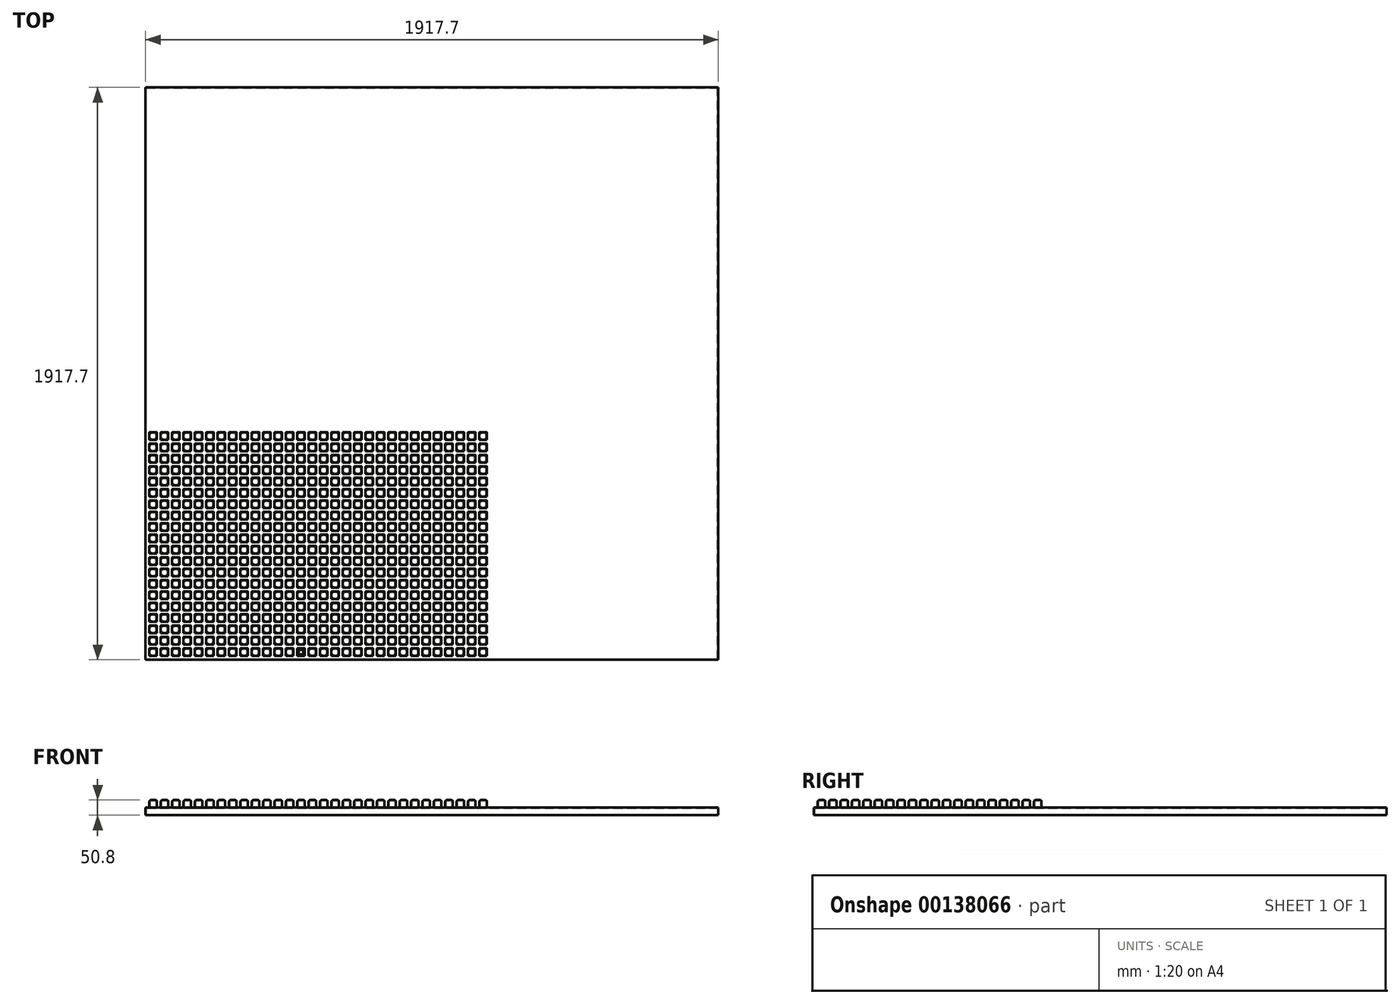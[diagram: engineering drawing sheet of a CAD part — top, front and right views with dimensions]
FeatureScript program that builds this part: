
annotation { "Feature Type Name" : "Feature", "Feature Type Description" : "" }
export const myFeature = defineFeature(function(context is Context, id is Id, definition is map)
    precondition{}
    {
        {
            var Q0;
            Q0=qCreatedBy(makeId("Top.planeOp"),FACE);
            var sketch = newSketch(context, id + "F0", { "sketchPlane" : qUnion([Q0])});
            skLineSegment(sketch, "E0.bottom", {"start": v(0, 0) * mm, "end": v(1917.7, 0) * mm});
            skLineSegment(sketch, "E0.top", {"start": v(0, 1917.7) * mm, "end": v(1917.7, 1917.7) * mm});
            skLineSegment(sketch, "E0.left", {"start": v(0, 0) * mm, "end": v(0, 1917.7) * mm});
            skLineSegment(sketch, "E0.right", {"start": v(1917.7, 0) * mm, "end": v(1917.7, 1917.7) * mm});
            skSolve(sketch);
        }
        {
            var Q0;
            Q0=makeQuery(id+"F0.imprint","IMPRINT",FACE,{"disambiguationData":[TD([[makeQuery(id+"F0.imprint","IMPRINT",EDGE,{"derivedFrom":sQuery(id+"F0.wireOp",EDGE,"E0.bottom")}),1.0]])]});
            extrude(context, id + "F1", {"entities" : qUnion([Q0]), "depth" : 25.4 * mm});
        }
        {
            var Q0;
            Q0=makeQuery(id+"F1.opExtrude","CAP_FACE",FACE,{"disambiguationData":[OSD([sQuery(id+"F0.wireOp",EDGE,"E0.bottom"),sQuery(id+"F0.wireOp",EDGE,"E0.top"),sQuery(id+"F0.wireOp",EDGE,"E0.left"),sQuery(id+"F0.wireOp",EDGE,"E0.right")])],"isStart":false});
            var sketch = newSketch(context, id + "F2", { "sketchPlane" : qUnion([Q0])});
            skLineSegment(sketch, "E1.bottom", {"start": v(12.7, 12.7) * mm, "end": v(38.1, 12.7) * mm});
            skLineSegment(sketch, "E1.top", {"start": v(12.7, 38.1) * mm, "end": v(38.1, 38.1) * mm});
            skLineSegment(sketch, "E1.left", {"start": v(12.7, 12.7) * mm, "end": v(12.7, 38.1) * mm});
            skLineSegment(sketch, "E1.right", {"start": v(38.1, 12.7) * mm, "end": v(38.1, 38.1) * mm});
            skLineSegment(sketch, "E2.0.1.0", {"start": v(38.1, 50.8) * mm, "end": v(38.1, 76.2) * mm});
            skLineSegment(sketch, "E2.0.1.1", {"start": v(12.7, 76.2) * mm, "end": v(38.1, 76.2) * mm});
            skLineSegment(sketch, "E2.0.1.2", {"start": v(12.7, 50.8) * mm, "end": v(38.1, 50.8) * mm});
            skLineSegment(sketch, "E2.0.1.3", {"start": v(12.7, 50.8) * mm, "end": v(12.7, 76.2) * mm});
            skLineSegment(sketch, "E2.0.2.0", {"start": v(38.1, 88.9) * mm, "end": v(38.1, 114.3) * mm});
            skLineSegment(sketch, "E2.0.2.1", {"start": v(12.7, 114.3) * mm, "end": v(38.1, 114.3) * mm});
            skLineSegment(sketch, "E2.0.2.2", {"start": v(12.7, 88.9) * mm, "end": v(38.1, 88.9) * mm});
            skLineSegment(sketch, "E2.0.2.3", {"start": v(12.7, 88.9) * mm, "end": v(12.7, 114.3) * mm});
            skLineSegment(sketch, "E2.0.3.0", {"start": v(38.1, 127) * mm, "end": v(38.1, 152.4) * mm});
            skLineSegment(sketch, "E2.0.3.1", {"start": v(12.7, 152.4) * mm, "end": v(38.1, 152.4) * mm});
            skLineSegment(sketch, "E2.0.3.2", {"start": v(12.7, 127) * mm, "end": v(38.1, 127) * mm});
            skLineSegment(sketch, "E2.0.3.3", {"start": v(12.7, 127) * mm, "end": v(12.7, 152.4) * mm});
            skLineSegment(sketch, "E2.0.4.0", {"start": v(38.1, 165.1) * mm, "end": v(38.1, 190.5) * mm});
            skLineSegment(sketch, "E2.0.4.1", {"start": v(12.7, 190.5) * mm, "end": v(38.1, 190.5) * mm});
            skLineSegment(sketch, "E2.0.4.2", {"start": v(12.7, 165.1) * mm, "end": v(38.1, 165.1) * mm});
            skLineSegment(sketch, "E2.0.4.3", {"start": v(12.7, 165.1) * mm, "end": v(12.7, 190.5) * mm});
            skLineSegment(sketch, "E2.0.5.0", {"start": v(38.1, 203.2) * mm, "end": v(38.1, 228.6) * mm});
            skLineSegment(sketch, "E2.0.5.1", {"start": v(12.7, 228.6) * mm, "end": v(38.1, 228.6) * mm});
            skLineSegment(sketch, "E2.0.5.2", {"start": v(12.7, 203.2) * mm, "end": v(38.1, 203.2) * mm});
            skLineSegment(sketch, "E2.0.5.3", {"start": v(12.7, 203.2) * mm, "end": v(12.7, 228.6) * mm});
            skLineSegment(sketch, "E2.0.6.0", {"start": v(38.1, 241.3) * mm, "end": v(38.1, 266.7) * mm});
            skLineSegment(sketch, "E2.0.6.1", {"start": v(12.7, 266.7) * mm, "end": v(38.1, 266.7) * mm});
            skLineSegment(sketch, "E2.0.6.2", {"start": v(12.7, 241.3) * mm, "end": v(38.1, 241.3) * mm});
            skLineSegment(sketch, "E2.0.6.3", {"start": v(12.7, 241.3) * mm, "end": v(12.7, 266.7) * mm});
            skLineSegment(sketch, "E2.0.7.0", {"start": v(38.1, 279.4) * mm, "end": v(38.1, 304.8) * mm});
            skLineSegment(sketch, "E2.0.7.1", {"start": v(12.7, 304.8) * mm, "end": v(38.1, 304.8) * mm});
            skLineSegment(sketch, "E2.0.7.2", {"start": v(12.7, 279.4) * mm, "end": v(38.1, 279.4) * mm});
            skLineSegment(sketch, "E2.0.7.3", {"start": v(12.7, 279.4) * mm, "end": v(12.7, 304.8) * mm});
            skLineSegment(sketch, "E2.0.8.0", {"start": v(38.1, 317.5) * mm, "end": v(38.1, 342.9) * mm});
            skLineSegment(sketch, "E2.0.8.1", {"start": v(12.7, 342.9) * mm, "end": v(38.1, 342.9) * mm});
            skLineSegment(sketch, "E2.0.8.2", {"start": v(12.7, 317.5) * mm, "end": v(38.1, 317.5) * mm});
            skLineSegment(sketch, "E2.0.8.3", {"start": v(12.7, 317.5) * mm, "end": v(12.7, 342.9) * mm});
            skLineSegment(sketch, "E2.0.9.0", {"start": v(38.1, 355.6) * mm, "end": v(38.1, 381) * mm});
            skLineSegment(sketch, "E2.0.9.1", {"start": v(12.7, 381) * mm, "end": v(38.1, 381) * mm});
            skLineSegment(sketch, "E2.0.9.2", {"start": v(12.7, 355.6) * mm, "end": v(38.1, 355.6) * mm});
            skLineSegment(sketch, "E2.0.9.3", {"start": v(12.7, 355.6) * mm, "end": v(12.7, 381) * mm});
            skLineSegment(sketch, "E2.0.10.0", {"start": v(38.1, 393.7) * mm, "end": v(38.1, 419.1) * mm});
            skLineSegment(sketch, "E2.0.10.1", {"start": v(12.7, 419.1) * mm, "end": v(38.1, 419.1) * mm});
            skLineSegment(sketch, "E2.0.10.2", {"start": v(12.7, 393.7) * mm, "end": v(38.1, 393.7) * mm});
            skLineSegment(sketch, "E2.0.10.3", {"start": v(12.7, 393.7) * mm, "end": v(12.7, 419.1) * mm});
            skLineSegment(sketch, "E2.0.11.0", {"start": v(38.1, 431.8) * mm, "end": v(38.1, 457.2) * mm});
            skLineSegment(sketch, "E2.0.11.1", {"start": v(12.7, 457.2) * mm, "end": v(38.1, 457.2) * mm});
            skLineSegment(sketch, "E2.0.11.2", {"start": v(12.7, 431.8) * mm, "end": v(38.1, 431.8) * mm});
            skLineSegment(sketch, "E2.0.11.3", {"start": v(12.7, 431.8) * mm, "end": v(12.7, 457.2) * mm});
            skLineSegment(sketch, "E2.0.12.0", {"start": v(38.1, 469.9) * mm, "end": v(38.1, 495.3) * mm});
            skLineSegment(sketch, "E2.0.12.1", {"start": v(12.7, 495.3) * mm, "end": v(38.1, 495.3) * mm});
            skLineSegment(sketch, "E2.0.12.2", {"start": v(12.7, 469.9) * mm, "end": v(38.1, 469.9) * mm});
            skLineSegment(sketch, "E2.0.12.3", {"start": v(12.7, 469.9) * mm, "end": v(12.7, 495.3) * mm});
            skLineSegment(sketch, "E2.0.13.0", {"start": v(38.1, 508) * mm, "end": v(38.1, 533.4) * mm});
            skLineSegment(sketch, "E2.0.13.1", {"start": v(12.7, 533.4) * mm, "end": v(38.1, 533.4) * mm});
            skLineSegment(sketch, "E2.0.13.2", {"start": v(12.7, 508) * mm, "end": v(38.1, 508) * mm});
            skLineSegment(sketch, "E2.0.13.3", {"start": v(12.7, 508) * mm, "end": v(12.7, 533.4) * mm});
            skLineSegment(sketch, "E2.0.14.0", {"start": v(38.1, 546.1) * mm, "end": v(38.1, 571.5) * mm});
            skLineSegment(sketch, "E2.0.14.1", {"start": v(12.7, 571.5) * mm, "end": v(38.1, 571.5) * mm});
            skLineSegment(sketch, "E2.0.14.2", {"start": v(12.7, 546.1) * mm, "end": v(38.1, 546.1) * mm});
            skLineSegment(sketch, "E2.0.14.3", {"start": v(12.7, 546.1) * mm, "end": v(12.7, 571.5) * mm});
            skLineSegment(sketch, "E2.0.15.0", {"start": v(38.1, 584.2) * mm, "end": v(38.1, 609.6) * mm});
            skLineSegment(sketch, "E2.0.15.1", {"start": v(12.7, 609.6) * mm, "end": v(38.1, 609.6) * mm});
            skLineSegment(sketch, "E2.0.15.2", {"start": v(12.7, 584.2) * mm, "end": v(38.1, 584.2) * mm});
            skLineSegment(sketch, "E2.0.15.3", {"start": v(12.7, 584.2) * mm, "end": v(12.7, 609.6) * mm});
            skLineSegment(sketch, "E2.0.16.0", {"start": v(38.1, 622.3) * mm, "end": v(38.1, 647.7) * mm});
            skLineSegment(sketch, "E2.0.16.1", {"start": v(12.7, 647.7) * mm, "end": v(38.1, 647.7) * mm});
            skLineSegment(sketch, "E2.0.16.2", {"start": v(12.7, 622.3) * mm, "end": v(38.1, 622.3) * mm});
            skLineSegment(sketch, "E2.0.16.3", {"start": v(12.7, 622.3) * mm, "end": v(12.7, 647.7) * mm});
            skLineSegment(sketch, "E2.0.17.0", {"start": v(38.1, 660.4) * mm, "end": v(38.1, 685.8) * mm});
            skLineSegment(sketch, "E2.0.17.1", {"start": v(12.7, 685.8) * mm, "end": v(38.1, 685.8) * mm});
            skLineSegment(sketch, "E2.0.17.2", {"start": v(12.7, 660.4) * mm, "end": v(38.1, 660.4) * mm});
            skLineSegment(sketch, "E2.0.17.3", {"start": v(12.7, 660.4) * mm, "end": v(12.7, 685.8) * mm});
            skLineSegment(sketch, "E2.0.18.0", {"start": v(38.1, 698.5) * mm, "end": v(38.1, 723.9) * mm});
            skLineSegment(sketch, "E2.0.18.1", {"start": v(12.7, 723.9) * mm, "end": v(38.1, 723.9) * mm});
            skLineSegment(sketch, "E2.0.18.2", {"start": v(12.7, 698.5) * mm, "end": v(38.1, 698.5) * mm});
            skLineSegment(sketch, "E2.0.18.3", {"start": v(12.7, 698.5) * mm, "end": v(12.7, 723.9) * mm});
            skLineSegment(sketch, "E2.0.19.0", {"start": v(38.1, 736.6) * mm, "end": v(38.1, 762) * mm});
            skLineSegment(sketch, "E2.0.19.1", {"start": v(12.7, 762) * mm, "end": v(38.1, 762) * mm});
            skLineSegment(sketch, "E2.0.19.2", {"start": v(12.7, 736.6) * mm, "end": v(38.1, 736.6) * mm});
            skLineSegment(sketch, "E2.0.19.3", {"start": v(12.7, 736.6) * mm, "end": v(12.7, 762) * mm});
            skLineSegment(sketch, "E2.1.0.0", {"start": v(76.2, 12.7) * mm, "end": v(76.2, 38.1) * mm});
            skLineSegment(sketch, "E2.1.0.1", {"start": v(50.8, 38.1) * mm, "end": v(76.2, 38.1) * mm});
            skLineSegment(sketch, "E2.1.0.2", {"start": v(50.8, 12.7) * mm, "end": v(76.2, 12.7) * mm});
            skLineSegment(sketch, "E2.1.0.3", {"start": v(50.8, 12.7) * mm, "end": v(50.8, 38.1) * mm});
            skLineSegment(sketch, "E2.1.1.0", {"start": v(76.2, 50.8) * mm, "end": v(76.2, 76.2) * mm});
            skLineSegment(sketch, "E2.1.1.1", {"start": v(50.8, 76.2) * mm, "end": v(76.2, 76.2) * mm});
            skLineSegment(sketch, "E2.1.1.2", {"start": v(50.8, 50.8) * mm, "end": v(76.2, 50.8) * mm});
            skLineSegment(sketch, "E2.1.1.3", {"start": v(50.8, 50.8) * mm, "end": v(50.8, 76.2) * mm});
            skLineSegment(sketch, "E2.1.2.0", {"start": v(76.2, 88.9) * mm, "end": v(76.2, 114.3) * mm});
            skLineSegment(sketch, "E2.1.2.1", {"start": v(50.8, 114.3) * mm, "end": v(76.2, 114.3) * mm});
            skLineSegment(sketch, "E2.1.2.2", {"start": v(50.8, 88.9) * mm, "end": v(76.2, 88.9) * mm});
            skLineSegment(sketch, "E2.1.2.3", {"start": v(50.8, 88.9) * mm, "end": v(50.8, 114.3) * mm});
            skLineSegment(sketch, "E2.1.3.0", {"start": v(76.2, 127) * mm, "end": v(76.2, 152.4) * mm});
            skLineSegment(sketch, "E2.1.3.1", {"start": v(50.8, 152.4) * mm, "end": v(76.2, 152.4) * mm});
            skLineSegment(sketch, "E2.1.3.2", {"start": v(50.8, 127) * mm, "end": v(76.2, 127) * mm});
            skLineSegment(sketch, "E2.1.3.3", {"start": v(50.8, 127) * mm, "end": v(50.8, 152.4) * mm});
            skLineSegment(sketch, "E2.1.4.0", {"start": v(76.2, 165.1) * mm, "end": v(76.2, 190.5) * mm});
            skLineSegment(sketch, "E2.1.4.1", {"start": v(50.8, 190.5) * mm, "end": v(76.2, 190.5) * mm});
            skLineSegment(sketch, "E2.1.4.2", {"start": v(50.8, 165.1) * mm, "end": v(76.2, 165.1) * mm});
            skLineSegment(sketch, "E2.1.4.3", {"start": v(50.8, 165.1) * mm, "end": v(50.8, 190.5) * mm});
            skLineSegment(sketch, "E2.1.5.0", {"start": v(76.2, 203.2) * mm, "end": v(76.2, 228.6) * mm});
            skLineSegment(sketch, "E2.1.5.1", {"start": v(50.8, 228.6) * mm, "end": v(76.2, 228.6) * mm});
            skLineSegment(sketch, "E2.1.5.2", {"start": v(50.8, 203.2) * mm, "end": v(76.2, 203.2) * mm});
            skLineSegment(sketch, "E2.1.5.3", {"start": v(50.8, 203.2) * mm, "end": v(50.8, 228.6) * mm});
            skLineSegment(sketch, "E2.1.6.0", {"start": v(76.2, 241.3) * mm, "end": v(76.2, 266.7) * mm});
            skLineSegment(sketch, "E2.1.6.1", {"start": v(50.8, 266.7) * mm, "end": v(76.2, 266.7) * mm});
            skLineSegment(sketch, "E2.1.6.2", {"start": v(50.8, 241.3) * mm, "end": v(76.2, 241.3) * mm});
            skLineSegment(sketch, "E2.1.6.3", {"start": v(50.8, 241.3) * mm, "end": v(50.8, 266.7) * mm});
            skLineSegment(sketch, "E2.1.7.0", {"start": v(76.2, 279.4) * mm, "end": v(76.2, 304.8) * mm});
            skLineSegment(sketch, "E2.1.7.1", {"start": v(50.8, 304.8) * mm, "end": v(76.2, 304.8) * mm});
            skLineSegment(sketch, "E2.1.7.2", {"start": v(50.8, 279.4) * mm, "end": v(76.2, 279.4) * mm});
            skLineSegment(sketch, "E2.1.7.3", {"start": v(50.8, 279.4) * mm, "end": v(50.8, 304.8) * mm});
            skLineSegment(sketch, "E2.1.8.0", {"start": v(76.2, 317.5) * mm, "end": v(76.2, 342.9) * mm});
            skLineSegment(sketch, "E2.1.8.1", {"start": v(50.8, 342.9) * mm, "end": v(76.2, 342.9) * mm});
            skLineSegment(sketch, "E2.1.8.2", {"start": v(50.8, 317.5) * mm, "end": v(76.2, 317.5) * mm});
            skLineSegment(sketch, "E2.1.8.3", {"start": v(50.8, 317.5) * mm, "end": v(50.8, 342.9) * mm});
            skLineSegment(sketch, "E2.1.9.0", {"start": v(76.2, 355.6) * mm, "end": v(76.2, 381) * mm});
            skLineSegment(sketch, "E2.1.9.1", {"start": v(50.8, 381) * mm, "end": v(76.2, 381) * mm});
            skLineSegment(sketch, "E2.1.9.2", {"start": v(50.8, 355.6) * mm, "end": v(76.2, 355.6) * mm});
            skLineSegment(sketch, "E2.1.9.3", {"start": v(50.8, 355.6) * mm, "end": v(50.8, 381) * mm});
            skLineSegment(sketch, "E2.1.10.0", {"start": v(76.2, 393.7) * mm, "end": v(76.2, 419.1) * mm});
            skLineSegment(sketch, "E2.1.10.1", {"start": v(50.8, 419.1) * mm, "end": v(76.2, 419.1) * mm});
            skLineSegment(sketch, "E2.1.10.2", {"start": v(50.8, 393.7) * mm, "end": v(76.2, 393.7) * mm});
            skLineSegment(sketch, "E2.1.10.3", {"start": v(50.8, 393.7) * mm, "end": v(50.8, 419.1) * mm});
            skLineSegment(sketch, "E2.1.11.0", {"start": v(76.2, 431.8) * mm, "end": v(76.2, 457.2) * mm});
            skLineSegment(sketch, "E2.1.11.1", {"start": v(50.8, 457.2) * mm, "end": v(76.2, 457.2) * mm});
            skLineSegment(sketch, "E2.1.11.2", {"start": v(50.8, 431.8) * mm, "end": v(76.2, 431.8) * mm});
            skLineSegment(sketch, "E2.1.11.3", {"start": v(50.8, 431.8) * mm, "end": v(50.8, 457.2) * mm});
            skLineSegment(sketch, "E2.1.12.0", {"start": v(76.2, 469.9) * mm, "end": v(76.2, 495.3) * mm});
            skLineSegment(sketch, "E2.1.12.1", {"start": v(50.8, 495.3) * mm, "end": v(76.2, 495.3) * mm});
            skLineSegment(sketch, "E2.1.12.2", {"start": v(50.8, 469.9) * mm, "end": v(76.2, 469.9) * mm});
            skLineSegment(sketch, "E2.1.12.3", {"start": v(50.8, 469.9) * mm, "end": v(50.8, 495.3) * mm});
            skLineSegment(sketch, "E2.1.13.0", {"start": v(76.2, 508) * mm, "end": v(76.2, 533.4) * mm});
            skLineSegment(sketch, "E2.1.13.1", {"start": v(50.8, 533.4) * mm, "end": v(76.2, 533.4) * mm});
            skLineSegment(sketch, "E2.1.13.2", {"start": v(50.8, 508) * mm, "end": v(76.2, 508) * mm});
            skLineSegment(sketch, "E2.1.13.3", {"start": v(50.8, 508) * mm, "end": v(50.8, 533.4) * mm});
            skLineSegment(sketch, "E2.1.14.0", {"start": v(76.2, 546.1) * mm, "end": v(76.2, 571.5) * mm});
            skLineSegment(sketch, "E2.1.14.1", {"start": v(50.8, 571.5) * mm, "end": v(76.2, 571.5) * mm});
            skLineSegment(sketch, "E2.1.14.2", {"start": v(50.8, 546.1) * mm, "end": v(76.2, 546.1) * mm});
            skLineSegment(sketch, "E2.1.14.3", {"start": v(50.8, 546.1) * mm, "end": v(50.8, 571.5) * mm});
            skLineSegment(sketch, "E2.1.15.0", {"start": v(76.2, 584.2) * mm, "end": v(76.2, 609.6) * mm});
            skLineSegment(sketch, "E2.1.15.1", {"start": v(50.8, 609.6) * mm, "end": v(76.2, 609.6) * mm});
            skLineSegment(sketch, "E2.1.15.2", {"start": v(50.8, 584.2) * mm, "end": v(76.2, 584.2) * mm});
            skLineSegment(sketch, "E2.1.15.3", {"start": v(50.8, 584.2) * mm, "end": v(50.8, 609.6) * mm});
            skLineSegment(sketch, "E2.1.16.0", {"start": v(76.2, 622.3) * mm, "end": v(76.2, 647.7) * mm});
            skLineSegment(sketch, "E2.1.16.1", {"start": v(50.8, 647.7) * mm, "end": v(76.2, 647.7) * mm});
            skLineSegment(sketch, "E2.1.16.2", {"start": v(50.8, 622.3) * mm, "end": v(76.2, 622.3) * mm});
            skLineSegment(sketch, "E2.1.16.3", {"start": v(50.8, 622.3) * mm, "end": v(50.8, 647.7) * mm});
            skLineSegment(sketch, "E2.1.17.0", {"start": v(76.2, 660.4) * mm, "end": v(76.2, 685.8) * mm});
            skLineSegment(sketch, "E2.1.17.1", {"start": v(50.8, 685.8) * mm, "end": v(76.2, 685.8) * mm});
            skLineSegment(sketch, "E2.1.17.2", {"start": v(50.8, 660.4) * mm, "end": v(76.2, 660.4) * mm});
            skLineSegment(sketch, "E2.1.17.3", {"start": v(50.8, 660.4) * mm, "end": v(50.8, 685.8) * mm});
            skLineSegment(sketch, "E2.1.18.0", {"start": v(76.2, 698.5) * mm, "end": v(76.2, 723.9) * mm});
            skLineSegment(sketch, "E2.1.18.1", {"start": v(50.8, 723.9) * mm, "end": v(76.2, 723.9) * mm});
            skLineSegment(sketch, "E2.1.18.2", {"start": v(50.8, 698.5) * mm, "end": v(76.2, 698.5) * mm});
            skLineSegment(sketch, "E2.1.18.3", {"start": v(50.8, 698.5) * mm, "end": v(50.8, 723.9) * mm});
            skLineSegment(sketch, "E2.1.19.0", {"start": v(76.2, 736.6) * mm, "end": v(76.2, 762) * mm});
            skLineSegment(sketch, "E2.1.19.1", {"start": v(50.8, 762) * mm, "end": v(76.2, 762) * mm});
            skLineSegment(sketch, "E2.1.19.2", {"start": v(50.8, 736.6) * mm, "end": v(76.2, 736.6) * mm});
            skLineSegment(sketch, "E2.1.19.3", {"start": v(50.8, 736.6) * mm, "end": v(50.8, 762) * mm});
            skLineSegment(sketch, "E2.2.0.0", {"start": v(114.3, 12.7) * mm, "end": v(114.3, 38.1) * mm});
            skLineSegment(sketch, "E2.2.0.1", {"start": v(88.9, 38.1) * mm, "end": v(114.3, 38.1) * mm});
            skLineSegment(sketch, "E2.2.0.2", {"start": v(88.9, 12.7) * mm, "end": v(114.3, 12.7) * mm});
            skLineSegment(sketch, "E2.2.0.3", {"start": v(88.9, 12.7) * mm, "end": v(88.9, 38.1) * mm});
            skLineSegment(sketch, "E2.2.1.0", {"start": v(114.3, 50.8) * mm, "end": v(114.3, 76.2) * mm});
            skLineSegment(sketch, "E2.2.1.1", {"start": v(88.9, 76.2) * mm, "end": v(114.3, 76.2) * mm});
            skLineSegment(sketch, "E2.2.1.2", {"start": v(88.9, 50.8) * mm, "end": v(114.3, 50.8) * mm});
            skLineSegment(sketch, "E2.2.1.3", {"start": v(88.9, 50.8) * mm, "end": v(88.9, 76.2) * mm});
            skLineSegment(sketch, "E2.2.2.0", {"start": v(114.3, 88.9) * mm, "end": v(114.3, 114.3) * mm});
            skLineSegment(sketch, "E2.2.2.1", {"start": v(88.9, 114.3) * mm, "end": v(114.3, 114.3) * mm});
            skLineSegment(sketch, "E2.2.2.2", {"start": v(88.9, 88.9) * mm, "end": v(114.3, 88.9) * mm});
            skLineSegment(sketch, "E2.2.2.3", {"start": v(88.9, 88.9) * mm, "end": v(88.9, 114.3) * mm});
            skLineSegment(sketch, "E2.2.3.0", {"start": v(114.3, 127) * mm, "end": v(114.3, 152.4) * mm});
            skLineSegment(sketch, "E2.2.3.1", {"start": v(88.9, 152.4) * mm, "end": v(114.3, 152.4) * mm});
            skLineSegment(sketch, "E2.2.3.2", {"start": v(88.9, 127) * mm, "end": v(114.3, 127) * mm});
            skLineSegment(sketch, "E2.2.3.3", {"start": v(88.9, 127) * mm, "end": v(88.9, 152.4) * mm});
            skLineSegment(sketch, "E2.2.4.0", {"start": v(114.3, 165.1) * mm, "end": v(114.3, 190.5) * mm});
            skLineSegment(sketch, "E2.2.4.1", {"start": v(88.9, 190.5) * mm, "end": v(114.3, 190.5) * mm});
            skLineSegment(sketch, "E2.2.4.2", {"start": v(88.9, 165.1) * mm, "end": v(114.3, 165.1) * mm});
            skLineSegment(sketch, "E2.2.4.3", {"start": v(88.9, 165.1) * mm, "end": v(88.9, 190.5) * mm});
            skLineSegment(sketch, "E2.2.5.0", {"start": v(114.3, 203.2) * mm, "end": v(114.3, 228.6) * mm});
            skLineSegment(sketch, "E2.2.5.1", {"start": v(88.9, 228.6) * mm, "end": v(114.3, 228.6) * mm});
            skLineSegment(sketch, "E2.2.5.2", {"start": v(88.9, 203.2) * mm, "end": v(114.3, 203.2) * mm});
            skLineSegment(sketch, "E2.2.5.3", {"start": v(88.9, 203.2) * mm, "end": v(88.9, 228.6) * mm});
            skLineSegment(sketch, "E2.2.6.0", {"start": v(114.3, 241.3) * mm, "end": v(114.3, 266.7) * mm});
            skLineSegment(sketch, "E2.2.6.1", {"start": v(88.9, 266.7) * mm, "end": v(114.3, 266.7) * mm});
            skLineSegment(sketch, "E2.2.6.2", {"start": v(88.9, 241.3) * mm, "end": v(114.3, 241.3) * mm});
            skLineSegment(sketch, "E2.2.6.3", {"start": v(88.9, 241.3) * mm, "end": v(88.9, 266.7) * mm});
            skLineSegment(sketch, "E2.2.7.0", {"start": v(114.3, 279.4) * mm, "end": v(114.3, 304.8) * mm});
            skLineSegment(sketch, "E2.2.7.1", {"start": v(88.9, 304.8) * mm, "end": v(114.3, 304.8) * mm});
            skLineSegment(sketch, "E2.2.7.2", {"start": v(88.9, 279.4) * mm, "end": v(114.3, 279.4) * mm});
            skLineSegment(sketch, "E2.2.7.3", {"start": v(88.9, 279.4) * mm, "end": v(88.9, 304.8) * mm});
            skLineSegment(sketch, "E2.2.8.0", {"start": v(114.3, 317.5) * mm, "end": v(114.3, 342.9) * mm});
            skLineSegment(sketch, "E2.2.8.1", {"start": v(88.9, 342.9) * mm, "end": v(114.3, 342.9) * mm});
            skLineSegment(sketch, "E2.2.8.2", {"start": v(88.9, 317.5) * mm, "end": v(114.3, 317.5) * mm});
            skLineSegment(sketch, "E2.2.8.3", {"start": v(88.9, 317.5) * mm, "end": v(88.9, 342.9) * mm});
            skLineSegment(sketch, "E2.2.9.0", {"start": v(114.3, 355.6) * mm, "end": v(114.3, 381) * mm});
            skLineSegment(sketch, "E2.2.9.1", {"start": v(88.9, 381) * mm, "end": v(114.3, 381) * mm});
            skLineSegment(sketch, "E2.2.9.2", {"start": v(88.9, 355.6) * mm, "end": v(114.3, 355.6) * mm});
            skLineSegment(sketch, "E2.2.9.3", {"start": v(88.9, 355.6) * mm, "end": v(88.9, 381) * mm});
            skLineSegment(sketch, "E2.2.10.0", {"start": v(114.3, 393.7) * mm, "end": v(114.3, 419.1) * mm});
            skLineSegment(sketch, "E2.2.10.1", {"start": v(88.9, 419.1) * mm, "end": v(114.3, 419.1) * mm});
            skLineSegment(sketch, "E2.2.10.2", {"start": v(88.9, 393.7) * mm, "end": v(114.3, 393.7) * mm});
            skLineSegment(sketch, "E2.2.10.3", {"start": v(88.9, 393.7) * mm, "end": v(88.9, 419.1) * mm});
            skLineSegment(sketch, "E2.2.11.0", {"start": v(114.3, 431.8) * mm, "end": v(114.3, 457.2) * mm});
            skLineSegment(sketch, "E2.2.11.1", {"start": v(88.9, 457.2) * mm, "end": v(114.3, 457.2) * mm});
            skLineSegment(sketch, "E2.2.11.2", {"start": v(88.9, 431.8) * mm, "end": v(114.3, 431.8) * mm});
            skLineSegment(sketch, "E2.2.11.3", {"start": v(88.9, 431.8) * mm, "end": v(88.9, 457.2) * mm});
            skLineSegment(sketch, "E2.2.12.0", {"start": v(114.3, 469.9) * mm, "end": v(114.3, 495.3) * mm});
            skLineSegment(sketch, "E2.2.12.1", {"start": v(88.9, 495.3) * mm, "end": v(114.3, 495.3) * mm});
            skLineSegment(sketch, "E2.2.12.2", {"start": v(88.9, 469.9) * mm, "end": v(114.3, 469.9) * mm});
            skLineSegment(sketch, "E2.2.12.3", {"start": v(88.9, 469.9) * mm, "end": v(88.9, 495.3) * mm});
            skLineSegment(sketch, "E2.2.13.0", {"start": v(114.3, 508) * mm, "end": v(114.3, 533.4) * mm});
            skLineSegment(sketch, "E2.2.13.1", {"start": v(88.9, 533.4) * mm, "end": v(114.3, 533.4) * mm});
            skLineSegment(sketch, "E2.2.13.2", {"start": v(88.9, 508) * mm, "end": v(114.3, 508) * mm});
            skLineSegment(sketch, "E2.2.13.3", {"start": v(88.9, 508) * mm, "end": v(88.9, 533.4) * mm});
            skLineSegment(sketch, "E2.2.14.0", {"start": v(114.3, 546.1) * mm, "end": v(114.3, 571.5) * mm});
            skLineSegment(sketch, "E2.2.14.1", {"start": v(88.9, 571.5) * mm, "end": v(114.3, 571.5) * mm});
            skLineSegment(sketch, "E2.2.14.2", {"start": v(88.9, 546.1) * mm, "end": v(114.3, 546.1) * mm});
            skLineSegment(sketch, "E2.2.14.3", {"start": v(88.9, 546.1) * mm, "end": v(88.9, 571.5) * mm});
            skLineSegment(sketch, "E2.2.15.0", {"start": v(114.3, 584.2) * mm, "end": v(114.3, 609.6) * mm});
            skLineSegment(sketch, "E2.2.15.1", {"start": v(88.9, 609.6) * mm, "end": v(114.3, 609.6) * mm});
            skLineSegment(sketch, "E2.2.15.2", {"start": v(88.9, 584.2) * mm, "end": v(114.3, 584.2) * mm});
            skLineSegment(sketch, "E2.2.15.3", {"start": v(88.9, 584.2) * mm, "end": v(88.9, 609.6) * mm});
            skLineSegment(sketch, "E2.2.16.0", {"start": v(114.3, 622.3) * mm, "end": v(114.3, 647.7) * mm});
            skLineSegment(sketch, "E2.2.16.1", {"start": v(88.9, 647.7) * mm, "end": v(114.3, 647.7) * mm});
            skLineSegment(sketch, "E2.2.16.2", {"start": v(88.9, 622.3) * mm, "end": v(114.3, 622.3) * mm});
            skLineSegment(sketch, "E2.2.16.3", {"start": v(88.9, 622.3) * mm, "end": v(88.9, 647.7) * mm});
            skLineSegment(sketch, "E2.2.17.0", {"start": v(114.3, 660.4) * mm, "end": v(114.3, 685.8) * mm});
            skLineSegment(sketch, "E2.2.17.1", {"start": v(88.9, 685.8) * mm, "end": v(114.3, 685.8) * mm});
            skLineSegment(sketch, "E2.2.17.2", {"start": v(88.9, 660.4) * mm, "end": v(114.3, 660.4) * mm});
            skLineSegment(sketch, "E2.2.17.3", {"start": v(88.9, 660.4) * mm, "end": v(88.9, 685.8) * mm});
            skLineSegment(sketch, "E2.2.18.0", {"start": v(114.3, 698.5) * mm, "end": v(114.3, 723.9) * mm});
            skLineSegment(sketch, "E2.2.18.1", {"start": v(88.9, 723.9) * mm, "end": v(114.3, 723.9) * mm});
            skLineSegment(sketch, "E2.2.18.2", {"start": v(88.9, 698.5) * mm, "end": v(114.3, 698.5) * mm});
            skLineSegment(sketch, "E2.2.18.3", {"start": v(88.9, 698.5) * mm, "end": v(88.9, 723.9) * mm});
            skLineSegment(sketch, "E2.2.19.0", {"start": v(114.3, 736.6) * mm, "end": v(114.3, 762) * mm});
            skLineSegment(sketch, "E2.2.19.1", {"start": v(88.9, 762) * mm, "end": v(114.3, 762) * mm});
            skLineSegment(sketch, "E2.2.19.2", {"start": v(88.9, 736.6) * mm, "end": v(114.3, 736.6) * mm});
            skLineSegment(sketch, "E2.2.19.3", {"start": v(88.9, 736.6) * mm, "end": v(88.9, 762) * mm});
            skLineSegment(sketch, "E2.3.0.0", {"start": v(152.4, 12.7) * mm, "end": v(152.4, 38.1) * mm});
            skLineSegment(sketch, "E2.3.0.1", {"start": v(127, 38.1) * mm, "end": v(152.4, 38.1) * mm});
            skLineSegment(sketch, "E2.3.0.2", {"start": v(127, 12.7) * mm, "end": v(152.4, 12.7) * mm});
            skLineSegment(sketch, "E2.3.0.3", {"start": v(127, 12.7) * mm, "end": v(127, 38.1) * mm});
            skLineSegment(sketch, "E2.3.1.0", {"start": v(152.4, 50.8) * mm, "end": v(152.4, 76.2) * mm});
            skLineSegment(sketch, "E2.3.1.1", {"start": v(127, 76.2) * mm, "end": v(152.4, 76.2) * mm});
            skLineSegment(sketch, "E2.3.1.2", {"start": v(127, 50.8) * mm, "end": v(152.4, 50.8) * mm});
            skLineSegment(sketch, "E2.3.1.3", {"start": v(127, 50.8) * mm, "end": v(127, 76.2) * mm});
            skLineSegment(sketch, "E2.3.2.0", {"start": v(152.4, 88.9) * mm, "end": v(152.4, 114.3) * mm});
            skLineSegment(sketch, "E2.3.2.1", {"start": v(127, 114.3) * mm, "end": v(152.4, 114.3) * mm});
            skLineSegment(sketch, "E2.3.2.2", {"start": v(127, 88.9) * mm, "end": v(152.4, 88.9) * mm});
            skLineSegment(sketch, "E2.3.2.3", {"start": v(127, 88.9) * mm, "end": v(127, 114.3) * mm});
            skLineSegment(sketch, "E2.3.3.0", {"start": v(152.4, 127) * mm, "end": v(152.4, 152.4) * mm});
            skLineSegment(sketch, "E2.3.3.1", {"start": v(127, 152.4) * mm, "end": v(152.4, 152.4) * mm});
            skLineSegment(sketch, "E2.3.3.2", {"start": v(127, 127) * mm, "end": v(152.4, 127) * mm});
            skLineSegment(sketch, "E2.3.3.3", {"start": v(127, 127) * mm, "end": v(127, 152.4) * mm});
            skLineSegment(sketch, "E2.3.4.0", {"start": v(152.4, 165.1) * mm, "end": v(152.4, 190.5) * mm});
            skLineSegment(sketch, "E2.3.4.1", {"start": v(127, 190.5) * mm, "end": v(152.4, 190.5) * mm});
            skLineSegment(sketch, "E2.3.4.2", {"start": v(127, 165.1) * mm, "end": v(152.4, 165.1) * mm});
            skLineSegment(sketch, "E2.3.4.3", {"start": v(127, 165.1) * mm, "end": v(127, 190.5) * mm});
            skLineSegment(sketch, "E2.3.5.0", {"start": v(152.4, 203.2) * mm, "end": v(152.4, 228.6) * mm});
            skLineSegment(sketch, "E2.3.5.1", {"start": v(127, 228.6) * mm, "end": v(152.4, 228.6) * mm});
            skLineSegment(sketch, "E2.3.5.2", {"start": v(127, 203.2) * mm, "end": v(152.4, 203.2) * mm});
            skLineSegment(sketch, "E2.3.5.3", {"start": v(127, 203.2) * mm, "end": v(127, 228.6) * mm});
            skLineSegment(sketch, "E2.3.6.0", {"start": v(152.4, 241.3) * mm, "end": v(152.4, 266.7) * mm});
            skLineSegment(sketch, "E2.3.6.1", {"start": v(127, 266.7) * mm, "end": v(152.4, 266.7) * mm});
            skLineSegment(sketch, "E2.3.6.2", {"start": v(127, 241.3) * mm, "end": v(152.4, 241.3) * mm});
            skLineSegment(sketch, "E2.3.6.3", {"start": v(127, 241.3) * mm, "end": v(127, 266.7) * mm});
            skLineSegment(sketch, "E2.3.7.0", {"start": v(152.4, 279.4) * mm, "end": v(152.4, 304.8) * mm});
            skLineSegment(sketch, "E2.3.7.1", {"start": v(127, 304.8) * mm, "end": v(152.4, 304.8) * mm});
            skLineSegment(sketch, "E2.3.7.2", {"start": v(127, 279.4) * mm, "end": v(152.4, 279.4) * mm});
            skLineSegment(sketch, "E2.3.7.3", {"start": v(127, 279.4) * mm, "end": v(127, 304.8) * mm});
            skLineSegment(sketch, "E2.3.8.0", {"start": v(152.4, 317.5) * mm, "end": v(152.4, 342.9) * mm});
            skLineSegment(sketch, "E2.3.8.1", {"start": v(127, 342.9) * mm, "end": v(152.4, 342.9) * mm});
            skLineSegment(sketch, "E2.3.8.2", {"start": v(127, 317.5) * mm, "end": v(152.4, 317.5) * mm});
            skLineSegment(sketch, "E2.3.8.3", {"start": v(127, 317.5) * mm, "end": v(127, 342.9) * mm});
            skLineSegment(sketch, "E2.3.9.0", {"start": v(152.4, 355.6) * mm, "end": v(152.4, 381) * mm});
            skLineSegment(sketch, "E2.3.9.1", {"start": v(127, 381) * mm, "end": v(152.4, 381) * mm});
            skLineSegment(sketch, "E2.3.9.2", {"start": v(127, 355.6) * mm, "end": v(152.4, 355.6) * mm});
            skLineSegment(sketch, "E2.3.9.3", {"start": v(127, 355.6) * mm, "end": v(127, 381) * mm});
            skLineSegment(sketch, "E2.3.10.0", {"start": v(152.4, 393.7) * mm, "end": v(152.4, 419.1) * mm});
            skLineSegment(sketch, "E2.3.10.1", {"start": v(127, 419.1) * mm, "end": v(152.4, 419.1) * mm});
            skLineSegment(sketch, "E2.3.10.2", {"start": v(127, 393.7) * mm, "end": v(152.4, 393.7) * mm});
            skLineSegment(sketch, "E2.3.10.3", {"start": v(127, 393.7) * mm, "end": v(127, 419.1) * mm});
            skLineSegment(sketch, "E2.3.11.0", {"start": v(152.4, 431.8) * mm, "end": v(152.4, 457.2) * mm});
            skLineSegment(sketch, "E2.3.11.1", {"start": v(127, 457.2) * mm, "end": v(152.4, 457.2) * mm});
            skLineSegment(sketch, "E2.3.11.2", {"start": v(127, 431.8) * mm, "end": v(152.4, 431.8) * mm});
            skLineSegment(sketch, "E2.3.11.3", {"start": v(127, 431.8) * mm, "end": v(127, 457.2) * mm});
            skLineSegment(sketch, "E2.3.12.0", {"start": v(152.4, 469.9) * mm, "end": v(152.4, 495.3) * mm});
            skLineSegment(sketch, "E2.3.12.1", {"start": v(127, 495.3) * mm, "end": v(152.4, 495.3) * mm});
            skLineSegment(sketch, "E2.3.12.2", {"start": v(127, 469.9) * mm, "end": v(152.4, 469.9) * mm});
            skLineSegment(sketch, "E2.3.12.3", {"start": v(127, 469.9) * mm, "end": v(127, 495.3) * mm});
            skLineSegment(sketch, "E2.3.13.0", {"start": v(152.4, 508) * mm, "end": v(152.4, 533.4) * mm});
            skLineSegment(sketch, "E2.3.13.1", {"start": v(127, 533.4) * mm, "end": v(152.4, 533.4) * mm});
            skLineSegment(sketch, "E2.3.13.2", {"start": v(127, 508) * mm, "end": v(152.4, 508) * mm});
            skLineSegment(sketch, "E2.3.13.3", {"start": v(127, 508) * mm, "end": v(127, 533.4) * mm});
            skLineSegment(sketch, "E2.3.14.0", {"start": v(152.4, 546.1) * mm, "end": v(152.4, 571.5) * mm});
            skLineSegment(sketch, "E2.3.14.1", {"start": v(127, 571.5) * mm, "end": v(152.4, 571.5) * mm});
            skLineSegment(sketch, "E2.3.14.2", {"start": v(127, 546.1) * mm, "end": v(152.4, 546.1) * mm});
            skLineSegment(sketch, "E2.3.14.3", {"start": v(127, 546.1) * mm, "end": v(127, 571.5) * mm});
            skLineSegment(sketch, "E2.3.15.0", {"start": v(152.4, 584.2) * mm, "end": v(152.4, 609.6) * mm});
            skLineSegment(sketch, "E2.3.15.1", {"start": v(127, 609.6) * mm, "end": v(152.4, 609.6) * mm});
            skLineSegment(sketch, "E2.3.15.2", {"start": v(127, 584.2) * mm, "end": v(152.4, 584.2) * mm});
            skLineSegment(sketch, "E2.3.15.3", {"start": v(127, 584.2) * mm, "end": v(127, 609.6) * mm});
            skLineSegment(sketch, "E2.3.16.0", {"start": v(152.4, 622.3) * mm, "end": v(152.4, 647.7) * mm});
            skLineSegment(sketch, "E2.3.16.1", {"start": v(127, 647.7) * mm, "end": v(152.4, 647.7) * mm});
            skLineSegment(sketch, "E2.3.16.2", {"start": v(127, 622.3) * mm, "end": v(152.4, 622.3) * mm});
            skLineSegment(sketch, "E2.3.16.3", {"start": v(127, 622.3) * mm, "end": v(127, 647.7) * mm});
            skLineSegment(sketch, "E2.3.17.0", {"start": v(152.4, 660.4) * mm, "end": v(152.4, 685.8) * mm});
            skLineSegment(sketch, "E2.3.17.1", {"start": v(127, 685.8) * mm, "end": v(152.4, 685.8) * mm});
            skLineSegment(sketch, "E2.3.17.2", {"start": v(127, 660.4) * mm, "end": v(152.4, 660.4) * mm});
            skLineSegment(sketch, "E2.3.17.3", {"start": v(127, 660.4) * mm, "end": v(127, 685.8) * mm});
            skLineSegment(sketch, "E2.3.18.0", {"start": v(152.4, 698.5) * mm, "end": v(152.4, 723.9) * mm});
            skLineSegment(sketch, "E2.3.18.1", {"start": v(127, 723.9) * mm, "end": v(152.4, 723.9) * mm});
            skLineSegment(sketch, "E2.3.18.2", {"start": v(127, 698.5) * mm, "end": v(152.4, 698.5) * mm});
            skLineSegment(sketch, "E2.3.18.3", {"start": v(127, 698.5) * mm, "end": v(127, 723.9) * mm});
            skLineSegment(sketch, "E2.3.19.0", {"start": v(152.4, 736.6) * mm, "end": v(152.4, 762) * mm});
            skLineSegment(sketch, "E2.3.19.1", {"start": v(127, 762) * mm, "end": v(152.4, 762) * mm});
            skLineSegment(sketch, "E2.3.19.2", {"start": v(127, 736.6) * mm, "end": v(152.4, 736.6) * mm});
            skLineSegment(sketch, "E2.3.19.3", {"start": v(127, 736.6) * mm, "end": v(127, 762) * mm});
            skLineSegment(sketch, "E2.4.0.0", {"start": v(190.5, 12.7) * mm, "end": v(190.5, 38.1) * mm});
            skLineSegment(sketch, "E2.4.0.1", {"start": v(165.1, 38.1) * mm, "end": v(190.5, 38.1) * mm});
            skLineSegment(sketch, "E2.4.0.2", {"start": v(165.1, 12.7) * mm, "end": v(190.5, 12.7) * mm});
            skLineSegment(sketch, "E2.4.0.3", {"start": v(165.1, 12.7) * mm, "end": v(165.1, 38.1) * mm});
            skLineSegment(sketch, "E2.4.1.0", {"start": v(190.5, 50.8) * mm, "end": v(190.5, 76.2) * mm});
            skLineSegment(sketch, "E2.4.1.1", {"start": v(165.1, 76.2) * mm, "end": v(190.5, 76.2) * mm});
            skLineSegment(sketch, "E2.4.1.2", {"start": v(165.1, 50.8) * mm, "end": v(190.5, 50.8) * mm});
            skLineSegment(sketch, "E2.4.1.3", {"start": v(165.1, 50.8) * mm, "end": v(165.1, 76.2) * mm});
            skLineSegment(sketch, "E2.4.2.0", {"start": v(190.5, 88.9) * mm, "end": v(190.5, 114.3) * mm});
            skLineSegment(sketch, "E2.4.2.1", {"start": v(165.1, 114.3) * mm, "end": v(190.5, 114.3) * mm});
            skLineSegment(sketch, "E2.4.2.2", {"start": v(165.1, 88.9) * mm, "end": v(190.5, 88.9) * mm});
            skLineSegment(sketch, "E2.4.2.3", {"start": v(165.1, 88.9) * mm, "end": v(165.1, 114.3) * mm});
            skLineSegment(sketch, "E2.4.3.0", {"start": v(190.5, 127) * mm, "end": v(190.5, 152.4) * mm});
            skLineSegment(sketch, "E2.4.3.1", {"start": v(165.1, 152.4) * mm, "end": v(190.5, 152.4) * mm});
            skLineSegment(sketch, "E2.4.3.2", {"start": v(165.1, 127) * mm, "end": v(190.5, 127) * mm});
            skLineSegment(sketch, "E2.4.3.3", {"start": v(165.1, 127) * mm, "end": v(165.1, 152.4) * mm});
            skLineSegment(sketch, "E2.4.4.0", {"start": v(190.5, 165.1) * mm, "end": v(190.5, 190.5) * mm});
            skLineSegment(sketch, "E2.4.4.1", {"start": v(165.1, 190.5) * mm, "end": v(190.5, 190.5) * mm});
            skLineSegment(sketch, "E2.4.4.2", {"start": v(165.1, 165.1) * mm, "end": v(190.5, 165.1) * mm});
            skLineSegment(sketch, "E2.4.4.3", {"start": v(165.1, 165.1) * mm, "end": v(165.1, 190.5) * mm});
            skLineSegment(sketch, "E2.4.5.0", {"start": v(190.5, 203.2) * mm, "end": v(190.5, 228.6) * mm});
            skLineSegment(sketch, "E2.4.5.1", {"start": v(165.1, 228.6) * mm, "end": v(190.5, 228.6) * mm});
            skLineSegment(sketch, "E2.4.5.2", {"start": v(165.1, 203.2) * mm, "end": v(190.5, 203.2) * mm});
            skLineSegment(sketch, "E2.4.5.3", {"start": v(165.1, 203.2) * mm, "end": v(165.1, 228.6) * mm});
            skLineSegment(sketch, "E2.4.6.0", {"start": v(190.5, 241.3) * mm, "end": v(190.5, 266.7) * mm});
            skLineSegment(sketch, "E2.4.6.1", {"start": v(165.1, 266.7) * mm, "end": v(190.5, 266.7) * mm});
            skLineSegment(sketch, "E2.4.6.2", {"start": v(165.1, 241.3) * mm, "end": v(190.5, 241.3) * mm});
            skLineSegment(sketch, "E2.4.6.3", {"start": v(165.1, 241.3) * mm, "end": v(165.1, 266.7) * mm});
            skLineSegment(sketch, "E2.4.7.0", {"start": v(190.5, 279.4) * mm, "end": v(190.5, 304.8) * mm});
            skLineSegment(sketch, "E2.4.7.1", {"start": v(165.1, 304.8) * mm, "end": v(190.5, 304.8) * mm});
            skLineSegment(sketch, "E2.4.7.2", {"start": v(165.1, 279.4) * mm, "end": v(190.5, 279.4) * mm});
            skLineSegment(sketch, "E2.4.7.3", {"start": v(165.1, 279.4) * mm, "end": v(165.1, 304.8) * mm});
            skLineSegment(sketch, "E2.4.8.0", {"start": v(190.5, 317.5) * mm, "end": v(190.5, 342.9) * mm});
            skLineSegment(sketch, "E2.4.8.1", {"start": v(165.1, 342.9) * mm, "end": v(190.5, 342.9) * mm});
            skLineSegment(sketch, "E2.4.8.2", {"start": v(165.1, 317.5) * mm, "end": v(190.5, 317.5) * mm});
            skLineSegment(sketch, "E2.4.8.3", {"start": v(165.1, 317.5) * mm, "end": v(165.1, 342.9) * mm});
            skLineSegment(sketch, "E2.4.9.0", {"start": v(190.5, 355.6) * mm, "end": v(190.5, 381) * mm});
            skLineSegment(sketch, "E2.4.9.1", {"start": v(165.1, 381) * mm, "end": v(190.5, 381) * mm});
            skLineSegment(sketch, "E2.4.9.2", {"start": v(165.1, 355.6) * mm, "end": v(190.5, 355.6) * mm});
            skLineSegment(sketch, "E2.4.9.3", {"start": v(165.1, 355.6) * mm, "end": v(165.1, 381) * mm});
            skLineSegment(sketch, "E2.4.10.0", {"start": v(190.5, 393.7) * mm, "end": v(190.5, 419.1) * mm});
            skLineSegment(sketch, "E2.4.10.1", {"start": v(165.1, 419.1) * mm, "end": v(190.5, 419.1) * mm});
            skLineSegment(sketch, "E2.4.10.2", {"start": v(165.1, 393.7) * mm, "end": v(190.5, 393.7) * mm});
            skLineSegment(sketch, "E2.4.10.3", {"start": v(165.1, 393.7) * mm, "end": v(165.1, 419.1) * mm});
            skLineSegment(sketch, "E2.4.11.0", {"start": v(190.5, 431.8) * mm, "end": v(190.5, 457.2) * mm});
            skLineSegment(sketch, "E2.4.11.1", {"start": v(165.1, 457.2) * mm, "end": v(190.5, 457.2) * mm});
            skLineSegment(sketch, "E2.4.11.2", {"start": v(165.1, 431.8) * mm, "end": v(190.5, 431.8) * mm});
            skLineSegment(sketch, "E2.4.11.3", {"start": v(165.1, 431.8) * mm, "end": v(165.1, 457.2) * mm});
            skLineSegment(sketch, "E2.4.12.0", {"start": v(190.5, 469.9) * mm, "end": v(190.5, 495.3) * mm});
            skLineSegment(sketch, "E2.4.12.1", {"start": v(165.1, 495.3) * mm, "end": v(190.5, 495.3) * mm});
            skLineSegment(sketch, "E2.4.12.2", {"start": v(165.1, 469.9) * mm, "end": v(190.5, 469.9) * mm});
            skLineSegment(sketch, "E2.4.12.3", {"start": v(165.1, 469.9) * mm, "end": v(165.1, 495.3) * mm});
            skLineSegment(sketch, "E2.4.13.0", {"start": v(190.5, 508) * mm, "end": v(190.5, 533.4) * mm});
            skLineSegment(sketch, "E2.4.13.1", {"start": v(165.1, 533.4) * mm, "end": v(190.5, 533.4) * mm});
            skLineSegment(sketch, "E2.4.13.2", {"start": v(165.1, 508) * mm, "end": v(190.5, 508) * mm});
            skLineSegment(sketch, "E2.4.13.3", {"start": v(165.1, 508) * mm, "end": v(165.1, 533.4) * mm});
            skLineSegment(sketch, "E2.4.14.0", {"start": v(190.5, 546.1) * mm, "end": v(190.5, 571.5) * mm});
            skLineSegment(sketch, "E2.4.14.1", {"start": v(165.1, 571.5) * mm, "end": v(190.5, 571.5) * mm});
            skLineSegment(sketch, "E2.4.14.2", {"start": v(165.1, 546.1) * mm, "end": v(190.5, 546.1) * mm});
            skLineSegment(sketch, "E2.4.14.3", {"start": v(165.1, 546.1) * mm, "end": v(165.1, 571.5) * mm});
            skLineSegment(sketch, "E2.4.15.0", {"start": v(190.5, 584.2) * mm, "end": v(190.5, 609.6) * mm});
            skLineSegment(sketch, "E2.4.15.1", {"start": v(165.1, 609.6) * mm, "end": v(190.5, 609.6) * mm});
            skLineSegment(sketch, "E2.4.15.2", {"start": v(165.1, 584.2) * mm, "end": v(190.5, 584.2) * mm});
            skLineSegment(sketch, "E2.4.15.3", {"start": v(165.1, 584.2) * mm, "end": v(165.1, 609.6) * mm});
            skLineSegment(sketch, "E2.4.16.0", {"start": v(190.5, 622.3) * mm, "end": v(190.5, 647.7) * mm});
            skLineSegment(sketch, "E2.4.16.1", {"start": v(165.1, 647.7) * mm, "end": v(190.5, 647.7) * mm});
            skLineSegment(sketch, "E2.4.16.2", {"start": v(165.1, 622.3) * mm, "end": v(190.5, 622.3) * mm});
            skLineSegment(sketch, "E2.4.16.3", {"start": v(165.1, 622.3) * mm, "end": v(165.1, 647.7) * mm});
            skLineSegment(sketch, "E2.4.17.0", {"start": v(190.5, 660.4) * mm, "end": v(190.5, 685.8) * mm});
            skLineSegment(sketch, "E2.4.17.1", {"start": v(165.1, 685.8) * mm, "end": v(190.5, 685.8) * mm});
            skLineSegment(sketch, "E2.4.17.2", {"start": v(165.1, 660.4) * mm, "end": v(190.5, 660.4) * mm});
            skLineSegment(sketch, "E2.4.17.3", {"start": v(165.1, 660.4) * mm, "end": v(165.1, 685.8) * mm});
            skLineSegment(sketch, "E2.4.18.0", {"start": v(190.5, 698.5) * mm, "end": v(190.5, 723.9) * mm});
            skLineSegment(sketch, "E2.4.18.1", {"start": v(165.1, 723.9) * mm, "end": v(190.5, 723.9) * mm});
            skLineSegment(sketch, "E2.4.18.2", {"start": v(165.1, 698.5) * mm, "end": v(190.5, 698.5) * mm});
            skLineSegment(sketch, "E2.4.18.3", {"start": v(165.1, 698.5) * mm, "end": v(165.1, 723.9) * mm});
            skLineSegment(sketch, "E2.4.19.0", {"start": v(190.5, 736.6) * mm, "end": v(190.5, 762) * mm});
            skLineSegment(sketch, "E2.4.19.1", {"start": v(165.1, 762) * mm, "end": v(190.5, 762) * mm});
            skLineSegment(sketch, "E2.4.19.2", {"start": v(165.1, 736.6) * mm, "end": v(190.5, 736.6) * mm});
            skLineSegment(sketch, "E2.4.19.3", {"start": v(165.1, 736.6) * mm, "end": v(165.1, 762) * mm});
            skLineSegment(sketch, "E2.5.0.0", {"start": v(228.6, 12.7) * mm, "end": v(228.6, 38.1) * mm});
            skLineSegment(sketch, "E2.5.0.1", {"start": v(203.2, 38.1) * mm, "end": v(228.6, 38.1) * mm});
            skLineSegment(sketch, "E2.5.0.2", {"start": v(203.2, 12.7) * mm, "end": v(228.6, 12.7) * mm});
            skLineSegment(sketch, "E2.5.0.3", {"start": v(203.2, 12.7) * mm, "end": v(203.2, 38.1) * mm});
            skLineSegment(sketch, "E2.5.1.0", {"start": v(228.6, 50.8) * mm, "end": v(228.6, 76.2) * mm});
            skLineSegment(sketch, "E2.5.1.1", {"start": v(203.2, 76.2) * mm, "end": v(228.6, 76.2) * mm});
            skLineSegment(sketch, "E2.5.1.2", {"start": v(203.2, 50.8) * mm, "end": v(228.6, 50.8) * mm});
            skLineSegment(sketch, "E2.5.1.3", {"start": v(203.2, 50.8) * mm, "end": v(203.2, 76.2) * mm});
            skLineSegment(sketch, "E2.5.2.0", {"start": v(228.6, 88.9) * mm, "end": v(228.6, 114.3) * mm});
            skLineSegment(sketch, "E2.5.2.1", {"start": v(203.2, 114.3) * mm, "end": v(228.6, 114.3) * mm});
            skLineSegment(sketch, "E2.5.2.2", {"start": v(203.2, 88.9) * mm, "end": v(228.6, 88.9) * mm});
            skLineSegment(sketch, "E2.5.2.3", {"start": v(203.2, 88.9) * mm, "end": v(203.2, 114.3) * mm});
            skLineSegment(sketch, "E2.5.3.0", {"start": v(228.6, 127) * mm, "end": v(228.6, 152.4) * mm});
            skLineSegment(sketch, "E2.5.3.1", {"start": v(203.2, 152.4) * mm, "end": v(228.6, 152.4) * mm});
            skLineSegment(sketch, "E2.5.3.2", {"start": v(203.2, 127) * mm, "end": v(228.6, 127) * mm});
            skLineSegment(sketch, "E2.5.3.3", {"start": v(203.2, 127) * mm, "end": v(203.2, 152.4) * mm});
            skLineSegment(sketch, "E2.5.4.0", {"start": v(228.6, 165.1) * mm, "end": v(228.6, 190.5) * mm});
            skLineSegment(sketch, "E2.5.4.1", {"start": v(203.2, 190.5) * mm, "end": v(228.6, 190.5) * mm});
            skLineSegment(sketch, "E2.5.4.2", {"start": v(203.2, 165.1) * mm, "end": v(228.6, 165.1) * mm});
            skLineSegment(sketch, "E2.5.4.3", {"start": v(203.2, 165.1) * mm, "end": v(203.2, 190.5) * mm});
            skLineSegment(sketch, "E2.5.5.0", {"start": v(228.6, 203.2) * mm, "end": v(228.6, 228.6) * mm});
            skLineSegment(sketch, "E2.5.5.1", {"start": v(203.2, 228.6) * mm, "end": v(228.6, 228.6) * mm});
            skLineSegment(sketch, "E2.5.5.2", {"start": v(203.2, 203.2) * mm, "end": v(228.6, 203.2) * mm});
            skLineSegment(sketch, "E2.5.5.3", {"start": v(203.2, 203.2) * mm, "end": v(203.2, 228.6) * mm});
            skLineSegment(sketch, "E2.5.6.0", {"start": v(228.6, 241.3) * mm, "end": v(228.6, 266.7) * mm});
            skLineSegment(sketch, "E2.5.6.1", {"start": v(203.2, 266.7) * mm, "end": v(228.6, 266.7) * mm});
            skLineSegment(sketch, "E2.5.6.2", {"start": v(203.2, 241.3) * mm, "end": v(228.6, 241.3) * mm});
            skLineSegment(sketch, "E2.5.6.3", {"start": v(203.2, 241.3) * mm, "end": v(203.2, 266.7) * mm});
            skLineSegment(sketch, "E2.5.7.0", {"start": v(228.6, 279.4) * mm, "end": v(228.6, 304.8) * mm});
            skLineSegment(sketch, "E2.5.7.1", {"start": v(203.2, 304.8) * mm, "end": v(228.6, 304.8) * mm});
            skLineSegment(sketch, "E2.5.7.2", {"start": v(203.2, 279.4) * mm, "end": v(228.6, 279.4) * mm});
            skLineSegment(sketch, "E2.5.7.3", {"start": v(203.2, 279.4) * mm, "end": v(203.2, 304.8) * mm});
            skLineSegment(sketch, "E2.5.8.0", {"start": v(228.6, 317.5) * mm, "end": v(228.6, 342.9) * mm});
            skLineSegment(sketch, "E2.5.8.1", {"start": v(203.2, 342.9) * mm, "end": v(228.6, 342.9) * mm});
            skLineSegment(sketch, "E2.5.8.2", {"start": v(203.2, 317.5) * mm, "end": v(228.6, 317.5) * mm});
            skLineSegment(sketch, "E2.5.8.3", {"start": v(203.2, 317.5) * mm, "end": v(203.2, 342.9) * mm});
            skLineSegment(sketch, "E2.5.9.0", {"start": v(228.6, 355.6) * mm, "end": v(228.6, 381) * mm});
            skLineSegment(sketch, "E2.5.9.1", {"start": v(203.2, 381) * mm, "end": v(228.6, 381) * mm});
            skLineSegment(sketch, "E2.5.9.2", {"start": v(203.2, 355.6) * mm, "end": v(228.6, 355.6) * mm});
            skLineSegment(sketch, "E2.5.9.3", {"start": v(203.2, 355.6) * mm, "end": v(203.2, 381) * mm});
            skLineSegment(sketch, "E2.5.10.0", {"start": v(228.6, 393.7) * mm, "end": v(228.6, 419.1) * mm});
            skLineSegment(sketch, "E2.5.10.1", {"start": v(203.2, 419.1) * mm, "end": v(228.6, 419.1) * mm});
            skLineSegment(sketch, "E2.5.10.2", {"start": v(203.2, 393.7) * mm, "end": v(228.6, 393.7) * mm});
            skLineSegment(sketch, "E2.5.10.3", {"start": v(203.2, 393.7) * mm, "end": v(203.2, 419.1) * mm});
            skLineSegment(sketch, "E2.5.11.0", {"start": v(228.6, 431.8) * mm, "end": v(228.6, 457.2) * mm});
            skLineSegment(sketch, "E2.5.11.1", {"start": v(203.2, 457.2) * mm, "end": v(228.6, 457.2) * mm});
            skLineSegment(sketch, "E2.5.11.2", {"start": v(203.2, 431.8) * mm, "end": v(228.6, 431.8) * mm});
            skLineSegment(sketch, "E2.5.11.3", {"start": v(203.2, 431.8) * mm, "end": v(203.2, 457.2) * mm});
            skLineSegment(sketch, "E2.5.12.0", {"start": v(228.6, 469.9) * mm, "end": v(228.6, 495.3) * mm});
            skLineSegment(sketch, "E2.5.12.1", {"start": v(203.2, 495.3) * mm, "end": v(228.6, 495.3) * mm});
            skLineSegment(sketch, "E2.5.12.2", {"start": v(203.2, 469.9) * mm, "end": v(228.6, 469.9) * mm});
            skLineSegment(sketch, "E2.5.12.3", {"start": v(203.2, 469.9) * mm, "end": v(203.2, 495.3) * mm});
            skLineSegment(sketch, "E2.5.13.0", {"start": v(228.6, 508) * mm, "end": v(228.6, 533.4) * mm});
            skLineSegment(sketch, "E2.5.13.1", {"start": v(203.2, 533.4) * mm, "end": v(228.6, 533.4) * mm});
            skLineSegment(sketch, "E2.5.13.2", {"start": v(203.2, 508) * mm, "end": v(228.6, 508) * mm});
            skLineSegment(sketch, "E2.5.13.3", {"start": v(203.2, 508) * mm, "end": v(203.2, 533.4) * mm});
            skLineSegment(sketch, "E2.5.14.0", {"start": v(228.6, 546.1) * mm, "end": v(228.6, 571.5) * mm});
            skLineSegment(sketch, "E2.5.14.1", {"start": v(203.2, 571.5) * mm, "end": v(228.6, 571.5) * mm});
            skLineSegment(sketch, "E2.5.14.2", {"start": v(203.2, 546.1) * mm, "end": v(228.6, 546.1) * mm});
            skLineSegment(sketch, "E2.5.14.3", {"start": v(203.2, 546.1) * mm, "end": v(203.2, 571.5) * mm});
            skLineSegment(sketch, "E2.5.15.0", {"start": v(228.6, 584.2) * mm, "end": v(228.6, 609.6) * mm});
            skLineSegment(sketch, "E2.5.15.1", {"start": v(203.2, 609.6) * mm, "end": v(228.6, 609.6) * mm});
            skLineSegment(sketch, "E2.5.15.2", {"start": v(203.2, 584.2) * mm, "end": v(228.6, 584.2) * mm});
            skLineSegment(sketch, "E2.5.15.3", {"start": v(203.2, 584.2) * mm, "end": v(203.2, 609.6) * mm});
            skLineSegment(sketch, "E2.5.16.0", {"start": v(228.6, 622.3) * mm, "end": v(228.6, 647.7) * mm});
            skLineSegment(sketch, "E2.5.16.1", {"start": v(203.2, 647.7) * mm, "end": v(228.6, 647.7) * mm});
            skLineSegment(sketch, "E2.5.16.2", {"start": v(203.2, 622.3) * mm, "end": v(228.6, 622.3) * mm});
            skLineSegment(sketch, "E2.5.16.3", {"start": v(203.2, 622.3) * mm, "end": v(203.2, 647.7) * mm});
            skLineSegment(sketch, "E2.5.17.0", {"start": v(228.6, 660.4) * mm, "end": v(228.6, 685.8) * mm});
            skLineSegment(sketch, "E2.5.17.1", {"start": v(203.2, 685.8) * mm, "end": v(228.6, 685.8) * mm});
            skLineSegment(sketch, "E2.5.17.2", {"start": v(203.2, 660.4) * mm, "end": v(228.6, 660.4) * mm});
            skLineSegment(sketch, "E2.5.17.3", {"start": v(203.2, 660.4) * mm, "end": v(203.2, 685.8) * mm});
            skLineSegment(sketch, "E2.5.18.0", {"start": v(228.6, 698.5) * mm, "end": v(228.6, 723.9) * mm});
            skLineSegment(sketch, "E2.5.18.1", {"start": v(203.2, 723.9) * mm, "end": v(228.6, 723.9) * mm});
            skLineSegment(sketch, "E2.5.18.2", {"start": v(203.2, 698.5) * mm, "end": v(228.6, 698.5) * mm});
            skLineSegment(sketch, "E2.5.18.3", {"start": v(203.2, 698.5) * mm, "end": v(203.2, 723.9) * mm});
            skLineSegment(sketch, "E2.5.19.0", {"start": v(228.6, 736.6) * mm, "end": v(228.6, 762) * mm});
            skLineSegment(sketch, "E2.5.19.1", {"start": v(203.2, 762) * mm, "end": v(228.6, 762) * mm});
            skLineSegment(sketch, "E2.5.19.2", {"start": v(203.2, 736.6) * mm, "end": v(228.6, 736.6) * mm});
            skLineSegment(sketch, "E2.5.19.3", {"start": v(203.2, 736.6) * mm, "end": v(203.2, 762) * mm});
            skLineSegment(sketch, "E2.6.0.0", {"start": v(266.7, 12.7) * mm, "end": v(266.7, 38.1) * mm});
            skLineSegment(sketch, "E2.6.0.1", {"start": v(241.3, 38.1) * mm, "end": v(266.7, 38.1) * mm});
            skLineSegment(sketch, "E2.6.0.2", {"start": v(241.3, 12.7) * mm, "end": v(266.7, 12.7) * mm});
            skLineSegment(sketch, "E2.6.0.3", {"start": v(241.3, 12.7) * mm, "end": v(241.3, 38.1) * mm});
            skLineSegment(sketch, "E2.6.1.0", {"start": v(266.7, 50.8) * mm, "end": v(266.7, 76.2) * mm});
            skLineSegment(sketch, "E2.6.1.1", {"start": v(241.3, 76.2) * mm, "end": v(266.7, 76.2) * mm});
            skLineSegment(sketch, "E2.6.1.2", {"start": v(241.3, 50.8) * mm, "end": v(266.7, 50.8) * mm});
            skLineSegment(sketch, "E2.6.1.3", {"start": v(241.3, 50.8) * mm, "end": v(241.3, 76.2) * mm});
            skLineSegment(sketch, "E2.6.2.0", {"start": v(266.7, 88.9) * mm, "end": v(266.7, 114.3) * mm});
            skLineSegment(sketch, "E2.6.2.1", {"start": v(241.3, 114.3) * mm, "end": v(266.7, 114.3) * mm});
            skLineSegment(sketch, "E2.6.2.2", {"start": v(241.3, 88.9) * mm, "end": v(266.7, 88.9) * mm});
            skLineSegment(sketch, "E2.6.2.3", {"start": v(241.3, 88.9) * mm, "end": v(241.3, 114.3) * mm});
            skLineSegment(sketch, "E2.6.3.0", {"start": v(266.7, 127) * mm, "end": v(266.7, 152.4) * mm});
            skLineSegment(sketch, "E2.6.3.1", {"start": v(241.3, 152.4) * mm, "end": v(266.7, 152.4) * mm});
            skLineSegment(sketch, "E2.6.3.2", {"start": v(241.3, 127) * mm, "end": v(266.7, 127) * mm});
            skLineSegment(sketch, "E2.6.3.3", {"start": v(241.3, 127) * mm, "end": v(241.3, 152.4) * mm});
            skLineSegment(sketch, "E2.6.4.0", {"start": v(266.7, 165.1) * mm, "end": v(266.7, 190.5) * mm});
            skLineSegment(sketch, "E2.6.4.1", {"start": v(241.3, 190.5) * mm, "end": v(266.7, 190.5) * mm});
            skLineSegment(sketch, "E2.6.4.2", {"start": v(241.3, 165.1) * mm, "end": v(266.7, 165.1) * mm});
            skLineSegment(sketch, "E2.6.4.3", {"start": v(241.3, 165.1) * mm, "end": v(241.3, 190.5) * mm});
            skLineSegment(sketch, "E2.6.5.0", {"start": v(266.7, 203.2) * mm, "end": v(266.7, 228.6) * mm});
            skLineSegment(sketch, "E2.6.5.1", {"start": v(241.3, 228.6) * mm, "end": v(266.7, 228.6) * mm});
            skLineSegment(sketch, "E2.6.5.2", {"start": v(241.3, 203.2) * mm, "end": v(266.7, 203.2) * mm});
            skLineSegment(sketch, "E2.6.5.3", {"start": v(241.3, 203.2) * mm, "end": v(241.3, 228.6) * mm});
            skLineSegment(sketch, "E2.6.6.0", {"start": v(266.7, 241.3) * mm, "end": v(266.7, 266.7) * mm});
            skLineSegment(sketch, "E2.6.6.1", {"start": v(241.3, 266.7) * mm, "end": v(266.7, 266.7) * mm});
            skLineSegment(sketch, "E2.6.6.2", {"start": v(241.3, 241.3) * mm, "end": v(266.7, 241.3) * mm});
            skLineSegment(sketch, "E2.6.6.3", {"start": v(241.3, 241.3) * mm, "end": v(241.3, 266.7) * mm});
            skLineSegment(sketch, "E2.6.7.0", {"start": v(266.7, 279.4) * mm, "end": v(266.7, 304.8) * mm});
            skLineSegment(sketch, "E2.6.7.1", {"start": v(241.3, 304.8) * mm, "end": v(266.7, 304.8) * mm});
            skLineSegment(sketch, "E2.6.7.2", {"start": v(241.3, 279.4) * mm, "end": v(266.7, 279.4) * mm});
            skLineSegment(sketch, "E2.6.7.3", {"start": v(241.3, 279.4) * mm, "end": v(241.3, 304.8) * mm});
            skLineSegment(sketch, "E2.6.8.0", {"start": v(266.7, 317.5) * mm, "end": v(266.7, 342.9) * mm});
            skLineSegment(sketch, "E2.6.8.1", {"start": v(241.3, 342.9) * mm, "end": v(266.7, 342.9) * mm});
            skLineSegment(sketch, "E2.6.8.2", {"start": v(241.3, 317.5) * mm, "end": v(266.7, 317.5) * mm});
            skLineSegment(sketch, "E2.6.8.3", {"start": v(241.3, 317.5) * mm, "end": v(241.3, 342.9) * mm});
            skLineSegment(sketch, "E2.6.9.0", {"start": v(266.7, 355.6) * mm, "end": v(266.7, 381) * mm});
            skLineSegment(sketch, "E2.6.9.1", {"start": v(241.3, 381) * mm, "end": v(266.7, 381) * mm});
            skLineSegment(sketch, "E2.6.9.2", {"start": v(241.3, 355.6) * mm, "end": v(266.7, 355.6) * mm});
            skLineSegment(sketch, "E2.6.9.3", {"start": v(241.3, 355.6) * mm, "end": v(241.3, 381) * mm});
            skLineSegment(sketch, "E2.6.10.0", {"start": v(266.7, 393.7) * mm, "end": v(266.7, 419.1) * mm});
            skLineSegment(sketch, "E2.6.10.1", {"start": v(241.3, 419.1) * mm, "end": v(266.7, 419.1) * mm});
            skLineSegment(sketch, "E2.6.10.2", {"start": v(241.3, 393.7) * mm, "end": v(266.7, 393.7) * mm});
            skLineSegment(sketch, "E2.6.10.3", {"start": v(241.3, 393.7) * mm, "end": v(241.3, 419.1) * mm});
            skLineSegment(sketch, "E2.6.11.0", {"start": v(266.7, 431.8) * mm, "end": v(266.7, 457.2) * mm});
            skLineSegment(sketch, "E2.6.11.1", {"start": v(241.3, 457.2) * mm, "end": v(266.7, 457.2) * mm});
            skLineSegment(sketch, "E2.6.11.2", {"start": v(241.3, 431.8) * mm, "end": v(266.7, 431.8) * mm});
            skLineSegment(sketch, "E2.6.11.3", {"start": v(241.3, 431.8) * mm, "end": v(241.3, 457.2) * mm});
            skLineSegment(sketch, "E2.6.12.0", {"start": v(266.7, 469.9) * mm, "end": v(266.7, 495.3) * mm});
            skLineSegment(sketch, "E2.6.12.1", {"start": v(241.3, 495.3) * mm, "end": v(266.7, 495.3) * mm});
            skLineSegment(sketch, "E2.6.12.2", {"start": v(241.3, 469.9) * mm, "end": v(266.7, 469.9) * mm});
            skLineSegment(sketch, "E2.6.12.3", {"start": v(241.3, 469.9) * mm, "end": v(241.3, 495.3) * mm});
            skLineSegment(sketch, "E2.6.13.0", {"start": v(266.7, 508) * mm, "end": v(266.7, 533.4) * mm});
            skLineSegment(sketch, "E2.6.13.1", {"start": v(241.3, 533.4) * mm, "end": v(266.7, 533.4) * mm});
            skLineSegment(sketch, "E2.6.13.2", {"start": v(241.3, 508) * mm, "end": v(266.7, 508) * mm});
            skLineSegment(sketch, "E2.6.13.3", {"start": v(241.3, 508) * mm, "end": v(241.3, 533.4) * mm});
            skLineSegment(sketch, "E2.6.14.0", {"start": v(266.7, 546.1) * mm, "end": v(266.7, 571.5) * mm});
            skLineSegment(sketch, "E2.6.14.1", {"start": v(241.3, 571.5) * mm, "end": v(266.7, 571.5) * mm});
            skLineSegment(sketch, "E2.6.14.2", {"start": v(241.3, 546.1) * mm, "end": v(266.7, 546.1) * mm});
            skLineSegment(sketch, "E2.6.14.3", {"start": v(241.3, 546.1) * mm, "end": v(241.3, 571.5) * mm});
            skLineSegment(sketch, "E2.6.15.0", {"start": v(266.7, 584.2) * mm, "end": v(266.7, 609.6) * mm});
            skLineSegment(sketch, "E2.6.15.1", {"start": v(241.3, 609.6) * mm, "end": v(266.7, 609.6) * mm});
            skLineSegment(sketch, "E2.6.15.2", {"start": v(241.3, 584.2) * mm, "end": v(266.7, 584.2) * mm});
            skLineSegment(sketch, "E2.6.15.3", {"start": v(241.3, 584.2) * mm, "end": v(241.3, 609.6) * mm});
            skLineSegment(sketch, "E2.6.16.0", {"start": v(266.7, 622.3) * mm, "end": v(266.7, 647.7) * mm});
            skLineSegment(sketch, "E2.6.16.1", {"start": v(241.3, 647.7) * mm, "end": v(266.7, 647.7) * mm});
            skLineSegment(sketch, "E2.6.16.2", {"start": v(241.3, 622.3) * mm, "end": v(266.7, 622.3) * mm});
            skLineSegment(sketch, "E2.6.16.3", {"start": v(241.3, 622.3) * mm, "end": v(241.3, 647.7) * mm});
            skLineSegment(sketch, "E2.6.17.0", {"start": v(266.7, 660.4) * mm, "end": v(266.7, 685.8) * mm});
            skLineSegment(sketch, "E2.6.17.1", {"start": v(241.3, 685.8) * mm, "end": v(266.7, 685.8) * mm});
            skLineSegment(sketch, "E2.6.17.2", {"start": v(241.3, 660.4) * mm, "end": v(266.7, 660.4) * mm});
            skLineSegment(sketch, "E2.6.17.3", {"start": v(241.3, 660.4) * mm, "end": v(241.3, 685.8) * mm});
            skLineSegment(sketch, "E2.6.18.0", {"start": v(266.7, 698.5) * mm, "end": v(266.7, 723.9) * mm});
            skLineSegment(sketch, "E2.6.18.1", {"start": v(241.3, 723.9) * mm, "end": v(266.7, 723.9) * mm});
            skLineSegment(sketch, "E2.6.18.2", {"start": v(241.3, 698.5) * mm, "end": v(266.7, 698.5) * mm});
            skLineSegment(sketch, "E2.6.18.3", {"start": v(241.3, 698.5) * mm, "end": v(241.3, 723.9) * mm});
            skLineSegment(sketch, "E2.6.19.0", {"start": v(266.7, 736.6) * mm, "end": v(266.7, 762) * mm});
            skLineSegment(sketch, "E2.6.19.1", {"start": v(241.3, 762) * mm, "end": v(266.7, 762) * mm});
            skLineSegment(sketch, "E2.6.19.2", {"start": v(241.3, 736.6) * mm, "end": v(266.7, 736.6) * mm});
            skLineSegment(sketch, "E2.6.19.3", {"start": v(241.3, 736.6) * mm, "end": v(241.3, 762) * mm});
            skLineSegment(sketch, "E2.7.0.0", {"start": v(304.8, 12.7) * mm, "end": v(304.8, 38.1) * mm});
            skLineSegment(sketch, "E2.7.0.1", {"start": v(279.4, 38.1) * mm, "end": v(304.8, 38.1) * mm});
            skLineSegment(sketch, "E2.7.0.2", {"start": v(279.4, 12.7) * mm, "end": v(304.8, 12.7) * mm});
            skLineSegment(sketch, "E2.7.0.3", {"start": v(279.4, 12.7) * mm, "end": v(279.4, 38.1) * mm});
            skLineSegment(sketch, "E2.7.1.0", {"start": v(304.8, 50.8) * mm, "end": v(304.8, 76.2) * mm});
            skLineSegment(sketch, "E2.7.1.1", {"start": v(279.4, 76.2) * mm, "end": v(304.8, 76.2) * mm});
            skLineSegment(sketch, "E2.7.1.2", {"start": v(279.4, 50.8) * mm, "end": v(304.8, 50.8) * mm});
            skLineSegment(sketch, "E2.7.1.3", {"start": v(279.4, 50.8) * mm, "end": v(279.4, 76.2) * mm});
            skLineSegment(sketch, "E2.7.2.0", {"start": v(304.8, 88.9) * mm, "end": v(304.8, 114.3) * mm});
            skLineSegment(sketch, "E2.7.2.1", {"start": v(279.4, 114.3) * mm, "end": v(304.8, 114.3) * mm});
            skLineSegment(sketch, "E2.7.2.2", {"start": v(279.4, 88.9) * mm, "end": v(304.8, 88.9) * mm});
            skLineSegment(sketch, "E2.7.2.3", {"start": v(279.4, 88.9) * mm, "end": v(279.4, 114.3) * mm});
            skLineSegment(sketch, "E2.7.3.0", {"start": v(304.8, 127) * mm, "end": v(304.8, 152.4) * mm});
            skLineSegment(sketch, "E2.7.3.1", {"start": v(279.4, 152.4) * mm, "end": v(304.8, 152.4) * mm});
            skLineSegment(sketch, "E2.7.3.2", {"start": v(279.4, 127) * mm, "end": v(304.8, 127) * mm});
            skLineSegment(sketch, "E2.7.3.3", {"start": v(279.4, 127) * mm, "end": v(279.4, 152.4) * mm});
            skLineSegment(sketch, "E2.7.4.0", {"start": v(304.8, 165.1) * mm, "end": v(304.8, 190.5) * mm});
            skLineSegment(sketch, "E2.7.4.1", {"start": v(279.4, 190.5) * mm, "end": v(304.8, 190.5) * mm});
            skLineSegment(sketch, "E2.7.4.2", {"start": v(279.4, 165.1) * mm, "end": v(304.8, 165.1) * mm});
            skLineSegment(sketch, "E2.7.4.3", {"start": v(279.4, 165.1) * mm, "end": v(279.4, 190.5) * mm});
            skLineSegment(sketch, "E2.7.5.0", {"start": v(304.8, 203.2) * mm, "end": v(304.8, 228.6) * mm});
            skLineSegment(sketch, "E2.7.5.1", {"start": v(279.4, 228.6) * mm, "end": v(304.8, 228.6) * mm});
            skLineSegment(sketch, "E2.7.5.2", {"start": v(279.4, 203.2) * mm, "end": v(304.8, 203.2) * mm});
            skLineSegment(sketch, "E2.7.5.3", {"start": v(279.4, 203.2) * mm, "end": v(279.4, 228.6) * mm});
            skLineSegment(sketch, "E2.7.6.0", {"start": v(304.8, 241.3) * mm, "end": v(304.8, 266.7) * mm});
            skLineSegment(sketch, "E2.7.6.1", {"start": v(279.4, 266.7) * mm, "end": v(304.8, 266.7) * mm});
            skLineSegment(sketch, "E2.7.6.2", {"start": v(279.4, 241.3) * mm, "end": v(304.8, 241.3) * mm});
            skLineSegment(sketch, "E2.7.6.3", {"start": v(279.4, 241.3) * mm, "end": v(279.4, 266.7) * mm});
            skLineSegment(sketch, "E2.7.7.0", {"start": v(304.8, 279.4) * mm, "end": v(304.8, 304.8) * mm});
            skLineSegment(sketch, "E2.7.7.1", {"start": v(279.4, 304.8) * mm, "end": v(304.8, 304.8) * mm});
            skLineSegment(sketch, "E2.7.7.2", {"start": v(279.4, 279.4) * mm, "end": v(304.8, 279.4) * mm});
            skLineSegment(sketch, "E2.7.7.3", {"start": v(279.4, 279.4) * mm, "end": v(279.4, 304.8) * mm});
            skLineSegment(sketch, "E2.7.8.0", {"start": v(304.8, 317.5) * mm, "end": v(304.8, 342.9) * mm});
            skLineSegment(sketch, "E2.7.8.1", {"start": v(279.4, 342.9) * mm, "end": v(304.8, 342.9) * mm});
            skLineSegment(sketch, "E2.7.8.2", {"start": v(279.4, 317.5) * mm, "end": v(304.8, 317.5) * mm});
            skLineSegment(sketch, "E2.7.8.3", {"start": v(279.4, 317.5) * mm, "end": v(279.4, 342.9) * mm});
            skLineSegment(sketch, "E2.7.9.0", {"start": v(304.8, 355.6) * mm, "end": v(304.8, 381) * mm});
            skLineSegment(sketch, "E2.7.9.1", {"start": v(279.4, 381) * mm, "end": v(304.8, 381) * mm});
            skLineSegment(sketch, "E2.7.9.2", {"start": v(279.4, 355.6) * mm, "end": v(304.8, 355.6) * mm});
            skLineSegment(sketch, "E2.7.9.3", {"start": v(279.4, 355.6) * mm, "end": v(279.4, 381) * mm});
            skLineSegment(sketch, "E2.7.10.0", {"start": v(304.8, 393.7) * mm, "end": v(304.8, 419.1) * mm});
            skLineSegment(sketch, "E2.7.10.1", {"start": v(279.4, 419.1) * mm, "end": v(304.8, 419.1) * mm});
            skLineSegment(sketch, "E2.7.10.2", {"start": v(279.4, 393.7) * mm, "end": v(304.8, 393.7) * mm});
            skLineSegment(sketch, "E2.7.10.3", {"start": v(279.4, 393.7) * mm, "end": v(279.4, 419.1) * mm});
            skLineSegment(sketch, "E2.7.11.0", {"start": v(304.8, 431.8) * mm, "end": v(304.8, 457.2) * mm});
            skLineSegment(sketch, "E2.7.11.1", {"start": v(279.4, 457.2) * mm, "end": v(304.8, 457.2) * mm});
            skLineSegment(sketch, "E2.7.11.2", {"start": v(279.4, 431.8) * mm, "end": v(304.8, 431.8) * mm});
            skLineSegment(sketch, "E2.7.11.3", {"start": v(279.4, 431.8) * mm, "end": v(279.4, 457.2) * mm});
            skLineSegment(sketch, "E2.7.12.0", {"start": v(304.8, 469.9) * mm, "end": v(304.8, 495.3) * mm});
            skLineSegment(sketch, "E2.7.12.1", {"start": v(279.4, 495.3) * mm, "end": v(304.8, 495.3) * mm});
            skLineSegment(sketch, "E2.7.12.2", {"start": v(279.4, 469.9) * mm, "end": v(304.8, 469.9) * mm});
            skLineSegment(sketch, "E2.7.12.3", {"start": v(279.4, 469.9) * mm, "end": v(279.4, 495.3) * mm});
            skLineSegment(sketch, "E2.7.13.0", {"start": v(304.8, 508) * mm, "end": v(304.8, 533.4) * mm});
            skLineSegment(sketch, "E2.7.13.1", {"start": v(279.4, 533.4) * mm, "end": v(304.8, 533.4) * mm});
            skLineSegment(sketch, "E2.7.13.2", {"start": v(279.4, 508) * mm, "end": v(304.8, 508) * mm});
            skLineSegment(sketch, "E2.7.13.3", {"start": v(279.4, 508) * mm, "end": v(279.4, 533.4) * mm});
            skLineSegment(sketch, "E2.7.14.0", {"start": v(304.8, 546.1) * mm, "end": v(304.8, 571.5) * mm});
            skLineSegment(sketch, "E2.7.14.1", {"start": v(279.4, 571.5) * mm, "end": v(304.8, 571.5) * mm});
            skLineSegment(sketch, "E2.7.14.2", {"start": v(279.4, 546.1) * mm, "end": v(304.8, 546.1) * mm});
            skLineSegment(sketch, "E2.7.14.3", {"start": v(279.4, 546.1) * mm, "end": v(279.4, 571.5) * mm});
            skLineSegment(sketch, "E2.7.15.0", {"start": v(304.8, 584.2) * mm, "end": v(304.8, 609.6) * mm});
            skLineSegment(sketch, "E2.7.15.1", {"start": v(279.4, 609.6) * mm, "end": v(304.8, 609.6) * mm});
            skLineSegment(sketch, "E2.7.15.2", {"start": v(279.4, 584.2) * mm, "end": v(304.8, 584.2) * mm});
            skLineSegment(sketch, "E2.7.15.3", {"start": v(279.4, 584.2) * mm, "end": v(279.4, 609.6) * mm});
            skLineSegment(sketch, "E2.7.16.0", {"start": v(304.8, 622.3) * mm, "end": v(304.8, 647.7) * mm});
            skLineSegment(sketch, "E2.7.16.1", {"start": v(279.4, 647.7) * mm, "end": v(304.8, 647.7) * mm});
            skLineSegment(sketch, "E2.7.16.2", {"start": v(279.4, 622.3) * mm, "end": v(304.8, 622.3) * mm});
            skLineSegment(sketch, "E2.7.16.3", {"start": v(279.4, 622.3) * mm, "end": v(279.4, 647.7) * mm});
            skLineSegment(sketch, "E2.7.17.0", {"start": v(304.8, 660.4) * mm, "end": v(304.8, 685.8) * mm});
            skLineSegment(sketch, "E2.7.17.1", {"start": v(279.4, 685.8) * mm, "end": v(304.8, 685.8) * mm});
            skLineSegment(sketch, "E2.7.17.2", {"start": v(279.4, 660.4) * mm, "end": v(304.8, 660.4) * mm});
            skLineSegment(sketch, "E2.7.17.3", {"start": v(279.4, 660.4) * mm, "end": v(279.4, 685.8) * mm});
            skLineSegment(sketch, "E2.7.18.0", {"start": v(304.8, 698.5) * mm, "end": v(304.8, 723.9) * mm});
            skLineSegment(sketch, "E2.7.18.1", {"start": v(279.4, 723.9) * mm, "end": v(304.8, 723.9) * mm});
            skLineSegment(sketch, "E2.7.18.2", {"start": v(279.4, 698.5) * mm, "end": v(304.8, 698.5) * mm});
            skLineSegment(sketch, "E2.7.18.3", {"start": v(279.4, 698.5) * mm, "end": v(279.4, 723.9) * mm});
            skLineSegment(sketch, "E2.7.19.0", {"start": v(304.8, 736.6) * mm, "end": v(304.8, 762) * mm});
            skLineSegment(sketch, "E2.7.19.1", {"start": v(279.4, 762) * mm, "end": v(304.8, 762) * mm});
            skLineSegment(sketch, "E2.7.19.2", {"start": v(279.4, 736.6) * mm, "end": v(304.8, 736.6) * mm});
            skLineSegment(sketch, "E2.7.19.3", {"start": v(279.4, 736.6) * mm, "end": v(279.4, 762) * mm});
            skLineSegment(sketch, "E2.8.0.0", {"start": v(342.9, 12.7) * mm, "end": v(342.9, 38.1) * mm});
            skLineSegment(sketch, "E2.8.0.1", {"start": v(317.5, 38.1) * mm, "end": v(342.9, 38.1) * mm});
            skLineSegment(sketch, "E2.8.0.2", {"start": v(317.5, 12.7) * mm, "end": v(342.9, 12.7) * mm});
            skLineSegment(sketch, "E2.8.0.3", {"start": v(317.5, 12.7) * mm, "end": v(317.5, 38.1) * mm});
            skLineSegment(sketch, "E2.8.1.0", {"start": v(342.9, 50.8) * mm, "end": v(342.9, 76.2) * mm});
            skLineSegment(sketch, "E2.8.1.1", {"start": v(317.5, 76.2) * mm, "end": v(342.9, 76.2) * mm});
            skLineSegment(sketch, "E2.8.1.2", {"start": v(317.5, 50.8) * mm, "end": v(342.9, 50.8) * mm});
            skLineSegment(sketch, "E2.8.1.3", {"start": v(317.5, 50.8) * mm, "end": v(317.5, 76.2) * mm});
            skLineSegment(sketch, "E2.8.2.0", {"start": v(342.9, 88.9) * mm, "end": v(342.9, 114.3) * mm});
            skLineSegment(sketch, "E2.8.2.1", {"start": v(317.5, 114.3) * mm, "end": v(342.9, 114.3) * mm});
            skLineSegment(sketch, "E2.8.2.2", {"start": v(317.5, 88.9) * mm, "end": v(342.9, 88.9) * mm});
            skLineSegment(sketch, "E2.8.2.3", {"start": v(317.5, 88.9) * mm, "end": v(317.5, 114.3) * mm});
            skLineSegment(sketch, "E2.8.3.0", {"start": v(342.9, 127) * mm, "end": v(342.9, 152.4) * mm});
            skLineSegment(sketch, "E2.8.3.1", {"start": v(317.5, 152.4) * mm, "end": v(342.9, 152.4) * mm});
            skLineSegment(sketch, "E2.8.3.2", {"start": v(317.5, 127) * mm, "end": v(342.9, 127) * mm});
            skLineSegment(sketch, "E2.8.3.3", {"start": v(317.5, 127) * mm, "end": v(317.5, 152.4) * mm});
            skLineSegment(sketch, "E2.8.4.0", {"start": v(342.9, 165.1) * mm, "end": v(342.9, 190.5) * mm});
            skLineSegment(sketch, "E2.8.4.1", {"start": v(317.5, 190.5) * mm, "end": v(342.9, 190.5) * mm});
            skLineSegment(sketch, "E2.8.4.2", {"start": v(317.5, 165.1) * mm, "end": v(342.9, 165.1) * mm});
            skLineSegment(sketch, "E2.8.4.3", {"start": v(317.5, 165.1) * mm, "end": v(317.5, 190.5) * mm});
            skLineSegment(sketch, "E2.8.5.0", {"start": v(342.9, 203.2) * mm, "end": v(342.9, 228.6) * mm});
            skLineSegment(sketch, "E2.8.5.1", {"start": v(317.5, 228.6) * mm, "end": v(342.9, 228.6) * mm});
            skLineSegment(sketch, "E2.8.5.2", {"start": v(317.5, 203.2) * mm, "end": v(342.9, 203.2) * mm});
            skLineSegment(sketch, "E2.8.5.3", {"start": v(317.5, 203.2) * mm, "end": v(317.5, 228.6) * mm});
            skLineSegment(sketch, "E2.8.6.0", {"start": v(342.9, 241.3) * mm, "end": v(342.9, 266.7) * mm});
            skLineSegment(sketch, "E2.8.6.1", {"start": v(317.5, 266.7) * mm, "end": v(342.9, 266.7) * mm});
            skLineSegment(sketch, "E2.8.6.2", {"start": v(317.5, 241.3) * mm, "end": v(342.9, 241.3) * mm});
            skLineSegment(sketch, "E2.8.6.3", {"start": v(317.5, 241.3) * mm, "end": v(317.5, 266.7) * mm});
            skLineSegment(sketch, "E2.8.7.0", {"start": v(342.9, 279.4) * mm, "end": v(342.9, 304.8) * mm});
            skLineSegment(sketch, "E2.8.7.1", {"start": v(317.5, 304.8) * mm, "end": v(342.9, 304.8) * mm});
            skLineSegment(sketch, "E2.8.7.2", {"start": v(317.5, 279.4) * mm, "end": v(342.9, 279.4) * mm});
            skLineSegment(sketch, "E2.8.7.3", {"start": v(317.5, 279.4) * mm, "end": v(317.5, 304.8) * mm});
            skLineSegment(sketch, "E2.8.8.0", {"start": v(342.9, 317.5) * mm, "end": v(342.9, 342.9) * mm});
            skLineSegment(sketch, "E2.8.8.1", {"start": v(317.5, 342.9) * mm, "end": v(342.9, 342.9) * mm});
            skLineSegment(sketch, "E2.8.8.2", {"start": v(317.5, 317.5) * mm, "end": v(342.9, 317.5) * mm});
            skLineSegment(sketch, "E2.8.8.3", {"start": v(317.5, 317.5) * mm, "end": v(317.5, 342.9) * mm});
            skLineSegment(sketch, "E2.8.9.0", {"start": v(342.9, 355.6) * mm, "end": v(342.9, 381) * mm});
            skLineSegment(sketch, "E2.8.9.1", {"start": v(317.5, 381) * mm, "end": v(342.9, 381) * mm});
            skLineSegment(sketch, "E2.8.9.2", {"start": v(317.5, 355.6) * mm, "end": v(342.9, 355.6) * mm});
            skLineSegment(sketch, "E2.8.9.3", {"start": v(317.5, 355.6) * mm, "end": v(317.5, 381) * mm});
            skLineSegment(sketch, "E2.8.10.0", {"start": v(342.9, 393.7) * mm, "end": v(342.9, 419.1) * mm});
            skLineSegment(sketch, "E2.8.10.1", {"start": v(317.5, 419.1) * mm, "end": v(342.9, 419.1) * mm});
            skLineSegment(sketch, "E2.8.10.2", {"start": v(317.5, 393.7) * mm, "end": v(342.9, 393.7) * mm});
            skLineSegment(sketch, "E2.8.10.3", {"start": v(317.5, 393.7) * mm, "end": v(317.5, 419.1) * mm});
            skLineSegment(sketch, "E2.8.11.0", {"start": v(342.9, 431.8) * mm, "end": v(342.9, 457.2) * mm});
            skLineSegment(sketch, "E2.8.11.1", {"start": v(317.5, 457.2) * mm, "end": v(342.9, 457.2) * mm});
            skLineSegment(sketch, "E2.8.11.2", {"start": v(317.5, 431.8) * mm, "end": v(342.9, 431.8) * mm});
            skLineSegment(sketch, "E2.8.11.3", {"start": v(317.5, 431.8) * mm, "end": v(317.5, 457.2) * mm});
            skLineSegment(sketch, "E2.8.12.0", {"start": v(342.9, 469.9) * mm, "end": v(342.9, 495.3) * mm});
            skLineSegment(sketch, "E2.8.12.1", {"start": v(317.5, 495.3) * mm, "end": v(342.9, 495.3) * mm});
            skLineSegment(sketch, "E2.8.12.2", {"start": v(317.5, 469.9) * mm, "end": v(342.9, 469.9) * mm});
            skLineSegment(sketch, "E2.8.12.3", {"start": v(317.5, 469.9) * mm, "end": v(317.5, 495.3) * mm});
            skLineSegment(sketch, "E2.8.13.0", {"start": v(342.9, 508) * mm, "end": v(342.9, 533.4) * mm});
            skLineSegment(sketch, "E2.8.13.1", {"start": v(317.5, 533.4) * mm, "end": v(342.9, 533.4) * mm});
            skLineSegment(sketch, "E2.8.13.2", {"start": v(317.5, 508) * mm, "end": v(342.9, 508) * mm});
            skLineSegment(sketch, "E2.8.13.3", {"start": v(317.5, 508) * mm, "end": v(317.5, 533.4) * mm});
            skLineSegment(sketch, "E2.8.14.0", {"start": v(342.9, 546.1) * mm, "end": v(342.9, 571.5) * mm});
            skLineSegment(sketch, "E2.8.14.1", {"start": v(317.5, 571.5) * mm, "end": v(342.9, 571.5) * mm});
            skLineSegment(sketch, "E2.8.14.2", {"start": v(317.5, 546.1) * mm, "end": v(342.9, 546.1) * mm});
            skLineSegment(sketch, "E2.8.14.3", {"start": v(317.5, 546.1) * mm, "end": v(317.5, 571.5) * mm});
            skLineSegment(sketch, "E2.8.15.0", {"start": v(342.9, 584.2) * mm, "end": v(342.9, 609.6) * mm});
            skLineSegment(sketch, "E2.8.15.1", {"start": v(317.5, 609.6) * mm, "end": v(342.9, 609.6) * mm});
            skLineSegment(sketch, "E2.8.15.2", {"start": v(317.5, 584.2) * mm, "end": v(342.9, 584.2) * mm});
            skLineSegment(sketch, "E2.8.15.3", {"start": v(317.5, 584.2) * mm, "end": v(317.5, 609.6) * mm});
            skLineSegment(sketch, "E2.8.16.0", {"start": v(342.9, 622.3) * mm, "end": v(342.9, 647.7) * mm});
            skLineSegment(sketch, "E2.8.16.1", {"start": v(317.5, 647.7) * mm, "end": v(342.9, 647.7) * mm});
            skLineSegment(sketch, "E2.8.16.2", {"start": v(317.5, 622.3) * mm, "end": v(342.9, 622.3) * mm});
            skLineSegment(sketch, "E2.8.16.3", {"start": v(317.5, 622.3) * mm, "end": v(317.5, 647.7) * mm});
            skLineSegment(sketch, "E2.8.17.0", {"start": v(342.9, 660.4) * mm, "end": v(342.9, 685.8) * mm});
            skLineSegment(sketch, "E2.8.17.1", {"start": v(317.5, 685.8) * mm, "end": v(342.9, 685.8) * mm});
            skLineSegment(sketch, "E2.8.17.2", {"start": v(317.5, 660.4) * mm, "end": v(342.9, 660.4) * mm});
            skLineSegment(sketch, "E2.8.17.3", {"start": v(317.5, 660.4) * mm, "end": v(317.5, 685.8) * mm});
            skLineSegment(sketch, "E2.8.18.0", {"start": v(342.9, 698.5) * mm, "end": v(342.9, 723.9) * mm});
            skLineSegment(sketch, "E2.8.18.1", {"start": v(317.5, 723.9) * mm, "end": v(342.9, 723.9) * mm});
            skLineSegment(sketch, "E2.8.18.2", {"start": v(317.5, 698.5) * mm, "end": v(342.9, 698.5) * mm});
            skLineSegment(sketch, "E2.8.18.3", {"start": v(317.5, 698.5) * mm, "end": v(317.5, 723.9) * mm});
            skLineSegment(sketch, "E2.8.19.0", {"start": v(342.9, 736.6) * mm, "end": v(342.9, 762) * mm});
            skLineSegment(sketch, "E2.8.19.1", {"start": v(317.5, 762) * mm, "end": v(342.9, 762) * mm});
            skLineSegment(sketch, "E2.8.19.2", {"start": v(317.5, 736.6) * mm, "end": v(342.9, 736.6) * mm});
            skLineSegment(sketch, "E2.8.19.3", {"start": v(317.5, 736.6) * mm, "end": v(317.5, 762) * mm});
            skLineSegment(sketch, "E2.9.0.0", {"start": v(381, 12.7) * mm, "end": v(381, 38.1) * mm});
            skLineSegment(sketch, "E2.9.0.1", {"start": v(355.6, 38.1) * mm, "end": v(381, 38.1) * mm});
            skLineSegment(sketch, "E2.9.0.2", {"start": v(355.6, 12.7) * mm, "end": v(381, 12.7) * mm});
            skLineSegment(sketch, "E2.9.0.3", {"start": v(355.6, 12.7) * mm, "end": v(355.6, 38.1) * mm});
            skLineSegment(sketch, "E2.9.1.0", {"start": v(381, 50.8) * mm, "end": v(381, 76.2) * mm});
            skLineSegment(sketch, "E2.9.1.1", {"start": v(355.6, 76.2) * mm, "end": v(381, 76.2) * mm});
            skLineSegment(sketch, "E2.9.1.2", {"start": v(355.6, 50.8) * mm, "end": v(381, 50.8) * mm});
            skLineSegment(sketch, "E2.9.1.3", {"start": v(355.6, 50.8) * mm, "end": v(355.6, 76.2) * mm});
            skLineSegment(sketch, "E2.9.2.0", {"start": v(381, 88.9) * mm, "end": v(381, 114.3) * mm});
            skLineSegment(sketch, "E2.9.2.1", {"start": v(355.6, 114.3) * mm, "end": v(381, 114.3) * mm});
            skLineSegment(sketch, "E2.9.2.2", {"start": v(355.6, 88.9) * mm, "end": v(381, 88.9) * mm});
            skLineSegment(sketch, "E2.9.2.3", {"start": v(355.6, 88.9) * mm, "end": v(355.6, 114.3) * mm});
            skLineSegment(sketch, "E2.9.3.0", {"start": v(381, 127) * mm, "end": v(381, 152.4) * mm});
            skLineSegment(sketch, "E2.9.3.1", {"start": v(355.6, 152.4) * mm, "end": v(381, 152.4) * mm});
            skLineSegment(sketch, "E2.9.3.2", {"start": v(355.6, 127) * mm, "end": v(381, 127) * mm});
            skLineSegment(sketch, "E2.9.3.3", {"start": v(355.6, 127) * mm, "end": v(355.6, 152.4) * mm});
            skLineSegment(sketch, "E2.9.4.0", {"start": v(381, 165.1) * mm, "end": v(381, 190.5) * mm});
            skLineSegment(sketch, "E2.9.4.1", {"start": v(355.6, 190.5) * mm, "end": v(381, 190.5) * mm});
            skLineSegment(sketch, "E2.9.4.2", {"start": v(355.6, 165.1) * mm, "end": v(381, 165.1) * mm});
            skLineSegment(sketch, "E2.9.4.3", {"start": v(355.6, 165.1) * mm, "end": v(355.6, 190.5) * mm});
            skLineSegment(sketch, "E2.9.5.0", {"start": v(381, 203.2) * mm, "end": v(381, 228.6) * mm});
            skLineSegment(sketch, "E2.9.5.1", {"start": v(355.6, 228.6) * mm, "end": v(381, 228.6) * mm});
            skLineSegment(sketch, "E2.9.5.2", {"start": v(355.6, 203.2) * mm, "end": v(381, 203.2) * mm});
            skLineSegment(sketch, "E2.9.5.3", {"start": v(355.6, 203.2) * mm, "end": v(355.6, 228.6) * mm});
            skLineSegment(sketch, "E2.9.6.0", {"start": v(381, 241.3) * mm, "end": v(381, 266.7) * mm});
            skLineSegment(sketch, "E2.9.6.1", {"start": v(355.6, 266.7) * mm, "end": v(381, 266.7) * mm});
            skLineSegment(sketch, "E2.9.6.2", {"start": v(355.6, 241.3) * mm, "end": v(381, 241.3) * mm});
            skLineSegment(sketch, "E2.9.6.3", {"start": v(355.6, 241.3) * mm, "end": v(355.6, 266.7) * mm});
            skLineSegment(sketch, "E2.9.7.0", {"start": v(381, 279.4) * mm, "end": v(381, 304.8) * mm});
            skLineSegment(sketch, "E2.9.7.1", {"start": v(355.6, 304.8) * mm, "end": v(381, 304.8) * mm});
            skLineSegment(sketch, "E2.9.7.2", {"start": v(355.6, 279.4) * mm, "end": v(381, 279.4) * mm});
            skLineSegment(sketch, "E2.9.7.3", {"start": v(355.6, 279.4) * mm, "end": v(355.6, 304.8) * mm});
            skLineSegment(sketch, "E2.9.8.0", {"start": v(381, 317.5) * mm, "end": v(381, 342.9) * mm});
            skLineSegment(sketch, "E2.9.8.1", {"start": v(355.6, 342.9) * mm, "end": v(381, 342.9) * mm});
            skLineSegment(sketch, "E2.9.8.2", {"start": v(355.6, 317.5) * mm, "end": v(381, 317.5) * mm});
            skLineSegment(sketch, "E2.9.8.3", {"start": v(355.6, 317.5) * mm, "end": v(355.6, 342.9) * mm});
            skLineSegment(sketch, "E2.9.9.0", {"start": v(381, 355.6) * mm, "end": v(381, 381) * mm});
            skLineSegment(sketch, "E2.9.9.1", {"start": v(355.6, 381) * mm, "end": v(381, 381) * mm});
            skLineSegment(sketch, "E2.9.9.2", {"start": v(355.6, 355.6) * mm, "end": v(381, 355.6) * mm});
            skLineSegment(sketch, "E2.9.9.3", {"start": v(355.6, 355.6) * mm, "end": v(355.6, 381) * mm});
            skLineSegment(sketch, "E2.9.10.0", {"start": v(381, 393.7) * mm, "end": v(381, 419.1) * mm});
            skLineSegment(sketch, "E2.9.10.1", {"start": v(355.6, 419.1) * mm, "end": v(381, 419.1) * mm});
            skLineSegment(sketch, "E2.9.10.2", {"start": v(355.6, 393.7) * mm, "end": v(381, 393.7) * mm});
            skLineSegment(sketch, "E2.9.10.3", {"start": v(355.6, 393.7) * mm, "end": v(355.6, 419.1) * mm});
            skLineSegment(sketch, "E2.9.11.0", {"start": v(381, 431.8) * mm, "end": v(381, 457.2) * mm});
            skLineSegment(sketch, "E2.9.11.1", {"start": v(355.6, 457.2) * mm, "end": v(381, 457.2) * mm});
            skLineSegment(sketch, "E2.9.11.2", {"start": v(355.6, 431.8) * mm, "end": v(381, 431.8) * mm});
            skLineSegment(sketch, "E2.9.11.3", {"start": v(355.6, 431.8) * mm, "end": v(355.6, 457.2) * mm});
            skLineSegment(sketch, "E2.9.12.0", {"start": v(381, 469.9) * mm, "end": v(381, 495.3) * mm});
            skLineSegment(sketch, "E2.9.12.1", {"start": v(355.6, 495.3) * mm, "end": v(381, 495.3) * mm});
            skLineSegment(sketch, "E2.9.12.2", {"start": v(355.6, 469.9) * mm, "end": v(381, 469.9) * mm});
            skLineSegment(sketch, "E2.9.12.3", {"start": v(355.6, 469.9) * mm, "end": v(355.6, 495.3) * mm});
            skLineSegment(sketch, "E2.9.13.0", {"start": v(381, 508) * mm, "end": v(381, 533.4) * mm});
            skLineSegment(sketch, "E2.9.13.1", {"start": v(355.6, 533.4) * mm, "end": v(381, 533.4) * mm});
            skLineSegment(sketch, "E2.9.13.2", {"start": v(355.6, 508) * mm, "end": v(381, 508) * mm});
            skLineSegment(sketch, "E2.9.13.3", {"start": v(355.6, 508) * mm, "end": v(355.6, 533.4) * mm});
            skLineSegment(sketch, "E2.9.14.0", {"start": v(381, 546.1) * mm, "end": v(381, 571.5) * mm});
            skLineSegment(sketch, "E2.9.14.1", {"start": v(355.6, 571.5) * mm, "end": v(381, 571.5) * mm});
            skLineSegment(sketch, "E2.9.14.2", {"start": v(355.6, 546.1) * mm, "end": v(381, 546.1) * mm});
            skLineSegment(sketch, "E2.9.14.3", {"start": v(355.6, 546.1) * mm, "end": v(355.6, 571.5) * mm});
            skLineSegment(sketch, "E2.9.15.0", {"start": v(381, 584.2) * mm, "end": v(381, 609.6) * mm});
            skLineSegment(sketch, "E2.9.15.1", {"start": v(355.6, 609.6) * mm, "end": v(381, 609.6) * mm});
            skLineSegment(sketch, "E2.9.15.2", {"start": v(355.6, 584.2) * mm, "end": v(381, 584.2) * mm});
            skLineSegment(sketch, "E2.9.15.3", {"start": v(355.6, 584.2) * mm, "end": v(355.6, 609.6) * mm});
            skLineSegment(sketch, "E2.9.16.0", {"start": v(381, 622.3) * mm, "end": v(381, 647.7) * mm});
            skLineSegment(sketch, "E2.9.16.1", {"start": v(355.6, 647.7) * mm, "end": v(381, 647.7) * mm});
            skLineSegment(sketch, "E2.9.16.2", {"start": v(355.6, 622.3) * mm, "end": v(381, 622.3) * mm});
            skLineSegment(sketch, "E2.9.16.3", {"start": v(355.6, 622.3) * mm, "end": v(355.6, 647.7) * mm});
            skLineSegment(sketch, "E2.9.17.0", {"start": v(381, 660.4) * mm, "end": v(381, 685.8) * mm});
            skLineSegment(sketch, "E2.9.17.1", {"start": v(355.6, 685.8) * mm, "end": v(381, 685.8) * mm});
            skLineSegment(sketch, "E2.9.17.2", {"start": v(355.6, 660.4) * mm, "end": v(381, 660.4) * mm});
            skLineSegment(sketch, "E2.9.17.3", {"start": v(355.6, 660.4) * mm, "end": v(355.6, 685.8) * mm});
            skLineSegment(sketch, "E2.9.18.0", {"start": v(381, 698.5) * mm, "end": v(381, 723.9) * mm});
            skLineSegment(sketch, "E2.9.18.1", {"start": v(355.6, 723.9) * mm, "end": v(381, 723.9) * mm});
            skLineSegment(sketch, "E2.9.18.2", {"start": v(355.6, 698.5) * mm, "end": v(381, 698.5) * mm});
            skLineSegment(sketch, "E2.9.18.3", {"start": v(355.6, 698.5) * mm, "end": v(355.6, 723.9) * mm});
            skLineSegment(sketch, "E2.9.19.0", {"start": v(381, 736.6) * mm, "end": v(381, 762) * mm});
            skLineSegment(sketch, "E2.9.19.1", {"start": v(355.6, 762) * mm, "end": v(381, 762) * mm});
            skLineSegment(sketch, "E2.9.19.2", {"start": v(355.6, 736.6) * mm, "end": v(381, 736.6) * mm});
            skLineSegment(sketch, "E2.9.19.3", {"start": v(355.6, 736.6) * mm, "end": v(355.6, 762) * mm});
            skLineSegment(sketch, "E2.10.0.0", {"start": v(419.1, 12.7) * mm, "end": v(419.1, 38.1) * mm});
            skLineSegment(sketch, "E2.10.0.1", {"start": v(393.7, 38.1) * mm, "end": v(419.1, 38.1) * mm});
            skLineSegment(sketch, "E2.10.0.2", {"start": v(393.7, 12.7) * mm, "end": v(419.1, 12.7) * mm});
            skLineSegment(sketch, "E2.10.0.3", {"start": v(393.7, 12.7) * mm, "end": v(393.7, 38.1) * mm});
            skLineSegment(sketch, "E2.10.1.0", {"start": v(419.1, 50.8) * mm, "end": v(419.1, 76.2) * mm});
            skLineSegment(sketch, "E2.10.1.1", {"start": v(393.7, 76.2) * mm, "end": v(419.1, 76.2) * mm});
            skLineSegment(sketch, "E2.10.1.2", {"start": v(393.7, 50.8) * mm, "end": v(419.1, 50.8) * mm});
            skLineSegment(sketch, "E2.10.1.3", {"start": v(393.7, 50.8) * mm, "end": v(393.7, 76.2) * mm});
            skLineSegment(sketch, "E2.10.2.0", {"start": v(419.1, 88.9) * mm, "end": v(419.1, 114.3) * mm});
            skLineSegment(sketch, "E2.10.2.1", {"start": v(393.7, 114.3) * mm, "end": v(419.1, 114.3) * mm});
            skLineSegment(sketch, "E2.10.2.2", {"start": v(393.7, 88.9) * mm, "end": v(419.1, 88.9) * mm});
            skLineSegment(sketch, "E2.10.2.3", {"start": v(393.7, 88.9) * mm, "end": v(393.7, 114.3) * mm});
            skLineSegment(sketch, "E2.10.3.0", {"start": v(419.1, 127) * mm, "end": v(419.1, 152.4) * mm});
            skLineSegment(sketch, "E2.10.3.1", {"start": v(393.7, 152.4) * mm, "end": v(419.1, 152.4) * mm});
            skLineSegment(sketch, "E2.10.3.2", {"start": v(393.7, 127) * mm, "end": v(419.1, 127) * mm});
            skLineSegment(sketch, "E2.10.3.3", {"start": v(393.7, 127) * mm, "end": v(393.7, 152.4) * mm});
            skLineSegment(sketch, "E2.10.4.0", {"start": v(419.1, 165.1) * mm, "end": v(419.1, 190.5) * mm});
            skLineSegment(sketch, "E2.10.4.1", {"start": v(393.7, 190.5) * mm, "end": v(419.1, 190.5) * mm});
            skLineSegment(sketch, "E2.10.4.2", {"start": v(393.7, 165.1) * mm, "end": v(419.1, 165.1) * mm});
            skLineSegment(sketch, "E2.10.4.3", {"start": v(393.7, 165.1) * mm, "end": v(393.7, 190.5) * mm});
            skLineSegment(sketch, "E2.10.5.0", {"start": v(419.1, 203.2) * mm, "end": v(419.1, 228.6) * mm});
            skLineSegment(sketch, "E2.10.5.1", {"start": v(393.7, 228.6) * mm, "end": v(419.1, 228.6) * mm});
            skLineSegment(sketch, "E2.10.5.2", {"start": v(393.7, 203.2) * mm, "end": v(419.1, 203.2) * mm});
            skLineSegment(sketch, "E2.10.5.3", {"start": v(393.7, 203.2) * mm, "end": v(393.7, 228.6) * mm});
            skLineSegment(sketch, "E2.10.6.0", {"start": v(419.1, 241.3) * mm, "end": v(419.1, 266.7) * mm});
            skLineSegment(sketch, "E2.10.6.1", {"start": v(393.7, 266.7) * mm, "end": v(419.1, 266.7) * mm});
            skLineSegment(sketch, "E2.10.6.2", {"start": v(393.7, 241.3) * mm, "end": v(419.1, 241.3) * mm});
            skLineSegment(sketch, "E2.10.6.3", {"start": v(393.7, 241.3) * mm, "end": v(393.7, 266.7) * mm});
            skLineSegment(sketch, "E2.10.7.0", {"start": v(419.1, 279.4) * mm, "end": v(419.1, 304.8) * mm});
            skLineSegment(sketch, "E2.10.7.1", {"start": v(393.7, 304.8) * mm, "end": v(419.1, 304.8) * mm});
            skLineSegment(sketch, "E2.10.7.2", {"start": v(393.7, 279.4) * mm, "end": v(419.1, 279.4) * mm});
            skLineSegment(sketch, "E2.10.7.3", {"start": v(393.7, 279.4) * mm, "end": v(393.7, 304.8) * mm});
            skLineSegment(sketch, "E2.10.8.0", {"start": v(419.1, 317.5) * mm, "end": v(419.1, 342.9) * mm});
            skLineSegment(sketch, "E2.10.8.1", {"start": v(393.7, 342.9) * mm, "end": v(419.1, 342.9) * mm});
            skLineSegment(sketch, "E2.10.8.2", {"start": v(393.7, 317.5) * mm, "end": v(419.1, 317.5) * mm});
            skLineSegment(sketch, "E2.10.8.3", {"start": v(393.7, 317.5) * mm, "end": v(393.7, 342.9) * mm});
            skLineSegment(sketch, "E2.10.9.0", {"start": v(419.1, 355.6) * mm, "end": v(419.1, 381) * mm});
            skLineSegment(sketch, "E2.10.9.1", {"start": v(393.7, 381) * mm, "end": v(419.1, 381) * mm});
            skLineSegment(sketch, "E2.10.9.2", {"start": v(393.7, 355.6) * mm, "end": v(419.1, 355.6) * mm});
            skLineSegment(sketch, "E2.10.9.3", {"start": v(393.7, 355.6) * mm, "end": v(393.7, 381) * mm});
            skLineSegment(sketch, "E2.10.10.0", {"start": v(419.1, 393.7) * mm, "end": v(419.1, 419.1) * mm});
            skLineSegment(sketch, "E2.10.10.1", {"start": v(393.7, 419.1) * mm, "end": v(419.1, 419.1) * mm});
            skLineSegment(sketch, "E2.10.10.2", {"start": v(393.7, 393.7) * mm, "end": v(419.1, 393.7) * mm});
            skLineSegment(sketch, "E2.10.10.3", {"start": v(393.7, 393.7) * mm, "end": v(393.7, 419.1) * mm});
            skLineSegment(sketch, "E2.10.11.0", {"start": v(419.1, 431.8) * mm, "end": v(419.1, 457.2) * mm});
            skLineSegment(sketch, "E2.10.11.1", {"start": v(393.7, 457.2) * mm, "end": v(419.1, 457.2) * mm});
            skLineSegment(sketch, "E2.10.11.2", {"start": v(393.7, 431.8) * mm, "end": v(419.1, 431.8) * mm});
            skLineSegment(sketch, "E2.10.11.3", {"start": v(393.7, 431.8) * mm, "end": v(393.7, 457.2) * mm});
            skLineSegment(sketch, "E2.10.12.0", {"start": v(419.1, 469.9) * mm, "end": v(419.1, 495.3) * mm});
            skLineSegment(sketch, "E2.10.12.1", {"start": v(393.7, 495.3) * mm, "end": v(419.1, 495.3) * mm});
            skLineSegment(sketch, "E2.10.12.2", {"start": v(393.7, 469.9) * mm, "end": v(419.1, 469.9) * mm});
            skLineSegment(sketch, "E2.10.12.3", {"start": v(393.7, 469.9) * mm, "end": v(393.7, 495.3) * mm});
            skLineSegment(sketch, "E2.10.13.0", {"start": v(419.1, 508) * mm, "end": v(419.1, 533.4) * mm});
            skLineSegment(sketch, "E2.10.13.1", {"start": v(393.7, 533.4) * mm, "end": v(419.1, 533.4) * mm});
            skLineSegment(sketch, "E2.10.13.2", {"start": v(393.7, 508) * mm, "end": v(419.1, 508) * mm});
            skLineSegment(sketch, "E2.10.13.3", {"start": v(393.7, 508) * mm, "end": v(393.7, 533.4) * mm});
            skLineSegment(sketch, "E2.10.14.0", {"start": v(419.1, 546.1) * mm, "end": v(419.1, 571.5) * mm});
            skLineSegment(sketch, "E2.10.14.1", {"start": v(393.7, 571.5) * mm, "end": v(419.1, 571.5) * mm});
            skLineSegment(sketch, "E2.10.14.2", {"start": v(393.7, 546.1) * mm, "end": v(419.1, 546.1) * mm});
            skLineSegment(sketch, "E2.10.14.3", {"start": v(393.7, 546.1) * mm, "end": v(393.7, 571.5) * mm});
            skLineSegment(sketch, "E2.10.15.0", {"start": v(419.1, 584.2) * mm, "end": v(419.1, 609.6) * mm});
            skLineSegment(sketch, "E2.10.15.1", {"start": v(393.7, 609.6) * mm, "end": v(419.1, 609.6) * mm});
            skLineSegment(sketch, "E2.10.15.2", {"start": v(393.7, 584.2) * mm, "end": v(419.1, 584.2) * mm});
            skLineSegment(sketch, "E2.10.15.3", {"start": v(393.7, 584.2) * mm, "end": v(393.7, 609.6) * mm});
            skLineSegment(sketch, "E2.10.16.0", {"start": v(419.1, 622.3) * mm, "end": v(419.1, 647.7) * mm});
            skLineSegment(sketch, "E2.10.16.1", {"start": v(393.7, 647.7) * mm, "end": v(419.1, 647.7) * mm});
            skLineSegment(sketch, "E2.10.16.2", {"start": v(393.7, 622.3) * mm, "end": v(419.1, 622.3) * mm});
            skLineSegment(sketch, "E2.10.16.3", {"start": v(393.7, 622.3) * mm, "end": v(393.7, 647.7) * mm});
            skLineSegment(sketch, "E2.10.17.0", {"start": v(419.1, 660.4) * mm, "end": v(419.1, 685.8) * mm});
            skLineSegment(sketch, "E2.10.17.1", {"start": v(393.7, 685.8) * mm, "end": v(419.1, 685.8) * mm});
            skLineSegment(sketch, "E2.10.17.2", {"start": v(393.7, 660.4) * mm, "end": v(419.1, 660.4) * mm});
            skLineSegment(sketch, "E2.10.17.3", {"start": v(393.7, 660.4) * mm, "end": v(393.7, 685.8) * mm});
            skLineSegment(sketch, "E2.10.18.0", {"start": v(419.1, 698.5) * mm, "end": v(419.1, 723.9) * mm});
            skLineSegment(sketch, "E2.10.18.1", {"start": v(393.7, 723.9) * mm, "end": v(419.1, 723.9) * mm});
            skLineSegment(sketch, "E2.10.18.2", {"start": v(393.7, 698.5) * mm, "end": v(419.1, 698.5) * mm});
            skLineSegment(sketch, "E2.10.18.3", {"start": v(393.7, 698.5) * mm, "end": v(393.7, 723.9) * mm});
            skLineSegment(sketch, "E2.10.19.0", {"start": v(419.1, 736.6) * mm, "end": v(419.1, 762) * mm});
            skLineSegment(sketch, "E2.10.19.1", {"start": v(393.7, 762) * mm, "end": v(419.1, 762) * mm});
            skLineSegment(sketch, "E2.10.19.2", {"start": v(393.7, 736.6) * mm, "end": v(419.1, 736.6) * mm});
            skLineSegment(sketch, "E2.10.19.3", {"start": v(393.7, 736.6) * mm, "end": v(393.7, 762) * mm});
            skLineSegment(sketch, "E2.11.0.0", {"start": v(457.2, 12.7) * mm, "end": v(457.2, 38.1) * mm});
            skLineSegment(sketch, "E2.11.0.1", {"start": v(431.8, 38.1) * mm, "end": v(457.2, 38.1) * mm});
            skLineSegment(sketch, "E2.11.0.2", {"start": v(431.8, 12.7) * mm, "end": v(457.2, 12.7) * mm});
            skLineSegment(sketch, "E2.11.0.3", {"start": v(431.8, 12.7) * mm, "end": v(431.8, 38.1) * mm});
            skLineSegment(sketch, "E2.11.1.0", {"start": v(457.2, 50.8) * mm, "end": v(457.2, 76.2) * mm});
            skLineSegment(sketch, "E2.11.1.1", {"start": v(431.8, 76.2) * mm, "end": v(457.2, 76.2) * mm});
            skLineSegment(sketch, "E2.11.1.2", {"start": v(431.8, 50.8) * mm, "end": v(457.2, 50.8) * mm});
            skLineSegment(sketch, "E2.11.1.3", {"start": v(431.8, 50.8) * mm, "end": v(431.8, 76.2) * mm});
            skLineSegment(sketch, "E2.11.2.0", {"start": v(457.2, 88.9) * mm, "end": v(457.2, 114.3) * mm});
            skLineSegment(sketch, "E2.11.2.1", {"start": v(431.8, 114.3) * mm, "end": v(457.2, 114.3) * mm});
            skLineSegment(sketch, "E2.11.2.2", {"start": v(431.8, 88.9) * mm, "end": v(457.2, 88.9) * mm});
            skLineSegment(sketch, "E2.11.2.3", {"start": v(431.8, 88.9) * mm, "end": v(431.8, 114.3) * mm});
            skLineSegment(sketch, "E2.11.3.0", {"start": v(457.2, 127) * mm, "end": v(457.2, 152.4) * mm});
            skLineSegment(sketch, "E2.11.3.1", {"start": v(431.8, 152.4) * mm, "end": v(457.2, 152.4) * mm});
            skLineSegment(sketch, "E2.11.3.2", {"start": v(431.8, 127) * mm, "end": v(457.2, 127) * mm});
            skLineSegment(sketch, "E2.11.3.3", {"start": v(431.8, 127) * mm, "end": v(431.8, 152.4) * mm});
            skLineSegment(sketch, "E2.11.4.0", {"start": v(457.2, 165.1) * mm, "end": v(457.2, 190.5) * mm});
            skLineSegment(sketch, "E2.11.4.1", {"start": v(431.8, 190.5) * mm, "end": v(457.2, 190.5) * mm});
            skLineSegment(sketch, "E2.11.4.2", {"start": v(431.8, 165.1) * mm, "end": v(457.2, 165.1) * mm});
            skLineSegment(sketch, "E2.11.4.3", {"start": v(431.8, 165.1) * mm, "end": v(431.8, 190.5) * mm});
            skLineSegment(sketch, "E2.11.5.0", {"start": v(457.2, 203.2) * mm, "end": v(457.2, 228.6) * mm});
            skLineSegment(sketch, "E2.11.5.1", {"start": v(431.8, 228.6) * mm, "end": v(457.2, 228.6) * mm});
            skLineSegment(sketch, "E2.11.5.2", {"start": v(431.8, 203.2) * mm, "end": v(457.2, 203.2) * mm});
            skLineSegment(sketch, "E2.11.5.3", {"start": v(431.8, 203.2) * mm, "end": v(431.8, 228.6) * mm});
            skLineSegment(sketch, "E2.11.6.0", {"start": v(457.2, 241.3) * mm, "end": v(457.2, 266.7) * mm});
            skLineSegment(sketch, "E2.11.6.1", {"start": v(431.8, 266.7) * mm, "end": v(457.2, 266.7) * mm});
            skLineSegment(sketch, "E2.11.6.2", {"start": v(431.8, 241.3) * mm, "end": v(457.2, 241.3) * mm});
            skLineSegment(sketch, "E2.11.6.3", {"start": v(431.8, 241.3) * mm, "end": v(431.8, 266.7) * mm});
            skLineSegment(sketch, "E2.11.7.0", {"start": v(457.2, 279.4) * mm, "end": v(457.2, 304.8) * mm});
            skLineSegment(sketch, "E2.11.7.1", {"start": v(431.8, 304.8) * mm, "end": v(457.2, 304.8) * mm});
            skLineSegment(sketch, "E2.11.7.2", {"start": v(431.8, 279.4) * mm, "end": v(457.2, 279.4) * mm});
            skLineSegment(sketch, "E2.11.7.3", {"start": v(431.8, 279.4) * mm, "end": v(431.8, 304.8) * mm});
            skLineSegment(sketch, "E2.11.8.0", {"start": v(457.2, 317.5) * mm, "end": v(457.2, 342.9) * mm});
            skLineSegment(sketch, "E2.11.8.1", {"start": v(431.8, 342.9) * mm, "end": v(457.2, 342.9) * mm});
            skLineSegment(sketch, "E2.11.8.2", {"start": v(431.8, 317.5) * mm, "end": v(457.2, 317.5) * mm});
            skLineSegment(sketch, "E2.11.8.3", {"start": v(431.8, 317.5) * mm, "end": v(431.8, 342.9) * mm});
            skLineSegment(sketch, "E2.11.9.0", {"start": v(457.2, 355.6) * mm, "end": v(457.2, 381) * mm});
            skLineSegment(sketch, "E2.11.9.1", {"start": v(431.8, 381) * mm, "end": v(457.2, 381) * mm});
            skLineSegment(sketch, "E2.11.9.2", {"start": v(431.8, 355.6) * mm, "end": v(457.2, 355.6) * mm});
            skLineSegment(sketch, "E2.11.9.3", {"start": v(431.8, 355.6) * mm, "end": v(431.8, 381) * mm});
            skLineSegment(sketch, "E2.11.10.0", {"start": v(457.2, 393.7) * mm, "end": v(457.2, 419.1) * mm});
            skLineSegment(sketch, "E2.11.10.1", {"start": v(431.8, 419.1) * mm, "end": v(457.2, 419.1) * mm});
            skLineSegment(sketch, "E2.11.10.2", {"start": v(431.8, 393.7) * mm, "end": v(457.2, 393.7) * mm});
            skLineSegment(sketch, "E2.11.10.3", {"start": v(431.8, 393.7) * mm, "end": v(431.8, 419.1) * mm});
            skLineSegment(sketch, "E2.11.11.0", {"start": v(457.2, 431.8) * mm, "end": v(457.2, 457.2) * mm});
            skLineSegment(sketch, "E2.11.11.1", {"start": v(431.8, 457.2) * mm, "end": v(457.2, 457.2) * mm});
            skLineSegment(sketch, "E2.11.11.2", {"start": v(431.8, 431.8) * mm, "end": v(457.2, 431.8) * mm});
            skLineSegment(sketch, "E2.11.11.3", {"start": v(431.8, 431.8) * mm, "end": v(431.8, 457.2) * mm});
            skLineSegment(sketch, "E2.11.12.0", {"start": v(457.2, 469.9) * mm, "end": v(457.2, 495.3) * mm});
            skLineSegment(sketch, "E2.11.12.1", {"start": v(431.8, 495.3) * mm, "end": v(457.2, 495.3) * mm});
            skLineSegment(sketch, "E2.11.12.2", {"start": v(431.8, 469.9) * mm, "end": v(457.2, 469.9) * mm});
            skLineSegment(sketch, "E2.11.12.3", {"start": v(431.8, 469.9) * mm, "end": v(431.8, 495.3) * mm});
            skLineSegment(sketch, "E2.11.13.0", {"start": v(457.2, 508) * mm, "end": v(457.2, 533.4) * mm});
            skLineSegment(sketch, "E2.11.13.1", {"start": v(431.8, 533.4) * mm, "end": v(457.2, 533.4) * mm});
            skLineSegment(sketch, "E2.11.13.2", {"start": v(431.8, 508) * mm, "end": v(457.2, 508) * mm});
            skLineSegment(sketch, "E2.11.13.3", {"start": v(431.8, 508) * mm, "end": v(431.8, 533.4) * mm});
            skLineSegment(sketch, "E2.11.14.0", {"start": v(457.2, 546.1) * mm, "end": v(457.2, 571.5) * mm});
            skLineSegment(sketch, "E2.11.14.1", {"start": v(431.8, 571.5) * mm, "end": v(457.2, 571.5) * mm});
            skLineSegment(sketch, "E2.11.14.2", {"start": v(431.8, 546.1) * mm, "end": v(457.2, 546.1) * mm});
            skLineSegment(sketch, "E2.11.14.3", {"start": v(431.8, 546.1) * mm, "end": v(431.8, 571.5) * mm});
            skLineSegment(sketch, "E2.11.15.0", {"start": v(457.2, 584.2) * mm, "end": v(457.2, 609.6) * mm});
            skLineSegment(sketch, "E2.11.15.1", {"start": v(431.8, 609.6) * mm, "end": v(457.2, 609.6) * mm});
            skLineSegment(sketch, "E2.11.15.2", {"start": v(431.8, 584.2) * mm, "end": v(457.2, 584.2) * mm});
            skLineSegment(sketch, "E2.11.15.3", {"start": v(431.8, 584.2) * mm, "end": v(431.8, 609.6) * mm});
            skLineSegment(sketch, "E2.11.16.0", {"start": v(457.2, 622.3) * mm, "end": v(457.2, 647.7) * mm});
            skLineSegment(sketch, "E2.11.16.1", {"start": v(431.8, 647.7) * mm, "end": v(457.2, 647.7) * mm});
            skLineSegment(sketch, "E2.11.16.2", {"start": v(431.8, 622.3) * mm, "end": v(457.2, 622.3) * mm});
            skLineSegment(sketch, "E2.11.16.3", {"start": v(431.8, 622.3) * mm, "end": v(431.8, 647.7) * mm});
            skLineSegment(sketch, "E2.11.17.0", {"start": v(457.2, 660.4) * mm, "end": v(457.2, 685.8) * mm});
            skLineSegment(sketch, "E2.11.17.1", {"start": v(431.8, 685.8) * mm, "end": v(457.2, 685.8) * mm});
            skLineSegment(sketch, "E2.11.17.2", {"start": v(431.8, 660.4) * mm, "end": v(457.2, 660.4) * mm});
            skLineSegment(sketch, "E2.11.17.3", {"start": v(431.8, 660.4) * mm, "end": v(431.8, 685.8) * mm});
            skLineSegment(sketch, "E2.11.18.0", {"start": v(457.2, 698.5) * mm, "end": v(457.2, 723.9) * mm});
            skLineSegment(sketch, "E2.11.18.1", {"start": v(431.8, 723.9) * mm, "end": v(457.2, 723.9) * mm});
            skLineSegment(sketch, "E2.11.18.2", {"start": v(431.8, 698.5) * mm, "end": v(457.2, 698.5) * mm});
            skLineSegment(sketch, "E2.11.18.3", {"start": v(431.8, 698.5) * mm, "end": v(431.8, 723.9) * mm});
            skLineSegment(sketch, "E2.11.19.0", {"start": v(457.2, 736.6) * mm, "end": v(457.2, 762) * mm});
            skLineSegment(sketch, "E2.11.19.1", {"start": v(431.8, 762) * mm, "end": v(457.2, 762) * mm});
            skLineSegment(sketch, "E2.11.19.2", {"start": v(431.8, 736.6) * mm, "end": v(457.2, 736.6) * mm});
            skLineSegment(sketch, "E2.11.19.3", {"start": v(431.8, 736.6) * mm, "end": v(431.8, 762) * mm});
            skLineSegment(sketch, "E2.12.0.0", {"start": v(495.3, 12.7) * mm, "end": v(495.3, 38.1) * mm});
            skLineSegment(sketch, "E2.12.0.1", {"start": v(469.9, 38.1) * mm, "end": v(495.3, 38.1) * mm});
            skLineSegment(sketch, "E2.12.0.2", {"start": v(469.9, 12.7) * mm, "end": v(495.3, 12.7) * mm});
            skLineSegment(sketch, "E2.12.0.3", {"start": v(469.9, 12.7) * mm, "end": v(469.9, 38.1) * mm});
            skLineSegment(sketch, "E2.12.1.0", {"start": v(495.3, 50.8) * mm, "end": v(495.3, 76.2) * mm});
            skLineSegment(sketch, "E2.12.1.1", {"start": v(469.9, 76.2) * mm, "end": v(495.3, 76.2) * mm});
            skLineSegment(sketch, "E2.12.1.2", {"start": v(469.9, 50.8) * mm, "end": v(495.3, 50.8) * mm});
            skLineSegment(sketch, "E2.12.1.3", {"start": v(469.9, 50.8) * mm, "end": v(469.9, 76.2) * mm});
            skLineSegment(sketch, "E2.12.2.0", {"start": v(495.3, 88.9) * mm, "end": v(495.3, 114.3) * mm});
            skLineSegment(sketch, "E2.12.2.1", {"start": v(469.9, 114.3) * mm, "end": v(495.3, 114.3) * mm});
            skLineSegment(sketch, "E2.12.2.2", {"start": v(469.9, 88.9) * mm, "end": v(495.3, 88.9) * mm});
            skLineSegment(sketch, "E2.12.2.3", {"start": v(469.9, 88.9) * mm, "end": v(469.9, 114.3) * mm});
            skLineSegment(sketch, "E2.12.3.0", {"start": v(495.3, 127) * mm, "end": v(495.3, 152.4) * mm});
            skLineSegment(sketch, "E2.12.3.1", {"start": v(469.9, 152.4) * mm, "end": v(495.3, 152.4) * mm});
            skLineSegment(sketch, "E2.12.3.2", {"start": v(469.9, 127) * mm, "end": v(495.3, 127) * mm});
            skLineSegment(sketch, "E2.12.3.3", {"start": v(469.9, 127) * mm, "end": v(469.9, 152.4) * mm});
            skLineSegment(sketch, "E2.12.4.0", {"start": v(495.3, 165.1) * mm, "end": v(495.3, 190.5) * mm});
            skLineSegment(sketch, "E2.12.4.1", {"start": v(469.9, 190.5) * mm, "end": v(495.3, 190.5) * mm});
            skLineSegment(sketch, "E2.12.4.2", {"start": v(469.9, 165.1) * mm, "end": v(495.3, 165.1) * mm});
            skLineSegment(sketch, "E2.12.4.3", {"start": v(469.9, 165.1) * mm, "end": v(469.9, 190.5) * mm});
            skLineSegment(sketch, "E2.12.5.0", {"start": v(495.3, 203.2) * mm, "end": v(495.3, 228.6) * mm});
            skLineSegment(sketch, "E2.12.5.1", {"start": v(469.9, 228.6) * mm, "end": v(495.3, 228.6) * mm});
            skLineSegment(sketch, "E2.12.5.2", {"start": v(469.9, 203.2) * mm, "end": v(495.3, 203.2) * mm});
            skLineSegment(sketch, "E2.12.5.3", {"start": v(469.9, 203.2) * mm, "end": v(469.9, 228.6) * mm});
            skLineSegment(sketch, "E2.12.6.0", {"start": v(495.3, 241.3) * mm, "end": v(495.3, 266.7) * mm});
            skLineSegment(sketch, "E2.12.6.1", {"start": v(469.9, 266.7) * mm, "end": v(495.3, 266.7) * mm});
            skLineSegment(sketch, "E2.12.6.2", {"start": v(469.9, 241.3) * mm, "end": v(495.3, 241.3) * mm});
            skLineSegment(sketch, "E2.12.6.3", {"start": v(469.9, 241.3) * mm, "end": v(469.9, 266.7) * mm});
            skLineSegment(sketch, "E2.12.7.0", {"start": v(495.3, 279.4) * mm, "end": v(495.3, 304.8) * mm});
            skLineSegment(sketch, "E2.12.7.1", {"start": v(469.9, 304.8) * mm, "end": v(495.3, 304.8) * mm});
            skLineSegment(sketch, "E2.12.7.2", {"start": v(469.9, 279.4) * mm, "end": v(495.3, 279.4) * mm});
            skLineSegment(sketch, "E2.12.7.3", {"start": v(469.9, 279.4) * mm, "end": v(469.9, 304.8) * mm});
            skLineSegment(sketch, "E2.12.8.0", {"start": v(495.3, 317.5) * mm, "end": v(495.3, 342.9) * mm});
            skLineSegment(sketch, "E2.12.8.1", {"start": v(469.9, 342.9) * mm, "end": v(495.3, 342.9) * mm});
            skLineSegment(sketch, "E2.12.8.2", {"start": v(469.9, 317.5) * mm, "end": v(495.3, 317.5) * mm});
            skLineSegment(sketch, "E2.12.8.3", {"start": v(469.9, 317.5) * mm, "end": v(469.9, 342.9) * mm});
            skLineSegment(sketch, "E2.12.9.0", {"start": v(495.3, 355.6) * mm, "end": v(495.3, 381) * mm});
            skLineSegment(sketch, "E2.12.9.1", {"start": v(469.9, 381) * mm, "end": v(495.3, 381) * mm});
            skLineSegment(sketch, "E2.12.9.2", {"start": v(469.9, 355.6) * mm, "end": v(495.3, 355.6) * mm});
            skLineSegment(sketch, "E2.12.9.3", {"start": v(469.9, 355.6) * mm, "end": v(469.9, 381) * mm});
            skLineSegment(sketch, "E2.12.10.0", {"start": v(495.3, 393.7) * mm, "end": v(495.3, 419.1) * mm});
            skLineSegment(sketch, "E2.12.10.1", {"start": v(469.9, 419.1) * mm, "end": v(495.3, 419.1) * mm});
            skLineSegment(sketch, "E2.12.10.2", {"start": v(469.9, 393.7) * mm, "end": v(495.3, 393.7) * mm});
            skLineSegment(sketch, "E2.12.10.3", {"start": v(469.9, 393.7) * mm, "end": v(469.9, 419.1) * mm});
            skLineSegment(sketch, "E2.12.11.0", {"start": v(495.3, 431.8) * mm, "end": v(495.3, 457.2) * mm});
            skLineSegment(sketch, "E2.12.11.1", {"start": v(469.9, 457.2) * mm, "end": v(495.3, 457.2) * mm});
            skLineSegment(sketch, "E2.12.11.2", {"start": v(469.9, 431.8) * mm, "end": v(495.3, 431.8) * mm});
            skLineSegment(sketch, "E2.12.11.3", {"start": v(469.9, 431.8) * mm, "end": v(469.9, 457.2) * mm});
            skLineSegment(sketch, "E2.12.12.0", {"start": v(495.3, 469.9) * mm, "end": v(495.3, 495.3) * mm});
            skLineSegment(sketch, "E2.12.12.1", {"start": v(469.9, 495.3) * mm, "end": v(495.3, 495.3) * mm});
            skLineSegment(sketch, "E2.12.12.2", {"start": v(469.9, 469.9) * mm, "end": v(495.3, 469.9) * mm});
            skLineSegment(sketch, "E2.12.12.3", {"start": v(469.9, 469.9) * mm, "end": v(469.9, 495.3) * mm});
            skLineSegment(sketch, "E2.12.13.0", {"start": v(495.3, 508) * mm, "end": v(495.3, 533.4) * mm});
            skLineSegment(sketch, "E2.12.13.1", {"start": v(469.9, 533.4) * mm, "end": v(495.3, 533.4) * mm});
            skLineSegment(sketch, "E2.12.13.2", {"start": v(469.9, 508) * mm, "end": v(495.3, 508) * mm});
            skLineSegment(sketch, "E2.12.13.3", {"start": v(469.9, 508) * mm, "end": v(469.9, 533.4) * mm});
            skLineSegment(sketch, "E2.12.14.0", {"start": v(495.3, 546.1) * mm, "end": v(495.3, 571.5) * mm});
            skLineSegment(sketch, "E2.12.14.1", {"start": v(469.9, 571.5) * mm, "end": v(495.3, 571.5) * mm});
            skLineSegment(sketch, "E2.12.14.2", {"start": v(469.9, 546.1) * mm, "end": v(495.3, 546.1) * mm});
            skLineSegment(sketch, "E2.12.14.3", {"start": v(469.9, 546.1) * mm, "end": v(469.9, 571.5) * mm});
            skLineSegment(sketch, "E2.12.15.0", {"start": v(495.3, 584.2) * mm, "end": v(495.3, 609.6) * mm});
            skLineSegment(sketch, "E2.12.15.1", {"start": v(469.9, 609.6) * mm, "end": v(495.3, 609.6) * mm});
            skLineSegment(sketch, "E2.12.15.2", {"start": v(469.9, 584.2) * mm, "end": v(495.3, 584.2) * mm});
            skLineSegment(sketch, "E2.12.15.3", {"start": v(469.9, 584.2) * mm, "end": v(469.9, 609.6) * mm});
            skLineSegment(sketch, "E2.12.16.0", {"start": v(495.3, 622.3) * mm, "end": v(495.3, 647.7) * mm});
            skLineSegment(sketch, "E2.12.16.1", {"start": v(469.9, 647.7) * mm, "end": v(495.3, 647.7) * mm});
            skLineSegment(sketch, "E2.12.16.2", {"start": v(469.9, 622.3) * mm, "end": v(495.3, 622.3) * mm});
            skLineSegment(sketch, "E2.12.16.3", {"start": v(469.9, 622.3) * mm, "end": v(469.9, 647.7) * mm});
            skLineSegment(sketch, "E2.12.17.0", {"start": v(495.3, 660.4) * mm, "end": v(495.3, 685.8) * mm});
            skLineSegment(sketch, "E2.12.17.1", {"start": v(469.9, 685.8) * mm, "end": v(495.3, 685.8) * mm});
            skLineSegment(sketch, "E2.12.17.2", {"start": v(469.9, 660.4) * mm, "end": v(495.3, 660.4) * mm});
            skLineSegment(sketch, "E2.12.17.3", {"start": v(469.9, 660.4) * mm, "end": v(469.9, 685.8) * mm});
            skLineSegment(sketch, "E2.12.18.0", {"start": v(495.3, 698.5) * mm, "end": v(495.3, 723.9) * mm});
            skLineSegment(sketch, "E2.12.18.1", {"start": v(469.9, 723.9) * mm, "end": v(495.3, 723.9) * mm});
            skLineSegment(sketch, "E2.12.18.2", {"start": v(469.9, 698.5) * mm, "end": v(495.3, 698.5) * mm});
            skLineSegment(sketch, "E2.12.18.3", {"start": v(469.9, 698.5) * mm, "end": v(469.9, 723.9) * mm});
            skLineSegment(sketch, "E2.12.19.0", {"start": v(495.3, 736.6) * mm, "end": v(495.3, 762) * mm});
            skLineSegment(sketch, "E2.12.19.1", {"start": v(469.9, 762) * mm, "end": v(495.3, 762) * mm});
            skLineSegment(sketch, "E2.12.19.2", {"start": v(469.9, 736.6) * mm, "end": v(495.3, 736.6) * mm});
            skLineSegment(sketch, "E2.12.19.3", {"start": v(469.9, 736.6) * mm, "end": v(469.9, 762) * mm});
            skLineSegment(sketch, "E2.13.0.0", {"start": v(533.4, 12.7) * mm, "end": v(533.4, 38.1) * mm});
            skLineSegment(sketch, "E2.13.0.1", {"start": v(508, 38.1) * mm, "end": v(533.4, 38.1) * mm});
            skLineSegment(sketch, "E2.13.0.2", {"start": v(508, 12.7) * mm, "end": v(533.4, 12.7) * mm});
            skLineSegment(sketch, "E2.13.0.3", {"start": v(508, 12.7) * mm, "end": v(508, 38.1) * mm});
            skLineSegment(sketch, "E2.13.1.0", {"start": v(533.4, 50.8) * mm, "end": v(533.4, 76.2) * mm});
            skLineSegment(sketch, "E2.13.1.1", {"start": v(508, 76.2) * mm, "end": v(533.4, 76.2) * mm});
            skLineSegment(sketch, "E2.13.1.2", {"start": v(508, 50.8) * mm, "end": v(533.4, 50.8) * mm});
            skLineSegment(sketch, "E2.13.1.3", {"start": v(508, 50.8) * mm, "end": v(508, 76.2) * mm});
            skLineSegment(sketch, "E2.13.2.0", {"start": v(533.4, 88.9) * mm, "end": v(533.4, 114.3) * mm});
            skLineSegment(sketch, "E2.13.2.1", {"start": v(508, 114.3) * mm, "end": v(533.4, 114.3) * mm});
            skLineSegment(sketch, "E2.13.2.2", {"start": v(508, 88.9) * mm, "end": v(533.4, 88.9) * mm});
            skLineSegment(sketch, "E2.13.2.3", {"start": v(508, 88.9) * mm, "end": v(508, 114.3) * mm});
            skLineSegment(sketch, "E2.13.3.0", {"start": v(533.4, 127) * mm, "end": v(533.4, 152.4) * mm});
            skLineSegment(sketch, "E2.13.3.1", {"start": v(508, 152.4) * mm, "end": v(533.4, 152.4) * mm});
            skLineSegment(sketch, "E2.13.3.2", {"start": v(508, 127) * mm, "end": v(533.4, 127) * mm});
            skLineSegment(sketch, "E2.13.3.3", {"start": v(508, 127) * mm, "end": v(508, 152.4) * mm});
            skLineSegment(sketch, "E2.13.4.0", {"start": v(533.4, 165.1) * mm, "end": v(533.4, 190.5) * mm});
            skLineSegment(sketch, "E2.13.4.1", {"start": v(508, 190.5) * mm, "end": v(533.4, 190.5) * mm});
            skLineSegment(sketch, "E2.13.4.2", {"start": v(508, 165.1) * mm, "end": v(533.4, 165.1) * mm});
            skLineSegment(sketch, "E2.13.4.3", {"start": v(508, 165.1) * mm, "end": v(508, 190.5) * mm});
            skLineSegment(sketch, "E2.13.5.0", {"start": v(533.4, 203.2) * mm, "end": v(533.4, 228.6) * mm});
            skLineSegment(sketch, "E2.13.5.1", {"start": v(508, 228.6) * mm, "end": v(533.4, 228.6) * mm});
            skLineSegment(sketch, "E2.13.5.2", {"start": v(508, 203.2) * mm, "end": v(533.4, 203.2) * mm});
            skLineSegment(sketch, "E2.13.5.3", {"start": v(508, 203.2) * mm, "end": v(508, 228.6) * mm});
            skLineSegment(sketch, "E2.13.6.0", {"start": v(533.4, 241.3) * mm, "end": v(533.4, 266.7) * mm});
            skLineSegment(sketch, "E2.13.6.1", {"start": v(508, 266.7) * mm, "end": v(533.4, 266.7) * mm});
            skLineSegment(sketch, "E2.13.6.2", {"start": v(508, 241.3) * mm, "end": v(533.4, 241.3) * mm});
            skLineSegment(sketch, "E2.13.6.3", {"start": v(508, 241.3) * mm, "end": v(508, 266.7) * mm});
            skLineSegment(sketch, "E2.13.7.0", {"start": v(533.4, 279.4) * mm, "end": v(533.4, 304.8) * mm});
            skLineSegment(sketch, "E2.13.7.1", {"start": v(508, 304.8) * mm, "end": v(533.4, 304.8) * mm});
            skLineSegment(sketch, "E2.13.7.2", {"start": v(508, 279.4) * mm, "end": v(533.4, 279.4) * mm});
            skLineSegment(sketch, "E2.13.7.3", {"start": v(508, 279.4) * mm, "end": v(508, 304.8) * mm});
            skLineSegment(sketch, "E2.13.8.0", {"start": v(533.4, 317.5) * mm, "end": v(533.4, 342.9) * mm});
            skLineSegment(sketch, "E2.13.8.1", {"start": v(508, 342.9) * mm, "end": v(533.4, 342.9) * mm});
            skLineSegment(sketch, "E2.13.8.2", {"start": v(508, 317.5) * mm, "end": v(533.4, 317.5) * mm});
            skLineSegment(sketch, "E2.13.8.3", {"start": v(508, 317.5) * mm, "end": v(508, 342.9) * mm});
            skLineSegment(sketch, "E2.13.9.0", {"start": v(533.4, 355.6) * mm, "end": v(533.4, 381) * mm});
            skLineSegment(sketch, "E2.13.9.1", {"start": v(508, 381) * mm, "end": v(533.4, 381) * mm});
            skLineSegment(sketch, "E2.13.9.2", {"start": v(508, 355.6) * mm, "end": v(533.4, 355.6) * mm});
            skLineSegment(sketch, "E2.13.9.3", {"start": v(508, 355.6) * mm, "end": v(508, 381) * mm});
            skLineSegment(sketch, "E2.13.10.0", {"start": v(533.4, 393.7) * mm, "end": v(533.4, 419.1) * mm});
            skLineSegment(sketch, "E2.13.10.1", {"start": v(508, 419.1) * mm, "end": v(533.4, 419.1) * mm});
            skLineSegment(sketch, "E2.13.10.2", {"start": v(508, 393.7) * mm, "end": v(533.4, 393.7) * mm});
            skLineSegment(sketch, "E2.13.10.3", {"start": v(508, 393.7) * mm, "end": v(508, 419.1) * mm});
            skLineSegment(sketch, "E2.13.11.0", {"start": v(533.4, 431.8) * mm, "end": v(533.4, 457.2) * mm});
            skLineSegment(sketch, "E2.13.11.1", {"start": v(508, 457.2) * mm, "end": v(533.4, 457.2) * mm});
            skLineSegment(sketch, "E2.13.11.2", {"start": v(508, 431.8) * mm, "end": v(533.4, 431.8) * mm});
            skLineSegment(sketch, "E2.13.11.3", {"start": v(508, 431.8) * mm, "end": v(508, 457.2) * mm});
            skLineSegment(sketch, "E2.13.12.0", {"start": v(533.4, 469.9) * mm, "end": v(533.4, 495.3) * mm});
            skLineSegment(sketch, "E2.13.12.1", {"start": v(508, 495.3) * mm, "end": v(533.4, 495.3) * mm});
            skLineSegment(sketch, "E2.13.12.2", {"start": v(508, 469.9) * mm, "end": v(533.4, 469.9) * mm});
            skLineSegment(sketch, "E2.13.12.3", {"start": v(508, 469.9) * mm, "end": v(508, 495.3) * mm});
            skLineSegment(sketch, "E2.13.13.0", {"start": v(533.4, 508) * mm, "end": v(533.4, 533.4) * mm});
            skLineSegment(sketch, "E2.13.13.1", {"start": v(508, 533.4) * mm, "end": v(533.4, 533.4) * mm});
            skLineSegment(sketch, "E2.13.13.2", {"start": v(508, 508) * mm, "end": v(533.4, 508) * mm});
            skLineSegment(sketch, "E2.13.13.3", {"start": v(508, 508) * mm, "end": v(508, 533.4) * mm});
            skLineSegment(sketch, "E2.13.14.0", {"start": v(533.4, 546.1) * mm, "end": v(533.4, 571.5) * mm});
            skLineSegment(sketch, "E2.13.14.1", {"start": v(508, 571.5) * mm, "end": v(533.4, 571.5) * mm});
            skLineSegment(sketch, "E2.13.14.2", {"start": v(508, 546.1) * mm, "end": v(533.4, 546.1) * mm});
            skLineSegment(sketch, "E2.13.14.3", {"start": v(508, 546.1) * mm, "end": v(508, 571.5) * mm});
            skLineSegment(sketch, "E2.13.15.0", {"start": v(533.4, 584.2) * mm, "end": v(533.4, 609.6) * mm});
            skLineSegment(sketch, "E2.13.15.1", {"start": v(508, 609.6) * mm, "end": v(533.4, 609.6) * mm});
            skLineSegment(sketch, "E2.13.15.2", {"start": v(508, 584.2) * mm, "end": v(533.4, 584.2) * mm});
            skLineSegment(sketch, "E2.13.15.3", {"start": v(508, 584.2) * mm, "end": v(508, 609.6) * mm});
            skLineSegment(sketch, "E2.13.16.0", {"start": v(533.4, 622.3) * mm, "end": v(533.4, 647.7) * mm});
            skLineSegment(sketch, "E2.13.16.1", {"start": v(508, 647.7) * mm, "end": v(533.4, 647.7) * mm});
            skLineSegment(sketch, "E2.13.16.2", {"start": v(508, 622.3) * mm, "end": v(533.4, 622.3) * mm});
            skLineSegment(sketch, "E2.13.16.3", {"start": v(508, 622.3) * mm, "end": v(508, 647.7) * mm});
            skLineSegment(sketch, "E2.13.17.0", {"start": v(533.4, 660.4) * mm, "end": v(533.4, 685.8) * mm});
            skLineSegment(sketch, "E2.13.17.1", {"start": v(508, 685.8) * mm, "end": v(533.4, 685.8) * mm});
            skLineSegment(sketch, "E2.13.17.2", {"start": v(508, 660.4) * mm, "end": v(533.4, 660.4) * mm});
            skLineSegment(sketch, "E2.13.17.3", {"start": v(508, 660.4) * mm, "end": v(508, 685.8) * mm});
            skLineSegment(sketch, "E2.13.18.0", {"start": v(533.4, 698.5) * mm, "end": v(533.4, 723.9) * mm});
            skLineSegment(sketch, "E2.13.18.1", {"start": v(508, 723.9) * mm, "end": v(533.4, 723.9) * mm});
            skLineSegment(sketch, "E2.13.18.2", {"start": v(508, 698.5) * mm, "end": v(533.4, 698.5) * mm});
            skLineSegment(sketch, "E2.13.18.3", {"start": v(508, 698.5) * mm, "end": v(508, 723.9) * mm});
            skLineSegment(sketch, "E2.13.19.0", {"start": v(533.4, 736.6) * mm, "end": v(533.4, 762) * mm});
            skLineSegment(sketch, "E2.13.19.1", {"start": v(508, 762) * mm, "end": v(533.4, 762) * mm});
            skLineSegment(sketch, "E2.13.19.2", {"start": v(508, 736.6) * mm, "end": v(533.4, 736.6) * mm});
            skLineSegment(sketch, "E2.13.19.3", {"start": v(508, 736.6) * mm, "end": v(508, 762) * mm});
            skLineSegment(sketch, "E2.14.0.0", {"start": v(571.5, 12.7) * mm, "end": v(571.5, 38.1) * mm});
            skLineSegment(sketch, "E2.14.0.1", {"start": v(546.1, 38.1) * mm, "end": v(571.5, 38.1) * mm});
            skLineSegment(sketch, "E2.14.0.2", {"start": v(546.1, 12.7) * mm, "end": v(571.5, 12.7) * mm});
            skLineSegment(sketch, "E2.14.0.3", {"start": v(546.1, 12.7) * mm, "end": v(546.1, 38.1) * mm});
            skLineSegment(sketch, "E2.14.1.0", {"start": v(571.5, 50.8) * mm, "end": v(571.5, 76.2) * mm});
            skLineSegment(sketch, "E2.14.1.1", {"start": v(546.1, 76.2) * mm, "end": v(571.5, 76.2) * mm});
            skLineSegment(sketch, "E2.14.1.2", {"start": v(546.1, 50.8) * mm, "end": v(571.5, 50.8) * mm});
            skLineSegment(sketch, "E2.14.1.3", {"start": v(546.1, 50.8) * mm, "end": v(546.1, 76.2) * mm});
            skLineSegment(sketch, "E2.14.2.0", {"start": v(571.5, 88.9) * mm, "end": v(571.5, 114.3) * mm});
            skLineSegment(sketch, "E2.14.2.1", {"start": v(546.1, 114.3) * mm, "end": v(571.5, 114.3) * mm});
            skLineSegment(sketch, "E2.14.2.2", {"start": v(546.1, 88.9) * mm, "end": v(571.5, 88.9) * mm});
            skLineSegment(sketch, "E2.14.2.3", {"start": v(546.1, 88.9) * mm, "end": v(546.1, 114.3) * mm});
            skLineSegment(sketch, "E2.14.3.0", {"start": v(571.5, 127) * mm, "end": v(571.5, 152.4) * mm});
            skLineSegment(sketch, "E2.14.3.1", {"start": v(546.1, 152.4) * mm, "end": v(571.5, 152.4) * mm});
            skLineSegment(sketch, "E2.14.3.2", {"start": v(546.1, 127) * mm, "end": v(571.5, 127) * mm});
            skLineSegment(sketch, "E2.14.3.3", {"start": v(546.1, 127) * mm, "end": v(546.1, 152.4) * mm});
            skLineSegment(sketch, "E2.14.4.0", {"start": v(571.5, 165.1) * mm, "end": v(571.5, 190.5) * mm});
            skLineSegment(sketch, "E2.14.4.1", {"start": v(546.1, 190.5) * mm, "end": v(571.5, 190.5) * mm});
            skLineSegment(sketch, "E2.14.4.2", {"start": v(546.1, 165.1) * mm, "end": v(571.5, 165.1) * mm});
            skLineSegment(sketch, "E2.14.4.3", {"start": v(546.1, 165.1) * mm, "end": v(546.1, 190.5) * mm});
            skLineSegment(sketch, "E2.14.5.0", {"start": v(571.5, 203.2) * mm, "end": v(571.5, 228.6) * mm});
            skLineSegment(sketch, "E2.14.5.1", {"start": v(546.1, 228.6) * mm, "end": v(571.5, 228.6) * mm});
            skLineSegment(sketch, "E2.14.5.2", {"start": v(546.1, 203.2) * mm, "end": v(571.5, 203.2) * mm});
            skLineSegment(sketch, "E2.14.5.3", {"start": v(546.1, 203.2) * mm, "end": v(546.1, 228.6) * mm});
            skLineSegment(sketch, "E2.14.6.0", {"start": v(571.5, 241.3) * mm, "end": v(571.5, 266.7) * mm});
            skLineSegment(sketch, "E2.14.6.1", {"start": v(546.1, 266.7) * mm, "end": v(571.5, 266.7) * mm});
            skLineSegment(sketch, "E2.14.6.2", {"start": v(546.1, 241.3) * mm, "end": v(571.5, 241.3) * mm});
            skLineSegment(sketch, "E2.14.6.3", {"start": v(546.1, 241.3) * mm, "end": v(546.1, 266.7) * mm});
            skLineSegment(sketch, "E2.14.7.0", {"start": v(571.5, 279.4) * mm, "end": v(571.5, 304.8) * mm});
            skLineSegment(sketch, "E2.14.7.1", {"start": v(546.1, 304.8) * mm, "end": v(571.5, 304.8) * mm});
            skLineSegment(sketch, "E2.14.7.2", {"start": v(546.1, 279.4) * mm, "end": v(571.5, 279.4) * mm});
            skLineSegment(sketch, "E2.14.7.3", {"start": v(546.1, 279.4) * mm, "end": v(546.1, 304.8) * mm});
            skLineSegment(sketch, "E2.14.8.0", {"start": v(571.5, 317.5) * mm, "end": v(571.5, 342.9) * mm});
            skLineSegment(sketch, "E2.14.8.1", {"start": v(546.1, 342.9) * mm, "end": v(571.5, 342.9) * mm});
            skLineSegment(sketch, "E2.14.8.2", {"start": v(546.1, 317.5) * mm, "end": v(571.5, 317.5) * mm});
            skLineSegment(sketch, "E2.14.8.3", {"start": v(546.1, 317.5) * mm, "end": v(546.1, 342.9) * mm});
            skLineSegment(sketch, "E2.14.9.0", {"start": v(571.5, 355.6) * mm, "end": v(571.5, 381) * mm});
            skLineSegment(sketch, "E2.14.9.1", {"start": v(546.1, 381) * mm, "end": v(571.5, 381) * mm});
            skLineSegment(sketch, "E2.14.9.2", {"start": v(546.1, 355.6) * mm, "end": v(571.5, 355.6) * mm});
            skLineSegment(sketch, "E2.14.9.3", {"start": v(546.1, 355.6) * mm, "end": v(546.1, 381) * mm});
            skLineSegment(sketch, "E2.14.10.0", {"start": v(571.5, 393.7) * mm, "end": v(571.5, 419.1) * mm});
            skLineSegment(sketch, "E2.14.10.1", {"start": v(546.1, 419.1) * mm, "end": v(571.5, 419.1) * mm});
            skLineSegment(sketch, "E2.14.10.2", {"start": v(546.1, 393.7) * mm, "end": v(571.5, 393.7) * mm});
            skLineSegment(sketch, "E2.14.10.3", {"start": v(546.1, 393.7) * mm, "end": v(546.1, 419.1) * mm});
            skLineSegment(sketch, "E2.14.11.0", {"start": v(571.5, 431.8) * mm, "end": v(571.5, 457.2) * mm});
            skLineSegment(sketch, "E2.14.11.1", {"start": v(546.1, 457.2) * mm, "end": v(571.5, 457.2) * mm});
            skLineSegment(sketch, "E2.14.11.2", {"start": v(546.1, 431.8) * mm, "end": v(571.5, 431.8) * mm});
            skLineSegment(sketch, "E2.14.11.3", {"start": v(546.1, 431.8) * mm, "end": v(546.1, 457.2) * mm});
            skLineSegment(sketch, "E2.14.12.0", {"start": v(571.5, 469.9) * mm, "end": v(571.5, 495.3) * mm});
            skLineSegment(sketch, "E2.14.12.1", {"start": v(546.1, 495.3) * mm, "end": v(571.5, 495.3) * mm});
            skLineSegment(sketch, "E2.14.12.2", {"start": v(546.1, 469.9) * mm, "end": v(571.5, 469.9) * mm});
            skLineSegment(sketch, "E2.14.12.3", {"start": v(546.1, 469.9) * mm, "end": v(546.1, 495.3) * mm});
            skLineSegment(sketch, "E2.14.13.0", {"start": v(571.5, 508) * mm, "end": v(571.5, 533.4) * mm});
            skLineSegment(sketch, "E2.14.13.1", {"start": v(546.1, 533.4) * mm, "end": v(571.5, 533.4) * mm});
            skLineSegment(sketch, "E2.14.13.2", {"start": v(546.1, 508) * mm, "end": v(571.5, 508) * mm});
            skLineSegment(sketch, "E2.14.13.3", {"start": v(546.1, 508) * mm, "end": v(546.1, 533.4) * mm});
            skLineSegment(sketch, "E2.14.14.0", {"start": v(571.5, 546.1) * mm, "end": v(571.5, 571.5) * mm});
            skLineSegment(sketch, "E2.14.14.1", {"start": v(546.1, 571.5) * mm, "end": v(571.5, 571.5) * mm});
            skLineSegment(sketch, "E2.14.14.2", {"start": v(546.1, 546.1) * mm, "end": v(571.5, 546.1) * mm});
            skLineSegment(sketch, "E2.14.14.3", {"start": v(546.1, 546.1) * mm, "end": v(546.1, 571.5) * mm});
            skLineSegment(sketch, "E2.14.15.0", {"start": v(571.5, 584.2) * mm, "end": v(571.5, 609.6) * mm});
            skLineSegment(sketch, "E2.14.15.1", {"start": v(546.1, 609.6) * mm, "end": v(571.5, 609.6) * mm});
            skLineSegment(sketch, "E2.14.15.2", {"start": v(546.1, 584.2) * mm, "end": v(571.5, 584.2) * mm});
            skLineSegment(sketch, "E2.14.15.3", {"start": v(546.1, 584.2) * mm, "end": v(546.1, 609.6) * mm});
            skLineSegment(sketch, "E2.14.16.0", {"start": v(571.5, 622.3) * mm, "end": v(571.5, 647.7) * mm});
            skLineSegment(sketch, "E2.14.16.1", {"start": v(546.1, 647.7) * mm, "end": v(571.5, 647.7) * mm});
            skLineSegment(sketch, "E2.14.16.2", {"start": v(546.1, 622.3) * mm, "end": v(571.5, 622.3) * mm});
            skLineSegment(sketch, "E2.14.16.3", {"start": v(546.1, 622.3) * mm, "end": v(546.1, 647.7) * mm});
            skLineSegment(sketch, "E2.14.17.0", {"start": v(571.5, 660.4) * mm, "end": v(571.5, 685.8) * mm});
            skLineSegment(sketch, "E2.14.17.1", {"start": v(546.1, 685.8) * mm, "end": v(571.5, 685.8) * mm});
            skLineSegment(sketch, "E2.14.17.2", {"start": v(546.1, 660.4) * mm, "end": v(571.5, 660.4) * mm});
            skLineSegment(sketch, "E2.14.17.3", {"start": v(546.1, 660.4) * mm, "end": v(546.1, 685.8) * mm});
            skLineSegment(sketch, "E2.14.18.0", {"start": v(571.5, 698.5) * mm, "end": v(571.5, 723.9) * mm});
            skLineSegment(sketch, "E2.14.18.1", {"start": v(546.1, 723.9) * mm, "end": v(571.5, 723.9) * mm});
            skLineSegment(sketch, "E2.14.18.2", {"start": v(546.1, 698.5) * mm, "end": v(571.5, 698.5) * mm});
            skLineSegment(sketch, "E2.14.18.3", {"start": v(546.1, 698.5) * mm, "end": v(546.1, 723.9) * mm});
            skLineSegment(sketch, "E2.14.19.0", {"start": v(571.5, 736.6) * mm, "end": v(571.5, 762) * mm});
            skLineSegment(sketch, "E2.14.19.1", {"start": v(546.1, 762) * mm, "end": v(571.5, 762) * mm});
            skLineSegment(sketch, "E2.14.19.2", {"start": v(546.1, 736.6) * mm, "end": v(571.5, 736.6) * mm});
            skLineSegment(sketch, "E2.14.19.3", {"start": v(546.1, 736.6) * mm, "end": v(546.1, 762) * mm});
            skLineSegment(sketch, "E2.15.0.0", {"start": v(609.6, 12.7) * mm, "end": v(609.6, 38.1) * mm});
            skLineSegment(sketch, "E2.15.0.1", {"start": v(584.2, 38.1) * mm, "end": v(609.6, 38.1) * mm});
            skLineSegment(sketch, "E2.15.0.2", {"start": v(584.2, 12.7) * mm, "end": v(609.6, 12.7) * mm});
            skLineSegment(sketch, "E2.15.0.3", {"start": v(584.2, 12.7) * mm, "end": v(584.2, 38.1) * mm});
            skLineSegment(sketch, "E2.15.1.0", {"start": v(609.6, 50.8) * mm, "end": v(609.6, 76.2) * mm});
            skLineSegment(sketch, "E2.15.1.1", {"start": v(584.2, 76.2) * mm, "end": v(609.6, 76.2) * mm});
            skLineSegment(sketch, "E2.15.1.2", {"start": v(584.2, 50.8) * mm, "end": v(609.6, 50.8) * mm});
            skLineSegment(sketch, "E2.15.1.3", {"start": v(584.2, 50.8) * mm, "end": v(584.2, 76.2) * mm});
            skLineSegment(sketch, "E2.15.2.0", {"start": v(609.6, 88.9) * mm, "end": v(609.6, 114.3) * mm});
            skLineSegment(sketch, "E2.15.2.1", {"start": v(584.2, 114.3) * mm, "end": v(609.6, 114.3) * mm});
            skLineSegment(sketch, "E2.15.2.2", {"start": v(584.2, 88.9) * mm, "end": v(609.6, 88.9) * mm});
            skLineSegment(sketch, "E2.15.2.3", {"start": v(584.2, 88.9) * mm, "end": v(584.2, 114.3) * mm});
            skLineSegment(sketch, "E2.15.3.0", {"start": v(609.6, 127) * mm, "end": v(609.6, 152.4) * mm});
            skLineSegment(sketch, "E2.15.3.1", {"start": v(584.2, 152.4) * mm, "end": v(609.6, 152.4) * mm});
            skLineSegment(sketch, "E2.15.3.2", {"start": v(584.2, 127) * mm, "end": v(609.6, 127) * mm});
            skLineSegment(sketch, "E2.15.3.3", {"start": v(584.2, 127) * mm, "end": v(584.2, 152.4) * mm});
            skLineSegment(sketch, "E2.15.4.0", {"start": v(609.6, 165.1) * mm, "end": v(609.6, 190.5) * mm});
            skLineSegment(sketch, "E2.15.4.1", {"start": v(584.2, 190.5) * mm, "end": v(609.6, 190.5) * mm});
            skLineSegment(sketch, "E2.15.4.2", {"start": v(584.2, 165.1) * mm, "end": v(609.6, 165.1) * mm});
            skLineSegment(sketch, "E2.15.4.3", {"start": v(584.2, 165.1) * mm, "end": v(584.2, 190.5) * mm});
            skLineSegment(sketch, "E2.15.5.0", {"start": v(609.6, 203.2) * mm, "end": v(609.6, 228.6) * mm});
            skLineSegment(sketch, "E2.15.5.1", {"start": v(584.2, 228.6) * mm, "end": v(609.6, 228.6) * mm});
            skLineSegment(sketch, "E2.15.5.2", {"start": v(584.2, 203.2) * mm, "end": v(609.6, 203.2) * mm});
            skLineSegment(sketch, "E2.15.5.3", {"start": v(584.2, 203.2) * mm, "end": v(584.2, 228.6) * mm});
            skLineSegment(sketch, "E2.15.6.0", {"start": v(609.6, 241.3) * mm, "end": v(609.6, 266.7) * mm});
            skLineSegment(sketch, "E2.15.6.1", {"start": v(584.2, 266.7) * mm, "end": v(609.6, 266.7) * mm});
            skLineSegment(sketch, "E2.15.6.2", {"start": v(584.2, 241.3) * mm, "end": v(609.6, 241.3) * mm});
            skLineSegment(sketch, "E2.15.6.3", {"start": v(584.2, 241.3) * mm, "end": v(584.2, 266.7) * mm});
            skLineSegment(sketch, "E2.15.7.0", {"start": v(609.6, 279.4) * mm, "end": v(609.6, 304.8) * mm});
            skLineSegment(sketch, "E2.15.7.1", {"start": v(584.2, 304.8) * mm, "end": v(609.6, 304.8) * mm});
            skLineSegment(sketch, "E2.15.7.2", {"start": v(584.2, 279.4) * mm, "end": v(609.6, 279.4) * mm});
            skLineSegment(sketch, "E2.15.7.3", {"start": v(584.2, 279.4) * mm, "end": v(584.2, 304.8) * mm});
            skLineSegment(sketch, "E2.15.8.0", {"start": v(609.6, 317.5) * mm, "end": v(609.6, 342.9) * mm});
            skLineSegment(sketch, "E2.15.8.1", {"start": v(584.2, 342.9) * mm, "end": v(609.6, 342.9) * mm});
            skLineSegment(sketch, "E2.15.8.2", {"start": v(584.2, 317.5) * mm, "end": v(609.6, 317.5) * mm});
            skLineSegment(sketch, "E2.15.8.3", {"start": v(584.2, 317.5) * mm, "end": v(584.2, 342.9) * mm});
            skLineSegment(sketch, "E2.15.9.0", {"start": v(609.6, 355.6) * mm, "end": v(609.6, 381) * mm});
            skLineSegment(sketch, "E2.15.9.1", {"start": v(584.2, 381) * mm, "end": v(609.6, 381) * mm});
            skLineSegment(sketch, "E2.15.9.2", {"start": v(584.2, 355.6) * mm, "end": v(609.6, 355.6) * mm});
            skLineSegment(sketch, "E2.15.9.3", {"start": v(584.2, 355.6) * mm, "end": v(584.2, 381) * mm});
            skLineSegment(sketch, "E2.15.10.0", {"start": v(609.6, 393.7) * mm, "end": v(609.6, 419.1) * mm});
            skLineSegment(sketch, "E2.15.10.1", {"start": v(584.2, 419.1) * mm, "end": v(609.6, 419.1) * mm});
            skLineSegment(sketch, "E2.15.10.2", {"start": v(584.2, 393.7) * mm, "end": v(609.6, 393.7) * mm});
            skLineSegment(sketch, "E2.15.10.3", {"start": v(584.2, 393.7) * mm, "end": v(584.2, 419.1) * mm});
            skLineSegment(sketch, "E2.15.11.0", {"start": v(609.6, 431.8) * mm, "end": v(609.6, 457.2) * mm});
            skLineSegment(sketch, "E2.15.11.1", {"start": v(584.2, 457.2) * mm, "end": v(609.6, 457.2) * mm});
            skLineSegment(sketch, "E2.15.11.2", {"start": v(584.2, 431.8) * mm, "end": v(609.6, 431.8) * mm});
            skLineSegment(sketch, "E2.15.11.3", {"start": v(584.2, 431.8) * mm, "end": v(584.2, 457.2) * mm});
            skLineSegment(sketch, "E2.15.12.0", {"start": v(609.6, 469.9) * mm, "end": v(609.6, 495.3) * mm});
            skLineSegment(sketch, "E2.15.12.1", {"start": v(584.2, 495.3) * mm, "end": v(609.6, 495.3) * mm});
            skLineSegment(sketch, "E2.15.12.2", {"start": v(584.2, 469.9) * mm, "end": v(609.6, 469.9) * mm});
            skLineSegment(sketch, "E2.15.12.3", {"start": v(584.2, 469.9) * mm, "end": v(584.2, 495.3) * mm});
            skLineSegment(sketch, "E2.15.13.0", {"start": v(609.6, 508) * mm, "end": v(609.6, 533.4) * mm});
            skLineSegment(sketch, "E2.15.13.1", {"start": v(584.2, 533.4) * mm, "end": v(609.6, 533.4) * mm});
            skLineSegment(sketch, "E2.15.13.2", {"start": v(584.2, 508) * mm, "end": v(609.6, 508) * mm});
            skLineSegment(sketch, "E2.15.13.3", {"start": v(584.2, 508) * mm, "end": v(584.2, 533.4) * mm});
            skLineSegment(sketch, "E2.15.14.0", {"start": v(609.6, 546.1) * mm, "end": v(609.6, 571.5) * mm});
            skLineSegment(sketch, "E2.15.14.1", {"start": v(584.2, 571.5) * mm, "end": v(609.6, 571.5) * mm});
            skLineSegment(sketch, "E2.15.14.2", {"start": v(584.2, 546.1) * mm, "end": v(609.6, 546.1) * mm});
            skLineSegment(sketch, "E2.15.14.3", {"start": v(584.2, 546.1) * mm, "end": v(584.2, 571.5) * mm});
            skLineSegment(sketch, "E2.15.15.0", {"start": v(609.6, 584.2) * mm, "end": v(609.6, 609.6) * mm});
            skLineSegment(sketch, "E2.15.15.1", {"start": v(584.2, 609.6) * mm, "end": v(609.6, 609.6) * mm});
            skLineSegment(sketch, "E2.15.15.2", {"start": v(584.2, 584.2) * mm, "end": v(609.6, 584.2) * mm});
            skLineSegment(sketch, "E2.15.15.3", {"start": v(584.2, 584.2) * mm, "end": v(584.2, 609.6) * mm});
            skLineSegment(sketch, "E2.15.16.0", {"start": v(609.6, 622.3) * mm, "end": v(609.6, 647.7) * mm});
            skLineSegment(sketch, "E2.15.16.1", {"start": v(584.2, 647.7) * mm, "end": v(609.6, 647.7) * mm});
            skLineSegment(sketch, "E2.15.16.2", {"start": v(584.2, 622.3) * mm, "end": v(609.6, 622.3) * mm});
            skLineSegment(sketch, "E2.15.16.3", {"start": v(584.2, 622.3) * mm, "end": v(584.2, 647.7) * mm});
            skLineSegment(sketch, "E2.15.17.0", {"start": v(609.6, 660.4) * mm, "end": v(609.6, 685.8) * mm});
            skLineSegment(sketch, "E2.15.17.1", {"start": v(584.2, 685.8) * mm, "end": v(609.6, 685.8) * mm});
            skLineSegment(sketch, "E2.15.17.2", {"start": v(584.2, 660.4) * mm, "end": v(609.6, 660.4) * mm});
            skLineSegment(sketch, "E2.15.17.3", {"start": v(584.2, 660.4) * mm, "end": v(584.2, 685.8) * mm});
            skLineSegment(sketch, "E2.15.18.0", {"start": v(609.6, 698.5) * mm, "end": v(609.6, 723.9) * mm});
            skLineSegment(sketch, "E2.15.18.1", {"start": v(584.2, 723.9) * mm, "end": v(609.6, 723.9) * mm});
            skLineSegment(sketch, "E2.15.18.2", {"start": v(584.2, 698.5) * mm, "end": v(609.6, 698.5) * mm});
            skLineSegment(sketch, "E2.15.18.3", {"start": v(584.2, 698.5) * mm, "end": v(584.2, 723.9) * mm});
            skLineSegment(sketch, "E2.15.19.0", {"start": v(609.6, 736.6) * mm, "end": v(609.6, 762) * mm});
            skLineSegment(sketch, "E2.15.19.1", {"start": v(584.2, 762) * mm, "end": v(609.6, 762) * mm});
            skLineSegment(sketch, "E2.15.19.2", {"start": v(584.2, 736.6) * mm, "end": v(609.6, 736.6) * mm});
            skLineSegment(sketch, "E2.15.19.3", {"start": v(584.2, 736.6) * mm, "end": v(584.2, 762) * mm});
            skLineSegment(sketch, "E2.16.0.0", {"start": v(647.7, 12.7) * mm, "end": v(647.7, 38.1) * mm});
            skLineSegment(sketch, "E2.16.0.1", {"start": v(622.3, 38.1) * mm, "end": v(647.7, 38.1) * mm});
            skLineSegment(sketch, "E2.16.0.2", {"start": v(622.3, 12.7) * mm, "end": v(647.7, 12.7) * mm});
            skLineSegment(sketch, "E2.16.0.3", {"start": v(622.3, 12.7) * mm, "end": v(622.3, 38.1) * mm});
            skLineSegment(sketch, "E2.16.1.0", {"start": v(647.7, 50.8) * mm, "end": v(647.7, 76.2) * mm});
            skLineSegment(sketch, "E2.16.1.1", {"start": v(622.3, 76.2) * mm, "end": v(647.7, 76.2) * mm});
            skLineSegment(sketch, "E2.16.1.2", {"start": v(622.3, 50.8) * mm, "end": v(647.7, 50.8) * mm});
            skLineSegment(sketch, "E2.16.1.3", {"start": v(622.3, 50.8) * mm, "end": v(622.3, 76.2) * mm});
            skLineSegment(sketch, "E2.16.2.0", {"start": v(647.7, 88.9) * mm, "end": v(647.7, 114.3) * mm});
            skLineSegment(sketch, "E2.16.2.1", {"start": v(622.3, 114.3) * mm, "end": v(647.7, 114.3) * mm});
            skLineSegment(sketch, "E2.16.2.2", {"start": v(622.3, 88.9) * mm, "end": v(647.7, 88.9) * mm});
            skLineSegment(sketch, "E2.16.2.3", {"start": v(622.3, 88.9) * mm, "end": v(622.3, 114.3) * mm});
            skLineSegment(sketch, "E2.16.3.0", {"start": v(647.7, 127) * mm, "end": v(647.7, 152.4) * mm});
            skLineSegment(sketch, "E2.16.3.1", {"start": v(622.3, 152.4) * mm, "end": v(647.7, 152.4) * mm});
            skLineSegment(sketch, "E2.16.3.2", {"start": v(622.3, 127) * mm, "end": v(647.7, 127) * mm});
            skLineSegment(sketch, "E2.16.3.3", {"start": v(622.3, 127) * mm, "end": v(622.3, 152.4) * mm});
            skLineSegment(sketch, "E2.16.4.0", {"start": v(647.7, 165.1) * mm, "end": v(647.7, 190.5) * mm});
            skLineSegment(sketch, "E2.16.4.1", {"start": v(622.3, 190.5) * mm, "end": v(647.7, 190.5) * mm});
            skLineSegment(sketch, "E2.16.4.2", {"start": v(622.3, 165.1) * mm, "end": v(647.7, 165.1) * mm});
            skLineSegment(sketch, "E2.16.4.3", {"start": v(622.3, 165.1) * mm, "end": v(622.3, 190.5) * mm});
            skLineSegment(sketch, "E2.16.5.0", {"start": v(647.7, 203.2) * mm, "end": v(647.7, 228.6) * mm});
            skLineSegment(sketch, "E2.16.5.1", {"start": v(622.3, 228.6) * mm, "end": v(647.7, 228.6) * mm});
            skLineSegment(sketch, "E2.16.5.2", {"start": v(622.3, 203.2) * mm, "end": v(647.7, 203.2) * mm});
            skLineSegment(sketch, "E2.16.5.3", {"start": v(622.3, 203.2) * mm, "end": v(622.3, 228.6) * mm});
            skLineSegment(sketch, "E2.16.6.0", {"start": v(647.7, 241.3) * mm, "end": v(647.7, 266.7) * mm});
            skLineSegment(sketch, "E2.16.6.1", {"start": v(622.3, 266.7) * mm, "end": v(647.7, 266.7) * mm});
            skLineSegment(sketch, "E2.16.6.2", {"start": v(622.3, 241.3) * mm, "end": v(647.7, 241.3) * mm});
            skLineSegment(sketch, "E2.16.6.3", {"start": v(622.3, 241.3) * mm, "end": v(622.3, 266.7) * mm});
            skLineSegment(sketch, "E2.16.7.0", {"start": v(647.7, 279.4) * mm, "end": v(647.7, 304.8) * mm});
            skLineSegment(sketch, "E2.16.7.1", {"start": v(622.3, 304.8) * mm, "end": v(647.7, 304.8) * mm});
            skLineSegment(sketch, "E2.16.7.2", {"start": v(622.3, 279.4) * mm, "end": v(647.7, 279.4) * mm});
            skLineSegment(sketch, "E2.16.7.3", {"start": v(622.3, 279.4) * mm, "end": v(622.3, 304.8) * mm});
            skLineSegment(sketch, "E2.16.8.0", {"start": v(647.7, 317.5) * mm, "end": v(647.7, 342.9) * mm});
            skLineSegment(sketch, "E2.16.8.1", {"start": v(622.3, 342.9) * mm, "end": v(647.7, 342.9) * mm});
            skLineSegment(sketch, "E2.16.8.2", {"start": v(622.3, 317.5) * mm, "end": v(647.7, 317.5) * mm});
            skLineSegment(sketch, "E2.16.8.3", {"start": v(622.3, 317.5) * mm, "end": v(622.3, 342.9) * mm});
            skLineSegment(sketch, "E2.16.9.0", {"start": v(647.7, 355.6) * mm, "end": v(647.7, 381) * mm});
            skLineSegment(sketch, "E2.16.9.1", {"start": v(622.3, 381) * mm, "end": v(647.7, 381) * mm});
            skLineSegment(sketch, "E2.16.9.2", {"start": v(622.3, 355.6) * mm, "end": v(647.7, 355.6) * mm});
            skLineSegment(sketch, "E2.16.9.3", {"start": v(622.3, 355.6) * mm, "end": v(622.3, 381) * mm});
            skLineSegment(sketch, "E2.16.10.0", {"start": v(647.7, 393.7) * mm, "end": v(647.7, 419.1) * mm});
            skLineSegment(sketch, "E2.16.10.1", {"start": v(622.3, 419.1) * mm, "end": v(647.7, 419.1) * mm});
            skLineSegment(sketch, "E2.16.10.2", {"start": v(622.3, 393.7) * mm, "end": v(647.7, 393.7) * mm});
            skLineSegment(sketch, "E2.16.10.3", {"start": v(622.3, 393.7) * mm, "end": v(622.3, 419.1) * mm});
            skLineSegment(sketch, "E2.16.11.0", {"start": v(647.7, 431.8) * mm, "end": v(647.7, 457.2) * mm});
            skLineSegment(sketch, "E2.16.11.1", {"start": v(622.3, 457.2) * mm, "end": v(647.7, 457.2) * mm});
            skLineSegment(sketch, "E2.16.11.2", {"start": v(622.3, 431.8) * mm, "end": v(647.7, 431.8) * mm});
            skLineSegment(sketch, "E2.16.11.3", {"start": v(622.3, 431.8) * mm, "end": v(622.3, 457.2) * mm});
            skLineSegment(sketch, "E2.16.12.0", {"start": v(647.7, 469.9) * mm, "end": v(647.7, 495.3) * mm});
            skLineSegment(sketch, "E2.16.12.1", {"start": v(622.3, 495.3) * mm, "end": v(647.7, 495.3) * mm});
            skLineSegment(sketch, "E2.16.12.2", {"start": v(622.3, 469.9) * mm, "end": v(647.7, 469.9) * mm});
            skLineSegment(sketch, "E2.16.12.3", {"start": v(622.3, 469.9) * mm, "end": v(622.3, 495.3) * mm});
            skLineSegment(sketch, "E2.16.13.0", {"start": v(647.7, 508) * mm, "end": v(647.7, 533.4) * mm});
            skLineSegment(sketch, "E2.16.13.1", {"start": v(622.3, 533.4) * mm, "end": v(647.7, 533.4) * mm});
            skLineSegment(sketch, "E2.16.13.2", {"start": v(622.3, 508) * mm, "end": v(647.7, 508) * mm});
            skLineSegment(sketch, "E2.16.13.3", {"start": v(622.3, 508) * mm, "end": v(622.3, 533.4) * mm});
            skLineSegment(sketch, "E2.16.14.0", {"start": v(647.7, 546.1) * mm, "end": v(647.7, 571.5) * mm});
            skLineSegment(sketch, "E2.16.14.1", {"start": v(622.3, 571.5) * mm, "end": v(647.7, 571.5) * mm});
            skLineSegment(sketch, "E2.16.14.2", {"start": v(622.3, 546.1) * mm, "end": v(647.7, 546.1) * mm});
            skLineSegment(sketch, "E2.16.14.3", {"start": v(622.3, 546.1) * mm, "end": v(622.3, 571.5) * mm});
            skLineSegment(sketch, "E2.16.15.0", {"start": v(647.7, 584.2) * mm, "end": v(647.7, 609.6) * mm});
            skLineSegment(sketch, "E2.16.15.1", {"start": v(622.3, 609.6) * mm, "end": v(647.7, 609.6) * mm});
            skLineSegment(sketch, "E2.16.15.2", {"start": v(622.3, 584.2) * mm, "end": v(647.7, 584.2) * mm});
            skLineSegment(sketch, "E2.16.15.3", {"start": v(622.3, 584.2) * mm, "end": v(622.3, 609.6) * mm});
            skLineSegment(sketch, "E2.16.16.0", {"start": v(647.7, 622.3) * mm, "end": v(647.7, 647.7) * mm});
            skLineSegment(sketch, "E2.16.16.1", {"start": v(622.3, 647.7) * mm, "end": v(647.7, 647.7) * mm});
            skLineSegment(sketch, "E2.16.16.2", {"start": v(622.3, 622.3) * mm, "end": v(647.7, 622.3) * mm});
            skLineSegment(sketch, "E2.16.16.3", {"start": v(622.3, 622.3) * mm, "end": v(622.3, 647.7) * mm});
            skLineSegment(sketch, "E2.16.17.0", {"start": v(647.7, 660.4) * mm, "end": v(647.7, 685.8) * mm});
            skLineSegment(sketch, "E2.16.17.1", {"start": v(622.3, 685.8) * mm, "end": v(647.7, 685.8) * mm});
            skLineSegment(sketch, "E2.16.17.2", {"start": v(622.3, 660.4) * mm, "end": v(647.7, 660.4) * mm});
            skLineSegment(sketch, "E2.16.17.3", {"start": v(622.3, 660.4) * mm, "end": v(622.3, 685.8) * mm});
            skLineSegment(sketch, "E2.16.18.0", {"start": v(647.7, 698.5) * mm, "end": v(647.7, 723.9) * mm});
            skLineSegment(sketch, "E2.16.18.1", {"start": v(622.3, 723.9) * mm, "end": v(647.7, 723.9) * mm});
            skLineSegment(sketch, "E2.16.18.2", {"start": v(622.3, 698.5) * mm, "end": v(647.7, 698.5) * mm});
            skLineSegment(sketch, "E2.16.18.3", {"start": v(622.3, 698.5) * mm, "end": v(622.3, 723.9) * mm});
            skLineSegment(sketch, "E2.16.19.0", {"start": v(647.7, 736.6) * mm, "end": v(647.7, 762) * mm});
            skLineSegment(sketch, "E2.16.19.1", {"start": v(622.3, 762) * mm, "end": v(647.7, 762) * mm});
            skLineSegment(sketch, "E2.16.19.2", {"start": v(622.3, 736.6) * mm, "end": v(647.7, 736.6) * mm});
            skLineSegment(sketch, "E2.16.19.3", {"start": v(622.3, 736.6) * mm, "end": v(622.3, 762) * mm});
            skLineSegment(sketch, "E2.17.0.0", {"start": v(685.8, 12.7) * mm, "end": v(685.8, 38.1) * mm});
            skLineSegment(sketch, "E2.17.0.1", {"start": v(660.4, 38.1) * mm, "end": v(685.8, 38.1) * mm});
            skLineSegment(sketch, "E2.17.0.2", {"start": v(660.4, 12.7) * mm, "end": v(685.8, 12.7) * mm});
            skLineSegment(sketch, "E2.17.0.3", {"start": v(660.4, 12.7) * mm, "end": v(660.4, 38.1) * mm});
            skLineSegment(sketch, "E2.17.1.0", {"start": v(685.8, 50.8) * mm, "end": v(685.8, 76.2) * mm});
            skLineSegment(sketch, "E2.17.1.1", {"start": v(660.4, 76.2) * mm, "end": v(685.8, 76.2) * mm});
            skLineSegment(sketch, "E2.17.1.2", {"start": v(660.4, 50.8) * mm, "end": v(685.8, 50.8) * mm});
            skLineSegment(sketch, "E2.17.1.3", {"start": v(660.4, 50.8) * mm, "end": v(660.4, 76.2) * mm});
            skLineSegment(sketch, "E2.17.2.0", {"start": v(685.8, 88.9) * mm, "end": v(685.8, 114.3) * mm});
            skLineSegment(sketch, "E2.17.2.1", {"start": v(660.4, 114.3) * mm, "end": v(685.8, 114.3) * mm});
            skLineSegment(sketch, "E2.17.2.2", {"start": v(660.4, 88.9) * mm, "end": v(685.8, 88.9) * mm});
            skLineSegment(sketch, "E2.17.2.3", {"start": v(660.4, 88.9) * mm, "end": v(660.4, 114.3) * mm});
            skLineSegment(sketch, "E2.17.3.0", {"start": v(685.8, 127) * mm, "end": v(685.8, 152.4) * mm});
            skLineSegment(sketch, "E2.17.3.1", {"start": v(660.4, 152.4) * mm, "end": v(685.8, 152.4) * mm});
            skLineSegment(sketch, "E2.17.3.2", {"start": v(660.4, 127) * mm, "end": v(685.8, 127) * mm});
            skLineSegment(sketch, "E2.17.3.3", {"start": v(660.4, 127) * mm, "end": v(660.4, 152.4) * mm});
            skLineSegment(sketch, "E2.17.4.0", {"start": v(685.8, 165.1) * mm, "end": v(685.8, 190.5) * mm});
            skLineSegment(sketch, "E2.17.4.1", {"start": v(660.4, 190.5) * mm, "end": v(685.8, 190.5) * mm});
            skLineSegment(sketch, "E2.17.4.2", {"start": v(660.4, 165.1) * mm, "end": v(685.8, 165.1) * mm});
            skLineSegment(sketch, "E2.17.4.3", {"start": v(660.4, 165.1) * mm, "end": v(660.4, 190.5) * mm});
            skLineSegment(sketch, "E2.17.5.0", {"start": v(685.8, 203.2) * mm, "end": v(685.8, 228.6) * mm});
            skLineSegment(sketch, "E2.17.5.1", {"start": v(660.4, 228.6) * mm, "end": v(685.8, 228.6) * mm});
            skLineSegment(sketch, "E2.17.5.2", {"start": v(660.4, 203.2) * mm, "end": v(685.8, 203.2) * mm});
            skLineSegment(sketch, "E2.17.5.3", {"start": v(660.4, 203.2) * mm, "end": v(660.4, 228.6) * mm});
            skLineSegment(sketch, "E2.17.6.0", {"start": v(685.8, 241.3) * mm, "end": v(685.8, 266.7) * mm});
            skLineSegment(sketch, "E2.17.6.1", {"start": v(660.4, 266.7) * mm, "end": v(685.8, 266.7) * mm});
            skLineSegment(sketch, "E2.17.6.2", {"start": v(660.4, 241.3) * mm, "end": v(685.8, 241.3) * mm});
            skLineSegment(sketch, "E2.17.6.3", {"start": v(660.4, 241.3) * mm, "end": v(660.4, 266.7) * mm});
            skLineSegment(sketch, "E2.17.7.0", {"start": v(685.8, 279.4) * mm, "end": v(685.8, 304.8) * mm});
            skLineSegment(sketch, "E2.17.7.1", {"start": v(660.4, 304.8) * mm, "end": v(685.8, 304.8) * mm});
            skLineSegment(sketch, "E2.17.7.2", {"start": v(660.4, 279.4) * mm, "end": v(685.8, 279.4) * mm});
            skLineSegment(sketch, "E2.17.7.3", {"start": v(660.4, 279.4) * mm, "end": v(660.4, 304.8) * mm});
            skLineSegment(sketch, "E2.17.8.0", {"start": v(685.8, 317.5) * mm, "end": v(685.8, 342.9) * mm});
            skLineSegment(sketch, "E2.17.8.1", {"start": v(660.4, 342.9) * mm, "end": v(685.8, 342.9) * mm});
            skLineSegment(sketch, "E2.17.8.2", {"start": v(660.4, 317.5) * mm, "end": v(685.8, 317.5) * mm});
            skLineSegment(sketch, "E2.17.8.3", {"start": v(660.4, 317.5) * mm, "end": v(660.4, 342.9) * mm});
            skLineSegment(sketch, "E2.17.9.0", {"start": v(685.8, 355.6) * mm, "end": v(685.8, 381) * mm});
            skLineSegment(sketch, "E2.17.9.1", {"start": v(660.4, 381) * mm, "end": v(685.8, 381) * mm});
            skLineSegment(sketch, "E2.17.9.2", {"start": v(660.4, 355.6) * mm, "end": v(685.8, 355.6) * mm});
            skLineSegment(sketch, "E2.17.9.3", {"start": v(660.4, 355.6) * mm, "end": v(660.4, 381) * mm});
            skLineSegment(sketch, "E2.17.10.0", {"start": v(685.8, 393.7) * mm, "end": v(685.8, 419.1) * mm});
            skLineSegment(sketch, "E2.17.10.1", {"start": v(660.4, 419.1) * mm, "end": v(685.8, 419.1) * mm});
            skLineSegment(sketch, "E2.17.10.2", {"start": v(660.4, 393.7) * mm, "end": v(685.8, 393.7) * mm});
            skLineSegment(sketch, "E2.17.10.3", {"start": v(660.4, 393.7) * mm, "end": v(660.4, 419.1) * mm});
            skLineSegment(sketch, "E2.17.11.0", {"start": v(685.8, 431.8) * mm, "end": v(685.8, 457.2) * mm});
            skLineSegment(sketch, "E2.17.11.1", {"start": v(660.4, 457.2) * mm, "end": v(685.8, 457.2) * mm});
            skLineSegment(sketch, "E2.17.11.2", {"start": v(660.4, 431.8) * mm, "end": v(685.8, 431.8) * mm});
            skLineSegment(sketch, "E2.17.11.3", {"start": v(660.4, 431.8) * mm, "end": v(660.4, 457.2) * mm});
            skLineSegment(sketch, "E2.17.12.0", {"start": v(685.8, 469.9) * mm, "end": v(685.8, 495.3) * mm});
            skLineSegment(sketch, "E2.17.12.1", {"start": v(660.4, 495.3) * mm, "end": v(685.8, 495.3) * mm});
            skLineSegment(sketch, "E2.17.12.2", {"start": v(660.4, 469.9) * mm, "end": v(685.8, 469.9) * mm});
            skLineSegment(sketch, "E2.17.12.3", {"start": v(660.4, 469.9) * mm, "end": v(660.4, 495.3) * mm});
            skLineSegment(sketch, "E2.17.13.0", {"start": v(685.8, 508) * mm, "end": v(685.8, 533.4) * mm});
            skLineSegment(sketch, "E2.17.13.1", {"start": v(660.4, 533.4) * mm, "end": v(685.8, 533.4) * mm});
            skLineSegment(sketch, "E2.17.13.2", {"start": v(660.4, 508) * mm, "end": v(685.8, 508) * mm});
            skLineSegment(sketch, "E2.17.13.3", {"start": v(660.4, 508) * mm, "end": v(660.4, 533.4) * mm});
            skLineSegment(sketch, "E2.17.14.0", {"start": v(685.8, 546.1) * mm, "end": v(685.8, 571.5) * mm});
            skLineSegment(sketch, "E2.17.14.1", {"start": v(660.4, 571.5) * mm, "end": v(685.8, 571.5) * mm});
            skLineSegment(sketch, "E2.17.14.2", {"start": v(660.4, 546.1) * mm, "end": v(685.8, 546.1) * mm});
            skLineSegment(sketch, "E2.17.14.3", {"start": v(660.4, 546.1) * mm, "end": v(660.4, 571.5) * mm});
            skLineSegment(sketch, "E2.17.15.0", {"start": v(685.8, 584.2) * mm, "end": v(685.8, 609.6) * mm});
            skLineSegment(sketch, "E2.17.15.1", {"start": v(660.4, 609.6) * mm, "end": v(685.8, 609.6) * mm});
            skLineSegment(sketch, "E2.17.15.2", {"start": v(660.4, 584.2) * mm, "end": v(685.8, 584.2) * mm});
            skLineSegment(sketch, "E2.17.15.3", {"start": v(660.4, 584.2) * mm, "end": v(660.4, 609.6) * mm});
            skLineSegment(sketch, "E2.17.16.0", {"start": v(685.8, 622.3) * mm, "end": v(685.8, 647.7) * mm});
            skLineSegment(sketch, "E2.17.16.1", {"start": v(660.4, 647.7) * mm, "end": v(685.8, 647.7) * mm});
            skLineSegment(sketch, "E2.17.16.2", {"start": v(660.4, 622.3) * mm, "end": v(685.8, 622.3) * mm});
            skLineSegment(sketch, "E2.17.16.3", {"start": v(660.4, 622.3) * mm, "end": v(660.4, 647.7) * mm});
            skLineSegment(sketch, "E2.17.17.0", {"start": v(685.8, 660.4) * mm, "end": v(685.8, 685.8) * mm});
            skLineSegment(sketch, "E2.17.17.1", {"start": v(660.4, 685.8) * mm, "end": v(685.8, 685.8) * mm});
            skLineSegment(sketch, "E2.17.17.2", {"start": v(660.4, 660.4) * mm, "end": v(685.8, 660.4) * mm});
            skLineSegment(sketch, "E2.17.17.3", {"start": v(660.4, 660.4) * mm, "end": v(660.4, 685.8) * mm});
            skLineSegment(sketch, "E2.17.18.0", {"start": v(685.8, 698.5) * mm, "end": v(685.8, 723.9) * mm});
            skLineSegment(sketch, "E2.17.18.1", {"start": v(660.4, 723.9) * mm, "end": v(685.8, 723.9) * mm});
            skLineSegment(sketch, "E2.17.18.2", {"start": v(660.4, 698.5) * mm, "end": v(685.8, 698.5) * mm});
            skLineSegment(sketch, "E2.17.18.3", {"start": v(660.4, 698.5) * mm, "end": v(660.4, 723.9) * mm});
            skLineSegment(sketch, "E2.17.19.0", {"start": v(685.8, 736.6) * mm, "end": v(685.8, 762) * mm});
            skLineSegment(sketch, "E2.17.19.1", {"start": v(660.4, 762) * mm, "end": v(685.8, 762) * mm});
            skLineSegment(sketch, "E2.17.19.2", {"start": v(660.4, 736.6) * mm, "end": v(685.8, 736.6) * mm});
            skLineSegment(sketch, "E2.17.19.3", {"start": v(660.4, 736.6) * mm, "end": v(660.4, 762) * mm});
            skLineSegment(sketch, "E2.18.0.0", {"start": v(723.9, 12.7) * mm, "end": v(723.9, 38.1) * mm});
            skLineSegment(sketch, "E2.18.0.1", {"start": v(698.5, 38.1) * mm, "end": v(723.9, 38.1) * mm});
            skLineSegment(sketch, "E2.18.0.2", {"start": v(698.5, 12.7) * mm, "end": v(723.9, 12.7) * mm});
            skLineSegment(sketch, "E2.18.0.3", {"start": v(698.5, 12.7) * mm, "end": v(698.5, 38.1) * mm});
            skLineSegment(sketch, "E2.18.1.0", {"start": v(723.9, 50.8) * mm, "end": v(723.9, 76.2) * mm});
            skLineSegment(sketch, "E2.18.1.1", {"start": v(698.5, 76.2) * mm, "end": v(723.9, 76.2) * mm});
            skLineSegment(sketch, "E2.18.1.2", {"start": v(698.5, 50.8) * mm, "end": v(723.9, 50.8) * mm});
            skLineSegment(sketch, "E2.18.1.3", {"start": v(698.5, 50.8) * mm, "end": v(698.5, 76.2) * mm});
            skLineSegment(sketch, "E2.18.2.0", {"start": v(723.9, 88.9) * mm, "end": v(723.9, 114.3) * mm});
            skLineSegment(sketch, "E2.18.2.1", {"start": v(698.5, 114.3) * mm, "end": v(723.9, 114.3) * mm});
            skLineSegment(sketch, "E2.18.2.2", {"start": v(698.5, 88.9) * mm, "end": v(723.9, 88.9) * mm});
            skLineSegment(sketch, "E2.18.2.3", {"start": v(698.5, 88.9) * mm, "end": v(698.5, 114.3) * mm});
            skLineSegment(sketch, "E2.18.3.0", {"start": v(723.9, 127) * mm, "end": v(723.9, 152.4) * mm});
            skLineSegment(sketch, "E2.18.3.1", {"start": v(698.5, 152.4) * mm, "end": v(723.9, 152.4) * mm});
            skLineSegment(sketch, "E2.18.3.2", {"start": v(698.5, 127) * mm, "end": v(723.9, 127) * mm});
            skLineSegment(sketch, "E2.18.3.3", {"start": v(698.5, 127) * mm, "end": v(698.5, 152.4) * mm});
            skLineSegment(sketch, "E2.18.4.0", {"start": v(723.9, 165.1) * mm, "end": v(723.9, 190.5) * mm});
            skLineSegment(sketch, "E2.18.4.1", {"start": v(698.5, 190.5) * mm, "end": v(723.9, 190.5) * mm});
            skLineSegment(sketch, "E2.18.4.2", {"start": v(698.5, 165.1) * mm, "end": v(723.9, 165.1) * mm});
            skLineSegment(sketch, "E2.18.4.3", {"start": v(698.5, 165.1) * mm, "end": v(698.5, 190.5) * mm});
            skLineSegment(sketch, "E2.18.5.0", {"start": v(723.9, 203.2) * mm, "end": v(723.9, 228.6) * mm});
            skLineSegment(sketch, "E2.18.5.1", {"start": v(698.5, 228.6) * mm, "end": v(723.9, 228.6) * mm});
            skLineSegment(sketch, "E2.18.5.2", {"start": v(698.5, 203.2) * mm, "end": v(723.9, 203.2) * mm});
            skLineSegment(sketch, "E2.18.5.3", {"start": v(698.5, 203.2) * mm, "end": v(698.5, 228.6) * mm});
            skLineSegment(sketch, "E2.18.6.0", {"start": v(723.9, 241.3) * mm, "end": v(723.9, 266.7) * mm});
            skLineSegment(sketch, "E2.18.6.1", {"start": v(698.5, 266.7) * mm, "end": v(723.9, 266.7) * mm});
            skLineSegment(sketch, "E2.18.6.2", {"start": v(698.5, 241.3) * mm, "end": v(723.9, 241.3) * mm});
            skLineSegment(sketch, "E2.18.6.3", {"start": v(698.5, 241.3) * mm, "end": v(698.5, 266.7) * mm});
            skLineSegment(sketch, "E2.18.7.0", {"start": v(723.9, 279.4) * mm, "end": v(723.9, 304.8) * mm});
            skLineSegment(sketch, "E2.18.7.1", {"start": v(698.5, 304.8) * mm, "end": v(723.9, 304.8) * mm});
            skLineSegment(sketch, "E2.18.7.2", {"start": v(698.5, 279.4) * mm, "end": v(723.9, 279.4) * mm});
            skLineSegment(sketch, "E2.18.7.3", {"start": v(698.5, 279.4) * mm, "end": v(698.5, 304.8) * mm});
            skLineSegment(sketch, "E2.18.8.0", {"start": v(723.9, 317.5) * mm, "end": v(723.9, 342.9) * mm});
            skLineSegment(sketch, "E2.18.8.1", {"start": v(698.5, 342.9) * mm, "end": v(723.9, 342.9) * mm});
            skLineSegment(sketch, "E2.18.8.2", {"start": v(698.5, 317.5) * mm, "end": v(723.9, 317.5) * mm});
            skLineSegment(sketch, "E2.18.8.3", {"start": v(698.5, 317.5) * mm, "end": v(698.5, 342.9) * mm});
            skLineSegment(sketch, "E2.18.9.0", {"start": v(723.9, 355.6) * mm, "end": v(723.9, 381) * mm});
            skLineSegment(sketch, "E2.18.9.1", {"start": v(698.5, 381) * mm, "end": v(723.9, 381) * mm});
            skLineSegment(sketch, "E2.18.9.2", {"start": v(698.5, 355.6) * mm, "end": v(723.9, 355.6) * mm});
            skLineSegment(sketch, "E2.18.9.3", {"start": v(698.5, 355.6) * mm, "end": v(698.5, 381) * mm});
            skLineSegment(sketch, "E2.18.10.0", {"start": v(723.9, 393.7) * mm, "end": v(723.9, 419.1) * mm});
            skLineSegment(sketch, "E2.18.10.1", {"start": v(698.5, 419.1) * mm, "end": v(723.9, 419.1) * mm});
            skLineSegment(sketch, "E2.18.10.2", {"start": v(698.5, 393.7) * mm, "end": v(723.9, 393.7) * mm});
            skLineSegment(sketch, "E2.18.10.3", {"start": v(698.5, 393.7) * mm, "end": v(698.5, 419.1) * mm});
            skLineSegment(sketch, "E2.18.11.0", {"start": v(723.9, 431.8) * mm, "end": v(723.9, 457.2) * mm});
            skLineSegment(sketch, "E2.18.11.1", {"start": v(698.5, 457.2) * mm, "end": v(723.9, 457.2) * mm});
            skLineSegment(sketch, "E2.18.11.2", {"start": v(698.5, 431.8) * mm, "end": v(723.9, 431.8) * mm});
            skLineSegment(sketch, "E2.18.11.3", {"start": v(698.5, 431.8) * mm, "end": v(698.5, 457.2) * mm});
            skLineSegment(sketch, "E2.18.12.0", {"start": v(723.9, 469.9) * mm, "end": v(723.9, 495.3) * mm});
            skLineSegment(sketch, "E2.18.12.1", {"start": v(698.5, 495.3) * mm, "end": v(723.9, 495.3) * mm});
            skLineSegment(sketch, "E2.18.12.2", {"start": v(698.5, 469.9) * mm, "end": v(723.9, 469.9) * mm});
            skLineSegment(sketch, "E2.18.12.3", {"start": v(698.5, 469.9) * mm, "end": v(698.5, 495.3) * mm});
            skLineSegment(sketch, "E2.18.13.0", {"start": v(723.9, 508) * mm, "end": v(723.9, 533.4) * mm});
            skLineSegment(sketch, "E2.18.13.1", {"start": v(698.5, 533.4) * mm, "end": v(723.9, 533.4) * mm});
            skLineSegment(sketch, "E2.18.13.2", {"start": v(698.5, 508) * mm, "end": v(723.9, 508) * mm});
            skLineSegment(sketch, "E2.18.13.3", {"start": v(698.5, 508) * mm, "end": v(698.5, 533.4) * mm});
            skLineSegment(sketch, "E2.18.14.0", {"start": v(723.9, 546.1) * mm, "end": v(723.9, 571.5) * mm});
            skLineSegment(sketch, "E2.18.14.1", {"start": v(698.5, 571.5) * mm, "end": v(723.9, 571.5) * mm});
            skLineSegment(sketch, "E2.18.14.2", {"start": v(698.5, 546.1) * mm, "end": v(723.9, 546.1) * mm});
            skLineSegment(sketch, "E2.18.14.3", {"start": v(698.5, 546.1) * mm, "end": v(698.5, 571.5) * mm});
            skLineSegment(sketch, "E2.18.15.0", {"start": v(723.9, 584.2) * mm, "end": v(723.9, 609.6) * mm});
            skLineSegment(sketch, "E2.18.15.1", {"start": v(698.5, 609.6) * mm, "end": v(723.9, 609.6) * mm});
            skLineSegment(sketch, "E2.18.15.2", {"start": v(698.5, 584.2) * mm, "end": v(723.9, 584.2) * mm});
            skLineSegment(sketch, "E2.18.15.3", {"start": v(698.5, 584.2) * mm, "end": v(698.5, 609.6) * mm});
            skLineSegment(sketch, "E2.18.16.0", {"start": v(723.9, 622.3) * mm, "end": v(723.9, 647.7) * mm});
            skLineSegment(sketch, "E2.18.16.1", {"start": v(698.5, 647.7) * mm, "end": v(723.9, 647.7) * mm});
            skLineSegment(sketch, "E2.18.16.2", {"start": v(698.5, 622.3) * mm, "end": v(723.9, 622.3) * mm});
            skLineSegment(sketch, "E2.18.16.3", {"start": v(698.5, 622.3) * mm, "end": v(698.5, 647.7) * mm});
            skLineSegment(sketch, "E2.18.17.0", {"start": v(723.9, 660.4) * mm, "end": v(723.9, 685.8) * mm});
            skLineSegment(sketch, "E2.18.17.1", {"start": v(698.5, 685.8) * mm, "end": v(723.9, 685.8) * mm});
            skLineSegment(sketch, "E2.18.17.2", {"start": v(698.5, 660.4) * mm, "end": v(723.9, 660.4) * mm});
            skLineSegment(sketch, "E2.18.17.3", {"start": v(698.5, 660.4) * mm, "end": v(698.5, 685.8) * mm});
            skLineSegment(sketch, "E2.18.18.0", {"start": v(723.9, 698.5) * mm, "end": v(723.9, 723.9) * mm});
            skLineSegment(sketch, "E2.18.18.1", {"start": v(698.5, 723.9) * mm, "end": v(723.9, 723.9) * mm});
            skLineSegment(sketch, "E2.18.18.2", {"start": v(698.5, 698.5) * mm, "end": v(723.9, 698.5) * mm});
            skLineSegment(sketch, "E2.18.18.3", {"start": v(698.5, 698.5) * mm, "end": v(698.5, 723.9) * mm});
            skLineSegment(sketch, "E2.18.19.0", {"start": v(723.9, 736.6) * mm, "end": v(723.9, 762) * mm});
            skLineSegment(sketch, "E2.18.19.1", {"start": v(698.5, 762) * mm, "end": v(723.9, 762) * mm});
            skLineSegment(sketch, "E2.18.19.2", {"start": v(698.5, 736.6) * mm, "end": v(723.9, 736.6) * mm});
            skLineSegment(sketch, "E2.18.19.3", {"start": v(698.5, 736.6) * mm, "end": v(698.5, 762) * mm});
            skLineSegment(sketch, "E2.19.0.0", {"start": v(762, 12.7) * mm, "end": v(762, 38.1) * mm});
            skLineSegment(sketch, "E2.19.0.1", {"start": v(736.6, 38.1) * mm, "end": v(762, 38.1) * mm});
            skLineSegment(sketch, "E2.19.0.2", {"start": v(736.6, 12.7) * mm, "end": v(762, 12.7) * mm});
            skLineSegment(sketch, "E2.19.0.3", {"start": v(736.6, 12.7) * mm, "end": v(736.6, 38.1) * mm});
            skLineSegment(sketch, "E2.19.1.0", {"start": v(762, 50.8) * mm, "end": v(762, 76.2) * mm});
            skLineSegment(sketch, "E2.19.1.1", {"start": v(736.6, 76.2) * mm, "end": v(762, 76.2) * mm});
            skLineSegment(sketch, "E2.19.1.2", {"start": v(736.6, 50.8) * mm, "end": v(762, 50.8) * mm});
            skLineSegment(sketch, "E2.19.1.3", {"start": v(736.6, 50.8) * mm, "end": v(736.6, 76.2) * mm});
            skLineSegment(sketch, "E2.19.2.0", {"start": v(762, 88.9) * mm, "end": v(762, 114.3) * mm});
            skLineSegment(sketch, "E2.19.2.1", {"start": v(736.6, 114.3) * mm, "end": v(762, 114.3) * mm});
            skLineSegment(sketch, "E2.19.2.2", {"start": v(736.6, 88.9) * mm, "end": v(762, 88.9) * mm});
            skLineSegment(sketch, "E2.19.2.3", {"start": v(736.6, 88.9) * mm, "end": v(736.6, 114.3) * mm});
            skLineSegment(sketch, "E2.19.3.0", {"start": v(762, 127) * mm, "end": v(762, 152.4) * mm});
            skLineSegment(sketch, "E2.19.3.1", {"start": v(736.6, 152.4) * mm, "end": v(762, 152.4) * mm});
            skLineSegment(sketch, "E2.19.3.2", {"start": v(736.6, 127) * mm, "end": v(762, 127) * mm});
            skLineSegment(sketch, "E2.19.3.3", {"start": v(736.6, 127) * mm, "end": v(736.6, 152.4) * mm});
            skLineSegment(sketch, "E2.19.4.0", {"start": v(762, 165.1) * mm, "end": v(762, 190.5) * mm});
            skLineSegment(sketch, "E2.19.4.1", {"start": v(736.6, 190.5) * mm, "end": v(762, 190.5) * mm});
            skLineSegment(sketch, "E2.19.4.2", {"start": v(736.6, 165.1) * mm, "end": v(762, 165.1) * mm});
            skLineSegment(sketch, "E2.19.4.3", {"start": v(736.6, 165.1) * mm, "end": v(736.6, 190.5) * mm});
            skLineSegment(sketch, "E2.19.5.0", {"start": v(762, 203.2) * mm, "end": v(762, 228.6) * mm});
            skLineSegment(sketch, "E2.19.5.1", {"start": v(736.6, 228.6) * mm, "end": v(762, 228.6) * mm});
            skLineSegment(sketch, "E2.19.5.2", {"start": v(736.6, 203.2) * mm, "end": v(762, 203.2) * mm});
            skLineSegment(sketch, "E2.19.5.3", {"start": v(736.6, 203.2) * mm, "end": v(736.6, 228.6) * mm});
            skLineSegment(sketch, "E2.19.6.0", {"start": v(762, 241.3) * mm, "end": v(762, 266.7) * mm});
            skLineSegment(sketch, "E2.19.6.1", {"start": v(736.6, 266.7) * mm, "end": v(762, 266.7) * mm});
            skLineSegment(sketch, "E2.19.6.2", {"start": v(736.6, 241.3) * mm, "end": v(762, 241.3) * mm});
            skLineSegment(sketch, "E2.19.6.3", {"start": v(736.6, 241.3) * mm, "end": v(736.6, 266.7) * mm});
            skLineSegment(sketch, "E2.19.7.0", {"start": v(762, 279.4) * mm, "end": v(762, 304.8) * mm});
            skLineSegment(sketch, "E2.19.7.1", {"start": v(736.6, 304.8) * mm, "end": v(762, 304.8) * mm});
            skLineSegment(sketch, "E2.19.7.2", {"start": v(736.6, 279.4) * mm, "end": v(762, 279.4) * mm});
            skLineSegment(sketch, "E2.19.7.3", {"start": v(736.6, 279.4) * mm, "end": v(736.6, 304.8) * mm});
            skLineSegment(sketch, "E2.19.8.0", {"start": v(762, 317.5) * mm, "end": v(762, 342.9) * mm});
            skLineSegment(sketch, "E2.19.8.1", {"start": v(736.6, 342.9) * mm, "end": v(762, 342.9) * mm});
            skLineSegment(sketch, "E2.19.8.2", {"start": v(736.6, 317.5) * mm, "end": v(762, 317.5) * mm});
            skLineSegment(sketch, "E2.19.8.3", {"start": v(736.6, 317.5) * mm, "end": v(736.6, 342.9) * mm});
            skLineSegment(sketch, "E2.19.9.0", {"start": v(762, 355.6) * mm, "end": v(762, 381) * mm});
            skLineSegment(sketch, "E2.19.9.1", {"start": v(736.6, 381) * mm, "end": v(762, 381) * mm});
            skLineSegment(sketch, "E2.19.9.2", {"start": v(736.6, 355.6) * mm, "end": v(762, 355.6) * mm});
            skLineSegment(sketch, "E2.19.9.3", {"start": v(736.6, 355.6) * mm, "end": v(736.6, 381) * mm});
            skLineSegment(sketch, "E2.19.10.0", {"start": v(762, 393.7) * mm, "end": v(762, 419.1) * mm});
            skLineSegment(sketch, "E2.19.10.1", {"start": v(736.6, 419.1) * mm, "end": v(762, 419.1) * mm});
            skLineSegment(sketch, "E2.19.10.2", {"start": v(736.6, 393.7) * mm, "end": v(762, 393.7) * mm});
            skLineSegment(sketch, "E2.19.10.3", {"start": v(736.6, 393.7) * mm, "end": v(736.6, 419.1) * mm});
            skLineSegment(sketch, "E2.19.11.0", {"start": v(762, 431.8) * mm, "end": v(762, 457.2) * mm});
            skLineSegment(sketch, "E2.19.11.1", {"start": v(736.6, 457.2) * mm, "end": v(762, 457.2) * mm});
            skLineSegment(sketch, "E2.19.11.2", {"start": v(736.6, 431.8) * mm, "end": v(762, 431.8) * mm});
            skLineSegment(sketch, "E2.19.11.3", {"start": v(736.6, 431.8) * mm, "end": v(736.6, 457.2) * mm});
            skLineSegment(sketch, "E2.19.12.0", {"start": v(762, 469.9) * mm, "end": v(762, 495.3) * mm});
            skLineSegment(sketch, "E2.19.12.1", {"start": v(736.6, 495.3) * mm, "end": v(762, 495.3) * mm});
            skLineSegment(sketch, "E2.19.12.2", {"start": v(736.6, 469.9) * mm, "end": v(762, 469.9) * mm});
            skLineSegment(sketch, "E2.19.12.3", {"start": v(736.6, 469.9) * mm, "end": v(736.6, 495.3) * mm});
            skLineSegment(sketch, "E2.19.13.0", {"start": v(762, 508) * mm, "end": v(762, 533.4) * mm});
            skLineSegment(sketch, "E2.19.13.1", {"start": v(736.6, 533.4) * mm, "end": v(762, 533.4) * mm});
            skLineSegment(sketch, "E2.19.13.2", {"start": v(736.6, 508) * mm, "end": v(762, 508) * mm});
            skLineSegment(sketch, "E2.19.13.3", {"start": v(736.6, 508) * mm, "end": v(736.6, 533.4) * mm});
            skLineSegment(sketch, "E2.19.14.0", {"start": v(762, 546.1) * mm, "end": v(762, 571.5) * mm});
            skLineSegment(sketch, "E2.19.14.1", {"start": v(736.6, 571.5) * mm, "end": v(762, 571.5) * mm});
            skLineSegment(sketch, "E2.19.14.2", {"start": v(736.6, 546.1) * mm, "end": v(762, 546.1) * mm});
            skLineSegment(sketch, "E2.19.14.3", {"start": v(736.6, 546.1) * mm, "end": v(736.6, 571.5) * mm});
            skLineSegment(sketch, "E2.19.15.0", {"start": v(762, 584.2) * mm, "end": v(762, 609.6) * mm});
            skLineSegment(sketch, "E2.19.15.1", {"start": v(736.6, 609.6) * mm, "end": v(762, 609.6) * mm});
            skLineSegment(sketch, "E2.19.15.2", {"start": v(736.6, 584.2) * mm, "end": v(762, 584.2) * mm});
            skLineSegment(sketch, "E2.19.15.3", {"start": v(736.6, 584.2) * mm, "end": v(736.6, 609.6) * mm});
            skLineSegment(sketch, "E2.19.16.0", {"start": v(762, 622.3) * mm, "end": v(762, 647.7) * mm});
            skLineSegment(sketch, "E2.19.16.1", {"start": v(736.6, 647.7) * mm, "end": v(762, 647.7) * mm});
            skLineSegment(sketch, "E2.19.16.2", {"start": v(736.6, 622.3) * mm, "end": v(762, 622.3) * mm});
            skLineSegment(sketch, "E2.19.16.3", {"start": v(736.6, 622.3) * mm, "end": v(736.6, 647.7) * mm});
            skLineSegment(sketch, "E2.19.17.0", {"start": v(762, 660.4) * mm, "end": v(762, 685.8) * mm});
            skLineSegment(sketch, "E2.19.17.1", {"start": v(736.6, 685.8) * mm, "end": v(762, 685.8) * mm});
            skLineSegment(sketch, "E2.19.17.2", {"start": v(736.6, 660.4) * mm, "end": v(762, 660.4) * mm});
            skLineSegment(sketch, "E2.19.17.3", {"start": v(736.6, 660.4) * mm, "end": v(736.6, 685.8) * mm});
            skLineSegment(sketch, "E2.19.18.0", {"start": v(762, 698.5) * mm, "end": v(762, 723.9) * mm});
            skLineSegment(sketch, "E2.19.18.1", {"start": v(736.6, 723.9) * mm, "end": v(762, 723.9) * mm});
            skLineSegment(sketch, "E2.19.18.2", {"start": v(736.6, 698.5) * mm, "end": v(762, 698.5) * mm});
            skLineSegment(sketch, "E2.19.18.3", {"start": v(736.6, 698.5) * mm, "end": v(736.6, 723.9) * mm});
            skLineSegment(sketch, "E2.19.19.0", {"start": v(762, 736.6) * mm, "end": v(762, 762) * mm});
            skLineSegment(sketch, "E2.19.19.1", {"start": v(736.6, 762) * mm, "end": v(762, 762) * mm});
            skLineSegment(sketch, "E2.19.19.2", {"start": v(736.6, 736.6) * mm, "end": v(762, 736.6) * mm});
            skLineSegment(sketch, "E2.19.19.3", {"start": v(736.6, 736.6) * mm, "end": v(736.6, 762) * mm});
            skLineSegment(sketch, "E2.direction1", {"start": v(12.7, 12.7) * mm, "end": v(50.8, 12.7) * mm, "construction": true});
            skLineSegment(sketch, "E2.direction2", {"start": v(12.7, 12.7) * mm, "end": v(12.7, 50.8) * mm, "construction": true});
            skLineSegment(sketch, "E3.0.20.0", {"start": v(800.1, 12.7) * mm, "end": v(800.1, 38.1) * mm});
            skLineSegment(sketch, "E3.3.20.0", {"start": v(774.7, 38.1) * mm, "end": v(800.1, 38.1) * mm});
            skLineSegment(sketch, "E3.6.20.0", {"start": v(774.7, 12.7) * mm, "end": v(800.1, 12.7) * mm});
            skLineSegment(sketch, "E3.9.20.0", {"start": v(774.7, 12.7) * mm, "end": v(774.7, 38.1) * mm});
            skLineSegment(sketch, "E3.0.20.1", {"start": v(800.1, 50.8) * mm, "end": v(800.1, 76.2) * mm});
            skLineSegment(sketch, "E3.3.20.1", {"start": v(774.7, 76.2) * mm, "end": v(800.1, 76.2) * mm});
            skLineSegment(sketch, "E3.6.20.1", {"start": v(774.7, 50.8) * mm, "end": v(800.1, 50.8) * mm});
            skLineSegment(sketch, "E3.9.20.1", {"start": v(774.7, 50.8) * mm, "end": v(774.7, 76.2) * mm});
            skLineSegment(sketch, "E3.0.20.2", {"start": v(800.1, 88.9) * mm, "end": v(800.1, 114.3) * mm});
            skLineSegment(sketch, "E3.3.20.2", {"start": v(774.7, 114.3) * mm, "end": v(800.1, 114.3) * mm});
            skLineSegment(sketch, "E3.6.20.2", {"start": v(774.7, 88.9) * mm, "end": v(800.1, 88.9) * mm});
            skLineSegment(sketch, "E3.9.20.2", {"start": v(774.7, 88.9) * mm, "end": v(774.7, 114.3) * mm});
            skLineSegment(sketch, "E3.0.20.3", {"start": v(800.1, 127) * mm, "end": v(800.1, 152.4) * mm});
            skLineSegment(sketch, "E3.3.20.3", {"start": v(774.7, 152.4) * mm, "end": v(800.1, 152.4) * mm});
            skLineSegment(sketch, "E3.6.20.3", {"start": v(774.7, 127) * mm, "end": v(800.1, 127) * mm});
            skLineSegment(sketch, "E3.9.20.3", {"start": v(774.7, 127) * mm, "end": v(774.7, 152.4) * mm});
            skLineSegment(sketch, "E3.0.20.4", {"start": v(800.1, 165.1) * mm, "end": v(800.1, 190.5) * mm});
            skLineSegment(sketch, "E3.3.20.4", {"start": v(774.7, 190.5) * mm, "end": v(800.1, 190.5) * mm});
            skLineSegment(sketch, "E3.6.20.4", {"start": v(774.7, 165.1) * mm, "end": v(800.1, 165.1) * mm});
            skLineSegment(sketch, "E3.9.20.4", {"start": v(774.7, 165.1) * mm, "end": v(774.7, 190.5) * mm});
            skLineSegment(sketch, "E3.0.20.5", {"start": v(800.1, 203.2) * mm, "end": v(800.1, 228.6) * mm});
            skLineSegment(sketch, "E3.3.20.5", {"start": v(774.7, 228.6) * mm, "end": v(800.1, 228.6) * mm});
            skLineSegment(sketch, "E3.6.20.5", {"start": v(774.7, 203.2) * mm, "end": v(800.1, 203.2) * mm});
            skLineSegment(sketch, "E3.9.20.5", {"start": v(774.7, 203.2) * mm, "end": v(774.7, 228.6) * mm});
            skLineSegment(sketch, "E3.0.20.6", {"start": v(800.1, 241.3) * mm, "end": v(800.1, 266.7) * mm});
            skLineSegment(sketch, "E3.3.20.6", {"start": v(774.7, 266.7) * mm, "end": v(800.1, 266.7) * mm});
            skLineSegment(sketch, "E3.6.20.6", {"start": v(774.7, 241.3) * mm, "end": v(800.1, 241.3) * mm});
            skLineSegment(sketch, "E3.9.20.6", {"start": v(774.7, 241.3) * mm, "end": v(774.7, 266.7) * mm});
            skLineSegment(sketch, "E3.0.20.7", {"start": v(800.1, 279.4) * mm, "end": v(800.1, 304.8) * mm});
            skLineSegment(sketch, "E3.3.20.7", {"start": v(774.7, 304.8) * mm, "end": v(800.1, 304.8) * mm});
            skLineSegment(sketch, "E3.6.20.7", {"start": v(774.7, 279.4) * mm, "end": v(800.1, 279.4) * mm});
            skLineSegment(sketch, "E3.9.20.7", {"start": v(774.7, 279.4) * mm, "end": v(774.7, 304.8) * mm});
            skLineSegment(sketch, "E3.0.20.8", {"start": v(800.1, 317.5) * mm, "end": v(800.1, 342.9) * mm});
            skLineSegment(sketch, "E3.3.20.8", {"start": v(774.7, 342.9) * mm, "end": v(800.1, 342.9) * mm});
            skLineSegment(sketch, "E3.6.20.8", {"start": v(774.7, 317.5) * mm, "end": v(800.1, 317.5) * mm});
            skLineSegment(sketch, "E3.9.20.8", {"start": v(774.7, 317.5) * mm, "end": v(774.7, 342.9) * mm});
            skLineSegment(sketch, "E3.0.20.9", {"start": v(800.1, 355.6) * mm, "end": v(800.1, 381) * mm});
            skLineSegment(sketch, "E3.3.20.9", {"start": v(774.7, 381) * mm, "end": v(800.1, 381) * mm});
            skLineSegment(sketch, "E3.6.20.9", {"start": v(774.7, 355.6) * mm, "end": v(800.1, 355.6) * mm});
            skLineSegment(sketch, "E3.9.20.9", {"start": v(774.7, 355.6) * mm, "end": v(774.7, 381) * mm});
            skLineSegment(sketch, "E3.0.20.10", {"start": v(800.1, 393.7) * mm, "end": v(800.1, 419.1) * mm});
            skLineSegment(sketch, "E3.3.20.10", {"start": v(774.7, 419.1) * mm, "end": v(800.1, 419.1) * mm});
            skLineSegment(sketch, "E3.6.20.10", {"start": v(774.7, 393.7) * mm, "end": v(800.1, 393.7) * mm});
            skLineSegment(sketch, "E3.9.20.10", {"start": v(774.7, 393.7) * mm, "end": v(774.7, 419.1) * mm});
            skLineSegment(sketch, "E3.0.20.11", {"start": v(800.1, 431.8) * mm, "end": v(800.1, 457.2) * mm});
            skLineSegment(sketch, "E3.3.20.11", {"start": v(774.7, 457.2) * mm, "end": v(800.1, 457.2) * mm});
            skLineSegment(sketch, "E3.6.20.11", {"start": v(774.7, 431.8) * mm, "end": v(800.1, 431.8) * mm});
            skLineSegment(sketch, "E3.9.20.11", {"start": v(774.7, 431.8) * mm, "end": v(774.7, 457.2) * mm});
            skLineSegment(sketch, "E3.0.20.12", {"start": v(800.1, 469.9) * mm, "end": v(800.1, 495.3) * mm});
            skLineSegment(sketch, "E3.3.20.12", {"start": v(774.7, 495.3) * mm, "end": v(800.1, 495.3) * mm});
            skLineSegment(sketch, "E3.6.20.12", {"start": v(774.7, 469.9) * mm, "end": v(800.1, 469.9) * mm});
            skLineSegment(sketch, "E3.9.20.12", {"start": v(774.7, 469.9) * mm, "end": v(774.7, 495.3) * mm});
            skLineSegment(sketch, "E3.0.20.13", {"start": v(800.1, 508) * mm, "end": v(800.1, 533.4) * mm});
            skLineSegment(sketch, "E3.3.20.13", {"start": v(774.7, 533.4) * mm, "end": v(800.1, 533.4) * mm});
            skLineSegment(sketch, "E3.6.20.13", {"start": v(774.7, 508) * mm, "end": v(800.1, 508) * mm});
            skLineSegment(sketch, "E3.9.20.13", {"start": v(774.7, 508) * mm, "end": v(774.7, 533.4) * mm});
            skLineSegment(sketch, "E3.0.20.14", {"start": v(800.1, 546.1) * mm, "end": v(800.1, 571.5) * mm});
            skLineSegment(sketch, "E3.3.20.14", {"start": v(774.7, 571.5) * mm, "end": v(800.1, 571.5) * mm});
            skLineSegment(sketch, "E3.6.20.14", {"start": v(774.7, 546.1) * mm, "end": v(800.1, 546.1) * mm});
            skLineSegment(sketch, "E3.9.20.14", {"start": v(774.7, 546.1) * mm, "end": v(774.7, 571.5) * mm});
            skLineSegment(sketch, "E3.0.20.15", {"start": v(800.1, 584.2) * mm, "end": v(800.1, 609.6) * mm});
            skLineSegment(sketch, "E3.3.20.15", {"start": v(774.7, 609.6) * mm, "end": v(800.1, 609.6) * mm});
            skLineSegment(sketch, "E3.6.20.15", {"start": v(774.7, 584.2) * mm, "end": v(800.1, 584.2) * mm});
            skLineSegment(sketch, "E3.9.20.15", {"start": v(774.7, 584.2) * mm, "end": v(774.7, 609.6) * mm});
            skLineSegment(sketch, "E3.0.20.16", {"start": v(800.1, 622.3) * mm, "end": v(800.1, 647.7) * mm});
            skLineSegment(sketch, "E3.3.20.16", {"start": v(774.7, 647.7) * mm, "end": v(800.1, 647.7) * mm});
            skLineSegment(sketch, "E3.6.20.16", {"start": v(774.7, 622.3) * mm, "end": v(800.1, 622.3) * mm});
            skLineSegment(sketch, "E3.9.20.16", {"start": v(774.7, 622.3) * mm, "end": v(774.7, 647.7) * mm});
            skLineSegment(sketch, "E3.0.20.17", {"start": v(800.1, 660.4) * mm, "end": v(800.1, 685.8) * mm});
            skLineSegment(sketch, "E3.3.20.17", {"start": v(774.7, 685.8) * mm, "end": v(800.1, 685.8) * mm});
            skLineSegment(sketch, "E3.6.20.17", {"start": v(774.7, 660.4) * mm, "end": v(800.1, 660.4) * mm});
            skLineSegment(sketch, "E3.9.20.17", {"start": v(774.7, 660.4) * mm, "end": v(774.7, 685.8) * mm});
            skLineSegment(sketch, "E3.0.20.18", {"start": v(800.1, 698.5) * mm, "end": v(800.1, 723.9) * mm});
            skLineSegment(sketch, "E3.3.20.18", {"start": v(774.7, 723.9) * mm, "end": v(800.1, 723.9) * mm});
            skLineSegment(sketch, "E3.6.20.18", {"start": v(774.7, 698.5) * mm, "end": v(800.1, 698.5) * mm});
            skLineSegment(sketch, "E3.9.20.18", {"start": v(774.7, 698.5) * mm, "end": v(774.7, 723.9) * mm});
            skLineSegment(sketch, "E3.0.20.19", {"start": v(800.1, 736.6) * mm, "end": v(800.1, 762) * mm});
            skLineSegment(sketch, "E3.3.20.19", {"start": v(774.7, 762) * mm, "end": v(800.1, 762) * mm});
            skLineSegment(sketch, "E3.6.20.19", {"start": v(774.7, 736.6) * mm, "end": v(800.1, 736.6) * mm});
            skLineSegment(sketch, "E3.9.20.19", {"start": v(774.7, 736.6) * mm, "end": v(774.7, 762) * mm});
            skLineSegment(sketch, "E3.0.21.0", {"start": v(838.2, 12.7) * mm, "end": v(838.2, 38.1) * mm});
            skLineSegment(sketch, "E3.3.21.0", {"start": v(812.8, 38.1) * mm, "end": v(838.2, 38.1) * mm});
            skLineSegment(sketch, "E3.6.21.0", {"start": v(812.8, 12.7) * mm, "end": v(838.2, 12.7) * mm});
            skLineSegment(sketch, "E3.9.21.0", {"start": v(812.8, 12.7) * mm, "end": v(812.8, 38.1) * mm});
            skLineSegment(sketch, "E3.0.21.1", {"start": v(838.2, 50.8) * mm, "end": v(838.2, 76.2) * mm});
            skLineSegment(sketch, "E3.3.21.1", {"start": v(812.8, 76.2) * mm, "end": v(838.2, 76.2) * mm});
            skLineSegment(sketch, "E3.6.21.1", {"start": v(812.8, 50.8) * mm, "end": v(838.2, 50.8) * mm});
            skLineSegment(sketch, "E3.9.21.1", {"start": v(812.8, 50.8) * mm, "end": v(812.8, 76.2) * mm});
            skLineSegment(sketch, "E3.0.21.2", {"start": v(838.2, 88.9) * mm, "end": v(838.2, 114.3) * mm});
            skLineSegment(sketch, "E3.3.21.2", {"start": v(812.8, 114.3) * mm, "end": v(838.2, 114.3) * mm});
            skLineSegment(sketch, "E3.6.21.2", {"start": v(812.8, 88.9) * mm, "end": v(838.2, 88.9) * mm});
            skLineSegment(sketch, "E3.9.21.2", {"start": v(812.8, 88.9) * mm, "end": v(812.8, 114.3) * mm});
            skLineSegment(sketch, "E3.0.21.3", {"start": v(838.2, 127) * mm, "end": v(838.2, 152.4) * mm});
            skLineSegment(sketch, "E3.3.21.3", {"start": v(812.8, 152.4) * mm, "end": v(838.2, 152.4) * mm});
            skLineSegment(sketch, "E3.6.21.3", {"start": v(812.8, 127) * mm, "end": v(838.2, 127) * mm});
            skLineSegment(sketch, "E3.9.21.3", {"start": v(812.8, 127) * mm, "end": v(812.8, 152.4) * mm});
            skLineSegment(sketch, "E3.0.21.4", {"start": v(838.2, 165.1) * mm, "end": v(838.2, 190.5) * mm});
            skLineSegment(sketch, "E3.3.21.4", {"start": v(812.8, 190.5) * mm, "end": v(838.2, 190.5) * mm});
            skLineSegment(sketch, "E3.6.21.4", {"start": v(812.8, 165.1) * mm, "end": v(838.2, 165.1) * mm});
            skLineSegment(sketch, "E3.9.21.4", {"start": v(812.8, 165.1) * mm, "end": v(812.8, 190.5) * mm});
            skLineSegment(sketch, "E3.0.21.5", {"start": v(838.2, 203.2) * mm, "end": v(838.2, 228.6) * mm});
            skLineSegment(sketch, "E3.3.21.5", {"start": v(812.8, 228.6) * mm, "end": v(838.2, 228.6) * mm});
            skLineSegment(sketch, "E3.6.21.5", {"start": v(812.8, 203.2) * mm, "end": v(838.2, 203.2) * mm});
            skLineSegment(sketch, "E3.9.21.5", {"start": v(812.8, 203.2) * mm, "end": v(812.8, 228.6) * mm});
            skLineSegment(sketch, "E3.0.21.6", {"start": v(838.2, 241.3) * mm, "end": v(838.2, 266.7) * mm});
            skLineSegment(sketch, "E3.3.21.6", {"start": v(812.8, 266.7) * mm, "end": v(838.2, 266.7) * mm});
            skLineSegment(sketch, "E3.6.21.6", {"start": v(812.8, 241.3) * mm, "end": v(838.2, 241.3) * mm});
            skLineSegment(sketch, "E3.9.21.6", {"start": v(812.8, 241.3) * mm, "end": v(812.8, 266.7) * mm});
            skLineSegment(sketch, "E3.0.21.7", {"start": v(838.2, 279.4) * mm, "end": v(838.2, 304.8) * mm});
            skLineSegment(sketch, "E3.3.21.7", {"start": v(812.8, 304.8) * mm, "end": v(838.2, 304.8) * mm});
            skLineSegment(sketch, "E3.6.21.7", {"start": v(812.8, 279.4) * mm, "end": v(838.2, 279.4) * mm});
            skLineSegment(sketch, "E3.9.21.7", {"start": v(812.8, 279.4) * mm, "end": v(812.8, 304.8) * mm});
            skLineSegment(sketch, "E3.0.21.8", {"start": v(838.2, 317.5) * mm, "end": v(838.2, 342.9) * mm});
            skLineSegment(sketch, "E3.3.21.8", {"start": v(812.8, 342.9) * mm, "end": v(838.2, 342.9) * mm});
            skLineSegment(sketch, "E3.6.21.8", {"start": v(812.8, 317.5) * mm, "end": v(838.2, 317.5) * mm});
            skLineSegment(sketch, "E3.9.21.8", {"start": v(812.8, 317.5) * mm, "end": v(812.8, 342.9) * mm});
            skLineSegment(sketch, "E3.0.21.9", {"start": v(838.2, 355.6) * mm, "end": v(838.2, 381) * mm});
            skLineSegment(sketch, "E3.3.21.9", {"start": v(812.8, 381) * mm, "end": v(838.2, 381) * mm});
            skLineSegment(sketch, "E3.6.21.9", {"start": v(812.8, 355.6) * mm, "end": v(838.2, 355.6) * mm});
            skLineSegment(sketch, "E3.9.21.9", {"start": v(812.8, 355.6) * mm, "end": v(812.8, 381) * mm});
            skLineSegment(sketch, "E3.0.21.10", {"start": v(838.2, 393.7) * mm, "end": v(838.2, 419.1) * mm});
            skLineSegment(sketch, "E3.3.21.10", {"start": v(812.8, 419.1) * mm, "end": v(838.2, 419.1) * mm});
            skLineSegment(sketch, "E3.6.21.10", {"start": v(812.8, 393.7) * mm, "end": v(838.2, 393.7) * mm});
            skLineSegment(sketch, "E3.9.21.10", {"start": v(812.8, 393.7) * mm, "end": v(812.8, 419.1) * mm});
            skLineSegment(sketch, "E3.0.21.11", {"start": v(838.2, 431.8) * mm, "end": v(838.2, 457.2) * mm});
            skLineSegment(sketch, "E3.3.21.11", {"start": v(812.8, 457.2) * mm, "end": v(838.2, 457.2) * mm});
            skLineSegment(sketch, "E3.6.21.11", {"start": v(812.8, 431.8) * mm, "end": v(838.2, 431.8) * mm});
            skLineSegment(sketch, "E3.9.21.11", {"start": v(812.8, 431.8) * mm, "end": v(812.8, 457.2) * mm});
            skLineSegment(sketch, "E3.0.21.12", {"start": v(838.2, 469.9) * mm, "end": v(838.2, 495.3) * mm});
            skLineSegment(sketch, "E3.3.21.12", {"start": v(812.8, 495.3) * mm, "end": v(838.2, 495.3) * mm});
            skLineSegment(sketch, "E3.6.21.12", {"start": v(812.8, 469.9) * mm, "end": v(838.2, 469.9) * mm});
            skLineSegment(sketch, "E3.9.21.12", {"start": v(812.8, 469.9) * mm, "end": v(812.8, 495.3) * mm});
            skLineSegment(sketch, "E3.0.21.13", {"start": v(838.2, 508) * mm, "end": v(838.2, 533.4) * mm});
            skLineSegment(sketch, "E3.3.21.13", {"start": v(812.8, 533.4) * mm, "end": v(838.2, 533.4) * mm});
            skLineSegment(sketch, "E3.6.21.13", {"start": v(812.8, 508) * mm, "end": v(838.2, 508) * mm});
            skLineSegment(sketch, "E3.9.21.13", {"start": v(812.8, 508) * mm, "end": v(812.8, 533.4) * mm});
            skLineSegment(sketch, "E3.0.21.14", {"start": v(838.2, 546.1) * mm, "end": v(838.2, 571.5) * mm});
            skLineSegment(sketch, "E3.3.21.14", {"start": v(812.8, 571.5) * mm, "end": v(838.2, 571.5) * mm});
            skLineSegment(sketch, "E3.6.21.14", {"start": v(812.8, 546.1) * mm, "end": v(838.2, 546.1) * mm});
            skLineSegment(sketch, "E3.9.21.14", {"start": v(812.8, 546.1) * mm, "end": v(812.8, 571.5) * mm});
            skLineSegment(sketch, "E3.0.21.15", {"start": v(838.2, 584.2) * mm, "end": v(838.2, 609.6) * mm});
            skLineSegment(sketch, "E3.3.21.15", {"start": v(812.8, 609.6) * mm, "end": v(838.2, 609.6) * mm});
            skLineSegment(sketch, "E3.6.21.15", {"start": v(812.8, 584.2) * mm, "end": v(838.2, 584.2) * mm});
            skLineSegment(sketch, "E3.9.21.15", {"start": v(812.8, 584.2) * mm, "end": v(812.8, 609.6) * mm});
            skLineSegment(sketch, "E3.0.21.16", {"start": v(838.2, 622.3) * mm, "end": v(838.2, 647.7) * mm});
            skLineSegment(sketch, "E3.3.21.16", {"start": v(812.8, 647.7) * mm, "end": v(838.2, 647.7) * mm});
            skLineSegment(sketch, "E3.6.21.16", {"start": v(812.8, 622.3) * mm, "end": v(838.2, 622.3) * mm});
            skLineSegment(sketch, "E3.9.21.16", {"start": v(812.8, 622.3) * mm, "end": v(812.8, 647.7) * mm});
            skLineSegment(sketch, "E3.0.21.17", {"start": v(838.2, 660.4) * mm, "end": v(838.2, 685.8) * mm});
            skLineSegment(sketch, "E3.3.21.17", {"start": v(812.8, 685.8) * mm, "end": v(838.2, 685.8) * mm});
            skLineSegment(sketch, "E3.6.21.17", {"start": v(812.8, 660.4) * mm, "end": v(838.2, 660.4) * mm});
            skLineSegment(sketch, "E3.9.21.17", {"start": v(812.8, 660.4) * mm, "end": v(812.8, 685.8) * mm});
            skLineSegment(sketch, "E3.0.21.18", {"start": v(838.2, 698.5) * mm, "end": v(838.2, 723.9) * mm});
            skLineSegment(sketch, "E3.3.21.18", {"start": v(812.8, 723.9) * mm, "end": v(838.2, 723.9) * mm});
            skLineSegment(sketch, "E3.6.21.18", {"start": v(812.8, 698.5) * mm, "end": v(838.2, 698.5) * mm});
            skLineSegment(sketch, "E3.9.21.18", {"start": v(812.8, 698.5) * mm, "end": v(812.8, 723.9) * mm});
            skLineSegment(sketch, "E3.0.21.19", {"start": v(838.2, 736.6) * mm, "end": v(838.2, 762) * mm});
            skLineSegment(sketch, "E3.3.21.19", {"start": v(812.8, 762) * mm, "end": v(838.2, 762) * mm});
            skLineSegment(sketch, "E3.6.21.19", {"start": v(812.8, 736.6) * mm, "end": v(838.2, 736.6) * mm});
            skLineSegment(sketch, "E3.9.21.19", {"start": v(812.8, 736.6) * mm, "end": v(812.8, 762) * mm});
            skLineSegment(sketch, "E3.0.22.0", {"start": v(876.3, 12.7) * mm, "end": v(876.3, 38.1) * mm});
            skLineSegment(sketch, "E3.3.22.0", {"start": v(850.9, 38.1) * mm, "end": v(876.3, 38.1) * mm});
            skLineSegment(sketch, "E3.6.22.0", {"start": v(850.9, 12.7) * mm, "end": v(876.3, 12.7) * mm});
            skLineSegment(sketch, "E3.9.22.0", {"start": v(850.9, 12.7) * mm, "end": v(850.9, 38.1) * mm});
            skLineSegment(sketch, "E3.0.22.1", {"start": v(876.3, 50.8) * mm, "end": v(876.3, 76.2) * mm});
            skLineSegment(sketch, "E3.3.22.1", {"start": v(850.9, 76.2) * mm, "end": v(876.3, 76.2) * mm});
            skLineSegment(sketch, "E3.6.22.1", {"start": v(850.9, 50.8) * mm, "end": v(876.3, 50.8) * mm});
            skLineSegment(sketch, "E3.9.22.1", {"start": v(850.9, 50.8) * mm, "end": v(850.9, 76.2) * mm});
            skLineSegment(sketch, "E3.0.22.2", {"start": v(876.3, 88.9) * mm, "end": v(876.3, 114.3) * mm});
            skLineSegment(sketch, "E3.3.22.2", {"start": v(850.9, 114.3) * mm, "end": v(876.3, 114.3) * mm});
            skLineSegment(sketch, "E3.6.22.2", {"start": v(850.9, 88.9) * mm, "end": v(876.3, 88.9) * mm});
            skLineSegment(sketch, "E3.9.22.2", {"start": v(850.9, 88.9) * mm, "end": v(850.9, 114.3) * mm});
            skLineSegment(sketch, "E3.0.22.3", {"start": v(876.3, 127) * mm, "end": v(876.3, 152.4) * mm});
            skLineSegment(sketch, "E3.3.22.3", {"start": v(850.9, 152.4) * mm, "end": v(876.3, 152.4) * mm});
            skLineSegment(sketch, "E3.6.22.3", {"start": v(850.9, 127) * mm, "end": v(876.3, 127) * mm});
            skLineSegment(sketch, "E3.9.22.3", {"start": v(850.9, 127) * mm, "end": v(850.9, 152.4) * mm});
            skLineSegment(sketch, "E3.0.22.4", {"start": v(876.3, 165.1) * mm, "end": v(876.3, 190.5) * mm});
            skLineSegment(sketch, "E3.3.22.4", {"start": v(850.9, 190.5) * mm, "end": v(876.3, 190.5) * mm});
            skLineSegment(sketch, "E3.6.22.4", {"start": v(850.9, 165.1) * mm, "end": v(876.3, 165.1) * mm});
            skLineSegment(sketch, "E3.9.22.4", {"start": v(850.9, 165.1) * mm, "end": v(850.9, 190.5) * mm});
            skLineSegment(sketch, "E3.0.22.5", {"start": v(876.3, 203.2) * mm, "end": v(876.3, 228.6) * mm});
            skLineSegment(sketch, "E3.3.22.5", {"start": v(850.9, 228.6) * mm, "end": v(876.3, 228.6) * mm});
            skLineSegment(sketch, "E3.6.22.5", {"start": v(850.9, 203.2) * mm, "end": v(876.3, 203.2) * mm});
            skLineSegment(sketch, "E3.9.22.5", {"start": v(850.9, 203.2) * mm, "end": v(850.9, 228.6) * mm});
            skLineSegment(sketch, "E3.0.22.6", {"start": v(876.3, 241.3) * mm, "end": v(876.3, 266.7) * mm});
            skLineSegment(sketch, "E3.3.22.6", {"start": v(850.9, 266.7) * mm, "end": v(876.3, 266.7) * mm});
            skLineSegment(sketch, "E3.6.22.6", {"start": v(850.9, 241.3) * mm, "end": v(876.3, 241.3) * mm});
            skLineSegment(sketch, "E3.9.22.6", {"start": v(850.9, 241.3) * mm, "end": v(850.9, 266.7) * mm});
            skLineSegment(sketch, "E3.0.22.7", {"start": v(876.3, 279.4) * mm, "end": v(876.3, 304.8) * mm});
            skLineSegment(sketch, "E3.3.22.7", {"start": v(850.9, 304.8) * mm, "end": v(876.3, 304.8) * mm});
            skLineSegment(sketch, "E3.6.22.7", {"start": v(850.9, 279.4) * mm, "end": v(876.3, 279.4) * mm});
            skLineSegment(sketch, "E3.9.22.7", {"start": v(850.9, 279.4) * mm, "end": v(850.9, 304.8) * mm});
            skLineSegment(sketch, "E3.0.22.8", {"start": v(876.3, 317.5) * mm, "end": v(876.3, 342.9) * mm});
            skLineSegment(sketch, "E3.3.22.8", {"start": v(850.9, 342.9) * mm, "end": v(876.3, 342.9) * mm});
            skLineSegment(sketch, "E3.6.22.8", {"start": v(850.9, 317.5) * mm, "end": v(876.3, 317.5) * mm});
            skLineSegment(sketch, "E3.9.22.8", {"start": v(850.9, 317.5) * mm, "end": v(850.9, 342.9) * mm});
            skLineSegment(sketch, "E3.0.22.9", {"start": v(876.3, 355.6) * mm, "end": v(876.3, 381) * mm});
            skLineSegment(sketch, "E3.3.22.9", {"start": v(850.9, 381) * mm, "end": v(876.3, 381) * mm});
            skLineSegment(sketch, "E3.6.22.9", {"start": v(850.9, 355.6) * mm, "end": v(876.3, 355.6) * mm});
            skLineSegment(sketch, "E3.9.22.9", {"start": v(850.9, 355.6) * mm, "end": v(850.9, 381) * mm});
            skLineSegment(sketch, "E3.0.22.10", {"start": v(876.3, 393.7) * mm, "end": v(876.3, 419.1) * mm});
            skLineSegment(sketch, "E3.3.22.10", {"start": v(850.9, 419.1) * mm, "end": v(876.3, 419.1) * mm});
            skLineSegment(sketch, "E3.6.22.10", {"start": v(850.9, 393.7) * mm, "end": v(876.3, 393.7) * mm});
            skLineSegment(sketch, "E3.9.22.10", {"start": v(850.9, 393.7) * mm, "end": v(850.9, 419.1) * mm});
            skLineSegment(sketch, "E3.0.22.11", {"start": v(876.3, 431.8) * mm, "end": v(876.3, 457.2) * mm});
            skLineSegment(sketch, "E3.3.22.11", {"start": v(850.9, 457.2) * mm, "end": v(876.3, 457.2) * mm});
            skLineSegment(sketch, "E3.6.22.11", {"start": v(850.9, 431.8) * mm, "end": v(876.3, 431.8) * mm});
            skLineSegment(sketch, "E3.9.22.11", {"start": v(850.9, 431.8) * mm, "end": v(850.9, 457.2) * mm});
            skLineSegment(sketch, "E3.0.22.12", {"start": v(876.3, 469.9) * mm, "end": v(876.3, 495.3) * mm});
            skLineSegment(sketch, "E3.3.22.12", {"start": v(850.9, 495.3) * mm, "end": v(876.3, 495.3) * mm});
            skLineSegment(sketch, "E3.6.22.12", {"start": v(850.9, 469.9) * mm, "end": v(876.3, 469.9) * mm});
            skLineSegment(sketch, "E3.9.22.12", {"start": v(850.9, 469.9) * mm, "end": v(850.9, 495.3) * mm});
            skLineSegment(sketch, "E3.0.22.13", {"start": v(876.3, 508) * mm, "end": v(876.3, 533.4) * mm});
            skLineSegment(sketch, "E3.3.22.13", {"start": v(850.9, 533.4) * mm, "end": v(876.3, 533.4) * mm});
            skLineSegment(sketch, "E3.6.22.13", {"start": v(850.9, 508) * mm, "end": v(876.3, 508) * mm});
            skLineSegment(sketch, "E3.9.22.13", {"start": v(850.9, 508) * mm, "end": v(850.9, 533.4) * mm});
            skLineSegment(sketch, "E3.0.22.14", {"start": v(876.3, 546.1) * mm, "end": v(876.3, 571.5) * mm});
            skLineSegment(sketch, "E3.3.22.14", {"start": v(850.9, 571.5) * mm, "end": v(876.3, 571.5) * mm});
            skLineSegment(sketch, "E3.6.22.14", {"start": v(850.9, 546.1) * mm, "end": v(876.3, 546.1) * mm});
            skLineSegment(sketch, "E3.9.22.14", {"start": v(850.9, 546.1) * mm, "end": v(850.9, 571.5) * mm});
            skLineSegment(sketch, "E3.0.22.15", {"start": v(876.3, 584.2) * mm, "end": v(876.3, 609.6) * mm});
            skLineSegment(sketch, "E3.3.22.15", {"start": v(850.9, 609.6) * mm, "end": v(876.3, 609.6) * mm});
            skLineSegment(sketch, "E3.6.22.15", {"start": v(850.9, 584.2) * mm, "end": v(876.3, 584.2) * mm});
            skLineSegment(sketch, "E3.9.22.15", {"start": v(850.9, 584.2) * mm, "end": v(850.9, 609.6) * mm});
            skLineSegment(sketch, "E3.0.22.16", {"start": v(876.3, 622.3) * mm, "end": v(876.3, 647.7) * mm});
            skLineSegment(sketch, "E3.3.22.16", {"start": v(850.9, 647.7) * mm, "end": v(876.3, 647.7) * mm});
            skLineSegment(sketch, "E3.6.22.16", {"start": v(850.9, 622.3) * mm, "end": v(876.3, 622.3) * mm});
            skLineSegment(sketch, "E3.9.22.16", {"start": v(850.9, 622.3) * mm, "end": v(850.9, 647.7) * mm});
            skLineSegment(sketch, "E3.0.22.17", {"start": v(876.3, 660.4) * mm, "end": v(876.3, 685.8) * mm});
            skLineSegment(sketch, "E3.3.22.17", {"start": v(850.9, 685.8) * mm, "end": v(876.3, 685.8) * mm});
            skLineSegment(sketch, "E3.6.22.17", {"start": v(850.9, 660.4) * mm, "end": v(876.3, 660.4) * mm});
            skLineSegment(sketch, "E3.9.22.17", {"start": v(850.9, 660.4) * mm, "end": v(850.9, 685.8) * mm});
            skLineSegment(sketch, "E3.0.22.18", {"start": v(876.3, 698.5) * mm, "end": v(876.3, 723.9) * mm});
            skLineSegment(sketch, "E3.3.22.18", {"start": v(850.9, 723.9) * mm, "end": v(876.3, 723.9) * mm});
            skLineSegment(sketch, "E3.6.22.18", {"start": v(850.9, 698.5) * mm, "end": v(876.3, 698.5) * mm});
            skLineSegment(sketch, "E3.9.22.18", {"start": v(850.9, 698.5) * mm, "end": v(850.9, 723.9) * mm});
            skLineSegment(sketch, "E3.0.22.19", {"start": v(876.3, 736.6) * mm, "end": v(876.3, 762) * mm});
            skLineSegment(sketch, "E3.3.22.19", {"start": v(850.9, 762) * mm, "end": v(876.3, 762) * mm});
            skLineSegment(sketch, "E3.6.22.19", {"start": v(850.9, 736.6) * mm, "end": v(876.3, 736.6) * mm});
            skLineSegment(sketch, "E3.9.22.19", {"start": v(850.9, 736.6) * mm, "end": v(850.9, 762) * mm});
            skLineSegment(sketch, "E3.0.23.0", {"start": v(914.4, 12.7) * mm, "end": v(914.4, 38.1) * mm});
            skLineSegment(sketch, "E3.3.23.0", {"start": v(889, 38.1) * mm, "end": v(914.4, 38.1) * mm});
            skLineSegment(sketch, "E3.6.23.0", {"start": v(889, 12.7) * mm, "end": v(914.4, 12.7) * mm});
            skLineSegment(sketch, "E3.9.23.0", {"start": v(889, 12.7) * mm, "end": v(889, 38.1) * mm});
            skLineSegment(sketch, "E3.0.23.1", {"start": v(914.4, 50.8) * mm, "end": v(914.4, 76.2) * mm});
            skLineSegment(sketch, "E3.3.23.1", {"start": v(889, 76.2) * mm, "end": v(914.4, 76.2) * mm});
            skLineSegment(sketch, "E3.6.23.1", {"start": v(889, 50.8) * mm, "end": v(914.4, 50.8) * mm});
            skLineSegment(sketch, "E3.9.23.1", {"start": v(889, 50.8) * mm, "end": v(889, 76.2) * mm});
            skLineSegment(sketch, "E3.0.23.2", {"start": v(914.4, 88.9) * mm, "end": v(914.4, 114.3) * mm});
            skLineSegment(sketch, "E3.3.23.2", {"start": v(889, 114.3) * mm, "end": v(914.4, 114.3) * mm});
            skLineSegment(sketch, "E3.6.23.2", {"start": v(889, 88.9) * mm, "end": v(914.4, 88.9) * mm});
            skLineSegment(sketch, "E3.9.23.2", {"start": v(889, 88.9) * mm, "end": v(889, 114.3) * mm});
            skLineSegment(sketch, "E3.0.23.3", {"start": v(914.4, 127) * mm, "end": v(914.4, 152.4) * mm});
            skLineSegment(sketch, "E3.3.23.3", {"start": v(889, 152.4) * mm, "end": v(914.4, 152.4) * mm});
            skLineSegment(sketch, "E3.6.23.3", {"start": v(889, 127) * mm, "end": v(914.4, 127) * mm});
            skLineSegment(sketch, "E3.9.23.3", {"start": v(889, 127) * mm, "end": v(889, 152.4) * mm});
            skLineSegment(sketch, "E3.0.23.4", {"start": v(914.4, 165.1) * mm, "end": v(914.4, 190.5) * mm});
            skLineSegment(sketch, "E3.3.23.4", {"start": v(889, 190.5) * mm, "end": v(914.4, 190.5) * mm});
            skLineSegment(sketch, "E3.6.23.4", {"start": v(889, 165.1) * mm, "end": v(914.4, 165.1) * mm});
            skLineSegment(sketch, "E3.9.23.4", {"start": v(889, 165.1) * mm, "end": v(889, 190.5) * mm});
            skLineSegment(sketch, "E3.0.23.5", {"start": v(914.4, 203.2) * mm, "end": v(914.4, 228.6) * mm});
            skLineSegment(sketch, "E3.3.23.5", {"start": v(889, 228.6) * mm, "end": v(914.4, 228.6) * mm});
            skLineSegment(sketch, "E3.6.23.5", {"start": v(889, 203.2) * mm, "end": v(914.4, 203.2) * mm});
            skLineSegment(sketch, "E3.9.23.5", {"start": v(889, 203.2) * mm, "end": v(889, 228.6) * mm});
            skLineSegment(sketch, "E3.0.23.6", {"start": v(914.4, 241.3) * mm, "end": v(914.4, 266.7) * mm});
            skLineSegment(sketch, "E3.3.23.6", {"start": v(889, 266.7) * mm, "end": v(914.4, 266.7) * mm});
            skLineSegment(sketch, "E3.6.23.6", {"start": v(889, 241.3) * mm, "end": v(914.4, 241.3) * mm});
            skLineSegment(sketch, "E3.9.23.6", {"start": v(889, 241.3) * mm, "end": v(889, 266.7) * mm});
            skLineSegment(sketch, "E3.0.23.7", {"start": v(914.4, 279.4) * mm, "end": v(914.4, 304.8) * mm});
            skLineSegment(sketch, "E3.3.23.7", {"start": v(889, 304.8) * mm, "end": v(914.4, 304.8) * mm});
            skLineSegment(sketch, "E3.6.23.7", {"start": v(889, 279.4) * mm, "end": v(914.4, 279.4) * mm});
            skLineSegment(sketch, "E3.9.23.7", {"start": v(889, 279.4) * mm, "end": v(889, 304.8) * mm});
            skLineSegment(sketch, "E3.0.23.8", {"start": v(914.4, 317.5) * mm, "end": v(914.4, 342.9) * mm});
            skLineSegment(sketch, "E3.3.23.8", {"start": v(889, 342.9) * mm, "end": v(914.4, 342.9) * mm});
            skLineSegment(sketch, "E3.6.23.8", {"start": v(889, 317.5) * mm, "end": v(914.4, 317.5) * mm});
            skLineSegment(sketch, "E3.9.23.8", {"start": v(889, 317.5) * mm, "end": v(889, 342.9) * mm});
            skLineSegment(sketch, "E3.0.23.9", {"start": v(914.4, 355.6) * mm, "end": v(914.4, 381) * mm});
            skLineSegment(sketch, "E3.3.23.9", {"start": v(889, 381) * mm, "end": v(914.4, 381) * mm});
            skLineSegment(sketch, "E3.6.23.9", {"start": v(889, 355.6) * mm, "end": v(914.4, 355.6) * mm});
            skLineSegment(sketch, "E3.9.23.9", {"start": v(889, 355.6) * mm, "end": v(889, 381) * mm});
            skLineSegment(sketch, "E3.0.23.10", {"start": v(914.4, 393.7) * mm, "end": v(914.4, 419.1) * mm});
            skLineSegment(sketch, "E3.3.23.10", {"start": v(889, 419.1) * mm, "end": v(914.4, 419.1) * mm});
            skLineSegment(sketch, "E3.6.23.10", {"start": v(889, 393.7) * mm, "end": v(914.4, 393.7) * mm});
            skLineSegment(sketch, "E3.9.23.10", {"start": v(889, 393.7) * mm, "end": v(889, 419.1) * mm});
            skLineSegment(sketch, "E3.0.23.11", {"start": v(914.4, 431.8) * mm, "end": v(914.4, 457.2) * mm});
            skLineSegment(sketch, "E3.3.23.11", {"start": v(889, 457.2) * mm, "end": v(914.4, 457.2) * mm});
            skLineSegment(sketch, "E3.6.23.11", {"start": v(889, 431.8) * mm, "end": v(914.4, 431.8) * mm});
            skLineSegment(sketch, "E3.9.23.11", {"start": v(889, 431.8) * mm, "end": v(889, 457.2) * mm});
            skLineSegment(sketch, "E3.0.23.12", {"start": v(914.4, 469.9) * mm, "end": v(914.4, 495.3) * mm});
            skLineSegment(sketch, "E3.3.23.12", {"start": v(889, 495.3) * mm, "end": v(914.4, 495.3) * mm});
            skLineSegment(sketch, "E3.6.23.12", {"start": v(889, 469.9) * mm, "end": v(914.4, 469.9) * mm});
            skLineSegment(sketch, "E3.9.23.12", {"start": v(889, 469.9) * mm, "end": v(889, 495.3) * mm});
            skLineSegment(sketch, "E3.0.23.13", {"start": v(914.4, 508) * mm, "end": v(914.4, 533.4) * mm});
            skLineSegment(sketch, "E3.3.23.13", {"start": v(889, 533.4) * mm, "end": v(914.4, 533.4) * mm});
            skLineSegment(sketch, "E3.6.23.13", {"start": v(889, 508) * mm, "end": v(914.4, 508) * mm});
            skLineSegment(sketch, "E3.9.23.13", {"start": v(889, 508) * mm, "end": v(889, 533.4) * mm});
            skLineSegment(sketch, "E3.0.23.14", {"start": v(914.4, 546.1) * mm, "end": v(914.4, 571.5) * mm});
            skLineSegment(sketch, "E3.3.23.14", {"start": v(889, 571.5) * mm, "end": v(914.4, 571.5) * mm});
            skLineSegment(sketch, "E3.6.23.14", {"start": v(889, 546.1) * mm, "end": v(914.4, 546.1) * mm});
            skLineSegment(sketch, "E3.9.23.14", {"start": v(889, 546.1) * mm, "end": v(889, 571.5) * mm});
            skLineSegment(sketch, "E3.0.23.15", {"start": v(914.4, 584.2) * mm, "end": v(914.4, 609.6) * mm});
            skLineSegment(sketch, "E3.3.23.15", {"start": v(889, 609.6) * mm, "end": v(914.4, 609.6) * mm});
            skLineSegment(sketch, "E3.6.23.15", {"start": v(889, 584.2) * mm, "end": v(914.4, 584.2) * mm});
            skLineSegment(sketch, "E3.9.23.15", {"start": v(889, 584.2) * mm, "end": v(889, 609.6) * mm});
            skLineSegment(sketch, "E3.0.23.16", {"start": v(914.4, 622.3) * mm, "end": v(914.4, 647.7) * mm});
            skLineSegment(sketch, "E3.3.23.16", {"start": v(889, 647.7) * mm, "end": v(914.4, 647.7) * mm});
            skLineSegment(sketch, "E3.6.23.16", {"start": v(889, 622.3) * mm, "end": v(914.4, 622.3) * mm});
            skLineSegment(sketch, "E3.9.23.16", {"start": v(889, 622.3) * mm, "end": v(889, 647.7) * mm});
            skLineSegment(sketch, "E3.0.23.17", {"start": v(914.4, 660.4) * mm, "end": v(914.4, 685.8) * mm});
            skLineSegment(sketch, "E3.3.23.17", {"start": v(889, 685.8) * mm, "end": v(914.4, 685.8) * mm});
            skLineSegment(sketch, "E3.6.23.17", {"start": v(889, 660.4) * mm, "end": v(914.4, 660.4) * mm});
            skLineSegment(sketch, "E3.9.23.17", {"start": v(889, 660.4) * mm, "end": v(889, 685.8) * mm});
            skLineSegment(sketch, "E3.0.23.18", {"start": v(914.4, 698.5) * mm, "end": v(914.4, 723.9) * mm});
            skLineSegment(sketch, "E3.3.23.18", {"start": v(889, 723.9) * mm, "end": v(914.4, 723.9) * mm});
            skLineSegment(sketch, "E3.6.23.18", {"start": v(889, 698.5) * mm, "end": v(914.4, 698.5) * mm});
            skLineSegment(sketch, "E3.9.23.18", {"start": v(889, 698.5) * mm, "end": v(889, 723.9) * mm});
            skLineSegment(sketch, "E3.0.23.19", {"start": v(914.4, 736.6) * mm, "end": v(914.4, 762) * mm});
            skLineSegment(sketch, "E3.3.23.19", {"start": v(889, 762) * mm, "end": v(914.4, 762) * mm});
            skLineSegment(sketch, "E3.6.23.19", {"start": v(889, 736.6) * mm, "end": v(914.4, 736.6) * mm});
            skLineSegment(sketch, "E3.9.23.19", {"start": v(889, 736.6) * mm, "end": v(889, 762) * mm});
            skLineSegment(sketch, "E3.0.24.0", {"start": v(952.5, 12.7) * mm, "end": v(952.5, 38.1) * mm});
            skLineSegment(sketch, "E3.3.24.0", {"start": v(927.1, 38.1) * mm, "end": v(952.5, 38.1) * mm});
            skLineSegment(sketch, "E3.6.24.0", {"start": v(927.1, 12.7) * mm, "end": v(952.5, 12.7) * mm});
            skLineSegment(sketch, "E3.9.24.0", {"start": v(927.1, 12.7) * mm, "end": v(927.1, 38.1) * mm});
            skLineSegment(sketch, "E3.0.24.1", {"start": v(952.5, 50.8) * mm, "end": v(952.5, 76.2) * mm});
            skLineSegment(sketch, "E3.3.24.1", {"start": v(927.1, 76.2) * mm, "end": v(952.5, 76.2) * mm});
            skLineSegment(sketch, "E3.6.24.1", {"start": v(927.1, 50.8) * mm, "end": v(952.5, 50.8) * mm});
            skLineSegment(sketch, "E3.9.24.1", {"start": v(927.1, 50.8) * mm, "end": v(927.1, 76.2) * mm});
            skLineSegment(sketch, "E3.0.24.2", {"start": v(952.5, 88.9) * mm, "end": v(952.5, 114.3) * mm});
            skLineSegment(sketch, "E3.3.24.2", {"start": v(927.1, 114.3) * mm, "end": v(952.5, 114.3) * mm});
            skLineSegment(sketch, "E3.6.24.2", {"start": v(927.1, 88.9) * mm, "end": v(952.5, 88.9) * mm});
            skLineSegment(sketch, "E3.9.24.2", {"start": v(927.1, 88.9) * mm, "end": v(927.1, 114.3) * mm});
            skLineSegment(sketch, "E3.0.24.3", {"start": v(952.5, 127) * mm, "end": v(952.5, 152.4) * mm});
            skLineSegment(sketch, "E3.3.24.3", {"start": v(927.1, 152.4) * mm, "end": v(952.5, 152.4) * mm});
            skLineSegment(sketch, "E3.6.24.3", {"start": v(927.1, 127) * mm, "end": v(952.5, 127) * mm});
            skLineSegment(sketch, "E3.9.24.3", {"start": v(927.1, 127) * mm, "end": v(927.1, 152.4) * mm});
            skLineSegment(sketch, "E3.0.24.4", {"start": v(952.5, 165.1) * mm, "end": v(952.5, 190.5) * mm});
            skLineSegment(sketch, "E3.3.24.4", {"start": v(927.1, 190.5) * mm, "end": v(952.5, 190.5) * mm});
            skLineSegment(sketch, "E3.6.24.4", {"start": v(927.1, 165.1) * mm, "end": v(952.5, 165.1) * mm});
            skLineSegment(sketch, "E3.9.24.4", {"start": v(927.1, 165.1) * mm, "end": v(927.1, 190.5) * mm});
            skLineSegment(sketch, "E3.0.24.5", {"start": v(952.5, 203.2) * mm, "end": v(952.5, 228.6) * mm});
            skLineSegment(sketch, "E3.3.24.5", {"start": v(927.1, 228.6) * mm, "end": v(952.5, 228.6) * mm});
            skLineSegment(sketch, "E3.6.24.5", {"start": v(927.1, 203.2) * mm, "end": v(952.5, 203.2) * mm});
            skLineSegment(sketch, "E3.9.24.5", {"start": v(927.1, 203.2) * mm, "end": v(927.1, 228.6) * mm});
            skLineSegment(sketch, "E3.0.24.6", {"start": v(952.5, 241.3) * mm, "end": v(952.5, 266.7) * mm});
            skLineSegment(sketch, "E3.3.24.6", {"start": v(927.1, 266.7) * mm, "end": v(952.5, 266.7) * mm});
            skLineSegment(sketch, "E3.6.24.6", {"start": v(927.1, 241.3) * mm, "end": v(952.5, 241.3) * mm});
            skLineSegment(sketch, "E3.9.24.6", {"start": v(927.1, 241.3) * mm, "end": v(927.1, 266.7) * mm});
            skLineSegment(sketch, "E3.0.24.7", {"start": v(952.5, 279.4) * mm, "end": v(952.5, 304.8) * mm});
            skLineSegment(sketch, "E3.3.24.7", {"start": v(927.1, 304.8) * mm, "end": v(952.5, 304.8) * mm});
            skLineSegment(sketch, "E3.6.24.7", {"start": v(927.1, 279.4) * mm, "end": v(952.5, 279.4) * mm});
            skLineSegment(sketch, "E3.9.24.7", {"start": v(927.1, 279.4) * mm, "end": v(927.1, 304.8) * mm});
            skLineSegment(sketch, "E3.0.24.8", {"start": v(952.5, 317.5) * mm, "end": v(952.5, 342.9) * mm});
            skLineSegment(sketch, "E3.3.24.8", {"start": v(927.1, 342.9) * mm, "end": v(952.5, 342.9) * mm});
            skLineSegment(sketch, "E3.6.24.8", {"start": v(927.1, 317.5) * mm, "end": v(952.5, 317.5) * mm});
            skLineSegment(sketch, "E3.9.24.8", {"start": v(927.1, 317.5) * mm, "end": v(927.1, 342.9) * mm});
            skLineSegment(sketch, "E3.0.24.9", {"start": v(952.5, 355.6) * mm, "end": v(952.5, 381) * mm});
            skLineSegment(sketch, "E3.3.24.9", {"start": v(927.1, 381) * mm, "end": v(952.5, 381) * mm});
            skLineSegment(sketch, "E3.6.24.9", {"start": v(927.1, 355.6) * mm, "end": v(952.5, 355.6) * mm});
            skLineSegment(sketch, "E3.9.24.9", {"start": v(927.1, 355.6) * mm, "end": v(927.1, 381) * mm});
            skLineSegment(sketch, "E3.0.24.10", {"start": v(952.5, 393.7) * mm, "end": v(952.5, 419.1) * mm});
            skLineSegment(sketch, "E3.3.24.10", {"start": v(927.1, 419.1) * mm, "end": v(952.5, 419.1) * mm});
            skLineSegment(sketch, "E3.6.24.10", {"start": v(927.1, 393.7) * mm, "end": v(952.5, 393.7) * mm});
            skLineSegment(sketch, "E3.9.24.10", {"start": v(927.1, 393.7) * mm, "end": v(927.1, 419.1) * mm});
            skLineSegment(sketch, "E3.0.24.11", {"start": v(952.5, 431.8) * mm, "end": v(952.5, 457.2) * mm});
            skLineSegment(sketch, "E3.3.24.11", {"start": v(927.1, 457.2) * mm, "end": v(952.5, 457.2) * mm});
            skLineSegment(sketch, "E3.6.24.11", {"start": v(927.1, 431.8) * mm, "end": v(952.5, 431.8) * mm});
            skLineSegment(sketch, "E3.9.24.11", {"start": v(927.1, 431.8) * mm, "end": v(927.1, 457.2) * mm});
            skLineSegment(sketch, "E3.0.24.12", {"start": v(952.5, 469.9) * mm, "end": v(952.5, 495.3) * mm});
            skLineSegment(sketch, "E3.3.24.12", {"start": v(927.1, 495.3) * mm, "end": v(952.5, 495.3) * mm});
            skLineSegment(sketch, "E3.6.24.12", {"start": v(927.1, 469.9) * mm, "end": v(952.5, 469.9) * mm});
            skLineSegment(sketch, "E3.9.24.12", {"start": v(927.1, 469.9) * mm, "end": v(927.1, 495.3) * mm});
            skLineSegment(sketch, "E3.0.24.13", {"start": v(952.5, 508) * mm, "end": v(952.5, 533.4) * mm});
            skLineSegment(sketch, "E3.3.24.13", {"start": v(927.1, 533.4) * mm, "end": v(952.5, 533.4) * mm});
            skLineSegment(sketch, "E3.6.24.13", {"start": v(927.1, 508) * mm, "end": v(952.5, 508) * mm});
            skLineSegment(sketch, "E3.9.24.13", {"start": v(927.1, 508) * mm, "end": v(927.1, 533.4) * mm});
            skLineSegment(sketch, "E3.0.24.14", {"start": v(952.5, 546.1) * mm, "end": v(952.5, 571.5) * mm});
            skLineSegment(sketch, "E3.3.24.14", {"start": v(927.1, 571.5) * mm, "end": v(952.5, 571.5) * mm});
            skLineSegment(sketch, "E3.6.24.14", {"start": v(927.1, 546.1) * mm, "end": v(952.5, 546.1) * mm});
            skLineSegment(sketch, "E3.9.24.14", {"start": v(927.1, 546.1) * mm, "end": v(927.1, 571.5) * mm});
            skLineSegment(sketch, "E3.0.24.15", {"start": v(952.5, 584.2) * mm, "end": v(952.5, 609.6) * mm});
            skLineSegment(sketch, "E3.3.24.15", {"start": v(927.1, 609.6) * mm, "end": v(952.5, 609.6) * mm});
            skLineSegment(sketch, "E3.6.24.15", {"start": v(927.1, 584.2) * mm, "end": v(952.5, 584.2) * mm});
            skLineSegment(sketch, "E3.9.24.15", {"start": v(927.1, 584.2) * mm, "end": v(927.1, 609.6) * mm});
            skLineSegment(sketch, "E3.0.24.16", {"start": v(952.5, 622.3) * mm, "end": v(952.5, 647.7) * mm});
            skLineSegment(sketch, "E3.3.24.16", {"start": v(927.1, 647.7) * mm, "end": v(952.5, 647.7) * mm});
            skLineSegment(sketch, "E3.6.24.16", {"start": v(927.1, 622.3) * mm, "end": v(952.5, 622.3) * mm});
            skLineSegment(sketch, "E3.9.24.16", {"start": v(927.1, 622.3) * mm, "end": v(927.1, 647.7) * mm});
            skLineSegment(sketch, "E3.0.24.17", {"start": v(952.5, 660.4) * mm, "end": v(952.5, 685.8) * mm});
            skLineSegment(sketch, "E3.3.24.17", {"start": v(927.1, 685.8) * mm, "end": v(952.5, 685.8) * mm});
            skLineSegment(sketch, "E3.6.24.17", {"start": v(927.1, 660.4) * mm, "end": v(952.5, 660.4) * mm});
            skLineSegment(sketch, "E3.9.24.17", {"start": v(927.1, 660.4) * mm, "end": v(927.1, 685.8) * mm});
            skLineSegment(sketch, "E3.0.24.18", {"start": v(952.5, 698.5) * mm, "end": v(952.5, 723.9) * mm});
            skLineSegment(sketch, "E3.3.24.18", {"start": v(927.1, 723.9) * mm, "end": v(952.5, 723.9) * mm});
            skLineSegment(sketch, "E3.6.24.18", {"start": v(927.1, 698.5) * mm, "end": v(952.5, 698.5) * mm});
            skLineSegment(sketch, "E3.9.24.18", {"start": v(927.1, 698.5) * mm, "end": v(927.1, 723.9) * mm});
            skLineSegment(sketch, "E3.0.24.19", {"start": v(952.5, 736.6) * mm, "end": v(952.5, 762) * mm});
            skLineSegment(sketch, "E3.3.24.19", {"start": v(927.1, 762) * mm, "end": v(952.5, 762) * mm});
            skLineSegment(sketch, "E3.6.24.19", {"start": v(927.1, 736.6) * mm, "end": v(952.5, 736.6) * mm});
            skLineSegment(sketch, "E3.9.24.19", {"start": v(927.1, 736.6) * mm, "end": v(927.1, 762) * mm});
            skLineSegment(sketch, "E3.0.25.0", {"start": v(990.6, 12.7) * mm, "end": v(990.6, 38.1) * mm});
            skLineSegment(sketch, "E3.3.25.0", {"start": v(965.2, 38.1) * mm, "end": v(990.6, 38.1) * mm});
            skLineSegment(sketch, "E3.6.25.0", {"start": v(965.2, 12.7) * mm, "end": v(990.6, 12.7) * mm});
            skLineSegment(sketch, "E3.9.25.0", {"start": v(965.2, 12.7) * mm, "end": v(965.2, 38.1) * mm});
            skLineSegment(sketch, "E3.0.25.1", {"start": v(990.6, 50.8) * mm, "end": v(990.6, 76.2) * mm});
            skLineSegment(sketch, "E3.3.25.1", {"start": v(965.2, 76.2) * mm, "end": v(990.6, 76.2) * mm});
            skLineSegment(sketch, "E3.6.25.1", {"start": v(965.2, 50.8) * mm, "end": v(990.6, 50.8) * mm});
            skLineSegment(sketch, "E3.9.25.1", {"start": v(965.2, 50.8) * mm, "end": v(965.2, 76.2) * mm});
            skLineSegment(sketch, "E3.0.25.2", {"start": v(990.6, 88.9) * mm, "end": v(990.6, 114.3) * mm});
            skLineSegment(sketch, "E3.3.25.2", {"start": v(965.2, 114.3) * mm, "end": v(990.6, 114.3) * mm});
            skLineSegment(sketch, "E3.6.25.2", {"start": v(965.2, 88.9) * mm, "end": v(990.6, 88.9) * mm});
            skLineSegment(sketch, "E3.9.25.2", {"start": v(965.2, 88.9) * mm, "end": v(965.2, 114.3) * mm});
            skLineSegment(sketch, "E3.0.25.3", {"start": v(990.6, 127) * mm, "end": v(990.6, 152.4) * mm});
            skLineSegment(sketch, "E3.3.25.3", {"start": v(965.2, 152.4) * mm, "end": v(990.6, 152.4) * mm});
            skLineSegment(sketch, "E3.6.25.3", {"start": v(965.2, 127) * mm, "end": v(990.6, 127) * mm});
            skLineSegment(sketch, "E3.9.25.3", {"start": v(965.2, 127) * mm, "end": v(965.2, 152.4) * mm});
            skLineSegment(sketch, "E3.0.25.4", {"start": v(990.6, 165.1) * mm, "end": v(990.6, 190.5) * mm});
            skLineSegment(sketch, "E3.3.25.4", {"start": v(965.2, 190.5) * mm, "end": v(990.6, 190.5) * mm});
            skLineSegment(sketch, "E3.6.25.4", {"start": v(965.2, 165.1) * mm, "end": v(990.6, 165.1) * mm});
            skLineSegment(sketch, "E3.9.25.4", {"start": v(965.2, 165.1) * mm, "end": v(965.2, 190.5) * mm});
            skLineSegment(sketch, "E3.0.25.5", {"start": v(990.6, 203.2) * mm, "end": v(990.6, 228.6) * mm});
            skLineSegment(sketch, "E3.3.25.5", {"start": v(965.2, 228.6) * mm, "end": v(990.6, 228.6) * mm});
            skLineSegment(sketch, "E3.6.25.5", {"start": v(965.2, 203.2) * mm, "end": v(990.6, 203.2) * mm});
            skLineSegment(sketch, "E3.9.25.5", {"start": v(965.2, 203.2) * mm, "end": v(965.2, 228.6) * mm});
            skLineSegment(sketch, "E3.0.25.6", {"start": v(990.6, 241.3) * mm, "end": v(990.6, 266.7) * mm});
            skLineSegment(sketch, "E3.3.25.6", {"start": v(965.2, 266.7) * mm, "end": v(990.6, 266.7) * mm});
            skLineSegment(sketch, "E3.6.25.6", {"start": v(965.2, 241.3) * mm, "end": v(990.6, 241.3) * mm});
            skLineSegment(sketch, "E3.9.25.6", {"start": v(965.2, 241.3) * mm, "end": v(965.2, 266.7) * mm});
            skLineSegment(sketch, "E3.0.25.7", {"start": v(990.6, 279.4) * mm, "end": v(990.6, 304.8) * mm});
            skLineSegment(sketch, "E3.3.25.7", {"start": v(965.2, 304.8) * mm, "end": v(990.6, 304.8) * mm});
            skLineSegment(sketch, "E3.6.25.7", {"start": v(965.2, 279.4) * mm, "end": v(990.6, 279.4) * mm});
            skLineSegment(sketch, "E3.9.25.7", {"start": v(965.2, 279.4) * mm, "end": v(965.2, 304.8) * mm});
            skLineSegment(sketch, "E3.0.25.8", {"start": v(990.6, 317.5) * mm, "end": v(990.6, 342.9) * mm});
            skLineSegment(sketch, "E3.3.25.8", {"start": v(965.2, 342.9) * mm, "end": v(990.6, 342.9) * mm});
            skLineSegment(sketch, "E3.6.25.8", {"start": v(965.2, 317.5) * mm, "end": v(990.6, 317.5) * mm});
            skLineSegment(sketch, "E3.9.25.8", {"start": v(965.2, 317.5) * mm, "end": v(965.2, 342.9) * mm});
            skLineSegment(sketch, "E3.0.25.9", {"start": v(990.6, 355.6) * mm, "end": v(990.6, 381) * mm});
            skLineSegment(sketch, "E3.3.25.9", {"start": v(965.2, 381) * mm, "end": v(990.6, 381) * mm});
            skLineSegment(sketch, "E3.6.25.9", {"start": v(965.2, 355.6) * mm, "end": v(990.6, 355.6) * mm});
            skLineSegment(sketch, "E3.9.25.9", {"start": v(965.2, 355.6) * mm, "end": v(965.2, 381) * mm});
            skLineSegment(sketch, "E3.0.25.10", {"start": v(990.6, 393.7) * mm, "end": v(990.6, 419.1) * mm});
            skLineSegment(sketch, "E3.3.25.10", {"start": v(965.2, 419.1) * mm, "end": v(990.6, 419.1) * mm});
            skLineSegment(sketch, "E3.6.25.10", {"start": v(965.2, 393.7) * mm, "end": v(990.6, 393.7) * mm});
            skLineSegment(sketch, "E3.9.25.10", {"start": v(965.2, 393.7) * mm, "end": v(965.2, 419.1) * mm});
            skLineSegment(sketch, "E3.0.25.11", {"start": v(990.6, 431.8) * mm, "end": v(990.6, 457.2) * mm});
            skLineSegment(sketch, "E3.3.25.11", {"start": v(965.2, 457.2) * mm, "end": v(990.6, 457.2) * mm});
            skLineSegment(sketch, "E3.6.25.11", {"start": v(965.2, 431.8) * mm, "end": v(990.6, 431.8) * mm});
            skLineSegment(sketch, "E3.9.25.11", {"start": v(965.2, 431.8) * mm, "end": v(965.2, 457.2) * mm});
            skLineSegment(sketch, "E3.0.25.12", {"start": v(990.6, 469.9) * mm, "end": v(990.6, 495.3) * mm});
            skLineSegment(sketch, "E3.3.25.12", {"start": v(965.2, 495.3) * mm, "end": v(990.6, 495.3) * mm});
            skLineSegment(sketch, "E3.6.25.12", {"start": v(965.2, 469.9) * mm, "end": v(990.6, 469.9) * mm});
            skLineSegment(sketch, "E3.9.25.12", {"start": v(965.2, 469.9) * mm, "end": v(965.2, 495.3) * mm});
            skLineSegment(sketch, "E3.0.25.13", {"start": v(990.6, 508) * mm, "end": v(990.6, 533.4) * mm});
            skLineSegment(sketch, "E3.3.25.13", {"start": v(965.2, 533.4) * mm, "end": v(990.6, 533.4) * mm});
            skLineSegment(sketch, "E3.6.25.13", {"start": v(965.2, 508) * mm, "end": v(990.6, 508) * mm});
            skLineSegment(sketch, "E3.9.25.13", {"start": v(965.2, 508) * mm, "end": v(965.2, 533.4) * mm});
            skLineSegment(sketch, "E3.0.25.14", {"start": v(990.6, 546.1) * mm, "end": v(990.6, 571.5) * mm});
            skLineSegment(sketch, "E3.3.25.14", {"start": v(965.2, 571.5) * mm, "end": v(990.6, 571.5) * mm});
            skLineSegment(sketch, "E3.6.25.14", {"start": v(965.2, 546.1) * mm, "end": v(990.6, 546.1) * mm});
            skLineSegment(sketch, "E3.9.25.14", {"start": v(965.2, 546.1) * mm, "end": v(965.2, 571.5) * mm});
            skLineSegment(sketch, "E3.0.25.15", {"start": v(990.6, 584.2) * mm, "end": v(990.6, 609.6) * mm});
            skLineSegment(sketch, "E3.3.25.15", {"start": v(965.2, 609.6) * mm, "end": v(990.6, 609.6) * mm});
            skLineSegment(sketch, "E3.6.25.15", {"start": v(965.2, 584.2) * mm, "end": v(990.6, 584.2) * mm});
            skLineSegment(sketch, "E3.9.25.15", {"start": v(965.2, 584.2) * mm, "end": v(965.2, 609.6) * mm});
            skLineSegment(sketch, "E3.0.25.16", {"start": v(990.6, 622.3) * mm, "end": v(990.6, 647.7) * mm});
            skLineSegment(sketch, "E3.3.25.16", {"start": v(965.2, 647.7) * mm, "end": v(990.6, 647.7) * mm});
            skLineSegment(sketch, "E3.6.25.16", {"start": v(965.2, 622.3) * mm, "end": v(990.6, 622.3) * mm});
            skLineSegment(sketch, "E3.9.25.16", {"start": v(965.2, 622.3) * mm, "end": v(965.2, 647.7) * mm});
            skLineSegment(sketch, "E3.0.25.17", {"start": v(990.6, 660.4) * mm, "end": v(990.6, 685.8) * mm});
            skLineSegment(sketch, "E3.3.25.17", {"start": v(965.2, 685.8) * mm, "end": v(990.6, 685.8) * mm});
            skLineSegment(sketch, "E3.6.25.17", {"start": v(965.2, 660.4) * mm, "end": v(990.6, 660.4) * mm});
            skLineSegment(sketch, "E3.9.25.17", {"start": v(965.2, 660.4) * mm, "end": v(965.2, 685.8) * mm});
            skLineSegment(sketch, "E3.0.25.18", {"start": v(990.6, 698.5) * mm, "end": v(990.6, 723.9) * mm});
            skLineSegment(sketch, "E3.3.25.18", {"start": v(965.2, 723.9) * mm, "end": v(990.6, 723.9) * mm});
            skLineSegment(sketch, "E3.6.25.18", {"start": v(965.2, 698.5) * mm, "end": v(990.6, 698.5) * mm});
            skLineSegment(sketch, "E3.9.25.18", {"start": v(965.2, 698.5) * mm, "end": v(965.2, 723.9) * mm});
            skLineSegment(sketch, "E3.0.25.19", {"start": v(990.6, 736.6) * mm, "end": v(990.6, 762) * mm});
            skLineSegment(sketch, "E3.3.25.19", {"start": v(965.2, 762) * mm, "end": v(990.6, 762) * mm});
            skLineSegment(sketch, "E3.6.25.19", {"start": v(965.2, 736.6) * mm, "end": v(990.6, 736.6) * mm});
            skLineSegment(sketch, "E3.9.25.19", {"start": v(965.2, 736.6) * mm, "end": v(965.2, 762) * mm});
            skLineSegment(sketch, "E3.0.26.0", {"start": v(1028.7, 12.7) * mm, "end": v(1028.7, 38.1) * mm});
            skLineSegment(sketch, "E3.3.26.0", {"start": v(1003.3, 38.1) * mm, "end": v(1028.7, 38.1) * mm});
            skLineSegment(sketch, "E3.6.26.0", {"start": v(1003.3, 12.7) * mm, "end": v(1028.7, 12.7) * mm});
            skLineSegment(sketch, "E3.9.26.0", {"start": v(1003.3, 12.7) * mm, "end": v(1003.3, 38.1) * mm});
            skLineSegment(sketch, "E3.0.26.1", {"start": v(1028.7, 50.8) * mm, "end": v(1028.7, 76.2) * mm});
            skLineSegment(sketch, "E3.3.26.1", {"start": v(1003.3, 76.2) * mm, "end": v(1028.7, 76.2) * mm});
            skLineSegment(sketch, "E3.6.26.1", {"start": v(1003.3, 50.8) * mm, "end": v(1028.7, 50.8) * mm});
            skLineSegment(sketch, "E3.9.26.1", {"start": v(1003.3, 50.8) * mm, "end": v(1003.3, 76.2) * mm});
            skLineSegment(sketch, "E3.0.26.2", {"start": v(1028.7, 88.9) * mm, "end": v(1028.7, 114.3) * mm});
            skLineSegment(sketch, "E3.3.26.2", {"start": v(1003.3, 114.3) * mm, "end": v(1028.7, 114.3) * mm});
            skLineSegment(sketch, "E3.6.26.2", {"start": v(1003.3, 88.9) * mm, "end": v(1028.7, 88.9) * mm});
            skLineSegment(sketch, "E3.9.26.2", {"start": v(1003.3, 88.9) * mm, "end": v(1003.3, 114.3) * mm});
            skLineSegment(sketch, "E3.0.26.3", {"start": v(1028.7, 127) * mm, "end": v(1028.7, 152.4) * mm});
            skLineSegment(sketch, "E3.3.26.3", {"start": v(1003.3, 152.4) * mm, "end": v(1028.7, 152.4) * mm});
            skLineSegment(sketch, "E3.6.26.3", {"start": v(1003.3, 127) * mm, "end": v(1028.7, 127) * mm});
            skLineSegment(sketch, "E3.9.26.3", {"start": v(1003.3, 127) * mm, "end": v(1003.3, 152.4) * mm});
            skLineSegment(sketch, "E3.0.26.4", {"start": v(1028.7, 165.1) * mm, "end": v(1028.7, 190.5) * mm});
            skLineSegment(sketch, "E3.3.26.4", {"start": v(1003.3, 190.5) * mm, "end": v(1028.7, 190.5) * mm});
            skLineSegment(sketch, "E3.6.26.4", {"start": v(1003.3, 165.1) * mm, "end": v(1028.7, 165.1) * mm});
            skLineSegment(sketch, "E3.9.26.4", {"start": v(1003.3, 165.1) * mm, "end": v(1003.3, 190.5) * mm});
            skLineSegment(sketch, "E3.0.26.5", {"start": v(1028.7, 203.2) * mm, "end": v(1028.7, 228.6) * mm});
            skLineSegment(sketch, "E3.3.26.5", {"start": v(1003.3, 228.6) * mm, "end": v(1028.7, 228.6) * mm});
            skLineSegment(sketch, "E3.6.26.5", {"start": v(1003.3, 203.2) * mm, "end": v(1028.7, 203.2) * mm});
            skLineSegment(sketch, "E3.9.26.5", {"start": v(1003.3, 203.2) * mm, "end": v(1003.3, 228.6) * mm});
            skLineSegment(sketch, "E3.0.26.6", {"start": v(1028.7, 241.3) * mm, "end": v(1028.7, 266.7) * mm});
            skLineSegment(sketch, "E3.3.26.6", {"start": v(1003.3, 266.7) * mm, "end": v(1028.7, 266.7) * mm});
            skLineSegment(sketch, "E3.6.26.6", {"start": v(1003.3, 241.3) * mm, "end": v(1028.7, 241.3) * mm});
            skLineSegment(sketch, "E3.9.26.6", {"start": v(1003.3, 241.3) * mm, "end": v(1003.3, 266.7) * mm});
            skLineSegment(sketch, "E3.0.26.7", {"start": v(1028.7, 279.4) * mm, "end": v(1028.7, 304.8) * mm});
            skLineSegment(sketch, "E3.3.26.7", {"start": v(1003.3, 304.8) * mm, "end": v(1028.7, 304.8) * mm});
            skLineSegment(sketch, "E3.6.26.7", {"start": v(1003.3, 279.4) * mm, "end": v(1028.7, 279.4) * mm});
            skLineSegment(sketch, "E3.9.26.7", {"start": v(1003.3, 279.4) * mm, "end": v(1003.3, 304.8) * mm});
            skLineSegment(sketch, "E3.0.26.8", {"start": v(1028.7, 317.5) * mm, "end": v(1028.7, 342.9) * mm});
            skLineSegment(sketch, "E3.3.26.8", {"start": v(1003.3, 342.9) * mm, "end": v(1028.7, 342.9) * mm});
            skLineSegment(sketch, "E3.6.26.8", {"start": v(1003.3, 317.5) * mm, "end": v(1028.7, 317.5) * mm});
            skLineSegment(sketch, "E3.9.26.8", {"start": v(1003.3, 317.5) * mm, "end": v(1003.3, 342.9) * mm});
            skLineSegment(sketch, "E3.0.26.9", {"start": v(1028.7, 355.6) * mm, "end": v(1028.7, 381) * mm});
            skLineSegment(sketch, "E3.3.26.9", {"start": v(1003.3, 381) * mm, "end": v(1028.7, 381) * mm});
            skLineSegment(sketch, "E3.6.26.9", {"start": v(1003.3, 355.6) * mm, "end": v(1028.7, 355.6) * mm});
            skLineSegment(sketch, "E3.9.26.9", {"start": v(1003.3, 355.6) * mm, "end": v(1003.3, 381) * mm});
            skLineSegment(sketch, "E3.0.26.10", {"start": v(1028.7, 393.7) * mm, "end": v(1028.7, 419.1) * mm});
            skLineSegment(sketch, "E3.3.26.10", {"start": v(1003.3, 419.1) * mm, "end": v(1028.7, 419.1) * mm});
            skLineSegment(sketch, "E3.6.26.10", {"start": v(1003.3, 393.7) * mm, "end": v(1028.7, 393.7) * mm});
            skLineSegment(sketch, "E3.9.26.10", {"start": v(1003.3, 393.7) * mm, "end": v(1003.3, 419.1) * mm});
            skLineSegment(sketch, "E3.0.26.11", {"start": v(1028.7, 431.8) * mm, "end": v(1028.7, 457.2) * mm});
            skLineSegment(sketch, "E3.3.26.11", {"start": v(1003.3, 457.2) * mm, "end": v(1028.7, 457.2) * mm});
            skLineSegment(sketch, "E3.6.26.11", {"start": v(1003.3, 431.8) * mm, "end": v(1028.7, 431.8) * mm});
            skLineSegment(sketch, "E3.9.26.11", {"start": v(1003.3, 431.8) * mm, "end": v(1003.3, 457.2) * mm});
            skLineSegment(sketch, "E3.0.26.12", {"start": v(1028.7, 469.9) * mm, "end": v(1028.7, 495.3) * mm});
            skLineSegment(sketch, "E3.3.26.12", {"start": v(1003.3, 495.3) * mm, "end": v(1028.7, 495.3) * mm});
            skLineSegment(sketch, "E3.6.26.12", {"start": v(1003.3, 469.9) * mm, "end": v(1028.7, 469.9) * mm});
            skLineSegment(sketch, "E3.9.26.12", {"start": v(1003.3, 469.9) * mm, "end": v(1003.3, 495.3) * mm});
            skLineSegment(sketch, "E3.0.26.13", {"start": v(1028.7, 508) * mm, "end": v(1028.7, 533.4) * mm});
            skLineSegment(sketch, "E3.3.26.13", {"start": v(1003.3, 533.4) * mm, "end": v(1028.7, 533.4) * mm});
            skLineSegment(sketch, "E3.6.26.13", {"start": v(1003.3, 508) * mm, "end": v(1028.7, 508) * mm});
            skLineSegment(sketch, "E3.9.26.13", {"start": v(1003.3, 508) * mm, "end": v(1003.3, 533.4) * mm});
            skLineSegment(sketch, "E3.0.26.14", {"start": v(1028.7, 546.1) * mm, "end": v(1028.7, 571.5) * mm});
            skLineSegment(sketch, "E3.3.26.14", {"start": v(1003.3, 571.5) * mm, "end": v(1028.7, 571.5) * mm});
            skLineSegment(sketch, "E3.6.26.14", {"start": v(1003.3, 546.1) * mm, "end": v(1028.7, 546.1) * mm});
            skLineSegment(sketch, "E3.9.26.14", {"start": v(1003.3, 546.1) * mm, "end": v(1003.3, 571.5) * mm});
            skLineSegment(sketch, "E3.0.26.15", {"start": v(1028.7, 584.2) * mm, "end": v(1028.7, 609.6) * mm});
            skLineSegment(sketch, "E3.3.26.15", {"start": v(1003.3, 609.6) * mm, "end": v(1028.7, 609.6) * mm});
            skLineSegment(sketch, "E3.6.26.15", {"start": v(1003.3, 584.2) * mm, "end": v(1028.7, 584.2) * mm});
            skLineSegment(sketch, "E3.9.26.15", {"start": v(1003.3, 584.2) * mm, "end": v(1003.3, 609.6) * mm});
            skLineSegment(sketch, "E3.0.26.16", {"start": v(1028.7, 622.3) * mm, "end": v(1028.7, 647.7) * mm});
            skLineSegment(sketch, "E3.3.26.16", {"start": v(1003.3, 647.7) * mm, "end": v(1028.7, 647.7) * mm});
            skLineSegment(sketch, "E3.6.26.16", {"start": v(1003.3, 622.3) * mm, "end": v(1028.7, 622.3) * mm});
            skLineSegment(sketch, "E3.9.26.16", {"start": v(1003.3, 622.3) * mm, "end": v(1003.3, 647.7) * mm});
            skLineSegment(sketch, "E3.0.26.17", {"start": v(1028.7, 660.4) * mm, "end": v(1028.7, 685.8) * mm});
            skLineSegment(sketch, "E3.3.26.17", {"start": v(1003.3, 685.8) * mm, "end": v(1028.7, 685.8) * mm});
            skLineSegment(sketch, "E3.6.26.17", {"start": v(1003.3, 660.4) * mm, "end": v(1028.7, 660.4) * mm});
            skLineSegment(sketch, "E3.9.26.17", {"start": v(1003.3, 660.4) * mm, "end": v(1003.3, 685.8) * mm});
            skLineSegment(sketch, "E3.0.26.18", {"start": v(1028.7, 698.5) * mm, "end": v(1028.7, 723.9) * mm});
            skLineSegment(sketch, "E3.3.26.18", {"start": v(1003.3, 723.9) * mm, "end": v(1028.7, 723.9) * mm});
            skLineSegment(sketch, "E3.6.26.18", {"start": v(1003.3, 698.5) * mm, "end": v(1028.7, 698.5) * mm});
            skLineSegment(sketch, "E3.9.26.18", {"start": v(1003.3, 698.5) * mm, "end": v(1003.3, 723.9) * mm});
            skLineSegment(sketch, "E3.0.26.19", {"start": v(1028.7, 736.6) * mm, "end": v(1028.7, 762) * mm});
            skLineSegment(sketch, "E3.3.26.19", {"start": v(1003.3, 762) * mm, "end": v(1028.7, 762) * mm});
            skLineSegment(sketch, "E3.6.26.19", {"start": v(1003.3, 736.6) * mm, "end": v(1028.7, 736.6) * mm});
            skLineSegment(sketch, "E3.9.26.19", {"start": v(1003.3, 736.6) * mm, "end": v(1003.3, 762) * mm});
            skLineSegment(sketch, "E3.0.27.0", {"start": v(1066.8, 12.7) * mm, "end": v(1066.8, 38.1) * mm});
            skLineSegment(sketch, "E3.3.27.0", {"start": v(1041.4, 38.1) * mm, "end": v(1066.8, 38.1) * mm});
            skLineSegment(sketch, "E3.6.27.0", {"start": v(1041.4, 12.7) * mm, "end": v(1066.8, 12.7) * mm});
            skLineSegment(sketch, "E3.9.27.0", {"start": v(1041.4, 12.7) * mm, "end": v(1041.4, 38.1) * mm});
            skLineSegment(sketch, "E3.0.27.1", {"start": v(1066.8, 50.8) * mm, "end": v(1066.8, 76.2) * mm});
            skLineSegment(sketch, "E3.3.27.1", {"start": v(1041.4, 76.2) * mm, "end": v(1066.8, 76.2) * mm});
            skLineSegment(sketch, "E3.6.27.1", {"start": v(1041.4, 50.8) * mm, "end": v(1066.8, 50.8) * mm});
            skLineSegment(sketch, "E3.9.27.1", {"start": v(1041.4, 50.8) * mm, "end": v(1041.4, 76.2) * mm});
            skLineSegment(sketch, "E3.0.27.2", {"start": v(1066.8, 88.9) * mm, "end": v(1066.8, 114.3) * mm});
            skLineSegment(sketch, "E3.3.27.2", {"start": v(1041.4, 114.3) * mm, "end": v(1066.8, 114.3) * mm});
            skLineSegment(sketch, "E3.6.27.2", {"start": v(1041.4, 88.9) * mm, "end": v(1066.8, 88.9) * mm});
            skLineSegment(sketch, "E3.9.27.2", {"start": v(1041.4, 88.9) * mm, "end": v(1041.4, 114.3) * mm});
            skLineSegment(sketch, "E3.0.27.3", {"start": v(1066.8, 127) * mm, "end": v(1066.8, 152.4) * mm});
            skLineSegment(sketch, "E3.3.27.3", {"start": v(1041.4, 152.4) * mm, "end": v(1066.8, 152.4) * mm});
            skLineSegment(sketch, "E3.6.27.3", {"start": v(1041.4, 127) * mm, "end": v(1066.8, 127) * mm});
            skLineSegment(sketch, "E3.9.27.3", {"start": v(1041.4, 127) * mm, "end": v(1041.4, 152.4) * mm});
            skLineSegment(sketch, "E3.0.27.4", {"start": v(1066.8, 165.1) * mm, "end": v(1066.8, 190.5) * mm});
            skLineSegment(sketch, "E3.3.27.4", {"start": v(1041.4, 190.5) * mm, "end": v(1066.8, 190.5) * mm});
            skLineSegment(sketch, "E3.6.27.4", {"start": v(1041.4, 165.1) * mm, "end": v(1066.8, 165.1) * mm});
            skLineSegment(sketch, "E3.9.27.4", {"start": v(1041.4, 165.1) * mm, "end": v(1041.4, 190.5) * mm});
            skLineSegment(sketch, "E3.0.27.5", {"start": v(1066.8, 203.2) * mm, "end": v(1066.8, 228.6) * mm});
            skLineSegment(sketch, "E3.3.27.5", {"start": v(1041.4, 228.6) * mm, "end": v(1066.8, 228.6) * mm});
            skLineSegment(sketch, "E3.6.27.5", {"start": v(1041.4, 203.2) * mm, "end": v(1066.8, 203.2) * mm});
            skLineSegment(sketch, "E3.9.27.5", {"start": v(1041.4, 203.2) * mm, "end": v(1041.4, 228.6) * mm});
            skLineSegment(sketch, "E3.0.27.6", {"start": v(1066.8, 241.3) * mm, "end": v(1066.8, 266.7) * mm});
            skLineSegment(sketch, "E3.3.27.6", {"start": v(1041.4, 266.7) * mm, "end": v(1066.8, 266.7) * mm});
            skLineSegment(sketch, "E3.6.27.6", {"start": v(1041.4, 241.3) * mm, "end": v(1066.8, 241.3) * mm});
            skLineSegment(sketch, "E3.9.27.6", {"start": v(1041.4, 241.3) * mm, "end": v(1041.4, 266.7) * mm});
            skLineSegment(sketch, "E3.0.27.7", {"start": v(1066.8, 279.4) * mm, "end": v(1066.8, 304.8) * mm});
            skLineSegment(sketch, "E3.3.27.7", {"start": v(1041.4, 304.8) * mm, "end": v(1066.8, 304.8) * mm});
            skLineSegment(sketch, "E3.6.27.7", {"start": v(1041.4, 279.4) * mm, "end": v(1066.8, 279.4) * mm});
            skLineSegment(sketch, "E3.9.27.7", {"start": v(1041.4, 279.4) * mm, "end": v(1041.4, 304.8) * mm});
            skLineSegment(sketch, "E3.0.27.8", {"start": v(1066.8, 317.5) * mm, "end": v(1066.8, 342.9) * mm});
            skLineSegment(sketch, "E3.3.27.8", {"start": v(1041.4, 342.9) * mm, "end": v(1066.8, 342.9) * mm});
            skLineSegment(sketch, "E3.6.27.8", {"start": v(1041.4, 317.5) * mm, "end": v(1066.8, 317.5) * mm});
            skLineSegment(sketch, "E3.9.27.8", {"start": v(1041.4, 317.5) * mm, "end": v(1041.4, 342.9) * mm});
            skLineSegment(sketch, "E3.0.27.9", {"start": v(1066.8, 355.6) * mm, "end": v(1066.8, 381) * mm});
            skLineSegment(sketch, "E3.3.27.9", {"start": v(1041.4, 381) * mm, "end": v(1066.8, 381) * mm});
            skLineSegment(sketch, "E3.6.27.9", {"start": v(1041.4, 355.6) * mm, "end": v(1066.8, 355.6) * mm});
            skLineSegment(sketch, "E3.9.27.9", {"start": v(1041.4, 355.6) * mm, "end": v(1041.4, 381) * mm});
            skLineSegment(sketch, "E3.0.27.10", {"start": v(1066.8, 393.7) * mm, "end": v(1066.8, 419.1) * mm});
            skLineSegment(sketch, "E3.3.27.10", {"start": v(1041.4, 419.1) * mm, "end": v(1066.8, 419.1) * mm});
            skLineSegment(sketch, "E3.6.27.10", {"start": v(1041.4, 393.7) * mm, "end": v(1066.8, 393.7) * mm});
            skLineSegment(sketch, "E3.9.27.10", {"start": v(1041.4, 393.7) * mm, "end": v(1041.4, 419.1) * mm});
            skLineSegment(sketch, "E3.0.27.11", {"start": v(1066.8, 431.8) * mm, "end": v(1066.8, 457.2) * mm});
            skLineSegment(sketch, "E3.3.27.11", {"start": v(1041.4, 457.2) * mm, "end": v(1066.8, 457.2) * mm});
            skLineSegment(sketch, "E3.6.27.11", {"start": v(1041.4, 431.8) * mm, "end": v(1066.8, 431.8) * mm});
            skLineSegment(sketch, "E3.9.27.11", {"start": v(1041.4, 431.8) * mm, "end": v(1041.4, 457.2) * mm});
            skLineSegment(sketch, "E3.0.27.12", {"start": v(1066.8, 469.9) * mm, "end": v(1066.8, 495.3) * mm});
            skLineSegment(sketch, "E3.3.27.12", {"start": v(1041.4, 495.3) * mm, "end": v(1066.8, 495.3) * mm});
            skLineSegment(sketch, "E3.6.27.12", {"start": v(1041.4, 469.9) * mm, "end": v(1066.8, 469.9) * mm});
            skLineSegment(sketch, "E3.9.27.12", {"start": v(1041.4, 469.9) * mm, "end": v(1041.4, 495.3) * mm});
            skLineSegment(sketch, "E3.0.27.13", {"start": v(1066.8, 508) * mm, "end": v(1066.8, 533.4) * mm});
            skLineSegment(sketch, "E3.3.27.13", {"start": v(1041.4, 533.4) * mm, "end": v(1066.8, 533.4) * mm});
            skLineSegment(sketch, "E3.6.27.13", {"start": v(1041.4, 508) * mm, "end": v(1066.8, 508) * mm});
            skLineSegment(sketch, "E3.9.27.13", {"start": v(1041.4, 508) * mm, "end": v(1041.4, 533.4) * mm});
            skLineSegment(sketch, "E3.0.27.14", {"start": v(1066.8, 546.1) * mm, "end": v(1066.8, 571.5) * mm});
            skLineSegment(sketch, "E3.3.27.14", {"start": v(1041.4, 571.5) * mm, "end": v(1066.8, 571.5) * mm});
            skLineSegment(sketch, "E3.6.27.14", {"start": v(1041.4, 546.1) * mm, "end": v(1066.8, 546.1) * mm});
            skLineSegment(sketch, "E3.9.27.14", {"start": v(1041.4, 546.1) * mm, "end": v(1041.4, 571.5) * mm});
            skLineSegment(sketch, "E3.0.27.15", {"start": v(1066.8, 584.2) * mm, "end": v(1066.8, 609.6) * mm});
            skLineSegment(sketch, "E3.3.27.15", {"start": v(1041.4, 609.6) * mm, "end": v(1066.8, 609.6) * mm});
            skLineSegment(sketch, "E3.6.27.15", {"start": v(1041.4, 584.2) * mm, "end": v(1066.8, 584.2) * mm});
            skLineSegment(sketch, "E3.9.27.15", {"start": v(1041.4, 584.2) * mm, "end": v(1041.4, 609.6) * mm});
            skLineSegment(sketch, "E3.0.27.16", {"start": v(1066.8, 622.3) * mm, "end": v(1066.8, 647.7) * mm});
            skLineSegment(sketch, "E3.3.27.16", {"start": v(1041.4, 647.7) * mm, "end": v(1066.8, 647.7) * mm});
            skLineSegment(sketch, "E3.6.27.16", {"start": v(1041.4, 622.3) * mm, "end": v(1066.8, 622.3) * mm});
            skLineSegment(sketch, "E3.9.27.16", {"start": v(1041.4, 622.3) * mm, "end": v(1041.4, 647.7) * mm});
            skLineSegment(sketch, "E3.0.27.17", {"start": v(1066.8, 660.4) * mm, "end": v(1066.8, 685.8) * mm});
            skLineSegment(sketch, "E3.3.27.17", {"start": v(1041.4, 685.8) * mm, "end": v(1066.8, 685.8) * mm});
            skLineSegment(sketch, "E3.6.27.17", {"start": v(1041.4, 660.4) * mm, "end": v(1066.8, 660.4) * mm});
            skLineSegment(sketch, "E3.9.27.17", {"start": v(1041.4, 660.4) * mm, "end": v(1041.4, 685.8) * mm});
            skLineSegment(sketch, "E3.0.27.18", {"start": v(1066.8, 698.5) * mm, "end": v(1066.8, 723.9) * mm});
            skLineSegment(sketch, "E3.3.27.18", {"start": v(1041.4, 723.9) * mm, "end": v(1066.8, 723.9) * mm});
            skLineSegment(sketch, "E3.6.27.18", {"start": v(1041.4, 698.5) * mm, "end": v(1066.8, 698.5) * mm});
            skLineSegment(sketch, "E3.9.27.18", {"start": v(1041.4, 698.5) * mm, "end": v(1041.4, 723.9) * mm});
            skLineSegment(sketch, "E3.0.27.19", {"start": v(1066.8, 736.6) * mm, "end": v(1066.8, 762) * mm});
            skLineSegment(sketch, "E3.3.27.19", {"start": v(1041.4, 762) * mm, "end": v(1066.8, 762) * mm});
            skLineSegment(sketch, "E3.6.27.19", {"start": v(1041.4, 736.6) * mm, "end": v(1066.8, 736.6) * mm});
            skLineSegment(sketch, "E3.9.27.19", {"start": v(1041.4, 736.6) * mm, "end": v(1041.4, 762) * mm});
            skLineSegment(sketch, "E3.0.28.0", {"start": v(1104.9, 12.7) * mm, "end": v(1104.9, 38.1) * mm});
            skLineSegment(sketch, "E3.3.28.0", {"start": v(1079.5, 38.1) * mm, "end": v(1104.9, 38.1) * mm});
            skLineSegment(sketch, "E3.6.28.0", {"start": v(1079.5, 12.7) * mm, "end": v(1104.9, 12.7) * mm});
            skLineSegment(sketch, "E3.9.28.0", {"start": v(1079.5, 12.7) * mm, "end": v(1079.5, 38.1) * mm});
            skLineSegment(sketch, "E3.0.28.1", {"start": v(1104.9, 50.8) * mm, "end": v(1104.9, 76.2) * mm});
            skLineSegment(sketch, "E3.3.28.1", {"start": v(1079.5, 76.2) * mm, "end": v(1104.9, 76.2) * mm});
            skLineSegment(sketch, "E3.6.28.1", {"start": v(1079.5, 50.8) * mm, "end": v(1104.9, 50.8) * mm});
            skLineSegment(sketch, "E3.9.28.1", {"start": v(1079.5, 50.8) * mm, "end": v(1079.5, 76.2) * mm});
            skLineSegment(sketch, "E3.0.28.2", {"start": v(1104.9, 88.9) * mm, "end": v(1104.9, 114.3) * mm});
            skLineSegment(sketch, "E3.3.28.2", {"start": v(1079.5, 114.3) * mm, "end": v(1104.9, 114.3) * mm});
            skLineSegment(sketch, "E3.6.28.2", {"start": v(1079.5, 88.9) * mm, "end": v(1104.9, 88.9) * mm});
            skLineSegment(sketch, "E3.9.28.2", {"start": v(1079.5, 88.9) * mm, "end": v(1079.5, 114.3) * mm});
            skLineSegment(sketch, "E3.0.28.3", {"start": v(1104.9, 127) * mm, "end": v(1104.9, 152.4) * mm});
            skLineSegment(sketch, "E3.3.28.3", {"start": v(1079.5, 152.4) * mm, "end": v(1104.9, 152.4) * mm});
            skLineSegment(sketch, "E3.6.28.3", {"start": v(1079.5, 127) * mm, "end": v(1104.9, 127) * mm});
            skLineSegment(sketch, "E3.9.28.3", {"start": v(1079.5, 127) * mm, "end": v(1079.5, 152.4) * mm});
            skLineSegment(sketch, "E3.0.28.4", {"start": v(1104.9, 165.1) * mm, "end": v(1104.9, 190.5) * mm});
            skLineSegment(sketch, "E3.3.28.4", {"start": v(1079.5, 190.5) * mm, "end": v(1104.9, 190.5) * mm});
            skLineSegment(sketch, "E3.6.28.4", {"start": v(1079.5, 165.1) * mm, "end": v(1104.9, 165.1) * mm});
            skLineSegment(sketch, "E3.9.28.4", {"start": v(1079.5, 165.1) * mm, "end": v(1079.5, 190.5) * mm});
            skLineSegment(sketch, "E3.0.28.5", {"start": v(1104.9, 203.2) * mm, "end": v(1104.9, 228.6) * mm});
            skLineSegment(sketch, "E3.3.28.5", {"start": v(1079.5, 228.6) * mm, "end": v(1104.9, 228.6) * mm});
            skLineSegment(sketch, "E3.6.28.5", {"start": v(1079.5, 203.2) * mm, "end": v(1104.9, 203.2) * mm});
            skLineSegment(sketch, "E3.9.28.5", {"start": v(1079.5, 203.2) * mm, "end": v(1079.5, 228.6) * mm});
            skLineSegment(sketch, "E3.0.28.6", {"start": v(1104.9, 241.3) * mm, "end": v(1104.9, 266.7) * mm});
            skLineSegment(sketch, "E3.3.28.6", {"start": v(1079.5, 266.7) * mm, "end": v(1104.9, 266.7) * mm});
            skLineSegment(sketch, "E3.6.28.6", {"start": v(1079.5, 241.3) * mm, "end": v(1104.9, 241.3) * mm});
            skLineSegment(sketch, "E3.9.28.6", {"start": v(1079.5, 241.3) * mm, "end": v(1079.5, 266.7) * mm});
            skLineSegment(sketch, "E3.0.28.7", {"start": v(1104.9, 279.4) * mm, "end": v(1104.9, 304.8) * mm});
            skLineSegment(sketch, "E3.3.28.7", {"start": v(1079.5, 304.8) * mm, "end": v(1104.9, 304.8) * mm});
            skLineSegment(sketch, "E3.6.28.7", {"start": v(1079.5, 279.4) * mm, "end": v(1104.9, 279.4) * mm});
            skLineSegment(sketch, "E3.9.28.7", {"start": v(1079.5, 279.4) * mm, "end": v(1079.5, 304.8) * mm});
            skLineSegment(sketch, "E3.0.28.8", {"start": v(1104.9, 317.5) * mm, "end": v(1104.9, 342.9) * mm});
            skLineSegment(sketch, "E3.3.28.8", {"start": v(1079.5, 342.9) * mm, "end": v(1104.9, 342.9) * mm});
            skLineSegment(sketch, "E3.6.28.8", {"start": v(1079.5, 317.5) * mm, "end": v(1104.9, 317.5) * mm});
            skLineSegment(sketch, "E3.9.28.8", {"start": v(1079.5, 317.5) * mm, "end": v(1079.5, 342.9) * mm});
            skLineSegment(sketch, "E3.0.28.9", {"start": v(1104.9, 355.6) * mm, "end": v(1104.9, 381) * mm});
            skLineSegment(sketch, "E3.3.28.9", {"start": v(1079.5, 381) * mm, "end": v(1104.9, 381) * mm});
            skLineSegment(sketch, "E3.6.28.9", {"start": v(1079.5, 355.6) * mm, "end": v(1104.9, 355.6) * mm});
            skLineSegment(sketch, "E3.9.28.9", {"start": v(1079.5, 355.6) * mm, "end": v(1079.5, 381) * mm});
            skLineSegment(sketch, "E3.0.28.10", {"start": v(1104.9, 393.7) * mm, "end": v(1104.9, 419.1) * mm});
            skLineSegment(sketch, "E3.3.28.10", {"start": v(1079.5, 419.1) * mm, "end": v(1104.9, 419.1) * mm});
            skLineSegment(sketch, "E3.6.28.10", {"start": v(1079.5, 393.7) * mm, "end": v(1104.9, 393.7) * mm});
            skLineSegment(sketch, "E3.9.28.10", {"start": v(1079.5, 393.7) * mm, "end": v(1079.5, 419.1) * mm});
            skLineSegment(sketch, "E3.0.28.11", {"start": v(1104.9, 431.8) * mm, "end": v(1104.9, 457.2) * mm});
            skLineSegment(sketch, "E3.3.28.11", {"start": v(1079.5, 457.2) * mm, "end": v(1104.9, 457.2) * mm});
            skLineSegment(sketch, "E3.6.28.11", {"start": v(1079.5, 431.8) * mm, "end": v(1104.9, 431.8) * mm});
            skLineSegment(sketch, "E3.9.28.11", {"start": v(1079.5, 431.8) * mm, "end": v(1079.5, 457.2) * mm});
            skLineSegment(sketch, "E3.0.28.12", {"start": v(1104.9, 469.9) * mm, "end": v(1104.9, 495.3) * mm});
            skLineSegment(sketch, "E3.3.28.12", {"start": v(1079.5, 495.3) * mm, "end": v(1104.9, 495.3) * mm});
            skLineSegment(sketch, "E3.6.28.12", {"start": v(1079.5, 469.9) * mm, "end": v(1104.9, 469.9) * mm});
            skLineSegment(sketch, "E3.9.28.12", {"start": v(1079.5, 469.9) * mm, "end": v(1079.5, 495.3) * mm});
            skLineSegment(sketch, "E3.0.28.13", {"start": v(1104.9, 508) * mm, "end": v(1104.9, 533.4) * mm});
            skLineSegment(sketch, "E3.3.28.13", {"start": v(1079.5, 533.4) * mm, "end": v(1104.9, 533.4) * mm});
            skLineSegment(sketch, "E3.6.28.13", {"start": v(1079.5, 508) * mm, "end": v(1104.9, 508) * mm});
            skLineSegment(sketch, "E3.9.28.13", {"start": v(1079.5, 508) * mm, "end": v(1079.5, 533.4) * mm});
            skLineSegment(sketch, "E3.0.28.14", {"start": v(1104.9, 546.1) * mm, "end": v(1104.9, 571.5) * mm});
            skLineSegment(sketch, "E3.3.28.14", {"start": v(1079.5, 571.5) * mm, "end": v(1104.9, 571.5) * mm});
            skLineSegment(sketch, "E3.6.28.14", {"start": v(1079.5, 546.1) * mm, "end": v(1104.9, 546.1) * mm});
            skLineSegment(sketch, "E3.9.28.14", {"start": v(1079.5, 546.1) * mm, "end": v(1079.5, 571.5) * mm});
            skLineSegment(sketch, "E3.0.28.15", {"start": v(1104.9, 584.2) * mm, "end": v(1104.9, 609.6) * mm});
            skLineSegment(sketch, "E3.3.28.15", {"start": v(1079.5, 609.6) * mm, "end": v(1104.9, 609.6) * mm});
            skLineSegment(sketch, "E3.6.28.15", {"start": v(1079.5, 584.2) * mm, "end": v(1104.9, 584.2) * mm});
            skLineSegment(sketch, "E3.9.28.15", {"start": v(1079.5, 584.2) * mm, "end": v(1079.5, 609.6) * mm});
            skLineSegment(sketch, "E3.0.28.16", {"start": v(1104.9, 622.3) * mm, "end": v(1104.9, 647.7) * mm});
            skLineSegment(sketch, "E3.3.28.16", {"start": v(1079.5, 647.7) * mm, "end": v(1104.9, 647.7) * mm});
            skLineSegment(sketch, "E3.6.28.16", {"start": v(1079.5, 622.3) * mm, "end": v(1104.9, 622.3) * mm});
            skLineSegment(sketch, "E3.9.28.16", {"start": v(1079.5, 622.3) * mm, "end": v(1079.5, 647.7) * mm});
            skLineSegment(sketch, "E3.0.28.17", {"start": v(1104.9, 660.4) * mm, "end": v(1104.9, 685.8) * mm});
            skLineSegment(sketch, "E3.3.28.17", {"start": v(1079.5, 685.8) * mm, "end": v(1104.9, 685.8) * mm});
            skLineSegment(sketch, "E3.6.28.17", {"start": v(1079.5, 660.4) * mm, "end": v(1104.9, 660.4) * mm});
            skLineSegment(sketch, "E3.9.28.17", {"start": v(1079.5, 660.4) * mm, "end": v(1079.5, 685.8) * mm});
            skLineSegment(sketch, "E3.0.28.18", {"start": v(1104.9, 698.5) * mm, "end": v(1104.9, 723.9) * mm});
            skLineSegment(sketch, "E3.3.28.18", {"start": v(1079.5, 723.9) * mm, "end": v(1104.9, 723.9) * mm});
            skLineSegment(sketch, "E3.6.28.18", {"start": v(1079.5, 698.5) * mm, "end": v(1104.9, 698.5) * mm});
            skLineSegment(sketch, "E3.9.28.18", {"start": v(1079.5, 698.5) * mm, "end": v(1079.5, 723.9) * mm});
            skLineSegment(sketch, "E3.0.28.19", {"start": v(1104.9, 736.6) * mm, "end": v(1104.9, 762) * mm});
            skLineSegment(sketch, "E3.3.28.19", {"start": v(1079.5, 762) * mm, "end": v(1104.9, 762) * mm});
            skLineSegment(sketch, "E3.6.28.19", {"start": v(1079.5, 736.6) * mm, "end": v(1104.9, 736.6) * mm});
            skLineSegment(sketch, "E3.9.28.19", {"start": v(1079.5, 736.6) * mm, "end": v(1079.5, 762) * mm});
            skLineSegment(sketch, "E3.0.29.0", {"start": v(1143, 12.7) * mm, "end": v(1143, 38.1) * mm});
            skLineSegment(sketch, "E3.3.29.0", {"start": v(1117.6, 38.1) * mm, "end": v(1143, 38.1) * mm});
            skLineSegment(sketch, "E3.6.29.0", {"start": v(1117.6, 12.7) * mm, "end": v(1143, 12.7) * mm});
            skLineSegment(sketch, "E3.9.29.0", {"start": v(1117.6, 12.7) * mm, "end": v(1117.6, 38.1) * mm});
            skLineSegment(sketch, "E3.0.29.1", {"start": v(1143, 50.8) * mm, "end": v(1143, 76.2) * mm});
            skLineSegment(sketch, "E3.3.29.1", {"start": v(1117.6, 76.2) * mm, "end": v(1143, 76.2) * mm});
            skLineSegment(sketch, "E3.6.29.1", {"start": v(1117.6, 50.8) * mm, "end": v(1143, 50.8) * mm});
            skLineSegment(sketch, "E3.9.29.1", {"start": v(1117.6, 50.8) * mm, "end": v(1117.6, 76.2) * mm});
            skLineSegment(sketch, "E3.0.29.2", {"start": v(1143, 88.9) * mm, "end": v(1143, 114.3) * mm});
            skLineSegment(sketch, "E3.3.29.2", {"start": v(1117.6, 114.3) * mm, "end": v(1143, 114.3) * mm});
            skLineSegment(sketch, "E3.6.29.2", {"start": v(1117.6, 88.9) * mm, "end": v(1143, 88.9) * mm});
            skLineSegment(sketch, "E3.9.29.2", {"start": v(1117.6, 88.9) * mm, "end": v(1117.6, 114.3) * mm});
            skLineSegment(sketch, "E3.0.29.3", {"start": v(1143, 127) * mm, "end": v(1143, 152.4) * mm});
            skLineSegment(sketch, "E3.3.29.3", {"start": v(1117.6, 152.4) * mm, "end": v(1143, 152.4) * mm});
            skLineSegment(sketch, "E3.6.29.3", {"start": v(1117.6, 127) * mm, "end": v(1143, 127) * mm});
            skLineSegment(sketch, "E3.9.29.3", {"start": v(1117.6, 127) * mm, "end": v(1117.6, 152.4) * mm});
            skLineSegment(sketch, "E3.0.29.4", {"start": v(1143, 165.1) * mm, "end": v(1143, 190.5) * mm});
            skLineSegment(sketch, "E3.3.29.4", {"start": v(1117.6, 190.5) * mm, "end": v(1143, 190.5) * mm});
            skLineSegment(sketch, "E3.6.29.4", {"start": v(1117.6, 165.1) * mm, "end": v(1143, 165.1) * mm});
            skLineSegment(sketch, "E3.9.29.4", {"start": v(1117.6, 165.1) * mm, "end": v(1117.6, 190.5) * mm});
            skLineSegment(sketch, "E3.0.29.5", {"start": v(1143, 203.2) * mm, "end": v(1143, 228.6) * mm});
            skLineSegment(sketch, "E3.3.29.5", {"start": v(1117.6, 228.6) * mm, "end": v(1143, 228.6) * mm});
            skLineSegment(sketch, "E3.6.29.5", {"start": v(1117.6, 203.2) * mm, "end": v(1143, 203.2) * mm});
            skLineSegment(sketch, "E3.9.29.5", {"start": v(1117.6, 203.2) * mm, "end": v(1117.6, 228.6) * mm});
            skLineSegment(sketch, "E3.0.29.6", {"start": v(1143, 241.3) * mm, "end": v(1143, 266.7) * mm});
            skLineSegment(sketch, "E3.3.29.6", {"start": v(1117.6, 266.7) * mm, "end": v(1143, 266.7) * mm});
            skLineSegment(sketch, "E3.6.29.6", {"start": v(1117.6, 241.3) * mm, "end": v(1143, 241.3) * mm});
            skLineSegment(sketch, "E3.9.29.6", {"start": v(1117.6, 241.3) * mm, "end": v(1117.6, 266.7) * mm});
            skLineSegment(sketch, "E3.0.29.7", {"start": v(1143, 279.4) * mm, "end": v(1143, 304.8) * mm});
            skLineSegment(sketch, "E3.3.29.7", {"start": v(1117.6, 304.8) * mm, "end": v(1143, 304.8) * mm});
            skLineSegment(sketch, "E3.6.29.7", {"start": v(1117.6, 279.4) * mm, "end": v(1143, 279.4) * mm});
            skLineSegment(sketch, "E3.9.29.7", {"start": v(1117.6, 279.4) * mm, "end": v(1117.6, 304.8) * mm});
            skLineSegment(sketch, "E3.0.29.8", {"start": v(1143, 317.5) * mm, "end": v(1143, 342.9) * mm});
            skLineSegment(sketch, "E3.3.29.8", {"start": v(1117.6, 342.9) * mm, "end": v(1143, 342.9) * mm});
            skLineSegment(sketch, "E3.6.29.8", {"start": v(1117.6, 317.5) * mm, "end": v(1143, 317.5) * mm});
            skLineSegment(sketch, "E3.9.29.8", {"start": v(1117.6, 317.5) * mm, "end": v(1117.6, 342.9) * mm});
            skLineSegment(sketch, "E3.0.29.9", {"start": v(1143, 355.6) * mm, "end": v(1143, 381) * mm});
            skLineSegment(sketch, "E3.3.29.9", {"start": v(1117.6, 381) * mm, "end": v(1143, 381) * mm});
            skLineSegment(sketch, "E3.6.29.9", {"start": v(1117.6, 355.6) * mm, "end": v(1143, 355.6) * mm});
            skLineSegment(sketch, "E3.9.29.9", {"start": v(1117.6, 355.6) * mm, "end": v(1117.6, 381) * mm});
            skLineSegment(sketch, "E3.0.29.10", {"start": v(1143, 393.7) * mm, "end": v(1143, 419.1) * mm});
            skLineSegment(sketch, "E3.3.29.10", {"start": v(1117.6, 419.1) * mm, "end": v(1143, 419.1) * mm});
            skLineSegment(sketch, "E3.6.29.10", {"start": v(1117.6, 393.7) * mm, "end": v(1143, 393.7) * mm});
            skLineSegment(sketch, "E3.9.29.10", {"start": v(1117.6, 393.7) * mm, "end": v(1117.6, 419.1) * mm});
            skLineSegment(sketch, "E3.0.29.11", {"start": v(1143, 431.8) * mm, "end": v(1143, 457.2) * mm});
            skLineSegment(sketch, "E3.3.29.11", {"start": v(1117.6, 457.2) * mm, "end": v(1143, 457.2) * mm});
            skLineSegment(sketch, "E3.6.29.11", {"start": v(1117.6, 431.8) * mm, "end": v(1143, 431.8) * mm});
            skLineSegment(sketch, "E3.9.29.11", {"start": v(1117.6, 431.8) * mm, "end": v(1117.6, 457.2) * mm});
            skLineSegment(sketch, "E3.0.29.12", {"start": v(1143, 469.9) * mm, "end": v(1143, 495.3) * mm});
            skLineSegment(sketch, "E3.3.29.12", {"start": v(1117.6, 495.3) * mm, "end": v(1143, 495.3) * mm});
            skLineSegment(sketch, "E3.6.29.12", {"start": v(1117.6, 469.9) * mm, "end": v(1143, 469.9) * mm});
            skLineSegment(sketch, "E3.9.29.12", {"start": v(1117.6, 469.9) * mm, "end": v(1117.6, 495.3) * mm});
            skLineSegment(sketch, "E3.0.29.13", {"start": v(1143, 508) * mm, "end": v(1143, 533.4) * mm});
            skLineSegment(sketch, "E3.3.29.13", {"start": v(1117.6, 533.4) * mm, "end": v(1143, 533.4) * mm});
            skLineSegment(sketch, "E3.6.29.13", {"start": v(1117.6, 508) * mm, "end": v(1143, 508) * mm});
            skLineSegment(sketch, "E3.9.29.13", {"start": v(1117.6, 508) * mm, "end": v(1117.6, 533.4) * mm});
            skLineSegment(sketch, "E3.0.29.14", {"start": v(1143, 546.1) * mm, "end": v(1143, 571.5) * mm});
            skLineSegment(sketch, "E3.3.29.14", {"start": v(1117.6, 571.5) * mm, "end": v(1143, 571.5) * mm});
            skLineSegment(sketch, "E3.6.29.14", {"start": v(1117.6, 546.1) * mm, "end": v(1143, 546.1) * mm});
            skLineSegment(sketch, "E3.9.29.14", {"start": v(1117.6, 546.1) * mm, "end": v(1117.6, 571.5) * mm});
            skLineSegment(sketch, "E3.0.29.15", {"start": v(1143, 584.2) * mm, "end": v(1143, 609.6) * mm});
            skLineSegment(sketch, "E3.3.29.15", {"start": v(1117.6, 609.6) * mm, "end": v(1143, 609.6) * mm});
            skLineSegment(sketch, "E3.6.29.15", {"start": v(1117.6, 584.2) * mm, "end": v(1143, 584.2) * mm});
            skLineSegment(sketch, "E3.9.29.15", {"start": v(1117.6, 584.2) * mm, "end": v(1117.6, 609.6) * mm});
            skLineSegment(sketch, "E3.0.29.16", {"start": v(1143, 622.3) * mm, "end": v(1143, 647.7) * mm});
            skLineSegment(sketch, "E3.3.29.16", {"start": v(1117.6, 647.7) * mm, "end": v(1143, 647.7) * mm});
            skLineSegment(sketch, "E3.6.29.16", {"start": v(1117.6, 622.3) * mm, "end": v(1143, 622.3) * mm});
            skLineSegment(sketch, "E3.9.29.16", {"start": v(1117.6, 622.3) * mm, "end": v(1117.6, 647.7) * mm});
            skLineSegment(sketch, "E3.0.29.17", {"start": v(1143, 660.4) * mm, "end": v(1143, 685.8) * mm});
            skLineSegment(sketch, "E3.3.29.17", {"start": v(1117.6, 685.8) * mm, "end": v(1143, 685.8) * mm});
            skLineSegment(sketch, "E3.6.29.17", {"start": v(1117.6, 660.4) * mm, "end": v(1143, 660.4) * mm});
            skLineSegment(sketch, "E3.9.29.17", {"start": v(1117.6, 660.4) * mm, "end": v(1117.6, 685.8) * mm});
            skLineSegment(sketch, "E3.0.29.18", {"start": v(1143, 698.5) * mm, "end": v(1143, 723.9) * mm});
            skLineSegment(sketch, "E3.3.29.18", {"start": v(1117.6, 723.9) * mm, "end": v(1143, 723.9) * mm});
            skLineSegment(sketch, "E3.6.29.18", {"start": v(1117.6, 698.5) * mm, "end": v(1143, 698.5) * mm});
            skLineSegment(sketch, "E3.9.29.18", {"start": v(1117.6, 698.5) * mm, "end": v(1117.6, 723.9) * mm});
            skLineSegment(sketch, "E3.0.29.19", {"start": v(1143, 736.6) * mm, "end": v(1143, 762) * mm});
            skLineSegment(sketch, "E3.3.29.19", {"start": v(1117.6, 762) * mm, "end": v(1143, 762) * mm});
            skLineSegment(sketch, "E3.6.29.19", {"start": v(1117.6, 736.6) * mm, "end": v(1143, 736.6) * mm});
            skLineSegment(sketch, "E3.9.29.19", {"start": v(1117.6, 736.6) * mm, "end": v(1117.6, 762) * mm});
            skSolve(sketch);
        }
        {
            var Q0;
            Q0 = qSketchRegion(id + "F2", true);
            extrude(context, id + "F3", {"entities" : qUnion([Q0]), "operationType" : NewBodyOperationType.ADD, "depth" : 25.4 * mm});
        }
        {
            var Q0;
            Q0=makeQuery(id+"F3.opExtrude","CAP_EDGE",EDGE,{"disambiguationData":[OSD([sQuery(id+"F2.wireOp",EDGE,"E1.bottom")])],"isStart":false});
            var Q1;
            Q1=makeQuery(id+"F3.opExtrude","CAP_EDGE",EDGE,{"disambiguationData":[OSD([sQuery(id+"F2.wireOp",EDGE,"E2.4.0.3")])],"isStart":false});
            var Q2;
            Q2=makeQuery(id+"F3.opExtrude","CAP_EDGE",EDGE,{"disambiguationData":[OSD([sQuery(id+"F2.wireOp",EDGE,"E2.16.0.3")])],"isStart":false});
            var Q3;
            Q3=makeQuery(id+"F3.opExtrude","CAP_EDGE",EDGE,{"disambiguationData":[OSD([sQuery(id+"F2.wireOp",EDGE,"E2.3.0.3")])],"isStart":false});
            var Q4;
            Q4=makeQuery(id+"F3.opExtrude","CAP_EDGE",EDGE,{"disambiguationData":[OSD([sQuery(id+"F2.wireOp",EDGE,"E1.right")])],"isStart":false});
            var Q5;
            Q5=makeQuery(id+"F3.opExtrude","CAP_EDGE",EDGE,{"disambiguationData":[OSD([sQuery(id+"F2.wireOp",EDGE,"E2.19.0.3")])],"isStart":false});
            var Q6;
            Q6=makeQuery(id+"F3.opExtrude","CAP_EDGE",EDGE,{"disambiguationData":[OSD([sQuery(id+"F2.wireOp",EDGE,"E2.13.0.3")])],"isStart":false});
            var Q7;
            Q7=makeQuery(id+"F3.opExtrude","CAP_EDGE",EDGE,{"disambiguationData":[OSD([sQuery(id+"F2.wireOp",EDGE,"E2.7.0.3")])],"isStart":false});
            var Q8;
            Q8=makeQuery(id+"F3.opExtrude","CAP_EDGE",EDGE,{"disambiguationData":[OSD([sQuery(id+"F2.wireOp",EDGE,"E3.9.26.0")])],"isStart":false});
            var Q9;
            Q9=makeQuery(id+"F3.opExtrude","CAP_EDGE",EDGE,{"disambiguationData":[OSD([sQuery(id+"F2.wireOp",EDGE,"E2.1.0.3")])],"isStart":false});
            var Q10;
            Q10=makeQuery(id+"F3.opExtrude","CAP_EDGE",EDGE,{"disambiguationData":[OSD([sQuery(id+"F2.wireOp",EDGE,"E3.9.20.0")])],"isStart":false});
            var Q11;
            Q11=makeQuery(id+"F3.opExtrude","CAP_EDGE",EDGE,{"disambiguationData":[OSD([sQuery(id+"F2.wireOp",EDGE,"E3.9.27.0")])],"isStart":false});
            var Q12;
            Q12=makeQuery(id+"F3.opExtrude","CAP_EDGE",EDGE,{"disambiguationData":[OSD([sQuery(id+"F2.wireOp",EDGE,"E2.8.0.3")])],"isStart":false});
            var Q13;
            Q13=makeQuery(id+"F3.opExtrude","CAP_EDGE",EDGE,{"disambiguationData":[OSD([sQuery(id+"F2.wireOp",EDGE,"E2.14.0.3")])],"isStart":false});
            var Q14;
            Q14=makeQuery(id+"F3.opExtrude","CAP_EDGE",EDGE,{"disambiguationData":[OSD([sQuery(id+"F2.wireOp",EDGE,"E2.2.0.3")])],"isStart":false});
            var Q15;
            Q15=makeQuery(id+"F3.opExtrude","CAP_EDGE",EDGE,{"disambiguationData":[OSD([sQuery(id+"F2.wireOp",EDGE,"E3.9.21.0")])],"isStart":false});
            var Q16;
            Q16=makeQuery(id+"F3.opExtrude","CAP_EDGE",EDGE,{"disambiguationData":[OSD([sQuery(id+"F2.wireOp",EDGE,"E3.9.28.0")])],"isStart":false});
            var Q17;
            Q17=makeQuery(id+"F3.opExtrude","CAP_EDGE",EDGE,{"disambiguationData":[OSD([sQuery(id+"F2.wireOp",EDGE,"E2.15.0.3")])],"isStart":false});
            var Q18;
            Q18=makeQuery(id+"F3.opExtrude","CAP_EDGE",EDGE,{"disambiguationData":[OSD([sQuery(id+"F2.wireOp",EDGE,"E2.10.0.3")])],"isStart":false});
            var Q19;
            Q19=makeQuery(id+"F3.opExtrude","CAP_EDGE",EDGE,{"disambiguationData":[OSD([sQuery(id+"F2.wireOp",EDGE,"E3.9.29.0")])],"isStart":false});
            var Q20;
            Q20=makeQuery(id+"F3.opExtrude","CAP_EDGE",EDGE,{"disambiguationData":[OSD([sQuery(id+"F2.wireOp",EDGE,"E3.9.23.0")])],"isStart":false});
            var Q21;
            Q21=makeQuery(id+"F3.opExtrude","CAP_EDGE",EDGE,{"disambiguationData":[OSD([sQuery(id+"F2.wireOp",EDGE,"E2.17.0.3")])],"isStart":false});
            var Q22;
            Q22=makeQuery(id+"F3.opExtrude","CAP_EDGE",EDGE,{"disambiguationData":[OSD([sQuery(id+"F2.wireOp",EDGE,"E3.9.24.0")])],"isStart":false});
            var Q23;
            Q23=makeQuery(id+"F3.opExtrude","CAP_EDGE",EDGE,{"disambiguationData":[OSD([sQuery(id+"F2.wireOp",EDGE,"E2.11.0.3")])],"isStart":false});
            var Q24;
            Q24=makeQuery(id+"F3.opExtrude","CAP_EDGE",EDGE,{"disambiguationData":[OSD([sQuery(id+"F2.wireOp",EDGE,"E2.18.0.3")])],"isStart":false});
            var Q25;
            Q25=makeQuery(id+"F3.opExtrude","CAP_EDGE",EDGE,{"disambiguationData":[OSD([sQuery(id+"F2.wireOp",EDGE,"E2.5.0.3")])],"isStart":false});
            var Q26;
            Q26=makeQuery(id+"F3.opExtrude","CAP_EDGE",EDGE,{"disambiguationData":[OSD([sQuery(id+"F2.wireOp",EDGE,"E2.12.0.3")])],"isStart":false});
            var Q27;
            Q27=makeQuery(id+"F3.opExtrude","CAP_EDGE",EDGE,{"disambiguationData":[OSD([sQuery(id+"F2.wireOp",EDGE,"E2.6.0.3")])],"isStart":false});
            var Q28;
            Q28=makeQuery(id+"F3.opExtrude","CAP_EDGE",EDGE,{"disambiguationData":[OSD([sQuery(id+"F2.wireOp",EDGE,"E3.9.25.0")])],"isStart":false});
            var Q29;
            Q29=makeQuery(id+"F3.opExtrude","CAP_EDGE",EDGE,{"disambiguationData":[OSD([sQuery(id+"F2.wireOp",EDGE,"E2.4.0.0")])],"isStart":false});
            var Q30;
            Q30=makeQuery(id+"F3.opExtrude","CAP_EDGE",EDGE,{"disambiguationData":[OSD([sQuery(id+"F2.wireOp",EDGE,"E2.3.0.0")])],"isStart":false});
            var Q31;
            Q31=makeQuery(id+"F3.opExtrude","CAP_EDGE",EDGE,{"disambiguationData":[OSD([sQuery(id+"F2.wireOp",EDGE,"E3.0.29.0")])],"isStart":false});
            var Q32;
            Q32=makeQuery(id+"F3.opExtrude","CAP_EDGE",EDGE,{"disambiguationData":[OSD([sQuery(id+"F2.wireOp",EDGE,"E2.16.0.0")])],"isStart":false});
            var Q33;
            Q33=makeQuery(id+"F3.opExtrude","CAP_EDGE",EDGE,{"disambiguationData":[OSD([sQuery(id+"F2.wireOp",EDGE,"E3.0.23.0")])],"isStart":false});
            var Q34;
            Q34=makeQuery(id+"F3.opExtrude","CAP_EDGE",EDGE,{"disambiguationData":[OSD([sQuery(id+"F2.wireOp",EDGE,"E2.10.0.0")])],"isStart":false});
            var Q35;
            Q35=makeQuery(id+"F3.opExtrude","CAP_EDGE",EDGE,{"disambiguationData":[OSD([sQuery(id+"F2.wireOp",EDGE,"E3.9.22.0")])],"isStart":false});
            var Q36;
            Q36=makeQuery(id+"F3.opExtrude","CAP_EDGE",EDGE,{"disambiguationData":[OSD([sQuery(id+"F2.wireOp",EDGE,"E2.9.0.3")])],"isStart":false});
            var Q37;
            Q37=makeQuery(id+"F3.opExtrude","CAP_EDGE",EDGE,{"disambiguationData":[OSD([sQuery(id+"F2.wireOp",EDGE,"E3.0.26.0")])],"isStart":false});
            var Q38;
            Q38=makeQuery(id+"F3.opExtrude","CAP_EDGE",EDGE,{"disambiguationData":[OSD([sQuery(id+"F2.wireOp",EDGE,"E3.0.20.0")])],"isStart":false});
            var Q39;
            Q39=makeQuery(id+"F3.opExtrude","CAP_EDGE",EDGE,{"disambiguationData":[OSD([sQuery(id+"F2.wireOp",EDGE,"E2.7.0.0")])],"isStart":false});
            var Q40;
            Q40=makeQuery(id+"F3.opExtrude","CAP_EDGE",EDGE,{"disambiguationData":[OSD([sQuery(id+"F2.wireOp",EDGE,"E2.14.0.0")])],"isStart":false});
            var Q41;
            Q41=makeQuery(id+"F3.opExtrude","CAP_EDGE",EDGE,{"disambiguationData":[OSD([sQuery(id+"F2.wireOp",EDGE,"E2.1.0.0")])],"isStart":false});
            var Q42;
            Q42=makeQuery(id+"F3.opExtrude","CAP_EDGE",EDGE,{"disambiguationData":[OSD([sQuery(id+"F2.wireOp",EDGE,"E2.8.0.0")])],"isStart":false});
            var Q43;
            Q43=makeQuery(id+"F3.opExtrude","CAP_EDGE",EDGE,{"disambiguationData":[OSD([sQuery(id+"F2.wireOp",EDGE,"E3.0.27.0")])],"isStart":false});
            var Q44;
            Q44=makeQuery(id+"F3.opExtrude","CAP_EDGE",EDGE,{"disambiguationData":[OSD([sQuery(id+"F2.wireOp",EDGE,"E2.2.0.0")])],"isStart":false});
            var Q45;
            Q45=makeQuery(id+"F3.opExtrude","CAP_EDGE",EDGE,{"disambiguationData":[OSD([sQuery(id+"F2.wireOp",EDGE,"E3.0.21.0")])],"isStart":false});
            var Q46;
            Q46=makeQuery(id+"F3.opExtrude","CAP_EDGE",EDGE,{"disambiguationData":[OSD([sQuery(id+"F2.wireOp",EDGE,"E3.0.28.0")])],"isStart":false});
            var Q47;
            Q47=makeQuery(id+"F3.opExtrude","CAP_EDGE",EDGE,{"disambiguationData":[OSD([sQuery(id+"F2.wireOp",EDGE,"E2.15.0.0")])],"isStart":false});
            var Q48;
            Q48=makeQuery(id+"F3.opExtrude","CAP_EDGE",EDGE,{"disambiguationData":[OSD([sQuery(id+"F2.wireOp",EDGE,"E3.0.22.0")])],"isStart":false});
            var Q49;
            Q49=makeQuery(id+"F3.opExtrude","CAP_EDGE",EDGE,{"disambiguationData":[OSD([sQuery(id+"F2.wireOp",EDGE,"E2.9.0.0")])],"isStart":false});
            var Q50;
            Q50=makeQuery(id+"F3.opExtrude","CAP_EDGE",EDGE,{"disambiguationData":[OSD([sQuery(id+"F2.wireOp",EDGE,"E2.17.0.0")])],"isStart":false});
            var Q51;
            Q51=makeQuery(id+"F3.opExtrude","CAP_EDGE",EDGE,{"disambiguationData":[OSD([sQuery(id+"F2.wireOp",EDGE,"E3.0.24.0")])],"isStart":false});
            var Q52;
            Q52=makeQuery(id+"F3.opExtrude","CAP_EDGE",EDGE,{"disambiguationData":[OSD([sQuery(id+"F2.wireOp",EDGE,"E2.11.0.0")])],"isStart":false});
            var Q53;
            Q53=makeQuery(id+"F3.opExtrude","CAP_EDGE",EDGE,{"disambiguationData":[OSD([sQuery(id+"F2.wireOp",EDGE,"E2.18.0.0")])],"isStart":false});
            var Q54;
            Q54=makeQuery(id+"F3.opExtrude","CAP_EDGE",EDGE,{"disambiguationData":[OSD([sQuery(id+"F2.wireOp",EDGE,"E2.5.0.0")])],"isStart":false});
            var Q55;
            Q55=makeQuery(id+"F3.opExtrude","CAP_EDGE",EDGE,{"disambiguationData":[OSD([sQuery(id+"F2.wireOp",EDGE,"E3.0.25.0")])],"isStart":false});
            var Q56;
            Q56=makeQuery(id+"F3.opExtrude","CAP_EDGE",EDGE,{"disambiguationData":[OSD([sQuery(id+"F2.wireOp",EDGE,"E2.12.0.0")])],"isStart":false});
            var Q57;
            Q57=makeQuery(id+"F3.opExtrude","CAP_EDGE",EDGE,{"disambiguationData":[OSD([sQuery(id+"F2.wireOp",EDGE,"E2.19.0.0")])],"isStart":false});
            var Q58;
            Q58=makeQuery(id+"F3.opExtrude","CAP_EDGE",EDGE,{"disambiguationData":[OSD([sQuery(id+"F2.wireOp",EDGE,"E2.6.0.0")])],"isStart":false});
            var Q59;
            Q59=makeQuery(id+"F3.opExtrude","CAP_EDGE",EDGE,{"disambiguationData":[OSD([sQuery(id+"F2.wireOp",EDGE,"E2.13.0.0")])],"isStart":false});
            var Q60;
            Q60=makeQuery(id+"F3.opExtrude","CAP_EDGE",EDGE,{"disambiguationData":[OSD([sQuery(id+"F2.wireOp",EDGE,"E1.top")])],"isStart":false});
            var Q61;
            Q61=makeQuery(id+"F3.opExtrude","CAP_EDGE",EDGE,{"disambiguationData":[OSD([sQuery(id+"F2.wireOp",EDGE,"E3.6.23.0")])],"isStart":false});
            var Q62;
            Q62=makeQuery(id+"F3.opExtrude","CAP_EDGE",EDGE,{"disambiguationData":[OSD([sQuery(id+"F2.wireOp",EDGE,"E2.17.0.2")])],"isStart":false});
            var Q63;
            Q63=makeQuery(id+"F3.opExtrude","CAP_EDGE",EDGE,{"disambiguationData":[OSD([sQuery(id+"F2.wireOp",EDGE,"E3.6.24.0")])],"isStart":false});
            var Q64;
            Q64=makeQuery(id+"F3.opExtrude","CAP_EDGE",EDGE,{"disambiguationData":[OSD([sQuery(id+"F2.wireOp",EDGE,"E2.11.0.2")])],"isStart":false});
            var Q65;
            Q65=makeQuery(id+"F3.opExtrude","CAP_EDGE",EDGE,{"disambiguationData":[OSD([sQuery(id+"F2.wireOp",EDGE,"E2.18.0.2")])],"isStart":false});
            var Q66;
            Q66=makeQuery(id+"F3.opExtrude","CAP_EDGE",EDGE,{"disambiguationData":[OSD([sQuery(id+"F2.wireOp",EDGE,"E2.5.0.2")])],"isStart":false});
            var Q67;
            Q67=makeQuery(id+"F3.opExtrude","CAP_EDGE",EDGE,{"disambiguationData":[OSD([sQuery(id+"F2.wireOp",EDGE,"E2.12.0.2")])],"isStart":false});
            var Q68;
            Q68=makeQuery(id+"F3.opExtrude","CAP_EDGE",EDGE,{"disambiguationData":[OSD([sQuery(id+"F2.wireOp",EDGE,"E2.6.0.2")])],"isStart":false});
            var Q69;
            Q69=makeQuery(id+"F3.opExtrude","CAP_EDGE",EDGE,{"disambiguationData":[OSD([sQuery(id+"F2.wireOp",EDGE,"E3.6.25.0")])],"isStart":false});
            var Q70;
            Q70=makeQuery(id+"F3.opExtrude","CAP_EDGE",EDGE,{"disambiguationData":[OSD([sQuery(id+"F2.wireOp",EDGE,"E1.left")])],"isStart":false});
            var Q71;
            Q71=makeQuery(id+"F3.opExtrude","CAP_EDGE",EDGE,{"disambiguationData":[OSD([sQuery(id+"F2.wireOp",EDGE,"E2.19.0.2")])],"isStart":false});
            var Q72;
            Q72=makeQuery(id+"F3.opExtrude","CAP_EDGE",EDGE,{"disambiguationData":[OSD([sQuery(id+"F2.wireOp",EDGE,"E2.4.0.2")])],"isStart":false});
            var Q73;
            Q73=makeQuery(id+"F3.opExtrude","CAP_EDGE",EDGE,{"disambiguationData":[OSD([sQuery(id+"F2.wireOp",EDGE,"E2.16.0.2")])],"isStart":false});
            var Q74;
            Q74=makeQuery(id+"F3.opExtrude","CAP_EDGE",EDGE,{"disambiguationData":[OSD([sQuery(id+"F2.wireOp",EDGE,"E2.3.0.2")])],"isStart":false});
            var Q75;
            Q75=makeQuery(id+"F3.opExtrude","CAP_EDGE",EDGE,{"disambiguationData":[OSD([sQuery(id+"F2.wireOp",EDGE,"E2.10.0.2")])],"isStart":false});
            var Q76;
            Q76=makeQuery(id+"F3.opExtrude","CAP_EDGE",EDGE,{"disambiguationData":[OSD([sQuery(id+"F2.wireOp",EDGE,"E3.6.29.0")])],"isStart":false});
            var Q77;
            Q77=makeQuery(id+"F3.opExtrude","CAP_EDGE",EDGE,{"disambiguationData":[OSD([sQuery(id+"F2.wireOp",EDGE,"E2.13.0.2")])],"isStart":false});
            var Q78;
            Q78=makeQuery(id+"F3.opExtrude","CAP_EDGE",EDGE,{"disambiguationData":[OSD([sQuery(id+"F2.wireOp",EDGE,"E3.6.26.0")])],"isStart":false});
            var Q79;
            Q79=makeQuery(id+"F3.opExtrude","CAP_EDGE",EDGE,{"disambiguationData":[OSD([sQuery(id+"F2.wireOp",EDGE,"E3.6.20.0")])],"isStart":false});
            var Q80;
            Q80=makeQuery(id+"F3.opExtrude","CAP_EDGE",EDGE,{"disambiguationData":[OSD([sQuery(id+"F2.wireOp",EDGE,"E2.7.0.2")])],"isStart":false});
            var Q81;
            Q81=makeQuery(id+"F3.opExtrude","CAP_EDGE",EDGE,{"disambiguationData":[OSD([sQuery(id+"F2.wireOp",EDGE,"E2.14.0.2")])],"isStart":false});
            var Q82;
            Q82=makeQuery(id+"F3.opExtrude","CAP_EDGE",EDGE,{"disambiguationData":[OSD([sQuery(id+"F2.wireOp",EDGE,"E2.1.0.2")])],"isStart":false});
            var Q83;
            Q83=makeQuery(id+"F3.opExtrude","CAP_EDGE",EDGE,{"disambiguationData":[OSD([sQuery(id+"F2.wireOp",EDGE,"E2.8.0.2")])],"isStart":false});
            var Q84;
            Q84=makeQuery(id+"F3.opExtrude","CAP_EDGE",EDGE,{"disambiguationData":[OSD([sQuery(id+"F2.wireOp",EDGE,"E3.6.27.0")])],"isStart":false});
            var Q85;
            Q85=makeQuery(id+"F3.opExtrude","CAP_EDGE",EDGE,{"disambiguationData":[OSD([sQuery(id+"F2.wireOp",EDGE,"E2.2.0.2")])],"isStart":false});
            var Q86;
            Q86=makeQuery(id+"F3.opExtrude","CAP_EDGE",EDGE,{"disambiguationData":[OSD([sQuery(id+"F2.wireOp",EDGE,"E3.6.21.0")])],"isStart":false});
            var Q87;
            Q87=makeQuery(id+"F3.opExtrude","CAP_EDGE",EDGE,{"disambiguationData":[OSD([sQuery(id+"F2.wireOp",EDGE,"E3.6.28.0")])],"isStart":false});
            var Q88;
            Q88=makeQuery(id+"F3.opExtrude","CAP_EDGE",EDGE,{"disambiguationData":[OSD([sQuery(id+"F2.wireOp",EDGE,"E2.15.0.2")])],"isStart":false});
            var Q89;
            Q89=makeQuery(id+"F3.opExtrude","CAP_EDGE",EDGE,{"disambiguationData":[OSD([sQuery(id+"F2.wireOp",EDGE,"E3.6.22.0")])],"isStart":false});
            var Q90;
            Q90=makeQuery(id+"F3.opExtrude","CAP_EDGE",EDGE,{"disambiguationData":[OSD([sQuery(id+"F2.wireOp",EDGE,"E2.9.0.2")])],"isStart":false});
            var Q91;
            Q91=makeQuery(id+"F3.opExtrude","CAP_EDGE",EDGE,{"disambiguationData":[OSD([sQuery(id+"F2.wireOp",EDGE,"E2.4.0.1")])],"isStart":false});
            var Q92;
            Q92=makeQuery(id+"F3.opExtrude","CAP_EDGE",EDGE,{"disambiguationData":[OSD([sQuery(id+"F2.wireOp",EDGE,"E2.16.0.1")])],"isStart":false});
            var Q93;
            Q93=makeQuery(id+"F3.opExtrude","CAP_EDGE",EDGE,{"disambiguationData":[OSD([sQuery(id+"F2.wireOp",EDGE,"E2.3.0.1")])],"isStart":false});
            var Q94;
            Q94=makeQuery(id+"F3.opExtrude","CAP_EDGE",EDGE,{"disambiguationData":[OSD([sQuery(id+"F2.wireOp",EDGE,"E3.3.23.0")])],"isStart":false});
            var Q95;
            Q95=makeQuery(id+"F3.opExtrude","CAP_EDGE",EDGE,{"disambiguationData":[OSD([sQuery(id+"F2.wireOp",EDGE,"E3.3.29.0")])],"isStart":false});
            var Q96;
            Q96=makeQuery(id+"F3.opExtrude","CAP_EDGE",EDGE,{"disambiguationData":[OSD([sQuery(id+"F2.wireOp",EDGE,"E2.10.0.1")])],"isStart":false});
            var Q97;
            Q97=makeQuery(id+"F3.opExtrude","CAP_EDGE",EDGE,{"disambiguationData":[OSD([sQuery(id+"F2.wireOp",EDGE,"E2.17.0.1")])],"isStart":false});
            var Q98;
            Q98=makeQuery(id+"F3.opExtrude","CAP_EDGE",EDGE,{"disambiguationData":[OSD([sQuery(id+"F2.wireOp",EDGE,"E3.3.24.0")])],"isStart":false});
            var Q99;
            Q99=makeQuery(id+"F3.opExtrude","CAP_EDGE",EDGE,{"disambiguationData":[OSD([sQuery(id+"F2.wireOp",EDGE,"E2.11.0.1")])],"isStart":false});
            var Q100;
            Q100=makeQuery(id+"F3.opExtrude","CAP_EDGE",EDGE,{"disambiguationData":[OSD([sQuery(id+"F2.wireOp",EDGE,"E2.8.0.1")])],"isStart":false});
            var Q101;
            Q101=makeQuery(id+"F3.opExtrude","CAP_EDGE",EDGE,{"disambiguationData":[OSD([sQuery(id+"F2.wireOp",EDGE,"E3.3.27.0")])],"isStart":false});
            var Q102;
            Q102=makeQuery(id+"F3.opExtrude","CAP_EDGE",EDGE,{"disambiguationData":[OSD([sQuery(id+"F2.wireOp",EDGE,"E2.2.0.1")])],"isStart":false});
            var Q103;
            Q103=makeQuery(id+"F3.opExtrude","CAP_EDGE",EDGE,{"disambiguationData":[OSD([sQuery(id+"F2.wireOp",EDGE,"E3.3.21.0")])],"isStart":false});
            var Q104;
            Q104=makeQuery(id+"F3.opExtrude","CAP_EDGE",EDGE,{"disambiguationData":[OSD([sQuery(id+"F2.wireOp",EDGE,"E3.3.28.0")])],"isStart":false});
            var Q105;
            Q105=makeQuery(id+"F3.opExtrude","CAP_EDGE",EDGE,{"disambiguationData":[OSD([sQuery(id+"F2.wireOp",EDGE,"E2.15.0.1")])],"isStart":false});
            var Q106;
            Q106=makeQuery(id+"F3.opExtrude","CAP_EDGE",EDGE,{"disambiguationData":[OSD([sQuery(id+"F2.wireOp",EDGE,"E3.3.22.0")])],"isStart":false});
            var Q107;
            Q107=makeQuery(id+"F3.opExtrude","CAP_EDGE",EDGE,{"disambiguationData":[OSD([sQuery(id+"F2.wireOp",EDGE,"E2.9.0.1")])],"isStart":false});
            var Q108;
            Q108=makeQuery(id+"F3.opExtrude","CAP_EDGE",EDGE,{"disambiguationData":[OSD([sQuery(id+"F2.wireOp",EDGE,"E2.18.0.1")])],"isStart":false});
            var Q109;
            Q109=makeQuery(id+"F3.opExtrude","CAP_EDGE",EDGE,{"disambiguationData":[OSD([sQuery(id+"F2.wireOp",EDGE,"E2.5.0.1")])],"isStart":false});
            var Q110;
            Q110=makeQuery(id+"F3.opExtrude","CAP_EDGE",EDGE,{"disambiguationData":[OSD([sQuery(id+"F2.wireOp",EDGE,"E2.12.0.1")])],"isStart":false});
            var Q111;
            Q111=makeQuery(id+"F3.opExtrude","CAP_EDGE",EDGE,{"disambiguationData":[OSD([sQuery(id+"F2.wireOp",EDGE,"E2.6.0.1")])],"isStart":false});
            var Q112;
            Q112=makeQuery(id+"F3.opExtrude","CAP_EDGE",EDGE,{"disambiguationData":[OSD([sQuery(id+"F2.wireOp",EDGE,"E3.3.25.0")])],"isStart":false});
            var Q113;
            Q113=makeQuery(id+"F3.opExtrude","CAP_EDGE",EDGE,{"disambiguationData":[OSD([sQuery(id+"F2.wireOp",EDGE,"E2.13.0.1")])],"isStart":false});
            var Q114;
            Q114=makeQuery(id+"F3.opExtrude","CAP_EDGE",EDGE,{"disambiguationData":[OSD([sQuery(id+"F2.wireOp",EDGE,"E2.19.0.1")])],"isStart":false});
            var Q115;
            Q115=makeQuery(id+"F3.opExtrude","CAP_EDGE",EDGE,{"disambiguationData":[OSD([sQuery(id+"F2.wireOp",EDGE,"E3.3.26.0")])],"isStart":false});
            var Q116;
            Q116=makeQuery(id+"F3.opExtrude","CAP_EDGE",EDGE,{"disambiguationData":[OSD([sQuery(id+"F2.wireOp",EDGE,"E3.3.20.0")])],"isStart":false});
            var Q117;
            Q117=makeQuery(id+"F3.opExtrude","CAP_EDGE",EDGE,{"disambiguationData":[OSD([sQuery(id+"F2.wireOp",EDGE,"E2.7.0.1")])],"isStart":false});
            var Q118;
            Q118=makeQuery(id+"F3.opExtrude","CAP_EDGE",EDGE,{"disambiguationData":[OSD([sQuery(id+"F2.wireOp",EDGE,"E2.14.0.1")])],"isStart":false});
            var Q119;
            Q119=makeQuery(id+"F3.opExtrude","CAP_EDGE",EDGE,{"disambiguationData":[OSD([sQuery(id+"F2.wireOp",EDGE,"E2.1.0.1")])],"isStart":false});
            var Q120;
            Q120=makeQuery(id+"F3.opExtrude","CAP_EDGE",EDGE,{"disambiguationData":[OSD([sQuery(id+"F2.wireOp",EDGE,"E2.0.1.0")])],"isStart":false});
            var Q121;
            Q121=makeQuery(id+"F3.opExtrude","CAP_EDGE",EDGE,{"disambiguationData":[OSD([sQuery(id+"F2.wireOp",EDGE,"E2.0.1.2")])],"isStart":false});
            var Q122;
            Q122=makeQuery(id+"F3.opExtrude","CAP_EDGE",EDGE,{"disambiguationData":[OSD([sQuery(id+"F2.wireOp",EDGE,"E2.4.1.0")])],"isStart":false});
            var Q123;
            Q123=makeQuery(id+"F3.opExtrude","CAP_EDGE",EDGE,{"disambiguationData":[OSD([sQuery(id+"F2.wireOp",EDGE,"E2.16.1.0")])],"isStart":false});
            var Q124;
            Q124=makeQuery(id+"F3.opExtrude","CAP_EDGE",EDGE,{"disambiguationData":[OSD([sQuery(id+"F2.wireOp",EDGE,"E2.3.1.0")])],"isStart":false});
            var Q125;
            Q125=makeQuery(id+"F3.opExtrude","CAP_EDGE",EDGE,{"disambiguationData":[OSD([sQuery(id+"F2.wireOp",EDGE,"E2.10.1.0")])],"isStart":false});
            var Q126;
            Q126=makeQuery(id+"F3.opExtrude","CAP_EDGE",EDGE,{"disambiguationData":[OSD([sQuery(id+"F2.wireOp",EDGE,"E3.0.29.1")])],"isStart":false});
            var Q127;
            Q127=makeQuery(id+"F3.opExtrude","CAP_EDGE",EDGE,{"disambiguationData":[OSD([sQuery(id+"F2.wireOp",EDGE,"E3.0.23.1")])],"isStart":false});
            var Q128;
            Q128=makeQuery(id+"F3.opExtrude","CAP_EDGE",EDGE,{"disambiguationData":[OSD([sQuery(id+"F2.wireOp",EDGE,"E2.17.1.0")])],"isStart":false});
            var Q129;
            Q129=makeQuery(id+"F3.opExtrude","CAP_EDGE",EDGE,{"disambiguationData":[OSD([sQuery(id+"F2.wireOp",EDGE,"E2.1.1.0")])],"isStart":false});
            var Q130;
            Q130=makeQuery(id+"F3.opExtrude","CAP_EDGE",EDGE,{"disambiguationData":[OSD([sQuery(id+"F2.wireOp",EDGE,"E3.0.20.1")])],"isStart":false});
            var Q131;
            Q131=makeQuery(id+"F3.opExtrude","CAP_EDGE",EDGE,{"disambiguationData":[OSD([sQuery(id+"F2.wireOp",EDGE,"E3.0.27.1")])],"isStart":false});
            var Q132;
            Q132=makeQuery(id+"F3.opExtrude","CAP_EDGE",EDGE,{"disambiguationData":[OSD([sQuery(id+"F2.wireOp",EDGE,"E2.14.1.0")])],"isStart":false});
            var Q133;
            Q133=makeQuery(id+"F3.opExtrude","CAP_EDGE",EDGE,{"disambiguationData":[OSD([sQuery(id+"F2.wireOp",EDGE,"E3.0.21.1")])],"isStart":false});
            var Q134;
            Q134=makeQuery(id+"F3.opExtrude","CAP_EDGE",EDGE,{"disambiguationData":[OSD([sQuery(id+"F2.wireOp",EDGE,"E2.2.1.0")])],"isStart":false});
            var Q135;
            Q135=makeQuery(id+"F3.opExtrude","CAP_EDGE",EDGE,{"disambiguationData":[OSD([sQuery(id+"F2.wireOp",EDGE,"E2.8.1.0")])],"isStart":false});
            var Q136;
            Q136=makeQuery(id+"F3.opExtrude","CAP_EDGE",EDGE,{"disambiguationData":[OSD([sQuery(id+"F2.wireOp",EDGE,"E3.0.28.1")])],"isStart":false});
            var Q137;
            Q137=makeQuery(id+"F3.opExtrude","CAP_EDGE",EDGE,{"disambiguationData":[OSD([sQuery(id+"F2.wireOp",EDGE,"E2.15.1.0")])],"isStart":false});
            var Q138;
            Q138=makeQuery(id+"F3.opExtrude","CAP_EDGE",EDGE,{"disambiguationData":[OSD([sQuery(id+"F2.wireOp",EDGE,"E3.0.22.1")])],"isStart":false});
            var Q139;
            Q139=makeQuery(id+"F3.opExtrude","CAP_EDGE",EDGE,{"disambiguationData":[OSD([sQuery(id+"F2.wireOp",EDGE,"E2.9.1.0")])],"isStart":false});
            var Q140;
            Q140=makeQuery(id+"F3.opExtrude","CAP_EDGE",EDGE,{"disambiguationData":[OSD([sQuery(id+"F2.wireOp",EDGE,"E3.0.24.1")])],"isStart":false});
            var Q141;
            Q141=makeQuery(id+"F3.opExtrude","CAP_EDGE",EDGE,{"disambiguationData":[OSD([sQuery(id+"F2.wireOp",EDGE,"E2.11.1.0")])],"isStart":false});
            var Q142;
            Q142=makeQuery(id+"F3.opExtrude","CAP_EDGE",EDGE,{"disambiguationData":[OSD([sQuery(id+"F2.wireOp",EDGE,"E2.18.1.0")])],"isStart":false});
            var Q143;
            Q143=makeQuery(id+"F3.opExtrude","CAP_EDGE",EDGE,{"disambiguationData":[OSD([sQuery(id+"F2.wireOp",EDGE,"E2.5.1.0")])],"isStart":false});
            var Q144;
            Q144=makeQuery(id+"F3.opExtrude","CAP_EDGE",EDGE,{"disambiguationData":[OSD([sQuery(id+"F2.wireOp",EDGE,"E2.12.1.0")])],"isStart":false});
            var Q145;
            Q145=makeQuery(id+"F3.opExtrude","CAP_EDGE",EDGE,{"disambiguationData":[OSD([sQuery(id+"F2.wireOp",EDGE,"E2.6.1.0")])],"isStart":false});
            var Q146;
            Q146=makeQuery(id+"F3.opExtrude","CAP_EDGE",EDGE,{"disambiguationData":[OSD([sQuery(id+"F2.wireOp",EDGE,"E3.0.25.1")])],"isStart":false});
            var Q147;
            Q147=makeQuery(id+"F3.opExtrude","CAP_EDGE",EDGE,{"disambiguationData":[OSD([sQuery(id+"F2.wireOp",EDGE,"E2.19.1.0")])],"isStart":false});
            var Q148;
            Q148=makeQuery(id+"F3.opExtrude","CAP_EDGE",EDGE,{"disambiguationData":[OSD([sQuery(id+"F2.wireOp",EDGE,"E2.13.1.0")])],"isStart":false});
            var Q149;
            Q149=makeQuery(id+"F3.opExtrude","CAP_EDGE",EDGE,{"disambiguationData":[OSD([sQuery(id+"F2.wireOp",EDGE,"E2.7.1.0")])],"isStart":false});
            var Q150;
            Q150=makeQuery(id+"F3.opExtrude","CAP_EDGE",EDGE,{"disambiguationData":[OSD([sQuery(id+"F2.wireOp",EDGE,"E3.0.26.1")])],"isStart":false});
            var Q151;
            Q151=makeQuery(id+"F3.opExtrude","CAP_EDGE",EDGE,{"disambiguationData":[OSD([sQuery(id+"F2.wireOp",EDGE,"E2.4.1.2")])],"isStart":false});
            var Q152;
            Q152=makeQuery(id+"F3.opExtrude","CAP_EDGE",EDGE,{"disambiguationData":[OSD([sQuery(id+"F2.wireOp",EDGE,"E2.6.1.2")])],"isStart":false});
            var Q153;
            Q153=makeQuery(id+"F3.opExtrude","CAP_EDGE",EDGE,{"disambiguationData":[OSD([sQuery(id+"F2.wireOp",EDGE,"E3.6.25.1")])],"isStart":false});
            var Q154;
            Q154=makeQuery(id+"F3.opExtrude","CAP_EDGE",EDGE,{"disambiguationData":[OSD([sQuery(id+"F2.wireOp",EDGE,"E2.19.1.2")])],"isStart":false});
            var Q155;
            Q155=makeQuery(id+"F3.opExtrude","CAP_EDGE",EDGE,{"disambiguationData":[OSD([sQuery(id+"F2.wireOp",EDGE,"E2.13.1.2")])],"isStart":false});
            var Q156;
            Q156=makeQuery(id+"F3.opExtrude","CAP_EDGE",EDGE,{"disambiguationData":[OSD([sQuery(id+"F2.wireOp",EDGE,"E2.7.1.2")])],"isStart":false});
            var Q157;
            Q157=makeQuery(id+"F3.opExtrude","CAP_EDGE",EDGE,{"disambiguationData":[OSD([sQuery(id+"F2.wireOp",EDGE,"E3.6.26.1")])],"isStart":false});
            var Q158;
            Q158=makeQuery(id+"F3.opExtrude","CAP_EDGE",EDGE,{"disambiguationData":[OSD([sQuery(id+"F2.wireOp",EDGE,"E2.1.1.2")])],"isStart":false});
            var Q159;
            Q159=makeQuery(id+"F3.opExtrude","CAP_EDGE",EDGE,{"disambiguationData":[OSD([sQuery(id+"F2.wireOp",EDGE,"E3.6.20.1")])],"isStart":false});
            var Q160;
            Q160=makeQuery(id+"F3.opExtrude","CAP_EDGE",EDGE,{"disambiguationData":[OSD([sQuery(id+"F2.wireOp",EDGE,"E3.6.27.1")])],"isStart":false});
            var Q161;
            Q161=makeQuery(id+"F3.opExtrude","CAP_EDGE",EDGE,{"disambiguationData":[OSD([sQuery(id+"F2.wireOp",EDGE,"E2.14.1.2")])],"isStart":false});
            var Q162;
            Q162=makeQuery(id+"F3.opExtrude","CAP_EDGE",EDGE,{"disambiguationData":[OSD([sQuery(id+"F2.wireOp",EDGE,"E3.6.21.1")])],"isStart":false});
            var Q163;
            Q163=makeQuery(id+"F3.opExtrude","CAP_EDGE",EDGE,{"disambiguationData":[OSD([sQuery(id+"F2.wireOp",EDGE,"E2.8.1.2")])],"isStart":false});
            var Q164;
            Q164=makeQuery(id+"F3.opExtrude","CAP_EDGE",EDGE,{"disambiguationData":[OSD([sQuery(id+"F2.wireOp",EDGE,"E2.0.1.1")])],"isStart":false});
            var Q165;
            Q165=makeQuery(id+"F3.opExtrude","CAP_EDGE",EDGE,{"disambiguationData":[OSD([sQuery(id+"F2.wireOp",EDGE,"E2.16.1.2")])],"isStart":false});
            var Q166;
            Q166=makeQuery(id+"F3.opExtrude","CAP_EDGE",EDGE,{"disambiguationData":[OSD([sQuery(id+"F2.wireOp",EDGE,"E2.3.1.2")])],"isStart":false});
            var Q167;
            Q167=makeQuery(id+"F3.opExtrude","CAP_EDGE",EDGE,{"disambiguationData":[OSD([sQuery(id+"F2.wireOp",EDGE,"E2.10.1.2")])],"isStart":false});
            var Q168;
            Q168=makeQuery(id+"F3.opExtrude","CAP_EDGE",EDGE,{"disambiguationData":[OSD([sQuery(id+"F2.wireOp",EDGE,"E3.6.29.1")])],"isStart":false});
            var Q169;
            Q169=makeQuery(id+"F3.opExtrude","CAP_EDGE",EDGE,{"disambiguationData":[OSD([sQuery(id+"F2.wireOp",EDGE,"E3.6.23.1")])],"isStart":false});
            var Q170;
            Q170=makeQuery(id+"F3.opExtrude","CAP_EDGE",EDGE,{"disambiguationData":[OSD([sQuery(id+"F2.wireOp",EDGE,"E2.17.1.2")])],"isStart":false});
            var Q171;
            Q171=makeQuery(id+"F3.opExtrude","CAP_EDGE",EDGE,{"disambiguationData":[OSD([sQuery(id+"F2.wireOp",EDGE,"E3.6.24.1")])],"isStart":false});
            var Q172;
            Q172=makeQuery(id+"F3.opExtrude","CAP_EDGE",EDGE,{"disambiguationData":[OSD([sQuery(id+"F2.wireOp",EDGE,"E2.11.1.2")])],"isStart":false});
            var Q173;
            Q173=makeQuery(id+"F3.opExtrude","CAP_EDGE",EDGE,{"disambiguationData":[OSD([sQuery(id+"F2.wireOp",EDGE,"E2.18.1.2")])],"isStart":false});
            var Q174;
            Q174=makeQuery(id+"F3.opExtrude","CAP_EDGE",EDGE,{"disambiguationData":[OSD([sQuery(id+"F2.wireOp",EDGE,"E2.5.1.2")])],"isStart":false});
            var Q175;
            Q175=makeQuery(id+"F3.opExtrude","CAP_EDGE",EDGE,{"disambiguationData":[OSD([sQuery(id+"F2.wireOp",EDGE,"E2.12.1.2")])],"isStart":false});
            var Q176;
            Q176=makeQuery(id+"F3.opExtrude","CAP_EDGE",EDGE,{"disambiguationData":[OSD([sQuery(id+"F2.wireOp",EDGE,"E2.15.1.2")])],"isStart":false});
            var Q177;
            Q177=makeQuery(id+"F3.opExtrude","CAP_EDGE",EDGE,{"disambiguationData":[OSD([sQuery(id+"F2.wireOp",EDGE,"E2.2.1.2")])],"isStart":false});
            var Q178;
            Q178=makeQuery(id+"F3.opExtrude","CAP_EDGE",EDGE,{"disambiguationData":[OSD([sQuery(id+"F2.wireOp",EDGE,"E3.6.22.1")])],"isStart":false});
            var Q179;
            Q179=makeQuery(id+"F3.opExtrude","CAP_EDGE",EDGE,{"disambiguationData":[OSD([sQuery(id+"F2.wireOp",EDGE,"E3.6.28.1")])],"isStart":false});
            var Q180;
            Q180=makeQuery(id+"F3.opExtrude","CAP_EDGE",EDGE,{"disambiguationData":[OSD([sQuery(id+"F2.wireOp",EDGE,"E2.9.1.2")])],"isStart":false});
            var Q181;
            Q181=makeQuery(id+"F3.opExtrude","CAP_EDGE",EDGE,{"disambiguationData":[OSD([sQuery(id+"F2.wireOp",EDGE,"E2.0.1.3")])],"isStart":false});
            var Q182;
            Q182=makeQuery(id+"F3.opExtrude","CAP_EDGE",EDGE,{"disambiguationData":[OSD([sQuery(id+"F2.wireOp",EDGE,"E2.10.1.1")])],"isStart":false});
            var Q183;
            Q183=makeQuery(id+"F3.opExtrude","CAP_EDGE",EDGE,{"disambiguationData":[OSD([sQuery(id+"F2.wireOp",EDGE,"E3.3.29.1")])],"isStart":false});
            var Q184;
            Q184=makeQuery(id+"F3.opExtrude","CAP_EDGE",EDGE,{"disambiguationData":[OSD([sQuery(id+"F2.wireOp",EDGE,"E3.3.23.1")])],"isStart":false});
            var Q185;
            Q185=makeQuery(id+"F3.opExtrude","CAP_EDGE",EDGE,{"disambiguationData":[OSD([sQuery(id+"F2.wireOp",EDGE,"E2.17.1.1")])],"isStart":false});
            var Q186;
            Q186=makeQuery(id+"F3.opExtrude","CAP_EDGE",EDGE,{"disambiguationData":[OSD([sQuery(id+"F2.wireOp",EDGE,"E3.3.24.1")])],"isStart":false});
            var Q187;
            Q187=makeQuery(id+"F3.opExtrude","CAP_EDGE",EDGE,{"disambiguationData":[OSD([sQuery(id+"F2.wireOp",EDGE,"E2.11.1.1")])],"isStart":false});
            var Q188;
            Q188=makeQuery(id+"F3.opExtrude","CAP_EDGE",EDGE,{"disambiguationData":[OSD([sQuery(id+"F2.wireOp",EDGE,"E2.18.1.1")])],"isStart":false});
            var Q189;
            Q189=makeQuery(id+"F3.opExtrude","CAP_EDGE",EDGE,{"disambiguationData":[OSD([sQuery(id+"F2.wireOp",EDGE,"E2.5.1.1")])],"isStart":false});
            var Q190;
            Q190=makeQuery(id+"F3.opExtrude","CAP_EDGE",EDGE,{"disambiguationData":[OSD([sQuery(id+"F2.wireOp",EDGE,"E2.12.1.1")])],"isStart":false});
            var Q191;
            Q191=makeQuery(id+"F3.opExtrude","CAP_EDGE",EDGE,{"disambiguationData":[OSD([sQuery(id+"F2.wireOp",EDGE,"E2.6.1.1")])],"isStart":false});
            var Q192;
            Q192=makeQuery(id+"F3.opExtrude","CAP_EDGE",EDGE,{"disambiguationData":[OSD([sQuery(id+"F2.wireOp",EDGE,"E3.3.25.1")])],"isStart":false});
            var Q193;
            Q193=makeQuery(id+"F3.opExtrude","CAP_EDGE",EDGE,{"disambiguationData":[OSD([sQuery(id+"F2.wireOp",EDGE,"E2.4.1.1")])],"isStart":false});
            var Q194;
            Q194=makeQuery(id+"F3.opExtrude","CAP_EDGE",EDGE,{"disambiguationData":[OSD([sQuery(id+"F2.wireOp",EDGE,"E2.16.1.1")])],"isStart":false});
            var Q195;
            Q195=makeQuery(id+"F3.opExtrude","CAP_EDGE",EDGE,{"disambiguationData":[OSD([sQuery(id+"F2.wireOp",EDGE,"E2.3.1.1")])],"isStart":false});
            var Q196;
            Q196=makeQuery(id+"F3.opExtrude","CAP_EDGE",EDGE,{"disambiguationData":[OSD([sQuery(id+"F2.wireOp",EDGE,"E2.9.1.1")])],"isStart":false});
            var Q197;
            Q197=makeQuery(id+"F3.opExtrude","CAP_EDGE",EDGE,{"disambiguationData":[OSD([sQuery(id+"F2.wireOp",EDGE,"E3.3.28.1")])],"isStart":false});
            var Q198;
            Q198=makeQuery(id+"F3.opExtrude","CAP_EDGE",EDGE,{"disambiguationData":[OSD([sQuery(id+"F2.wireOp",EDGE,"E3.3.22.1")])],"isStart":false});
            var Q199;
            Q199=makeQuery(id+"F3.opExtrude","CAP_EDGE",EDGE,{"disambiguationData":[OSD([sQuery(id+"F2.wireOp",EDGE,"E2.19.1.1")])],"isStart":false});
            var Q200;
            Q200=makeQuery(id+"F3.opExtrude","CAP_EDGE",EDGE,{"disambiguationData":[OSD([sQuery(id+"F2.wireOp",EDGE,"E2.13.1.1")])],"isStart":false});
            var Q201;
            Q201=makeQuery(id+"F3.opExtrude","CAP_EDGE",EDGE,{"disambiguationData":[OSD([sQuery(id+"F2.wireOp",EDGE,"E2.7.1.1")])],"isStart":false});
            var Q202;
            Q202=makeQuery(id+"F3.opExtrude","CAP_EDGE",EDGE,{"disambiguationData":[OSD([sQuery(id+"F2.wireOp",EDGE,"E3.3.26.1")])],"isStart":false});
            var Q203;
            Q203=makeQuery(id+"F3.opExtrude","CAP_EDGE",EDGE,{"disambiguationData":[OSD([sQuery(id+"F2.wireOp",EDGE,"E2.1.1.1")])],"isStart":false});
            var Q204;
            Q204=makeQuery(id+"F3.opExtrude","CAP_EDGE",EDGE,{"disambiguationData":[OSD([sQuery(id+"F2.wireOp",EDGE,"E3.3.20.1")])],"isStart":false});
            var Q205;
            Q205=makeQuery(id+"F3.opExtrude","CAP_EDGE",EDGE,{"disambiguationData":[OSD([sQuery(id+"F2.wireOp",EDGE,"E3.3.27.1")])],"isStart":false});
            var Q206;
            Q206=makeQuery(id+"F3.opExtrude","CAP_EDGE",EDGE,{"disambiguationData":[OSD([sQuery(id+"F2.wireOp",EDGE,"E2.14.1.1")])],"isStart":false});
            var Q207;
            Q207=makeQuery(id+"F3.opExtrude","CAP_EDGE",EDGE,{"disambiguationData":[OSD([sQuery(id+"F2.wireOp",EDGE,"E3.3.21.1")])],"isStart":false});
            var Q208;
            Q208=makeQuery(id+"F3.opExtrude","CAP_EDGE",EDGE,{"disambiguationData":[OSD([sQuery(id+"F2.wireOp",EDGE,"E2.8.1.1")])],"isStart":false});
            var Q209;
            Q209=makeQuery(id+"F3.opExtrude","CAP_EDGE",EDGE,{"disambiguationData":[OSD([sQuery(id+"F2.wireOp",EDGE,"E2.15.1.1")])],"isStart":false});
            var Q210;
            Q210=makeQuery(id+"F3.opExtrude","CAP_EDGE",EDGE,{"disambiguationData":[OSD([sQuery(id+"F2.wireOp",EDGE,"E2.2.1.1")])],"isStart":false});
            var Q211;
            Q211=makeQuery(id+"F3.opExtrude","CAP_EDGE",EDGE,{"disambiguationData":[OSD([sQuery(id+"F2.wireOp",EDGE,"E2.4.1.3")])],"isStart":false});
            var Q212;
            Q212=makeQuery(id+"F3.opExtrude","CAP_EDGE",EDGE,{"disambiguationData":[OSD([sQuery(id+"F2.wireOp",EDGE,"E2.16.1.3")])],"isStart":false});
            var Q213;
            Q213=makeQuery(id+"F3.opExtrude","CAP_EDGE",EDGE,{"disambiguationData":[OSD([sQuery(id+"F2.wireOp",EDGE,"E2.3.1.3")])],"isStart":false});
            var Q214;
            Q214=makeQuery(id+"F3.opExtrude","CAP_EDGE",EDGE,{"disambiguationData":[OSD([sQuery(id+"F2.wireOp",EDGE,"E2.10.1.3")])],"isStart":false});
            var Q215;
            Q215=makeQuery(id+"F3.opExtrude","CAP_EDGE",EDGE,{"disambiguationData":[OSD([sQuery(id+"F2.wireOp",EDGE,"E3.9.29.1")])],"isStart":false});
            var Q216;
            Q216=makeQuery(id+"F3.opExtrude","CAP_EDGE",EDGE,{"disambiguationData":[OSD([sQuery(id+"F2.wireOp",EDGE,"E3.9.23.1")])],"isStart":false});
            var Q217;
            Q217=makeQuery(id+"F3.opExtrude","CAP_EDGE",EDGE,{"disambiguationData":[OSD([sQuery(id+"F2.wireOp",EDGE,"E2.7.1.3")])],"isStart":false});
            var Q218;
            Q218=makeQuery(id+"F3.opExtrude","CAP_EDGE",EDGE,{"disambiguationData":[OSD([sQuery(id+"F2.wireOp",EDGE,"E3.9.26.1")])],"isStart":false});
            var Q219;
            Q219=makeQuery(id+"F3.opExtrude","CAP_EDGE",EDGE,{"disambiguationData":[OSD([sQuery(id+"F2.wireOp",EDGE,"E2.1.1.3")])],"isStart":false});
            var Q220;
            Q220=makeQuery(id+"F3.opExtrude","CAP_EDGE",EDGE,{"disambiguationData":[OSD([sQuery(id+"F2.wireOp",EDGE,"E3.9.20.1")])],"isStart":false});
            var Q221;
            Q221=makeQuery(id+"F3.opExtrude","CAP_EDGE",EDGE,{"disambiguationData":[OSD([sQuery(id+"F2.wireOp",EDGE,"E3.9.27.1")])],"isStart":false});
            var Q222;
            Q222=makeQuery(id+"F3.opExtrude","CAP_EDGE",EDGE,{"disambiguationData":[OSD([sQuery(id+"F2.wireOp",EDGE,"E2.14.1.3")])],"isStart":false});
            var Q223;
            Q223=makeQuery(id+"F3.opExtrude","CAP_EDGE",EDGE,{"disambiguationData":[OSD([sQuery(id+"F2.wireOp",EDGE,"E3.9.21.1")])],"isStart":false});
            var Q224;
            Q224=makeQuery(id+"F3.opExtrude","CAP_EDGE",EDGE,{"disambiguationData":[OSD([sQuery(id+"F2.wireOp",EDGE,"E2.8.1.3")])],"isStart":false});
            var Q225;
            Q225=makeQuery(id+"F3.opExtrude","CAP_EDGE",EDGE,{"disambiguationData":[OSD([sQuery(id+"F2.wireOp",EDGE,"E2.15.1.3")])],"isStart":false});
            var Q226;
            Q226=makeQuery(id+"F3.opExtrude","CAP_EDGE",EDGE,{"disambiguationData":[OSD([sQuery(id+"F2.wireOp",EDGE,"E2.2.1.3")])],"isStart":false});
            var Q227;
            Q227=makeQuery(id+"F3.opExtrude","CAP_EDGE",EDGE,{"disambiguationData":[OSD([sQuery(id+"F2.wireOp",EDGE,"E2.9.1.3")])],"isStart":false});
            var Q228;
            Q228=makeQuery(id+"F3.opExtrude","CAP_EDGE",EDGE,{"disambiguationData":[OSD([sQuery(id+"F2.wireOp",EDGE,"E3.9.28.1")])],"isStart":false});
            var Q229;
            Q229=makeQuery(id+"F3.opExtrude","CAP_EDGE",EDGE,{"disambiguationData":[OSD([sQuery(id+"F2.wireOp",EDGE,"E3.9.22.1")])],"isStart":false});
            var Q230;
            Q230=makeQuery(id+"F3.opExtrude","CAP_EDGE",EDGE,{"disambiguationData":[OSD([sQuery(id+"F2.wireOp",EDGE,"E2.17.1.3")])],"isStart":false});
            var Q231;
            Q231=makeQuery(id+"F3.opExtrude","CAP_EDGE",EDGE,{"disambiguationData":[OSD([sQuery(id+"F2.wireOp",EDGE,"E3.9.24.1")])],"isStart":false});
            var Q232;
            Q232=makeQuery(id+"F3.opExtrude","CAP_EDGE",EDGE,{"disambiguationData":[OSD([sQuery(id+"F2.wireOp",EDGE,"E2.11.1.3")])],"isStart":false});
            var Q233;
            Q233=makeQuery(id+"F3.opExtrude","CAP_EDGE",EDGE,{"disambiguationData":[OSD([sQuery(id+"F2.wireOp",EDGE,"E2.18.1.3")])],"isStart":false});
            var Q234;
            Q234=makeQuery(id+"F3.opExtrude","CAP_EDGE",EDGE,{"disambiguationData":[OSD([sQuery(id+"F2.wireOp",EDGE,"E2.5.1.3")])],"isStart":false});
            var Q235;
            Q235=makeQuery(id+"F3.opExtrude","CAP_EDGE",EDGE,{"disambiguationData":[OSD([sQuery(id+"F2.wireOp",EDGE,"E2.12.1.3")])],"isStart":false});
            var Q236;
            Q236=makeQuery(id+"F3.opExtrude","CAP_EDGE",EDGE,{"disambiguationData":[OSD([sQuery(id+"F2.wireOp",EDGE,"E2.6.1.3")])],"isStart":false});
            var Q237;
            Q237=makeQuery(id+"F3.opExtrude","CAP_EDGE",EDGE,{"disambiguationData":[OSD([sQuery(id+"F2.wireOp",EDGE,"E3.9.25.1")])],"isStart":false});
            var Q238;
            Q238=makeQuery(id+"F3.opExtrude","CAP_EDGE",EDGE,{"disambiguationData":[OSD([sQuery(id+"F2.wireOp",EDGE,"E2.19.1.3")])],"isStart":false});
            var Q239;
            Q239=makeQuery(id+"F3.opExtrude","CAP_EDGE",EDGE,{"disambiguationData":[OSD([sQuery(id+"F2.wireOp",EDGE,"E2.13.1.3")])],"isStart":false});
            var Q240;
            Q240=makeQuery(id+"F3.opExtrude","CAP_EDGE",EDGE,{"disambiguationData":[OSD([sQuery(id+"F2.wireOp",EDGE,"E2.0.2.3")])],"isStart":false});
            var Q241;
            Q241=makeQuery(id+"F3.opExtrude","CAP_EDGE",EDGE,{"disambiguationData":[OSD([sQuery(id+"F2.wireOp",EDGE,"E2.0.2.0")])],"isStart":false});
            var Q242;
            Q242=makeQuery(id+"F3.opExtrude","CAP_EDGE",EDGE,{"disambiguationData":[OSD([sQuery(id+"F2.wireOp",EDGE,"E2.0.2.2")])],"isStart":false});
            var Q243;
            Q243=makeQuery(id+"F3.opExtrude","CAP_EDGE",EDGE,{"disambiguationData":[OSD([sQuery(id+"F2.wireOp",EDGE,"E2.4.2.3")])],"isStart":false});
            var Q244;
            Q244=makeQuery(id+"F3.opExtrude","CAP_EDGE",EDGE,{"disambiguationData":[OSD([sQuery(id+"F2.wireOp",EDGE,"E2.16.2.3")])],"isStart":false});
            var Q245;
            Q245=makeQuery(id+"F3.opExtrude","CAP_EDGE",EDGE,{"disambiguationData":[OSD([sQuery(id+"F2.wireOp",EDGE,"E2.3.2.3")])],"isStart":false});
            var Q246;
            Q246=makeQuery(id+"F3.opExtrude","CAP_EDGE",EDGE,{"disambiguationData":[OSD([sQuery(id+"F2.wireOp",EDGE,"E2.19.2.3")])],"isStart":false});
            var Q247;
            Q247=makeQuery(id+"F3.opExtrude","CAP_EDGE",EDGE,{"disambiguationData":[OSD([sQuery(id+"F2.wireOp",EDGE,"E2.13.2.3")])],"isStart":false});
            var Q248;
            Q248=makeQuery(id+"F3.opExtrude","CAP_EDGE",EDGE,{"disambiguationData":[OSD([sQuery(id+"F2.wireOp",EDGE,"E2.7.2.3")])],"isStart":false});
            var Q249;
            Q249=makeQuery(id+"F3.opExtrude","CAP_EDGE",EDGE,{"disambiguationData":[OSD([sQuery(id+"F2.wireOp",EDGE,"E3.9.26.2")])],"isStart":false});
            var Q250;
            Q250=makeQuery(id+"F3.opExtrude","CAP_EDGE",EDGE,{"disambiguationData":[OSD([sQuery(id+"F2.wireOp",EDGE,"E2.1.2.3")])],"isStart":false});
            var Q251;
            Q251=makeQuery(id+"F3.opExtrude","CAP_EDGE",EDGE,{"disambiguationData":[OSD([sQuery(id+"F2.wireOp",EDGE,"E3.9.20.2")])],"isStart":false});
            var Q252;
            Q252=makeQuery(id+"F3.opExtrude","CAP_EDGE",EDGE,{"disambiguationData":[OSD([sQuery(id+"F2.wireOp",EDGE,"E3.9.27.2")])],"isStart":false});
            var Q253;
            Q253=makeQuery(id+"F3.opExtrude","CAP_EDGE",EDGE,{"disambiguationData":[OSD([sQuery(id+"F2.wireOp",EDGE,"E2.14.2.3")])],"isStart":false});
            var Q254;
            Q254=makeQuery(id+"F3.opExtrude","CAP_EDGE",EDGE,{"disambiguationData":[OSD([sQuery(id+"F2.wireOp",EDGE,"E3.9.21.2")])],"isStart":false});
            var Q255;
            Q255=makeQuery(id+"F3.opExtrude","CAP_EDGE",EDGE,{"disambiguationData":[OSD([sQuery(id+"F2.wireOp",EDGE,"E2.8.2.3")])],"isStart":false});
            var Q256;
            Q256=makeQuery(id+"F3.opExtrude","CAP_EDGE",EDGE,{"disambiguationData":[OSD([sQuery(id+"F2.wireOp",EDGE,"E2.15.2.3")])],"isStart":false});
            var Q257;
            Q257=makeQuery(id+"F3.opExtrude","CAP_EDGE",EDGE,{"disambiguationData":[OSD([sQuery(id+"F2.wireOp",EDGE,"E2.2.2.3")])],"isStart":false});
            var Q258;
            Q258=makeQuery(id+"F3.opExtrude","CAP_EDGE",EDGE,{"disambiguationData":[OSD([sQuery(id+"F2.wireOp",EDGE,"E2.10.2.3")])],"isStart":false});
            var Q259;
            Q259=makeQuery(id+"F3.opExtrude","CAP_EDGE",EDGE,{"disambiguationData":[OSD([sQuery(id+"F2.wireOp",EDGE,"E3.9.29.2")])],"isStart":false});
            var Q260;
            Q260=makeQuery(id+"F3.opExtrude","CAP_EDGE",EDGE,{"disambiguationData":[OSD([sQuery(id+"F2.wireOp",EDGE,"E3.9.23.2")])],"isStart":false});
            var Q261;
            Q261=makeQuery(id+"F3.opExtrude","CAP_EDGE",EDGE,{"disambiguationData":[OSD([sQuery(id+"F2.wireOp",EDGE,"E2.17.2.3")])],"isStart":false});
            var Q262;
            Q262=makeQuery(id+"F3.opExtrude","CAP_EDGE",EDGE,{"disambiguationData":[OSD([sQuery(id+"F2.wireOp",EDGE,"E2.11.2.3")])],"isStart":false});
            var Q263;
            Q263=makeQuery(id+"F3.opExtrude","CAP_EDGE",EDGE,{"disambiguationData":[OSD([sQuery(id+"F2.wireOp",EDGE,"E2.18.2.3")])],"isStart":false});
            var Q264;
            Q264=makeQuery(id+"F3.opExtrude","CAP_EDGE",EDGE,{"disambiguationData":[OSD([sQuery(id+"F2.wireOp",EDGE,"E3.9.24.2")])],"isStart":false});
            var Q265;
            Q265=makeQuery(id+"F3.opExtrude","CAP_EDGE",EDGE,{"disambiguationData":[OSD([sQuery(id+"F2.wireOp",EDGE,"E2.5.2.3")])],"isStart":false});
            var Q266;
            Q266=makeQuery(id+"F3.opExtrude","CAP_EDGE",EDGE,{"disambiguationData":[OSD([sQuery(id+"F2.wireOp",EDGE,"E2.12.2.3")])],"isStart":false});
            var Q267;
            Q267=makeQuery(id+"F3.opExtrude","CAP_EDGE",EDGE,{"disambiguationData":[OSD([sQuery(id+"F2.wireOp",EDGE,"E2.6.2.3")])],"isStart":false});
            var Q268;
            Q268=makeQuery(id+"F3.opExtrude","CAP_EDGE",EDGE,{"disambiguationData":[OSD([sQuery(id+"F2.wireOp",EDGE,"E3.9.25.2")])],"isStart":false});
            var Q269;
            Q269=makeQuery(id+"F3.opExtrude","CAP_EDGE",EDGE,{"disambiguationData":[OSD([sQuery(id+"F2.wireOp",EDGE,"E2.4.2.0")])],"isStart":false});
            var Q270;
            Q270=makeQuery(id+"F3.opExtrude","CAP_EDGE",EDGE,{"disambiguationData":[OSD([sQuery(id+"F2.wireOp",EDGE,"E2.16.2.0")])],"isStart":false});
            var Q271;
            Q271=makeQuery(id+"F3.opExtrude","CAP_EDGE",EDGE,{"disambiguationData":[OSD([sQuery(id+"F2.wireOp",EDGE,"E2.3.2.0")])],"isStart":false});
            var Q272;
            Q272=makeQuery(id+"F3.opExtrude","CAP_EDGE",EDGE,{"disambiguationData":[OSD([sQuery(id+"F2.wireOp",EDGE,"E2.10.2.0")])],"isStart":false});
            var Q273;
            Q273=makeQuery(id+"F3.opExtrude","CAP_EDGE",EDGE,{"disambiguationData":[OSD([sQuery(id+"F2.wireOp",EDGE,"E3.0.29.2")])],"isStart":false});
            var Q274;
            Q274=makeQuery(id+"F3.opExtrude","CAP_EDGE",EDGE,{"disambiguationData":[OSD([sQuery(id+"F2.wireOp",EDGE,"E2.9.2.3")])],"isStart":false});
            var Q275;
            Q275=makeQuery(id+"F3.opExtrude","CAP_EDGE",EDGE,{"disambiguationData":[OSD([sQuery(id+"F2.wireOp",EDGE,"E3.9.28.2")])],"isStart":false});
            var Q276;
            Q276=makeQuery(id+"F3.opExtrude","CAP_EDGE",EDGE,{"disambiguationData":[OSD([sQuery(id+"F2.wireOp",EDGE,"E3.9.22.2")])],"isStart":false});
            var Q277;
            Q277=makeQuery(id+"F3.opExtrude","CAP_EDGE",EDGE,{"disambiguationData":[OSD([sQuery(id+"F2.wireOp",EDGE,"E2.13.2.0")])],"isStart":false});
            var Q278;
            Q278=makeQuery(id+"F3.opExtrude","CAP_EDGE",EDGE,{"disambiguationData":[OSD([sQuery(id+"F2.wireOp",EDGE,"E2.7.2.0")])],"isStart":false});
            var Q279;
            Q279=makeQuery(id+"F3.opExtrude","CAP_EDGE",EDGE,{"disambiguationData":[OSD([sQuery(id+"F2.wireOp",EDGE,"E3.0.26.2")])],"isStart":false});
            var Q280;
            Q280=makeQuery(id+"F3.opExtrude","CAP_EDGE",EDGE,{"disambiguationData":[OSD([sQuery(id+"F2.wireOp",EDGE,"E2.1.2.0")])],"isStart":false});
            var Q281;
            Q281=makeQuery(id+"F3.opExtrude","CAP_EDGE",EDGE,{"disambiguationData":[OSD([sQuery(id+"F2.wireOp",EDGE,"E3.0.20.2")])],"isStart":false});
            var Q282;
            Q282=makeQuery(id+"F3.opExtrude","CAP_EDGE",EDGE,{"disambiguationData":[OSD([sQuery(id+"F2.wireOp",EDGE,"E3.0.27.2")])],"isStart":false});
            var Q283;
            Q283=makeQuery(id+"F3.opExtrude","CAP_EDGE",EDGE,{"disambiguationData":[OSD([sQuery(id+"F2.wireOp",EDGE,"E2.8.2.0")])],"isStart":false});
            var Q284;
            Q284=makeQuery(id+"F3.opExtrude","CAP_EDGE",EDGE,{"disambiguationData":[OSD([sQuery(id+"F2.wireOp",EDGE,"E2.14.2.0")])],"isStart":false});
            var Q285;
            Q285=makeQuery(id+"F3.opExtrude","CAP_EDGE",EDGE,{"disambiguationData":[OSD([sQuery(id+"F2.wireOp",EDGE,"E2.2.2.0")])],"isStart":false});
            var Q286;
            Q286=makeQuery(id+"F3.opExtrude","CAP_EDGE",EDGE,{"disambiguationData":[OSD([sQuery(id+"F2.wireOp",EDGE,"E3.0.21.2")])],"isStart":false});
            var Q287;
            Q287=makeQuery(id+"F3.opExtrude","CAP_EDGE",EDGE,{"disambiguationData":[OSD([sQuery(id+"F2.wireOp",EDGE,"E3.0.28.2")])],"isStart":false});
            var Q288;
            Q288=makeQuery(id+"F3.opExtrude","CAP_EDGE",EDGE,{"disambiguationData":[OSD([sQuery(id+"F2.wireOp",EDGE,"E2.15.2.0")])],"isStart":false});
            var Q289;
            Q289=makeQuery(id+"F3.opExtrude","CAP_EDGE",EDGE,{"disambiguationData":[OSD([sQuery(id+"F2.wireOp",EDGE,"E3.0.22.2")])],"isStart":false});
            var Q290;
            Q290=makeQuery(id+"F3.opExtrude","CAP_EDGE",EDGE,{"disambiguationData":[OSD([sQuery(id+"F2.wireOp",EDGE,"E2.9.2.0")])],"isStart":false});
            var Q291;
            Q291=makeQuery(id+"F3.opExtrude","CAP_EDGE",EDGE,{"disambiguationData":[OSD([sQuery(id+"F2.wireOp",EDGE,"E3.0.23.2")])],"isStart":false});
            var Q292;
            Q292=makeQuery(id+"F3.opExtrude","CAP_EDGE",EDGE,{"disambiguationData":[OSD([sQuery(id+"F2.wireOp",EDGE,"E2.17.2.0")])],"isStart":false});
            var Q293;
            Q293=makeQuery(id+"F3.opExtrude","CAP_EDGE",EDGE,{"disambiguationData":[OSD([sQuery(id+"F2.wireOp",EDGE,"E3.0.24.2")])],"isStart":false});
            var Q294;
            Q294=makeQuery(id+"F3.opExtrude","CAP_EDGE",EDGE,{"disambiguationData":[OSD([sQuery(id+"F2.wireOp",EDGE,"E2.11.2.0")])],"isStart":false});
            var Q295;
            Q295=makeQuery(id+"F3.opExtrude","CAP_EDGE",EDGE,{"disambiguationData":[OSD([sQuery(id+"F2.wireOp",EDGE,"E2.18.2.0")])],"isStart":false});
            var Q296;
            Q296=makeQuery(id+"F3.opExtrude","CAP_EDGE",EDGE,{"disambiguationData":[OSD([sQuery(id+"F2.wireOp",EDGE,"E2.5.2.0")])],"isStart":false});
            var Q297;
            Q297=makeQuery(id+"F3.opExtrude","CAP_EDGE",EDGE,{"disambiguationData":[OSD([sQuery(id+"F2.wireOp",EDGE,"E2.12.2.0")])],"isStart":false});
            var Q298;
            Q298=makeQuery(id+"F3.opExtrude","CAP_EDGE",EDGE,{"disambiguationData":[OSD([sQuery(id+"F2.wireOp",EDGE,"E2.6.2.0")])],"isStart":false});
            var Q299;
            Q299=makeQuery(id+"F3.opExtrude","CAP_EDGE",EDGE,{"disambiguationData":[OSD([sQuery(id+"F2.wireOp",EDGE,"E3.0.25.2")])],"isStart":false});
            var Q300;
            Q300=makeQuery(id+"F3.opExtrude","CAP_EDGE",EDGE,{"disambiguationData":[OSD([sQuery(id+"F2.wireOp",EDGE,"E2.19.2.0")])],"isStart":false});
            var Q301;
            Q301=makeQuery(id+"F3.opExtrude","CAP_EDGE",EDGE,{"disambiguationData":[OSD([sQuery(id+"F2.wireOp",EDGE,"E2.0.2.1")])],"isStart":false});
            var Q302;
            Q302=makeQuery(id+"F3.opExtrude","CAP_EDGE",EDGE,{"disambiguationData":[OSD([sQuery(id+"F2.wireOp",EDGE,"E3.6.23.2")])],"isStart":false});
            var Q303;
            Q303=makeQuery(id+"F3.opExtrude","CAP_EDGE",EDGE,{"disambiguationData":[OSD([sQuery(id+"F2.wireOp",EDGE,"E2.17.2.2")])],"isStart":false});
            var Q304;
            Q304=makeQuery(id+"F3.opExtrude","CAP_EDGE",EDGE,{"disambiguationData":[OSD([sQuery(id+"F2.wireOp",EDGE,"E3.6.24.2")])],"isStart":false});
            var Q305;
            Q305=makeQuery(id+"F3.opExtrude","CAP_EDGE",EDGE,{"disambiguationData":[OSD([sQuery(id+"F2.wireOp",EDGE,"E2.11.2.2")])],"isStart":false});
            var Q306;
            Q306=makeQuery(id+"F3.opExtrude","CAP_EDGE",EDGE,{"disambiguationData":[OSD([sQuery(id+"F2.wireOp",EDGE,"E2.18.2.2")])],"isStart":false});
            var Q307;
            Q307=makeQuery(id+"F3.opExtrude","CAP_EDGE",EDGE,{"disambiguationData":[OSD([sQuery(id+"F2.wireOp",EDGE,"E2.5.2.2")])],"isStart":false});
            var Q308;
            Q308=makeQuery(id+"F3.opExtrude","CAP_EDGE",EDGE,{"disambiguationData":[OSD([sQuery(id+"F2.wireOp",EDGE,"E2.12.2.2")])],"isStart":false});
            var Q309;
            Q309=makeQuery(id+"F3.opExtrude","CAP_EDGE",EDGE,{"disambiguationData":[OSD([sQuery(id+"F2.wireOp",EDGE,"E2.6.2.2")])],"isStart":false});
            var Q310;
            Q310=makeQuery(id+"F3.opExtrude","CAP_EDGE",EDGE,{"disambiguationData":[OSD([sQuery(id+"F2.wireOp",EDGE,"E3.6.25.2")])],"isStart":false});
            var Q311;
            Q311=makeQuery(id+"F3.opExtrude","CAP_EDGE",EDGE,{"disambiguationData":[OSD([sQuery(id+"F2.wireOp",EDGE,"E2.19.2.2")])],"isStart":false});
            var Q312;
            Q312=makeQuery(id+"F3.opExtrude","CAP_EDGE",EDGE,{"disambiguationData":[OSD([sQuery(id+"F2.wireOp",EDGE,"E2.4.2.2")])],"isStart":false});
            var Q313;
            Q313=makeQuery(id+"F3.opExtrude","CAP_EDGE",EDGE,{"disambiguationData":[OSD([sQuery(id+"F2.wireOp",EDGE,"E2.16.2.2")])],"isStart":false});
            var Q314;
            Q314=makeQuery(id+"F3.opExtrude","CAP_EDGE",EDGE,{"disambiguationData":[OSD([sQuery(id+"F2.wireOp",EDGE,"E2.3.2.2")])],"isStart":false});
            var Q315;
            Q315=makeQuery(id+"F3.opExtrude","CAP_EDGE",EDGE,{"disambiguationData":[OSD([sQuery(id+"F2.wireOp",EDGE,"E2.10.2.2")])],"isStart":false});
            var Q316;
            Q316=makeQuery(id+"F3.opExtrude","CAP_EDGE",EDGE,{"disambiguationData":[OSD([sQuery(id+"F2.wireOp",EDGE,"E3.6.29.2")])],"isStart":false});
            var Q317;
            Q317=makeQuery(id+"F3.opExtrude","CAP_EDGE",EDGE,{"disambiguationData":[OSD([sQuery(id+"F2.wireOp",EDGE,"E3.6.22.2")])],"isStart":false});
            var Q318;
            Q318=makeQuery(id+"F3.opExtrude","CAP_EDGE",EDGE,{"disambiguationData":[OSD([sQuery(id+"F2.wireOp",EDGE,"E2.13.2.2")])],"isStart":false});
            var Q319;
            Q319=makeQuery(id+"F3.opExtrude","CAP_EDGE",EDGE,{"disambiguationData":[OSD([sQuery(id+"F2.wireOp",EDGE,"E2.7.2.2")])],"isStart":false});
            var Q320;
            Q320=makeQuery(id+"F3.opExtrude","CAP_EDGE",EDGE,{"disambiguationData":[OSD([sQuery(id+"F2.wireOp",EDGE,"E3.6.26.2")])],"isStart":false});
            var Q321;
            Q321=makeQuery(id+"F3.opExtrude","CAP_EDGE",EDGE,{"disambiguationData":[OSD([sQuery(id+"F2.wireOp",EDGE,"E2.1.2.2")])],"isStart":false});
            var Q322;
            Q322=makeQuery(id+"F3.opExtrude","CAP_EDGE",EDGE,{"disambiguationData":[OSD([sQuery(id+"F2.wireOp",EDGE,"E3.6.20.2")])],"isStart":false});
            var Q323;
            Q323=makeQuery(id+"F3.opExtrude","CAP_EDGE",EDGE,{"disambiguationData":[OSD([sQuery(id+"F2.wireOp",EDGE,"E3.6.27.2")])],"isStart":false});
            var Q324;
            Q324=makeQuery(id+"F3.opExtrude","CAP_EDGE",EDGE,{"disambiguationData":[OSD([sQuery(id+"F2.wireOp",EDGE,"E2.14.2.2")])],"isStart":false});
            var Q325;
            Q325=makeQuery(id+"F3.opExtrude","CAP_EDGE",EDGE,{"disambiguationData":[OSD([sQuery(id+"F2.wireOp",EDGE,"E3.6.21.2")])],"isStart":false});
            var Q326;
            Q326=makeQuery(id+"F3.opExtrude","CAP_EDGE",EDGE,{"disambiguationData":[OSD([sQuery(id+"F2.wireOp",EDGE,"E2.8.2.2")])],"isStart":false});
            var Q327;
            Q327=makeQuery(id+"F3.opExtrude","CAP_EDGE",EDGE,{"disambiguationData":[OSD([sQuery(id+"F2.wireOp",EDGE,"E2.15.2.2")])],"isStart":false});
            var Q328;
            Q328=makeQuery(id+"F3.opExtrude","CAP_EDGE",EDGE,{"disambiguationData":[OSD([sQuery(id+"F2.wireOp",EDGE,"E2.2.2.2")])],"isStart":false});
            var Q329;
            Q329=makeQuery(id+"F3.opExtrude","CAP_EDGE",EDGE,{"disambiguationData":[OSD([sQuery(id+"F2.wireOp",EDGE,"E2.9.2.2")])],"isStart":false});
            var Q330;
            Q330=makeQuery(id+"F3.opExtrude","CAP_EDGE",EDGE,{"disambiguationData":[OSD([sQuery(id+"F2.wireOp",EDGE,"E3.6.28.2")])],"isStart":false});
            var Q331;
            Q331=makeQuery(id+"F3.opExtrude","CAP_EDGE",EDGE,{"disambiguationData":[OSD([sQuery(id+"F2.wireOp",EDGE,"E2.4.2.1")])],"isStart":false});
            var Q332;
            Q332=makeQuery(id+"F3.opExtrude","CAP_EDGE",EDGE,{"disambiguationData":[OSD([sQuery(id+"F2.wireOp",EDGE,"E2.16.2.1")])],"isStart":false});
            var Q333;
            Q333=makeQuery(id+"F3.opExtrude","CAP_EDGE",EDGE,{"disambiguationData":[OSD([sQuery(id+"F2.wireOp",EDGE,"E2.3.2.1")])],"isStart":false});
            var Q334;
            Q334=makeQuery(id+"F3.opExtrude","CAP_EDGE",EDGE,{"disambiguationData":[OSD([sQuery(id+"F2.wireOp",EDGE,"E2.10.2.1")])],"isStart":false});
            var Q335;
            Q335=makeQuery(id+"F3.opExtrude","CAP_EDGE",EDGE,{"disambiguationData":[OSD([sQuery(id+"F2.wireOp",EDGE,"E3.3.29.2")])],"isStart":false});
            var Q336;
            Q336=makeQuery(id+"F3.opExtrude","CAP_EDGE",EDGE,{"disambiguationData":[OSD([sQuery(id+"F2.wireOp",EDGE,"E3.3.23.2")])],"isStart":false});
            var Q337;
            Q337=makeQuery(id+"F3.opExtrude","CAP_EDGE",EDGE,{"disambiguationData":[OSD([sQuery(id+"F2.wireOp",EDGE,"E2.17.2.1")])],"isStart":false});
            var Q338;
            Q338=makeQuery(id+"F3.opExtrude","CAP_EDGE",EDGE,{"disambiguationData":[OSD([sQuery(id+"F2.wireOp",EDGE,"E3.3.24.2")])],"isStart":false});
            var Q339;
            Q339=makeQuery(id+"F3.opExtrude","CAP_EDGE",EDGE,{"disambiguationData":[OSD([sQuery(id+"F2.wireOp",EDGE,"E2.11.2.1")])],"isStart":false});
            var Q340;
            Q340=makeQuery(id+"F3.opExtrude","CAP_EDGE",EDGE,{"disambiguationData":[OSD([sQuery(id+"F2.wireOp",EDGE,"E3.3.27.2")])],"isStart":false});
            var Q341;
            Q341=makeQuery(id+"F3.opExtrude","CAP_EDGE",EDGE,{"disambiguationData":[OSD([sQuery(id+"F2.wireOp",EDGE,"E2.14.2.1")])],"isStart":false});
            var Q342;
            Q342=makeQuery(id+"F3.opExtrude","CAP_EDGE",EDGE,{"disambiguationData":[OSD([sQuery(id+"F2.wireOp",EDGE,"E3.3.21.2")])],"isStart":false});
            var Q343;
            Q343=makeQuery(id+"F3.opExtrude","CAP_EDGE",EDGE,{"disambiguationData":[OSD([sQuery(id+"F2.wireOp",EDGE,"E2.8.2.1")])],"isStart":false});
            var Q344;
            Q344=makeQuery(id+"F3.opExtrude","CAP_EDGE",EDGE,{"disambiguationData":[OSD([sQuery(id+"F2.wireOp",EDGE,"E2.15.2.1")])],"isStart":false});
            var Q345;
            Q345=makeQuery(id+"F3.opExtrude","CAP_EDGE",EDGE,{"disambiguationData":[OSD([sQuery(id+"F2.wireOp",EDGE,"E2.2.2.1")])],"isStart":false});
            var Q346;
            Q346=makeQuery(id+"F3.opExtrude","CAP_EDGE",EDGE,{"disambiguationData":[OSD([sQuery(id+"F2.wireOp",EDGE,"E3.3.22.2")])],"isStart":false});
            var Q347;
            Q347=makeQuery(id+"F3.opExtrude","CAP_EDGE",EDGE,{"disambiguationData":[OSD([sQuery(id+"F2.wireOp",EDGE,"E3.3.28.2")])],"isStart":false});
            var Q348;
            Q348=makeQuery(id+"F3.opExtrude","CAP_EDGE",EDGE,{"disambiguationData":[OSD([sQuery(id+"F2.wireOp",EDGE,"E2.9.2.1")])],"isStart":false});
            var Q349;
            Q349=makeQuery(id+"F3.opExtrude","CAP_EDGE",EDGE,{"disambiguationData":[OSD([sQuery(id+"F2.wireOp",EDGE,"E2.18.2.1")])],"isStart":false});
            var Q350;
            Q350=makeQuery(id+"F3.opExtrude","CAP_EDGE",EDGE,{"disambiguationData":[OSD([sQuery(id+"F2.wireOp",EDGE,"E2.5.2.1")])],"isStart":false});
            var Q351;
            Q351=makeQuery(id+"F3.opExtrude","CAP_EDGE",EDGE,{"disambiguationData":[OSD([sQuery(id+"F2.wireOp",EDGE,"E2.12.2.1")])],"isStart":false});
            var Q352;
            Q352=makeQuery(id+"F3.opExtrude","CAP_EDGE",EDGE,{"disambiguationData":[OSD([sQuery(id+"F2.wireOp",EDGE,"E2.6.2.1")])],"isStart":false});
            var Q353;
            Q353=makeQuery(id+"F3.opExtrude","CAP_EDGE",EDGE,{"disambiguationData":[OSD([sQuery(id+"F2.wireOp",EDGE,"E3.3.25.2")])],"isStart":false});
            var Q354;
            Q354=makeQuery(id+"F3.opExtrude","CAP_EDGE",EDGE,{"disambiguationData":[OSD([sQuery(id+"F2.wireOp",EDGE,"E2.19.2.1")])],"isStart":false});
            var Q355;
            Q355=makeQuery(id+"F3.opExtrude","CAP_EDGE",EDGE,{"disambiguationData":[OSD([sQuery(id+"F2.wireOp",EDGE,"E2.13.2.1")])],"isStart":false});
            var Q356;
            Q356=makeQuery(id+"F3.opExtrude","CAP_EDGE",EDGE,{"disambiguationData":[OSD([sQuery(id+"F2.wireOp",EDGE,"E2.7.2.1")])],"isStart":false});
            var Q357;
            Q357=makeQuery(id+"F3.opExtrude","CAP_EDGE",EDGE,{"disambiguationData":[OSD([sQuery(id+"F2.wireOp",EDGE,"E3.3.26.2")])],"isStart":false});
            var Q358;
            Q358=makeQuery(id+"F3.opExtrude","CAP_EDGE",EDGE,{"disambiguationData":[OSD([sQuery(id+"F2.wireOp",EDGE,"E2.1.2.1")])],"isStart":false});
            var Q359;
            Q359=makeQuery(id+"F3.opExtrude","CAP_EDGE",EDGE,{"disambiguationData":[OSD([sQuery(id+"F2.wireOp",EDGE,"E3.3.20.2")])],"isStart":false});
            var Q360;
            Q360=makeQuery(id+"F3.opExtrude","CAP_EDGE",EDGE,{"disambiguationData":[OSD([sQuery(id+"F2.wireOp",EDGE,"E2.0.3.0")])],"isStart":false});
            var Q361;
            Q361=makeQuery(id+"F3.opExtrude","CAP_EDGE",EDGE,{"disambiguationData":[OSD([sQuery(id+"F2.wireOp",EDGE,"E2.0.3.2")])],"isStart":false});
            var Q362;
            Q362=makeQuery(id+"F3.opExtrude","CAP_EDGE",EDGE,{"disambiguationData":[OSD([sQuery(id+"F2.wireOp",EDGE,"E2.16.3.0")])],"isStart":false});
            var Q363;
            Q363=makeQuery(id+"F3.opExtrude","CAP_EDGE",EDGE,{"disambiguationData":[OSD([sQuery(id+"F2.wireOp",EDGE,"E2.4.3.0")])],"isStart":false});
            var Q364;
            Q364=makeQuery(id+"F3.opExtrude","CAP_EDGE",EDGE,{"disambiguationData":[OSD([sQuery(id+"F2.wireOp",EDGE,"E2.3.3.0")])],"isStart":false});
            var Q365;
            Q365=makeQuery(id+"F3.opExtrude","CAP_EDGE",EDGE,{"disambiguationData":[OSD([sQuery(id+"F2.wireOp",EDGE,"E2.10.3.0")])],"isStart":false});
            var Q366;
            Q366=makeQuery(id+"F3.opExtrude","CAP_EDGE",EDGE,{"disambiguationData":[OSD([sQuery(id+"F2.wireOp",EDGE,"E3.0.29.3")])],"isStart":false});
            var Q367;
            Q367=makeQuery(id+"F3.opExtrude","CAP_EDGE",EDGE,{"disambiguationData":[OSD([sQuery(id+"F2.wireOp",EDGE,"E3.0.23.3")])],"isStart":false});
            var Q368;
            Q368=makeQuery(id+"F3.opExtrude","CAP_EDGE",EDGE,{"disambiguationData":[OSD([sQuery(id+"F2.wireOp",EDGE,"E2.17.3.0")])],"isStart":false});
            var Q369;
            Q369=makeQuery(id+"F3.opExtrude","CAP_EDGE",EDGE,{"disambiguationData":[OSD([sQuery(id+"F2.wireOp",EDGE,"E2.1.3.0")])],"isStart":false});
            var Q370;
            Q370=makeQuery(id+"F3.opExtrude","CAP_EDGE",EDGE,{"disambiguationData":[OSD([sQuery(id+"F2.wireOp",EDGE,"E3.0.20.3")])],"isStart":false});
            var Q371;
            Q371=makeQuery(id+"F3.opExtrude","CAP_EDGE",EDGE,{"disambiguationData":[OSD([sQuery(id+"F2.wireOp",EDGE,"E3.0.27.3")])],"isStart":false});
            var Q372;
            Q372=makeQuery(id+"F3.opExtrude","CAP_EDGE",EDGE,{"disambiguationData":[OSD([sQuery(id+"F2.wireOp",EDGE,"E2.14.3.0")])],"isStart":false});
            var Q373;
            Q373=makeQuery(id+"F3.opExtrude","CAP_EDGE",EDGE,{"disambiguationData":[OSD([sQuery(id+"F2.wireOp",EDGE,"E3.0.21.3")])],"isStart":false});
            var Q374;
            Q374=makeQuery(id+"F3.opExtrude","CAP_EDGE",EDGE,{"disambiguationData":[OSD([sQuery(id+"F2.wireOp",EDGE,"E2.8.3.0")])],"isStart":false});
            var Q375;
            Q375=makeQuery(id+"F3.opExtrude","CAP_EDGE",EDGE,{"disambiguationData":[OSD([sQuery(id+"F2.wireOp",EDGE,"E2.15.3.0")])],"isStart":false});
            var Q376;
            Q376=makeQuery(id+"F3.opExtrude","CAP_EDGE",EDGE,{"disambiguationData":[OSD([sQuery(id+"F2.wireOp",EDGE,"E2.2.3.0")])],"isStart":false});
            var Q377;
            Q377=makeQuery(id+"F3.opExtrude","CAP_EDGE",EDGE,{"disambiguationData":[OSD([sQuery(id+"F2.wireOp",EDGE,"E2.9.3.0")])],"isStart":false});
            var Q378;
            Q378=makeQuery(id+"F3.opExtrude","CAP_EDGE",EDGE,{"disambiguationData":[OSD([sQuery(id+"F2.wireOp",EDGE,"E3.0.28.3")])],"isStart":false});
            var Q379;
            Q379=makeQuery(id+"F3.opExtrude","CAP_EDGE",EDGE,{"disambiguationData":[OSD([sQuery(id+"F2.wireOp",EDGE,"E3.0.22.3")])],"isStart":false});
            var Q380;
            Q380=makeQuery(id+"F3.opExtrude","CAP_EDGE",EDGE,{"disambiguationData":[OSD([sQuery(id+"F2.wireOp",EDGE,"E2.11.3.0")])],"isStart":false});
            var Q381;
            Q381=makeQuery(id+"F3.opExtrude","CAP_EDGE",EDGE,{"disambiguationData":[OSD([sQuery(id+"F2.wireOp",EDGE,"E2.5.3.0")])],"isStart":false});
            var Q382;
            Q382=makeQuery(id+"F3.opExtrude","CAP_EDGE",EDGE,{"disambiguationData":[OSD([sQuery(id+"F2.wireOp",EDGE,"E3.0.24.3")])],"isStart":false});
            var Q383;
            Q383=makeQuery(id+"F3.opExtrude","CAP_EDGE",EDGE,{"disambiguationData":[OSD([sQuery(id+"F2.wireOp",EDGE,"E2.18.3.0")])],"isStart":false});
            var Q384;
            Q384=makeQuery(id+"F3.opExtrude","CAP_EDGE",EDGE,{"disambiguationData":[OSD([sQuery(id+"F2.wireOp",EDGE,"E3.0.25.3")])],"isStart":false});
            var Q385;
            Q385=makeQuery(id+"F3.opExtrude","CAP_EDGE",EDGE,{"disambiguationData":[OSD([sQuery(id+"F2.wireOp",EDGE,"E2.6.3.0")])],"isStart":false});
            var Q386;
            Q386=makeQuery(id+"F3.opExtrude","CAP_EDGE",EDGE,{"disambiguationData":[OSD([sQuery(id+"F2.wireOp",EDGE,"E2.12.3.0")])],"isStart":false});
            var Q387;
            Q387=makeQuery(id+"F3.opExtrude","CAP_EDGE",EDGE,{"disambiguationData":[OSD([sQuery(id+"F2.wireOp",EDGE,"E2.19.3.0")])],"isStart":false});
            var Q388;
            Q388=makeQuery(id+"F3.opExtrude","CAP_EDGE",EDGE,{"disambiguationData":[OSD([sQuery(id+"F2.wireOp",EDGE,"E2.13.3.0")])],"isStart":false});
            var Q389;
            Q389=makeQuery(id+"F3.opExtrude","CAP_EDGE",EDGE,{"disambiguationData":[OSD([sQuery(id+"F2.wireOp",EDGE,"E2.7.3.0")])],"isStart":false});
            var Q390;
            Q390=makeQuery(id+"F3.opExtrude","CAP_EDGE",EDGE,{"disambiguationData":[OSD([sQuery(id+"F2.wireOp",EDGE,"E3.0.26.3")])],"isStart":false});
            var Q391;
            Q391=makeQuery(id+"F3.opExtrude","CAP_EDGE",EDGE,{"disambiguationData":[OSD([sQuery(id+"F2.wireOp",EDGE,"E3.6.25.3")])],"isStart":false});
            var Q392;
            Q392=makeQuery(id+"F3.opExtrude","CAP_EDGE",EDGE,{"disambiguationData":[OSD([sQuery(id+"F2.wireOp",EDGE,"E2.12.3.2")])],"isStart":false});
            var Q393;
            Q393=makeQuery(id+"F3.opExtrude","CAP_EDGE",EDGE,{"disambiguationData":[OSD([sQuery(id+"F2.wireOp",EDGE,"E2.19.3.2")])],"isStart":false});
            var Q394;
            Q394=makeQuery(id+"F3.opExtrude","CAP_EDGE",EDGE,{"disambiguationData":[OSD([sQuery(id+"F2.wireOp",EDGE,"E2.6.3.2")])],"isStart":false});
            var Q395;
            Q395=makeQuery(id+"F3.opExtrude","CAP_EDGE",EDGE,{"disambiguationData":[OSD([sQuery(id+"F2.wireOp",EDGE,"E2.13.3.2")])],"isStart":false});
            var Q396;
            Q396=makeQuery(id+"F3.opExtrude","CAP_EDGE",EDGE,{"disambiguationData":[OSD([sQuery(id+"F2.wireOp",EDGE,"E2.7.3.2")])],"isStart":false});
            var Q397;
            Q397=makeQuery(id+"F3.opExtrude","CAP_EDGE",EDGE,{"disambiguationData":[OSD([sQuery(id+"F2.wireOp",EDGE,"E3.6.26.3")])],"isStart":false});
            var Q398;
            Q398=makeQuery(id+"F3.opExtrude","CAP_EDGE",EDGE,{"disambiguationData":[OSD([sQuery(id+"F2.wireOp",EDGE,"E2.1.3.2")])],"isStart":false});
            var Q399;
            Q399=makeQuery(id+"F3.opExtrude","CAP_EDGE",EDGE,{"disambiguationData":[OSD([sQuery(id+"F2.wireOp",EDGE,"E3.6.20.3")])],"isStart":false});
            var Q400;
            Q400=makeQuery(id+"F3.opExtrude","CAP_EDGE",EDGE,{"disambiguationData":[OSD([sQuery(id+"F2.wireOp",EDGE,"E3.6.27.3")])],"isStart":false});
            var Q401;
            Q401=makeQuery(id+"F3.opExtrude","CAP_EDGE",EDGE,{"disambiguationData":[OSD([sQuery(id+"F2.wireOp",EDGE,"E2.14.3.2")])],"isStart":false});
            var Q402;
            Q402=makeQuery(id+"F3.opExtrude","CAP_EDGE",EDGE,{"disambiguationData":[OSD([sQuery(id+"F2.wireOp",EDGE,"E3.6.21.3")])],"isStart":false});
            var Q403;
            Q403=makeQuery(id+"F3.opExtrude","CAP_EDGE",EDGE,{"disambiguationData":[OSD([sQuery(id+"F2.wireOp",EDGE,"E2.8.3.2")])],"isStart":false});
            var Q404;
            Q404=makeQuery(id+"F3.opExtrude","CAP_EDGE",EDGE,{"disambiguationData":[OSD([sQuery(id+"F2.wireOp",EDGE,"E2.3.3.2")])],"isStart":false});
            var Q405;
            Q405=makeQuery(id+"F3.opExtrude","CAP_EDGE",EDGE,{"disambiguationData":[OSD([sQuery(id+"F2.wireOp",EDGE,"E2.4.3.2")])],"isStart":false});
            var Q406;
            Q406=makeQuery(id+"F3.opExtrude","CAP_EDGE",EDGE,{"disambiguationData":[OSD([sQuery(id+"F2.wireOp",EDGE,"E3.6.29.3")])],"isStart":false});
            var Q407;
            Q407=makeQuery(id+"F3.opExtrude","CAP_EDGE",EDGE,{"disambiguationData":[OSD([sQuery(id+"F2.wireOp",EDGE,"E2.10.3.2")])],"isStart":false});
            var Q408;
            Q408=makeQuery(id+"F3.opExtrude","CAP_EDGE",EDGE,{"disambiguationData":[OSD([sQuery(id+"F2.wireOp",EDGE,"E2.0.3.1")])],"isStart":false});
            var Q409;
            Q409=makeQuery(id+"F3.opExtrude","CAP_EDGE",EDGE,{"disambiguationData":[OSD([sQuery(id+"F2.wireOp",EDGE,"E2.16.3.2")])],"isStart":false});
            var Q410;
            Q410=makeQuery(id+"F3.opExtrude","CAP_EDGE",EDGE,{"disambiguationData":[OSD([sQuery(id+"F2.wireOp",EDGE,"E3.6.23.3")])],"isStart":false});
            var Q411;
            Q411=makeQuery(id+"F3.opExtrude","CAP_EDGE",EDGE,{"disambiguationData":[OSD([sQuery(id+"F2.wireOp",EDGE,"E2.17.3.2")])],"isStart":false});
            var Q412;
            Q412=makeQuery(id+"F3.opExtrude","CAP_EDGE",EDGE,{"disambiguationData":[OSD([sQuery(id+"F2.wireOp",EDGE,"E2.11.3.2")])],"isStart":false});
            var Q413;
            Q413=makeQuery(id+"F3.opExtrude","CAP_EDGE",EDGE,{"disambiguationData":[OSD([sQuery(id+"F2.wireOp",EDGE,"E2.5.3.2")])],"isStart":false});
            var Q414;
            Q414=makeQuery(id+"F3.opExtrude","CAP_EDGE",EDGE,{"disambiguationData":[OSD([sQuery(id+"F2.wireOp",EDGE,"E3.6.24.3")])],"isStart":false});
            var Q415;
            Q415=makeQuery(id+"F3.opExtrude","CAP_EDGE",EDGE,{"disambiguationData":[OSD([sQuery(id+"F2.wireOp",EDGE,"E2.18.3.2")])],"isStart":false});
            var Q416;
            Q416=makeQuery(id+"F3.opExtrude","CAP_EDGE",EDGE,{"disambiguationData":[OSD([sQuery(id+"F2.wireOp",EDGE,"E2.15.3.2")])],"isStart":false});
            var Q417;
            Q417=makeQuery(id+"F3.opExtrude","CAP_EDGE",EDGE,{"disambiguationData":[OSD([sQuery(id+"F2.wireOp",EDGE,"E2.2.3.2")])],"isStart":false});
            var Q418;
            Q418=makeQuery(id+"F3.opExtrude","CAP_EDGE",EDGE,{"disambiguationData":[OSD([sQuery(id+"F2.wireOp",EDGE,"E2.9.3.2")])],"isStart":false});
            var Q419;
            Q419=makeQuery(id+"F3.opExtrude","CAP_EDGE",EDGE,{"disambiguationData":[OSD([sQuery(id+"F2.wireOp",EDGE,"E3.6.28.3")])],"isStart":false});
            var Q420;
            Q420=makeQuery(id+"F3.opExtrude","CAP_EDGE",EDGE,{"disambiguationData":[OSD([sQuery(id+"F2.wireOp",EDGE,"E3.6.22.3")])],"isStart":false});
            var Q421;
            Q421=makeQuery(id+"F3.opExtrude","CAP_EDGE",EDGE,{"disambiguationData":[OSD([sQuery(id+"F2.wireOp",EDGE,"E2.0.3.3")])],"isStart":false});
            var Q422;
            Q422=makeQuery(id+"F3.opExtrude","CAP_EDGE",EDGE,{"disambiguationData":[OSD([sQuery(id+"F2.wireOp",EDGE,"E3.3.29.3")])],"isStart":false});
            var Q423;
            Q423=makeQuery(id+"F3.opExtrude","CAP_EDGE",EDGE,{"disambiguationData":[OSD([sQuery(id+"F2.wireOp",EDGE,"E2.16.3.1")])],"isStart":false});
            var Q424;
            Q424=makeQuery(id+"F3.opExtrude","CAP_EDGE",EDGE,{"disambiguationData":[OSD([sQuery(id+"F2.wireOp",EDGE,"E3.3.23.3")])],"isStart":false});
            var Q425;
            Q425=makeQuery(id+"F3.opExtrude","CAP_EDGE",EDGE,{"disambiguationData":[OSD([sQuery(id+"F2.wireOp",EDGE,"E2.10.3.1")])],"isStart":false});
            var Q426;
            Q426=makeQuery(id+"F3.opExtrude","CAP_EDGE",EDGE,{"disambiguationData":[OSD([sQuery(id+"F2.wireOp",EDGE,"E2.17.3.1")])],"isStart":false});
            var Q427;
            Q427=makeQuery(id+"F3.opExtrude","CAP_EDGE",EDGE,{"disambiguationData":[OSD([sQuery(id+"F2.wireOp",EDGE,"E2.11.3.1")])],"isStart":false});
            var Q428;
            Q428=makeQuery(id+"F3.opExtrude","CAP_EDGE",EDGE,{"disambiguationData":[OSD([sQuery(id+"F2.wireOp",EDGE,"E2.5.3.1")])],"isStart":false});
            var Q429;
            Q429=makeQuery(id+"F3.opExtrude","CAP_EDGE",EDGE,{"disambiguationData":[OSD([sQuery(id+"F2.wireOp",EDGE,"E3.3.24.3")])],"isStart":false});
            var Q430;
            Q430=makeQuery(id+"F3.opExtrude","CAP_EDGE",EDGE,{"disambiguationData":[OSD([sQuery(id+"F2.wireOp",EDGE,"E2.18.3.1")])],"isStart":false});
            var Q431;
            Q431=makeQuery(id+"F3.opExtrude","CAP_EDGE",EDGE,{"disambiguationData":[OSD([sQuery(id+"F2.wireOp",EDGE,"E3.3.25.3")])],"isStart":false});
            var Q432;
            Q432=makeQuery(id+"F3.opExtrude","CAP_EDGE",EDGE,{"disambiguationData":[OSD([sQuery(id+"F2.wireOp",EDGE,"E2.12.3.1")])],"isStart":false});
            var Q433;
            Q433=makeQuery(id+"F3.opExtrude","CAP_EDGE",EDGE,{"disambiguationData":[OSD([sQuery(id+"F2.wireOp",EDGE,"E2.3.3.1")])],"isStart":false});
            var Q434;
            Q434=makeQuery(id+"F3.opExtrude","CAP_EDGE",EDGE,{"disambiguationData":[OSD([sQuery(id+"F2.wireOp",EDGE,"E2.4.3.1")])],"isStart":false});
            var Q435;
            Q435=makeQuery(id+"F3.opExtrude","CAP_EDGE",EDGE,{"disambiguationData":[OSD([sQuery(id+"F2.wireOp",EDGE,"E2.9.3.1")])],"isStart":false});
            var Q436;
            Q436=makeQuery(id+"F3.opExtrude","CAP_EDGE",EDGE,{"disambiguationData":[OSD([sQuery(id+"F2.wireOp",EDGE,"E3.3.28.3")])],"isStart":false});
            var Q437;
            Q437=makeQuery(id+"F3.opExtrude","CAP_EDGE",EDGE,{"disambiguationData":[OSD([sQuery(id+"F2.wireOp",EDGE,"E3.3.22.3")])],"isStart":false});
            var Q438;
            Q438=makeQuery(id+"F3.opExtrude","CAP_EDGE",EDGE,{"disambiguationData":[OSD([sQuery(id+"F2.wireOp",EDGE,"E2.19.3.1")])],"isStart":false});
            var Q439;
            Q439=makeQuery(id+"F3.opExtrude","CAP_EDGE",EDGE,{"disambiguationData":[OSD([sQuery(id+"F2.wireOp",EDGE,"E2.6.3.1")])],"isStart":false});
            var Q440;
            Q440=makeQuery(id+"F3.opExtrude","CAP_EDGE",EDGE,{"disambiguationData":[OSD([sQuery(id+"F2.wireOp",EDGE,"E2.13.3.1")])],"isStart":false});
            var Q441;
            Q441=makeQuery(id+"F3.opExtrude","CAP_EDGE",EDGE,{"disambiguationData":[OSD([sQuery(id+"F2.wireOp",EDGE,"E2.7.3.1")])],"isStart":false});
            var Q442;
            Q442=makeQuery(id+"F3.opExtrude","CAP_EDGE",EDGE,{"disambiguationData":[OSD([sQuery(id+"F2.wireOp",EDGE,"E3.3.26.3")])],"isStart":false});
            var Q443;
            Q443=makeQuery(id+"F3.opExtrude","CAP_EDGE",EDGE,{"disambiguationData":[OSD([sQuery(id+"F2.wireOp",EDGE,"E2.1.3.1")])],"isStart":false});
            var Q444;
            Q444=makeQuery(id+"F3.opExtrude","CAP_EDGE",EDGE,{"disambiguationData":[OSD([sQuery(id+"F2.wireOp",EDGE,"E3.3.20.3")])],"isStart":false});
            var Q445;
            Q445=makeQuery(id+"F3.opExtrude","CAP_EDGE",EDGE,{"disambiguationData":[OSD([sQuery(id+"F2.wireOp",EDGE,"E3.3.27.3")])],"isStart":false});
            var Q446;
            Q446=makeQuery(id+"F3.opExtrude","CAP_EDGE",EDGE,{"disambiguationData":[OSD([sQuery(id+"F2.wireOp",EDGE,"E2.14.3.1")])],"isStart":false});
            var Q447;
            Q447=makeQuery(id+"F3.opExtrude","CAP_EDGE",EDGE,{"disambiguationData":[OSD([sQuery(id+"F2.wireOp",EDGE,"E3.3.21.3")])],"isStart":false});
            var Q448;
            Q448=makeQuery(id+"F3.opExtrude","CAP_EDGE",EDGE,{"disambiguationData":[OSD([sQuery(id+"F2.wireOp",EDGE,"E2.8.3.1")])],"isStart":false});
            var Q449;
            Q449=makeQuery(id+"F3.opExtrude","CAP_EDGE",EDGE,{"disambiguationData":[OSD([sQuery(id+"F2.wireOp",EDGE,"E2.15.3.1")])],"isStart":false});
            var Q450;
            Q450=makeQuery(id+"F3.opExtrude","CAP_EDGE",EDGE,{"disambiguationData":[OSD([sQuery(id+"F2.wireOp",EDGE,"E2.2.3.1")])],"isStart":false});
            var Q451;
            Q451=makeQuery(id+"F3.opExtrude","CAP_EDGE",EDGE,{"disambiguationData":[OSD([sQuery(id+"F2.wireOp",EDGE,"E2.3.3.3")])],"isStart":false});
            var Q452;
            Q452=makeQuery(id+"F3.opExtrude","CAP_EDGE",EDGE,{"disambiguationData":[OSD([sQuery(id+"F2.wireOp",EDGE,"E2.4.3.3")])],"isStart":false});
            var Q453;
            Q453=makeQuery(id+"F3.opExtrude","CAP_EDGE",EDGE,{"disambiguationData":[OSD([sQuery(id+"F2.wireOp",EDGE,"E3.9.29.3")])],"isStart":false});
            var Q454;
            Q454=makeQuery(id+"F3.opExtrude","CAP_EDGE",EDGE,{"disambiguationData":[OSD([sQuery(id+"F2.wireOp",EDGE,"E2.16.3.3")])],"isStart":false});
            var Q455;
            Q455=makeQuery(id+"F3.opExtrude","CAP_EDGE",EDGE,{"disambiguationData":[OSD([sQuery(id+"F2.wireOp",EDGE,"E3.9.23.3")])],"isStart":false});
            var Q456;
            Q456=makeQuery(id+"F3.opExtrude","CAP_EDGE",EDGE,{"disambiguationData":[OSD([sQuery(id+"F2.wireOp",EDGE,"E2.10.3.3")])],"isStart":false});
            var Q457;
            Q457=makeQuery(id+"F3.opExtrude","CAP_EDGE",EDGE,{"disambiguationData":[OSD([sQuery(id+"F2.wireOp",EDGE,"E2.7.3.3")])],"isStart":false});
            var Q458;
            Q458=makeQuery(id+"F3.opExtrude","CAP_EDGE",EDGE,{"disambiguationData":[OSD([sQuery(id+"F2.wireOp",EDGE,"E3.9.26.3")])],"isStart":false});
            var Q459;
            Q459=makeQuery(id+"F3.opExtrude","CAP_EDGE",EDGE,{"disambiguationData":[OSD([sQuery(id+"F2.wireOp",EDGE,"E2.1.3.3")])],"isStart":false});
            var Q460;
            Q460=makeQuery(id+"F3.opExtrude","CAP_EDGE",EDGE,{"disambiguationData":[OSD([sQuery(id+"F2.wireOp",EDGE,"E3.9.20.3")])],"isStart":false});
            var Q461;
            Q461=makeQuery(id+"F3.opExtrude","CAP_EDGE",EDGE,{"disambiguationData":[OSD([sQuery(id+"F2.wireOp",EDGE,"E3.9.27.3")])],"isStart":false});
            var Q462;
            Q462=makeQuery(id+"F3.opExtrude","CAP_EDGE",EDGE,{"disambiguationData":[OSD([sQuery(id+"F2.wireOp",EDGE,"E2.14.3.3")])],"isStart":false});
            var Q463;
            Q463=makeQuery(id+"F3.opExtrude","CAP_EDGE",EDGE,{"disambiguationData":[OSD([sQuery(id+"F2.wireOp",EDGE,"E3.9.21.3")])],"isStart":false});
            var Q464;
            Q464=makeQuery(id+"F3.opExtrude","CAP_EDGE",EDGE,{"disambiguationData":[OSD([sQuery(id+"F2.wireOp",EDGE,"E2.8.3.3")])],"isStart":false});
            var Q465;
            Q465=makeQuery(id+"F3.opExtrude","CAP_EDGE",EDGE,{"disambiguationData":[OSD([sQuery(id+"F2.wireOp",EDGE,"E2.15.3.3")])],"isStart":false});
            var Q466;
            Q466=makeQuery(id+"F3.opExtrude","CAP_EDGE",EDGE,{"disambiguationData":[OSD([sQuery(id+"F2.wireOp",EDGE,"E2.2.3.3")])],"isStart":false});
            var Q467;
            Q467=makeQuery(id+"F3.opExtrude","CAP_EDGE",EDGE,{"disambiguationData":[OSD([sQuery(id+"F2.wireOp",EDGE,"E2.9.3.3")])],"isStart":false});
            var Q468;
            Q468=makeQuery(id+"F3.opExtrude","CAP_EDGE",EDGE,{"disambiguationData":[OSD([sQuery(id+"F2.wireOp",EDGE,"E3.9.28.3")])],"isStart":false});
            var Q469;
            Q469=makeQuery(id+"F3.opExtrude","CAP_EDGE",EDGE,{"disambiguationData":[OSD([sQuery(id+"F2.wireOp",EDGE,"E3.9.22.3")])],"isStart":false});
            var Q470;
            Q470=makeQuery(id+"F3.opExtrude","CAP_EDGE",EDGE,{"disambiguationData":[OSD([sQuery(id+"F2.wireOp",EDGE,"E2.17.3.3")])],"isStart":false});
            var Q471;
            Q471=makeQuery(id+"F3.opExtrude","CAP_EDGE",EDGE,{"disambiguationData":[OSD([sQuery(id+"F2.wireOp",EDGE,"E2.11.3.3")])],"isStart":false});
            var Q472;
            Q472=makeQuery(id+"F3.opExtrude","CAP_EDGE",EDGE,{"disambiguationData":[OSD([sQuery(id+"F2.wireOp",EDGE,"E2.5.3.3")])],"isStart":false});
            var Q473;
            Q473=makeQuery(id+"F3.opExtrude","CAP_EDGE",EDGE,{"disambiguationData":[OSD([sQuery(id+"F2.wireOp",EDGE,"E3.9.24.3")])],"isStart":false});
            var Q474;
            Q474=makeQuery(id+"F3.opExtrude","CAP_EDGE",EDGE,{"disambiguationData":[OSD([sQuery(id+"F2.wireOp",EDGE,"E2.18.3.3")])],"isStart":false});
            var Q475;
            Q475=makeQuery(id+"F3.opExtrude","CAP_EDGE",EDGE,{"disambiguationData":[OSD([sQuery(id+"F2.wireOp",EDGE,"E3.9.25.3")])],"isStart":false});
            var Q476;
            Q476=makeQuery(id+"F3.opExtrude","CAP_EDGE",EDGE,{"disambiguationData":[OSD([sQuery(id+"F2.wireOp",EDGE,"E2.12.3.3")])],"isStart":false});
            var Q477;
            Q477=makeQuery(id+"F3.opExtrude","CAP_EDGE",EDGE,{"disambiguationData":[OSD([sQuery(id+"F2.wireOp",EDGE,"E2.19.3.3")])],"isStart":false});
            var Q478;
            Q478=makeQuery(id+"F3.opExtrude","CAP_EDGE",EDGE,{"disambiguationData":[OSD([sQuery(id+"F2.wireOp",EDGE,"E2.6.3.3")])],"isStart":false});
            var Q479;
            Q479=makeQuery(id+"F3.opExtrude","CAP_EDGE",EDGE,{"disambiguationData":[OSD([sQuery(id+"F2.wireOp",EDGE,"E2.13.3.3")])],"isStart":false});
            var Q480;
            Q480=makeQuery(id+"F3.opExtrude","CAP_EDGE",EDGE,{"disambiguationData":[OSD([sQuery(id+"F2.wireOp",EDGE,"E2.0.4.3")])],"isStart":false});
            var Q481;
            Q481=makeQuery(id+"F3.opExtrude","CAP_EDGE",EDGE,{"disambiguationData":[OSD([sQuery(id+"F2.wireOp",EDGE,"E2.0.4.0")])],"isStart":false});
            var Q482;
            Q482=makeQuery(id+"F3.opExtrude","CAP_EDGE",EDGE,{"disambiguationData":[OSD([sQuery(id+"F2.wireOp",EDGE,"E2.0.4.2")])],"isStart":false});
            var Q483;
            Q483=makeQuery(id+"F3.opExtrude","CAP_EDGE",EDGE,{"disambiguationData":[OSD([sQuery(id+"F2.wireOp",EDGE,"E3.9.23.4")])],"isStart":false});
            var Q484;
            Q484=makeQuery(id+"F3.opExtrude","CAP_EDGE",EDGE,{"disambiguationData":[OSD([sQuery(id+"F2.wireOp",EDGE,"E2.3.4.3")])],"isStart":false});
            var Q485;
            Q485=makeQuery(id+"F3.opExtrude","CAP_EDGE",EDGE,{"disambiguationData":[OSD([sQuery(id+"F2.wireOp",EDGE,"E3.9.22.4")])],"isStart":false});
            var Q486;
            Q486=makeQuery(id+"F3.opExtrude","CAP_EDGE",EDGE,{"disambiguationData":[OSD([sQuery(id+"F2.wireOp",EDGE,"E2.19.4.3")])],"isStart":false});
            var Q487;
            Q487=makeQuery(id+"F3.opExtrude","CAP_EDGE",EDGE,{"disambiguationData":[OSD([sQuery(id+"F2.wireOp",EDGE,"E2.6.4.3")])],"isStart":false});
            var Q488;
            Q488=makeQuery(id+"F3.opExtrude","CAP_EDGE",EDGE,{"disambiguationData":[OSD([sQuery(id+"F2.wireOp",EDGE,"E3.9.26.4")])],"isStart":false});
            var Q489;
            Q489=makeQuery(id+"F3.opExtrude","CAP_EDGE",EDGE,{"disambiguationData":[OSD([sQuery(id+"F2.wireOp",EDGE,"E2.13.4.3")])],"isStart":false});
            var Q490;
            Q490=makeQuery(id+"F3.opExtrude","CAP_EDGE",EDGE,{"disambiguationData":[OSD([sQuery(id+"F2.wireOp",EDGE,"E3.9.20.4")])],"isStart":false});
            var Q491;
            Q491=makeQuery(id+"F3.opExtrude","CAP_EDGE",EDGE,{"disambiguationData":[OSD([sQuery(id+"F2.wireOp",EDGE,"E2.1.4.3")])],"isStart":false});
            var Q492;
            Q492=makeQuery(id+"F3.opExtrude","CAP_EDGE",EDGE,{"disambiguationData":[OSD([sQuery(id+"F2.wireOp",EDGE,"E2.7.4.3")])],"isStart":false});
            var Q493;
            Q493=makeQuery(id+"F3.opExtrude","CAP_EDGE",EDGE,{"disambiguationData":[OSD([sQuery(id+"F2.wireOp",EDGE,"E3.9.27.4")])],"isStart":false});
            var Q494;
            Q494=makeQuery(id+"F3.opExtrude","CAP_EDGE",EDGE,{"disambiguationData":[OSD([sQuery(id+"F2.wireOp",EDGE,"E2.14.4.3")])],"isStart":false});
            var Q495;
            Q495=makeQuery(id+"F3.opExtrude","CAP_EDGE",EDGE,{"disambiguationData":[OSD([sQuery(id+"F2.wireOp",EDGE,"E3.9.21.4")])],"isStart":false});
            var Q496;
            Q496=makeQuery(id+"F3.opExtrude","CAP_EDGE",EDGE,{"disambiguationData":[OSD([sQuery(id+"F2.wireOp",EDGE,"E2.8.4.3")])],"isStart":false});
            var Q497;
            Q497=makeQuery(id+"F3.opExtrude","CAP_EDGE",EDGE,{"disambiguationData":[OSD([sQuery(id+"F2.wireOp",EDGE,"E2.15.4.3")])],"isStart":false});
            var Q498;
            Q498=makeQuery(id+"F3.opExtrude","CAP_EDGE",EDGE,{"disambiguationData":[OSD([sQuery(id+"F2.wireOp",EDGE,"E2.2.4.3")])],"isStart":false});
            var Q499;
            Q499=makeQuery(id+"F3.opExtrude","CAP_EDGE",EDGE,{"disambiguationData":[OSD([sQuery(id+"F2.wireOp",EDGE,"E3.9.29.4")])],"isStart":false});
            var Q500;
            Q500=makeQuery(id+"F3.opExtrude","CAP_EDGE",EDGE,{"disambiguationData":[OSD([sQuery(id+"F2.wireOp",EDGE,"E2.16.4.3")])],"isStart":false});
            var Q501;
            Q501=makeQuery(id+"F3.opExtrude","CAP_EDGE",EDGE,{"disambiguationData":[OSD([sQuery(id+"F2.wireOp",EDGE,"E2.10.4.3")])],"isStart":false});
            var Q502;
            Q502=makeQuery(id+"F3.opExtrude","CAP_EDGE",EDGE,{"disambiguationData":[OSD([sQuery(id+"F2.wireOp",EDGE,"E2.17.4.3")])],"isStart":false});
            var Q503;
            Q503=makeQuery(id+"F3.opExtrude","CAP_EDGE",EDGE,{"disambiguationData":[OSD([sQuery(id+"F2.wireOp",EDGE,"E2.4.4.3")])],"isStart":false});
            var Q504;
            Q504=makeQuery(id+"F3.opExtrude","CAP_EDGE",EDGE,{"disambiguationData":[OSD([sQuery(id+"F2.wireOp",EDGE,"E2.11.4.3")])],"isStart":false});
            var Q505;
            Q505=makeQuery(id+"F3.opExtrude","CAP_EDGE",EDGE,{"disambiguationData":[OSD([sQuery(id+"F2.wireOp",EDGE,"E2.5.4.3")])],"isStart":false});
            var Q506;
            Q506=makeQuery(id+"F3.opExtrude","CAP_EDGE",EDGE,{"disambiguationData":[OSD([sQuery(id+"F2.wireOp",EDGE,"E3.9.24.4")])],"isStart":false});
            var Q507;
            Q507=makeQuery(id+"F3.opExtrude","CAP_EDGE",EDGE,{"disambiguationData":[OSD([sQuery(id+"F2.wireOp",EDGE,"E2.18.4.3")])],"isStart":false});
            var Q508;
            Q508=makeQuery(id+"F3.opExtrude","CAP_EDGE",EDGE,{"disambiguationData":[OSD([sQuery(id+"F2.wireOp",EDGE,"E3.9.25.4")])],"isStart":false});
            var Q509;
            Q509=makeQuery(id+"F3.opExtrude","CAP_EDGE",EDGE,{"disambiguationData":[OSD([sQuery(id+"F2.wireOp",EDGE,"E2.12.4.3")])],"isStart":false});
            var Q510;
            Q510=makeQuery(id+"F3.opExtrude","CAP_EDGE",EDGE,{"disambiguationData":[OSD([sQuery(id+"F2.wireOp",EDGE,"E3.0.23.4")])],"isStart":false});
            var Q511;
            Q511=makeQuery(id+"F3.opExtrude","CAP_EDGE",EDGE,{"disambiguationData":[OSD([sQuery(id+"F2.wireOp",EDGE,"E3.0.22.4")])],"isStart":false});
            var Q512;
            Q512=makeQuery(id+"F3.opExtrude","CAP_EDGE",EDGE,{"disambiguationData":[OSD([sQuery(id+"F2.wireOp",EDGE,"E2.16.4.0")])],"isStart":false});
            var Q513;
            Q513=makeQuery(id+"F3.opExtrude","CAP_EDGE",EDGE,{"disambiguationData":[OSD([sQuery(id+"F2.wireOp",EDGE,"E2.3.4.0")])],"isStart":false});
            var Q514;
            Q514=makeQuery(id+"F3.opExtrude","CAP_EDGE",EDGE,{"disambiguationData":[OSD([sQuery(id+"F2.wireOp",EDGE,"E2.10.4.0")])],"isStart":false});
            var Q515;
            Q515=makeQuery(id+"F3.opExtrude","CAP_EDGE",EDGE,{"disambiguationData":[OSD([sQuery(id+"F2.wireOp",EDGE,"E3.0.29.4")])],"isStart":false});
            var Q516;
            Q516=makeQuery(id+"F3.opExtrude","CAP_EDGE",EDGE,{"disambiguationData":[OSD([sQuery(id+"F2.wireOp",EDGE,"E2.9.4.3")])],"isStart":false});
            var Q517;
            Q517=makeQuery(id+"F3.opExtrude","CAP_EDGE",EDGE,{"disambiguationData":[OSD([sQuery(id+"F2.wireOp",EDGE,"E3.9.28.4")])],"isStart":false});
            var Q518;
            Q518=makeQuery(id+"F3.opExtrude","CAP_EDGE",EDGE,{"disambiguationData":[OSD([sQuery(id+"F2.wireOp",EDGE,"E2.13.4.0")])],"isStart":false});
            var Q519;
            Q519=makeQuery(id+"F3.opExtrude","CAP_EDGE",EDGE,{"disambiguationData":[OSD([sQuery(id+"F2.wireOp",EDGE,"E2.7.4.0")])],"isStart":false});
            var Q520;
            Q520=makeQuery(id+"F3.opExtrude","CAP_EDGE",EDGE,{"disambiguationData":[OSD([sQuery(id+"F2.wireOp",EDGE,"E3.0.26.4")])],"isStart":false});
            var Q521;
            Q521=makeQuery(id+"F3.opExtrude","CAP_EDGE",EDGE,{"disambiguationData":[OSD([sQuery(id+"F2.wireOp",EDGE,"E2.1.4.0")])],"isStart":false});
            var Q522;
            Q522=makeQuery(id+"F3.opExtrude","CAP_EDGE",EDGE,{"disambiguationData":[OSD([sQuery(id+"F2.wireOp",EDGE,"E3.0.20.4")])],"isStart":false});
            var Q523;
            Q523=makeQuery(id+"F3.opExtrude","CAP_EDGE",EDGE,{"disambiguationData":[OSD([sQuery(id+"F2.wireOp",EDGE,"E3.0.27.4")])],"isStart":false});
            var Q524;
            Q524=makeQuery(id+"F3.opExtrude","CAP_EDGE",EDGE,{"disambiguationData":[OSD([sQuery(id+"F2.wireOp",EDGE,"E2.14.4.0")])],"isStart":false});
            var Q525;
            Q525=makeQuery(id+"F3.opExtrude","CAP_EDGE",EDGE,{"disambiguationData":[OSD([sQuery(id+"F2.wireOp",EDGE,"E3.0.21.4")])],"isStart":false});
            var Q526;
            Q526=makeQuery(id+"F3.opExtrude","CAP_EDGE",EDGE,{"disambiguationData":[OSD([sQuery(id+"F2.wireOp",EDGE,"E2.8.4.0")])],"isStart":false});
            var Q527;
            Q527=makeQuery(id+"F3.opExtrude","CAP_EDGE",EDGE,{"disambiguationData":[OSD([sQuery(id+"F2.wireOp",EDGE,"E2.15.4.0")])],"isStart":false});
            var Q528;
            Q528=makeQuery(id+"F3.opExtrude","CAP_EDGE",EDGE,{"disambiguationData":[OSD([sQuery(id+"F2.wireOp",EDGE,"E2.2.4.0")])],"isStart":false});
            var Q529;
            Q529=makeQuery(id+"F3.opExtrude","CAP_EDGE",EDGE,{"disambiguationData":[OSD([sQuery(id+"F2.wireOp",EDGE,"E2.9.4.0")])],"isStart":false});
            var Q530;
            Q530=makeQuery(id+"F3.opExtrude","CAP_EDGE",EDGE,{"disambiguationData":[OSD([sQuery(id+"F2.wireOp",EDGE,"E3.0.28.4")])],"isStart":false});
            var Q531;
            Q531=makeQuery(id+"F3.opExtrude","CAP_EDGE",EDGE,{"disambiguationData":[OSD([sQuery(id+"F2.wireOp",EDGE,"E2.17.4.0")])],"isStart":false});
            var Q532;
            Q532=makeQuery(id+"F3.opExtrude","CAP_EDGE",EDGE,{"disambiguationData":[OSD([sQuery(id+"F2.wireOp",EDGE,"E2.4.4.0")])],"isStart":false});
            var Q533;
            Q533=makeQuery(id+"F3.opExtrude","CAP_EDGE",EDGE,{"disambiguationData":[OSD([sQuery(id+"F2.wireOp",EDGE,"E2.11.4.0")])],"isStart":false});
            var Q534;
            Q534=makeQuery(id+"F3.opExtrude","CAP_EDGE",EDGE,{"disambiguationData":[OSD([sQuery(id+"F2.wireOp",EDGE,"E2.5.4.0")])],"isStart":false});
            var Q535;
            Q535=makeQuery(id+"F3.opExtrude","CAP_EDGE",EDGE,{"disambiguationData":[OSD([sQuery(id+"F2.wireOp",EDGE,"E3.0.24.4")])],"isStart":false});
            var Q536;
            Q536=makeQuery(id+"F3.opExtrude","CAP_EDGE",EDGE,{"disambiguationData":[OSD([sQuery(id+"F2.wireOp",EDGE,"E2.12.4.0")])],"isStart":false});
            var Q537;
            Q537=makeQuery(id+"F3.opExtrude","CAP_EDGE",EDGE,{"disambiguationData":[OSD([sQuery(id+"F2.wireOp",EDGE,"E2.18.4.0")])],"isStart":false});
            var Q538;
            Q538=makeQuery(id+"F3.opExtrude","CAP_EDGE",EDGE,{"disambiguationData":[OSD([sQuery(id+"F2.wireOp",EDGE,"E2.6.4.0")])],"isStart":false});
            var Q539;
            Q539=makeQuery(id+"F3.opExtrude","CAP_EDGE",EDGE,{"disambiguationData":[OSD([sQuery(id+"F2.wireOp",EDGE,"E3.0.25.4")])],"isStart":false});
            var Q540;
            Q540=makeQuery(id+"F3.opExtrude","CAP_EDGE",EDGE,{"disambiguationData":[OSD([sQuery(id+"F2.wireOp",EDGE,"E2.19.4.0")])],"isStart":false});
            var Q541;
            Q541=makeQuery(id+"F3.opExtrude","CAP_EDGE",EDGE,{"disambiguationData":[OSD([sQuery(id+"F2.wireOp",EDGE,"E2.0.4.1")])],"isStart":false});
            var Q542;
            Q542=makeQuery(id+"F3.opExtrude","CAP_EDGE",EDGE,{"disambiguationData":[OSD([sQuery(id+"F2.wireOp",EDGE,"E2.10.4.2")])],"isStart":false});
            var Q543;
            Q543=makeQuery(id+"F3.opExtrude","CAP_EDGE",EDGE,{"disambiguationData":[OSD([sQuery(id+"F2.wireOp",EDGE,"E2.17.4.2")])],"isStart":false});
            var Q544;
            Q544=makeQuery(id+"F3.opExtrude","CAP_EDGE",EDGE,{"disambiguationData":[OSD([sQuery(id+"F2.wireOp",EDGE,"E2.4.4.2")])],"isStart":false});
            var Q545;
            Q545=makeQuery(id+"F3.opExtrude","CAP_EDGE",EDGE,{"disambiguationData":[OSD([sQuery(id+"F2.wireOp",EDGE,"E2.11.4.2")])],"isStart":false});
            var Q546;
            Q546=makeQuery(id+"F3.opExtrude","CAP_EDGE",EDGE,{"disambiguationData":[OSD([sQuery(id+"F2.wireOp",EDGE,"E2.5.4.2")])],"isStart":false});
            var Q547;
            Q547=makeQuery(id+"F3.opExtrude","CAP_EDGE",EDGE,{"disambiguationData":[OSD([sQuery(id+"F2.wireOp",EDGE,"E3.6.24.4")])],"isStart":false});
            var Q548;
            Q548=makeQuery(id+"F3.opExtrude","CAP_EDGE",EDGE,{"disambiguationData":[OSD([sQuery(id+"F2.wireOp",EDGE,"E2.18.4.2")])],"isStart":false});
            var Q549;
            Q549=makeQuery(id+"F3.opExtrude","CAP_EDGE",EDGE,{"disambiguationData":[OSD([sQuery(id+"F2.wireOp",EDGE,"E3.6.25.4")])],"isStart":false});
            var Q550;
            Q550=makeQuery(id+"F3.opExtrude","CAP_EDGE",EDGE,{"disambiguationData":[OSD([sQuery(id+"F2.wireOp",EDGE,"E2.12.4.2")])],"isStart":false});
            var Q551;
            Q551=makeQuery(id+"F3.opExtrude","CAP_EDGE",EDGE,{"disambiguationData":[OSD([sQuery(id+"F2.wireOp",EDGE,"E2.19.4.2")])],"isStart":false});
            var Q552;
            Q552=makeQuery(id+"F3.opExtrude","CAP_EDGE",EDGE,{"disambiguationData":[OSD([sQuery(id+"F2.wireOp",EDGE,"E2.6.4.2")])],"isStart":false});
            var Q553;
            Q553=makeQuery(id+"F3.opExtrude","CAP_EDGE",EDGE,{"disambiguationData":[OSD([sQuery(id+"F2.wireOp",EDGE,"E3.6.23.4")])],"isStart":false});
            var Q554;
            Q554=makeQuery(id+"F3.opExtrude","CAP_EDGE",EDGE,{"disambiguationData":[OSD([sQuery(id+"F2.wireOp",EDGE,"E2.3.4.2")])],"isStart":false});
            var Q555;
            Q555=makeQuery(id+"F3.opExtrude","CAP_EDGE",EDGE,{"disambiguationData":[OSD([sQuery(id+"F2.wireOp",EDGE,"E3.6.22.4")])],"isStart":false});
            var Q556;
            Q556=makeQuery(id+"F3.opExtrude","CAP_EDGE",EDGE,{"disambiguationData":[OSD([sQuery(id+"F2.wireOp",EDGE,"E3.6.29.4")])],"isStart":false});
            var Q557;
            Q557=makeQuery(id+"F3.opExtrude","CAP_EDGE",EDGE,{"disambiguationData":[OSD([sQuery(id+"F2.wireOp",EDGE,"E2.16.4.2")])],"isStart":false});
            var Q558;
            Q558=makeQuery(id+"F3.opExtrude","CAP_EDGE",EDGE,{"disambiguationData":[OSD([sQuery(id+"F2.wireOp",EDGE,"E2.13.4.2")])],"isStart":false});
            var Q559;
            Q559=makeQuery(id+"F3.opExtrude","CAP_EDGE",EDGE,{"disambiguationData":[OSD([sQuery(id+"F2.wireOp",EDGE,"E2.7.4.2")])],"isStart":false});
            var Q560;
            Q560=makeQuery(id+"F3.opExtrude","CAP_EDGE",EDGE,{"disambiguationData":[OSD([sQuery(id+"F2.wireOp",EDGE,"E3.6.26.4")])],"isStart":false});
            var Q561;
            Q561=makeQuery(id+"F3.opExtrude","CAP_EDGE",EDGE,{"disambiguationData":[OSD([sQuery(id+"F2.wireOp",EDGE,"E2.1.4.2")])],"isStart":false});
            var Q562;
            Q562=makeQuery(id+"F3.opExtrude","CAP_EDGE",EDGE,{"disambiguationData":[OSD([sQuery(id+"F2.wireOp",EDGE,"E3.6.20.4")])],"isStart":false});
            var Q563;
            Q563=makeQuery(id+"F3.opExtrude","CAP_EDGE",EDGE,{"disambiguationData":[OSD([sQuery(id+"F2.wireOp",EDGE,"E3.6.27.4")])],"isStart":false});
            var Q564;
            Q564=makeQuery(id+"F3.opExtrude","CAP_EDGE",EDGE,{"disambiguationData":[OSD([sQuery(id+"F2.wireOp",EDGE,"E2.14.4.2")])],"isStart":false});
            var Q565;
            Q565=makeQuery(id+"F3.opExtrude","CAP_EDGE",EDGE,{"disambiguationData":[OSD([sQuery(id+"F2.wireOp",EDGE,"E3.6.21.4")])],"isStart":false});
            var Q566;
            Q566=makeQuery(id+"F3.opExtrude","CAP_EDGE",EDGE,{"disambiguationData":[OSD([sQuery(id+"F2.wireOp",EDGE,"E2.8.4.2")])],"isStart":false});
            var Q567;
            Q567=makeQuery(id+"F3.opExtrude","CAP_EDGE",EDGE,{"disambiguationData":[OSD([sQuery(id+"F2.wireOp",EDGE,"E2.15.4.2")])],"isStart":false});
            var Q568;
            Q568=makeQuery(id+"F3.opExtrude","CAP_EDGE",EDGE,{"disambiguationData":[OSD([sQuery(id+"F2.wireOp",EDGE,"E2.2.4.2")])],"isStart":false});
            var Q569;
            Q569=makeQuery(id+"F3.opExtrude","CAP_EDGE",EDGE,{"disambiguationData":[OSD([sQuery(id+"F2.wireOp",EDGE,"E2.9.4.2")])],"isStart":false});
            var Q570;
            Q570=makeQuery(id+"F3.opExtrude","CAP_EDGE",EDGE,{"disambiguationData":[OSD([sQuery(id+"F2.wireOp",EDGE,"E3.6.28.4")])],"isStart":false});
            var Q571;
            Q571=makeQuery(id+"F3.opExtrude","CAP_EDGE",EDGE,{"disambiguationData":[OSD([sQuery(id+"F2.wireOp",EDGE,"E3.3.23.4")])],"isStart":false});
            var Q572;
            Q572=makeQuery(id+"F3.opExtrude","CAP_EDGE",EDGE,{"disambiguationData":[OSD([sQuery(id+"F2.wireOp",EDGE,"E2.3.4.1")])],"isStart":false});
            var Q573;
            Q573=makeQuery(id+"F3.opExtrude","CAP_EDGE",EDGE,{"disambiguationData":[OSD([sQuery(id+"F2.wireOp",EDGE,"E3.3.22.4")])],"isStart":false});
            var Q574;
            Q574=makeQuery(id+"F3.opExtrude","CAP_EDGE",EDGE,{"disambiguationData":[OSD([sQuery(id+"F2.wireOp",EDGE,"E3.3.29.4")])],"isStart":false});
            var Q575;
            Q575=makeQuery(id+"F3.opExtrude","CAP_EDGE",EDGE,{"disambiguationData":[OSD([sQuery(id+"F2.wireOp",EDGE,"E2.10.4.1")])],"isStart":false});
            var Q576;
            Q576=makeQuery(id+"F3.opExtrude","CAP_EDGE",EDGE,{"disambiguationData":[OSD([sQuery(id+"F2.wireOp",EDGE,"E2.16.4.1")])],"isStart":false});
            var Q577;
            Q577=makeQuery(id+"F3.opExtrude","CAP_EDGE",EDGE,{"disambiguationData":[OSD([sQuery(id+"F2.wireOp",EDGE,"E2.17.4.1")])],"isStart":false});
            var Q578;
            Q578=makeQuery(id+"F3.opExtrude","CAP_EDGE",EDGE,{"disambiguationData":[OSD([sQuery(id+"F2.wireOp",EDGE,"E2.4.4.1")])],"isStart":false});
            var Q579;
            Q579=makeQuery(id+"F3.opExtrude","CAP_EDGE",EDGE,{"disambiguationData":[OSD([sQuery(id+"F2.wireOp",EDGE,"E2.11.4.1")])],"isStart":false});
            var Q580;
            Q580=makeQuery(id+"F3.opExtrude","CAP_EDGE",EDGE,{"disambiguationData":[OSD([sQuery(id+"F2.wireOp",EDGE,"E3.3.27.4")])],"isStart":false});
            var Q581;
            Q581=makeQuery(id+"F3.opExtrude","CAP_EDGE",EDGE,{"disambiguationData":[OSD([sQuery(id+"F2.wireOp",EDGE,"E2.14.4.1")])],"isStart":false});
            var Q582;
            Q582=makeQuery(id+"F3.opExtrude","CAP_EDGE",EDGE,{"disambiguationData":[OSD([sQuery(id+"F2.wireOp",EDGE,"E3.3.21.4")])],"isStart":false});
            var Q583;
            Q583=makeQuery(id+"F3.opExtrude","CAP_EDGE",EDGE,{"disambiguationData":[OSD([sQuery(id+"F2.wireOp",EDGE,"E2.8.4.1")])],"isStart":false});
            var Q584;
            Q584=makeQuery(id+"F3.opExtrude","CAP_EDGE",EDGE,{"disambiguationData":[OSD([sQuery(id+"F2.wireOp",EDGE,"E2.15.4.1")])],"isStart":false});
            var Q585;
            Q585=makeQuery(id+"F3.opExtrude","CAP_EDGE",EDGE,{"disambiguationData":[OSD([sQuery(id+"F2.wireOp",EDGE,"E2.2.4.1")])],"isStart":false});
            var Q586;
            Q586=makeQuery(id+"F3.opExtrude","CAP_EDGE",EDGE,{"disambiguationData":[OSD([sQuery(id+"F2.wireOp",EDGE,"E2.9.4.1")])],"isStart":false});
            var Q587;
            Q587=makeQuery(id+"F3.opExtrude","CAP_EDGE",EDGE,{"disambiguationData":[OSD([sQuery(id+"F2.wireOp",EDGE,"E3.3.28.4")])],"isStart":false});
            var Q588;
            Q588=makeQuery(id+"F3.opExtrude","CAP_EDGE",EDGE,{"disambiguationData":[OSD([sQuery(id+"F2.wireOp",EDGE,"E2.5.4.1")])],"isStart":false});
            var Q589;
            Q589=makeQuery(id+"F3.opExtrude","CAP_EDGE",EDGE,{"disambiguationData":[OSD([sQuery(id+"F2.wireOp",EDGE,"E3.3.24.4")])],"isStart":false});
            var Q590;
            Q590=makeQuery(id+"F3.opExtrude","CAP_EDGE",EDGE,{"disambiguationData":[OSD([sQuery(id+"F2.wireOp",EDGE,"E2.18.4.1")])],"isStart":false});
            var Q591;
            Q591=makeQuery(id+"F3.opExtrude","CAP_EDGE",EDGE,{"disambiguationData":[OSD([sQuery(id+"F2.wireOp",EDGE,"E3.3.25.4")])],"isStart":false});
            var Q592;
            Q592=makeQuery(id+"F3.opExtrude","CAP_EDGE",EDGE,{"disambiguationData":[OSD([sQuery(id+"F2.wireOp",EDGE,"E2.6.4.1")])],"isStart":false});
            var Q593;
            Q593=makeQuery(id+"F3.opExtrude","CAP_EDGE",EDGE,{"disambiguationData":[OSD([sQuery(id+"F2.wireOp",EDGE,"E2.12.4.1")])],"isStart":false});
            var Q594;
            Q594=makeQuery(id+"F3.opExtrude","CAP_EDGE",EDGE,{"disambiguationData":[OSD([sQuery(id+"F2.wireOp",EDGE,"E2.19.4.1")])],"isStart":false});
            var Q595;
            Q595=makeQuery(id+"F3.opExtrude","CAP_EDGE",EDGE,{"disambiguationData":[OSD([sQuery(id+"F2.wireOp",EDGE,"E2.13.4.1")])],"isStart":false});
            var Q596;
            Q596=makeQuery(id+"F3.opExtrude","CAP_EDGE",EDGE,{"disambiguationData":[OSD([sQuery(id+"F2.wireOp",EDGE,"E2.7.4.1")])],"isStart":false});
            var Q597;
            Q597=makeQuery(id+"F3.opExtrude","CAP_EDGE",EDGE,{"disambiguationData":[OSD([sQuery(id+"F2.wireOp",EDGE,"E3.3.26.4")])],"isStart":false});
            var Q598;
            Q598=makeQuery(id+"F3.opExtrude","CAP_EDGE",EDGE,{"disambiguationData":[OSD([sQuery(id+"F2.wireOp",EDGE,"E2.1.4.1")])],"isStart":false});
            var Q599;
            Q599=makeQuery(id+"F3.opExtrude","CAP_EDGE",EDGE,{"disambiguationData":[OSD([sQuery(id+"F2.wireOp",EDGE,"E3.3.20.4")])],"isStart":false});
            var Q600;
            Q600=makeQuery(id+"F3.opExtrude","CAP_EDGE",EDGE,{"disambiguationData":[OSD([sQuery(id+"F2.wireOp",EDGE,"E2.0.5.0")])],"isStart":false});
            var Q601;
            Q601=makeQuery(id+"F3.opExtrude","CAP_EDGE",EDGE,{"disambiguationData":[OSD([sQuery(id+"F2.wireOp",EDGE,"E2.0.5.2")])],"isStart":false});
            var Q602;
            Q602=makeQuery(id+"F3.opExtrude","CAP_EDGE",EDGE,{"disambiguationData":[OSD([sQuery(id+"F2.wireOp",EDGE,"E3.0.23.5")])],"isStart":false});
            var Q603;
            Q603=makeQuery(id+"F3.opExtrude","CAP_EDGE",EDGE,{"disambiguationData":[OSD([sQuery(id+"F2.wireOp",EDGE,"E2.3.5.0")])],"isStart":false});
            var Q604;
            Q604=makeQuery(id+"F3.opExtrude","CAP_EDGE",EDGE,{"disambiguationData":[OSD([sQuery(id+"F2.wireOp",EDGE,"E3.0.22.5")])],"isStart":false});
            var Q605;
            Q605=makeQuery(id+"F3.opExtrude","CAP_EDGE",EDGE,{"disambiguationData":[OSD([sQuery(id+"F2.wireOp",EDGE,"E3.0.29.5")])],"isStart":false});
            var Q606;
            Q606=makeQuery(id+"F3.opExtrude","CAP_EDGE",EDGE,{"disambiguationData":[OSD([sQuery(id+"F2.wireOp",EDGE,"E2.16.5.0")])],"isStart":false});
            var Q607;
            Q607=makeQuery(id+"F3.opExtrude","CAP_EDGE",EDGE,{"disambiguationData":[OSD([sQuery(id+"F2.wireOp",EDGE,"E2.10.5.0")])],"isStart":false});
            var Q608;
            Q608=makeQuery(id+"F3.opExtrude","CAP_EDGE",EDGE,{"disambiguationData":[OSD([sQuery(id+"F2.wireOp",EDGE,"E2.17.5.0")])],"isStart":false});
            var Q609;
            Q609=makeQuery(id+"F3.opExtrude","CAP_EDGE",EDGE,{"disambiguationData":[OSD([sQuery(id+"F2.wireOp",EDGE,"E2.4.5.0")])],"isStart":false});
            var Q610;
            Q610=makeQuery(id+"F3.opExtrude","CAP_EDGE",EDGE,{"disambiguationData":[OSD([sQuery(id+"F2.wireOp",EDGE,"E3.0.20.5")])],"isStart":false});
            var Q611;
            Q611=makeQuery(id+"F3.opExtrude","CAP_EDGE",EDGE,{"disambiguationData":[OSD([sQuery(id+"F2.wireOp",EDGE,"E2.7.5.0")])],"isStart":false});
            var Q612;
            Q612=makeQuery(id+"F3.opExtrude","CAP_EDGE",EDGE,{"disambiguationData":[OSD([sQuery(id+"F2.wireOp",EDGE,"E2.14.5.0")])],"isStart":false});
            var Q613;
            Q613=makeQuery(id+"F3.opExtrude","CAP_EDGE",EDGE,{"disambiguationData":[OSD([sQuery(id+"F2.wireOp",EDGE,"E2.1.5.0")])],"isStart":false});
            var Q614;
            Q614=makeQuery(id+"F3.opExtrude","CAP_EDGE",EDGE,{"disambiguationData":[OSD([sQuery(id+"F2.wireOp",EDGE,"E2.8.5.0")])],"isStart":false});
            var Q615;
            Q615=makeQuery(id+"F3.opExtrude","CAP_EDGE",EDGE,{"disambiguationData":[OSD([sQuery(id+"F2.wireOp",EDGE,"E3.0.27.5")])],"isStart":false});
            var Q616;
            Q616=makeQuery(id+"F3.opExtrude","CAP_EDGE",EDGE,{"disambiguationData":[OSD([sQuery(id+"F2.wireOp",EDGE,"E2.15.5.0")])],"isStart":false});
            var Q617;
            Q617=makeQuery(id+"F3.opExtrude","CAP_EDGE",EDGE,{"disambiguationData":[OSD([sQuery(id+"F2.wireOp",EDGE,"E3.0.21.5")])],"isStart":false});
            var Q618;
            Q618=makeQuery(id+"F3.opExtrude","CAP_EDGE",EDGE,{"disambiguationData":[OSD([sQuery(id+"F2.wireOp",EDGE,"E2.2.5.0")])],"isStart":false});
            var Q619;
            Q619=makeQuery(id+"F3.opExtrude","CAP_EDGE",EDGE,{"disambiguationData":[OSD([sQuery(id+"F2.wireOp",EDGE,"E2.9.5.0")])],"isStart":false});
            var Q620;
            Q620=makeQuery(id+"F3.opExtrude","CAP_EDGE",EDGE,{"disambiguationData":[OSD([sQuery(id+"F2.wireOp",EDGE,"E3.0.28.5")])],"isStart":false});
            var Q621;
            Q621=makeQuery(id+"F3.opExtrude","CAP_EDGE",EDGE,{"disambiguationData":[OSD([sQuery(id+"F2.wireOp",EDGE,"E2.11.5.0")])],"isStart":false});
            var Q622;
            Q622=makeQuery(id+"F3.opExtrude","CAP_EDGE",EDGE,{"disambiguationData":[OSD([sQuery(id+"F2.wireOp",EDGE,"E2.5.5.0")])],"isStart":false});
            var Q623;
            Q623=makeQuery(id+"F3.opExtrude","CAP_EDGE",EDGE,{"disambiguationData":[OSD([sQuery(id+"F2.wireOp",EDGE,"E3.0.24.5")])],"isStart":false});
            var Q624;
            Q624=makeQuery(id+"F3.opExtrude","CAP_EDGE",EDGE,{"disambiguationData":[OSD([sQuery(id+"F2.wireOp",EDGE,"E2.18.5.0")])],"isStart":false});
            var Q625;
            Q625=makeQuery(id+"F3.opExtrude","CAP_EDGE",EDGE,{"disambiguationData":[OSD([sQuery(id+"F2.wireOp",EDGE,"E3.0.25.5")])],"isStart":false});
            var Q626;
            Q626=makeQuery(id+"F3.opExtrude","CAP_EDGE",EDGE,{"disambiguationData":[OSD([sQuery(id+"F2.wireOp",EDGE,"E2.12.5.0")])],"isStart":false});
            var Q627;
            Q627=makeQuery(id+"F3.opExtrude","CAP_EDGE",EDGE,{"disambiguationData":[OSD([sQuery(id+"F2.wireOp",EDGE,"E2.19.5.0")])],"isStart":false});
            var Q628;
            Q628=makeQuery(id+"F3.opExtrude","CAP_EDGE",EDGE,{"disambiguationData":[OSD([sQuery(id+"F2.wireOp",EDGE,"E2.6.5.0")])],"isStart":false});
            var Q629;
            Q629=makeQuery(id+"F3.opExtrude","CAP_EDGE",EDGE,{"disambiguationData":[OSD([sQuery(id+"F2.wireOp",EDGE,"E3.0.26.5")])],"isStart":false});
            var Q630;
            Q630=makeQuery(id+"F3.opExtrude","CAP_EDGE",EDGE,{"disambiguationData":[OSD([sQuery(id+"F2.wireOp",EDGE,"E2.13.5.0")])],"isStart":false});
            var Q631;
            Q631=makeQuery(id+"F3.opExtrude","CAP_EDGE",EDGE,{"disambiguationData":[OSD([sQuery(id+"F2.wireOp",EDGE,"E3.6.23.5")])],"isStart":false});
            var Q632;
            Q632=makeQuery(id+"F3.opExtrude","CAP_EDGE",EDGE,{"disambiguationData":[OSD([sQuery(id+"F2.wireOp",EDGE,"E3.6.25.5")])],"isStart":false});
            var Q633;
            Q633=makeQuery(id+"F3.opExtrude","CAP_EDGE",EDGE,{"disambiguationData":[OSD([sQuery(id+"F2.wireOp",EDGE,"E2.12.5.2")])],"isStart":false});
            var Q634;
            Q634=makeQuery(id+"F3.opExtrude","CAP_EDGE",EDGE,{"disambiguationData":[OSD([sQuery(id+"F2.wireOp",EDGE,"E2.19.5.2")])],"isStart":false});
            var Q635;
            Q635=makeQuery(id+"F3.opExtrude","CAP_EDGE",EDGE,{"disambiguationData":[OSD([sQuery(id+"F2.wireOp",EDGE,"E2.6.5.2")])],"isStart":false});
            var Q636;
            Q636=makeQuery(id+"F3.opExtrude","CAP_EDGE",EDGE,{"disambiguationData":[OSD([sQuery(id+"F2.wireOp",EDGE,"E3.6.26.5")])],"isStart":false});
            var Q637;
            Q637=makeQuery(id+"F3.opExtrude","CAP_EDGE",EDGE,{"disambiguationData":[OSD([sQuery(id+"F2.wireOp",EDGE,"E2.13.5.2")])],"isStart":false});
            var Q638;
            Q638=makeQuery(id+"F3.opExtrude","CAP_EDGE",EDGE,{"disambiguationData":[OSD([sQuery(id+"F2.wireOp",EDGE,"E3.6.20.5")])],"isStart":false});
            var Q639;
            Q639=makeQuery(id+"F3.opExtrude","CAP_EDGE",EDGE,{"disambiguationData":[OSD([sQuery(id+"F2.wireOp",EDGE,"E2.7.5.2")])],"isStart":false});
            var Q640;
            Q640=makeQuery(id+"F3.opExtrude","CAP_EDGE",EDGE,{"disambiguationData":[OSD([sQuery(id+"F2.wireOp",EDGE,"E2.14.5.2")])],"isStart":false});
            var Q641;
            Q641=makeQuery(id+"F3.opExtrude","CAP_EDGE",EDGE,{"disambiguationData":[OSD([sQuery(id+"F2.wireOp",EDGE,"E2.1.5.2")])],"isStart":false});
            var Q642;
            Q642=makeQuery(id+"F3.opExtrude","CAP_EDGE",EDGE,{"disambiguationData":[OSD([sQuery(id+"F2.wireOp",EDGE,"E2.8.5.2")])],"isStart":false});
            var Q643;
            Q643=makeQuery(id+"F3.opExtrude","CAP_EDGE",EDGE,{"disambiguationData":[OSD([sQuery(id+"F2.wireOp",EDGE,"E3.6.27.5")])],"isStart":false});
            var Q644;
            Q644=makeQuery(id+"F3.opExtrude","CAP_EDGE",EDGE,{"disambiguationData":[OSD([sQuery(id+"F2.wireOp",EDGE,"E2.3.5.2")])],"isStart":false});
            var Q645;
            Q645=makeQuery(id+"F3.opExtrude","CAP_EDGE",EDGE,{"disambiguationData":[OSD([sQuery(id+"F2.wireOp",EDGE,"E3.6.22.5")])],"isStart":false});
            var Q646;
            Q646=makeQuery(id+"F3.opExtrude","CAP_EDGE",EDGE,{"disambiguationData":[OSD([sQuery(id+"F2.wireOp",EDGE,"E3.6.29.5")])],"isStart":false});
            var Q647;
            Q647=makeQuery(id+"F3.opExtrude","CAP_EDGE",EDGE,{"disambiguationData":[OSD([sQuery(id+"F2.wireOp",EDGE,"E2.0.5.1")])],"isStart":false});
            var Q648;
            Q648=makeQuery(id+"F3.opExtrude","CAP_EDGE",EDGE,{"disambiguationData":[OSD([sQuery(id+"F2.wireOp",EDGE,"E2.16.5.2")])],"isStart":false});
            var Q649;
            Q649=makeQuery(id+"F3.opExtrude","CAP_EDGE",EDGE,{"disambiguationData":[OSD([sQuery(id+"F2.wireOp",EDGE,"E2.10.5.2")])],"isStart":false});
            var Q650;
            Q650=makeQuery(id+"F3.opExtrude","CAP_EDGE",EDGE,{"disambiguationData":[OSD([sQuery(id+"F2.wireOp",EDGE,"E2.17.5.2")])],"isStart":false});
            var Q651;
            Q651=makeQuery(id+"F3.opExtrude","CAP_EDGE",EDGE,{"disambiguationData":[OSD([sQuery(id+"F2.wireOp",EDGE,"E2.4.5.2")])],"isStart":false});
            var Q652;
            Q652=makeQuery(id+"F3.opExtrude","CAP_EDGE",EDGE,{"disambiguationData":[OSD([sQuery(id+"F2.wireOp",EDGE,"E2.11.5.2")])],"isStart":false});
            var Q653;
            Q653=makeQuery(id+"F3.opExtrude","CAP_EDGE",EDGE,{"disambiguationData":[OSD([sQuery(id+"F2.wireOp",EDGE,"E2.5.5.2")])],"isStart":false});
            var Q654;
            Q654=makeQuery(id+"F3.opExtrude","CAP_EDGE",EDGE,{"disambiguationData":[OSD([sQuery(id+"F2.wireOp",EDGE,"E3.6.24.5")])],"isStart":false});
            var Q655;
            Q655=makeQuery(id+"F3.opExtrude","CAP_EDGE",EDGE,{"disambiguationData":[OSD([sQuery(id+"F2.wireOp",EDGE,"E2.18.5.2")])],"isStart":false});
            var Q656;
            Q656=makeQuery(id+"F3.opExtrude","CAP_EDGE",EDGE,{"disambiguationData":[OSD([sQuery(id+"F2.wireOp",EDGE,"E2.2.5.2")])],"isStart":false});
            var Q657;
            Q657=makeQuery(id+"F3.opExtrude","CAP_EDGE",EDGE,{"disambiguationData":[OSD([sQuery(id+"F2.wireOp",EDGE,"E3.6.21.5")])],"isStart":false});
            var Q658;
            Q658=makeQuery(id+"F3.opExtrude","CAP_EDGE",EDGE,{"disambiguationData":[OSD([sQuery(id+"F2.wireOp",EDGE,"E3.6.28.5")])],"isStart":false});
            var Q659;
            Q659=makeQuery(id+"F3.opExtrude","CAP_EDGE",EDGE,{"disambiguationData":[OSD([sQuery(id+"F2.wireOp",EDGE,"E2.9.5.2")])],"isStart":false});
            var Q660;
            Q660=makeQuery(id+"F3.opExtrude","CAP_EDGE",EDGE,{"disambiguationData":[OSD([sQuery(id+"F2.wireOp",EDGE,"E2.15.5.2")])],"isStart":false});
            var Q661;
            Q661=makeQuery(id+"F3.opExtrude","CAP_EDGE",EDGE,{"disambiguationData":[OSD([sQuery(id+"F2.wireOp",EDGE,"E2.0.5.3")])],"isStart":false});
            var Q662;
            Q662=makeQuery(id+"F3.opExtrude","CAP_EDGE",EDGE,{"disambiguationData":[OSD([sQuery(id+"F2.wireOp",EDGE,"E3.3.29.5")])],"isStart":false});
            var Q663;
            Q663=makeQuery(id+"F3.opExtrude","CAP_EDGE",EDGE,{"disambiguationData":[OSD([sQuery(id+"F2.wireOp",EDGE,"E2.16.5.1")])],"isStart":false});
            var Q664;
            Q664=makeQuery(id+"F3.opExtrude","CAP_EDGE",EDGE,{"disambiguationData":[OSD([sQuery(id+"F2.wireOp",EDGE,"E2.10.5.1")])],"isStart":false});
            var Q665;
            Q665=makeQuery(id+"F3.opExtrude","CAP_EDGE",EDGE,{"disambiguationData":[OSD([sQuery(id+"F2.wireOp",EDGE,"E2.17.5.1")])],"isStart":false});
            var Q666;
            Q666=makeQuery(id+"F3.opExtrude","CAP_EDGE",EDGE,{"disambiguationData":[OSD([sQuery(id+"F2.wireOp",EDGE,"E2.4.5.1")])],"isStart":false});
            var Q667;
            Q667=makeQuery(id+"F3.opExtrude","CAP_EDGE",EDGE,{"disambiguationData":[OSD([sQuery(id+"F2.wireOp",EDGE,"E2.11.5.1")])],"isStart":false});
            var Q668;
            Q668=makeQuery(id+"F3.opExtrude","CAP_EDGE",EDGE,{"disambiguationData":[OSD([sQuery(id+"F2.wireOp",EDGE,"E2.5.5.1")])],"isStart":false});
            var Q669;
            Q669=makeQuery(id+"F3.opExtrude","CAP_EDGE",EDGE,{"disambiguationData":[OSD([sQuery(id+"F2.wireOp",EDGE,"E3.3.24.5")])],"isStart":false});
            var Q670;
            Q670=makeQuery(id+"F3.opExtrude","CAP_EDGE",EDGE,{"disambiguationData":[OSD([sQuery(id+"F2.wireOp",EDGE,"E2.18.5.1")])],"isStart":false});
            var Q671;
            Q671=makeQuery(id+"F3.opExtrude","CAP_EDGE",EDGE,{"disambiguationData":[OSD([sQuery(id+"F2.wireOp",EDGE,"E3.3.25.5")])],"isStart":false});
            var Q672;
            Q672=makeQuery(id+"F3.opExtrude","CAP_EDGE",EDGE,{"disambiguationData":[OSD([sQuery(id+"F2.wireOp",EDGE,"E2.12.5.1")])],"isStart":false});
            var Q673;
            Q673=makeQuery(id+"F3.opExtrude","CAP_EDGE",EDGE,{"disambiguationData":[OSD([sQuery(id+"F2.wireOp",EDGE,"E3.3.23.5")])],"isStart":false});
            var Q674;
            Q674=makeQuery(id+"F3.opExtrude","CAP_EDGE",EDGE,{"disambiguationData":[OSD([sQuery(id+"F2.wireOp",EDGE,"E2.3.5.1")])],"isStart":false});
            var Q675;
            Q675=makeQuery(id+"F3.opExtrude","CAP_EDGE",EDGE,{"disambiguationData":[OSD([sQuery(id+"F2.wireOp",EDGE,"E3.3.22.5")])],"isStart":false});
            var Q676;
            Q676=makeQuery(id+"F3.opExtrude","CAP_EDGE",EDGE,{"disambiguationData":[OSD([sQuery(id+"F2.wireOp",EDGE,"E3.3.28.5")])],"isStart":false});
            var Q677;
            Q677=makeQuery(id+"F3.opExtrude","CAP_EDGE",EDGE,{"disambiguationData":[OSD([sQuery(id+"F2.wireOp",EDGE,"E2.15.5.1")])],"isStart":false});
            var Q678;
            Q678=makeQuery(id+"F3.opExtrude","CAP_EDGE",EDGE,{"disambiguationData":[OSD([sQuery(id+"F2.wireOp",EDGE,"E2.9.5.1")])],"isStart":false});
            var Q679;
            Q679=makeQuery(id+"F3.opExtrude","CAP_EDGE",EDGE,{"disambiguationData":[OSD([sQuery(id+"F2.wireOp",EDGE,"E2.19.5.1")])],"isStart":false});
            var Q680;
            Q680=makeQuery(id+"F3.opExtrude","CAP_EDGE",EDGE,{"disambiguationData":[OSD([sQuery(id+"F2.wireOp",EDGE,"E2.6.5.1")])],"isStart":false});
            var Q681;
            Q681=makeQuery(id+"F3.opExtrude","CAP_EDGE",EDGE,{"disambiguationData":[OSD([sQuery(id+"F2.wireOp",EDGE,"E3.3.26.5")])],"isStart":false});
            var Q682;
            Q682=makeQuery(id+"F3.opExtrude","CAP_EDGE",EDGE,{"disambiguationData":[OSD([sQuery(id+"F2.wireOp",EDGE,"E2.13.5.1")])],"isStart":false});
            var Q683;
            Q683=makeQuery(id+"F3.opExtrude","CAP_EDGE",EDGE,{"disambiguationData":[OSD([sQuery(id+"F2.wireOp",EDGE,"E3.3.20.5")])],"isStart":false});
            var Q684;
            Q684=makeQuery(id+"F3.opExtrude","CAP_EDGE",EDGE,{"disambiguationData":[OSD([sQuery(id+"F2.wireOp",EDGE,"E2.7.5.1")])],"isStart":false});
            var Q685;
            Q685=makeQuery(id+"F3.opExtrude","CAP_EDGE",EDGE,{"disambiguationData":[OSD([sQuery(id+"F2.wireOp",EDGE,"E2.14.5.1")])],"isStart":false});
            var Q686;
            Q686=makeQuery(id+"F3.opExtrude","CAP_EDGE",EDGE,{"disambiguationData":[OSD([sQuery(id+"F2.wireOp",EDGE,"E2.1.5.1")])],"isStart":false});
            var Q687;
            Q687=makeQuery(id+"F3.opExtrude","CAP_EDGE",EDGE,{"disambiguationData":[OSD([sQuery(id+"F2.wireOp",EDGE,"E2.8.5.1")])],"isStart":false});
            var Q688;
            Q688=makeQuery(id+"F3.opExtrude","CAP_EDGE",EDGE,{"disambiguationData":[OSD([sQuery(id+"F2.wireOp",EDGE,"E3.3.27.5")])],"isStart":false});
            var Q689;
            Q689=makeQuery(id+"F3.opExtrude","CAP_EDGE",EDGE,{"disambiguationData":[OSD([sQuery(id+"F2.wireOp",EDGE,"E2.2.5.1")])],"isStart":false});
            var Q690;
            Q690=makeQuery(id+"F3.opExtrude","CAP_EDGE",EDGE,{"disambiguationData":[OSD([sQuery(id+"F2.wireOp",EDGE,"E3.3.21.5")])],"isStart":false});
            var Q691;
            Q691=makeQuery(id+"F3.opExtrude","CAP_EDGE",EDGE,{"disambiguationData":[OSD([sQuery(id+"F2.wireOp",EDGE,"E3.9.23.5")])],"isStart":false});
            var Q692;
            Q692=makeQuery(id+"F3.opExtrude","CAP_EDGE",EDGE,{"disambiguationData":[OSD([sQuery(id+"F2.wireOp",EDGE,"E2.3.5.3")])],"isStart":false});
            var Q693;
            Q693=makeQuery(id+"F3.opExtrude","CAP_EDGE",EDGE,{"disambiguationData":[OSD([sQuery(id+"F2.wireOp",EDGE,"E3.9.22.5")])],"isStart":false});
            var Q694;
            Q694=makeQuery(id+"F3.opExtrude","CAP_EDGE",EDGE,{"disambiguationData":[OSD([sQuery(id+"F2.wireOp",EDGE,"E3.9.29.5")])],"isStart":false});
            var Q695;
            Q695=makeQuery(id+"F3.opExtrude","CAP_EDGE",EDGE,{"disambiguationData":[OSD([sQuery(id+"F2.wireOp",EDGE,"E2.16.5.3")])],"isStart":false});
            var Q696;
            Q696=makeQuery(id+"F3.opExtrude","CAP_EDGE",EDGE,{"disambiguationData":[OSD([sQuery(id+"F2.wireOp",EDGE,"E2.10.5.3")])],"isStart":false});
            var Q697;
            Q697=makeQuery(id+"F3.opExtrude","CAP_EDGE",EDGE,{"disambiguationData":[OSD([sQuery(id+"F2.wireOp",EDGE,"E3.9.26.5")])],"isStart":false});
            var Q698;
            Q698=makeQuery(id+"F3.opExtrude","CAP_EDGE",EDGE,{"disambiguationData":[OSD([sQuery(id+"F2.wireOp",EDGE,"E2.13.5.3")])],"isStart":false});
            var Q699;
            Q699=makeQuery(id+"F3.opExtrude","CAP_EDGE",EDGE,{"disambiguationData":[OSD([sQuery(id+"F2.wireOp",EDGE,"E3.9.20.5")])],"isStart":false});
            var Q700;
            Q700=makeQuery(id+"F3.opExtrude","CAP_EDGE",EDGE,{"disambiguationData":[OSD([sQuery(id+"F2.wireOp",EDGE,"E2.7.5.3")])],"isStart":false});
            var Q701;
            Q701=makeQuery(id+"F3.opExtrude","CAP_EDGE",EDGE,{"disambiguationData":[OSD([sQuery(id+"F2.wireOp",EDGE,"E2.14.5.3")])],"isStart":false});
            var Q702;
            Q702=makeQuery(id+"F3.opExtrude","CAP_EDGE",EDGE,{"disambiguationData":[OSD([sQuery(id+"F2.wireOp",EDGE,"E2.1.5.3")])],"isStart":false});
            var Q703;
            Q703=makeQuery(id+"F3.opExtrude","CAP_EDGE",EDGE,{"disambiguationData":[OSD([sQuery(id+"F2.wireOp",EDGE,"E2.8.5.3")])],"isStart":false});
            var Q704;
            Q704=makeQuery(id+"F3.opExtrude","CAP_EDGE",EDGE,{"disambiguationData":[OSD([sQuery(id+"F2.wireOp",EDGE,"E3.9.27.5")])],"isStart":false});
            var Q705;
            Q705=makeQuery(id+"F3.opExtrude","CAP_EDGE",EDGE,{"disambiguationData":[OSD([sQuery(id+"F2.wireOp",EDGE,"E2.2.5.3")])],"isStart":false});
            var Q706;
            Q706=makeQuery(id+"F3.opExtrude","CAP_EDGE",EDGE,{"disambiguationData":[OSD([sQuery(id+"F2.wireOp",EDGE,"E3.9.21.5")])],"isStart":false});
            var Q707;
            Q707=makeQuery(id+"F3.opExtrude","CAP_EDGE",EDGE,{"disambiguationData":[OSD([sQuery(id+"F2.wireOp",EDGE,"E3.9.28.5")])],"isStart":false});
            var Q708;
            Q708=makeQuery(id+"F3.opExtrude","CAP_EDGE",EDGE,{"disambiguationData":[OSD([sQuery(id+"F2.wireOp",EDGE,"E2.15.5.3")])],"isStart":false});
            var Q709;
            Q709=makeQuery(id+"F3.opExtrude","CAP_EDGE",EDGE,{"disambiguationData":[OSD([sQuery(id+"F2.wireOp",EDGE,"E2.9.5.3")])],"isStart":false});
            var Q710;
            Q710=makeQuery(id+"F3.opExtrude","CAP_EDGE",EDGE,{"disambiguationData":[OSD([sQuery(id+"F2.wireOp",EDGE,"E2.17.5.3")])],"isStart":false});
            var Q711;
            Q711=makeQuery(id+"F3.opExtrude","CAP_EDGE",EDGE,{"disambiguationData":[OSD([sQuery(id+"F2.wireOp",EDGE,"E2.4.5.3")])],"isStart":false});
            var Q712;
            Q712=makeQuery(id+"F3.opExtrude","CAP_EDGE",EDGE,{"disambiguationData":[OSD([sQuery(id+"F2.wireOp",EDGE,"E2.11.5.3")])],"isStart":false});
            var Q713;
            Q713=makeQuery(id+"F3.opExtrude","CAP_EDGE",EDGE,{"disambiguationData":[OSD([sQuery(id+"F2.wireOp",EDGE,"E2.5.5.3")])],"isStart":false});
            var Q714;
            Q714=makeQuery(id+"F3.opExtrude","CAP_EDGE",EDGE,{"disambiguationData":[OSD([sQuery(id+"F2.wireOp",EDGE,"E3.9.24.5")])],"isStart":false});
            var Q715;
            Q715=makeQuery(id+"F3.opExtrude","CAP_EDGE",EDGE,{"disambiguationData":[OSD([sQuery(id+"F2.wireOp",EDGE,"E2.18.5.3")])],"isStart":false});
            var Q716;
            Q716=makeQuery(id+"F3.opExtrude","CAP_EDGE",EDGE,{"disambiguationData":[OSD([sQuery(id+"F2.wireOp",EDGE,"E3.9.25.5")])],"isStart":false});
            var Q717;
            Q717=makeQuery(id+"F3.opExtrude","CAP_EDGE",EDGE,{"disambiguationData":[OSD([sQuery(id+"F2.wireOp",EDGE,"E2.12.5.3")])],"isStart":false});
            var Q718;
            Q718=makeQuery(id+"F3.opExtrude","CAP_EDGE",EDGE,{"disambiguationData":[OSD([sQuery(id+"F2.wireOp",EDGE,"E2.19.5.3")])],"isStart":false});
            var Q719;
            Q719=makeQuery(id+"F3.opExtrude","CAP_EDGE",EDGE,{"disambiguationData":[OSD([sQuery(id+"F2.wireOp",EDGE,"E2.6.5.3")])],"isStart":false});
            var Q720;
            Q720=makeQuery(id+"F3.opExtrude","CAP_EDGE",EDGE,{"disambiguationData":[OSD([sQuery(id+"F2.wireOp",EDGE,"E2.0.6.3")])],"isStart":false});
            var Q721;
            Q721=makeQuery(id+"F3.opExtrude","CAP_EDGE",EDGE,{"disambiguationData":[OSD([sQuery(id+"F2.wireOp",EDGE,"E2.0.6.0")])],"isStart":false});
            var Q722;
            Q722=makeQuery(id+"F3.opExtrude","CAP_EDGE",EDGE,{"disambiguationData":[OSD([sQuery(id+"F2.wireOp",EDGE,"E2.0.6.2")])],"isStart":false});
            var Q723;
            Q723=makeQuery(id+"F3.opExtrude","CAP_EDGE",EDGE,{"disambiguationData":[OSD([sQuery(id+"F2.wireOp",EDGE,"E3.9.23.6")])],"isStart":false});
            var Q724;
            Q724=makeQuery(id+"F3.opExtrude","CAP_EDGE",EDGE,{"disambiguationData":[OSD([sQuery(id+"F2.wireOp",EDGE,"E2.3.6.3")])],"isStart":false});
            var Q725;
            Q725=makeQuery(id+"F3.opExtrude","CAP_EDGE",EDGE,{"disambiguationData":[OSD([sQuery(id+"F2.wireOp",EDGE,"E3.9.22.6")])],"isStart":false});
            var Q726;
            Q726=makeQuery(id+"F3.opExtrude","CAP_EDGE",EDGE,{"disambiguationData":[OSD([sQuery(id+"F2.wireOp",EDGE,"E2.19.6.3")])],"isStart":false});
            var Q727;
            Q727=makeQuery(id+"F3.opExtrude","CAP_EDGE",EDGE,{"disambiguationData":[OSD([sQuery(id+"F2.wireOp",EDGE,"E2.6.6.3")])],"isStart":false});
            var Q728;
            Q728=makeQuery(id+"F3.opExtrude","CAP_EDGE",EDGE,{"disambiguationData":[OSD([sQuery(id+"F2.wireOp",EDGE,"E3.9.26.6")])],"isStart":false});
            var Q729;
            Q729=makeQuery(id+"F3.opExtrude","CAP_EDGE",EDGE,{"disambiguationData":[OSD([sQuery(id+"F2.wireOp",EDGE,"E2.13.6.3")])],"isStart":false});
            var Q730;
            Q730=makeQuery(id+"F3.opExtrude","CAP_EDGE",EDGE,{"disambiguationData":[OSD([sQuery(id+"F2.wireOp",EDGE,"E3.9.20.6")])],"isStart":false});
            var Q731;
            Q731=makeQuery(id+"F3.opExtrude","CAP_EDGE",EDGE,{"disambiguationData":[OSD([sQuery(id+"F2.wireOp",EDGE,"E2.7.6.3")])],"isStart":false});
            var Q732;
            Q732=makeQuery(id+"F3.opExtrude","CAP_EDGE",EDGE,{"disambiguationData":[OSD([sQuery(id+"F2.wireOp",EDGE,"E2.14.6.3")])],"isStart":false});
            var Q733;
            Q733=makeQuery(id+"F3.opExtrude","CAP_EDGE",EDGE,{"disambiguationData":[OSD([sQuery(id+"F2.wireOp",EDGE,"E2.1.6.3")])],"isStart":false});
            var Q734;
            Q734=makeQuery(id+"F3.opExtrude","CAP_EDGE",EDGE,{"disambiguationData":[OSD([sQuery(id+"F2.wireOp",EDGE,"E2.8.6.3")])],"isStart":false});
            var Q735;
            Q735=makeQuery(id+"F3.opExtrude","CAP_EDGE",EDGE,{"disambiguationData":[OSD([sQuery(id+"F2.wireOp",EDGE,"E3.9.27.6")])],"isStart":false});
            var Q736;
            Q736=makeQuery(id+"F3.opExtrude","CAP_EDGE",EDGE,{"disambiguationData":[OSD([sQuery(id+"F2.wireOp",EDGE,"E2.2.6.3")])],"isStart":false});
            var Q737;
            Q737=makeQuery(id+"F3.opExtrude","CAP_EDGE",EDGE,{"disambiguationData":[OSD([sQuery(id+"F2.wireOp",EDGE,"E3.9.21.6")])],"isStart":false});
            var Q738;
            Q738=makeQuery(id+"F3.opExtrude","CAP_EDGE",EDGE,{"disambiguationData":[OSD([sQuery(id+"F2.wireOp",EDGE,"E3.9.29.6")])],"isStart":false});
            var Q739;
            Q739=makeQuery(id+"F3.opExtrude","CAP_EDGE",EDGE,{"disambiguationData":[OSD([sQuery(id+"F2.wireOp",EDGE,"E2.16.6.3")])],"isStart":false});
            var Q740;
            Q740=makeQuery(id+"F3.opExtrude","CAP_EDGE",EDGE,{"disambiguationData":[OSD([sQuery(id+"F2.wireOp",EDGE,"E2.10.6.3")])],"isStart":false});
            var Q741;
            Q741=makeQuery(id+"F3.opExtrude","CAP_EDGE",EDGE,{"disambiguationData":[OSD([sQuery(id+"F2.wireOp",EDGE,"E2.4.6.3")])],"isStart":false});
            var Q742;
            Q742=makeQuery(id+"F3.opExtrude","CAP_EDGE",EDGE,{"disambiguationData":[OSD([sQuery(id+"F2.wireOp",EDGE,"E2.17.6.3")])],"isStart":false});
            var Q743;
            Q743=makeQuery(id+"F3.opExtrude","CAP_EDGE",EDGE,{"disambiguationData":[OSD([sQuery(id+"F2.wireOp",EDGE,"E3.9.24.6")])],"isStart":false});
            var Q744;
            Q744=makeQuery(id+"F3.opExtrude","CAP_EDGE",EDGE,{"disambiguationData":[OSD([sQuery(id+"F2.wireOp",EDGE,"E2.5.6.3")])],"isStart":false});
            var Q745;
            Q745=makeQuery(id+"F3.opExtrude","CAP_EDGE",EDGE,{"disambiguationData":[OSD([sQuery(id+"F2.wireOp",EDGE,"E2.11.6.3")])],"isStart":false});
            var Q746;
            Q746=makeQuery(id+"F3.opExtrude","CAP_EDGE",EDGE,{"disambiguationData":[OSD([sQuery(id+"F2.wireOp",EDGE,"E2.18.6.3")])],"isStart":false});
            var Q747;
            Q747=makeQuery(id+"F3.opExtrude","CAP_EDGE",EDGE,{"disambiguationData":[OSD([sQuery(id+"F2.wireOp",EDGE,"E3.9.25.6")])],"isStart":false});
            var Q748;
            Q748=makeQuery(id+"F3.opExtrude","CAP_EDGE",EDGE,{"disambiguationData":[OSD([sQuery(id+"F2.wireOp",EDGE,"E2.12.6.3")])],"isStart":false});
            var Q749;
            Q749=makeQuery(id+"F3.opExtrude","CAP_EDGE",EDGE,{"disambiguationData":[OSD([sQuery(id+"F2.wireOp",EDGE,"E3.0.23.6")])],"isStart":false});
            var Q750;
            Q750=makeQuery(id+"F3.opExtrude","CAP_EDGE",EDGE,{"disambiguationData":[OSD([sQuery(id+"F2.wireOp",EDGE,"E2.3.6.0")])],"isStart":false});
            var Q751;
            Q751=makeQuery(id+"F3.opExtrude","CAP_EDGE",EDGE,{"disambiguationData":[OSD([sQuery(id+"F2.wireOp",EDGE,"E3.0.22.6")])],"isStart":false});
            var Q752;
            Q752=makeQuery(id+"F3.opExtrude","CAP_EDGE",EDGE,{"disambiguationData":[OSD([sQuery(id+"F2.wireOp",EDGE,"E3.0.29.6")])],"isStart":false});
            var Q753;
            Q753=makeQuery(id+"F3.opExtrude","CAP_EDGE",EDGE,{"disambiguationData":[OSD([sQuery(id+"F2.wireOp",EDGE,"E2.16.6.0")])],"isStart":false});
            var Q754;
            Q754=makeQuery(id+"F3.opExtrude","CAP_EDGE",EDGE,{"disambiguationData":[OSD([sQuery(id+"F2.wireOp",EDGE,"E3.9.28.6")])],"isStart":false});
            var Q755;
            Q755=makeQuery(id+"F3.opExtrude","CAP_EDGE",EDGE,{"disambiguationData":[OSD([sQuery(id+"F2.wireOp",EDGE,"E2.15.6.3")])],"isStart":false});
            var Q756;
            Q756=makeQuery(id+"F3.opExtrude","CAP_EDGE",EDGE,{"disambiguationData":[OSD([sQuery(id+"F2.wireOp",EDGE,"E2.9.6.3")])],"isStart":false});
            var Q757;
            Q757=makeQuery(id+"F3.opExtrude","CAP_EDGE",EDGE,{"disambiguationData":[OSD([sQuery(id+"F2.wireOp",EDGE,"E3.0.26.6")])],"isStart":false});
            var Q758;
            Q758=makeQuery(id+"F3.opExtrude","CAP_EDGE",EDGE,{"disambiguationData":[OSD([sQuery(id+"F2.wireOp",EDGE,"E2.13.6.0")])],"isStart":false});
            var Q759;
            Q759=makeQuery(id+"F3.opExtrude","CAP_EDGE",EDGE,{"disambiguationData":[OSD([sQuery(id+"F2.wireOp",EDGE,"E3.0.20.6")])],"isStart":false});
            var Q760;
            Q760=makeQuery(id+"F3.opExtrude","CAP_EDGE",EDGE,{"disambiguationData":[OSD([sQuery(id+"F2.wireOp",EDGE,"E2.7.6.0")])],"isStart":false});
            var Q761;
            Q761=makeQuery(id+"F3.opExtrude","CAP_EDGE",EDGE,{"disambiguationData":[OSD([sQuery(id+"F2.wireOp",EDGE,"E2.14.6.0")])],"isStart":false});
            var Q762;
            Q762=makeQuery(id+"F3.opExtrude","CAP_EDGE",EDGE,{"disambiguationData":[OSD([sQuery(id+"F2.wireOp",EDGE,"E2.1.6.0")])],"isStart":false});
            var Q763;
            Q763=makeQuery(id+"F3.opExtrude","CAP_EDGE",EDGE,{"disambiguationData":[OSD([sQuery(id+"F2.wireOp",EDGE,"E3.0.21.6")])],"isStart":false});
            var Q764;
            Q764=makeQuery(id+"F3.opExtrude","CAP_EDGE",EDGE,{"disambiguationData":[OSD([sQuery(id+"F2.wireOp",EDGE,"E3.0.27.6")])],"isStart":false});
            var Q765;
            Q765=makeQuery(id+"F3.opExtrude","CAP_EDGE",EDGE,{"disambiguationData":[OSD([sQuery(id+"F2.wireOp",EDGE,"E2.8.6.0")])],"isStart":false});
            var Q766;
            Q766=makeQuery(id+"F3.opExtrude","CAP_EDGE",EDGE,{"disambiguationData":[OSD([sQuery(id+"F2.wireOp",EDGE,"E2.15.6.0")])],"isStart":false});
            var Q767;
            Q767=makeQuery(id+"F3.opExtrude","CAP_EDGE",EDGE,{"disambiguationData":[OSD([sQuery(id+"F2.wireOp",EDGE,"E2.2.6.0")])],"isStart":false});
            var Q768;
            Q768=makeQuery(id+"F3.opExtrude","CAP_EDGE",EDGE,{"disambiguationData":[OSD([sQuery(id+"F2.wireOp",EDGE,"E2.9.6.0")])],"isStart":false});
            var Q769;
            Q769=makeQuery(id+"F3.opExtrude","CAP_EDGE",EDGE,{"disambiguationData":[OSD([sQuery(id+"F2.wireOp",EDGE,"E3.0.28.6")])],"isStart":false});
            var Q770;
            Q770=makeQuery(id+"F3.opExtrude","CAP_EDGE",EDGE,{"disambiguationData":[OSD([sQuery(id+"F2.wireOp",EDGE,"E2.10.6.0")])],"isStart":false});
            var Q771;
            Q771=makeQuery(id+"F3.opExtrude","CAP_EDGE",EDGE,{"disambiguationData":[OSD([sQuery(id+"F2.wireOp",EDGE,"E2.17.6.0")])],"isStart":false});
            var Q772;
            Q772=makeQuery(id+"F3.opExtrude","CAP_EDGE",EDGE,{"disambiguationData":[OSD([sQuery(id+"F2.wireOp",EDGE,"E2.4.6.0")])],"isStart":false});
            var Q773;
            Q773=makeQuery(id+"F3.opExtrude","CAP_EDGE",EDGE,{"disambiguationData":[OSD([sQuery(id+"F2.wireOp",EDGE,"E2.11.6.0")])],"isStart":false});
            var Q774;
            Q774=makeQuery(id+"F3.opExtrude","CAP_EDGE",EDGE,{"disambiguationData":[OSD([sQuery(id+"F2.wireOp",EDGE,"E2.5.6.0")])],"isStart":false});
            var Q775;
            Q775=makeQuery(id+"F3.opExtrude","CAP_EDGE",EDGE,{"disambiguationData":[OSD([sQuery(id+"F2.wireOp",EDGE,"E3.0.24.6")])],"isStart":false});
            var Q776;
            Q776=makeQuery(id+"F3.opExtrude","CAP_EDGE",EDGE,{"disambiguationData":[OSD([sQuery(id+"F2.wireOp",EDGE,"E2.18.6.0")])],"isStart":false});
            var Q777;
            Q777=makeQuery(id+"F3.opExtrude","CAP_EDGE",EDGE,{"disambiguationData":[OSD([sQuery(id+"F2.wireOp",EDGE,"E3.0.25.6")])],"isStart":false});
            var Q778;
            Q778=makeQuery(id+"F3.opExtrude","CAP_EDGE",EDGE,{"disambiguationData":[OSD([sQuery(id+"F2.wireOp",EDGE,"E2.12.6.0")])],"isStart":false});
            var Q779;
            Q779=makeQuery(id+"F3.opExtrude","CAP_EDGE",EDGE,{"disambiguationData":[OSD([sQuery(id+"F2.wireOp",EDGE,"E2.19.6.0")])],"isStart":false});
            var Q780;
            Q780=makeQuery(id+"F3.opExtrude","CAP_EDGE",EDGE,{"disambiguationData":[OSD([sQuery(id+"F2.wireOp",EDGE,"E2.6.6.0")])],"isStart":false});
            var Q781;
            Q781=makeQuery(id+"F3.opExtrude","CAP_EDGE",EDGE,{"disambiguationData":[OSD([sQuery(id+"F2.wireOp",EDGE,"E2.0.6.1")])],"isStart":false});
            var Q782;
            Q782=makeQuery(id+"F3.opExtrude","CAP_EDGE",EDGE,{"disambiguationData":[OSD([sQuery(id+"F2.wireOp",EDGE,"E2.10.6.2")])],"isStart":false});
            var Q783;
            Q783=makeQuery(id+"F3.opExtrude","CAP_EDGE",EDGE,{"disambiguationData":[OSD([sQuery(id+"F2.wireOp",EDGE,"E2.17.6.2")])],"isStart":false});
            var Q784;
            Q784=makeQuery(id+"F3.opExtrude","CAP_EDGE",EDGE,{"disambiguationData":[OSD([sQuery(id+"F2.wireOp",EDGE,"E2.4.6.2")])],"isStart":false});
            var Q785;
            Q785=makeQuery(id+"F3.opExtrude","CAP_EDGE",EDGE,{"disambiguationData":[OSD([sQuery(id+"F2.wireOp",EDGE,"E2.11.6.2")])],"isStart":false});
            var Q786;
            Q786=makeQuery(id+"F3.opExtrude","CAP_EDGE",EDGE,{"disambiguationData":[OSD([sQuery(id+"F2.wireOp",EDGE,"E2.5.6.2")])],"isStart":false});
            var Q787;
            Q787=makeQuery(id+"F3.opExtrude","CAP_EDGE",EDGE,{"disambiguationData":[OSD([sQuery(id+"F2.wireOp",EDGE,"E3.6.24.6")])],"isStart":false});
            var Q788;
            Q788=makeQuery(id+"F3.opExtrude","CAP_EDGE",EDGE,{"disambiguationData":[OSD([sQuery(id+"F2.wireOp",EDGE,"E2.18.6.2")])],"isStart":false});
            var Q789;
            Q789=makeQuery(id+"F3.opExtrude","CAP_EDGE",EDGE,{"disambiguationData":[OSD([sQuery(id+"F2.wireOp",EDGE,"E3.6.25.6")])],"isStart":false});
            var Q790;
            Q790=makeQuery(id+"F3.opExtrude","CAP_EDGE",EDGE,{"disambiguationData":[OSD([sQuery(id+"F2.wireOp",EDGE,"E2.12.6.2")])],"isStart":false});
            var Q791;
            Q791=makeQuery(id+"F3.opExtrude","CAP_EDGE",EDGE,{"disambiguationData":[OSD([sQuery(id+"F2.wireOp",EDGE,"E2.19.6.2")])],"isStart":false});
            var Q792;
            Q792=makeQuery(id+"F3.opExtrude","CAP_EDGE",EDGE,{"disambiguationData":[OSD([sQuery(id+"F2.wireOp",EDGE,"E2.6.6.2")])],"isStart":false});
            var Q793;
            Q793=makeQuery(id+"F3.opExtrude","CAP_EDGE",EDGE,{"disambiguationData":[OSD([sQuery(id+"F2.wireOp",EDGE,"E3.6.23.6")])],"isStart":false});
            var Q794;
            Q794=makeQuery(id+"F3.opExtrude","CAP_EDGE",EDGE,{"disambiguationData":[OSD([sQuery(id+"F2.wireOp",EDGE,"E2.3.6.2")])],"isStart":false});
            var Q795;
            Q795=makeQuery(id+"F3.opExtrude","CAP_EDGE",EDGE,{"disambiguationData":[OSD([sQuery(id+"F2.wireOp",EDGE,"E3.6.22.6")])],"isStart":false});
            var Q796;
            Q796=makeQuery(id+"F3.opExtrude","CAP_EDGE",EDGE,{"disambiguationData":[OSD([sQuery(id+"F2.wireOp",EDGE,"E3.6.29.6")])],"isStart":false});
            var Q797;
            Q797=makeQuery(id+"F3.opExtrude","CAP_EDGE",EDGE,{"disambiguationData":[OSD([sQuery(id+"F2.wireOp",EDGE,"E2.16.6.2")])],"isStart":false});
            var Q798;
            Q798=makeQuery(id+"F3.opExtrude","CAP_EDGE",EDGE,{"disambiguationData":[OSD([sQuery(id+"F2.wireOp",EDGE,"E2.9.6.2")])],"isStart":false});
            var Q799;
            Q799=makeQuery(id+"F3.opExtrude","CAP_EDGE",EDGE,{"disambiguationData":[OSD([sQuery(id+"F2.wireOp",EDGE,"E3.6.26.6")])],"isStart":false});
            var Q800;
            Q800=makeQuery(id+"F3.opExtrude","CAP_EDGE",EDGE,{"disambiguationData":[OSD([sQuery(id+"F2.wireOp",EDGE,"E2.13.6.2")])],"isStart":false});
            var Q801;
            Q801=makeQuery(id+"F3.opExtrude","CAP_EDGE",EDGE,{"disambiguationData":[OSD([sQuery(id+"F2.wireOp",EDGE,"E3.6.20.6")])],"isStart":false});
            var Q802;
            Q802=makeQuery(id+"F3.opExtrude","CAP_EDGE",EDGE,{"disambiguationData":[OSD([sQuery(id+"F2.wireOp",EDGE,"E2.7.6.2")])],"isStart":false});
            var Q803;
            Q803=makeQuery(id+"F3.opExtrude","CAP_EDGE",EDGE,{"disambiguationData":[OSD([sQuery(id+"F2.wireOp",EDGE,"E2.14.6.2")])],"isStart":false});
            var Q804;
            Q804=makeQuery(id+"F3.opExtrude","CAP_EDGE",EDGE,{"disambiguationData":[OSD([sQuery(id+"F2.wireOp",EDGE,"E2.1.6.2")])],"isStart":false});
            var Q805;
            Q805=makeQuery(id+"F3.opExtrude","CAP_EDGE",EDGE,{"disambiguationData":[OSD([sQuery(id+"F2.wireOp",EDGE,"E2.8.6.2")])],"isStart":false});
            var Q806;
            Q806=makeQuery(id+"F3.opExtrude","CAP_EDGE",EDGE,{"disambiguationData":[OSD([sQuery(id+"F2.wireOp",EDGE,"E3.6.27.6")])],"isStart":false});
            var Q807;
            Q807=makeQuery(id+"F3.opExtrude","CAP_EDGE",EDGE,{"disambiguationData":[OSD([sQuery(id+"F2.wireOp",EDGE,"E2.2.6.2")])],"isStart":false});
            var Q808;
            Q808=makeQuery(id+"F3.opExtrude","CAP_EDGE",EDGE,{"disambiguationData":[OSD([sQuery(id+"F2.wireOp",EDGE,"E3.6.21.6")])],"isStart":false});
            var Q809;
            Q809=makeQuery(id+"F3.opExtrude","CAP_EDGE",EDGE,{"disambiguationData":[OSD([sQuery(id+"F2.wireOp",EDGE,"E3.6.28.6")])],"isStart":false});
            var Q810;
            Q810=makeQuery(id+"F3.opExtrude","CAP_EDGE",EDGE,{"disambiguationData":[OSD([sQuery(id+"F2.wireOp",EDGE,"E2.15.6.2")])],"isStart":false});
            var Q811;
            Q811=makeQuery(id+"F3.opExtrude","CAP_EDGE",EDGE,{"disambiguationData":[OSD([sQuery(id+"F2.wireOp",EDGE,"E3.3.23.6")])],"isStart":false});
            var Q812;
            Q812=makeQuery(id+"F3.opExtrude","CAP_EDGE",EDGE,{"disambiguationData":[OSD([sQuery(id+"F2.wireOp",EDGE,"E2.3.6.1")])],"isStart":false});
            var Q813;
            Q813=makeQuery(id+"F3.opExtrude","CAP_EDGE",EDGE,{"disambiguationData":[OSD([sQuery(id+"F2.wireOp",EDGE,"E3.3.22.6")])],"isStart":false});
            var Q814;
            Q814=makeQuery(id+"F3.opExtrude","CAP_EDGE",EDGE,{"disambiguationData":[OSD([sQuery(id+"F2.wireOp",EDGE,"E3.3.29.6")])],"isStart":false});
            var Q815;
            Q815=makeQuery(id+"F3.opExtrude","CAP_EDGE",EDGE,{"disambiguationData":[OSD([sQuery(id+"F2.wireOp",EDGE,"E2.16.6.1")])],"isStart":false});
            var Q816;
            Q816=makeQuery(id+"F3.opExtrude","CAP_EDGE",EDGE,{"disambiguationData":[OSD([sQuery(id+"F2.wireOp",EDGE,"E2.10.6.1")])],"isStart":false});
            var Q817;
            Q817=makeQuery(id+"F3.opExtrude","CAP_EDGE",EDGE,{"disambiguationData":[OSD([sQuery(id+"F2.wireOp",EDGE,"E2.17.6.1")])],"isStart":false});
            var Q818;
            Q818=makeQuery(id+"F3.opExtrude","CAP_EDGE",EDGE,{"disambiguationData":[OSD([sQuery(id+"F2.wireOp",EDGE,"E2.4.6.1")])],"isStart":false});
            var Q819;
            Q819=makeQuery(id+"F3.opExtrude","CAP_EDGE",EDGE,{"disambiguationData":[OSD([sQuery(id+"F2.wireOp",EDGE,"E2.11.6.1")])],"isStart":false});
            var Q820;
            Q820=makeQuery(id+"F3.opExtrude","CAP_EDGE",EDGE,{"disambiguationData":[OSD([sQuery(id+"F2.wireOp",EDGE,"E2.14.6.1")])],"isStart":false});
            var Q821;
            Q821=makeQuery(id+"F3.opExtrude","CAP_EDGE",EDGE,{"disambiguationData":[OSD([sQuery(id+"F2.wireOp",EDGE,"E2.1.6.1")])],"isStart":false});
            var Q822;
            Q822=makeQuery(id+"F3.opExtrude","CAP_EDGE",EDGE,{"disambiguationData":[OSD([sQuery(id+"F2.wireOp",EDGE,"E2.8.6.1")])],"isStart":false});
            var Q823;
            Q823=makeQuery(id+"F3.opExtrude","CAP_EDGE",EDGE,{"disambiguationData":[OSD([sQuery(id+"F2.wireOp",EDGE,"E3.3.27.6")])],"isStart":false});
            var Q824;
            Q824=makeQuery(id+"F3.opExtrude","CAP_EDGE",EDGE,{"disambiguationData":[OSD([sQuery(id+"F2.wireOp",EDGE,"E2.15.6.1")])],"isStart":false});
            var Q825;
            Q825=makeQuery(id+"F3.opExtrude","CAP_EDGE",EDGE,{"disambiguationData":[OSD([sQuery(id+"F2.wireOp",EDGE,"E3.3.21.6")])],"isStart":false});
            var Q826;
            Q826=makeQuery(id+"F3.opExtrude","CAP_EDGE",EDGE,{"disambiguationData":[OSD([sQuery(id+"F2.wireOp",EDGE,"E2.2.6.1")])],"isStart":false});
            var Q827;
            Q827=makeQuery(id+"F3.opExtrude","CAP_EDGE",EDGE,{"disambiguationData":[OSD([sQuery(id+"F2.wireOp",EDGE,"E2.9.6.1")])],"isStart":false});
            var Q828;
            Q828=makeQuery(id+"F3.opExtrude","CAP_EDGE",EDGE,{"disambiguationData":[OSD([sQuery(id+"F2.wireOp",EDGE,"E3.3.28.6")])],"isStart":false});
            var Q829;
            Q829=makeQuery(id+"F3.opExtrude","CAP_EDGE",EDGE,{"disambiguationData":[OSD([sQuery(id+"F2.wireOp",EDGE,"E2.5.6.1")])],"isStart":false});
            var Q830;
            Q830=makeQuery(id+"F3.opExtrude","CAP_EDGE",EDGE,{"disambiguationData":[OSD([sQuery(id+"F2.wireOp",EDGE,"E3.3.24.6")])],"isStart":false});
            var Q831;
            Q831=makeQuery(id+"F3.opExtrude","CAP_EDGE",EDGE,{"disambiguationData":[OSD([sQuery(id+"F2.wireOp",EDGE,"E2.18.6.1")])],"isStart":false});
            var Q832;
            Q832=makeQuery(id+"F3.opExtrude","CAP_EDGE",EDGE,{"disambiguationData":[OSD([sQuery(id+"F2.wireOp",EDGE,"E3.3.25.6")])],"isStart":false});
            var Q833;
            Q833=makeQuery(id+"F3.opExtrude","CAP_EDGE",EDGE,{"disambiguationData":[OSD([sQuery(id+"F2.wireOp",EDGE,"E2.12.6.1")])],"isStart":false});
            var Q834;
            Q834=makeQuery(id+"F3.opExtrude","CAP_EDGE",EDGE,{"disambiguationData":[OSD([sQuery(id+"F2.wireOp",EDGE,"E2.19.6.1")])],"isStart":false});
            var Q835;
            Q835=makeQuery(id+"F3.opExtrude","CAP_EDGE",EDGE,{"disambiguationData":[OSD([sQuery(id+"F2.wireOp",EDGE,"E2.6.6.1")])],"isStart":false});
            var Q836;
            Q836=makeQuery(id+"F3.opExtrude","CAP_EDGE",EDGE,{"disambiguationData":[OSD([sQuery(id+"F2.wireOp",EDGE,"E3.3.26.6")])],"isStart":false});
            var Q837;
            Q837=makeQuery(id+"F3.opExtrude","CAP_EDGE",EDGE,{"disambiguationData":[OSD([sQuery(id+"F2.wireOp",EDGE,"E2.13.6.1")])],"isStart":false});
            var Q838;
            Q838=makeQuery(id+"F3.opExtrude","CAP_EDGE",EDGE,{"disambiguationData":[OSD([sQuery(id+"F2.wireOp",EDGE,"E3.3.20.6")])],"isStart":false});
            var Q839;
            Q839=makeQuery(id+"F3.opExtrude","CAP_EDGE",EDGE,{"disambiguationData":[OSD([sQuery(id+"F2.wireOp",EDGE,"E2.7.6.1")])],"isStart":false});
            var Q840;
            Q840=makeQuery(id+"F3.opExtrude","CAP_EDGE",EDGE,{"disambiguationData":[OSD([sQuery(id+"F2.wireOp",EDGE,"E2.0.7.0")])],"isStart":false});
            var Q841;
            Q841=makeQuery(id+"F3.opExtrude","CAP_EDGE",EDGE,{"disambiguationData":[OSD([sQuery(id+"F2.wireOp",EDGE,"E2.0.7.2")])],"isStart":false});
            var Q842;
            Q842=makeQuery(id+"F3.opExtrude","CAP_EDGE",EDGE,{"disambiguationData":[OSD([sQuery(id+"F2.wireOp",EDGE,"E3.0.22.7")])],"isStart":false});
            var Q843;
            Q843=makeQuery(id+"F3.opExtrude","CAP_EDGE",EDGE,{"disambiguationData":[OSD([sQuery(id+"F2.wireOp",EDGE,"E2.3.7.0")])],"isStart":false});
            var Q844;
            Q844=makeQuery(id+"F3.opExtrude","CAP_EDGE",EDGE,{"disambiguationData":[OSD([sQuery(id+"F2.wireOp",EDGE,"E3.0.23.7")])],"isStart":false});
            var Q845;
            Q845=makeQuery(id+"F3.opExtrude","CAP_EDGE",EDGE,{"disambiguationData":[OSD([sQuery(id+"F2.wireOp",EDGE,"E3.0.29.7")])],"isStart":false});
            var Q846;
            Q846=makeQuery(id+"F3.opExtrude","CAP_EDGE",EDGE,{"disambiguationData":[OSD([sQuery(id+"F2.wireOp",EDGE,"E2.16.7.0")])],"isStart":false});
            var Q847;
            Q847=makeQuery(id+"F3.opExtrude","CAP_EDGE",EDGE,{"disambiguationData":[OSD([sQuery(id+"F2.wireOp",EDGE,"E2.10.7.0")])],"isStart":false});
            var Q848;
            Q848=makeQuery(id+"F3.opExtrude","CAP_EDGE",EDGE,{"disambiguationData":[OSD([sQuery(id+"F2.wireOp",EDGE,"E2.4.7.0")])],"isStart":false});
            var Q849;
            Q849=makeQuery(id+"F3.opExtrude","CAP_EDGE",EDGE,{"disambiguationData":[OSD([sQuery(id+"F2.wireOp",EDGE,"E3.0.20.7")])],"isStart":false});
            var Q850;
            Q850=makeQuery(id+"F3.opExtrude","CAP_EDGE",EDGE,{"disambiguationData":[OSD([sQuery(id+"F2.wireOp",EDGE,"E2.7.7.0")])],"isStart":false});
            var Q851;
            Q851=makeQuery(id+"F3.opExtrude","CAP_EDGE",EDGE,{"disambiguationData":[OSD([sQuery(id+"F2.wireOp",EDGE,"E2.14.7.0")])],"isStart":false});
            var Q852;
            Q852=makeQuery(id+"F3.opExtrude","CAP_EDGE",EDGE,{"disambiguationData":[OSD([sQuery(id+"F2.wireOp",EDGE,"E2.1.7.0")])],"isStart":false});
            var Q853;
            Q853=makeQuery(id+"F3.opExtrude","CAP_EDGE",EDGE,{"disambiguationData":[OSD([sQuery(id+"F2.wireOp",EDGE,"E2.8.7.0")])],"isStart":false});
            var Q854;
            Q854=makeQuery(id+"F3.opExtrude","CAP_EDGE",EDGE,{"disambiguationData":[OSD([sQuery(id+"F2.wireOp",EDGE,"E3.0.27.7")])],"isStart":false});
            var Q855;
            Q855=makeQuery(id+"F3.opExtrude","CAP_EDGE",EDGE,{"disambiguationData":[OSD([sQuery(id+"F2.wireOp",EDGE,"E2.2.7.0")])],"isStart":false});
            var Q856;
            Q856=makeQuery(id+"F3.opExtrude","CAP_EDGE",EDGE,{"disambiguationData":[OSD([sQuery(id+"F2.wireOp",EDGE,"E3.0.21.7")])],"isStart":false});
            var Q857;
            Q857=makeQuery(id+"F3.opExtrude","CAP_EDGE",EDGE,{"disambiguationData":[OSD([sQuery(id+"F2.wireOp",EDGE,"E3.0.28.7")])],"isStart":false});
            var Q858;
            Q858=makeQuery(id+"F3.opExtrude","CAP_EDGE",EDGE,{"disambiguationData":[OSD([sQuery(id+"F2.wireOp",EDGE,"E2.15.7.0")])],"isStart":false});
            var Q859;
            Q859=makeQuery(id+"F3.opExtrude","CAP_EDGE",EDGE,{"disambiguationData":[OSD([sQuery(id+"F2.wireOp",EDGE,"E2.9.7.0")])],"isStart":false});
            var Q860;
            Q860=makeQuery(id+"F3.opExtrude","CAP_EDGE",EDGE,{"disambiguationData":[OSD([sQuery(id+"F2.wireOp",EDGE,"E2.17.7.0")])],"isStart":false});
            var Q861;
            Q861=makeQuery(id+"F3.opExtrude","CAP_EDGE",EDGE,{"disambiguationData":[OSD([sQuery(id+"F2.wireOp",EDGE,"E3.0.24.7")])],"isStart":false});
            var Q862;
            Q862=makeQuery(id+"F3.opExtrude","CAP_EDGE",EDGE,{"disambiguationData":[OSD([sQuery(id+"F2.wireOp",EDGE,"E2.11.7.0")])],"isStart":false});
            var Q863;
            Q863=makeQuery(id+"F3.opExtrude","CAP_EDGE",EDGE,{"disambiguationData":[OSD([sQuery(id+"F2.wireOp",EDGE,"E2.18.7.0")])],"isStart":false});
            var Q864;
            Q864=makeQuery(id+"F3.opExtrude","CAP_EDGE",EDGE,{"disambiguationData":[OSD([sQuery(id+"F2.wireOp",EDGE,"E2.5.7.0")])],"isStart":false});
            var Q865;
            Q865=makeQuery(id+"F3.opExtrude","CAP_EDGE",EDGE,{"disambiguationData":[OSD([sQuery(id+"F2.wireOp",EDGE,"E2.12.7.0")])],"isStart":false});
            var Q866;
            Q866=makeQuery(id+"F3.opExtrude","CAP_EDGE",EDGE,{"disambiguationData":[OSD([sQuery(id+"F2.wireOp",EDGE,"E2.19.7.0")])],"isStart":false});
            var Q867;
            Q867=makeQuery(id+"F3.opExtrude","CAP_EDGE",EDGE,{"disambiguationData":[OSD([sQuery(id+"F2.wireOp",EDGE,"E3.0.25.7")])],"isStart":false});
            var Q868;
            Q868=makeQuery(id+"F3.opExtrude","CAP_EDGE",EDGE,{"disambiguationData":[OSD([sQuery(id+"F2.wireOp",EDGE,"E2.6.7.0")])],"isStart":false});
            var Q869;
            Q869=makeQuery(id+"F3.opExtrude","CAP_EDGE",EDGE,{"disambiguationData":[OSD([sQuery(id+"F2.wireOp",EDGE,"E3.0.26.7")])],"isStart":false});
            var Q870;
            Q870=makeQuery(id+"F3.opExtrude","CAP_EDGE",EDGE,{"disambiguationData":[OSD([sQuery(id+"F2.wireOp",EDGE,"E2.13.7.0")])],"isStart":false});
            var Q871;
            Q871=makeQuery(id+"F3.opExtrude","CAP_EDGE",EDGE,{"disambiguationData":[OSD([sQuery(id+"F2.wireOp",EDGE,"E2.12.7.2")])],"isStart":false});
            var Q872;
            Q872=makeQuery(id+"F3.opExtrude","CAP_EDGE",EDGE,{"disambiguationData":[OSD([sQuery(id+"F2.wireOp",EDGE,"E2.6.7.2")])],"isStart":false});
            var Q873;
            Q873=makeQuery(id+"F3.opExtrude","CAP_EDGE",EDGE,{"disambiguationData":[OSD([sQuery(id+"F2.wireOp",EDGE,"E3.6.25.7")])],"isStart":false});
            var Q874;
            Q874=makeQuery(id+"F3.opExtrude","CAP_EDGE",EDGE,{"disambiguationData":[OSD([sQuery(id+"F2.wireOp",EDGE,"E2.19.7.2")])],"isStart":false});
            var Q875;
            Q875=makeQuery(id+"F3.opExtrude","CAP_EDGE",EDGE,{"disambiguationData":[OSD([sQuery(id+"F2.wireOp",EDGE,"E3.6.26.7")])],"isStart":false});
            var Q876;
            Q876=makeQuery(id+"F3.opExtrude","CAP_EDGE",EDGE,{"disambiguationData":[OSD([sQuery(id+"F2.wireOp",EDGE,"E2.13.7.2")])],"isStart":false});
            var Q877;
            Q877=makeQuery(id+"F3.opExtrude","CAP_EDGE",EDGE,{"disambiguationData":[OSD([sQuery(id+"F2.wireOp",EDGE,"E3.6.20.7")])],"isStart":false});
            var Q878;
            Q878=makeQuery(id+"F3.opExtrude","CAP_EDGE",EDGE,{"disambiguationData":[OSD([sQuery(id+"F2.wireOp",EDGE,"E2.7.7.2")])],"isStart":false});
            var Q879;
            Q879=makeQuery(id+"F3.opExtrude","CAP_EDGE",EDGE,{"disambiguationData":[OSD([sQuery(id+"F2.wireOp",EDGE,"E2.14.7.2")])],"isStart":false});
            var Q880;
            Q880=makeQuery(id+"F3.opExtrude","CAP_EDGE",EDGE,{"disambiguationData":[OSD([sQuery(id+"F2.wireOp",EDGE,"E2.1.7.2")])],"isStart":false});
            var Q881;
            Q881=makeQuery(id+"F3.opExtrude","CAP_EDGE",EDGE,{"disambiguationData":[OSD([sQuery(id+"F2.wireOp",EDGE,"E2.8.7.2")])],"isStart":false});
            var Q882;
            Q882=makeQuery(id+"F3.opExtrude","CAP_EDGE",EDGE,{"disambiguationData":[OSD([sQuery(id+"F2.wireOp",EDGE,"E3.6.27.7")])],"isStart":false});
            var Q883;
            Q883=makeQuery(id+"F3.opExtrude","CAP_EDGE",EDGE,{"disambiguationData":[OSD([sQuery(id+"F2.wireOp",EDGE,"E3.6.22.7")])],"isStart":false});
            var Q884;
            Q884=makeQuery(id+"F3.opExtrude","CAP_EDGE",EDGE,{"disambiguationData":[OSD([sQuery(id+"F2.wireOp",EDGE,"E3.6.23.7")])],"isStart":false});
            var Q885;
            Q885=makeQuery(id+"F3.opExtrude","CAP_EDGE",EDGE,{"disambiguationData":[OSD([sQuery(id+"F2.wireOp",EDGE,"E2.16.7.2")])],"isStart":false});
            var Q886;
            Q886=makeQuery(id+"F3.opExtrude","CAP_EDGE",EDGE,{"disambiguationData":[OSD([sQuery(id+"F2.wireOp",EDGE,"E2.3.7.2")])],"isStart":false});
            var Q887;
            Q887=makeQuery(id+"F3.opExtrude","CAP_EDGE",EDGE,{"disambiguationData":[OSD([sQuery(id+"F2.wireOp",EDGE,"E2.0.7.1")])],"isStart":false});
            var Q888;
            Q888=makeQuery(id+"F3.opExtrude","CAP_EDGE",EDGE,{"disambiguationData":[OSD([sQuery(id+"F2.wireOp",EDGE,"E3.6.29.7")])],"isStart":false});
            var Q889;
            Q889=makeQuery(id+"F3.opExtrude","CAP_EDGE",EDGE,{"disambiguationData":[OSD([sQuery(id+"F2.wireOp",EDGE,"E2.10.7.2")])],"isStart":false});
            var Q890;
            Q890=makeQuery(id+"F3.opExtrude","CAP_EDGE",EDGE,{"disambiguationData":[OSD([sQuery(id+"F2.wireOp",EDGE,"E2.4.7.2")])],"isStart":false});
            var Q891;
            Q891=makeQuery(id+"F3.opExtrude","CAP_EDGE",EDGE,{"disambiguationData":[OSD([sQuery(id+"F2.wireOp",EDGE,"E2.17.7.2")])],"isStart":false});
            var Q892;
            Q892=makeQuery(id+"F3.opExtrude","CAP_EDGE",EDGE,{"disambiguationData":[OSD([sQuery(id+"F2.wireOp",EDGE,"E3.6.24.7")])],"isStart":false});
            var Q893;
            Q893=makeQuery(id+"F3.opExtrude","CAP_EDGE",EDGE,{"disambiguationData":[OSD([sQuery(id+"F2.wireOp",EDGE,"E2.11.7.2")])],"isStart":false});
            var Q894;
            Q894=makeQuery(id+"F3.opExtrude","CAP_EDGE",EDGE,{"disambiguationData":[OSD([sQuery(id+"F2.wireOp",EDGE,"E2.18.7.2")])],"isStart":false});
            var Q895;
            Q895=makeQuery(id+"F3.opExtrude","CAP_EDGE",EDGE,{"disambiguationData":[OSD([sQuery(id+"F2.wireOp",EDGE,"E2.5.7.2")])],"isStart":false});
            var Q896;
            Q896=makeQuery(id+"F3.opExtrude","CAP_EDGE",EDGE,{"disambiguationData":[OSD([sQuery(id+"F2.wireOp",EDGE,"E2.2.7.2")])],"isStart":false});
            var Q897;
            Q897=makeQuery(id+"F3.opExtrude","CAP_EDGE",EDGE,{"disambiguationData":[OSD([sQuery(id+"F2.wireOp",EDGE,"E3.6.21.7")])],"isStart":false});
            var Q898;
            Q898=makeQuery(id+"F3.opExtrude","CAP_EDGE",EDGE,{"disambiguationData":[OSD([sQuery(id+"F2.wireOp",EDGE,"E3.6.28.7")])],"isStart":false});
            var Q899;
            Q899=makeQuery(id+"F3.opExtrude","CAP_EDGE",EDGE,{"disambiguationData":[OSD([sQuery(id+"F2.wireOp",EDGE,"E2.15.7.2")])],"isStart":false});
            var Q900;
            Q900=makeQuery(id+"F3.opExtrude","CAP_EDGE",EDGE,{"disambiguationData":[OSD([sQuery(id+"F2.wireOp",EDGE,"E2.9.7.2")])],"isStart":false});
            var Q901;
            Q901=makeQuery(id+"F3.opExtrude","CAP_EDGE",EDGE,{"disambiguationData":[OSD([sQuery(id+"F2.wireOp",EDGE,"E2.0.7.3")])],"isStart":false});
            var Q902;
            Q902=makeQuery(id+"F3.opExtrude","CAP_EDGE",EDGE,{"disambiguationData":[OSD([sQuery(id+"F2.wireOp",EDGE,"E2.16.7.1")])],"isStart":false});
            var Q903;
            Q903=makeQuery(id+"F3.opExtrude","CAP_EDGE",EDGE,{"disambiguationData":[OSD([sQuery(id+"F2.wireOp",EDGE,"E2.3.7.1")])],"isStart":false});
            var Q904;
            Q904=makeQuery(id+"F3.opExtrude","CAP_EDGE",EDGE,{"disambiguationData":[OSD([sQuery(id+"F2.wireOp",EDGE,"E2.10.7.1")])],"isStart":false});
            var Q905;
            Q905=makeQuery(id+"F3.opExtrude","CAP_EDGE",EDGE,{"disambiguationData":[OSD([sQuery(id+"F2.wireOp",EDGE,"E3.3.29.7")])],"isStart":false});
            var Q906;
            Q906=makeQuery(id+"F3.opExtrude","CAP_EDGE",EDGE,{"disambiguationData":[OSD([sQuery(id+"F2.wireOp",EDGE,"E2.4.7.1")])],"isStart":false});
            var Q907;
            Q907=makeQuery(id+"F3.opExtrude","CAP_EDGE",EDGE,{"disambiguationData":[OSD([sQuery(id+"F2.wireOp",EDGE,"E2.17.7.1")])],"isStart":false});
            var Q908;
            Q908=makeQuery(id+"F3.opExtrude","CAP_EDGE",EDGE,{"disambiguationData":[OSD([sQuery(id+"F2.wireOp",EDGE,"E3.3.24.7")])],"isStart":false});
            var Q909;
            Q909=makeQuery(id+"F3.opExtrude","CAP_EDGE",EDGE,{"disambiguationData":[OSD([sQuery(id+"F2.wireOp",EDGE,"E2.11.7.1")])],"isStart":false});
            var Q910;
            Q910=makeQuery(id+"F3.opExtrude","CAP_EDGE",EDGE,{"disambiguationData":[OSD([sQuery(id+"F2.wireOp",EDGE,"E2.18.7.1")])],"isStart":false});
            var Q911;
            Q911=makeQuery(id+"F3.opExtrude","CAP_EDGE",EDGE,{"disambiguationData":[OSD([sQuery(id+"F2.wireOp",EDGE,"E2.5.7.1")])],"isStart":false});
            var Q912;
            Q912=makeQuery(id+"F3.opExtrude","CAP_EDGE",EDGE,{"disambiguationData":[OSD([sQuery(id+"F2.wireOp",EDGE,"E2.12.7.1")])],"isStart":false});
            var Q913;
            Q913=makeQuery(id+"F3.opExtrude","CAP_EDGE",EDGE,{"disambiguationData":[OSD([sQuery(id+"F2.wireOp",EDGE,"E3.3.22.7")])],"isStart":false});
            var Q914;
            Q914=makeQuery(id+"F3.opExtrude","CAP_EDGE",EDGE,{"disambiguationData":[OSD([sQuery(id+"F2.wireOp",EDGE,"E3.3.23.7")])],"isStart":false});
            var Q915;
            Q915=makeQuery(id+"F3.opExtrude","CAP_EDGE",EDGE,{"disambiguationData":[OSD([sQuery(id+"F2.wireOp",EDGE,"E3.3.28.7")])],"isStart":false});
            var Q916;
            Q916=makeQuery(id+"F3.opExtrude","CAP_EDGE",EDGE,{"disambiguationData":[OSD([sQuery(id+"F2.wireOp",EDGE,"E2.15.7.1")])],"isStart":false});
            var Q917;
            Q917=makeQuery(id+"F3.opExtrude","CAP_EDGE",EDGE,{"disambiguationData":[OSD([sQuery(id+"F2.wireOp",EDGE,"E2.9.7.1")])],"isStart":false});
            var Q918;
            Q918=makeQuery(id+"F3.opExtrude","CAP_EDGE",EDGE,{"disambiguationData":[OSD([sQuery(id+"F2.wireOp",EDGE,"E2.6.7.1")])],"isStart":false});
            var Q919;
            Q919=makeQuery(id+"F3.opExtrude","CAP_EDGE",EDGE,{"disambiguationData":[OSD([sQuery(id+"F2.wireOp",EDGE,"E3.3.25.7")])],"isStart":false});
            var Q920;
            Q920=makeQuery(id+"F3.opExtrude","CAP_EDGE",EDGE,{"disambiguationData":[OSD([sQuery(id+"F2.wireOp",EDGE,"E2.19.7.1")])],"isStart":false});
            var Q921;
            Q921=makeQuery(id+"F3.opExtrude","CAP_EDGE",EDGE,{"disambiguationData":[OSD([sQuery(id+"F2.wireOp",EDGE,"E3.3.26.7")])],"isStart":false});
            var Q922;
            Q922=makeQuery(id+"F3.opExtrude","CAP_EDGE",EDGE,{"disambiguationData":[OSD([sQuery(id+"F2.wireOp",EDGE,"E2.13.7.1")])],"isStart":false});
            var Q923;
            Q923=makeQuery(id+"F3.opExtrude","CAP_EDGE",EDGE,{"disambiguationData":[OSD([sQuery(id+"F2.wireOp",EDGE,"E3.3.20.7")])],"isStart":false});
            var Q924;
            Q924=makeQuery(id+"F3.opExtrude","CAP_EDGE",EDGE,{"disambiguationData":[OSD([sQuery(id+"F2.wireOp",EDGE,"E2.7.7.1")])],"isStart":false});
            var Q925;
            Q925=makeQuery(id+"F3.opExtrude","CAP_EDGE",EDGE,{"disambiguationData":[OSD([sQuery(id+"F2.wireOp",EDGE,"E2.14.7.1")])],"isStart":false});
            var Q926;
            Q926=makeQuery(id+"F3.opExtrude","CAP_EDGE",EDGE,{"disambiguationData":[OSD([sQuery(id+"F2.wireOp",EDGE,"E2.1.7.1")])],"isStart":false});
            var Q927;
            Q927=makeQuery(id+"F3.opExtrude","CAP_EDGE",EDGE,{"disambiguationData":[OSD([sQuery(id+"F2.wireOp",EDGE,"E2.8.7.1")])],"isStart":false});
            var Q928;
            Q928=makeQuery(id+"F3.opExtrude","CAP_EDGE",EDGE,{"disambiguationData":[OSD([sQuery(id+"F2.wireOp",EDGE,"E3.3.27.7")])],"isStart":false});
            var Q929;
            Q929=makeQuery(id+"F3.opExtrude","CAP_EDGE",EDGE,{"disambiguationData":[OSD([sQuery(id+"F2.wireOp",EDGE,"E2.2.7.1")])],"isStart":false});
            var Q930;
            Q930=makeQuery(id+"F3.opExtrude","CAP_EDGE",EDGE,{"disambiguationData":[OSD([sQuery(id+"F2.wireOp",EDGE,"E3.3.21.7")])],"isStart":false});
            var Q931;
            Q931=makeQuery(id+"F3.opExtrude","CAP_EDGE",EDGE,{"disambiguationData":[OSD([sQuery(id+"F2.wireOp",EDGE,"E3.9.22.7")])],"isStart":false});
            var Q932;
            Q932=makeQuery(id+"F3.opExtrude","CAP_EDGE",EDGE,{"disambiguationData":[OSD([sQuery(id+"F2.wireOp",EDGE,"E3.9.23.7")])],"isStart":false});
            var Q933;
            Q933=makeQuery(id+"F3.opExtrude","CAP_EDGE",EDGE,{"disambiguationData":[OSD([sQuery(id+"F2.wireOp",EDGE,"E2.16.7.3")])],"isStart":false});
            var Q934;
            Q934=makeQuery(id+"F3.opExtrude","CAP_EDGE",EDGE,{"disambiguationData":[OSD([sQuery(id+"F2.wireOp",EDGE,"E2.3.7.3")])],"isStart":false});
            var Q935;
            Q935=makeQuery(id+"F3.opExtrude","CAP_EDGE",EDGE,{"disambiguationData":[OSD([sQuery(id+"F2.wireOp",EDGE,"E2.10.7.3")])],"isStart":false});
            var Q936;
            Q936=makeQuery(id+"F3.opExtrude","CAP_EDGE",EDGE,{"disambiguationData":[OSD([sQuery(id+"F2.wireOp",EDGE,"E3.9.29.7")])],"isStart":false});
            var Q937;
            Q937=makeQuery(id+"F3.opExtrude","CAP_EDGE",EDGE,{"disambiguationData":[OSD([sQuery(id+"F2.wireOp",EDGE,"E3.9.26.7")])],"isStart":false});
            var Q938;
            Q938=makeQuery(id+"F3.opExtrude","CAP_EDGE",EDGE,{"disambiguationData":[OSD([sQuery(id+"F2.wireOp",EDGE,"E2.13.7.3")])],"isStart":false});
            var Q939;
            Q939=makeQuery(id+"F3.opExtrude","CAP_EDGE",EDGE,{"disambiguationData":[OSD([sQuery(id+"F2.wireOp",EDGE,"E3.9.20.7")])],"isStart":false});
            var Q940;
            Q940=makeQuery(id+"F3.opExtrude","CAP_EDGE",EDGE,{"disambiguationData":[OSD([sQuery(id+"F2.wireOp",EDGE,"E2.7.7.3")])],"isStart":false});
            var Q941;
            Q941=makeQuery(id+"F3.opExtrude","CAP_EDGE",EDGE,{"disambiguationData":[OSD([sQuery(id+"F2.wireOp",EDGE,"E2.14.7.3")])],"isStart":false});
            var Q942;
            Q942=makeQuery(id+"F3.opExtrude","CAP_EDGE",EDGE,{"disambiguationData":[OSD([sQuery(id+"F2.wireOp",EDGE,"E2.1.7.3")])],"isStart":false});
            var Q943;
            Q943=makeQuery(id+"F3.opExtrude","CAP_EDGE",EDGE,{"disambiguationData":[OSD([sQuery(id+"F2.wireOp",EDGE,"E2.8.7.3")])],"isStart":false});
            var Q944;
            Q944=makeQuery(id+"F3.opExtrude","CAP_EDGE",EDGE,{"disambiguationData":[OSD([sQuery(id+"F2.wireOp",EDGE,"E3.9.27.7")])],"isStart":false});
            var Q945;
            Q945=makeQuery(id+"F3.opExtrude","CAP_EDGE",EDGE,{"disambiguationData":[OSD([sQuery(id+"F2.wireOp",EDGE,"E2.2.7.3")])],"isStart":false});
            var Q946;
            Q946=makeQuery(id+"F3.opExtrude","CAP_EDGE",EDGE,{"disambiguationData":[OSD([sQuery(id+"F2.wireOp",EDGE,"E3.9.21.7")])],"isStart":false});
            var Q947;
            Q947=makeQuery(id+"F3.opExtrude","CAP_EDGE",EDGE,{"disambiguationData":[OSD([sQuery(id+"F2.wireOp",EDGE,"E3.9.28.7")])],"isStart":false});
            var Q948;
            Q948=makeQuery(id+"F3.opExtrude","CAP_EDGE",EDGE,{"disambiguationData":[OSD([sQuery(id+"F2.wireOp",EDGE,"E2.15.7.3")])],"isStart":false});
            var Q949;
            Q949=makeQuery(id+"F3.opExtrude","CAP_EDGE",EDGE,{"disambiguationData":[OSD([sQuery(id+"F2.wireOp",EDGE,"E2.9.7.3")])],"isStart":false});
            var Q950;
            Q950=makeQuery(id+"F3.opExtrude","CAP_EDGE",EDGE,{"disambiguationData":[OSD([sQuery(id+"F2.wireOp",EDGE,"E2.4.7.3")])],"isStart":false});
            var Q951;
            Q951=makeQuery(id+"F3.opExtrude","CAP_EDGE",EDGE,{"disambiguationData":[OSD([sQuery(id+"F2.wireOp",EDGE,"E2.17.7.3")])],"isStart":false});
            var Q952;
            Q952=makeQuery(id+"F3.opExtrude","CAP_EDGE",EDGE,{"disambiguationData":[OSD([sQuery(id+"F2.wireOp",EDGE,"E3.9.24.7")])],"isStart":false});
            var Q953;
            Q953=makeQuery(id+"F3.opExtrude","CAP_EDGE",EDGE,{"disambiguationData":[OSD([sQuery(id+"F2.wireOp",EDGE,"E2.11.7.3")])],"isStart":false});
            var Q954;
            Q954=makeQuery(id+"F3.opExtrude","CAP_EDGE",EDGE,{"disambiguationData":[OSD([sQuery(id+"F2.wireOp",EDGE,"E2.18.7.3")])],"isStart":false});
            var Q955;
            Q955=makeQuery(id+"F3.opExtrude","CAP_EDGE",EDGE,{"disambiguationData":[OSD([sQuery(id+"F2.wireOp",EDGE,"E2.5.7.3")])],"isStart":false});
            var Q956;
            Q956=makeQuery(id+"F3.opExtrude","CAP_EDGE",EDGE,{"disambiguationData":[OSD([sQuery(id+"F2.wireOp",EDGE,"E2.12.7.3")])],"isStart":false});
            var Q957;
            Q957=makeQuery(id+"F3.opExtrude","CAP_EDGE",EDGE,{"disambiguationData":[OSD([sQuery(id+"F2.wireOp",EDGE,"E2.6.7.3")])],"isStart":false});
            var Q958;
            Q958=makeQuery(id+"F3.opExtrude","CAP_EDGE",EDGE,{"disambiguationData":[OSD([sQuery(id+"F2.wireOp",EDGE,"E3.9.25.7")])],"isStart":false});
            var Q959;
            Q959=makeQuery(id+"F3.opExtrude","CAP_EDGE",EDGE,{"disambiguationData":[OSD([sQuery(id+"F2.wireOp",EDGE,"E2.19.7.3")])],"isStart":false});
            var Q960;
            Q960=makeQuery(id+"F3.opExtrude","CAP_EDGE",EDGE,{"disambiguationData":[OSD([sQuery(id+"F2.wireOp",EDGE,"E2.0.8.3")])],"isStart":false});
            var Q961;
            Q961=makeQuery(id+"F3.opExtrude","CAP_EDGE",EDGE,{"disambiguationData":[OSD([sQuery(id+"F2.wireOp",EDGE,"E2.0.8.0")])],"isStart":false});
            var Q962;
            Q962=makeQuery(id+"F3.opExtrude","CAP_EDGE",EDGE,{"disambiguationData":[OSD([sQuery(id+"F2.wireOp",EDGE,"E2.0.8.2")])],"isStart":false});
            var Q963;
            Q963=makeQuery(id+"F3.opExtrude","CAP_EDGE",EDGE,{"disambiguationData":[OSD([sQuery(id+"F2.wireOp",EDGE,"E2.10.8.3")])],"isStart":false});
            var Q964;
            Q964=makeQuery(id+"F3.opExtrude","CAP_EDGE",EDGE,{"disambiguationData":[OSD([sQuery(id+"F2.wireOp",EDGE,"E3.9.22.8")])],"isStart":false});
            var Q965;
            Q965=makeQuery(id+"F3.opExtrude","CAP_EDGE",EDGE,{"disambiguationData":[OSD([sQuery(id+"F2.wireOp",EDGE,"E2.9.8.3")])],"isStart":false});
            var Q966;
            Q966=makeQuery(id+"F3.opExtrude","CAP_EDGE",EDGE,{"disambiguationData":[OSD([sQuery(id+"F2.wireOp",EDGE,"E2.6.8.3")])],"isStart":false});
            var Q967;
            Q967=makeQuery(id+"F3.opExtrude","CAP_EDGE",EDGE,{"disambiguationData":[OSD([sQuery(id+"F2.wireOp",EDGE,"E3.9.25.8")])],"isStart":false});
            var Q968;
            Q968=makeQuery(id+"F3.opExtrude","CAP_EDGE",EDGE,{"disambiguationData":[OSD([sQuery(id+"F2.wireOp",EDGE,"E2.19.8.3")])],"isStart":false});
            var Q969;
            Q969=makeQuery(id+"F3.opExtrude","CAP_EDGE",EDGE,{"disambiguationData":[OSD([sQuery(id+"F2.wireOp",EDGE,"E2.13.8.3")])],"isStart":false});
            var Q970;
            Q970=makeQuery(id+"F3.opExtrude","CAP_EDGE",EDGE,{"disambiguationData":[OSD([sQuery(id+"F2.wireOp",EDGE,"E2.7.8.3")])],"isStart":false});
            var Q971;
            Q971=makeQuery(id+"F3.opExtrude","CAP_EDGE",EDGE,{"disambiguationData":[OSD([sQuery(id+"F2.wireOp",EDGE,"E3.9.26.8")])],"isStart":false});
            var Q972;
            Q972=makeQuery(id+"F3.opExtrude","CAP_EDGE",EDGE,{"disambiguationData":[OSD([sQuery(id+"F2.wireOp",EDGE,"E2.14.8.3")])],"isStart":false});
            var Q973;
            Q973=makeQuery(id+"F3.opExtrude","CAP_EDGE",EDGE,{"disambiguationData":[OSD([sQuery(id+"F2.wireOp",EDGE,"E3.9.20.8")])],"isStart":false});
            var Q974;
            Q974=makeQuery(id+"F3.opExtrude","CAP_EDGE",EDGE,{"disambiguationData":[OSD([sQuery(id+"F2.wireOp",EDGE,"E2.1.8.3")])],"isStart":false});
            var Q975;
            Q975=makeQuery(id+"F3.opExtrude","CAP_EDGE",EDGE,{"disambiguationData":[OSD([sQuery(id+"F2.wireOp",EDGE,"E2.8.8.3")])],"isStart":false});
            var Q976;
            Q976=makeQuery(id+"F3.opExtrude","CAP_EDGE",EDGE,{"disambiguationData":[OSD([sQuery(id+"F2.wireOp",EDGE,"E3.9.27.8")])],"isStart":false});
            var Q977;
            Q977=makeQuery(id+"F3.opExtrude","CAP_EDGE",EDGE,{"disambiguationData":[OSD([sQuery(id+"F2.wireOp",EDGE,"E2.2.8.3")])],"isStart":false});
            var Q978;
            Q978=makeQuery(id+"F3.opExtrude","CAP_EDGE",EDGE,{"disambiguationData":[OSD([sQuery(id+"F2.wireOp",EDGE,"E3.9.21.8")])],"isStart":false});
            var Q979;
            Q979=makeQuery(id+"F3.opExtrude","CAP_EDGE",EDGE,{"disambiguationData":[OSD([sQuery(id+"F2.wireOp",EDGE,"E2.16.8.3")])],"isStart":false});
            var Q980;
            Q980=makeQuery(id+"F3.opExtrude","CAP_EDGE",EDGE,{"disambiguationData":[OSD([sQuery(id+"F2.wireOp",EDGE,"E2.3.8.3")])],"isStart":false});
            var Q981;
            Q981=makeQuery(id+"F3.opExtrude","CAP_EDGE",EDGE,{"disambiguationData":[OSD([sQuery(id+"F2.wireOp",EDGE,"E3.9.29.8")])],"isStart":false});
            var Q982;
            Q982=makeQuery(id+"F3.opExtrude","CAP_EDGE",EDGE,{"disambiguationData":[OSD([sQuery(id+"F2.wireOp",EDGE,"E2.4.8.3")])],"isStart":false});
            var Q983;
            Q983=makeQuery(id+"F3.opExtrude","CAP_EDGE",EDGE,{"disambiguationData":[OSD([sQuery(id+"F2.wireOp",EDGE,"E3.9.23.8")])],"isStart":false});
            var Q984;
            Q984=makeQuery(id+"F3.opExtrude","CAP_EDGE",EDGE,{"disambiguationData":[OSD([sQuery(id+"F2.wireOp",EDGE,"E2.17.8.3")])],"isStart":false});
            var Q985;
            Q985=makeQuery(id+"F3.opExtrude","CAP_EDGE",EDGE,{"disambiguationData":[OSD([sQuery(id+"F2.wireOp",EDGE,"E3.9.24.8")])],"isStart":false});
            var Q986;
            Q986=makeQuery(id+"F3.opExtrude","CAP_EDGE",EDGE,{"disambiguationData":[OSD([sQuery(id+"F2.wireOp",EDGE,"E2.11.8.3")])],"isStart":false});
            var Q987;
            Q987=makeQuery(id+"F3.opExtrude","CAP_EDGE",EDGE,{"disambiguationData":[OSD([sQuery(id+"F2.wireOp",EDGE,"E2.18.8.3")])],"isStart":false});
            var Q988;
            Q988=makeQuery(id+"F3.opExtrude","CAP_EDGE",EDGE,{"disambiguationData":[OSD([sQuery(id+"F2.wireOp",EDGE,"E2.5.8.3")])],"isStart":false});
            var Q989;
            Q989=makeQuery(id+"F3.opExtrude","CAP_EDGE",EDGE,{"disambiguationData":[OSD([sQuery(id+"F2.wireOp",EDGE,"E2.12.8.3")])],"isStart":false});
            var Q990;
            Q990=makeQuery(id+"F3.opExtrude","CAP_EDGE",EDGE,{"disambiguationData":[OSD([sQuery(id+"F2.wireOp",EDGE,"E2.10.8.0")])],"isStart":false});
            var Q991;
            Q991=makeQuery(id+"F3.opExtrude","CAP_EDGE",EDGE,{"disambiguationData":[OSD([sQuery(id+"F2.wireOp",EDGE,"E2.9.8.0")])],"isStart":false});
            var Q992;
            Q992=makeQuery(id+"F3.opExtrude","CAP_EDGE",EDGE,{"disambiguationData":[OSD([sQuery(id+"F2.wireOp",EDGE,"E2.3.8.0")])],"isStart":false});
            var Q993;
            Q993=makeQuery(id+"F3.opExtrude","CAP_EDGE",EDGE,{"disambiguationData":[OSD([sQuery(id+"F2.wireOp",EDGE,"E3.0.22.8")])],"isStart":false});
            var Q994;
            Q994=makeQuery(id+"F3.opExtrude","CAP_EDGE",EDGE,{"disambiguationData":[OSD([sQuery(id+"F2.wireOp",EDGE,"E3.0.29.8")])],"isStart":false});
            var Q995;
            Q995=makeQuery(id+"F3.opExtrude","CAP_EDGE",EDGE,{"disambiguationData":[OSD([sQuery(id+"F2.wireOp",EDGE,"E2.16.8.0")])],"isStart":false});
            var Q996;
            Q996=makeQuery(id+"F3.opExtrude","CAP_EDGE",EDGE,{"disambiguationData":[OSD([sQuery(id+"F2.wireOp",EDGE,"E3.9.28.8")])],"isStart":false});
            var Q997;
            Q997=makeQuery(id+"F3.opExtrude","CAP_EDGE",EDGE,{"disambiguationData":[OSD([sQuery(id+"F2.wireOp",EDGE,"E2.15.8.3")])],"isStart":false});
            var Q998;
            Q998=makeQuery(id+"F3.opExtrude","CAP_EDGE",EDGE,{"disambiguationData":[OSD([sQuery(id+"F2.wireOp",EDGE,"E3.0.26.8")])],"isStart":false});
            var Q999;
            Q999=makeQuery(id+"F3.opExtrude","CAP_EDGE",EDGE,{"disambiguationData":[OSD([sQuery(id+"F2.wireOp",EDGE,"E2.13.8.0")])],"isStart":false});
            var Q1000;
            Q1000=makeQuery(id+"F3.opExtrude","CAP_EDGE",EDGE,{"disambiguationData":[OSD([sQuery(id+"F2.wireOp",EDGE,"E3.0.20.8")])],"isStart":false});
            var Q1001;
            Q1001=makeQuery(id+"F3.opExtrude","CAP_EDGE",EDGE,{"disambiguationData":[OSD([sQuery(id+"F2.wireOp",EDGE,"E2.7.8.0")])],"isStart":false});
            var Q1002;
            Q1002=makeQuery(id+"F3.opExtrude","CAP_EDGE",EDGE,{"disambiguationData":[OSD([sQuery(id+"F2.wireOp",EDGE,"E2.14.8.0")])],"isStart":false});
            var Q1003;
            Q1003=makeQuery(id+"F3.opExtrude","CAP_EDGE",EDGE,{"disambiguationData":[OSD([sQuery(id+"F2.wireOp",EDGE,"E2.1.8.0")])],"isStart":false});
            var Q1004;
            Q1004=makeQuery(id+"F3.opExtrude","CAP_EDGE",EDGE,{"disambiguationData":[OSD([sQuery(id+"F2.wireOp",EDGE,"E2.8.8.0")])],"isStart":false});
            var Q1005;
            Q1005=makeQuery(id+"F3.opExtrude","CAP_EDGE",EDGE,{"disambiguationData":[OSD([sQuery(id+"F2.wireOp",EDGE,"E3.0.27.8")])],"isStart":false});
            var Q1006;
            Q1006=makeQuery(id+"F3.opExtrude","CAP_EDGE",EDGE,{"disambiguationData":[OSD([sQuery(id+"F2.wireOp",EDGE,"E2.2.8.0")])],"isStart":false});
            var Q1007;
            Q1007=makeQuery(id+"F3.opExtrude","CAP_EDGE",EDGE,{"disambiguationData":[OSD([sQuery(id+"F2.wireOp",EDGE,"E3.0.21.8")])],"isStart":false});
            var Q1008;
            Q1008=makeQuery(id+"F3.opExtrude","CAP_EDGE",EDGE,{"disambiguationData":[OSD([sQuery(id+"F2.wireOp",EDGE,"E3.0.28.8")])],"isStart":false});
            var Q1009;
            Q1009=makeQuery(id+"F3.opExtrude","CAP_EDGE",EDGE,{"disambiguationData":[OSD([sQuery(id+"F2.wireOp",EDGE,"E2.15.8.0")])],"isStart":false});
            var Q1010;
            Q1010=makeQuery(id+"F3.opExtrude","CAP_EDGE",EDGE,{"disambiguationData":[OSD([sQuery(id+"F2.wireOp",EDGE,"E2.4.8.0")])],"isStart":false});
            var Q1011;
            Q1011=makeQuery(id+"F3.opExtrude","CAP_EDGE",EDGE,{"disambiguationData":[OSD([sQuery(id+"F2.wireOp",EDGE,"E3.0.23.8")])],"isStart":false});
            var Q1012;
            Q1012=makeQuery(id+"F3.opExtrude","CAP_EDGE",EDGE,{"disambiguationData":[OSD([sQuery(id+"F2.wireOp",EDGE,"E2.17.8.0")])],"isStart":false});
            var Q1013;
            Q1013=makeQuery(id+"F3.opExtrude","CAP_EDGE",EDGE,{"disambiguationData":[OSD([sQuery(id+"F2.wireOp",EDGE,"E3.0.24.8")])],"isStart":false});
            var Q1014;
            Q1014=makeQuery(id+"F3.opExtrude","CAP_EDGE",EDGE,{"disambiguationData":[OSD([sQuery(id+"F2.wireOp",EDGE,"E2.5.8.0")])],"isStart":false});
            var Q1015;
            Q1015=makeQuery(id+"F3.opExtrude","CAP_EDGE",EDGE,{"disambiguationData":[OSD([sQuery(id+"F2.wireOp",EDGE,"E2.11.8.0")])],"isStart":false});
            var Q1016;
            Q1016=makeQuery(id+"F3.opExtrude","CAP_EDGE",EDGE,{"disambiguationData":[OSD([sQuery(id+"F2.wireOp",EDGE,"E2.18.8.0")])],"isStart":false});
            var Q1017;
            Q1017=makeQuery(id+"F3.opExtrude","CAP_EDGE",EDGE,{"disambiguationData":[OSD([sQuery(id+"F2.wireOp",EDGE,"E3.0.25.8")])],"isStart":false});
            var Q1018;
            Q1018=makeQuery(id+"F3.opExtrude","CAP_EDGE",EDGE,{"disambiguationData":[OSD([sQuery(id+"F2.wireOp",EDGE,"E2.12.8.0")])],"isStart":false});
            var Q1019;
            Q1019=makeQuery(id+"F3.opExtrude","CAP_EDGE",EDGE,{"disambiguationData":[OSD([sQuery(id+"F2.wireOp",EDGE,"E2.19.8.0")])],"isStart":false});
            var Q1020;
            Q1020=makeQuery(id+"F3.opExtrude","CAP_EDGE",EDGE,{"disambiguationData":[OSD([sQuery(id+"F2.wireOp",EDGE,"E2.6.8.0")])],"isStart":false});
            var Q1021;
            Q1021=makeQuery(id+"F3.opExtrude","CAP_EDGE",EDGE,{"disambiguationData":[OSD([sQuery(id+"F2.wireOp",EDGE,"E2.0.8.1")])],"isStart":false});
            var Q1022;
            Q1022=makeQuery(id+"F3.opExtrude","CAP_EDGE",EDGE,{"disambiguationData":[OSD([sQuery(id+"F2.wireOp",EDGE,"E3.6.29.8")])],"isStart":false});
            var Q1023;
            Q1023=makeQuery(id+"F3.opExtrude","CAP_EDGE",EDGE,{"disambiguationData":[OSD([sQuery(id+"F2.wireOp",EDGE,"E2.4.8.2")])],"isStart":false});
            var Q1024;
            Q1024=makeQuery(id+"F3.opExtrude","CAP_EDGE",EDGE,{"disambiguationData":[OSD([sQuery(id+"F2.wireOp",EDGE,"E3.6.23.8")])],"isStart":false});
            var Q1025;
            Q1025=makeQuery(id+"F3.opExtrude","CAP_EDGE",EDGE,{"disambiguationData":[OSD([sQuery(id+"F2.wireOp",EDGE,"E2.17.8.2")])],"isStart":false});
            var Q1026;
            Q1026=makeQuery(id+"F3.opExtrude","CAP_EDGE",EDGE,{"disambiguationData":[OSD([sQuery(id+"F2.wireOp",EDGE,"E3.6.24.8")])],"isStart":false});
            var Q1027;
            Q1027=makeQuery(id+"F3.opExtrude","CAP_EDGE",EDGE,{"disambiguationData":[OSD([sQuery(id+"F2.wireOp",EDGE,"E2.11.8.2")])],"isStart":false});
            var Q1028;
            Q1028=makeQuery(id+"F3.opExtrude","CAP_EDGE",EDGE,{"disambiguationData":[OSD([sQuery(id+"F2.wireOp",EDGE,"E2.18.8.2")])],"isStart":false});
            var Q1029;
            Q1029=makeQuery(id+"F3.opExtrude","CAP_EDGE",EDGE,{"disambiguationData":[OSD([sQuery(id+"F2.wireOp",EDGE,"E2.5.8.2")])],"isStart":false});
            var Q1030;
            Q1030=makeQuery(id+"F3.opExtrude","CAP_EDGE",EDGE,{"disambiguationData":[OSD([sQuery(id+"F2.wireOp",EDGE,"E2.12.8.2")])],"isStart":false});
            var Q1031;
            Q1031=makeQuery(id+"F3.opExtrude","CAP_EDGE",EDGE,{"disambiguationData":[OSD([sQuery(id+"F2.wireOp",EDGE,"E2.6.8.2")])],"isStart":false});
            var Q1032;
            Q1032=makeQuery(id+"F3.opExtrude","CAP_EDGE",EDGE,{"disambiguationData":[OSD([sQuery(id+"F2.wireOp",EDGE,"E3.6.25.8")])],"isStart":false});
            var Q1033;
            Q1033=makeQuery(id+"F3.opExtrude","CAP_EDGE",EDGE,{"disambiguationData":[OSD([sQuery(id+"F2.wireOp",EDGE,"E2.10.8.2")])],"isStart":false});
            var Q1034;
            Q1034=makeQuery(id+"F3.opExtrude","CAP_EDGE",EDGE,{"disambiguationData":[OSD([sQuery(id+"F2.wireOp",EDGE,"E3.6.22.8")])],"isStart":false});
            var Q1035;
            Q1035=makeQuery(id+"F3.opExtrude","CAP_EDGE",EDGE,{"disambiguationData":[OSD([sQuery(id+"F2.wireOp",EDGE,"E2.9.8.2")])],"isStart":false});
            var Q1036;
            Q1036=makeQuery(id+"F3.opExtrude","CAP_EDGE",EDGE,{"disambiguationData":[OSD([sQuery(id+"F2.wireOp",EDGE,"E2.16.8.2")])],"isStart":false});
            var Q1037;
            Q1037=makeQuery(id+"F3.opExtrude","CAP_EDGE",EDGE,{"disambiguationData":[OSD([sQuery(id+"F2.wireOp",EDGE,"E2.3.8.2")])],"isStart":false});
            var Q1038;
            Q1038=makeQuery(id+"F3.opExtrude","CAP_EDGE",EDGE,{"disambiguationData":[OSD([sQuery(id+"F2.wireOp",EDGE,"E2.19.8.2")])],"isStart":false});
            var Q1039;
            Q1039=makeQuery(id+"F3.opExtrude","CAP_EDGE",EDGE,{"disambiguationData":[OSD([sQuery(id+"F2.wireOp",EDGE,"E3.6.26.8")])],"isStart":false});
            var Q1040;
            Q1040=makeQuery(id+"F3.opExtrude","CAP_EDGE",EDGE,{"disambiguationData":[OSD([sQuery(id+"F2.wireOp",EDGE,"E2.13.8.2")])],"isStart":false});
            var Q1041;
            Q1041=makeQuery(id+"F3.opExtrude","CAP_EDGE",EDGE,{"disambiguationData":[OSD([sQuery(id+"F2.wireOp",EDGE,"E3.6.20.8")])],"isStart":false});
            var Q1042;
            Q1042=makeQuery(id+"F3.opExtrude","CAP_EDGE",EDGE,{"disambiguationData":[OSD([sQuery(id+"F2.wireOp",EDGE,"E2.7.8.2")])],"isStart":false});
            var Q1043;
            Q1043=makeQuery(id+"F3.opExtrude","CAP_EDGE",EDGE,{"disambiguationData":[OSD([sQuery(id+"F2.wireOp",EDGE,"E2.14.8.2")])],"isStart":false});
            var Q1044;
            Q1044=makeQuery(id+"F3.opExtrude","CAP_EDGE",EDGE,{"disambiguationData":[OSD([sQuery(id+"F2.wireOp",EDGE,"E2.1.8.2")])],"isStart":false});
            var Q1045;
            Q1045=makeQuery(id+"F3.opExtrude","CAP_EDGE",EDGE,{"disambiguationData":[OSD([sQuery(id+"F2.wireOp",EDGE,"E2.8.8.2")])],"isStart":false});
            var Q1046;
            Q1046=makeQuery(id+"F3.opExtrude","CAP_EDGE",EDGE,{"disambiguationData":[OSD([sQuery(id+"F2.wireOp",EDGE,"E3.6.27.8")])],"isStart":false});
            var Q1047;
            Q1047=makeQuery(id+"F3.opExtrude","CAP_EDGE",EDGE,{"disambiguationData":[OSD([sQuery(id+"F2.wireOp",EDGE,"E2.2.8.2")])],"isStart":false});
            var Q1048;
            Q1048=makeQuery(id+"F3.opExtrude","CAP_EDGE",EDGE,{"disambiguationData":[OSD([sQuery(id+"F2.wireOp",EDGE,"E3.6.21.8")])],"isStart":false});
            var Q1049;
            Q1049=makeQuery(id+"F3.opExtrude","CAP_EDGE",EDGE,{"disambiguationData":[OSD([sQuery(id+"F2.wireOp",EDGE,"E3.6.28.8")])],"isStart":false});
            var Q1050;
            Q1050=makeQuery(id+"F3.opExtrude","CAP_EDGE",EDGE,{"disambiguationData":[OSD([sQuery(id+"F2.wireOp",EDGE,"E2.15.8.2")])],"isStart":false});
            var Q1051;
            Q1051=makeQuery(id+"F3.opExtrude","CAP_EDGE",EDGE,{"disambiguationData":[OSD([sQuery(id+"F2.wireOp",EDGE,"E2.10.8.1")])],"isStart":false});
            var Q1052;
            Q1052=makeQuery(id+"F3.opExtrude","CAP_EDGE",EDGE,{"disambiguationData":[OSD([sQuery(id+"F2.wireOp",EDGE,"E3.3.22.8")])],"isStart":false});
            var Q1053;
            Q1053=makeQuery(id+"F3.opExtrude","CAP_EDGE",EDGE,{"disambiguationData":[OSD([sQuery(id+"F2.wireOp",EDGE,"E2.3.8.1")])],"isStart":false});
            var Q1054;
            Q1054=makeQuery(id+"F3.opExtrude","CAP_EDGE",EDGE,{"disambiguationData":[OSD([sQuery(id+"F2.wireOp",EDGE,"E2.9.8.1")])],"isStart":false});
            var Q1055;
            Q1055=makeQuery(id+"F3.opExtrude","CAP_EDGE",EDGE,{"disambiguationData":[OSD([sQuery(id+"F2.wireOp",EDGE,"E3.3.29.8")])],"isStart":false});
            var Q1056;
            Q1056=makeQuery(id+"F3.opExtrude","CAP_EDGE",EDGE,{"disambiguationData":[OSD([sQuery(id+"F2.wireOp",EDGE,"E2.16.8.1")])],"isStart":false});
            var Q1057;
            Q1057=makeQuery(id+"F3.opExtrude","CAP_EDGE",EDGE,{"disambiguationData":[OSD([sQuery(id+"F2.wireOp",EDGE,"E2.4.8.1")])],"isStart":false});
            var Q1058;
            Q1058=makeQuery(id+"F3.opExtrude","CAP_EDGE",EDGE,{"disambiguationData":[OSD([sQuery(id+"F2.wireOp",EDGE,"E3.3.23.8")])],"isStart":false});
            var Q1059;
            Q1059=makeQuery(id+"F3.opExtrude","CAP_EDGE",EDGE,{"disambiguationData":[OSD([sQuery(id+"F2.wireOp",EDGE,"E2.17.8.1")])],"isStart":false});
            var Q1060;
            Q1060=makeQuery(id+"F3.opExtrude","CAP_EDGE",EDGE,{"disambiguationData":[OSD([sQuery(id+"F2.wireOp",EDGE,"E2.14.8.1")])],"isStart":false});
            var Q1061;
            Q1061=makeQuery(id+"F3.opExtrude","CAP_EDGE",EDGE,{"disambiguationData":[OSD([sQuery(id+"F2.wireOp",EDGE,"E2.1.8.1")])],"isStart":false});
            var Q1062;
            Q1062=makeQuery(id+"F3.opExtrude","CAP_EDGE",EDGE,{"disambiguationData":[OSD([sQuery(id+"F2.wireOp",EDGE,"E2.8.8.1")])],"isStart":false});
            var Q1063;
            Q1063=makeQuery(id+"F3.opExtrude","CAP_EDGE",EDGE,{"disambiguationData":[OSD([sQuery(id+"F2.wireOp",EDGE,"E3.3.27.8")])],"isStart":false});
            var Q1064;
            Q1064=makeQuery(id+"F3.opExtrude","CAP_EDGE",EDGE,{"disambiguationData":[OSD([sQuery(id+"F2.wireOp",EDGE,"E2.2.8.1")])],"isStart":false});
            var Q1065;
            Q1065=makeQuery(id+"F3.opExtrude","CAP_EDGE",EDGE,{"disambiguationData":[OSD([sQuery(id+"F2.wireOp",EDGE,"E3.3.21.8")])],"isStart":false});
            var Q1066;
            Q1066=makeQuery(id+"F3.opExtrude","CAP_EDGE",EDGE,{"disambiguationData":[OSD([sQuery(id+"F2.wireOp",EDGE,"E3.3.28.8")])],"isStart":false});
            var Q1067;
            Q1067=makeQuery(id+"F3.opExtrude","CAP_EDGE",EDGE,{"disambiguationData":[OSD([sQuery(id+"F2.wireOp",EDGE,"E2.15.8.1")])],"isStart":false});
            var Q1068;
            Q1068=makeQuery(id+"F3.opExtrude","CAP_EDGE",EDGE,{"disambiguationData":[OSD([sQuery(id+"F2.wireOp",EDGE,"E3.3.24.8")])],"isStart":false});
            var Q1069;
            Q1069=makeQuery(id+"F3.opExtrude","CAP_EDGE",EDGE,{"disambiguationData":[OSD([sQuery(id+"F2.wireOp",EDGE,"E2.11.8.1")])],"isStart":false});
            var Q1070;
            Q1070=makeQuery(id+"F3.opExtrude","CAP_EDGE",EDGE,{"disambiguationData":[OSD([sQuery(id+"F2.wireOp",EDGE,"E2.18.8.1")])],"isStart":false});
            var Q1071;
            Q1071=makeQuery(id+"F3.opExtrude","CAP_EDGE",EDGE,{"disambiguationData":[OSD([sQuery(id+"F2.wireOp",EDGE,"E2.5.8.1")])],"isStart":false});
            var Q1072;
            Q1072=makeQuery(id+"F3.opExtrude","CAP_EDGE",EDGE,{"disambiguationData":[OSD([sQuery(id+"F2.wireOp",EDGE,"E2.12.8.1")])],"isStart":false});
            var Q1073;
            Q1073=makeQuery(id+"F3.opExtrude","CAP_EDGE",EDGE,{"disambiguationData":[OSD([sQuery(id+"F2.wireOp",EDGE,"E2.19.8.1")])],"isStart":false});
            var Q1074;
            Q1074=makeQuery(id+"F3.opExtrude","CAP_EDGE",EDGE,{"disambiguationData":[OSD([sQuery(id+"F2.wireOp",EDGE,"E3.3.25.8")])],"isStart":false});
            var Q1075;
            Q1075=makeQuery(id+"F3.opExtrude","CAP_EDGE",EDGE,{"disambiguationData":[OSD([sQuery(id+"F2.wireOp",EDGE,"E2.6.8.1")])],"isStart":false});
            var Q1076;
            Q1076=makeQuery(id+"F3.opExtrude","CAP_EDGE",EDGE,{"disambiguationData":[OSD([sQuery(id+"F2.wireOp",EDGE,"E3.3.26.8")])],"isStart":false});
            var Q1077;
            Q1077=makeQuery(id+"F3.opExtrude","CAP_EDGE",EDGE,{"disambiguationData":[OSD([sQuery(id+"F2.wireOp",EDGE,"E2.13.8.1")])],"isStart":false});
            var Q1078;
            Q1078=makeQuery(id+"F3.opExtrude","CAP_EDGE",EDGE,{"disambiguationData":[OSD([sQuery(id+"F2.wireOp",EDGE,"E3.3.20.8")])],"isStart":false});
            var Q1079;
            Q1079=makeQuery(id+"F3.opExtrude","CAP_EDGE",EDGE,{"disambiguationData":[OSD([sQuery(id+"F2.wireOp",EDGE,"E2.7.8.1")])],"isStart":false});
            var Q1080;
            Q1080=makeQuery(id+"F3.opExtrude","CAP_EDGE",EDGE,{"disambiguationData":[OSD([sQuery(id+"F2.wireOp",EDGE,"E2.0.9.0")])],"isStart":false});
            var Q1081;
            Q1081=makeQuery(id+"F3.opExtrude","CAP_EDGE",EDGE,{"disambiguationData":[OSD([sQuery(id+"F2.wireOp",EDGE,"E2.0.9.2")])],"isStart":false});
            var Q1082;
            Q1082=makeQuery(id+"F3.opExtrude","CAP_EDGE",EDGE,{"disambiguationData":[OSD([sQuery(id+"F2.wireOp",EDGE,"E2.10.9.0")])],"isStart":false});
            var Q1083;
            Q1083=makeQuery(id+"F3.opExtrude","CAP_EDGE",EDGE,{"disambiguationData":[OSD([sQuery(id+"F2.wireOp",EDGE,"E3.0.22.9")])],"isStart":false});
            var Q1084;
            Q1084=makeQuery(id+"F3.opExtrude","CAP_EDGE",EDGE,{"disambiguationData":[OSD([sQuery(id+"F2.wireOp",EDGE,"E2.9.9.0")])],"isStart":false});
            var Q1085;
            Q1085=makeQuery(id+"F3.opExtrude","CAP_EDGE",EDGE,{"disambiguationData":[OSD([sQuery(id+"F2.wireOp",EDGE,"E2.16.9.0")])],"isStart":false});
            var Q1086;
            Q1086=makeQuery(id+"F3.opExtrude","CAP_EDGE",EDGE,{"disambiguationData":[OSD([sQuery(id+"F2.wireOp",EDGE,"E2.3.9.0")])],"isStart":false});
            var Q1087;
            Q1087=makeQuery(id+"F3.opExtrude","CAP_EDGE",EDGE,{"disambiguationData":[OSD([sQuery(id+"F2.wireOp",EDGE,"E3.0.29.9")])],"isStart":false});
            var Q1088;
            Q1088=makeQuery(id+"F3.opExtrude","CAP_EDGE",EDGE,{"disambiguationData":[OSD([sQuery(id+"F2.wireOp",EDGE,"E2.4.9.0")])],"isStart":false});
            var Q1089;
            Q1089=makeQuery(id+"F3.opExtrude","CAP_EDGE",EDGE,{"disambiguationData":[OSD([sQuery(id+"F2.wireOp",EDGE,"E3.0.23.9")])],"isStart":false});
            var Q1090;
            Q1090=makeQuery(id+"F3.opExtrude","CAP_EDGE",EDGE,{"disambiguationData":[OSD([sQuery(id+"F2.wireOp",EDGE,"E2.7.9.0")])],"isStart":false});
            var Q1091;
            Q1091=makeQuery(id+"F3.opExtrude","CAP_EDGE",EDGE,{"disambiguationData":[OSD([sQuery(id+"F2.wireOp",EDGE,"E3.0.26.9")])],"isStart":false});
            var Q1092;
            Q1092=makeQuery(id+"F3.opExtrude","CAP_EDGE",EDGE,{"disambiguationData":[OSD([sQuery(id+"F2.wireOp",EDGE,"E2.1.9.0")])],"isStart":false});
            var Q1093;
            Q1093=makeQuery(id+"F3.opExtrude","CAP_EDGE",EDGE,{"disambiguationData":[OSD([sQuery(id+"F2.wireOp",EDGE,"E3.0.20.9")])],"isStart":false});
            var Q1094;
            Q1094=makeQuery(id+"F3.opExtrude","CAP_EDGE",EDGE,{"disambiguationData":[OSD([sQuery(id+"F2.wireOp",EDGE,"E3.0.27.9")])],"isStart":false});
            var Q1095;
            Q1095=makeQuery(id+"F3.opExtrude","CAP_EDGE",EDGE,{"disambiguationData":[OSD([sQuery(id+"F2.wireOp",EDGE,"E2.14.9.0")])],"isStart":false});
            var Q1096;
            Q1096=makeQuery(id+"F3.opExtrude","CAP_EDGE",EDGE,{"disambiguationData":[OSD([sQuery(id+"F2.wireOp",EDGE,"E3.0.21.9")])],"isStart":false});
            var Q1097;
            Q1097=makeQuery(id+"F3.opExtrude","CAP_EDGE",EDGE,{"disambiguationData":[OSD([sQuery(id+"F2.wireOp",EDGE,"E2.2.9.0")])],"isStart":false});
            var Q1098;
            Q1098=makeQuery(id+"F3.opExtrude","CAP_EDGE",EDGE,{"disambiguationData":[OSD([sQuery(id+"F2.wireOp",EDGE,"E2.8.9.0")])],"isStart":false});
            var Q1099;
            Q1099=makeQuery(id+"F3.opExtrude","CAP_EDGE",EDGE,{"disambiguationData":[OSD([sQuery(id+"F2.wireOp",EDGE,"E3.0.28.9")])],"isStart":false});
            var Q1100;
            Q1100=makeQuery(id+"F3.opExtrude","CAP_EDGE",EDGE,{"disambiguationData":[OSD([sQuery(id+"F2.wireOp",EDGE,"E2.15.9.0")])],"isStart":false});
            var Q1101;
            Q1101=makeQuery(id+"F3.opExtrude","CAP_EDGE",EDGE,{"disambiguationData":[OSD([sQuery(id+"F2.wireOp",EDGE,"E2.17.9.0")])],"isStart":false});
            var Q1102;
            Q1102=makeQuery(id+"F3.opExtrude","CAP_EDGE",EDGE,{"disambiguationData":[OSD([sQuery(id+"F2.wireOp",EDGE,"E3.0.24.9")])],"isStart":false});
            var Q1103;
            Q1103=makeQuery(id+"F3.opExtrude","CAP_EDGE",EDGE,{"disambiguationData":[OSD([sQuery(id+"F2.wireOp",EDGE,"E2.11.9.0")])],"isStart":false});
            var Q1104;
            Q1104=makeQuery(id+"F3.opExtrude","CAP_EDGE",EDGE,{"disambiguationData":[OSD([sQuery(id+"F2.wireOp",EDGE,"E2.18.9.0")])],"isStart":false});
            var Q1105;
            Q1105=makeQuery(id+"F3.opExtrude","CAP_EDGE",EDGE,{"disambiguationData":[OSD([sQuery(id+"F2.wireOp",EDGE,"E2.5.9.0")])],"isStart":false});
            var Q1106;
            Q1106=makeQuery(id+"F3.opExtrude","CAP_EDGE",EDGE,{"disambiguationData":[OSD([sQuery(id+"F2.wireOp",EDGE,"E2.12.9.0")])],"isStart":false});
            var Q1107;
            Q1107=makeQuery(id+"F3.opExtrude","CAP_EDGE",EDGE,{"disambiguationData":[OSD([sQuery(id+"F2.wireOp",EDGE,"E2.6.9.0")])],"isStart":false});
            var Q1108;
            Q1108=makeQuery(id+"F3.opExtrude","CAP_EDGE",EDGE,{"disambiguationData":[OSD([sQuery(id+"F2.wireOp",EDGE,"E3.0.25.9")])],"isStart":false});
            var Q1109;
            Q1109=makeQuery(id+"F3.opExtrude","CAP_EDGE",EDGE,{"disambiguationData":[OSD([sQuery(id+"F2.wireOp",EDGE,"E2.19.9.0")])],"isStart":false});
            var Q1110;
            Q1110=makeQuery(id+"F3.opExtrude","CAP_EDGE",EDGE,{"disambiguationData":[OSD([sQuery(id+"F2.wireOp",EDGE,"E2.13.9.0")])],"isStart":false});
            var Q1111;
            Q1111=makeQuery(id+"F3.opExtrude","CAP_EDGE",EDGE,{"disambiguationData":[OSD([sQuery(id+"F2.wireOp",EDGE,"E2.10.9.2")])],"isStart":false});
            var Q1112;
            Q1112=makeQuery(id+"F3.opExtrude","CAP_EDGE",EDGE,{"disambiguationData":[OSD([sQuery(id+"F2.wireOp",EDGE,"E2.12.9.2")])],"isStart":false});
            var Q1113;
            Q1113=makeQuery(id+"F3.opExtrude","CAP_EDGE",EDGE,{"disambiguationData":[OSD([sQuery(id+"F2.wireOp",EDGE,"E2.6.9.2")])],"isStart":false});
            var Q1114;
            Q1114=makeQuery(id+"F3.opExtrude","CAP_EDGE",EDGE,{"disambiguationData":[OSD([sQuery(id+"F2.wireOp",EDGE,"E3.6.25.9")])],"isStart":false});
            var Q1115;
            Q1115=makeQuery(id+"F3.opExtrude","CAP_EDGE",EDGE,{"disambiguationData":[OSD([sQuery(id+"F2.wireOp",EDGE,"E2.19.9.2")])],"isStart":false});
            var Q1116;
            Q1116=makeQuery(id+"F3.opExtrude","CAP_EDGE",EDGE,{"disambiguationData":[OSD([sQuery(id+"F2.wireOp",EDGE,"E2.13.9.2")])],"isStart":false});
            var Q1117;
            Q1117=makeQuery(id+"F3.opExtrude","CAP_EDGE",EDGE,{"disambiguationData":[OSD([sQuery(id+"F2.wireOp",EDGE,"E2.7.9.2")])],"isStart":false});
            var Q1118;
            Q1118=makeQuery(id+"F3.opExtrude","CAP_EDGE",EDGE,{"disambiguationData":[OSD([sQuery(id+"F2.wireOp",EDGE,"E3.6.26.9")])],"isStart":false});
            var Q1119;
            Q1119=makeQuery(id+"F3.opExtrude","CAP_EDGE",EDGE,{"disambiguationData":[OSD([sQuery(id+"F2.wireOp",EDGE,"E2.1.9.2")])],"isStart":false});
            var Q1120;
            Q1120=makeQuery(id+"F3.opExtrude","CAP_EDGE",EDGE,{"disambiguationData":[OSD([sQuery(id+"F2.wireOp",EDGE,"E3.6.20.9")])],"isStart":false});
            var Q1121;
            Q1121=makeQuery(id+"F3.opExtrude","CAP_EDGE",EDGE,{"disambiguationData":[OSD([sQuery(id+"F2.wireOp",EDGE,"E3.6.27.9")])],"isStart":false});
            var Q1122;
            Q1122=makeQuery(id+"F3.opExtrude","CAP_EDGE",EDGE,{"disambiguationData":[OSD([sQuery(id+"F2.wireOp",EDGE,"E2.14.9.2")])],"isStart":false});
            var Q1123;
            Q1123=makeQuery(id+"F3.opExtrude","CAP_EDGE",EDGE,{"disambiguationData":[OSD([sQuery(id+"F2.wireOp",EDGE,"E3.6.22.9")])],"isStart":false});
            var Q1124;
            Q1124=makeQuery(id+"F3.opExtrude","CAP_EDGE",EDGE,{"disambiguationData":[OSD([sQuery(id+"F2.wireOp",EDGE,"E2.9.9.2")])],"isStart":false});
            var Q1125;
            Q1125=makeQuery(id+"F3.opExtrude","CAP_EDGE",EDGE,{"disambiguationData":[OSD([sQuery(id+"F2.wireOp",EDGE,"E2.16.9.2")])],"isStart":false});
            var Q1126;
            Q1126=makeQuery(id+"F3.opExtrude","CAP_EDGE",EDGE,{"disambiguationData":[OSD([sQuery(id+"F2.wireOp",EDGE,"E2.3.9.2")])],"isStart":false});
            var Q1127;
            Q1127=makeQuery(id+"F3.opExtrude","CAP_EDGE",EDGE,{"disambiguationData":[OSD([sQuery(id+"F2.wireOp",EDGE,"E3.6.29.9")])],"isStart":false});
            var Q1128;
            Q1128=makeQuery(id+"F3.opExtrude","CAP_EDGE",EDGE,{"disambiguationData":[OSD([sQuery(id+"F2.wireOp",EDGE,"E2.0.9.1")])],"isStart":false});
            var Q1129;
            Q1129=makeQuery(id+"F3.opExtrude","CAP_EDGE",EDGE,{"disambiguationData":[OSD([sQuery(id+"F2.wireOp",EDGE,"E2.4.9.2")])],"isStart":false});
            var Q1130;
            Q1130=makeQuery(id+"F3.opExtrude","CAP_EDGE",EDGE,{"disambiguationData":[OSD([sQuery(id+"F2.wireOp",EDGE,"E3.6.23.9")])],"isStart":false});
            var Q1131;
            Q1131=makeQuery(id+"F3.opExtrude","CAP_EDGE",EDGE,{"disambiguationData":[OSD([sQuery(id+"F2.wireOp",EDGE,"E2.17.9.2")])],"isStart":false});
            var Q1132;
            Q1132=makeQuery(id+"F3.opExtrude","CAP_EDGE",EDGE,{"disambiguationData":[OSD([sQuery(id+"F2.wireOp",EDGE,"E3.6.24.9")])],"isStart":false});
            var Q1133;
            Q1133=makeQuery(id+"F3.opExtrude","CAP_EDGE",EDGE,{"disambiguationData":[OSD([sQuery(id+"F2.wireOp",EDGE,"E2.11.9.2")])],"isStart":false});
            var Q1134;
            Q1134=makeQuery(id+"F3.opExtrude","CAP_EDGE",EDGE,{"disambiguationData":[OSD([sQuery(id+"F2.wireOp",EDGE,"E2.18.9.2")])],"isStart":false});
            var Q1135;
            Q1135=makeQuery(id+"F3.opExtrude","CAP_EDGE",EDGE,{"disambiguationData":[OSD([sQuery(id+"F2.wireOp",EDGE,"E2.5.9.2")])],"isStart":false});
            var Q1136;
            Q1136=makeQuery(id+"F3.opExtrude","CAP_EDGE",EDGE,{"disambiguationData":[OSD([sQuery(id+"F2.wireOp",EDGE,"E3.6.21.9")])],"isStart":false});
            var Q1137;
            Q1137=makeQuery(id+"F3.opExtrude","CAP_EDGE",EDGE,{"disambiguationData":[OSD([sQuery(id+"F2.wireOp",EDGE,"E2.8.9.2")])],"isStart":false});
            var Q1138;
            Q1138=makeQuery(id+"F3.opExtrude","CAP_EDGE",EDGE,{"disambiguationData":[OSD([sQuery(id+"F2.wireOp",EDGE,"E2.15.9.2")])],"isStart":false});
            var Q1139;
            Q1139=makeQuery(id+"F3.opExtrude","CAP_EDGE",EDGE,{"disambiguationData":[OSD([sQuery(id+"F2.wireOp",EDGE,"E2.2.9.2")])],"isStart":false});
            var Q1140;
            Q1140=makeQuery(id+"F3.opExtrude","CAP_EDGE",EDGE,{"disambiguationData":[OSD([sQuery(id+"F2.wireOp",EDGE,"E3.6.28.9")])],"isStart":false});
            var Q1141;
            Q1141=makeQuery(id+"F3.opExtrude","CAP_EDGE",EDGE,{"disambiguationData":[OSD([sQuery(id+"F2.wireOp",EDGE,"E2.0.9.3")])],"isStart":false});
            var Q1142;
            Q1142=makeQuery(id+"F3.opExtrude","CAP_EDGE",EDGE,{"disambiguationData":[OSD([sQuery(id+"F2.wireOp",EDGE,"E2.16.9.1")])],"isStart":false});
            var Q1143;
            Q1143=makeQuery(id+"F3.opExtrude","CAP_EDGE",EDGE,{"disambiguationData":[OSD([sQuery(id+"F2.wireOp",EDGE,"E2.3.9.1")])],"isStart":false});
            var Q1144;
            Q1144=makeQuery(id+"F3.opExtrude","CAP_EDGE",EDGE,{"disambiguationData":[OSD([sQuery(id+"F2.wireOp",EDGE,"E3.3.29.9")])],"isStart":false});
            var Q1145;
            Q1145=makeQuery(id+"F3.opExtrude","CAP_EDGE",EDGE,{"disambiguationData":[OSD([sQuery(id+"F2.wireOp",EDGE,"E2.4.9.1")])],"isStart":false});
            var Q1146;
            Q1146=makeQuery(id+"F3.opExtrude","CAP_EDGE",EDGE,{"disambiguationData":[OSD([sQuery(id+"F2.wireOp",EDGE,"E3.3.23.9")])],"isStart":false});
            var Q1147;
            Q1147=makeQuery(id+"F3.opExtrude","CAP_EDGE",EDGE,{"disambiguationData":[OSD([sQuery(id+"F2.wireOp",EDGE,"E2.17.9.1")])],"isStart":false});
            var Q1148;
            Q1148=makeQuery(id+"F3.opExtrude","CAP_EDGE",EDGE,{"disambiguationData":[OSD([sQuery(id+"F2.wireOp",EDGE,"E3.3.24.9")])],"isStart":false});
            var Q1149;
            Q1149=makeQuery(id+"F3.opExtrude","CAP_EDGE",EDGE,{"disambiguationData":[OSD([sQuery(id+"F2.wireOp",EDGE,"E2.11.9.1")])],"isStart":false});
            var Q1150;
            Q1150=makeQuery(id+"F3.opExtrude","CAP_EDGE",EDGE,{"disambiguationData":[OSD([sQuery(id+"F2.wireOp",EDGE,"E2.18.9.1")])],"isStart":false});
            var Q1151;
            Q1151=makeQuery(id+"F3.opExtrude","CAP_EDGE",EDGE,{"disambiguationData":[OSD([sQuery(id+"F2.wireOp",EDGE,"E2.5.9.1")])],"isStart":false});
            var Q1152;
            Q1152=makeQuery(id+"F3.opExtrude","CAP_EDGE",EDGE,{"disambiguationData":[OSD([sQuery(id+"F2.wireOp",EDGE,"E2.12.9.1")])],"isStart":false});
            var Q1153;
            Q1153=makeQuery(id+"F3.opExtrude","CAP_EDGE",EDGE,{"disambiguationData":[OSD([sQuery(id+"F2.wireOp",EDGE,"E2.10.9.1")])],"isStart":false});
            var Q1154;
            Q1154=makeQuery(id+"F3.opExtrude","CAP_EDGE",EDGE,{"disambiguationData":[OSD([sQuery(id+"F2.wireOp",EDGE,"E3.3.22.9")])],"isStart":false});
            var Q1155;
            Q1155=makeQuery(id+"F3.opExtrude","CAP_EDGE",EDGE,{"disambiguationData":[OSD([sQuery(id+"F2.wireOp",EDGE,"E2.9.9.1")])],"isStart":false});
            var Q1156;
            Q1156=makeQuery(id+"F3.opExtrude","CAP_EDGE",EDGE,{"disambiguationData":[OSD([sQuery(id+"F2.wireOp",EDGE,"E2.15.9.1")])],"isStart":false});
            var Q1157;
            Q1157=makeQuery(id+"F3.opExtrude","CAP_EDGE",EDGE,{"disambiguationData":[OSD([sQuery(id+"F2.wireOp",EDGE,"E2.2.9.1")])],"isStart":false});
            var Q1158;
            Q1158=makeQuery(id+"F3.opExtrude","CAP_EDGE",EDGE,{"disambiguationData":[OSD([sQuery(id+"F2.wireOp",EDGE,"E3.3.28.9")])],"isStart":false});
            var Q1159;
            Q1159=makeQuery(id+"F3.opExtrude","CAP_EDGE",EDGE,{"disambiguationData":[OSD([sQuery(id+"F2.wireOp",EDGE,"E2.6.9.1")])],"isStart":false});
            var Q1160;
            Q1160=makeQuery(id+"F3.opExtrude","CAP_EDGE",EDGE,{"disambiguationData":[OSD([sQuery(id+"F2.wireOp",EDGE,"E3.3.25.9")])],"isStart":false});
            var Q1161;
            Q1161=makeQuery(id+"F3.opExtrude","CAP_EDGE",EDGE,{"disambiguationData":[OSD([sQuery(id+"F2.wireOp",EDGE,"E2.19.9.1")])],"isStart":false});
            var Q1162;
            Q1162=makeQuery(id+"F3.opExtrude","CAP_EDGE",EDGE,{"disambiguationData":[OSD([sQuery(id+"F2.wireOp",EDGE,"E2.13.9.1")])],"isStart":false});
            var Q1163;
            Q1163=makeQuery(id+"F3.opExtrude","CAP_EDGE",EDGE,{"disambiguationData":[OSD([sQuery(id+"F2.wireOp",EDGE,"E2.7.9.1")])],"isStart":false});
            var Q1164;
            Q1164=makeQuery(id+"F3.opExtrude","CAP_EDGE",EDGE,{"disambiguationData":[OSD([sQuery(id+"F2.wireOp",EDGE,"E3.3.26.9")])],"isStart":false});
            var Q1165;
            Q1165=makeQuery(id+"F3.opExtrude","CAP_EDGE",EDGE,{"disambiguationData":[OSD([sQuery(id+"F2.wireOp",EDGE,"E2.1.9.1")])],"isStart":false});
            var Q1166;
            Q1166=makeQuery(id+"F3.opExtrude","CAP_EDGE",EDGE,{"disambiguationData":[OSD([sQuery(id+"F2.wireOp",EDGE,"E3.3.20.9")])],"isStart":false});
            var Q1167;
            Q1167=makeQuery(id+"F3.opExtrude","CAP_EDGE",EDGE,{"disambiguationData":[OSD([sQuery(id+"F2.wireOp",EDGE,"E3.3.27.9")])],"isStart":false});
            var Q1168;
            Q1168=makeQuery(id+"F3.opExtrude","CAP_EDGE",EDGE,{"disambiguationData":[OSD([sQuery(id+"F2.wireOp",EDGE,"E2.14.9.1")])],"isStart":false});
            var Q1169;
            Q1169=makeQuery(id+"F3.opExtrude","CAP_EDGE",EDGE,{"disambiguationData":[OSD([sQuery(id+"F2.wireOp",EDGE,"E3.3.21.9")])],"isStart":false});
            var Q1170;
            Q1170=makeQuery(id+"F3.opExtrude","CAP_EDGE",EDGE,{"disambiguationData":[OSD([sQuery(id+"F2.wireOp",EDGE,"E2.8.9.1")])],"isStart":false});
            var Q1171;
            Q1171=makeQuery(id+"F3.opExtrude","CAP_EDGE",EDGE,{"disambiguationData":[OSD([sQuery(id+"F2.wireOp",EDGE,"E2.10.9.3")])],"isStart":false});
            var Q1172;
            Q1172=makeQuery(id+"F3.opExtrude","CAP_EDGE",EDGE,{"disambiguationData":[OSD([sQuery(id+"F2.wireOp",EDGE,"E3.9.22.9")])],"isStart":false});
            var Q1173;
            Q1173=makeQuery(id+"F3.opExtrude","CAP_EDGE",EDGE,{"disambiguationData":[OSD([sQuery(id+"F2.wireOp",EDGE,"E2.9.9.3")])],"isStart":false});
            var Q1174;
            Q1174=makeQuery(id+"F3.opExtrude","CAP_EDGE",EDGE,{"disambiguationData":[OSD([sQuery(id+"F2.wireOp",EDGE,"E2.16.9.3")])],"isStart":false});
            var Q1175;
            Q1175=makeQuery(id+"F3.opExtrude","CAP_EDGE",EDGE,{"disambiguationData":[OSD([sQuery(id+"F2.wireOp",EDGE,"E2.3.9.3")])],"isStart":false});
            var Q1176;
            Q1176=makeQuery(id+"F3.opExtrude","CAP_EDGE",EDGE,{"disambiguationData":[OSD([sQuery(id+"F2.wireOp",EDGE,"E3.9.29.9")])],"isStart":false});
            var Q1177;
            Q1177=makeQuery(id+"F3.opExtrude","CAP_EDGE",EDGE,{"disambiguationData":[OSD([sQuery(id+"F2.wireOp",EDGE,"E2.13.9.3")])],"isStart":false});
            var Q1178;
            Q1178=makeQuery(id+"F3.opExtrude","CAP_EDGE",EDGE,{"disambiguationData":[OSD([sQuery(id+"F2.wireOp",EDGE,"E2.7.9.3")])],"isStart":false});
            var Q1179;
            Q1179=makeQuery(id+"F3.opExtrude","CAP_EDGE",EDGE,{"disambiguationData":[OSD([sQuery(id+"F2.wireOp",EDGE,"E3.9.26.9")])],"isStart":false});
            var Q1180;
            Q1180=makeQuery(id+"F3.opExtrude","CAP_EDGE",EDGE,{"disambiguationData":[OSD([sQuery(id+"F2.wireOp",EDGE,"E2.1.9.3")])],"isStart":false});
            var Q1181;
            Q1181=makeQuery(id+"F3.opExtrude","CAP_EDGE",EDGE,{"disambiguationData":[OSD([sQuery(id+"F2.wireOp",EDGE,"E3.9.20.9")])],"isStart":false});
            var Q1182;
            Q1182=makeQuery(id+"F3.opExtrude","CAP_EDGE",EDGE,{"disambiguationData":[OSD([sQuery(id+"F2.wireOp",EDGE,"E3.9.27.9")])],"isStart":false});
            var Q1183;
            Q1183=makeQuery(id+"F3.opExtrude","CAP_EDGE",EDGE,{"disambiguationData":[OSD([sQuery(id+"F2.wireOp",EDGE,"E2.14.9.3")])],"isStart":false});
            var Q1184;
            Q1184=makeQuery(id+"F3.opExtrude","CAP_EDGE",EDGE,{"disambiguationData":[OSD([sQuery(id+"F2.wireOp",EDGE,"E3.9.21.9")])],"isStart":false});
            var Q1185;
            Q1185=makeQuery(id+"F3.opExtrude","CAP_EDGE",EDGE,{"disambiguationData":[OSD([sQuery(id+"F2.wireOp",EDGE,"E2.8.9.3")])],"isStart":false});
            var Q1186;
            Q1186=makeQuery(id+"F3.opExtrude","CAP_EDGE",EDGE,{"disambiguationData":[OSD([sQuery(id+"F2.wireOp",EDGE,"E2.15.9.3")])],"isStart":false});
            var Q1187;
            Q1187=makeQuery(id+"F3.opExtrude","CAP_EDGE",EDGE,{"disambiguationData":[OSD([sQuery(id+"F2.wireOp",EDGE,"E2.2.9.3")])],"isStart":false});
            var Q1188;
            Q1188=makeQuery(id+"F3.opExtrude","CAP_EDGE",EDGE,{"disambiguationData":[OSD([sQuery(id+"F2.wireOp",EDGE,"E3.9.28.9")])],"isStart":false});
            var Q1189;
            Q1189=makeQuery(id+"F3.opExtrude","CAP_EDGE",EDGE,{"disambiguationData":[OSD([sQuery(id+"F2.wireOp",EDGE,"E3.9.23.9")])],"isStart":false});
            var Q1190;
            Q1190=makeQuery(id+"F3.opExtrude","CAP_EDGE",EDGE,{"disambiguationData":[OSD([sQuery(id+"F2.wireOp",EDGE,"E2.4.9.3")])],"isStart":false});
            var Q1191;
            Q1191=makeQuery(id+"F3.opExtrude","CAP_EDGE",EDGE,{"disambiguationData":[OSD([sQuery(id+"F2.wireOp",EDGE,"E2.17.9.3")])],"isStart":false});
            var Q1192;
            Q1192=makeQuery(id+"F3.opExtrude","CAP_EDGE",EDGE,{"disambiguationData":[OSD([sQuery(id+"F2.wireOp",EDGE,"E3.9.24.9")])],"isStart":false});
            var Q1193;
            Q1193=makeQuery(id+"F3.opExtrude","CAP_EDGE",EDGE,{"disambiguationData":[OSD([sQuery(id+"F2.wireOp",EDGE,"E2.11.9.3")])],"isStart":false});
            var Q1194;
            Q1194=makeQuery(id+"F3.opExtrude","CAP_EDGE",EDGE,{"disambiguationData":[OSD([sQuery(id+"F2.wireOp",EDGE,"E2.18.9.3")])],"isStart":false});
            var Q1195;
            Q1195=makeQuery(id+"F3.opExtrude","CAP_EDGE",EDGE,{"disambiguationData":[OSD([sQuery(id+"F2.wireOp",EDGE,"E2.5.9.3")])],"isStart":false});
            var Q1196;
            Q1196=makeQuery(id+"F3.opExtrude","CAP_EDGE",EDGE,{"disambiguationData":[OSD([sQuery(id+"F2.wireOp",EDGE,"E2.12.9.3")])],"isStart":false});
            var Q1197;
            Q1197=makeQuery(id+"F3.opExtrude","CAP_EDGE",EDGE,{"disambiguationData":[OSD([sQuery(id+"F2.wireOp",EDGE,"E2.6.9.3")])],"isStart":false});
            var Q1198;
            Q1198=makeQuery(id+"F3.opExtrude","CAP_EDGE",EDGE,{"disambiguationData":[OSD([sQuery(id+"F2.wireOp",EDGE,"E3.9.25.9")])],"isStart":false});
            var Q1199;
            Q1199=makeQuery(id+"F3.opExtrude","CAP_EDGE",EDGE,{"disambiguationData":[OSD([sQuery(id+"F2.wireOp",EDGE,"E2.19.9.3")])],"isStart":false});
            var Q1200;
            Q1200=makeQuery(id+"F3.opExtrude","CAP_EDGE",EDGE,{"disambiguationData":[OSD([sQuery(id+"F2.wireOp",EDGE,"E2.0.10.3")])],"isStart":false});
            var Q1201;
            Q1201=makeQuery(id+"F3.opExtrude","CAP_EDGE",EDGE,{"disambiguationData":[OSD([sQuery(id+"F2.wireOp",EDGE,"E2.0.10.0")])],"isStart":false});
            var Q1202;
            Q1202=makeQuery(id+"F3.opExtrude","CAP_EDGE",EDGE,{"disambiguationData":[OSD([sQuery(id+"F2.wireOp",EDGE,"E2.0.10.2")])],"isStart":false});
            var Q1203;
            Q1203=makeQuery(id+"F3.opExtrude","CAP_EDGE",EDGE,{"disambiguationData":[OSD([sQuery(id+"F2.wireOp",EDGE,"E2.10.10.3")])],"isStart":false});
            var Q1204;
            Q1204=makeQuery(id+"F3.opExtrude","CAP_EDGE",EDGE,{"disambiguationData":[OSD([sQuery(id+"F2.wireOp",EDGE,"E3.9.22.10")])],"isStart":false});
            var Q1205;
            Q1205=makeQuery(id+"F3.opExtrude","CAP_EDGE",EDGE,{"disambiguationData":[OSD([sQuery(id+"F2.wireOp",EDGE,"E2.9.10.3")])],"isStart":false});
            var Q1206;
            Q1206=makeQuery(id+"F3.opExtrude","CAP_EDGE",EDGE,{"disambiguationData":[OSD([sQuery(id+"F2.wireOp",EDGE,"E2.6.10.3")])],"isStart":false});
            var Q1207;
            Q1207=makeQuery(id+"F3.opExtrude","CAP_EDGE",EDGE,{"disambiguationData":[OSD([sQuery(id+"F2.wireOp",EDGE,"E3.9.25.10")])],"isStart":false});
            var Q1208;
            Q1208=makeQuery(id+"F3.opExtrude","CAP_EDGE",EDGE,{"disambiguationData":[OSD([sQuery(id+"F2.wireOp",EDGE,"E2.19.10.3")])],"isStart":false});
            var Q1209;
            Q1209=makeQuery(id+"F3.opExtrude","CAP_EDGE",EDGE,{"disambiguationData":[OSD([sQuery(id+"F2.wireOp",EDGE,"E2.13.10.3")])],"isStart":false});
            var Q1210;
            Q1210=makeQuery(id+"F3.opExtrude","CAP_EDGE",EDGE,{"disambiguationData":[OSD([sQuery(id+"F2.wireOp",EDGE,"E2.7.10.3")])],"isStart":false});
            var Q1211;
            Q1211=makeQuery(id+"F3.opExtrude","CAP_EDGE",EDGE,{"disambiguationData":[OSD([sQuery(id+"F2.wireOp",EDGE,"E3.9.26.10")])],"isStart":false});
            var Q1212;
            Q1212=makeQuery(id+"F3.opExtrude","CAP_EDGE",EDGE,{"disambiguationData":[OSD([sQuery(id+"F2.wireOp",EDGE,"E2.1.10.3")])],"isStart":false});
            var Q1213;
            Q1213=makeQuery(id+"F3.opExtrude","CAP_EDGE",EDGE,{"disambiguationData":[OSD([sQuery(id+"F2.wireOp",EDGE,"E3.9.20.10")])],"isStart":false});
            var Q1214;
            Q1214=makeQuery(id+"F3.opExtrude","CAP_EDGE",EDGE,{"disambiguationData":[OSD([sQuery(id+"F2.wireOp",EDGE,"E3.9.27.10")])],"isStart":false});
            var Q1215;
            Q1215=makeQuery(id+"F3.opExtrude","CAP_EDGE",EDGE,{"disambiguationData":[OSD([sQuery(id+"F2.wireOp",EDGE,"E2.14.10.3")])],"isStart":false});
            var Q1216;
            Q1216=makeQuery(id+"F3.opExtrude","CAP_EDGE",EDGE,{"disambiguationData":[OSD([sQuery(id+"F2.wireOp",EDGE,"E3.9.21.10")])],"isStart":false});
            var Q1217;
            Q1217=makeQuery(id+"F3.opExtrude","CAP_EDGE",EDGE,{"disambiguationData":[OSD([sQuery(id+"F2.wireOp",EDGE,"E2.8.10.3")])],"isStart":false});
            var Q1218;
            Q1218=makeQuery(id+"F3.opExtrude","CAP_EDGE",EDGE,{"disambiguationData":[OSD([sQuery(id+"F2.wireOp",EDGE,"E2.16.10.3")])],"isStart":false});
            var Q1219;
            Q1219=makeQuery(id+"F3.opExtrude","CAP_EDGE",EDGE,{"disambiguationData":[OSD([sQuery(id+"F2.wireOp",EDGE,"E2.3.10.3")])],"isStart":false});
            var Q1220;
            Q1220=makeQuery(id+"F3.opExtrude","CAP_EDGE",EDGE,{"disambiguationData":[OSD([sQuery(id+"F2.wireOp",EDGE,"E3.9.29.10")])],"isStart":false});
            var Q1221;
            Q1221=makeQuery(id+"F3.opExtrude","CAP_EDGE",EDGE,{"disambiguationData":[OSD([sQuery(id+"F2.wireOp",EDGE,"E3.9.23.10")])],"isStart":false});
            var Q1222;
            Q1222=makeQuery(id+"F3.opExtrude","CAP_EDGE",EDGE,{"disambiguationData":[OSD([sQuery(id+"F2.wireOp",EDGE,"E2.17.10.3")])],"isStart":false});
            var Q1223;
            Q1223=makeQuery(id+"F3.opExtrude","CAP_EDGE",EDGE,{"disambiguationData":[OSD([sQuery(id+"F2.wireOp",EDGE,"E2.4.10.3")])],"isStart":false});
            var Q1224;
            Q1224=makeQuery(id+"F3.opExtrude","CAP_EDGE",EDGE,{"disambiguationData":[OSD([sQuery(id+"F2.wireOp",EDGE,"E2.11.10.3")])],"isStart":false});
            var Q1225;
            Q1225=makeQuery(id+"F3.opExtrude","CAP_EDGE",EDGE,{"disambiguationData":[OSD([sQuery(id+"F2.wireOp",EDGE,"E2.18.10.3")])],"isStart":false});
            var Q1226;
            Q1226=makeQuery(id+"F3.opExtrude","CAP_EDGE",EDGE,{"disambiguationData":[OSD([sQuery(id+"F2.wireOp",EDGE,"E3.9.24.10")])],"isStart":false});
            var Q1227;
            Q1227=makeQuery(id+"F3.opExtrude","CAP_EDGE",EDGE,{"disambiguationData":[OSD([sQuery(id+"F2.wireOp",EDGE,"E2.5.10.3")])],"isStart":false});
            var Q1228;
            Q1228=makeQuery(id+"F3.opExtrude","CAP_EDGE",EDGE,{"disambiguationData":[OSD([sQuery(id+"F2.wireOp",EDGE,"E2.12.10.3")])],"isStart":false});
            var Q1229;
            Q1229=makeQuery(id+"F3.opExtrude","CAP_EDGE",EDGE,{"disambiguationData":[OSD([sQuery(id+"F2.wireOp",EDGE,"E2.10.10.0")])],"isStart":false});
            var Q1230;
            Q1230=makeQuery(id+"F3.opExtrude","CAP_EDGE",EDGE,{"disambiguationData":[OSD([sQuery(id+"F2.wireOp",EDGE,"E3.0.22.10")])],"isStart":false});
            var Q1231;
            Q1231=makeQuery(id+"F3.opExtrude","CAP_EDGE",EDGE,{"disambiguationData":[OSD([sQuery(id+"F2.wireOp",EDGE,"E2.9.10.0")])],"isStart":false});
            var Q1232;
            Q1232=makeQuery(id+"F3.opExtrude","CAP_EDGE",EDGE,{"disambiguationData":[OSD([sQuery(id+"F2.wireOp",EDGE,"E2.16.10.0")])],"isStart":false});
            var Q1233;
            Q1233=makeQuery(id+"F3.opExtrude","CAP_EDGE",EDGE,{"disambiguationData":[OSD([sQuery(id+"F2.wireOp",EDGE,"E2.3.10.0")])],"isStart":false});
            var Q1234;
            Q1234=makeQuery(id+"F3.opExtrude","CAP_EDGE",EDGE,{"disambiguationData":[OSD([sQuery(id+"F2.wireOp",EDGE,"E2.15.10.3")])],"isStart":false});
            var Q1235;
            Q1235=makeQuery(id+"F3.opExtrude","CAP_EDGE",EDGE,{"disambiguationData":[OSD([sQuery(id+"F2.wireOp",EDGE,"E2.2.10.3")])],"isStart":false});
            var Q1236;
            Q1236=makeQuery(id+"F3.opExtrude","CAP_EDGE",EDGE,{"disambiguationData":[OSD([sQuery(id+"F2.wireOp",EDGE,"E3.9.28.10")])],"isStart":false});
            var Q1237;
            Q1237=makeQuery(id+"F3.opExtrude","CAP_EDGE",EDGE,{"disambiguationData":[OSD([sQuery(id+"F2.wireOp",EDGE,"E2.19.10.0")])],"isStart":false});
            var Q1238;
            Q1238=makeQuery(id+"F3.opExtrude","CAP_EDGE",EDGE,{"disambiguationData":[OSD([sQuery(id+"F2.wireOp",EDGE,"E2.13.10.0")])],"isStart":false});
            var Q1239;
            Q1239=makeQuery(id+"F3.opExtrude","CAP_EDGE",EDGE,{"disambiguationData":[OSD([sQuery(id+"F2.wireOp",EDGE,"E2.7.10.0")])],"isStart":false});
            var Q1240;
            Q1240=makeQuery(id+"F3.opExtrude","CAP_EDGE",EDGE,{"disambiguationData":[OSD([sQuery(id+"F2.wireOp",EDGE,"E3.0.26.10")])],"isStart":false});
            var Q1241;
            Q1241=makeQuery(id+"F3.opExtrude","CAP_EDGE",EDGE,{"disambiguationData":[OSD([sQuery(id+"F2.wireOp",EDGE,"E2.14.10.0")])],"isStart":false});
            var Q1242;
            Q1242=makeQuery(id+"F3.opExtrude","CAP_EDGE",EDGE,{"disambiguationData":[OSD([sQuery(id+"F2.wireOp",EDGE,"E3.0.20.10")])],"isStart":false});
            var Q1243;
            Q1243=makeQuery(id+"F3.opExtrude","CAP_EDGE",EDGE,{"disambiguationData":[OSD([sQuery(id+"F2.wireOp",EDGE,"E2.1.10.0")])],"isStart":false});
            var Q1244;
            Q1244=makeQuery(id+"F3.opExtrude","CAP_EDGE",EDGE,{"disambiguationData":[OSD([sQuery(id+"F2.wireOp",EDGE,"E2.8.10.0")])],"isStart":false});
            var Q1245;
            Q1245=makeQuery(id+"F3.opExtrude","CAP_EDGE",EDGE,{"disambiguationData":[OSD([sQuery(id+"F2.wireOp",EDGE,"E3.0.27.10")])],"isStart":false});
            var Q1246;
            Q1246=makeQuery(id+"F3.opExtrude","CAP_EDGE",EDGE,{"disambiguationData":[OSD([sQuery(id+"F2.wireOp",EDGE,"E2.2.10.0")])],"isStart":false});
            var Q1247;
            Q1247=makeQuery(id+"F3.opExtrude","CAP_EDGE",EDGE,{"disambiguationData":[OSD([sQuery(id+"F2.wireOp",EDGE,"E3.0.21.10")])],"isStart":false});
            var Q1248;
            Q1248=makeQuery(id+"F3.opExtrude","CAP_EDGE",EDGE,{"disambiguationData":[OSD([sQuery(id+"F2.wireOp",EDGE,"E3.0.28.10")])],"isStart":false});
            var Q1249;
            Q1249=makeQuery(id+"F3.opExtrude","CAP_EDGE",EDGE,{"disambiguationData":[OSD([sQuery(id+"F2.wireOp",EDGE,"E2.15.10.0")])],"isStart":false});
            var Q1250;
            Q1250=makeQuery(id+"F3.opExtrude","CAP_EDGE",EDGE,{"disambiguationData":[OSD([sQuery(id+"F2.wireOp",EDGE,"E3.0.29.10")])],"isStart":false});
            var Q1251;
            Q1251=makeQuery(id+"F3.opExtrude","CAP_EDGE",EDGE,{"disambiguationData":[OSD([sQuery(id+"F2.wireOp",EDGE,"E2.4.10.0")])],"isStart":false});
            var Q1252;
            Q1252=makeQuery(id+"F3.opExtrude","CAP_EDGE",EDGE,{"disambiguationData":[OSD([sQuery(id+"F2.wireOp",EDGE,"E3.0.23.10")])],"isStart":false});
            var Q1253;
            Q1253=makeQuery(id+"F3.opExtrude","CAP_EDGE",EDGE,{"disambiguationData":[OSD([sQuery(id+"F2.wireOp",EDGE,"E2.17.10.0")])],"isStart":false});
            var Q1254;
            Q1254=makeQuery(id+"F3.opExtrude","CAP_EDGE",EDGE,{"disambiguationData":[OSD([sQuery(id+"F2.wireOp",EDGE,"E3.0.24.10")])],"isStart":false});
            var Q1255;
            Q1255=makeQuery(id+"F3.opExtrude","CAP_EDGE",EDGE,{"disambiguationData":[OSD([sQuery(id+"F2.wireOp",EDGE,"E2.11.10.0")])],"isStart":false});
            var Q1256;
            Q1256=makeQuery(id+"F3.opExtrude","CAP_EDGE",EDGE,{"disambiguationData":[OSD([sQuery(id+"F2.wireOp",EDGE,"E2.18.10.0")])],"isStart":false});
            var Q1257;
            Q1257=makeQuery(id+"F3.opExtrude","CAP_EDGE",EDGE,{"disambiguationData":[OSD([sQuery(id+"F2.wireOp",EDGE,"E2.5.10.0")])],"isStart":false});
            var Q1258;
            Q1258=makeQuery(id+"F3.opExtrude","CAP_EDGE",EDGE,{"disambiguationData":[OSD([sQuery(id+"F2.wireOp",EDGE,"E2.12.10.0")])],"isStart":false});
            var Q1259;
            Q1259=makeQuery(id+"F3.opExtrude","CAP_EDGE",EDGE,{"disambiguationData":[OSD([sQuery(id+"F2.wireOp",EDGE,"E2.6.10.0")])],"isStart":false});
            var Q1260;
            Q1260=makeQuery(id+"F3.opExtrude","CAP_EDGE",EDGE,{"disambiguationData":[OSD([sQuery(id+"F2.wireOp",EDGE,"E3.0.25.10")])],"isStart":false});
            var Q1261;
            Q1261=makeQuery(id+"F3.opExtrude","CAP_EDGE",EDGE,{"disambiguationData":[OSD([sQuery(id+"F2.wireOp",EDGE,"E2.0.10.1")])],"isStart":false});
            var Q1262;
            Q1262=makeQuery(id+"F3.opExtrude","CAP_EDGE",EDGE,{"disambiguationData":[OSD([sQuery(id+"F2.wireOp",EDGE,"E3.6.29.10")])],"isStart":false});
            var Q1263;
            Q1263=makeQuery(id+"F3.opExtrude","CAP_EDGE",EDGE,{"disambiguationData":[OSD([sQuery(id+"F2.wireOp",EDGE,"E2.4.10.2")])],"isStart":false});
            var Q1264;
            Q1264=makeQuery(id+"F3.opExtrude","CAP_EDGE",EDGE,{"disambiguationData":[OSD([sQuery(id+"F2.wireOp",EDGE,"E3.6.23.10")])],"isStart":false});
            var Q1265;
            Q1265=makeQuery(id+"F3.opExtrude","CAP_EDGE",EDGE,{"disambiguationData":[OSD([sQuery(id+"F2.wireOp",EDGE,"E2.17.10.2")])],"isStart":false});
            var Q1266;
            Q1266=makeQuery(id+"F3.opExtrude","CAP_EDGE",EDGE,{"disambiguationData":[OSD([sQuery(id+"F2.wireOp",EDGE,"E3.6.24.10")])],"isStart":false});
            var Q1267;
            Q1267=makeQuery(id+"F3.opExtrude","CAP_EDGE",EDGE,{"disambiguationData":[OSD([sQuery(id+"F2.wireOp",EDGE,"E2.11.10.2")])],"isStart":false});
            var Q1268;
            Q1268=makeQuery(id+"F3.opExtrude","CAP_EDGE",EDGE,{"disambiguationData":[OSD([sQuery(id+"F2.wireOp",EDGE,"E2.18.10.2")])],"isStart":false});
            var Q1269;
            Q1269=makeQuery(id+"F3.opExtrude","CAP_EDGE",EDGE,{"disambiguationData":[OSD([sQuery(id+"F2.wireOp",EDGE,"E2.5.10.2")])],"isStart":false});
            var Q1270;
            Q1270=makeQuery(id+"F3.opExtrude","CAP_EDGE",EDGE,{"disambiguationData":[OSD([sQuery(id+"F2.wireOp",EDGE,"E2.12.10.2")])],"isStart":false});
            var Q1271;
            Q1271=makeQuery(id+"F3.opExtrude","CAP_EDGE",EDGE,{"disambiguationData":[OSD([sQuery(id+"F2.wireOp",EDGE,"E2.6.10.2")])],"isStart":false});
            var Q1272;
            Q1272=makeQuery(id+"F3.opExtrude","CAP_EDGE",EDGE,{"disambiguationData":[OSD([sQuery(id+"F2.wireOp",EDGE,"E3.6.25.10")])],"isStart":false});
            var Q1273;
            Q1273=makeQuery(id+"F3.opExtrude","CAP_EDGE",EDGE,{"disambiguationData":[OSD([sQuery(id+"F2.wireOp",EDGE,"E2.10.10.2")])],"isStart":false});
            var Q1274;
            Q1274=makeQuery(id+"F3.opExtrude","CAP_EDGE",EDGE,{"disambiguationData":[OSD([sQuery(id+"F2.wireOp",EDGE,"E3.6.22.10")])],"isStart":false});
            var Q1275;
            Q1275=makeQuery(id+"F3.opExtrude","CAP_EDGE",EDGE,{"disambiguationData":[OSD([sQuery(id+"F2.wireOp",EDGE,"E2.9.10.2")])],"isStart":false});
            var Q1276;
            Q1276=makeQuery(id+"F3.opExtrude","CAP_EDGE",EDGE,{"disambiguationData":[OSD([sQuery(id+"F2.wireOp",EDGE,"E2.16.10.2")])],"isStart":false});
            var Q1277;
            Q1277=makeQuery(id+"F3.opExtrude","CAP_EDGE",EDGE,{"disambiguationData":[OSD([sQuery(id+"F2.wireOp",EDGE,"E2.3.10.2")])],"isStart":false});
            var Q1278;
            Q1278=makeQuery(id+"F3.opExtrude","CAP_EDGE",EDGE,{"disambiguationData":[OSD([sQuery(id+"F2.wireOp",EDGE,"E3.6.28.10")])],"isStart":false});
            var Q1279;
            Q1279=makeQuery(id+"F3.opExtrude","CAP_EDGE",EDGE,{"disambiguationData":[OSD([sQuery(id+"F2.wireOp",EDGE,"E2.19.10.2")])],"isStart":false});
            var Q1280;
            Q1280=makeQuery(id+"F3.opExtrude","CAP_EDGE",EDGE,{"disambiguationData":[OSD([sQuery(id+"F2.wireOp",EDGE,"E2.13.10.2")])],"isStart":false});
            var Q1281;
            Q1281=makeQuery(id+"F3.opExtrude","CAP_EDGE",EDGE,{"disambiguationData":[OSD([sQuery(id+"F2.wireOp",EDGE,"E2.7.10.2")])],"isStart":false});
            var Q1282;
            Q1282=makeQuery(id+"F3.opExtrude","CAP_EDGE",EDGE,{"disambiguationData":[OSD([sQuery(id+"F2.wireOp",EDGE,"E3.6.26.10")])],"isStart":false});
            var Q1283;
            Q1283=makeQuery(id+"F3.opExtrude","CAP_EDGE",EDGE,{"disambiguationData":[OSD([sQuery(id+"F2.wireOp",EDGE,"E2.1.10.2")])],"isStart":false});
            var Q1284;
            Q1284=makeQuery(id+"F3.opExtrude","CAP_EDGE",EDGE,{"disambiguationData":[OSD([sQuery(id+"F2.wireOp",EDGE,"E3.6.20.10")])],"isStart":false});
            var Q1285;
            Q1285=makeQuery(id+"F3.opExtrude","CAP_EDGE",EDGE,{"disambiguationData":[OSD([sQuery(id+"F2.wireOp",EDGE,"E3.6.27.10")])],"isStart":false});
            var Q1286;
            Q1286=makeQuery(id+"F3.opExtrude","CAP_EDGE",EDGE,{"disambiguationData":[OSD([sQuery(id+"F2.wireOp",EDGE,"E2.14.10.2")])],"isStart":false});
            var Q1287;
            Q1287=makeQuery(id+"F3.opExtrude","CAP_EDGE",EDGE,{"disambiguationData":[OSD([sQuery(id+"F2.wireOp",EDGE,"E3.6.21.10")])],"isStart":false});
            var Q1288;
            Q1288=makeQuery(id+"F3.opExtrude","CAP_EDGE",EDGE,{"disambiguationData":[OSD([sQuery(id+"F2.wireOp",EDGE,"E2.8.10.2")])],"isStart":false});
            var Q1289;
            Q1289=makeQuery(id+"F3.opExtrude","CAP_EDGE",EDGE,{"disambiguationData":[OSD([sQuery(id+"F2.wireOp",EDGE,"E2.15.10.2")])],"isStart":false});
            var Q1290;
            Q1290=makeQuery(id+"F3.opExtrude","CAP_EDGE",EDGE,{"disambiguationData":[OSD([sQuery(id+"F2.wireOp",EDGE,"E2.2.10.2")])],"isStart":false});
            var Q1291;
            Q1291=makeQuery(id+"F3.opExtrude","CAP_EDGE",EDGE,{"disambiguationData":[OSD([sQuery(id+"F2.wireOp",EDGE,"E2.10.10.1")])],"isStart":false});
            var Q1292;
            Q1292=makeQuery(id+"F3.opExtrude","CAP_EDGE",EDGE,{"disambiguationData":[OSD([sQuery(id+"F2.wireOp",EDGE,"E3.3.22.10")])],"isStart":false});
            var Q1293;
            Q1293=makeQuery(id+"F3.opExtrude","CAP_EDGE",EDGE,{"disambiguationData":[OSD([sQuery(id+"F2.wireOp",EDGE,"E2.9.10.1")])],"isStart":false});
            var Q1294;
            Q1294=makeQuery(id+"F3.opExtrude","CAP_EDGE",EDGE,{"disambiguationData":[OSD([sQuery(id+"F2.wireOp",EDGE,"E2.16.10.1")])],"isStart":false});
            var Q1295;
            Q1295=makeQuery(id+"F3.opExtrude","CAP_EDGE",EDGE,{"disambiguationData":[OSD([sQuery(id+"F2.wireOp",EDGE,"E2.3.10.1")])],"isStart":false});
            var Q1296;
            Q1296=makeQuery(id+"F3.opExtrude","CAP_EDGE",EDGE,{"disambiguationData":[OSD([sQuery(id+"F2.wireOp",EDGE,"E3.3.29.10")])],"isStart":false});
            var Q1297;
            Q1297=makeQuery(id+"F3.opExtrude","CAP_EDGE",EDGE,{"disambiguationData":[OSD([sQuery(id+"F2.wireOp",EDGE,"E2.4.10.1")])],"isStart":false});
            var Q1298;
            Q1298=makeQuery(id+"F3.opExtrude","CAP_EDGE",EDGE,{"disambiguationData":[OSD([sQuery(id+"F2.wireOp",EDGE,"E3.3.23.10")])],"isStart":false});
            var Q1299;
            Q1299=makeQuery(id+"F3.opExtrude","CAP_EDGE",EDGE,{"disambiguationData":[OSD([sQuery(id+"F2.wireOp",EDGE,"E2.17.10.1")])],"isStart":false});
            var Q1300;
            Q1300=makeQuery(id+"F3.opExtrude","CAP_EDGE",EDGE,{"disambiguationData":[OSD([sQuery(id+"F2.wireOp",EDGE,"E2.1.10.1")])],"isStart":false});
            var Q1301;
            Q1301=makeQuery(id+"F3.opExtrude","CAP_EDGE",EDGE,{"disambiguationData":[OSD([sQuery(id+"F2.wireOp",EDGE,"E3.3.20.10")])],"isStart":false});
            var Q1302;
            Q1302=makeQuery(id+"F3.opExtrude","CAP_EDGE",EDGE,{"disambiguationData":[OSD([sQuery(id+"F2.wireOp",EDGE,"E3.3.27.10")])],"isStart":false});
            var Q1303;
            Q1303=makeQuery(id+"F3.opExtrude","CAP_EDGE",EDGE,{"disambiguationData":[OSD([sQuery(id+"F2.wireOp",EDGE,"E2.14.10.1")])],"isStart":false});
            var Q1304;
            Q1304=makeQuery(id+"F3.opExtrude","CAP_EDGE",EDGE,{"disambiguationData":[OSD([sQuery(id+"F2.wireOp",EDGE,"E3.3.21.10")])],"isStart":false});
            var Q1305;
            Q1305=makeQuery(id+"F3.opExtrude","CAP_EDGE",EDGE,{"disambiguationData":[OSD([sQuery(id+"F2.wireOp",EDGE,"E2.2.10.1")])],"isStart":false});
            var Q1306;
            Q1306=makeQuery(id+"F3.opExtrude","CAP_EDGE",EDGE,{"disambiguationData":[OSD([sQuery(id+"F2.wireOp",EDGE,"E2.8.10.1")])],"isStart":false});
            var Q1307;
            Q1307=makeQuery(id+"F3.opExtrude","CAP_EDGE",EDGE,{"disambiguationData":[OSD([sQuery(id+"F2.wireOp",EDGE,"E3.3.28.10")])],"isStart":false});
            var Q1308;
            Q1308=makeQuery(id+"F3.opExtrude","CAP_EDGE",EDGE,{"disambiguationData":[OSD([sQuery(id+"F2.wireOp",EDGE,"E2.15.10.1")])],"isStart":false});
            var Q1309;
            Q1309=makeQuery(id+"F3.opExtrude","CAP_EDGE",EDGE,{"disambiguationData":[OSD([sQuery(id+"F2.wireOp",EDGE,"E3.3.24.10")])],"isStart":false});
            var Q1310;
            Q1310=makeQuery(id+"F3.opExtrude","CAP_EDGE",EDGE,{"disambiguationData":[OSD([sQuery(id+"F2.wireOp",EDGE,"E2.11.10.1")])],"isStart":false});
            var Q1311;
            Q1311=makeQuery(id+"F3.opExtrude","CAP_EDGE",EDGE,{"disambiguationData":[OSD([sQuery(id+"F2.wireOp",EDGE,"E2.18.10.1")])],"isStart":false});
            var Q1312;
            Q1312=makeQuery(id+"F3.opExtrude","CAP_EDGE",EDGE,{"disambiguationData":[OSD([sQuery(id+"F2.wireOp",EDGE,"E2.5.10.1")])],"isStart":false});
            var Q1313;
            Q1313=makeQuery(id+"F3.opExtrude","CAP_EDGE",EDGE,{"disambiguationData":[OSD([sQuery(id+"F2.wireOp",EDGE,"E2.12.10.1")])],"isStart":false});
            var Q1314;
            Q1314=makeQuery(id+"F3.opExtrude","CAP_EDGE",EDGE,{"disambiguationData":[OSD([sQuery(id+"F2.wireOp",EDGE,"E2.6.10.1")])],"isStart":false});
            var Q1315;
            Q1315=makeQuery(id+"F3.opExtrude","CAP_EDGE",EDGE,{"disambiguationData":[OSD([sQuery(id+"F2.wireOp",EDGE,"E3.3.25.10")])],"isStart":false});
            var Q1316;
            Q1316=makeQuery(id+"F3.opExtrude","CAP_EDGE",EDGE,{"disambiguationData":[OSD([sQuery(id+"F2.wireOp",EDGE,"E2.19.10.1")])],"isStart":false});
            var Q1317;
            Q1317=makeQuery(id+"F3.opExtrude","CAP_EDGE",EDGE,{"disambiguationData":[OSD([sQuery(id+"F2.wireOp",EDGE,"E2.13.10.1")])],"isStart":false});
            var Q1318;
            Q1318=makeQuery(id+"F3.opExtrude","CAP_EDGE",EDGE,{"disambiguationData":[OSD([sQuery(id+"F2.wireOp",EDGE,"E2.7.10.1")])],"isStart":false});
            var Q1319;
            Q1319=makeQuery(id+"F3.opExtrude","CAP_EDGE",EDGE,{"disambiguationData":[OSD([sQuery(id+"F2.wireOp",EDGE,"E3.3.26.10")])],"isStart":false});
            var Q1320;
            Q1320=makeQuery(id+"F3.opExtrude","CAP_EDGE",EDGE,{"disambiguationData":[OSD([sQuery(id+"F2.wireOp",EDGE,"E2.0.11.0")])],"isStart":false});
            var Q1321;
            Q1321=makeQuery(id+"F3.opExtrude","CAP_EDGE",EDGE,{"disambiguationData":[OSD([sQuery(id+"F2.wireOp",EDGE,"E2.0.11.2")])],"isStart":false});
            var Q1322;
            Q1322=makeQuery(id+"F3.opExtrude","CAP_EDGE",EDGE,{"disambiguationData":[OSD([sQuery(id+"F2.wireOp",EDGE,"E2.9.11.0")])],"isStart":false});
            var Q1323;
            Q1323=makeQuery(id+"F3.opExtrude","CAP_EDGE",EDGE,{"disambiguationData":[OSD([sQuery(id+"F2.wireOp",EDGE,"E2.10.11.0")])],"isStart":false});
            var Q1324;
            Q1324=makeQuery(id+"F3.opExtrude","CAP_EDGE",EDGE,{"disambiguationData":[OSD([sQuery(id+"F2.wireOp",EDGE,"E2.16.11.0")])],"isStart":false});
            var Q1325;
            Q1325=makeQuery(id+"F3.opExtrude","CAP_EDGE",EDGE,{"disambiguationData":[OSD([sQuery(id+"F2.wireOp",EDGE,"E3.0.22.11")])],"isStart":false});
            var Q1326;
            Q1326=makeQuery(id+"F3.opExtrude","CAP_EDGE",EDGE,{"disambiguationData":[OSD([sQuery(id+"F2.wireOp",EDGE,"E2.3.11.0")])],"isStart":false});
            var Q1327;
            Q1327=makeQuery(id+"F3.opExtrude","CAP_EDGE",EDGE,{"disambiguationData":[OSD([sQuery(id+"F2.wireOp",EDGE,"E3.0.29.11")])],"isStart":false});
            var Q1328;
            Q1328=makeQuery(id+"F3.opExtrude","CAP_EDGE",EDGE,{"disambiguationData":[OSD([sQuery(id+"F2.wireOp",EDGE,"E3.0.23.11")])],"isStart":false});
            var Q1329;
            Q1329=makeQuery(id+"F3.opExtrude","CAP_EDGE",EDGE,{"disambiguationData":[OSD([sQuery(id+"F2.wireOp",EDGE,"E2.7.11.0")])],"isStart":false});
            var Q1330;
            Q1330=makeQuery(id+"F3.opExtrude","CAP_EDGE",EDGE,{"disambiguationData":[OSD([sQuery(id+"F2.wireOp",EDGE,"E3.0.26.11")])],"isStart":false});
            var Q1331;
            Q1331=makeQuery(id+"F3.opExtrude","CAP_EDGE",EDGE,{"disambiguationData":[OSD([sQuery(id+"F2.wireOp",EDGE,"E2.1.11.0")])],"isStart":false});
            var Q1332;
            Q1332=makeQuery(id+"F3.opExtrude","CAP_EDGE",EDGE,{"disambiguationData":[OSD([sQuery(id+"F2.wireOp",EDGE,"E3.0.20.11")])],"isStart":false});
            var Q1333;
            Q1333=makeQuery(id+"F3.opExtrude","CAP_EDGE",EDGE,{"disambiguationData":[OSD([sQuery(id+"F2.wireOp",EDGE,"E3.0.27.11")])],"isStart":false});
            var Q1334;
            Q1334=makeQuery(id+"F3.opExtrude","CAP_EDGE",EDGE,{"disambiguationData":[OSD([sQuery(id+"F2.wireOp",EDGE,"E2.14.11.0")])],"isStart":false});
            var Q1335;
            Q1335=makeQuery(id+"F3.opExtrude","CAP_EDGE",EDGE,{"disambiguationData":[OSD([sQuery(id+"F2.wireOp",EDGE,"E3.0.21.11")])],"isStart":false});
            var Q1336;
            Q1336=makeQuery(id+"F3.opExtrude","CAP_EDGE",EDGE,{"disambiguationData":[OSD([sQuery(id+"F2.wireOp",EDGE,"E2.8.11.0")])],"isStart":false});
            var Q1337;
            Q1337=makeQuery(id+"F3.opExtrude","CAP_EDGE",EDGE,{"disambiguationData":[OSD([sQuery(id+"F2.wireOp",EDGE,"E2.15.11.0")])],"isStart":false});
            var Q1338;
            Q1338=makeQuery(id+"F3.opExtrude","CAP_EDGE",EDGE,{"disambiguationData":[OSD([sQuery(id+"F2.wireOp",EDGE,"E2.2.11.0")])],"isStart":false});
            var Q1339;
            Q1339=makeQuery(id+"F3.opExtrude","CAP_EDGE",EDGE,{"disambiguationData":[OSD([sQuery(id+"F2.wireOp",EDGE,"E3.0.28.11")])],"isStart":false});
            var Q1340;
            Q1340=makeQuery(id+"F3.opExtrude","CAP_EDGE",EDGE,{"disambiguationData":[OSD([sQuery(id+"F2.wireOp",EDGE,"E2.17.11.0")])],"isStart":false});
            var Q1341;
            Q1341=makeQuery(id+"F3.opExtrude","CAP_EDGE",EDGE,{"disambiguationData":[OSD([sQuery(id+"F2.wireOp",EDGE,"E2.4.11.0")])],"isStart":false});
            var Q1342;
            Q1342=makeQuery(id+"F3.opExtrude","CAP_EDGE",EDGE,{"disambiguationData":[OSD([sQuery(id+"F2.wireOp",EDGE,"E2.11.11.0")])],"isStart":false});
            var Q1343;
            Q1343=makeQuery(id+"F3.opExtrude","CAP_EDGE",EDGE,{"disambiguationData":[OSD([sQuery(id+"F2.wireOp",EDGE,"E2.5.11.0")])],"isStart":false});
            var Q1344;
            Q1344=makeQuery(id+"F3.opExtrude","CAP_EDGE",EDGE,{"disambiguationData":[OSD([sQuery(id+"F2.wireOp",EDGE,"E3.0.24.11")])],"isStart":false});
            var Q1345;
            Q1345=makeQuery(id+"F3.opExtrude","CAP_EDGE",EDGE,{"disambiguationData":[OSD([sQuery(id+"F2.wireOp",EDGE,"E2.12.11.0")])],"isStart":false});
            var Q1346;
            Q1346=makeQuery(id+"F3.opExtrude","CAP_EDGE",EDGE,{"disambiguationData":[OSD([sQuery(id+"F2.wireOp",EDGE,"E2.18.11.0")])],"isStart":false});
            var Q1347;
            Q1347=makeQuery(id+"F3.opExtrude","CAP_EDGE",EDGE,{"disambiguationData":[OSD([sQuery(id+"F2.wireOp",EDGE,"E2.6.11.0")])],"isStart":false});
            var Q1348;
            Q1348=makeQuery(id+"F3.opExtrude","CAP_EDGE",EDGE,{"disambiguationData":[OSD([sQuery(id+"F2.wireOp",EDGE,"E3.0.25.11")])],"isStart":false});
            var Q1349;
            Q1349=makeQuery(id+"F3.opExtrude","CAP_EDGE",EDGE,{"disambiguationData":[OSD([sQuery(id+"F2.wireOp",EDGE,"E2.19.11.0")])],"isStart":false});
            var Q1350;
            Q1350=makeQuery(id+"F3.opExtrude","CAP_EDGE",EDGE,{"disambiguationData":[OSD([sQuery(id+"F2.wireOp",EDGE,"E2.13.11.0")])],"isStart":false});
            var Q1351;
            Q1351=makeQuery(id+"F3.opExtrude","CAP_EDGE",EDGE,{"disambiguationData":[OSD([sQuery(id+"F2.wireOp",EDGE,"E2.18.11.2")])],"isStart":false});
            var Q1352;
            Q1352=makeQuery(id+"F3.opExtrude","CAP_EDGE",EDGE,{"disambiguationData":[OSD([sQuery(id+"F2.wireOp",EDGE,"E3.6.25.11")])],"isStart":false});
            var Q1353;
            Q1353=makeQuery(id+"F3.opExtrude","CAP_EDGE",EDGE,{"disambiguationData":[OSD([sQuery(id+"F2.wireOp",EDGE,"E2.6.11.2")])],"isStart":false});
            var Q1354;
            Q1354=makeQuery(id+"F3.opExtrude","CAP_EDGE",EDGE,{"disambiguationData":[OSD([sQuery(id+"F2.wireOp",EDGE,"E2.12.11.2")])],"isStart":false});
            var Q1355;
            Q1355=makeQuery(id+"F3.opExtrude","CAP_EDGE",EDGE,{"disambiguationData":[OSD([sQuery(id+"F2.wireOp",EDGE,"E2.19.11.2")])],"isStart":false});
            var Q1356;
            Q1356=makeQuery(id+"F3.opExtrude","CAP_EDGE",EDGE,{"disambiguationData":[OSD([sQuery(id+"F2.wireOp",EDGE,"E2.13.11.2")])],"isStart":false});
            var Q1357;
            Q1357=makeQuery(id+"F3.opExtrude","CAP_EDGE",EDGE,{"disambiguationData":[OSD([sQuery(id+"F2.wireOp",EDGE,"E2.7.11.2")])],"isStart":false});
            var Q1358;
            Q1358=makeQuery(id+"F3.opExtrude","CAP_EDGE",EDGE,{"disambiguationData":[OSD([sQuery(id+"F2.wireOp",EDGE,"E3.6.26.11")])],"isStart":false});
            var Q1359;
            Q1359=makeQuery(id+"F3.opExtrude","CAP_EDGE",EDGE,{"disambiguationData":[OSD([sQuery(id+"F2.wireOp",EDGE,"E2.1.11.2")])],"isStart":false});
            var Q1360;
            Q1360=makeQuery(id+"F3.opExtrude","CAP_EDGE",EDGE,{"disambiguationData":[OSD([sQuery(id+"F2.wireOp",EDGE,"E3.6.20.11")])],"isStart":false});
            var Q1361;
            Q1361=makeQuery(id+"F3.opExtrude","CAP_EDGE",EDGE,{"disambiguationData":[OSD([sQuery(id+"F2.wireOp",EDGE,"E3.6.27.11")])],"isStart":false});
            var Q1362;
            Q1362=makeQuery(id+"F3.opExtrude","CAP_EDGE",EDGE,{"disambiguationData":[OSD([sQuery(id+"F2.wireOp",EDGE,"E2.14.11.2")])],"isStart":false});
            var Q1363;
            Q1363=makeQuery(id+"F3.opExtrude","CAP_EDGE",EDGE,{"disambiguationData":[OSD([sQuery(id+"F2.wireOp",EDGE,"E2.9.11.2")])],"isStart":false});
            var Q1364;
            Q1364=makeQuery(id+"F3.opExtrude","CAP_EDGE",EDGE,{"disambiguationData":[OSD([sQuery(id+"F2.wireOp",EDGE,"E2.10.11.2")])],"isStart":false});
            var Q1365;
            Q1365=makeQuery(id+"F3.opExtrude","CAP_EDGE",EDGE,{"disambiguationData":[OSD([sQuery(id+"F2.wireOp",EDGE,"E2.3.11.2")])],"isStart":false});
            var Q1366;
            Q1366=makeQuery(id+"F3.opExtrude","CAP_EDGE",EDGE,{"disambiguationData":[OSD([sQuery(id+"F2.wireOp",EDGE,"E3.6.22.11")])],"isStart":false});
            var Q1367;
            Q1367=makeQuery(id+"F3.opExtrude","CAP_EDGE",EDGE,{"disambiguationData":[OSD([sQuery(id+"F2.wireOp",EDGE,"E3.6.29.11")])],"isStart":false});
            var Q1368;
            Q1368=makeQuery(id+"F3.opExtrude","CAP_EDGE",EDGE,{"disambiguationData":[OSD([sQuery(id+"F2.wireOp",EDGE,"E2.16.11.2")])],"isStart":false});
            var Q1369;
            Q1369=makeQuery(id+"F3.opExtrude","CAP_EDGE",EDGE,{"disambiguationData":[OSD([sQuery(id+"F2.wireOp",EDGE,"E2.0.11.1")])],"isStart":false});
            var Q1370;
            Q1370=makeQuery(id+"F3.opExtrude","CAP_EDGE",EDGE,{"disambiguationData":[OSD([sQuery(id+"F2.wireOp",EDGE,"E3.6.23.11")])],"isStart":false});
            var Q1371;
            Q1371=makeQuery(id+"F3.opExtrude","CAP_EDGE",EDGE,{"disambiguationData":[OSD([sQuery(id+"F2.wireOp",EDGE,"E2.17.11.2")])],"isStart":false});
            var Q1372;
            Q1372=makeQuery(id+"F3.opExtrude","CAP_EDGE",EDGE,{"disambiguationData":[OSD([sQuery(id+"F2.wireOp",EDGE,"E2.4.11.2")])],"isStart":false});
            var Q1373;
            Q1373=makeQuery(id+"F3.opExtrude","CAP_EDGE",EDGE,{"disambiguationData":[OSD([sQuery(id+"F2.wireOp",EDGE,"E2.11.11.2")])],"isStart":false});
            var Q1374;
            Q1374=makeQuery(id+"F3.opExtrude","CAP_EDGE",EDGE,{"disambiguationData":[OSD([sQuery(id+"F2.wireOp",EDGE,"E2.5.11.2")])],"isStart":false});
            var Q1375;
            Q1375=makeQuery(id+"F3.opExtrude","CAP_EDGE",EDGE,{"disambiguationData":[OSD([sQuery(id+"F2.wireOp",EDGE,"E3.6.24.11")])],"isStart":false});
            var Q1376;
            Q1376=makeQuery(id+"F3.opExtrude","CAP_EDGE",EDGE,{"disambiguationData":[OSD([sQuery(id+"F2.wireOp",EDGE,"E3.6.21.11")])],"isStart":false});
            var Q1377;
            Q1377=makeQuery(id+"F3.opExtrude","CAP_EDGE",EDGE,{"disambiguationData":[OSD([sQuery(id+"F2.wireOp",EDGE,"E2.8.11.2")])],"isStart":false});
            var Q1378;
            Q1378=makeQuery(id+"F3.opExtrude","CAP_EDGE",EDGE,{"disambiguationData":[OSD([sQuery(id+"F2.wireOp",EDGE,"E2.15.11.2")])],"isStart":false});
            var Q1379;
            Q1379=makeQuery(id+"F3.opExtrude","CAP_EDGE",EDGE,{"disambiguationData":[OSD([sQuery(id+"F2.wireOp",EDGE,"E2.2.11.2")])],"isStart":false});
            var Q1380;
            Q1380=makeQuery(id+"F3.opExtrude","CAP_EDGE",EDGE,{"disambiguationData":[OSD([sQuery(id+"F2.wireOp",EDGE,"E3.6.28.11")])],"isStart":false});
            var Q1381;
            Q1381=makeQuery(id+"F3.opExtrude","CAP_EDGE",EDGE,{"disambiguationData":[OSD([sQuery(id+"F2.wireOp",EDGE,"E2.0.11.3")])],"isStart":false});
            var Q1382;
            Q1382=makeQuery(id+"F3.opExtrude","CAP_EDGE",EDGE,{"disambiguationData":[OSD([sQuery(id+"F2.wireOp",EDGE,"E2.3.11.1")])],"isStart":false});
            var Q1383;
            Q1383=makeQuery(id+"F3.opExtrude","CAP_EDGE",EDGE,{"disambiguationData":[OSD([sQuery(id+"F2.wireOp",EDGE,"E3.3.22.11")])],"isStart":false});
            var Q1384;
            Q1384=makeQuery(id+"F3.opExtrude","CAP_EDGE",EDGE,{"disambiguationData":[OSD([sQuery(id+"F2.wireOp",EDGE,"E3.3.29.11")])],"isStart":false});
            var Q1385;
            Q1385=makeQuery(id+"F3.opExtrude","CAP_EDGE",EDGE,{"disambiguationData":[OSD([sQuery(id+"F2.wireOp",EDGE,"E2.16.11.1")])],"isStart":false});
            var Q1386;
            Q1386=makeQuery(id+"F3.opExtrude","CAP_EDGE",EDGE,{"disambiguationData":[OSD([sQuery(id+"F2.wireOp",EDGE,"E3.3.23.11")])],"isStart":false});
            var Q1387;
            Q1387=makeQuery(id+"F3.opExtrude","CAP_EDGE",EDGE,{"disambiguationData":[OSD([sQuery(id+"F2.wireOp",EDGE,"E2.17.11.1")])],"isStart":false});
            var Q1388;
            Q1388=makeQuery(id+"F3.opExtrude","CAP_EDGE",EDGE,{"disambiguationData":[OSD([sQuery(id+"F2.wireOp",EDGE,"E2.4.11.1")])],"isStart":false});
            var Q1389;
            Q1389=makeQuery(id+"F3.opExtrude","CAP_EDGE",EDGE,{"disambiguationData":[OSD([sQuery(id+"F2.wireOp",EDGE,"E2.11.11.1")])],"isStart":false});
            var Q1390;
            Q1390=makeQuery(id+"F3.opExtrude","CAP_EDGE",EDGE,{"disambiguationData":[OSD([sQuery(id+"F2.wireOp",EDGE,"E2.5.11.1")])],"isStart":false});
            var Q1391;
            Q1391=makeQuery(id+"F3.opExtrude","CAP_EDGE",EDGE,{"disambiguationData":[OSD([sQuery(id+"F2.wireOp",EDGE,"E3.3.24.11")])],"isStart":false});
            var Q1392;
            Q1392=makeQuery(id+"F3.opExtrude","CAP_EDGE",EDGE,{"disambiguationData":[OSD([sQuery(id+"F2.wireOp",EDGE,"E2.18.11.1")])],"isStart":false});
            var Q1393;
            Q1393=makeQuery(id+"F3.opExtrude","CAP_EDGE",EDGE,{"disambiguationData":[OSD([sQuery(id+"F2.wireOp",EDGE,"E2.9.11.1")])],"isStart":false});
            var Q1394;
            Q1394=makeQuery(id+"F3.opExtrude","CAP_EDGE",EDGE,{"disambiguationData":[OSD([sQuery(id+"F2.wireOp",EDGE,"E2.10.11.1")])],"isStart":false});
            var Q1395;
            Q1395=makeQuery(id+"F3.opExtrude","CAP_EDGE",EDGE,{"disambiguationData":[OSD([sQuery(id+"F2.wireOp",EDGE,"E2.15.11.1")])],"isStart":false});
            var Q1396;
            Q1396=makeQuery(id+"F3.opExtrude","CAP_EDGE",EDGE,{"disambiguationData":[OSD([sQuery(id+"F2.wireOp",EDGE,"E2.2.11.1")])],"isStart":false});
            var Q1397;
            Q1397=makeQuery(id+"F3.opExtrude","CAP_EDGE",EDGE,{"disambiguationData":[OSD([sQuery(id+"F2.wireOp",EDGE,"E3.3.28.11")])],"isStart":false});
            var Q1398;
            Q1398=makeQuery(id+"F3.opExtrude","CAP_EDGE",EDGE,{"disambiguationData":[OSD([sQuery(id+"F2.wireOp",EDGE,"E3.3.25.11")])],"isStart":false});
            var Q1399;
            Q1399=makeQuery(id+"F3.opExtrude","CAP_EDGE",EDGE,{"disambiguationData":[OSD([sQuery(id+"F2.wireOp",EDGE,"E2.12.11.1")])],"isStart":false});
            var Q1400;
            Q1400=makeQuery(id+"F3.opExtrude","CAP_EDGE",EDGE,{"disambiguationData":[OSD([sQuery(id+"F2.wireOp",EDGE,"E2.19.11.1")])],"isStart":false});
            var Q1401;
            Q1401=makeQuery(id+"F3.opExtrude","CAP_EDGE",EDGE,{"disambiguationData":[OSD([sQuery(id+"F2.wireOp",EDGE,"E2.6.11.1")])],"isStart":false});
            var Q1402;
            Q1402=makeQuery(id+"F3.opExtrude","CAP_EDGE",EDGE,{"disambiguationData":[OSD([sQuery(id+"F2.wireOp",EDGE,"E2.13.11.1")])],"isStart":false});
            var Q1403;
            Q1403=makeQuery(id+"F3.opExtrude","CAP_EDGE",EDGE,{"disambiguationData":[OSD([sQuery(id+"F2.wireOp",EDGE,"E2.7.11.1")])],"isStart":false});
            var Q1404;
            Q1404=makeQuery(id+"F3.opExtrude","CAP_EDGE",EDGE,{"disambiguationData":[OSD([sQuery(id+"F2.wireOp",EDGE,"E3.3.26.11")])],"isStart":false});
            var Q1405;
            Q1405=makeQuery(id+"F3.opExtrude","CAP_EDGE",EDGE,{"disambiguationData":[OSD([sQuery(id+"F2.wireOp",EDGE,"E2.1.11.1")])],"isStart":false});
            var Q1406;
            Q1406=makeQuery(id+"F3.opExtrude","CAP_EDGE",EDGE,{"disambiguationData":[OSD([sQuery(id+"F2.wireOp",EDGE,"E3.3.20.11")])],"isStart":false});
            var Q1407;
            Q1407=makeQuery(id+"F3.opExtrude","CAP_EDGE",EDGE,{"disambiguationData":[OSD([sQuery(id+"F2.wireOp",EDGE,"E3.3.27.11")])],"isStart":false});
            var Q1408;
            Q1408=makeQuery(id+"F3.opExtrude","CAP_EDGE",EDGE,{"disambiguationData":[OSD([sQuery(id+"F2.wireOp",EDGE,"E2.14.11.1")])],"isStart":false});
            var Q1409;
            Q1409=makeQuery(id+"F3.opExtrude","CAP_EDGE",EDGE,{"disambiguationData":[OSD([sQuery(id+"F2.wireOp",EDGE,"E3.3.21.11")])],"isStart":false});
            var Q1410;
            Q1410=makeQuery(id+"F3.opExtrude","CAP_EDGE",EDGE,{"disambiguationData":[OSD([sQuery(id+"F2.wireOp",EDGE,"E2.8.11.1")])],"isStart":false});
            var Q1411;
            Q1411=makeQuery(id+"F3.opExtrude","CAP_EDGE",EDGE,{"disambiguationData":[OSD([sQuery(id+"F2.wireOp",EDGE,"E2.9.11.3")])],"isStart":false});
            var Q1412;
            Q1412=makeQuery(id+"F3.opExtrude","CAP_EDGE",EDGE,{"disambiguationData":[OSD([sQuery(id+"F2.wireOp",EDGE,"E2.10.11.3")])],"isStart":false});
            var Q1413;
            Q1413=makeQuery(id+"F3.opExtrude","CAP_EDGE",EDGE,{"disambiguationData":[OSD([sQuery(id+"F2.wireOp",EDGE,"E2.3.11.3")])],"isStart":false});
            var Q1414;
            Q1414=makeQuery(id+"F3.opExtrude","CAP_EDGE",EDGE,{"disambiguationData":[OSD([sQuery(id+"F2.wireOp",EDGE,"E3.9.22.11")])],"isStart":false});
            var Q1415;
            Q1415=makeQuery(id+"F3.opExtrude","CAP_EDGE",EDGE,{"disambiguationData":[OSD([sQuery(id+"F2.wireOp",EDGE,"E3.9.29.11")])],"isStart":false});
            var Q1416;
            Q1416=makeQuery(id+"F3.opExtrude","CAP_EDGE",EDGE,{"disambiguationData":[OSD([sQuery(id+"F2.wireOp",EDGE,"E2.16.11.3")])],"isStart":false});
            var Q1417;
            Q1417=makeQuery(id+"F3.opExtrude","CAP_EDGE",EDGE,{"disambiguationData":[OSD([sQuery(id+"F2.wireOp",EDGE,"E2.13.11.3")])],"isStart":false});
            var Q1418;
            Q1418=makeQuery(id+"F3.opExtrude","CAP_EDGE",EDGE,{"disambiguationData":[OSD([sQuery(id+"F2.wireOp",EDGE,"E2.7.11.3")])],"isStart":false});
            var Q1419;
            Q1419=makeQuery(id+"F3.opExtrude","CAP_EDGE",EDGE,{"disambiguationData":[OSD([sQuery(id+"F2.wireOp",EDGE,"E3.9.26.11")])],"isStart":false});
            var Q1420;
            Q1420=makeQuery(id+"F3.opExtrude","CAP_EDGE",EDGE,{"disambiguationData":[OSD([sQuery(id+"F2.wireOp",EDGE,"E2.1.11.3")])],"isStart":false});
            var Q1421;
            Q1421=makeQuery(id+"F3.opExtrude","CAP_EDGE",EDGE,{"disambiguationData":[OSD([sQuery(id+"F2.wireOp",EDGE,"E3.9.20.11")])],"isStart":false});
            var Q1422;
            Q1422=makeQuery(id+"F3.opExtrude","CAP_EDGE",EDGE,{"disambiguationData":[OSD([sQuery(id+"F2.wireOp",EDGE,"E3.9.27.11")])],"isStart":false});
            var Q1423;
            Q1423=makeQuery(id+"F3.opExtrude","CAP_EDGE",EDGE,{"disambiguationData":[OSD([sQuery(id+"F2.wireOp",EDGE,"E2.14.11.3")])],"isStart":false});
            var Q1424;
            Q1424=makeQuery(id+"F3.opExtrude","CAP_EDGE",EDGE,{"disambiguationData":[OSD([sQuery(id+"F2.wireOp",EDGE,"E3.9.21.11")])],"isStart":false});
            var Q1425;
            Q1425=makeQuery(id+"F3.opExtrude","CAP_EDGE",EDGE,{"disambiguationData":[OSD([sQuery(id+"F2.wireOp",EDGE,"E2.8.11.3")])],"isStart":false});
            var Q1426;
            Q1426=makeQuery(id+"F3.opExtrude","CAP_EDGE",EDGE,{"disambiguationData":[OSD([sQuery(id+"F2.wireOp",EDGE,"E2.15.11.3")])],"isStart":false});
            var Q1427;
            Q1427=makeQuery(id+"F3.opExtrude","CAP_EDGE",EDGE,{"disambiguationData":[OSD([sQuery(id+"F2.wireOp",EDGE,"E2.2.11.3")])],"isStart":false});
            var Q1428;
            Q1428=makeQuery(id+"F3.opExtrude","CAP_EDGE",EDGE,{"disambiguationData":[OSD([sQuery(id+"F2.wireOp",EDGE,"E3.9.28.11")])],"isStart":false});
            var Q1429;
            Q1429=makeQuery(id+"F3.opExtrude","CAP_EDGE",EDGE,{"disambiguationData":[OSD([sQuery(id+"F2.wireOp",EDGE,"E3.9.23.11")])],"isStart":false});
            var Q1430;
            Q1430=makeQuery(id+"F3.opExtrude","CAP_EDGE",EDGE,{"disambiguationData":[OSD([sQuery(id+"F2.wireOp",EDGE,"E2.17.11.3")])],"isStart":false});
            var Q1431;
            Q1431=makeQuery(id+"F3.opExtrude","CAP_EDGE",EDGE,{"disambiguationData":[OSD([sQuery(id+"F2.wireOp",EDGE,"E2.4.11.3")])],"isStart":false});
            var Q1432;
            Q1432=makeQuery(id+"F3.opExtrude","CAP_EDGE",EDGE,{"disambiguationData":[OSD([sQuery(id+"F2.wireOp",EDGE,"E2.11.11.3")])],"isStart":false});
            var Q1433;
            Q1433=makeQuery(id+"F3.opExtrude","CAP_EDGE",EDGE,{"disambiguationData":[OSD([sQuery(id+"F2.wireOp",EDGE,"E2.5.11.3")])],"isStart":false});
            var Q1434;
            Q1434=makeQuery(id+"F3.opExtrude","CAP_EDGE",EDGE,{"disambiguationData":[OSD([sQuery(id+"F2.wireOp",EDGE,"E3.9.24.11")])],"isStart":false});
            var Q1435;
            Q1435=makeQuery(id+"F3.opExtrude","CAP_EDGE",EDGE,{"disambiguationData":[OSD([sQuery(id+"F2.wireOp",EDGE,"E2.18.11.3")])],"isStart":false});
            var Q1436;
            Q1436=makeQuery(id+"F3.opExtrude","CAP_EDGE",EDGE,{"disambiguationData":[OSD([sQuery(id+"F2.wireOp",EDGE,"E3.9.25.11")])],"isStart":false});
            var Q1437;
            Q1437=makeQuery(id+"F3.opExtrude","CAP_EDGE",EDGE,{"disambiguationData":[OSD([sQuery(id+"F2.wireOp",EDGE,"E2.12.11.3")])],"isStart":false});
            var Q1438;
            Q1438=makeQuery(id+"F3.opExtrude","CAP_EDGE",EDGE,{"disambiguationData":[OSD([sQuery(id+"F2.wireOp",EDGE,"E2.19.11.3")])],"isStart":false});
            var Q1439;
            Q1439=makeQuery(id+"F3.opExtrude","CAP_EDGE",EDGE,{"disambiguationData":[OSD([sQuery(id+"F2.wireOp",EDGE,"E2.6.11.3")])],"isStart":false});
            var Q1440;
            Q1440=makeQuery(id+"F3.opExtrude","CAP_EDGE",EDGE,{"disambiguationData":[OSD([sQuery(id+"F2.wireOp",EDGE,"E2.0.12.3")])],"isStart":false});
            var Q1441;
            Q1441=makeQuery(id+"F3.opExtrude","CAP_EDGE",EDGE,{"disambiguationData":[OSD([sQuery(id+"F2.wireOp",EDGE,"E2.0.12.0")])],"isStart":false});
            var Q1442;
            Q1442=makeQuery(id+"F3.opExtrude","CAP_EDGE",EDGE,{"disambiguationData":[OSD([sQuery(id+"F2.wireOp",EDGE,"E2.0.12.2")])],"isStart":false});
            var Q1443;
            Q1443=makeQuery(id+"F3.opExtrude","CAP_EDGE",EDGE,{"disambiguationData":[OSD([sQuery(id+"F2.wireOp",EDGE,"E3.9.29.12")])],"isStart":false});
            var Q1444;
            Q1444=makeQuery(id+"F3.opExtrude","CAP_EDGE",EDGE,{"disambiguationData":[OSD([sQuery(id+"F2.wireOp",EDGE,"E2.9.12.3")])],"isStart":false});
            var Q1445;
            Q1445=makeQuery(id+"F3.opExtrude","CAP_EDGE",EDGE,{"disambiguationData":[OSD([sQuery(id+"F2.wireOp",EDGE,"E3.9.28.12")])],"isStart":false});
            var Q1446;
            Q1446=makeQuery(id+"F3.opExtrude","CAP_EDGE",EDGE,{"disambiguationData":[OSD([sQuery(id+"F2.wireOp",EDGE,"E3.9.25.12")])],"isStart":false});
            var Q1447;
            Q1447=makeQuery(id+"F3.opExtrude","CAP_EDGE",EDGE,{"disambiguationData":[OSD([sQuery(id+"F2.wireOp",EDGE,"E2.12.12.3")])],"isStart":false});
            var Q1448;
            Q1448=makeQuery(id+"F3.opExtrude","CAP_EDGE",EDGE,{"disambiguationData":[OSD([sQuery(id+"F2.wireOp",EDGE,"E2.6.12.3")])],"isStart":false});
            var Q1449;
            Q1449=makeQuery(id+"F3.opExtrude","CAP_EDGE",EDGE,{"disambiguationData":[OSD([sQuery(id+"F2.wireOp",EDGE,"E2.19.12.3")])],"isStart":false});
            var Q1450;
            Q1450=makeQuery(id+"F3.opExtrude","CAP_EDGE",EDGE,{"disambiguationData":[OSD([sQuery(id+"F2.wireOp",EDGE,"E3.9.26.12")])],"isStart":false});
            var Q1451;
            Q1451=makeQuery(id+"F3.opExtrude","CAP_EDGE",EDGE,{"disambiguationData":[OSD([sQuery(id+"F2.wireOp",EDGE,"E2.13.12.3")])],"isStart":false});
            var Q1452;
            Q1452=makeQuery(id+"F3.opExtrude","CAP_EDGE",EDGE,{"disambiguationData":[OSD([sQuery(id+"F2.wireOp",EDGE,"E3.9.20.12")])],"isStart":false});
            var Q1453;
            Q1453=makeQuery(id+"F3.opExtrude","CAP_EDGE",EDGE,{"disambiguationData":[OSD([sQuery(id+"F2.wireOp",EDGE,"E2.1.12.3")])],"isStart":false});
            var Q1454;
            Q1454=makeQuery(id+"F3.opExtrude","CAP_EDGE",EDGE,{"disambiguationData":[OSD([sQuery(id+"F2.wireOp",EDGE,"E2.7.12.3")])],"isStart":false});
            var Q1455;
            Q1455=makeQuery(id+"F3.opExtrude","CAP_EDGE",EDGE,{"disambiguationData":[OSD([sQuery(id+"F2.wireOp",EDGE,"E3.9.27.12")])],"isStart":false});
            var Q1456;
            Q1456=makeQuery(id+"F3.opExtrude","CAP_EDGE",EDGE,{"disambiguationData":[OSD([sQuery(id+"F2.wireOp",EDGE,"E2.14.12.3")])],"isStart":false});
            var Q1457;
            Q1457=makeQuery(id+"F3.opExtrude","CAP_EDGE",EDGE,{"disambiguationData":[OSD([sQuery(id+"F2.wireOp",EDGE,"E3.9.21.12")])],"isStart":false});
            var Q1458;
            Q1458=makeQuery(id+"F3.opExtrude","CAP_EDGE",EDGE,{"disambiguationData":[OSD([sQuery(id+"F2.wireOp",EDGE,"E2.8.12.3")])],"isStart":false});
            var Q1459;
            Q1459=makeQuery(id+"F3.opExtrude","CAP_EDGE",EDGE,{"disambiguationData":[OSD([sQuery(id+"F2.wireOp",EDGE,"E2.3.12.3")])],"isStart":false});
            var Q1460;
            Q1460=makeQuery(id+"F3.opExtrude","CAP_EDGE",EDGE,{"disambiguationData":[OSD([sQuery(id+"F2.wireOp",EDGE,"E3.9.22.12")])],"isStart":false});
            var Q1461;
            Q1461=makeQuery(id+"F3.opExtrude","CAP_EDGE",EDGE,{"disambiguationData":[OSD([sQuery(id+"F2.wireOp",EDGE,"E2.16.12.3")])],"isStart":false});
            var Q1462;
            Q1462=makeQuery(id+"F3.opExtrude","CAP_EDGE",EDGE,{"disambiguationData":[OSD([sQuery(id+"F2.wireOp",EDGE,"E3.9.23.12")])],"isStart":false});
            var Q1463;
            Q1463=makeQuery(id+"F3.opExtrude","CAP_EDGE",EDGE,{"disambiguationData":[OSD([sQuery(id+"F2.wireOp",EDGE,"E2.10.12.3")])],"isStart":false});
            var Q1464;
            Q1464=makeQuery(id+"F3.opExtrude","CAP_EDGE",EDGE,{"disambiguationData":[OSD([sQuery(id+"F2.wireOp",EDGE,"E2.17.12.3")])],"isStart":false});
            var Q1465;
            Q1465=makeQuery(id+"F3.opExtrude","CAP_EDGE",EDGE,{"disambiguationData":[OSD([sQuery(id+"F2.wireOp",EDGE,"E2.4.12.3")])],"isStart":false});
            var Q1466;
            Q1466=makeQuery(id+"F3.opExtrude","CAP_EDGE",EDGE,{"disambiguationData":[OSD([sQuery(id+"F2.wireOp",EDGE,"E2.11.12.3")])],"isStart":false});
            var Q1467;
            Q1467=makeQuery(id+"F3.opExtrude","CAP_EDGE",EDGE,{"disambiguationData":[OSD([sQuery(id+"F2.wireOp",EDGE,"E2.5.12.3")])],"isStart":false});
            var Q1468;
            Q1468=makeQuery(id+"F3.opExtrude","CAP_EDGE",EDGE,{"disambiguationData":[OSD([sQuery(id+"F2.wireOp",EDGE,"E3.9.24.12")])],"isStart":false});
            var Q1469;
            Q1469=makeQuery(id+"F3.opExtrude","CAP_EDGE",EDGE,{"disambiguationData":[OSD([sQuery(id+"F2.wireOp",EDGE,"E2.18.12.3")])],"isStart":false});
            var Q1470;
            Q1470=makeQuery(id+"F3.opExtrude","CAP_EDGE",EDGE,{"disambiguationData":[OSD([sQuery(id+"F2.wireOp",EDGE,"E3.0.29.12")])],"isStart":false});
            var Q1471;
            Q1471=makeQuery(id+"F3.opExtrude","CAP_EDGE",EDGE,{"disambiguationData":[OSD([sQuery(id+"F2.wireOp",EDGE,"E3.0.28.12")])],"isStart":false});
            var Q1472;
            Q1472=makeQuery(id+"F3.opExtrude","CAP_EDGE",EDGE,{"disambiguationData":[OSD([sQuery(id+"F2.wireOp",EDGE,"E3.0.22.12")])],"isStart":false});
            var Q1473;
            Q1473=makeQuery(id+"F3.opExtrude","CAP_EDGE",EDGE,{"disambiguationData":[OSD([sQuery(id+"F2.wireOp",EDGE,"E2.9.12.0")])],"isStart":false});
            var Q1474;
            Q1474=makeQuery(id+"F3.opExtrude","CAP_EDGE",EDGE,{"disambiguationData":[OSD([sQuery(id+"F2.wireOp",EDGE,"E2.16.12.0")])],"isStart":false});
            var Q1475;
            Q1475=makeQuery(id+"F3.opExtrude","CAP_EDGE",EDGE,{"disambiguationData":[OSD([sQuery(id+"F2.wireOp",EDGE,"E2.3.12.0")])],"isStart":false});
            var Q1476;
            Q1476=makeQuery(id+"F3.opExtrude","CAP_EDGE",EDGE,{"disambiguationData":[OSD([sQuery(id+"F2.wireOp",EDGE,"E2.15.12.3")])],"isStart":false});
            var Q1477;
            Q1477=makeQuery(id+"F3.opExtrude","CAP_EDGE",EDGE,{"disambiguationData":[OSD([sQuery(id+"F2.wireOp",EDGE,"E2.2.12.3")])],"isStart":false});
            var Q1478;
            Q1478=makeQuery(id+"F3.opExtrude","CAP_EDGE",EDGE,{"disambiguationData":[OSD([sQuery(id+"F2.wireOp",EDGE,"E2.19.12.0")])],"isStart":false});
            var Q1479;
            Q1479=makeQuery(id+"F3.opExtrude","CAP_EDGE",EDGE,{"disambiguationData":[OSD([sQuery(id+"F2.wireOp",EDGE,"E2.13.12.0")])],"isStart":false});
            var Q1480;
            Q1480=makeQuery(id+"F3.opExtrude","CAP_EDGE",EDGE,{"disambiguationData":[OSD([sQuery(id+"F2.wireOp",EDGE,"E2.7.12.0")])],"isStart":false});
            var Q1481;
            Q1481=makeQuery(id+"F3.opExtrude","CAP_EDGE",EDGE,{"disambiguationData":[OSD([sQuery(id+"F2.wireOp",EDGE,"E3.0.26.12")])],"isStart":false});
            var Q1482;
            Q1482=makeQuery(id+"F3.opExtrude","CAP_EDGE",EDGE,{"disambiguationData":[OSD([sQuery(id+"F2.wireOp",EDGE,"E2.1.12.0")])],"isStart":false});
            var Q1483;
            Q1483=makeQuery(id+"F3.opExtrude","CAP_EDGE",EDGE,{"disambiguationData":[OSD([sQuery(id+"F2.wireOp",EDGE,"E3.0.20.12")])],"isStart":false});
            var Q1484;
            Q1484=makeQuery(id+"F3.opExtrude","CAP_EDGE",EDGE,{"disambiguationData":[OSD([sQuery(id+"F2.wireOp",EDGE,"E3.0.27.12")])],"isStart":false});
            var Q1485;
            Q1485=makeQuery(id+"F3.opExtrude","CAP_EDGE",EDGE,{"disambiguationData":[OSD([sQuery(id+"F2.wireOp",EDGE,"E2.14.12.0")])],"isStart":false});
            var Q1486;
            Q1486=makeQuery(id+"F3.opExtrude","CAP_EDGE",EDGE,{"disambiguationData":[OSD([sQuery(id+"F2.wireOp",EDGE,"E3.0.21.12")])],"isStart":false});
            var Q1487;
            Q1487=makeQuery(id+"F3.opExtrude","CAP_EDGE",EDGE,{"disambiguationData":[OSD([sQuery(id+"F2.wireOp",EDGE,"E2.8.12.0")])],"isStart":false});
            var Q1488;
            Q1488=makeQuery(id+"F3.opExtrude","CAP_EDGE",EDGE,{"disambiguationData":[OSD([sQuery(id+"F2.wireOp",EDGE,"E2.15.12.0")])],"isStart":false});
            var Q1489;
            Q1489=makeQuery(id+"F3.opExtrude","CAP_EDGE",EDGE,{"disambiguationData":[OSD([sQuery(id+"F2.wireOp",EDGE,"E2.2.12.0")])],"isStart":false});
            var Q1490;
            Q1490=makeQuery(id+"F3.opExtrude","CAP_EDGE",EDGE,{"disambiguationData":[OSD([sQuery(id+"F2.wireOp",EDGE,"E3.0.23.12")])],"isStart":false});
            var Q1491;
            Q1491=makeQuery(id+"F3.opExtrude","CAP_EDGE",EDGE,{"disambiguationData":[OSD([sQuery(id+"F2.wireOp",EDGE,"E2.10.12.0")])],"isStart":false});
            var Q1492;
            Q1492=makeQuery(id+"F3.opExtrude","CAP_EDGE",EDGE,{"disambiguationData":[OSD([sQuery(id+"F2.wireOp",EDGE,"E2.17.12.0")])],"isStart":false});
            var Q1493;
            Q1493=makeQuery(id+"F3.opExtrude","CAP_EDGE",EDGE,{"disambiguationData":[OSD([sQuery(id+"F2.wireOp",EDGE,"E2.4.12.0")])],"isStart":false});
            var Q1494;
            Q1494=makeQuery(id+"F3.opExtrude","CAP_EDGE",EDGE,{"disambiguationData":[OSD([sQuery(id+"F2.wireOp",EDGE,"E2.11.12.0")])],"isStart":false});
            var Q1495;
            Q1495=makeQuery(id+"F3.opExtrude","CAP_EDGE",EDGE,{"disambiguationData":[OSD([sQuery(id+"F2.wireOp",EDGE,"E2.18.12.0")])],"isStart":false});
            var Q1496;
            Q1496=makeQuery(id+"F3.opExtrude","CAP_EDGE",EDGE,{"disambiguationData":[OSD([sQuery(id+"F2.wireOp",EDGE,"E3.0.24.12")])],"isStart":false});
            var Q1497;
            Q1497=makeQuery(id+"F3.opExtrude","CAP_EDGE",EDGE,{"disambiguationData":[OSD([sQuery(id+"F2.wireOp",EDGE,"E2.5.12.0")])],"isStart":false});
            var Q1498;
            Q1498=makeQuery(id+"F3.opExtrude","CAP_EDGE",EDGE,{"disambiguationData":[OSD([sQuery(id+"F2.wireOp",EDGE,"E2.12.12.0")])],"isStart":false});
            var Q1499;
            Q1499=makeQuery(id+"F3.opExtrude","CAP_EDGE",EDGE,{"disambiguationData":[OSD([sQuery(id+"F2.wireOp",EDGE,"E2.6.12.0")])],"isStart":false});
            var Q1500;
            Q1500=makeQuery(id+"F3.opExtrude","CAP_EDGE",EDGE,{"disambiguationData":[OSD([sQuery(id+"F2.wireOp",EDGE,"E3.0.25.12")])],"isStart":false});
            var Q1501;
            Q1501=makeQuery(id+"F3.opExtrude","CAP_EDGE",EDGE,{"disambiguationData":[OSD([sQuery(id+"F2.wireOp",EDGE,"E2.0.12.1")])],"isStart":false});
            var Q1502;
            Q1502=makeQuery(id+"F3.opExtrude","CAP_EDGE",EDGE,{"disambiguationData":[OSD([sQuery(id+"F2.wireOp",EDGE,"E2.16.12.2")])],"isStart":false});
            var Q1503;
            Q1503=makeQuery(id+"F3.opExtrude","CAP_EDGE",EDGE,{"disambiguationData":[OSD([sQuery(id+"F2.wireOp",EDGE,"E3.6.23.12")])],"isStart":false});
            var Q1504;
            Q1504=makeQuery(id+"F3.opExtrude","CAP_EDGE",EDGE,{"disambiguationData":[OSD([sQuery(id+"F2.wireOp",EDGE,"E2.10.12.2")])],"isStart":false});
            var Q1505;
            Q1505=makeQuery(id+"F3.opExtrude","CAP_EDGE",EDGE,{"disambiguationData":[OSD([sQuery(id+"F2.wireOp",EDGE,"E2.17.12.2")])],"isStart":false});
            var Q1506;
            Q1506=makeQuery(id+"F3.opExtrude","CAP_EDGE",EDGE,{"disambiguationData":[OSD([sQuery(id+"F2.wireOp",EDGE,"E2.4.12.2")])],"isStart":false});
            var Q1507;
            Q1507=makeQuery(id+"F3.opExtrude","CAP_EDGE",EDGE,{"disambiguationData":[OSD([sQuery(id+"F2.wireOp",EDGE,"E2.11.12.2")])],"isStart":false});
            var Q1508;
            Q1508=makeQuery(id+"F3.opExtrude","CAP_EDGE",EDGE,{"disambiguationData":[OSD([sQuery(id+"F2.wireOp",EDGE,"E2.5.12.2")])],"isStart":false});
            var Q1509;
            Q1509=makeQuery(id+"F3.opExtrude","CAP_EDGE",EDGE,{"disambiguationData":[OSD([sQuery(id+"F2.wireOp",EDGE,"E3.6.24.12")])],"isStart":false});
            var Q1510;
            Q1510=makeQuery(id+"F3.opExtrude","CAP_EDGE",EDGE,{"disambiguationData":[OSD([sQuery(id+"F2.wireOp",EDGE,"E2.18.12.2")])],"isStart":false});
            var Q1511;
            Q1511=makeQuery(id+"F3.opExtrude","CAP_EDGE",EDGE,{"disambiguationData":[OSD([sQuery(id+"F2.wireOp",EDGE,"E3.6.25.12")])],"isStart":false});
            var Q1512;
            Q1512=makeQuery(id+"F3.opExtrude","CAP_EDGE",EDGE,{"disambiguationData":[OSD([sQuery(id+"F2.wireOp",EDGE,"E2.12.12.2")])],"isStart":false});
            var Q1513;
            Q1513=makeQuery(id+"F3.opExtrude","CAP_EDGE",EDGE,{"disambiguationData":[OSD([sQuery(id+"F2.wireOp",EDGE,"E3.6.29.12")])],"isStart":false});
            var Q1514;
            Q1514=makeQuery(id+"F3.opExtrude","CAP_EDGE",EDGE,{"disambiguationData":[OSD([sQuery(id+"F2.wireOp",EDGE,"E2.9.12.2")])],"isStart":false});
            var Q1515;
            Q1515=makeQuery(id+"F3.opExtrude","CAP_EDGE",EDGE,{"disambiguationData":[OSD([sQuery(id+"F2.wireOp",EDGE,"E3.6.28.12")])],"isStart":false});
            var Q1516;
            Q1516=makeQuery(id+"F3.opExtrude","CAP_EDGE",EDGE,{"disambiguationData":[OSD([sQuery(id+"F2.wireOp",EDGE,"E2.3.12.2")])],"isStart":false});
            var Q1517;
            Q1517=makeQuery(id+"F3.opExtrude","CAP_EDGE",EDGE,{"disambiguationData":[OSD([sQuery(id+"F2.wireOp",EDGE,"E3.6.22.12")])],"isStart":false});
            var Q1518;
            Q1518=makeQuery(id+"F3.opExtrude","CAP_EDGE",EDGE,{"disambiguationData":[OSD([sQuery(id+"F2.wireOp",EDGE,"E2.6.12.2")])],"isStart":false});
            var Q1519;
            Q1519=makeQuery(id+"F3.opExtrude","CAP_EDGE",EDGE,{"disambiguationData":[OSD([sQuery(id+"F2.wireOp",EDGE,"E2.19.12.2")])],"isStart":false});
            var Q1520;
            Q1520=makeQuery(id+"F3.opExtrude","CAP_EDGE",EDGE,{"disambiguationData":[OSD([sQuery(id+"F2.wireOp",EDGE,"E2.13.12.2")])],"isStart":false});
            var Q1521;
            Q1521=makeQuery(id+"F3.opExtrude","CAP_EDGE",EDGE,{"disambiguationData":[OSD([sQuery(id+"F2.wireOp",EDGE,"E2.7.12.2")])],"isStart":false});
            var Q1522;
            Q1522=makeQuery(id+"F3.opExtrude","CAP_EDGE",EDGE,{"disambiguationData":[OSD([sQuery(id+"F2.wireOp",EDGE,"E3.6.26.12")])],"isStart":false});
            var Q1523;
            Q1523=makeQuery(id+"F3.opExtrude","CAP_EDGE",EDGE,{"disambiguationData":[OSD([sQuery(id+"F2.wireOp",EDGE,"E2.1.12.2")])],"isStart":false});
            var Q1524;
            Q1524=makeQuery(id+"F3.opExtrude","CAP_EDGE",EDGE,{"disambiguationData":[OSD([sQuery(id+"F2.wireOp",EDGE,"E3.6.20.12")])],"isStart":false});
            var Q1525;
            Q1525=makeQuery(id+"F3.opExtrude","CAP_EDGE",EDGE,{"disambiguationData":[OSD([sQuery(id+"F2.wireOp",EDGE,"E3.6.27.12")])],"isStart":false});
            var Q1526;
            Q1526=makeQuery(id+"F3.opExtrude","CAP_EDGE",EDGE,{"disambiguationData":[OSD([sQuery(id+"F2.wireOp",EDGE,"E2.14.12.2")])],"isStart":false});
            var Q1527;
            Q1527=makeQuery(id+"F3.opExtrude","CAP_EDGE",EDGE,{"disambiguationData":[OSD([sQuery(id+"F2.wireOp",EDGE,"E3.6.21.12")])],"isStart":false});
            var Q1528;
            Q1528=makeQuery(id+"F3.opExtrude","CAP_EDGE",EDGE,{"disambiguationData":[OSD([sQuery(id+"F2.wireOp",EDGE,"E2.8.12.2")])],"isStart":false});
            var Q1529;
            Q1529=makeQuery(id+"F3.opExtrude","CAP_EDGE",EDGE,{"disambiguationData":[OSD([sQuery(id+"F2.wireOp",EDGE,"E2.15.12.2")])],"isStart":false});
            var Q1530;
            Q1530=makeQuery(id+"F3.opExtrude","CAP_EDGE",EDGE,{"disambiguationData":[OSD([sQuery(id+"F2.wireOp",EDGE,"E2.2.12.2")])],"isStart":false});
            var Q1531;
            Q1531=makeQuery(id+"F3.opExtrude","CAP_EDGE",EDGE,{"disambiguationData":[OSD([sQuery(id+"F2.wireOp",EDGE,"E3.3.29.12")])],"isStart":false});
            var Q1532;
            Q1532=makeQuery(id+"F3.opExtrude","CAP_EDGE",EDGE,{"disambiguationData":[OSD([sQuery(id+"F2.wireOp",EDGE,"E2.9.12.1")])],"isStart":false});
            var Q1533;
            Q1533=makeQuery(id+"F3.opExtrude","CAP_EDGE",EDGE,{"disambiguationData":[OSD([sQuery(id+"F2.wireOp",EDGE,"E3.3.28.12")])],"isStart":false});
            var Q1534;
            Q1534=makeQuery(id+"F3.opExtrude","CAP_EDGE",EDGE,{"disambiguationData":[OSD([sQuery(id+"F2.wireOp",EDGE,"E2.16.12.1")])],"isStart":false});
            var Q1535;
            Q1535=makeQuery(id+"F3.opExtrude","CAP_EDGE",EDGE,{"disambiguationData":[OSD([sQuery(id+"F2.wireOp",EDGE,"E3.3.22.12")])],"isStart":false});
            var Q1536;
            Q1536=makeQuery(id+"F3.opExtrude","CAP_EDGE",EDGE,{"disambiguationData":[OSD([sQuery(id+"F2.wireOp",EDGE,"E2.3.12.1")])],"isStart":false});
            var Q1537;
            Q1537=makeQuery(id+"F3.opExtrude","CAP_EDGE",EDGE,{"disambiguationData":[OSD([sQuery(id+"F2.wireOp",EDGE,"E3.3.23.12")])],"isStart":false});
            var Q1538;
            Q1538=makeQuery(id+"F3.opExtrude","CAP_EDGE",EDGE,{"disambiguationData":[OSD([sQuery(id+"F2.wireOp",EDGE,"E2.10.12.1")])],"isStart":false});
            var Q1539;
            Q1539=makeQuery(id+"F3.opExtrude","CAP_EDGE",EDGE,{"disambiguationData":[OSD([sQuery(id+"F2.wireOp",EDGE,"E2.17.12.1")])],"isStart":false});
            var Q1540;
            Q1540=makeQuery(id+"F3.opExtrude","CAP_EDGE",EDGE,{"disambiguationData":[OSD([sQuery(id+"F2.wireOp",EDGE,"E2.4.12.1")])],"isStart":false});
            var Q1541;
            Q1541=makeQuery(id+"F3.opExtrude","CAP_EDGE",EDGE,{"disambiguationData":[OSD([sQuery(id+"F2.wireOp",EDGE,"E2.1.12.1")])],"isStart":false});
            var Q1542;
            Q1542=makeQuery(id+"F3.opExtrude","CAP_EDGE",EDGE,{"disambiguationData":[OSD([sQuery(id+"F2.wireOp",EDGE,"E3.3.20.12")])],"isStart":false});
            var Q1543;
            Q1543=makeQuery(id+"F3.opExtrude","CAP_EDGE",EDGE,{"disambiguationData":[OSD([sQuery(id+"F2.wireOp",EDGE,"E3.3.27.12")])],"isStart":false});
            var Q1544;
            Q1544=makeQuery(id+"F3.opExtrude","CAP_EDGE",EDGE,{"disambiguationData":[OSD([sQuery(id+"F2.wireOp",EDGE,"E2.14.12.1")])],"isStart":false});
            var Q1545;
            Q1545=makeQuery(id+"F3.opExtrude","CAP_EDGE",EDGE,{"disambiguationData":[OSD([sQuery(id+"F2.wireOp",EDGE,"E3.3.21.12")])],"isStart":false});
            var Q1546;
            Q1546=makeQuery(id+"F3.opExtrude","CAP_EDGE",EDGE,{"disambiguationData":[OSD([sQuery(id+"F2.wireOp",EDGE,"E2.8.12.1")])],"isStart":false});
            var Q1547;
            Q1547=makeQuery(id+"F3.opExtrude","CAP_EDGE",EDGE,{"disambiguationData":[OSD([sQuery(id+"F2.wireOp",EDGE,"E2.15.12.1")])],"isStart":false});
            var Q1548;
            Q1548=makeQuery(id+"F3.opExtrude","CAP_EDGE",EDGE,{"disambiguationData":[OSD([sQuery(id+"F2.wireOp",EDGE,"E2.2.12.1")])],"isStart":false});
            var Q1549;
            Q1549=makeQuery(id+"F3.opExtrude","CAP_EDGE",EDGE,{"disambiguationData":[OSD([sQuery(id+"F2.wireOp",EDGE,"E2.11.12.1")])],"isStart":false});
            var Q1550;
            Q1550=makeQuery(id+"F3.opExtrude","CAP_EDGE",EDGE,{"disambiguationData":[OSD([sQuery(id+"F2.wireOp",EDGE,"E2.5.12.1")])],"isStart":false});
            var Q1551;
            Q1551=makeQuery(id+"F3.opExtrude","CAP_EDGE",EDGE,{"disambiguationData":[OSD([sQuery(id+"F2.wireOp",EDGE,"E3.3.24.12")])],"isStart":false});
            var Q1552;
            Q1552=makeQuery(id+"F3.opExtrude","CAP_EDGE",EDGE,{"disambiguationData":[OSD([sQuery(id+"F2.wireOp",EDGE,"E2.12.12.1")])],"isStart":false});
            var Q1553;
            Q1553=makeQuery(id+"F3.opExtrude","CAP_EDGE",EDGE,{"disambiguationData":[OSD([sQuery(id+"F2.wireOp",EDGE,"E2.18.12.1")])],"isStart":false});
            var Q1554;
            Q1554=makeQuery(id+"F3.opExtrude","CAP_EDGE",EDGE,{"disambiguationData":[OSD([sQuery(id+"F2.wireOp",EDGE,"E2.6.12.1")])],"isStart":false});
            var Q1555;
            Q1555=makeQuery(id+"F3.opExtrude","CAP_EDGE",EDGE,{"disambiguationData":[OSD([sQuery(id+"F2.wireOp",EDGE,"E3.3.25.12")])],"isStart":false});
            var Q1556;
            Q1556=makeQuery(id+"F3.opExtrude","CAP_EDGE",EDGE,{"disambiguationData":[OSD([sQuery(id+"F2.wireOp",EDGE,"E2.19.12.1")])],"isStart":false});
            var Q1557;
            Q1557=makeQuery(id+"F3.opExtrude","CAP_EDGE",EDGE,{"disambiguationData":[OSD([sQuery(id+"F2.wireOp",EDGE,"E2.13.12.1")])],"isStart":false});
            var Q1558;
            Q1558=makeQuery(id+"F3.opExtrude","CAP_EDGE",EDGE,{"disambiguationData":[OSD([sQuery(id+"F2.wireOp",EDGE,"E2.7.12.1")])],"isStart":false});
            var Q1559;
            Q1559=makeQuery(id+"F3.opExtrude","CAP_EDGE",EDGE,{"disambiguationData":[OSD([sQuery(id+"F2.wireOp",EDGE,"E3.3.26.12")])],"isStart":false});
            var Q1560;
            Q1560=makeQuery(id+"F3.opExtrude","CAP_EDGE",EDGE,{"disambiguationData":[OSD([sQuery(id+"F2.wireOp",EDGE,"E2.0.13.0")])],"isStart":false});
            var Q1561;
            Q1561=makeQuery(id+"F3.opExtrude","CAP_EDGE",EDGE,{"disambiguationData":[OSD([sQuery(id+"F2.wireOp",EDGE,"E2.0.13.2")])],"isStart":false});
            var Q1562;
            Q1562=makeQuery(id+"F3.opExtrude","CAP_EDGE",EDGE,{"disambiguationData":[OSD([sQuery(id+"F2.wireOp",EDGE,"E3.0.29.13")])],"isStart":false});
            var Q1563;
            Q1563=makeQuery(id+"F3.opExtrude","CAP_EDGE",EDGE,{"disambiguationData":[OSD([sQuery(id+"F2.wireOp",EDGE,"E2.9.13.0")])],"isStart":false});
            var Q1564;
            Q1564=makeQuery(id+"F3.opExtrude","CAP_EDGE",EDGE,{"disambiguationData":[OSD([sQuery(id+"F2.wireOp",EDGE,"E3.0.28.13")])],"isStart":false});
            var Q1565;
            Q1565=makeQuery(id+"F3.opExtrude","CAP_EDGE",EDGE,{"disambiguationData":[OSD([sQuery(id+"F2.wireOp",EDGE,"E2.3.13.0")])],"isStart":false});
            var Q1566;
            Q1566=makeQuery(id+"F3.opExtrude","CAP_EDGE",EDGE,{"disambiguationData":[OSD([sQuery(id+"F2.wireOp",EDGE,"E3.0.22.13")])],"isStart":false});
            var Q1567;
            Q1567=makeQuery(id+"F3.opExtrude","CAP_EDGE",EDGE,{"disambiguationData":[OSD([sQuery(id+"F2.wireOp",EDGE,"E2.16.13.0")])],"isStart":false});
            var Q1568;
            Q1568=makeQuery(id+"F3.opExtrude","CAP_EDGE",EDGE,{"disambiguationData":[OSD([sQuery(id+"F2.wireOp",EDGE,"E3.0.23.13")])],"isStart":false});
            var Q1569;
            Q1569=makeQuery(id+"F3.opExtrude","CAP_EDGE",EDGE,{"disambiguationData":[OSD([sQuery(id+"F2.wireOp",EDGE,"E2.10.13.0")])],"isStart":false});
            var Q1570;
            Q1570=makeQuery(id+"F3.opExtrude","CAP_EDGE",EDGE,{"disambiguationData":[OSD([sQuery(id+"F2.wireOp",EDGE,"E3.0.26.13")])],"isStart":false});
            var Q1571;
            Q1571=makeQuery(id+"F3.opExtrude","CAP_EDGE",EDGE,{"disambiguationData":[OSD([sQuery(id+"F2.wireOp",EDGE,"E2.13.13.0")])],"isStart":false});
            var Q1572;
            Q1572=makeQuery(id+"F3.opExtrude","CAP_EDGE",EDGE,{"disambiguationData":[OSD([sQuery(id+"F2.wireOp",EDGE,"E3.0.20.13")])],"isStart":false});
            var Q1573;
            Q1573=makeQuery(id+"F3.opExtrude","CAP_EDGE",EDGE,{"disambiguationData":[OSD([sQuery(id+"F2.wireOp",EDGE,"E2.7.13.0")])],"isStart":false});
            var Q1574;
            Q1574=makeQuery(id+"F3.opExtrude","CAP_EDGE",EDGE,{"disambiguationData":[OSD([sQuery(id+"F2.wireOp",EDGE,"E2.14.13.0")])],"isStart":false});
            var Q1575;
            Q1575=makeQuery(id+"F3.opExtrude","CAP_EDGE",EDGE,{"disambiguationData":[OSD([sQuery(id+"F2.wireOp",EDGE,"E2.1.13.0")])],"isStart":false});
            var Q1576;
            Q1576=makeQuery(id+"F3.opExtrude","CAP_EDGE",EDGE,{"disambiguationData":[OSD([sQuery(id+"F2.wireOp",EDGE,"E3.0.21.13")])],"isStart":false});
            var Q1577;
            Q1577=makeQuery(id+"F3.opExtrude","CAP_EDGE",EDGE,{"disambiguationData":[OSD([sQuery(id+"F2.wireOp",EDGE,"E3.0.27.13")])],"isStart":false});
            var Q1578;
            Q1578=makeQuery(id+"F3.opExtrude","CAP_EDGE",EDGE,{"disambiguationData":[OSD([sQuery(id+"F2.wireOp",EDGE,"E2.8.13.0")])],"isStart":false});
            var Q1579;
            Q1579=makeQuery(id+"F3.opExtrude","CAP_EDGE",EDGE,{"disambiguationData":[OSD([sQuery(id+"F2.wireOp",EDGE,"E2.15.13.0")])],"isStart":false});
            var Q1580;
            Q1580=makeQuery(id+"F3.opExtrude","CAP_EDGE",EDGE,{"disambiguationData":[OSD([sQuery(id+"F2.wireOp",EDGE,"E2.2.13.0")])],"isStart":false});
            var Q1581;
            Q1581=makeQuery(id+"F3.opExtrude","CAP_EDGE",EDGE,{"disambiguationData":[OSD([sQuery(id+"F2.wireOp",EDGE,"E2.17.13.0")])],"isStart":false});
            var Q1582;
            Q1582=makeQuery(id+"F3.opExtrude","CAP_EDGE",EDGE,{"disambiguationData":[OSD([sQuery(id+"F2.wireOp",EDGE,"E2.4.13.0")])],"isStart":false});
            var Q1583;
            Q1583=makeQuery(id+"F3.opExtrude","CAP_EDGE",EDGE,{"disambiguationData":[OSD([sQuery(id+"F2.wireOp",EDGE,"E2.11.13.0")])],"isStart":false});
            var Q1584;
            Q1584=makeQuery(id+"F3.opExtrude","CAP_EDGE",EDGE,{"disambiguationData":[OSD([sQuery(id+"F2.wireOp",EDGE,"E2.5.13.0")])],"isStart":false});
            var Q1585;
            Q1585=makeQuery(id+"F3.opExtrude","CAP_EDGE",EDGE,{"disambiguationData":[OSD([sQuery(id+"F2.wireOp",EDGE,"E3.0.24.13")])],"isStart":false});
            var Q1586;
            Q1586=makeQuery(id+"F3.opExtrude","CAP_EDGE",EDGE,{"disambiguationData":[OSD([sQuery(id+"F2.wireOp",EDGE,"E2.18.13.0")])],"isStart":false});
            var Q1587;
            Q1587=makeQuery(id+"F3.opExtrude","CAP_EDGE",EDGE,{"disambiguationData":[OSD([sQuery(id+"F2.wireOp",EDGE,"E3.0.25.13")])],"isStart":false});
            var Q1588;
            Q1588=makeQuery(id+"F3.opExtrude","CAP_EDGE",EDGE,{"disambiguationData":[OSD([sQuery(id+"F2.wireOp",EDGE,"E2.12.13.0")])],"isStart":false});
            var Q1589;
            Q1589=makeQuery(id+"F3.opExtrude","CAP_EDGE",EDGE,{"disambiguationData":[OSD([sQuery(id+"F2.wireOp",EDGE,"E2.6.13.0")])],"isStart":false});
            var Q1590;
            Q1590=makeQuery(id+"F3.opExtrude","CAP_EDGE",EDGE,{"disambiguationData":[OSD([sQuery(id+"F2.wireOp",EDGE,"E2.19.13.0")])],"isStart":false});
            var Q1591;
            Q1591=makeQuery(id+"F3.opExtrude","CAP_EDGE",EDGE,{"disambiguationData":[OSD([sQuery(id+"F2.wireOp",EDGE,"E3.6.29.13")])],"isStart":false});
            var Q1592;
            Q1592=makeQuery(id+"F3.opExtrude","CAP_EDGE",EDGE,{"disambiguationData":[OSD([sQuery(id+"F2.wireOp",EDGE,"E2.18.13.2")])],"isStart":false});
            var Q1593;
            Q1593=makeQuery(id+"F3.opExtrude","CAP_EDGE",EDGE,{"disambiguationData":[OSD([sQuery(id+"F2.wireOp",EDGE,"E3.6.25.13")])],"isStart":false});
            var Q1594;
            Q1594=makeQuery(id+"F3.opExtrude","CAP_EDGE",EDGE,{"disambiguationData":[OSD([sQuery(id+"F2.wireOp",EDGE,"E2.12.13.2")])],"isStart":false});
            var Q1595;
            Q1595=makeQuery(id+"F3.opExtrude","CAP_EDGE",EDGE,{"disambiguationData":[OSD([sQuery(id+"F2.wireOp",EDGE,"E2.6.13.2")])],"isStart":false});
            var Q1596;
            Q1596=makeQuery(id+"F3.opExtrude","CAP_EDGE",EDGE,{"disambiguationData":[OSD([sQuery(id+"F2.wireOp",EDGE,"E2.19.13.2")])],"isStart":false});
            var Q1597;
            Q1597=makeQuery(id+"F3.opExtrude","CAP_EDGE",EDGE,{"disambiguationData":[OSD([sQuery(id+"F2.wireOp",EDGE,"E3.6.26.13")])],"isStart":false});
            var Q1598;
            Q1598=makeQuery(id+"F3.opExtrude","CAP_EDGE",EDGE,{"disambiguationData":[OSD([sQuery(id+"F2.wireOp",EDGE,"E2.13.13.2")])],"isStart":false});
            var Q1599;
            Q1599=makeQuery(id+"F3.opExtrude","CAP_EDGE",EDGE,{"disambiguationData":[OSD([sQuery(id+"F2.wireOp",EDGE,"E3.6.20.13")])],"isStart":false});
            var Q1600;
            Q1600=makeQuery(id+"F3.opExtrude","CAP_EDGE",EDGE,{"disambiguationData":[OSD([sQuery(id+"F2.wireOp",EDGE,"E2.7.13.2")])],"isStart":false});
            var Q1601;
            Q1601=makeQuery(id+"F3.opExtrude","CAP_EDGE",EDGE,{"disambiguationData":[OSD([sQuery(id+"F2.wireOp",EDGE,"E2.14.13.2")])],"isStart":false});
            var Q1602;
            Q1602=makeQuery(id+"F3.opExtrude","CAP_EDGE",EDGE,{"disambiguationData":[OSD([sQuery(id+"F2.wireOp",EDGE,"E2.1.13.2")])],"isStart":false});
            var Q1603;
            Q1603=makeQuery(id+"F3.opExtrude","CAP_EDGE",EDGE,{"disambiguationData":[OSD([sQuery(id+"F2.wireOp",EDGE,"E2.9.13.2")])],"isStart":false});
            var Q1604;
            Q1604=makeQuery(id+"F3.opExtrude","CAP_EDGE",EDGE,{"disambiguationData":[OSD([sQuery(id+"F2.wireOp",EDGE,"E3.6.28.13")])],"isStart":false});
            var Q1605;
            Q1605=makeQuery(id+"F3.opExtrude","CAP_EDGE",EDGE,{"disambiguationData":[OSD([sQuery(id+"F2.wireOp",EDGE,"E2.3.13.2")])],"isStart":false});
            var Q1606;
            Q1606=makeQuery(id+"F3.opExtrude","CAP_EDGE",EDGE,{"disambiguationData":[OSD([sQuery(id+"F2.wireOp",EDGE,"E3.6.22.13")])],"isStart":false});
            var Q1607;
            Q1607=makeQuery(id+"F3.opExtrude","CAP_EDGE",EDGE,{"disambiguationData":[OSD([sQuery(id+"F2.wireOp",EDGE,"E2.16.13.2")])],"isStart":false});
            var Q1608;
            Q1608=makeQuery(id+"F3.opExtrude","CAP_EDGE",EDGE,{"disambiguationData":[OSD([sQuery(id+"F2.wireOp",EDGE,"E2.0.13.1")])],"isStart":false});
            var Q1609;
            Q1609=makeQuery(id+"F3.opExtrude","CAP_EDGE",EDGE,{"disambiguationData":[OSD([sQuery(id+"F2.wireOp",EDGE,"E3.6.23.13")])],"isStart":false});
            var Q1610;
            Q1610=makeQuery(id+"F3.opExtrude","CAP_EDGE",EDGE,{"disambiguationData":[OSD([sQuery(id+"F2.wireOp",EDGE,"E2.10.13.2")])],"isStart":false});
            var Q1611;
            Q1611=makeQuery(id+"F3.opExtrude","CAP_EDGE",EDGE,{"disambiguationData":[OSD([sQuery(id+"F2.wireOp",EDGE,"E2.17.13.2")])],"isStart":false});
            var Q1612;
            Q1612=makeQuery(id+"F3.opExtrude","CAP_EDGE",EDGE,{"disambiguationData":[OSD([sQuery(id+"F2.wireOp",EDGE,"E2.4.13.2")])],"isStart":false});
            var Q1613;
            Q1613=makeQuery(id+"F3.opExtrude","CAP_EDGE",EDGE,{"disambiguationData":[OSD([sQuery(id+"F2.wireOp",EDGE,"E2.11.13.2")])],"isStart":false});
            var Q1614;
            Q1614=makeQuery(id+"F3.opExtrude","CAP_EDGE",EDGE,{"disambiguationData":[OSD([sQuery(id+"F2.wireOp",EDGE,"E2.5.13.2")])],"isStart":false});
            var Q1615;
            Q1615=makeQuery(id+"F3.opExtrude","CAP_EDGE",EDGE,{"disambiguationData":[OSD([sQuery(id+"F2.wireOp",EDGE,"E3.6.24.13")])],"isStart":false});
            var Q1616;
            Q1616=makeQuery(id+"F3.opExtrude","CAP_EDGE",EDGE,{"disambiguationData":[OSD([sQuery(id+"F2.wireOp",EDGE,"E2.8.13.2")])],"isStart":false});
            var Q1617;
            Q1617=makeQuery(id+"F3.opExtrude","CAP_EDGE",EDGE,{"disambiguationData":[OSD([sQuery(id+"F2.wireOp",EDGE,"E3.6.27.13")])],"isStart":false});
            var Q1618;
            Q1618=makeQuery(id+"F3.opExtrude","CAP_EDGE",EDGE,{"disambiguationData":[OSD([sQuery(id+"F2.wireOp",EDGE,"E2.15.13.2")])],"isStart":false});
            var Q1619;
            Q1619=makeQuery(id+"F3.opExtrude","CAP_EDGE",EDGE,{"disambiguationData":[OSD([sQuery(id+"F2.wireOp",EDGE,"E3.6.21.13")])],"isStart":false});
            var Q1620;
            Q1620=makeQuery(id+"F3.opExtrude","CAP_EDGE",EDGE,{"disambiguationData":[OSD([sQuery(id+"F2.wireOp",EDGE,"E2.2.13.2")])],"isStart":false});
            var Q1621;
            Q1621=makeQuery(id+"F3.opExtrude","CAP_EDGE",EDGE,{"disambiguationData":[OSD([sQuery(id+"F2.wireOp",EDGE,"E2.0.13.3")])],"isStart":false});
            var Q1622;
            Q1622=makeQuery(id+"F3.opExtrude","CAP_EDGE",EDGE,{"disambiguationData":[OSD([sQuery(id+"F2.wireOp",EDGE,"E2.3.13.1")])],"isStart":false});
            var Q1623;
            Q1623=makeQuery(id+"F3.opExtrude","CAP_EDGE",EDGE,{"disambiguationData":[OSD([sQuery(id+"F2.wireOp",EDGE,"E3.3.22.13")])],"isStart":false});
            var Q1624;
            Q1624=makeQuery(id+"F3.opExtrude","CAP_EDGE",EDGE,{"disambiguationData":[OSD([sQuery(id+"F2.wireOp",EDGE,"E2.16.13.1")])],"isStart":false});
            var Q1625;
            Q1625=makeQuery(id+"F3.opExtrude","CAP_EDGE",EDGE,{"disambiguationData":[OSD([sQuery(id+"F2.wireOp",EDGE,"E3.3.23.13")])],"isStart":false});
            var Q1626;
            Q1626=makeQuery(id+"F3.opExtrude","CAP_EDGE",EDGE,{"disambiguationData":[OSD([sQuery(id+"F2.wireOp",EDGE,"E2.10.13.1")])],"isStart":false});
            var Q1627;
            Q1627=makeQuery(id+"F3.opExtrude","CAP_EDGE",EDGE,{"disambiguationData":[OSD([sQuery(id+"F2.wireOp",EDGE,"E2.17.13.1")])],"isStart":false});
            var Q1628;
            Q1628=makeQuery(id+"F3.opExtrude","CAP_EDGE",EDGE,{"disambiguationData":[OSD([sQuery(id+"F2.wireOp",EDGE,"E2.4.13.1")])],"isStart":false});
            var Q1629;
            Q1629=makeQuery(id+"F3.opExtrude","CAP_EDGE",EDGE,{"disambiguationData":[OSD([sQuery(id+"F2.wireOp",EDGE,"E2.11.13.1")])],"isStart":false});
            var Q1630;
            Q1630=makeQuery(id+"F3.opExtrude","CAP_EDGE",EDGE,{"disambiguationData":[OSD([sQuery(id+"F2.wireOp",EDGE,"E2.5.13.1")])],"isStart":false});
            var Q1631;
            Q1631=makeQuery(id+"F3.opExtrude","CAP_EDGE",EDGE,{"disambiguationData":[OSD([sQuery(id+"F2.wireOp",EDGE,"E3.3.24.13")])],"isStart":false});
            var Q1632;
            Q1632=makeQuery(id+"F3.opExtrude","CAP_EDGE",EDGE,{"disambiguationData":[OSD([sQuery(id+"F2.wireOp",EDGE,"E2.18.13.1")])],"isStart":false});
            var Q1633;
            Q1633=makeQuery(id+"F3.opExtrude","CAP_EDGE",EDGE,{"disambiguationData":[OSD([sQuery(id+"F2.wireOp",EDGE,"E3.3.29.13")])],"isStart":false});
            var Q1634;
            Q1634=makeQuery(id+"F3.opExtrude","CAP_EDGE",EDGE,{"disambiguationData":[OSD([sQuery(id+"F2.wireOp",EDGE,"E2.9.13.1")])],"isStart":false});
            var Q1635;
            Q1635=makeQuery(id+"F3.opExtrude","CAP_EDGE",EDGE,{"disambiguationData":[OSD([sQuery(id+"F2.wireOp",EDGE,"E3.3.28.13")])],"isStart":false});
            var Q1636;
            Q1636=makeQuery(id+"F3.opExtrude","CAP_EDGE",EDGE,{"disambiguationData":[OSD([sQuery(id+"F2.wireOp",EDGE,"E2.2.13.1")])],"isStart":false});
            var Q1637;
            Q1637=makeQuery(id+"F3.opExtrude","CAP_EDGE",EDGE,{"disambiguationData":[OSD([sQuery(id+"F2.wireOp",EDGE,"E3.3.21.13")])],"isStart":false});
            var Q1638;
            Q1638=makeQuery(id+"F3.opExtrude","CAP_EDGE",EDGE,{"disambiguationData":[OSD([sQuery(id+"F2.wireOp",EDGE,"E2.15.13.1")])],"isStart":false});
            var Q1639;
            Q1639=makeQuery(id+"F3.opExtrude","CAP_EDGE",EDGE,{"disambiguationData":[OSD([sQuery(id+"F2.wireOp",EDGE,"E3.3.25.13")])],"isStart":false});
            var Q1640;
            Q1640=makeQuery(id+"F3.opExtrude","CAP_EDGE",EDGE,{"disambiguationData":[OSD([sQuery(id+"F2.wireOp",EDGE,"E2.12.13.1")])],"isStart":false});
            var Q1641;
            Q1641=makeQuery(id+"F3.opExtrude","CAP_EDGE",EDGE,{"disambiguationData":[OSD([sQuery(id+"F2.wireOp",EDGE,"E2.6.13.1")])],"isStart":false});
            var Q1642;
            Q1642=makeQuery(id+"F3.opExtrude","CAP_EDGE",EDGE,{"disambiguationData":[OSD([sQuery(id+"F2.wireOp",EDGE,"E2.19.13.1")])],"isStart":false});
            var Q1643;
            Q1643=makeQuery(id+"F3.opExtrude","CAP_EDGE",EDGE,{"disambiguationData":[OSD([sQuery(id+"F2.wireOp",EDGE,"E3.3.26.13")])],"isStart":false});
            var Q1644;
            Q1644=makeQuery(id+"F3.opExtrude","CAP_EDGE",EDGE,{"disambiguationData":[OSD([sQuery(id+"F2.wireOp",EDGE,"E2.13.13.1")])],"isStart":false});
            var Q1645;
            Q1645=makeQuery(id+"F3.opExtrude","CAP_EDGE",EDGE,{"disambiguationData":[OSD([sQuery(id+"F2.wireOp",EDGE,"E3.3.20.13")])],"isStart":false});
            var Q1646;
            Q1646=makeQuery(id+"F3.opExtrude","CAP_EDGE",EDGE,{"disambiguationData":[OSD([sQuery(id+"F2.wireOp",EDGE,"E2.7.13.1")])],"isStart":false});
            var Q1647;
            Q1647=makeQuery(id+"F3.opExtrude","CAP_EDGE",EDGE,{"disambiguationData":[OSD([sQuery(id+"F2.wireOp",EDGE,"E2.14.13.1")])],"isStart":false});
            var Q1648;
            Q1648=makeQuery(id+"F3.opExtrude","CAP_EDGE",EDGE,{"disambiguationData":[OSD([sQuery(id+"F2.wireOp",EDGE,"E2.1.13.1")])],"isStart":false});
            var Q1649;
            Q1649=makeQuery(id+"F3.opExtrude","CAP_EDGE",EDGE,{"disambiguationData":[OSD([sQuery(id+"F2.wireOp",EDGE,"E2.8.13.1")])],"isStart":false});
            var Q1650;
            Q1650=makeQuery(id+"F3.opExtrude","CAP_EDGE",EDGE,{"disambiguationData":[OSD([sQuery(id+"F2.wireOp",EDGE,"E3.3.27.13")])],"isStart":false});
            var Q1651;
            Q1651=makeQuery(id+"F3.opExtrude","CAP_EDGE",EDGE,{"disambiguationData":[OSD([sQuery(id+"F2.wireOp",EDGE,"E3.9.29.13")])],"isStart":false});
            var Q1652;
            Q1652=makeQuery(id+"F3.opExtrude","CAP_EDGE",EDGE,{"disambiguationData":[OSD([sQuery(id+"F2.wireOp",EDGE,"E2.9.13.3")])],"isStart":false});
            var Q1653;
            Q1653=makeQuery(id+"F3.opExtrude","CAP_EDGE",EDGE,{"disambiguationData":[OSD([sQuery(id+"F2.wireOp",EDGE,"E3.9.28.13")])],"isStart":false});
            var Q1654;
            Q1654=makeQuery(id+"F3.opExtrude","CAP_EDGE",EDGE,{"disambiguationData":[OSD([sQuery(id+"F2.wireOp",EDGE,"E2.3.13.3")])],"isStart":false});
            var Q1655;
            Q1655=makeQuery(id+"F3.opExtrude","CAP_EDGE",EDGE,{"disambiguationData":[OSD([sQuery(id+"F2.wireOp",EDGE,"E3.9.22.13")])],"isStart":false});
            var Q1656;
            Q1656=makeQuery(id+"F3.opExtrude","CAP_EDGE",EDGE,{"disambiguationData":[OSD([sQuery(id+"F2.wireOp",EDGE,"E2.16.13.3")])],"isStart":false});
            var Q1657;
            Q1657=makeQuery(id+"F3.opExtrude","CAP_EDGE",EDGE,{"disambiguationData":[OSD([sQuery(id+"F2.wireOp",EDGE,"E2.19.13.3")])],"isStart":false});
            var Q1658;
            Q1658=makeQuery(id+"F3.opExtrude","CAP_EDGE",EDGE,{"disambiguationData":[OSD([sQuery(id+"F2.wireOp",EDGE,"E3.9.26.13")])],"isStart":false});
            var Q1659;
            Q1659=makeQuery(id+"F3.opExtrude","CAP_EDGE",EDGE,{"disambiguationData":[OSD([sQuery(id+"F2.wireOp",EDGE,"E2.13.13.3")])],"isStart":false});
            var Q1660;
            Q1660=makeQuery(id+"F3.opExtrude","CAP_EDGE",EDGE,{"disambiguationData":[OSD([sQuery(id+"F2.wireOp",EDGE,"E3.9.20.13")])],"isStart":false});
            var Q1661;
            Q1661=makeQuery(id+"F3.opExtrude","CAP_EDGE",EDGE,{"disambiguationData":[OSD([sQuery(id+"F2.wireOp",EDGE,"E2.7.13.3")])],"isStart":false});
            var Q1662;
            Q1662=makeQuery(id+"F3.opExtrude","CAP_EDGE",EDGE,{"disambiguationData":[OSD([sQuery(id+"F2.wireOp",EDGE,"E2.14.13.3")])],"isStart":false});
            var Q1663;
            Q1663=makeQuery(id+"F3.opExtrude","CAP_EDGE",EDGE,{"disambiguationData":[OSD([sQuery(id+"F2.wireOp",EDGE,"E2.1.13.3")])],"isStart":false});
            var Q1664;
            Q1664=makeQuery(id+"F3.opExtrude","CAP_EDGE",EDGE,{"disambiguationData":[OSD([sQuery(id+"F2.wireOp",EDGE,"E2.8.13.3")])],"isStart":false});
            var Q1665;
            Q1665=makeQuery(id+"F3.opExtrude","CAP_EDGE",EDGE,{"disambiguationData":[OSD([sQuery(id+"F2.wireOp",EDGE,"E3.9.27.13")])],"isStart":false});
            var Q1666;
            Q1666=makeQuery(id+"F3.opExtrude","CAP_EDGE",EDGE,{"disambiguationData":[OSD([sQuery(id+"F2.wireOp",EDGE,"E2.2.13.3")])],"isStart":false});
            var Q1667;
            Q1667=makeQuery(id+"F3.opExtrude","CAP_EDGE",EDGE,{"disambiguationData":[OSD([sQuery(id+"F2.wireOp",EDGE,"E3.9.21.13")])],"isStart":false});
            var Q1668;
            Q1668=makeQuery(id+"F3.opExtrude","CAP_EDGE",EDGE,{"disambiguationData":[OSD([sQuery(id+"F2.wireOp",EDGE,"E2.15.13.3")])],"isStart":false});
            var Q1669;
            Q1669=makeQuery(id+"F3.opExtrude","CAP_EDGE",EDGE,{"disambiguationData":[OSD([sQuery(id+"F2.wireOp",EDGE,"E3.9.23.13")])],"isStart":false});
            var Q1670;
            Q1670=makeQuery(id+"F3.opExtrude","CAP_EDGE",EDGE,{"disambiguationData":[OSD([sQuery(id+"F2.wireOp",EDGE,"E2.10.13.3")])],"isStart":false});
            var Q1671;
            Q1671=makeQuery(id+"F3.opExtrude","CAP_EDGE",EDGE,{"disambiguationData":[OSD([sQuery(id+"F2.wireOp",EDGE,"E2.17.13.3")])],"isStart":false});
            var Q1672;
            Q1672=makeQuery(id+"F3.opExtrude","CAP_EDGE",EDGE,{"disambiguationData":[OSD([sQuery(id+"F2.wireOp",EDGE,"E2.4.13.3")])],"isStart":false});
            var Q1673;
            Q1673=makeQuery(id+"F3.opExtrude","CAP_EDGE",EDGE,{"disambiguationData":[OSD([sQuery(id+"F2.wireOp",EDGE,"E2.11.13.3")])],"isStart":false});
            var Q1674;
            Q1674=makeQuery(id+"F3.opExtrude","CAP_EDGE",EDGE,{"disambiguationData":[OSD([sQuery(id+"F2.wireOp",EDGE,"E2.5.13.3")])],"isStart":false});
            var Q1675;
            Q1675=makeQuery(id+"F3.opExtrude","CAP_EDGE",EDGE,{"disambiguationData":[OSD([sQuery(id+"F2.wireOp",EDGE,"E3.9.24.13")])],"isStart":false});
            var Q1676;
            Q1676=makeQuery(id+"F3.opExtrude","CAP_EDGE",EDGE,{"disambiguationData":[OSD([sQuery(id+"F2.wireOp",EDGE,"E2.18.13.3")])],"isStart":false});
            var Q1677;
            Q1677=makeQuery(id+"F3.opExtrude","CAP_EDGE",EDGE,{"disambiguationData":[OSD([sQuery(id+"F2.wireOp",EDGE,"E3.9.25.13")])],"isStart":false});
            var Q1678;
            Q1678=makeQuery(id+"F3.opExtrude","CAP_EDGE",EDGE,{"disambiguationData":[OSD([sQuery(id+"F2.wireOp",EDGE,"E2.12.13.3")])],"isStart":false});
            var Q1679;
            Q1679=makeQuery(id+"F3.opExtrude","CAP_EDGE",EDGE,{"disambiguationData":[OSD([sQuery(id+"F2.wireOp",EDGE,"E2.6.13.3")])],"isStart":false});
            var Q1680;
            Q1680=makeQuery(id+"F3.opExtrude","CAP_EDGE",EDGE,{"disambiguationData":[OSD([sQuery(id+"F2.wireOp",EDGE,"E2.0.14.3")])],"isStart":false});
            var Q1681;
            Q1681=makeQuery(id+"F3.opExtrude","CAP_EDGE",EDGE,{"disambiguationData":[OSD([sQuery(id+"F2.wireOp",EDGE,"E2.0.14.0")])],"isStart":false});
            var Q1682;
            Q1682=makeQuery(id+"F3.opExtrude","CAP_EDGE",EDGE,{"disambiguationData":[OSD([sQuery(id+"F2.wireOp",EDGE,"E2.0.14.2")])],"isStart":false});
            var Q1683;
            Q1683=makeQuery(id+"F3.opExtrude","CAP_EDGE",EDGE,{"disambiguationData":[OSD([sQuery(id+"F2.wireOp",EDGE,"E3.9.29.14")])],"isStart":false});
            var Q1684;
            Q1684=makeQuery(id+"F3.opExtrude","CAP_EDGE",EDGE,{"disambiguationData":[OSD([sQuery(id+"F2.wireOp",EDGE,"E2.9.14.3")])],"isStart":false});
            var Q1685;
            Q1685=makeQuery(id+"F3.opExtrude","CAP_EDGE",EDGE,{"disambiguationData":[OSD([sQuery(id+"F2.wireOp",EDGE,"E3.9.28.14")])],"isStart":false});
            var Q1686;
            Q1686=makeQuery(id+"F3.opExtrude","CAP_EDGE",EDGE,{"disambiguationData":[OSD([sQuery(id+"F2.wireOp",EDGE,"E3.9.25.14")])],"isStart":false});
            var Q1687;
            Q1687=makeQuery(id+"F3.opExtrude","CAP_EDGE",EDGE,{"disambiguationData":[OSD([sQuery(id+"F2.wireOp",EDGE,"E2.12.14.3")])],"isStart":false});
            var Q1688;
            Q1688=makeQuery(id+"F3.opExtrude","CAP_EDGE",EDGE,{"disambiguationData":[OSD([sQuery(id+"F2.wireOp",EDGE,"E2.6.14.3")])],"isStart":false});
            var Q1689;
            Q1689=makeQuery(id+"F3.opExtrude","CAP_EDGE",EDGE,{"disambiguationData":[OSD([sQuery(id+"F2.wireOp",EDGE,"E2.19.14.3")])],"isStart":false});
            var Q1690;
            Q1690=makeQuery(id+"F3.opExtrude","CAP_EDGE",EDGE,{"disambiguationData":[OSD([sQuery(id+"F2.wireOp",EDGE,"E3.9.26.14")])],"isStart":false});
            var Q1691;
            Q1691=makeQuery(id+"F3.opExtrude","CAP_EDGE",EDGE,{"disambiguationData":[OSD([sQuery(id+"F2.wireOp",EDGE,"E2.13.14.3")])],"isStart":false});
            var Q1692;
            Q1692=makeQuery(id+"F3.opExtrude","CAP_EDGE",EDGE,{"disambiguationData":[OSD([sQuery(id+"F2.wireOp",EDGE,"E3.9.20.14")])],"isStart":false});
            var Q1693;
            Q1693=makeQuery(id+"F3.opExtrude","CAP_EDGE",EDGE,{"disambiguationData":[OSD([sQuery(id+"F2.wireOp",EDGE,"E2.7.14.3")])],"isStart":false});
            var Q1694;
            Q1694=makeQuery(id+"F3.opExtrude","CAP_EDGE",EDGE,{"disambiguationData":[OSD([sQuery(id+"F2.wireOp",EDGE,"E2.14.14.3")])],"isStart":false});
            var Q1695;
            Q1695=makeQuery(id+"F3.opExtrude","CAP_EDGE",EDGE,{"disambiguationData":[OSD([sQuery(id+"F2.wireOp",EDGE,"E2.1.14.3")])],"isStart":false});
            var Q1696;
            Q1696=makeQuery(id+"F3.opExtrude","CAP_EDGE",EDGE,{"disambiguationData":[OSD([sQuery(id+"F2.wireOp",EDGE,"E2.8.14.3")])],"isStart":false});
            var Q1697;
            Q1697=makeQuery(id+"F3.opExtrude","CAP_EDGE",EDGE,{"disambiguationData":[OSD([sQuery(id+"F2.wireOp",EDGE,"E3.9.27.14")])],"isStart":false});
            var Q1698;
            Q1698=makeQuery(id+"F3.opExtrude","CAP_EDGE",EDGE,{"disambiguationData":[OSD([sQuery(id+"F2.wireOp",EDGE,"E2.3.14.3")])],"isStart":false});
            var Q1699;
            Q1699=makeQuery(id+"F3.opExtrude","CAP_EDGE",EDGE,{"disambiguationData":[OSD([sQuery(id+"F2.wireOp",EDGE,"E3.9.22.14")])],"isStart":false});
            var Q1700;
            Q1700=makeQuery(id+"F3.opExtrude","CAP_EDGE",EDGE,{"disambiguationData":[OSD([sQuery(id+"F2.wireOp",EDGE,"E2.16.14.3")])],"isStart":false});
            var Q1701;
            Q1701=makeQuery(id+"F3.opExtrude","CAP_EDGE",EDGE,{"disambiguationData":[OSD([sQuery(id+"F2.wireOp",EDGE,"E2.10.14.3")])],"isStart":false});
            var Q1702;
            Q1702=makeQuery(id+"F3.opExtrude","CAP_EDGE",EDGE,{"disambiguationData":[OSD([sQuery(id+"F2.wireOp",EDGE,"E2.4.14.3")])],"isStart":false});
            var Q1703;
            Q1703=makeQuery(id+"F3.opExtrude","CAP_EDGE",EDGE,{"disambiguationData":[OSD([sQuery(id+"F2.wireOp",EDGE,"E3.9.23.14")])],"isStart":false});
            var Q1704;
            Q1704=makeQuery(id+"F3.opExtrude","CAP_EDGE",EDGE,{"disambiguationData":[OSD([sQuery(id+"F2.wireOp",EDGE,"E2.11.14.3")])],"isStart":false});
            var Q1705;
            Q1705=makeQuery(id+"F3.opExtrude","CAP_EDGE",EDGE,{"disambiguationData":[OSD([sQuery(id+"F2.wireOp",EDGE,"E2.17.14.3")])],"isStart":false});
            var Q1706;
            Q1706=makeQuery(id+"F3.opExtrude","CAP_EDGE",EDGE,{"disambiguationData":[OSD([sQuery(id+"F2.wireOp",EDGE,"E2.5.14.3")])],"isStart":false});
            var Q1707;
            Q1707=makeQuery(id+"F3.opExtrude","CAP_EDGE",EDGE,{"disambiguationData":[OSD([sQuery(id+"F2.wireOp",EDGE,"E3.9.24.14")])],"isStart":false});
            var Q1708;
            Q1708=makeQuery(id+"F3.opExtrude","CAP_EDGE",EDGE,{"disambiguationData":[OSD([sQuery(id+"F2.wireOp",EDGE,"E2.18.14.3")])],"isStart":false});
            var Q1709;
            Q1709=makeQuery(id+"F3.opExtrude","CAP_EDGE",EDGE,{"disambiguationData":[OSD([sQuery(id+"F2.wireOp",EDGE,"E3.0.29.14")])],"isStart":false});
            var Q1710;
            Q1710=makeQuery(id+"F3.opExtrude","CAP_EDGE",EDGE,{"disambiguationData":[OSD([sQuery(id+"F2.wireOp",EDGE,"E2.9.14.0")])],"isStart":false});
            var Q1711;
            Q1711=makeQuery(id+"F3.opExtrude","CAP_EDGE",EDGE,{"disambiguationData":[OSD([sQuery(id+"F2.wireOp",EDGE,"E3.0.28.14")])],"isStart":false});
            var Q1712;
            Q1712=makeQuery(id+"F3.opExtrude","CAP_EDGE",EDGE,{"disambiguationData":[OSD([sQuery(id+"F2.wireOp",EDGE,"E2.3.14.0")])],"isStart":false});
            var Q1713;
            Q1713=makeQuery(id+"F3.opExtrude","CAP_EDGE",EDGE,{"disambiguationData":[OSD([sQuery(id+"F2.wireOp",EDGE,"E3.0.22.14")])],"isStart":false});
            var Q1714;
            Q1714=makeQuery(id+"F3.opExtrude","CAP_EDGE",EDGE,{"disambiguationData":[OSD([sQuery(id+"F2.wireOp",EDGE,"E2.2.14.3")])],"isStart":false});
            var Q1715;
            Q1715=makeQuery(id+"F3.opExtrude","CAP_EDGE",EDGE,{"disambiguationData":[OSD([sQuery(id+"F2.wireOp",EDGE,"E3.9.21.14")])],"isStart":false});
            var Q1716;
            Q1716=makeQuery(id+"F3.opExtrude","CAP_EDGE",EDGE,{"disambiguationData":[OSD([sQuery(id+"F2.wireOp",EDGE,"E2.15.14.3")])],"isStart":false});
            var Q1717;
            Q1717=makeQuery(id+"F3.opExtrude","CAP_EDGE",EDGE,{"disambiguationData":[OSD([sQuery(id+"F2.wireOp",EDGE,"E2.6.14.0")])],"isStart":false});
            var Q1718;
            Q1718=makeQuery(id+"F3.opExtrude","CAP_EDGE",EDGE,{"disambiguationData":[OSD([sQuery(id+"F2.wireOp",EDGE,"E2.19.14.0")])],"isStart":false});
            var Q1719;
            Q1719=makeQuery(id+"F3.opExtrude","CAP_EDGE",EDGE,{"disambiguationData":[OSD([sQuery(id+"F2.wireOp",EDGE,"E3.0.26.14")])],"isStart":false});
            var Q1720;
            Q1720=makeQuery(id+"F3.opExtrude","CAP_EDGE",EDGE,{"disambiguationData":[OSD([sQuery(id+"F2.wireOp",EDGE,"E2.13.14.0")])],"isStart":false});
            var Q1721;
            Q1721=makeQuery(id+"F3.opExtrude","CAP_EDGE",EDGE,{"disambiguationData":[OSD([sQuery(id+"F2.wireOp",EDGE,"E3.0.20.14")])],"isStart":false});
            var Q1722;
            Q1722=makeQuery(id+"F3.opExtrude","CAP_EDGE",EDGE,{"disambiguationData":[OSD([sQuery(id+"F2.wireOp",EDGE,"E2.1.14.0")])],"isStart":false});
            var Q1723;
            Q1723=makeQuery(id+"F3.opExtrude","CAP_EDGE",EDGE,{"disambiguationData":[OSD([sQuery(id+"F2.wireOp",EDGE,"E2.7.14.0")])],"isStart":false});
            var Q1724;
            Q1724=makeQuery(id+"F3.opExtrude","CAP_EDGE",EDGE,{"disambiguationData":[OSD([sQuery(id+"F2.wireOp",EDGE,"E3.0.27.14")])],"isStart":false});
            var Q1725;
            Q1725=makeQuery(id+"F3.opExtrude","CAP_EDGE",EDGE,{"disambiguationData":[OSD([sQuery(id+"F2.wireOp",EDGE,"E2.14.14.0")])],"isStart":false});
            var Q1726;
            Q1726=makeQuery(id+"F3.opExtrude","CAP_EDGE",EDGE,{"disambiguationData":[OSD([sQuery(id+"F2.wireOp",EDGE,"E3.0.21.14")])],"isStart":false});
            var Q1727;
            Q1727=makeQuery(id+"F3.opExtrude","CAP_EDGE",EDGE,{"disambiguationData":[OSD([sQuery(id+"F2.wireOp",EDGE,"E2.8.14.0")])],"isStart":false});
            var Q1728;
            Q1728=makeQuery(id+"F3.opExtrude","CAP_EDGE",EDGE,{"disambiguationData":[OSD([sQuery(id+"F2.wireOp",EDGE,"E2.15.14.0")])],"isStart":false});
            var Q1729;
            Q1729=makeQuery(id+"F3.opExtrude","CAP_EDGE",EDGE,{"disambiguationData":[OSD([sQuery(id+"F2.wireOp",EDGE,"E2.2.14.0")])],"isStart":false});
            var Q1730;
            Q1730=makeQuery(id+"F3.opExtrude","CAP_EDGE",EDGE,{"disambiguationData":[OSD([sQuery(id+"F2.wireOp",EDGE,"E2.16.14.0")])],"isStart":false});
            var Q1731;
            Q1731=makeQuery(id+"F3.opExtrude","CAP_EDGE",EDGE,{"disambiguationData":[OSD([sQuery(id+"F2.wireOp",EDGE,"E3.0.23.14")])],"isStart":false});
            var Q1732;
            Q1732=makeQuery(id+"F3.opExtrude","CAP_EDGE",EDGE,{"disambiguationData":[OSD([sQuery(id+"F2.wireOp",EDGE,"E2.10.14.0")])],"isStart":false});
            var Q1733;
            Q1733=makeQuery(id+"F3.opExtrude","CAP_EDGE",EDGE,{"disambiguationData":[OSD([sQuery(id+"F2.wireOp",EDGE,"E2.17.14.0")])],"isStart":false});
            var Q1734;
            Q1734=makeQuery(id+"F3.opExtrude","CAP_EDGE",EDGE,{"disambiguationData":[OSD([sQuery(id+"F2.wireOp",EDGE,"E2.4.14.0")])],"isStart":false});
            var Q1735;
            Q1735=makeQuery(id+"F3.opExtrude","CAP_EDGE",EDGE,{"disambiguationData":[OSD([sQuery(id+"F2.wireOp",EDGE,"E2.11.14.0")])],"isStart":false});
            var Q1736;
            Q1736=makeQuery(id+"F3.opExtrude","CAP_EDGE",EDGE,{"disambiguationData":[OSD([sQuery(id+"F2.wireOp",EDGE,"E2.5.14.0")])],"isStart":false});
            var Q1737;
            Q1737=makeQuery(id+"F3.opExtrude","CAP_EDGE",EDGE,{"disambiguationData":[OSD([sQuery(id+"F2.wireOp",EDGE,"E3.0.24.14")])],"isStart":false});
            var Q1738;
            Q1738=makeQuery(id+"F3.opExtrude","CAP_EDGE",EDGE,{"disambiguationData":[OSD([sQuery(id+"F2.wireOp",EDGE,"E2.18.14.0")])],"isStart":false});
            var Q1739;
            Q1739=makeQuery(id+"F3.opExtrude","CAP_EDGE",EDGE,{"disambiguationData":[OSD([sQuery(id+"F2.wireOp",EDGE,"E3.0.25.14")])],"isStart":false});
            var Q1740;
            Q1740=makeQuery(id+"F3.opExtrude","CAP_EDGE",EDGE,{"disambiguationData":[OSD([sQuery(id+"F2.wireOp",EDGE,"E2.12.14.0")])],"isStart":false});
            var Q1741;
            Q1741=makeQuery(id+"F3.opExtrude","CAP_EDGE",EDGE,{"disambiguationData":[OSD([sQuery(id+"F2.wireOp",EDGE,"E2.0.14.1")])],"isStart":false});
            var Q1742;
            Q1742=makeQuery(id+"F3.opExtrude","CAP_EDGE",EDGE,{"disambiguationData":[OSD([sQuery(id+"F2.wireOp",EDGE,"E2.16.14.2")])],"isStart":false});
            var Q1743;
            Q1743=makeQuery(id+"F3.opExtrude","CAP_EDGE",EDGE,{"disambiguationData":[OSD([sQuery(id+"F2.wireOp",EDGE,"E3.6.23.14")])],"isStart":false});
            var Q1744;
            Q1744=makeQuery(id+"F3.opExtrude","CAP_EDGE",EDGE,{"disambiguationData":[OSD([sQuery(id+"F2.wireOp",EDGE,"E2.10.14.2")])],"isStart":false});
            var Q1745;
            Q1745=makeQuery(id+"F3.opExtrude","CAP_EDGE",EDGE,{"disambiguationData":[OSD([sQuery(id+"F2.wireOp",EDGE,"E2.17.14.2")])],"isStart":false});
            var Q1746;
            Q1746=makeQuery(id+"F3.opExtrude","CAP_EDGE",EDGE,{"disambiguationData":[OSD([sQuery(id+"F2.wireOp",EDGE,"E2.4.14.2")])],"isStart":false});
            var Q1747;
            Q1747=makeQuery(id+"F3.opExtrude","CAP_EDGE",EDGE,{"disambiguationData":[OSD([sQuery(id+"F2.wireOp",EDGE,"E2.11.14.2")])],"isStart":false});
            var Q1748;
            Q1748=makeQuery(id+"F3.opExtrude","CAP_EDGE",EDGE,{"disambiguationData":[OSD([sQuery(id+"F2.wireOp",EDGE,"E2.5.14.2")])],"isStart":false});
            var Q1749;
            Q1749=makeQuery(id+"F3.opExtrude","CAP_EDGE",EDGE,{"disambiguationData":[OSD([sQuery(id+"F2.wireOp",EDGE,"E3.6.24.14")])],"isStart":false});
            var Q1750;
            Q1750=makeQuery(id+"F3.opExtrude","CAP_EDGE",EDGE,{"disambiguationData":[OSD([sQuery(id+"F2.wireOp",EDGE,"E2.18.14.2")])],"isStart":false});
            var Q1751;
            Q1751=makeQuery(id+"F3.opExtrude","CAP_EDGE",EDGE,{"disambiguationData":[OSD([sQuery(id+"F2.wireOp",EDGE,"E3.6.25.14")])],"isStart":false});
            var Q1752;
            Q1752=makeQuery(id+"F3.opExtrude","CAP_EDGE",EDGE,{"disambiguationData":[OSD([sQuery(id+"F2.wireOp",EDGE,"E2.12.14.2")])],"isStart":false});
            var Q1753;
            Q1753=makeQuery(id+"F3.opExtrude","CAP_EDGE",EDGE,{"disambiguationData":[OSD([sQuery(id+"F2.wireOp",EDGE,"E3.6.29.14")])],"isStart":false});
            var Q1754;
            Q1754=makeQuery(id+"F3.opExtrude","CAP_EDGE",EDGE,{"disambiguationData":[OSD([sQuery(id+"F2.wireOp",EDGE,"E2.9.14.2")])],"isStart":false});
            var Q1755;
            Q1755=makeQuery(id+"F3.opExtrude","CAP_EDGE",EDGE,{"disambiguationData":[OSD([sQuery(id+"F2.wireOp",EDGE,"E3.6.28.14")])],"isStart":false});
            var Q1756;
            Q1756=makeQuery(id+"F3.opExtrude","CAP_EDGE",EDGE,{"disambiguationData":[OSD([sQuery(id+"F2.wireOp",EDGE,"E2.3.14.2")])],"isStart":false});
            var Q1757;
            Q1757=makeQuery(id+"F3.opExtrude","CAP_EDGE",EDGE,{"disambiguationData":[OSD([sQuery(id+"F2.wireOp",EDGE,"E3.6.22.14")])],"isStart":false});
            var Q1758;
            Q1758=makeQuery(id+"F3.opExtrude","CAP_EDGE",EDGE,{"disambiguationData":[OSD([sQuery(id+"F2.wireOp",EDGE,"E2.15.14.2")])],"isStart":false});
            var Q1759;
            Q1759=makeQuery(id+"F3.opExtrude","CAP_EDGE",EDGE,{"disambiguationData":[OSD([sQuery(id+"F2.wireOp",EDGE,"E2.6.14.2")])],"isStart":false});
            var Q1760;
            Q1760=makeQuery(id+"F3.opExtrude","CAP_EDGE",EDGE,{"disambiguationData":[OSD([sQuery(id+"F2.wireOp",EDGE,"E2.19.14.2")])],"isStart":false});
            var Q1761;
            Q1761=makeQuery(id+"F3.opExtrude","CAP_EDGE",EDGE,{"disambiguationData":[OSD([sQuery(id+"F2.wireOp",EDGE,"E3.6.26.14")])],"isStart":false});
            var Q1762;
            Q1762=makeQuery(id+"F3.opExtrude","CAP_EDGE",EDGE,{"disambiguationData":[OSD([sQuery(id+"F2.wireOp",EDGE,"E2.13.14.2")])],"isStart":false});
            var Q1763;
            Q1763=makeQuery(id+"F3.opExtrude","CAP_EDGE",EDGE,{"disambiguationData":[OSD([sQuery(id+"F2.wireOp",EDGE,"E3.6.20.14")])],"isStart":false});
            var Q1764;
            Q1764=makeQuery(id+"F3.opExtrude","CAP_EDGE",EDGE,{"disambiguationData":[OSD([sQuery(id+"F2.wireOp",EDGE,"E2.7.14.2")])],"isStart":false});
            var Q1765;
            Q1765=makeQuery(id+"F3.opExtrude","CAP_EDGE",EDGE,{"disambiguationData":[OSD([sQuery(id+"F2.wireOp",EDGE,"E2.14.14.2")])],"isStart":false});
            var Q1766;
            Q1766=makeQuery(id+"F3.opExtrude","CAP_EDGE",EDGE,{"disambiguationData":[OSD([sQuery(id+"F2.wireOp",EDGE,"E2.1.14.2")])],"isStart":false});
            var Q1767;
            Q1767=makeQuery(id+"F3.opExtrude","CAP_EDGE",EDGE,{"disambiguationData":[OSD([sQuery(id+"F2.wireOp",EDGE,"E2.8.14.2")])],"isStart":false});
            var Q1768;
            Q1768=makeQuery(id+"F3.opExtrude","CAP_EDGE",EDGE,{"disambiguationData":[OSD([sQuery(id+"F2.wireOp",EDGE,"E3.6.27.14")])],"isStart":false});
            var Q1769;
            Q1769=makeQuery(id+"F3.opExtrude","CAP_EDGE",EDGE,{"disambiguationData":[OSD([sQuery(id+"F2.wireOp",EDGE,"E2.2.14.2")])],"isStart":false});
            var Q1770;
            Q1770=makeQuery(id+"F3.opExtrude","CAP_EDGE",EDGE,{"disambiguationData":[OSD([sQuery(id+"F2.wireOp",EDGE,"E3.6.21.14")])],"isStart":false});
            var Q1771;
            Q1771=makeQuery(id+"F3.opExtrude","CAP_EDGE",EDGE,{"disambiguationData":[OSD([sQuery(id+"F2.wireOp",EDGE,"E3.3.29.14")])],"isStart":false});
            var Q1772;
            Q1772=makeQuery(id+"F3.opExtrude","CAP_EDGE",EDGE,{"disambiguationData":[OSD([sQuery(id+"F2.wireOp",EDGE,"E2.9.14.1")])],"isStart":false});
            var Q1773;
            Q1773=makeQuery(id+"F3.opExtrude","CAP_EDGE",EDGE,{"disambiguationData":[OSD([sQuery(id+"F2.wireOp",EDGE,"E3.3.28.14")])],"isStart":false});
            var Q1774;
            Q1774=makeQuery(id+"F3.opExtrude","CAP_EDGE",EDGE,{"disambiguationData":[OSD([sQuery(id+"F2.wireOp",EDGE,"E2.3.14.1")])],"isStart":false});
            var Q1775;
            Q1775=makeQuery(id+"F3.opExtrude","CAP_EDGE",EDGE,{"disambiguationData":[OSD([sQuery(id+"F2.wireOp",EDGE,"E3.3.22.14")])],"isStart":false});
            var Q1776;
            Q1776=makeQuery(id+"F3.opExtrude","CAP_EDGE",EDGE,{"disambiguationData":[OSD([sQuery(id+"F2.wireOp",EDGE,"E2.16.14.1")])],"isStart":false});
            var Q1777;
            Q1777=makeQuery(id+"F3.opExtrude","CAP_EDGE",EDGE,{"disambiguationData":[OSD([sQuery(id+"F2.wireOp",EDGE,"E3.3.23.14")])],"isStart":false});
            var Q1778;
            Q1778=makeQuery(id+"F3.opExtrude","CAP_EDGE",EDGE,{"disambiguationData":[OSD([sQuery(id+"F2.wireOp",EDGE,"E2.10.14.1")])],"isStart":false});
            var Q1779;
            Q1779=makeQuery(id+"F3.opExtrude","CAP_EDGE",EDGE,{"disambiguationData":[OSD([sQuery(id+"F2.wireOp",EDGE,"E2.17.14.1")])],"isStart":false});
            var Q1780;
            Q1780=makeQuery(id+"F3.opExtrude","CAP_EDGE",EDGE,{"disambiguationData":[OSD([sQuery(id+"F2.wireOp",EDGE,"E2.4.14.1")])],"isStart":false});
            var Q1781;
            Q1781=makeQuery(id+"F3.opExtrude","CAP_EDGE",EDGE,{"disambiguationData":[OSD([sQuery(id+"F2.wireOp",EDGE,"E3.3.20.14")])],"isStart":false});
            var Q1782;
            Q1782=makeQuery(id+"F3.opExtrude","CAP_EDGE",EDGE,{"disambiguationData":[OSD([sQuery(id+"F2.wireOp",EDGE,"E2.7.14.1")])],"isStart":false});
            var Q1783;
            Q1783=makeQuery(id+"F3.opExtrude","CAP_EDGE",EDGE,{"disambiguationData":[OSD([sQuery(id+"F2.wireOp",EDGE,"E2.14.14.1")])],"isStart":false});
            var Q1784;
            Q1784=makeQuery(id+"F3.opExtrude","CAP_EDGE",EDGE,{"disambiguationData":[OSD([sQuery(id+"F2.wireOp",EDGE,"E2.1.14.1")])],"isStart":false});
            var Q1785;
            Q1785=makeQuery(id+"F3.opExtrude","CAP_EDGE",EDGE,{"disambiguationData":[OSD([sQuery(id+"F2.wireOp",EDGE,"E3.3.21.14")])],"isStart":false});
            var Q1786;
            Q1786=makeQuery(id+"F3.opExtrude","CAP_EDGE",EDGE,{"disambiguationData":[OSD([sQuery(id+"F2.wireOp",EDGE,"E3.3.27.14")])],"isStart":false});
            var Q1787;
            Q1787=makeQuery(id+"F3.opExtrude","CAP_EDGE",EDGE,{"disambiguationData":[OSD([sQuery(id+"F2.wireOp",EDGE,"E2.8.14.1")])],"isStart":false});
            var Q1788;
            Q1788=makeQuery(id+"F3.opExtrude","CAP_EDGE",EDGE,{"disambiguationData":[OSD([sQuery(id+"F2.wireOp",EDGE,"E2.15.14.1")])],"isStart":false});
            var Q1789;
            Q1789=makeQuery(id+"F3.opExtrude","CAP_EDGE",EDGE,{"disambiguationData":[OSD([sQuery(id+"F2.wireOp",EDGE,"E2.2.14.1")])],"isStart":false});
            var Q1790;
            Q1790=makeQuery(id+"F3.opExtrude","CAP_EDGE",EDGE,{"disambiguationData":[OSD([sQuery(id+"F2.wireOp",EDGE,"E2.11.14.1")])],"isStart":false});
            var Q1791;
            Q1791=makeQuery(id+"F3.opExtrude","CAP_EDGE",EDGE,{"disambiguationData":[OSD([sQuery(id+"F2.wireOp",EDGE,"E2.5.14.1")])],"isStart":false});
            var Q1792;
            Q1792=makeQuery(id+"F3.opExtrude","CAP_EDGE",EDGE,{"disambiguationData":[OSD([sQuery(id+"F2.wireOp",EDGE,"E3.3.24.14")])],"isStart":false});
            var Q1793;
            Q1793=makeQuery(id+"F3.opExtrude","CAP_EDGE",EDGE,{"disambiguationData":[OSD([sQuery(id+"F2.wireOp",EDGE,"E2.18.14.1")])],"isStart":false});
            var Q1794;
            Q1794=makeQuery(id+"F3.opExtrude","CAP_EDGE",EDGE,{"disambiguationData":[OSD([sQuery(id+"F2.wireOp",EDGE,"E3.3.25.14")])],"isStart":false});
            var Q1795;
            Q1795=makeQuery(id+"F3.opExtrude","CAP_EDGE",EDGE,{"disambiguationData":[OSD([sQuery(id+"F2.wireOp",EDGE,"E2.12.14.1")])],"isStart":false});
            var Q1796;
            Q1796=makeQuery(id+"F3.opExtrude","CAP_EDGE",EDGE,{"disambiguationData":[OSD([sQuery(id+"F2.wireOp",EDGE,"E2.6.14.1")])],"isStart":false});
            var Q1797;
            Q1797=makeQuery(id+"F3.opExtrude","CAP_EDGE",EDGE,{"disambiguationData":[OSD([sQuery(id+"F2.wireOp",EDGE,"E2.19.14.1")])],"isStart":false});
            var Q1798;
            Q1798=makeQuery(id+"F3.opExtrude","CAP_EDGE",EDGE,{"disambiguationData":[OSD([sQuery(id+"F2.wireOp",EDGE,"E3.3.26.14")])],"isStart":false});
            var Q1799;
            Q1799=makeQuery(id+"F3.opExtrude","CAP_EDGE",EDGE,{"disambiguationData":[OSD([sQuery(id+"F2.wireOp",EDGE,"E2.13.14.1")])],"isStart":false});
            var Q1800;
            Q1800=makeQuery(id+"F3.opExtrude","CAP_EDGE",EDGE,{"disambiguationData":[OSD([sQuery(id+"F2.wireOp",EDGE,"E2.0.15.0")])],"isStart":false});
            var Q1801;
            Q1801=makeQuery(id+"F3.opExtrude","CAP_EDGE",EDGE,{"disambiguationData":[OSD([sQuery(id+"F2.wireOp",EDGE,"E2.0.15.2")])],"isStart":false});
            var Q1802;
            Q1802=makeQuery(id+"F3.opExtrude","CAP_EDGE",EDGE,{"disambiguationData":[OSD([sQuery(id+"F2.wireOp",EDGE,"E3.0.28.15")])],"isStart":false});
            var Q1803;
            Q1803=makeQuery(id+"F3.opExtrude","CAP_EDGE",EDGE,{"disambiguationData":[OSD([sQuery(id+"F2.wireOp",EDGE,"E2.9.15.0")])],"isStart":false});
            var Q1804;
            Q1804=makeQuery(id+"F3.opExtrude","CAP_EDGE",EDGE,{"disambiguationData":[OSD([sQuery(id+"F2.wireOp",EDGE,"E3.0.29.15")])],"isStart":false});
            var Q1805;
            Q1805=makeQuery(id+"F3.opExtrude","CAP_EDGE",EDGE,{"disambiguationData":[OSD([sQuery(id+"F2.wireOp",EDGE,"E2.3.15.0")])],"isStart":false});
            var Q1806;
            Q1806=makeQuery(id+"F3.opExtrude","CAP_EDGE",EDGE,{"disambiguationData":[OSD([sQuery(id+"F2.wireOp",EDGE,"E3.0.22.15")])],"isStart":false});
            var Q1807;
            Q1807=makeQuery(id+"F3.opExtrude","CAP_EDGE",EDGE,{"disambiguationData":[OSD([sQuery(id+"F2.wireOp",EDGE,"E2.16.15.0")])],"isStart":false});
            var Q1808;
            Q1808=makeQuery(id+"F3.opExtrude","CAP_EDGE",EDGE,{"disambiguationData":[OSD([sQuery(id+"F2.wireOp",EDGE,"E2.10.15.0")])],"isStart":false});
            var Q1809;
            Q1809=makeQuery(id+"F3.opExtrude","CAP_EDGE",EDGE,{"disambiguationData":[OSD([sQuery(id+"F2.wireOp",EDGE,"E3.0.26.15")])],"isStart":false});
            var Q1810;
            Q1810=makeQuery(id+"F3.opExtrude","CAP_EDGE",EDGE,{"disambiguationData":[OSD([sQuery(id+"F2.wireOp",EDGE,"E2.13.15.0")])],"isStart":false});
            var Q1811;
            Q1811=makeQuery(id+"F3.opExtrude","CAP_EDGE",EDGE,{"disambiguationData":[OSD([sQuery(id+"F2.wireOp",EDGE,"E3.0.20.15")])],"isStart":false});
            var Q1812;
            Q1812=makeQuery(id+"F3.opExtrude","CAP_EDGE",EDGE,{"disambiguationData":[OSD([sQuery(id+"F2.wireOp",EDGE,"E2.7.15.0")])],"isStart":false});
            var Q1813;
            Q1813=makeQuery(id+"F3.opExtrude","CAP_EDGE",EDGE,{"disambiguationData":[OSD([sQuery(id+"F2.wireOp",EDGE,"E2.14.15.0")])],"isStart":false});
            var Q1814;
            Q1814=makeQuery(id+"F3.opExtrude","CAP_EDGE",EDGE,{"disambiguationData":[OSD([sQuery(id+"F2.wireOp",EDGE,"E2.1.15.0")])],"isStart":false});
            var Q1815;
            Q1815=makeQuery(id+"F3.opExtrude","CAP_EDGE",EDGE,{"disambiguationData":[OSD([sQuery(id+"F2.wireOp",EDGE,"E2.8.15.0")])],"isStart":false});
            var Q1816;
            Q1816=makeQuery(id+"F3.opExtrude","CAP_EDGE",EDGE,{"disambiguationData":[OSD([sQuery(id+"F2.wireOp",EDGE,"E3.0.27.15")])],"isStart":false});
            var Q1817;
            Q1817=makeQuery(id+"F3.opExtrude","CAP_EDGE",EDGE,{"disambiguationData":[OSD([sQuery(id+"F2.wireOp",EDGE,"E2.2.15.0")])],"isStart":false});
            var Q1818;
            Q1818=makeQuery(id+"F3.opExtrude","CAP_EDGE",EDGE,{"disambiguationData":[OSD([sQuery(id+"F2.wireOp",EDGE,"E3.0.21.15")])],"isStart":false});
            var Q1819;
            Q1819=makeQuery(id+"F3.opExtrude","CAP_EDGE",EDGE,{"disambiguationData":[OSD([sQuery(id+"F2.wireOp",EDGE,"E2.15.15.0")])],"isStart":false});
            var Q1820;
            Q1820=makeQuery(id+"F3.opExtrude","CAP_EDGE",EDGE,{"disambiguationData":[OSD([sQuery(id+"F2.wireOp",EDGE,"E2.4.15.0")])],"isStart":false});
            var Q1821;
            Q1821=makeQuery(id+"F3.opExtrude","CAP_EDGE",EDGE,{"disambiguationData":[OSD([sQuery(id+"F2.wireOp",EDGE,"E3.0.23.15")])],"isStart":false});
            var Q1822;
            Q1822=makeQuery(id+"F3.opExtrude","CAP_EDGE",EDGE,{"disambiguationData":[OSD([sQuery(id+"F2.wireOp",EDGE,"E2.17.15.0")])],"isStart":false});
            var Q1823;
            Q1823=makeQuery(id+"F3.opExtrude","CAP_EDGE",EDGE,{"disambiguationData":[OSD([sQuery(id+"F2.wireOp",EDGE,"E3.0.24.15")])],"isStart":false});
            var Q1824;
            Q1824=makeQuery(id+"F3.opExtrude","CAP_EDGE",EDGE,{"disambiguationData":[OSD([sQuery(id+"F2.wireOp",EDGE,"E2.11.15.0")])],"isStart":false});
            var Q1825;
            Q1825=makeQuery(id+"F3.opExtrude","CAP_EDGE",EDGE,{"disambiguationData":[OSD([sQuery(id+"F2.wireOp",EDGE,"E2.18.15.0")])],"isStart":false});
            var Q1826;
            Q1826=makeQuery(id+"F3.opExtrude","CAP_EDGE",EDGE,{"disambiguationData":[OSD([sQuery(id+"F2.wireOp",EDGE,"E2.5.15.0")])],"isStart":false});
            var Q1827;
            Q1827=makeQuery(id+"F3.opExtrude","CAP_EDGE",EDGE,{"disambiguationData":[OSD([sQuery(id+"F2.wireOp",EDGE,"E3.0.25.15")])],"isStart":false});
            var Q1828;
            Q1828=makeQuery(id+"F3.opExtrude","CAP_EDGE",EDGE,{"disambiguationData":[OSD([sQuery(id+"F2.wireOp",EDGE,"E2.12.15.0")])],"isStart":false});
            var Q1829;
            Q1829=makeQuery(id+"F3.opExtrude","CAP_EDGE",EDGE,{"disambiguationData":[OSD([sQuery(id+"F2.wireOp",EDGE,"E2.6.15.0")])],"isStart":false});
            var Q1830;
            Q1830=makeQuery(id+"F3.opExtrude","CAP_EDGE",EDGE,{"disambiguationData":[OSD([sQuery(id+"F2.wireOp",EDGE,"E2.19.15.0")])],"isStart":false});
            var Q1831;
            Q1831=makeQuery(id+"F3.opExtrude","CAP_EDGE",EDGE,{"disambiguationData":[OSD([sQuery(id+"F2.wireOp",EDGE,"E2.18.15.2")])],"isStart":false});
            var Q1832;
            Q1832=makeQuery(id+"F3.opExtrude","CAP_EDGE",EDGE,{"disambiguationData":[OSD([sQuery(id+"F2.wireOp",EDGE,"E2.5.15.2")])],"isStart":false});
            var Q1833;
            Q1833=makeQuery(id+"F3.opExtrude","CAP_EDGE",EDGE,{"disambiguationData":[OSD([sQuery(id+"F2.wireOp",EDGE,"E2.12.15.2")])],"isStart":false});
            var Q1834;
            Q1834=makeQuery(id+"F3.opExtrude","CAP_EDGE",EDGE,{"disambiguationData":[OSD([sQuery(id+"F2.wireOp",EDGE,"E3.6.25.15")])],"isStart":false});
            var Q1835;
            Q1835=makeQuery(id+"F3.opExtrude","CAP_EDGE",EDGE,{"disambiguationData":[OSD([sQuery(id+"F2.wireOp",EDGE,"E2.6.15.2")])],"isStart":false});
            var Q1836;
            Q1836=makeQuery(id+"F3.opExtrude","CAP_EDGE",EDGE,{"disambiguationData":[OSD([sQuery(id+"F2.wireOp",EDGE,"E2.19.15.2")])],"isStart":false});
            var Q1837;
            Q1837=makeQuery(id+"F3.opExtrude","CAP_EDGE",EDGE,{"disambiguationData":[OSD([sQuery(id+"F2.wireOp",EDGE,"E3.6.26.15")])],"isStart":false});
            var Q1838;
            Q1838=makeQuery(id+"F3.opExtrude","CAP_EDGE",EDGE,{"disambiguationData":[OSD([sQuery(id+"F2.wireOp",EDGE,"E2.13.15.2")])],"isStart":false});
            var Q1839;
            Q1839=makeQuery(id+"F3.opExtrude","CAP_EDGE",EDGE,{"disambiguationData":[OSD([sQuery(id+"F2.wireOp",EDGE,"E3.6.20.15")])],"isStart":false});
            var Q1840;
            Q1840=makeQuery(id+"F3.opExtrude","CAP_EDGE",EDGE,{"disambiguationData":[OSD([sQuery(id+"F2.wireOp",EDGE,"E2.7.15.2")])],"isStart":false});
            var Q1841;
            Q1841=makeQuery(id+"F3.opExtrude","CAP_EDGE",EDGE,{"disambiguationData":[OSD([sQuery(id+"F2.wireOp",EDGE,"E2.14.15.2")])],"isStart":false});
            var Q1842;
            Q1842=makeQuery(id+"F3.opExtrude","CAP_EDGE",EDGE,{"disambiguationData":[OSD([sQuery(id+"F2.wireOp",EDGE,"E2.1.15.2")])],"isStart":false});
            var Q1843;
            Q1843=makeQuery(id+"F3.opExtrude","CAP_EDGE",EDGE,{"disambiguationData":[OSD([sQuery(id+"F2.wireOp",EDGE,"E3.6.28.15")])],"isStart":false});
            var Q1844;
            Q1844=makeQuery(id+"F3.opExtrude","CAP_EDGE",EDGE,{"disambiguationData":[OSD([sQuery(id+"F2.wireOp",EDGE,"E3.6.29.15")])],"isStart":false});
            var Q1845;
            Q1845=makeQuery(id+"F3.opExtrude","CAP_EDGE",EDGE,{"disambiguationData":[OSD([sQuery(id+"F2.wireOp",EDGE,"E3.6.22.15")])],"isStart":false});
            var Q1846;
            Q1846=makeQuery(id+"F3.opExtrude","CAP_EDGE",EDGE,{"disambiguationData":[OSD([sQuery(id+"F2.wireOp",EDGE,"E2.3.15.2")])],"isStart":false});
            var Q1847;
            Q1847=makeQuery(id+"F3.opExtrude","CAP_EDGE",EDGE,{"disambiguationData":[OSD([sQuery(id+"F2.wireOp",EDGE,"E2.9.15.2")])],"isStart":false});
            var Q1848;
            Q1848=makeQuery(id+"F3.opExtrude","CAP_EDGE",EDGE,{"disambiguationData":[OSD([sQuery(id+"F2.wireOp",EDGE,"E2.16.15.2")])],"isStart":false});
            var Q1849;
            Q1849=makeQuery(id+"F3.opExtrude","CAP_EDGE",EDGE,{"disambiguationData":[OSD([sQuery(id+"F2.wireOp",EDGE,"E2.0.15.1")])],"isStart":false});
            var Q1850;
            Q1850=makeQuery(id+"F3.opExtrude","CAP_EDGE",EDGE,{"disambiguationData":[OSD([sQuery(id+"F2.wireOp",EDGE,"E2.10.15.2")])],"isStart":false});
            var Q1851;
            Q1851=makeQuery(id+"F3.opExtrude","CAP_EDGE",EDGE,{"disambiguationData":[OSD([sQuery(id+"F2.wireOp",EDGE,"E2.4.15.2")])],"isStart":false});
            var Q1852;
            Q1852=makeQuery(id+"F3.opExtrude","CAP_EDGE",EDGE,{"disambiguationData":[OSD([sQuery(id+"F2.wireOp",EDGE,"E3.6.23.15")])],"isStart":false});
            var Q1853;
            Q1853=makeQuery(id+"F3.opExtrude","CAP_EDGE",EDGE,{"disambiguationData":[OSD([sQuery(id+"F2.wireOp",EDGE,"E2.17.15.2")])],"isStart":false});
            var Q1854;
            Q1854=makeQuery(id+"F3.opExtrude","CAP_EDGE",EDGE,{"disambiguationData":[OSD([sQuery(id+"F2.wireOp",EDGE,"E3.6.24.15")])],"isStart":false});
            var Q1855;
            Q1855=makeQuery(id+"F3.opExtrude","CAP_EDGE",EDGE,{"disambiguationData":[OSD([sQuery(id+"F2.wireOp",EDGE,"E2.11.15.2")])],"isStart":false});
            var Q1856;
            Q1856=makeQuery(id+"F3.opExtrude","CAP_EDGE",EDGE,{"disambiguationData":[OSD([sQuery(id+"F2.wireOp",EDGE,"E2.8.15.2")])],"isStart":false});
            var Q1857;
            Q1857=makeQuery(id+"F3.opExtrude","CAP_EDGE",EDGE,{"disambiguationData":[OSD([sQuery(id+"F2.wireOp",EDGE,"E3.6.27.15")])],"isStart":false});
            var Q1858;
            Q1858=makeQuery(id+"F3.opExtrude","CAP_EDGE",EDGE,{"disambiguationData":[OSD([sQuery(id+"F2.wireOp",EDGE,"E2.2.15.2")])],"isStart":false});
            var Q1859;
            Q1859=makeQuery(id+"F3.opExtrude","CAP_EDGE",EDGE,{"disambiguationData":[OSD([sQuery(id+"F2.wireOp",EDGE,"E3.6.21.15")])],"isStart":false});
            var Q1860;
            Q1860=makeQuery(id+"F3.opExtrude","CAP_EDGE",EDGE,{"disambiguationData":[OSD([sQuery(id+"F2.wireOp",EDGE,"E2.15.15.2")])],"isStart":false});
            var Q1861;
            Q1861=makeQuery(id+"F3.opExtrude","CAP_EDGE",EDGE,{"disambiguationData":[OSD([sQuery(id+"F2.wireOp",EDGE,"E2.0.15.3")])],"isStart":false});
            var Q1862;
            Q1862=makeQuery(id+"F3.opExtrude","CAP_EDGE",EDGE,{"disambiguationData":[OSD([sQuery(id+"F2.wireOp",EDGE,"E3.3.22.15")])],"isStart":false});
            var Q1863;
            Q1863=makeQuery(id+"F3.opExtrude","CAP_EDGE",EDGE,{"disambiguationData":[OSD([sQuery(id+"F2.wireOp",EDGE,"E2.9.15.1")])],"isStart":false});
            var Q1864;
            Q1864=makeQuery(id+"F3.opExtrude","CAP_EDGE",EDGE,{"disambiguationData":[OSD([sQuery(id+"F2.wireOp",EDGE,"E2.16.15.1")])],"isStart":false});
            var Q1865;
            Q1865=makeQuery(id+"F3.opExtrude","CAP_EDGE",EDGE,{"disambiguationData":[OSD([sQuery(id+"F2.wireOp",EDGE,"E2.3.15.1")])],"isStart":false});
            var Q1866;
            Q1866=makeQuery(id+"F3.opExtrude","CAP_EDGE",EDGE,{"disambiguationData":[OSD([sQuery(id+"F2.wireOp",EDGE,"E2.10.15.1")])],"isStart":false});
            var Q1867;
            Q1867=makeQuery(id+"F3.opExtrude","CAP_EDGE",EDGE,{"disambiguationData":[OSD([sQuery(id+"F2.wireOp",EDGE,"E2.4.15.1")])],"isStart":false});
            var Q1868;
            Q1868=makeQuery(id+"F3.opExtrude","CAP_EDGE",EDGE,{"disambiguationData":[OSD([sQuery(id+"F2.wireOp",EDGE,"E3.3.23.15")])],"isStart":false});
            var Q1869;
            Q1869=makeQuery(id+"F3.opExtrude","CAP_EDGE",EDGE,{"disambiguationData":[OSD([sQuery(id+"F2.wireOp",EDGE,"E2.17.15.1")])],"isStart":false});
            var Q1870;
            Q1870=makeQuery(id+"F3.opExtrude","CAP_EDGE",EDGE,{"disambiguationData":[OSD([sQuery(id+"F2.wireOp",EDGE,"E3.3.24.15")])],"isStart":false});
            var Q1871;
            Q1871=makeQuery(id+"F3.opExtrude","CAP_EDGE",EDGE,{"disambiguationData":[OSD([sQuery(id+"F2.wireOp",EDGE,"E2.11.15.1")])],"isStart":false});
            var Q1872;
            Q1872=makeQuery(id+"F3.opExtrude","CAP_EDGE",EDGE,{"disambiguationData":[OSD([sQuery(id+"F2.wireOp",EDGE,"E2.18.15.1")])],"isStart":false});
            var Q1873;
            Q1873=makeQuery(id+"F3.opExtrude","CAP_EDGE",EDGE,{"disambiguationData":[OSD([sQuery(id+"F2.wireOp",EDGE,"E2.5.15.1")])],"isStart":false});
            var Q1874;
            Q1874=makeQuery(id+"F3.opExtrude","CAP_EDGE",EDGE,{"disambiguationData":[OSD([sQuery(id+"F2.wireOp",EDGE,"E3.3.28.15")])],"isStart":false});
            var Q1875;
            Q1875=makeQuery(id+"F3.opExtrude","CAP_EDGE",EDGE,{"disambiguationData":[OSD([sQuery(id+"F2.wireOp",EDGE,"E3.3.29.15")])],"isStart":false});
            var Q1876;
            Q1876=makeQuery(id+"F3.opExtrude","CAP_EDGE",EDGE,{"disambiguationData":[OSD([sQuery(id+"F2.wireOp",EDGE,"E2.2.15.1")])],"isStart":false});
            var Q1877;
            Q1877=makeQuery(id+"F3.opExtrude","CAP_EDGE",EDGE,{"disambiguationData":[OSD([sQuery(id+"F2.wireOp",EDGE,"E3.3.21.15")])],"isStart":false});
            var Q1878;
            Q1878=makeQuery(id+"F3.opExtrude","CAP_EDGE",EDGE,{"disambiguationData":[OSD([sQuery(id+"F2.wireOp",EDGE,"E2.15.15.1")])],"isStart":false});
            var Q1879;
            Q1879=makeQuery(id+"F3.opExtrude","CAP_EDGE",EDGE,{"disambiguationData":[OSD([sQuery(id+"F2.wireOp",EDGE,"E2.12.15.1")])],"isStart":false});
            var Q1880;
            Q1880=makeQuery(id+"F3.opExtrude","CAP_EDGE",EDGE,{"disambiguationData":[OSD([sQuery(id+"F2.wireOp",EDGE,"E3.3.25.15")])],"isStart":false});
            var Q1881;
            Q1881=makeQuery(id+"F3.opExtrude","CAP_EDGE",EDGE,{"disambiguationData":[OSD([sQuery(id+"F2.wireOp",EDGE,"E2.6.15.1")])],"isStart":false});
            var Q1882;
            Q1882=makeQuery(id+"F3.opExtrude","CAP_EDGE",EDGE,{"disambiguationData":[OSD([sQuery(id+"F2.wireOp",EDGE,"E2.19.15.1")])],"isStart":false});
            var Q1883;
            Q1883=makeQuery(id+"F3.opExtrude","CAP_EDGE",EDGE,{"disambiguationData":[OSD([sQuery(id+"F2.wireOp",EDGE,"E3.3.26.15")])],"isStart":false});
            var Q1884;
            Q1884=makeQuery(id+"F3.opExtrude","CAP_EDGE",EDGE,{"disambiguationData":[OSD([sQuery(id+"F2.wireOp",EDGE,"E2.13.15.1")])],"isStart":false});
            var Q1885;
            Q1885=makeQuery(id+"F3.opExtrude","CAP_EDGE",EDGE,{"disambiguationData":[OSD([sQuery(id+"F2.wireOp",EDGE,"E3.3.20.15")])],"isStart":false});
            var Q1886;
            Q1886=makeQuery(id+"F3.opExtrude","CAP_EDGE",EDGE,{"disambiguationData":[OSD([sQuery(id+"F2.wireOp",EDGE,"E2.7.15.1")])],"isStart":false});
            var Q1887;
            Q1887=makeQuery(id+"F3.opExtrude","CAP_EDGE",EDGE,{"disambiguationData":[OSD([sQuery(id+"F2.wireOp",EDGE,"E2.14.15.1")])],"isStart":false});
            var Q1888;
            Q1888=makeQuery(id+"F3.opExtrude","CAP_EDGE",EDGE,{"disambiguationData":[OSD([sQuery(id+"F2.wireOp",EDGE,"E2.1.15.1")])],"isStart":false});
            var Q1889;
            Q1889=makeQuery(id+"F3.opExtrude","CAP_EDGE",EDGE,{"disambiguationData":[OSD([sQuery(id+"F2.wireOp",EDGE,"E2.8.15.1")])],"isStart":false});
            var Q1890;
            Q1890=makeQuery(id+"F3.opExtrude","CAP_EDGE",EDGE,{"disambiguationData":[OSD([sQuery(id+"F2.wireOp",EDGE,"E3.3.27.15")])],"isStart":false});
            var Q1891;
            Q1891=makeQuery(id+"F3.opExtrude","CAP_EDGE",EDGE,{"disambiguationData":[OSD([sQuery(id+"F2.wireOp",EDGE,"E3.9.28.15")])],"isStart":false});
            var Q1892;
            Q1892=makeQuery(id+"F3.opExtrude","CAP_EDGE",EDGE,{"disambiguationData":[OSD([sQuery(id+"F2.wireOp",EDGE,"E3.9.29.15")])],"isStart":false});
            var Q1893;
            Q1893=makeQuery(id+"F3.opExtrude","CAP_EDGE",EDGE,{"disambiguationData":[OSD([sQuery(id+"F2.wireOp",EDGE,"E3.9.22.15")])],"isStart":false});
            var Q1894;
            Q1894=makeQuery(id+"F3.opExtrude","CAP_EDGE",EDGE,{"disambiguationData":[OSD([sQuery(id+"F2.wireOp",EDGE,"E2.9.15.3")])],"isStart":false});
            var Q1895;
            Q1895=makeQuery(id+"F3.opExtrude","CAP_EDGE",EDGE,{"disambiguationData":[OSD([sQuery(id+"F2.wireOp",EDGE,"E2.16.15.3")])],"isStart":false});
            var Q1896;
            Q1896=makeQuery(id+"F3.opExtrude","CAP_EDGE",EDGE,{"disambiguationData":[OSD([sQuery(id+"F2.wireOp",EDGE,"E2.3.15.3")])],"isStart":false});
            var Q1897;
            Q1897=makeQuery(id+"F3.opExtrude","CAP_EDGE",EDGE,{"disambiguationData":[OSD([sQuery(id+"F2.wireOp",EDGE,"E2.19.15.3")])],"isStart":false});
            var Q1898;
            Q1898=makeQuery(id+"F3.opExtrude","CAP_EDGE",EDGE,{"disambiguationData":[OSD([sQuery(id+"F2.wireOp",EDGE,"E3.9.26.15")])],"isStart":false});
            var Q1899;
            Q1899=makeQuery(id+"F3.opExtrude","CAP_EDGE",EDGE,{"disambiguationData":[OSD([sQuery(id+"F2.wireOp",EDGE,"E2.13.15.3")])],"isStart":false});
            var Q1900;
            Q1900=makeQuery(id+"F3.opExtrude","CAP_EDGE",EDGE,{"disambiguationData":[OSD([sQuery(id+"F2.wireOp",EDGE,"E3.9.20.15")])],"isStart":false});
            var Q1901;
            Q1901=makeQuery(id+"F3.opExtrude","CAP_EDGE",EDGE,{"disambiguationData":[OSD([sQuery(id+"F2.wireOp",EDGE,"E2.7.15.3")])],"isStart":false});
            var Q1902;
            Q1902=makeQuery(id+"F3.opExtrude","CAP_EDGE",EDGE,{"disambiguationData":[OSD([sQuery(id+"F2.wireOp",EDGE,"E2.14.15.3")])],"isStart":false});
            var Q1903;
            Q1903=makeQuery(id+"F3.opExtrude","CAP_EDGE",EDGE,{"disambiguationData":[OSD([sQuery(id+"F2.wireOp",EDGE,"E2.1.15.3")])],"isStart":false});
            var Q1904;
            Q1904=makeQuery(id+"F3.opExtrude","CAP_EDGE",EDGE,{"disambiguationData":[OSD([sQuery(id+"F2.wireOp",EDGE,"E2.8.15.3")])],"isStart":false});
            var Q1905;
            Q1905=makeQuery(id+"F3.opExtrude","CAP_EDGE",EDGE,{"disambiguationData":[OSD([sQuery(id+"F2.wireOp",EDGE,"E3.9.27.15")])],"isStart":false});
            var Q1906;
            Q1906=makeQuery(id+"F3.opExtrude","CAP_EDGE",EDGE,{"disambiguationData":[OSD([sQuery(id+"F2.wireOp",EDGE,"E2.2.15.3")])],"isStart":false});
            var Q1907;
            Q1907=makeQuery(id+"F3.opExtrude","CAP_EDGE",EDGE,{"disambiguationData":[OSD([sQuery(id+"F2.wireOp",EDGE,"E3.9.21.15")])],"isStart":false});
            var Q1908;
            Q1908=makeQuery(id+"F3.opExtrude","CAP_EDGE",EDGE,{"disambiguationData":[OSD([sQuery(id+"F2.wireOp",EDGE,"E2.15.15.3")])],"isStart":false});
            var Q1909;
            Q1909=makeQuery(id+"F3.opExtrude","CAP_EDGE",EDGE,{"disambiguationData":[OSD([sQuery(id+"F2.wireOp",EDGE,"E2.10.15.3")])],"isStart":false});
            var Q1910;
            Q1910=makeQuery(id+"F3.opExtrude","CAP_EDGE",EDGE,{"disambiguationData":[OSD([sQuery(id+"F2.wireOp",EDGE,"E2.4.15.3")])],"isStart":false});
            var Q1911;
            Q1911=makeQuery(id+"F3.opExtrude","CAP_EDGE",EDGE,{"disambiguationData":[OSD([sQuery(id+"F2.wireOp",EDGE,"E3.9.23.15")])],"isStart":false});
            var Q1912;
            Q1912=makeQuery(id+"F3.opExtrude","CAP_EDGE",EDGE,{"disambiguationData":[OSD([sQuery(id+"F2.wireOp",EDGE,"E2.17.15.3")])],"isStart":false});
            var Q1913;
            Q1913=makeQuery(id+"F3.opExtrude","CAP_EDGE",EDGE,{"disambiguationData":[OSD([sQuery(id+"F2.wireOp",EDGE,"E3.9.24.15")])],"isStart":false});
            var Q1914;
            Q1914=makeQuery(id+"F3.opExtrude","CAP_EDGE",EDGE,{"disambiguationData":[OSD([sQuery(id+"F2.wireOp",EDGE,"E2.11.15.3")])],"isStart":false});
            var Q1915;
            Q1915=makeQuery(id+"F3.opExtrude","CAP_EDGE",EDGE,{"disambiguationData":[OSD([sQuery(id+"F2.wireOp",EDGE,"E2.18.15.3")])],"isStart":false});
            var Q1916;
            Q1916=makeQuery(id+"F3.opExtrude","CAP_EDGE",EDGE,{"disambiguationData":[OSD([sQuery(id+"F2.wireOp",EDGE,"E2.5.15.3")])],"isStart":false});
            var Q1917;
            Q1917=makeQuery(id+"F3.opExtrude","CAP_EDGE",EDGE,{"disambiguationData":[OSD([sQuery(id+"F2.wireOp",EDGE,"E2.12.15.3")])],"isStart":false});
            var Q1918;
            Q1918=makeQuery(id+"F3.opExtrude","CAP_EDGE",EDGE,{"disambiguationData":[OSD([sQuery(id+"F2.wireOp",EDGE,"E2.6.15.3")])],"isStart":false});
            var Q1919;
            Q1919=makeQuery(id+"F3.opExtrude","CAP_EDGE",EDGE,{"disambiguationData":[OSD([sQuery(id+"F2.wireOp",EDGE,"E3.9.25.15")])],"isStart":false});
            var Q1920;
            Q1920=makeQuery(id+"F3.opExtrude","CAP_EDGE",EDGE,{"disambiguationData":[OSD([sQuery(id+"F2.wireOp",EDGE,"E2.0.16.3")])],"isStart":false});
            var Q1921;
            Q1921=makeQuery(id+"F3.opExtrude","CAP_EDGE",EDGE,{"disambiguationData":[OSD([sQuery(id+"F2.wireOp",EDGE,"E2.0.16.0")])],"isStart":false});
            var Q1922;
            Q1922=makeQuery(id+"F3.opExtrude","CAP_EDGE",EDGE,{"disambiguationData":[OSD([sQuery(id+"F2.wireOp",EDGE,"E2.0.16.2")])],"isStart":false});
            var Q1923;
            Q1923=makeQuery(id+"F3.opExtrude","CAP_EDGE",EDGE,{"disambiguationData":[OSD([sQuery(id+"F2.wireOp",EDGE,"E2.16.16.3")])],"isStart":false});
            var Q1924;
            Q1924=makeQuery(id+"F3.opExtrude","CAP_EDGE",EDGE,{"disambiguationData":[OSD([sQuery(id+"F2.wireOp",EDGE,"E3.9.28.16")])],"isStart":false});
            var Q1925;
            Q1925=makeQuery(id+"F3.opExtrude","CAP_EDGE",EDGE,{"disambiguationData":[OSD([sQuery(id+"F2.wireOp",EDGE,"E2.15.16.3")])],"isStart":false});
            var Q1926;
            Q1926=makeQuery(id+"F3.opExtrude","CAP_EDGE",EDGE,{"disambiguationData":[OSD([sQuery(id+"F2.wireOp",EDGE,"E2.12.16.3")])],"isStart":false});
            var Q1927;
            Q1927=makeQuery(id+"F3.opExtrude","CAP_EDGE",EDGE,{"disambiguationData":[OSD([sQuery(id+"F2.wireOp",EDGE,"E3.9.25.16")])],"isStart":false});
            var Q1928;
            Q1928=makeQuery(id+"F3.opExtrude","CAP_EDGE",EDGE,{"disambiguationData":[OSD([sQuery(id+"F2.wireOp",EDGE,"E2.19.16.3")])],"isStart":false});
            var Q1929;
            Q1929=makeQuery(id+"F3.opExtrude","CAP_EDGE",EDGE,{"disambiguationData":[OSD([sQuery(id+"F2.wireOp",EDGE,"E2.6.16.3")])],"isStart":false});
            var Q1930;
            Q1930=makeQuery(id+"F3.opExtrude","CAP_EDGE",EDGE,{"disambiguationData":[OSD([sQuery(id+"F2.wireOp",EDGE,"E2.13.16.3")])],"isStart":false});
            var Q1931;
            Q1931=makeQuery(id+"F3.opExtrude","CAP_EDGE",EDGE,{"disambiguationData":[OSD([sQuery(id+"F2.wireOp",EDGE,"E3.9.20.16")])],"isStart":false});
            var Q1932;
            Q1932=makeQuery(id+"F3.opExtrude","CAP_EDGE",EDGE,{"disambiguationData":[OSD([sQuery(id+"F2.wireOp",EDGE,"E3.9.26.16")])],"isStart":false});
            var Q1933;
            Q1933=makeQuery(id+"F3.opExtrude","CAP_EDGE",EDGE,{"disambiguationData":[OSD([sQuery(id+"F2.wireOp",EDGE,"E2.7.16.3")])],"isStart":false});
            var Q1934;
            Q1934=makeQuery(id+"F3.opExtrude","CAP_EDGE",EDGE,{"disambiguationData":[OSD([sQuery(id+"F2.wireOp",EDGE,"E2.14.16.3")])],"isStart":false});
            var Q1935;
            Q1935=makeQuery(id+"F3.opExtrude","CAP_EDGE",EDGE,{"disambiguationData":[OSD([sQuery(id+"F2.wireOp",EDGE,"E2.1.16.3")])],"isStart":false});
            var Q1936;
            Q1936=makeQuery(id+"F3.opExtrude","CAP_EDGE",EDGE,{"disambiguationData":[OSD([sQuery(id+"F2.wireOp",EDGE,"E2.8.16.3")])],"isStart":false});
            var Q1937;
            Q1937=makeQuery(id+"F3.opExtrude","CAP_EDGE",EDGE,{"disambiguationData":[OSD([sQuery(id+"F2.wireOp",EDGE,"E3.9.27.16")])],"isStart":false});
            var Q1938;
            Q1938=makeQuery(id+"F3.opExtrude","CAP_EDGE",EDGE,{"disambiguationData":[OSD([sQuery(id+"F2.wireOp",EDGE,"E3.9.22.16")])],"isStart":false});
            var Q1939;
            Q1939=makeQuery(id+"F3.opExtrude","CAP_EDGE",EDGE,{"disambiguationData":[OSD([sQuery(id+"F2.wireOp",EDGE,"E2.9.16.3")])],"isStart":false});
            var Q1940;
            Q1940=makeQuery(id+"F3.opExtrude","CAP_EDGE",EDGE,{"disambiguationData":[OSD([sQuery(id+"F2.wireOp",EDGE,"E2.3.16.3")])],"isStart":false});
            var Q1941;
            Q1941=makeQuery(id+"F3.opExtrude","CAP_EDGE",EDGE,{"disambiguationData":[OSD([sQuery(id+"F2.wireOp",EDGE,"E2.10.16.3")])],"isStart":false});
            var Q1942;
            Q1942=makeQuery(id+"F3.opExtrude","CAP_EDGE",EDGE,{"disambiguationData":[OSD([sQuery(id+"F2.wireOp",EDGE,"E3.9.29.16")])],"isStart":false});
            var Q1943;
            Q1943=makeQuery(id+"F3.opExtrude","CAP_EDGE",EDGE,{"disambiguationData":[OSD([sQuery(id+"F2.wireOp",EDGE,"E2.4.16.3")])],"isStart":false});
            var Q1944;
            Q1944=makeQuery(id+"F3.opExtrude","CAP_EDGE",EDGE,{"disambiguationData":[OSD([sQuery(id+"F2.wireOp",EDGE,"E3.9.23.16")])],"isStart":false});
            var Q1945;
            Q1945=makeQuery(id+"F3.opExtrude","CAP_EDGE",EDGE,{"disambiguationData":[OSD([sQuery(id+"F2.wireOp",EDGE,"E2.17.16.3")])],"isStart":false});
            var Q1946;
            Q1946=makeQuery(id+"F3.opExtrude","CAP_EDGE",EDGE,{"disambiguationData":[OSD([sQuery(id+"F2.wireOp",EDGE,"E3.9.24.16")])],"isStart":false});
            var Q1947;
            Q1947=makeQuery(id+"F3.opExtrude","CAP_EDGE",EDGE,{"disambiguationData":[OSD([sQuery(id+"F2.wireOp",EDGE,"E2.11.16.3")])],"isStart":false});
            var Q1948;
            Q1948=makeQuery(id+"F3.opExtrude","CAP_EDGE",EDGE,{"disambiguationData":[OSD([sQuery(id+"F2.wireOp",EDGE,"E2.18.16.3")])],"isStart":false});
            var Q1949;
            Q1949=makeQuery(id+"F3.opExtrude","CAP_EDGE",EDGE,{"disambiguationData":[OSD([sQuery(id+"F2.wireOp",EDGE,"E2.5.16.3")])],"isStart":false});
            var Q1950;
            Q1950=makeQuery(id+"F3.opExtrude","CAP_EDGE",EDGE,{"disambiguationData":[OSD([sQuery(id+"F2.wireOp",EDGE,"E2.16.16.0")])],"isStart":false});
            var Q1951;
            Q1951=makeQuery(id+"F3.opExtrude","CAP_EDGE",EDGE,{"disambiguationData":[OSD([sQuery(id+"F2.wireOp",EDGE,"E2.15.16.0")])],"isStart":false});
            var Q1952;
            Q1952=makeQuery(id+"F3.opExtrude","CAP_EDGE",EDGE,{"disambiguationData":[OSD([sQuery(id+"F2.wireOp",EDGE,"E2.9.16.0")])],"isStart":false});
            var Q1953;
            Q1953=makeQuery(id+"F3.opExtrude","CAP_EDGE",EDGE,{"disambiguationData":[OSD([sQuery(id+"F2.wireOp",EDGE,"E3.0.28.16")])],"isStart":false});
            var Q1954;
            Q1954=makeQuery(id+"F3.opExtrude","CAP_EDGE",EDGE,{"disambiguationData":[OSD([sQuery(id+"F2.wireOp",EDGE,"E2.3.16.0")])],"isStart":false});
            var Q1955;
            Q1955=makeQuery(id+"F3.opExtrude","CAP_EDGE",EDGE,{"disambiguationData":[OSD([sQuery(id+"F2.wireOp",EDGE,"E3.0.22.16")])],"isStart":false});
            var Q1956;
            Q1956=makeQuery(id+"F3.opExtrude","CAP_EDGE",EDGE,{"disambiguationData":[OSD([sQuery(id+"F2.wireOp",EDGE,"E2.2.16.3")])],"isStart":false});
            var Q1957;
            Q1957=makeQuery(id+"F3.opExtrude","CAP_EDGE",EDGE,{"disambiguationData":[OSD([sQuery(id+"F2.wireOp",EDGE,"E3.9.21.16")])],"isStart":false});
            var Q1958;
            Q1958=makeQuery(id+"F3.opExtrude","CAP_EDGE",EDGE,{"disambiguationData":[OSD([sQuery(id+"F2.wireOp",EDGE,"E2.6.16.0")])],"isStart":false});
            var Q1959;
            Q1959=makeQuery(id+"F3.opExtrude","CAP_EDGE",EDGE,{"disambiguationData":[OSD([sQuery(id+"F2.wireOp",EDGE,"E2.19.16.0")])],"isStart":false});
            var Q1960;
            Q1960=makeQuery(id+"F3.opExtrude","CAP_EDGE",EDGE,{"disambiguationData":[OSD([sQuery(id+"F2.wireOp",EDGE,"E3.0.26.16")])],"isStart":false});
            var Q1961;
            Q1961=makeQuery(id+"F3.opExtrude","CAP_EDGE",EDGE,{"disambiguationData":[OSD([sQuery(id+"F2.wireOp",EDGE,"E2.13.16.0")])],"isStart":false});
            var Q1962;
            Q1962=makeQuery(id+"F3.opExtrude","CAP_EDGE",EDGE,{"disambiguationData":[OSD([sQuery(id+"F2.wireOp",EDGE,"E3.0.20.16")])],"isStart":false});
            var Q1963;
            Q1963=makeQuery(id+"F3.opExtrude","CAP_EDGE",EDGE,{"disambiguationData":[OSD([sQuery(id+"F2.wireOp",EDGE,"E2.7.16.0")])],"isStart":false});
            var Q1964;
            Q1964=makeQuery(id+"F3.opExtrude","CAP_EDGE",EDGE,{"disambiguationData":[OSD([sQuery(id+"F2.wireOp",EDGE,"E2.14.16.0")])],"isStart":false});
            var Q1965;
            Q1965=makeQuery(id+"F3.opExtrude","CAP_EDGE",EDGE,{"disambiguationData":[OSD([sQuery(id+"F2.wireOp",EDGE,"E2.1.16.0")])],"isStart":false});
            var Q1966;
            Q1966=makeQuery(id+"F3.opExtrude","CAP_EDGE",EDGE,{"disambiguationData":[OSD([sQuery(id+"F2.wireOp",EDGE,"E2.8.16.0")])],"isStart":false});
            var Q1967;
            Q1967=makeQuery(id+"F3.opExtrude","CAP_EDGE",EDGE,{"disambiguationData":[OSD([sQuery(id+"F2.wireOp",EDGE,"E3.0.27.16")])],"isStart":false});
            var Q1968;
            Q1968=makeQuery(id+"F3.opExtrude","CAP_EDGE",EDGE,{"disambiguationData":[OSD([sQuery(id+"F2.wireOp",EDGE,"E2.2.16.0")])],"isStart":false});
            var Q1969;
            Q1969=makeQuery(id+"F3.opExtrude","CAP_EDGE",EDGE,{"disambiguationData":[OSD([sQuery(id+"F2.wireOp",EDGE,"E3.0.21.16")])],"isStart":false});
            var Q1970;
            Q1970=makeQuery(id+"F3.opExtrude","CAP_EDGE",EDGE,{"disambiguationData":[OSD([sQuery(id+"F2.wireOp",EDGE,"E2.10.16.0")])],"isStart":false});
            var Q1971;
            Q1971=makeQuery(id+"F3.opExtrude","CAP_EDGE",EDGE,{"disambiguationData":[OSD([sQuery(id+"F2.wireOp",EDGE,"E3.0.29.16")])],"isStart":false});
            var Q1972;
            Q1972=makeQuery(id+"F3.opExtrude","CAP_EDGE",EDGE,{"disambiguationData":[OSD([sQuery(id+"F2.wireOp",EDGE,"E2.4.16.0")])],"isStart":false});
            var Q1973;
            Q1973=makeQuery(id+"F3.opExtrude","CAP_EDGE",EDGE,{"disambiguationData":[OSD([sQuery(id+"F2.wireOp",EDGE,"E3.0.23.16")])],"isStart":false});
            var Q1974;
            Q1974=makeQuery(id+"F3.opExtrude","CAP_EDGE",EDGE,{"disambiguationData":[OSD([sQuery(id+"F2.wireOp",EDGE,"E2.11.16.0")])],"isStart":false});
            var Q1975;
            Q1975=makeQuery(id+"F3.opExtrude","CAP_EDGE",EDGE,{"disambiguationData":[OSD([sQuery(id+"F2.wireOp",EDGE,"E2.17.16.0")])],"isStart":false});
            var Q1976;
            Q1976=makeQuery(id+"F3.opExtrude","CAP_EDGE",EDGE,{"disambiguationData":[OSD([sQuery(id+"F2.wireOp",EDGE,"E2.5.16.0")])],"isStart":false});
            var Q1977;
            Q1977=makeQuery(id+"F3.opExtrude","CAP_EDGE",EDGE,{"disambiguationData":[OSD([sQuery(id+"F2.wireOp",EDGE,"E3.0.24.16")])],"isStart":false});
            var Q1978;
            Q1978=makeQuery(id+"F3.opExtrude","CAP_EDGE",EDGE,{"disambiguationData":[OSD([sQuery(id+"F2.wireOp",EDGE,"E2.18.16.0")])],"isStart":false});
            var Q1979;
            Q1979=makeQuery(id+"F3.opExtrude","CAP_EDGE",EDGE,{"disambiguationData":[OSD([sQuery(id+"F2.wireOp",EDGE,"E3.0.25.16")])],"isStart":false});
            var Q1980;
            Q1980=makeQuery(id+"F3.opExtrude","CAP_EDGE",EDGE,{"disambiguationData":[OSD([sQuery(id+"F2.wireOp",EDGE,"E2.12.16.0")])],"isStart":false});
            var Q1981;
            Q1981=makeQuery(id+"F3.opExtrude","CAP_EDGE",EDGE,{"disambiguationData":[OSD([sQuery(id+"F2.wireOp",EDGE,"E2.0.16.1")])],"isStart":false});
            var Q1982;
            Q1982=makeQuery(id+"F3.opExtrude","CAP_EDGE",EDGE,{"disambiguationData":[OSD([sQuery(id+"F2.wireOp",EDGE,"E2.3.16.2")])],"isStart":false});
            var Q1983;
            Q1983=makeQuery(id+"F3.opExtrude","CAP_EDGE",EDGE,{"disambiguationData":[OSD([sQuery(id+"F2.wireOp",EDGE,"E2.10.16.2")])],"isStart":false});
            var Q1984;
            Q1984=makeQuery(id+"F3.opExtrude","CAP_EDGE",EDGE,{"disambiguationData":[OSD([sQuery(id+"F2.wireOp",EDGE,"E3.6.29.16")])],"isStart":false});
            var Q1985;
            Q1985=makeQuery(id+"F3.opExtrude","CAP_EDGE",EDGE,{"disambiguationData":[OSD([sQuery(id+"F2.wireOp",EDGE,"E2.4.16.2")])],"isStart":false});
            var Q1986;
            Q1986=makeQuery(id+"F3.opExtrude","CAP_EDGE",EDGE,{"disambiguationData":[OSD([sQuery(id+"F2.wireOp",EDGE,"E3.6.23.16")])],"isStart":false});
            var Q1987;
            Q1987=makeQuery(id+"F3.opExtrude","CAP_EDGE",EDGE,{"disambiguationData":[OSD([sQuery(id+"F2.wireOp",EDGE,"E2.17.16.2")])],"isStart":false});
            var Q1988;
            Q1988=makeQuery(id+"F3.opExtrude","CAP_EDGE",EDGE,{"disambiguationData":[OSD([sQuery(id+"F2.wireOp",EDGE,"E3.6.24.16")])],"isStart":false});
            var Q1989;
            Q1989=makeQuery(id+"F3.opExtrude","CAP_EDGE",EDGE,{"disambiguationData":[OSD([sQuery(id+"F2.wireOp",EDGE,"E2.11.16.2")])],"isStart":false});
            var Q1990;
            Q1990=makeQuery(id+"F3.opExtrude","CAP_EDGE",EDGE,{"disambiguationData":[OSD([sQuery(id+"F2.wireOp",EDGE,"E2.18.16.2")])],"isStart":false});
            var Q1991;
            Q1991=makeQuery(id+"F3.opExtrude","CAP_EDGE",EDGE,{"disambiguationData":[OSD([sQuery(id+"F2.wireOp",EDGE,"E2.5.16.2")])],"isStart":false});
            var Q1992;
            Q1992=makeQuery(id+"F3.opExtrude","CAP_EDGE",EDGE,{"disambiguationData":[OSD([sQuery(id+"F2.wireOp",EDGE,"E2.12.16.2")])],"isStart":false});
            var Q1993;
            Q1993=makeQuery(id+"F3.opExtrude","CAP_EDGE",EDGE,{"disambiguationData":[OSD([sQuery(id+"F2.wireOp",EDGE,"E2.16.16.2")])],"isStart":false});
            var Q1994;
            Q1994=makeQuery(id+"F3.opExtrude","CAP_EDGE",EDGE,{"disambiguationData":[OSD([sQuery(id+"F2.wireOp",EDGE,"E3.6.28.16")])],"isStart":false});
            var Q1995;
            Q1995=makeQuery(id+"F3.opExtrude","CAP_EDGE",EDGE,{"disambiguationData":[OSD([sQuery(id+"F2.wireOp",EDGE,"E2.15.16.2")])],"isStart":false});
            var Q1996;
            Q1996=makeQuery(id+"F3.opExtrude","CAP_EDGE",EDGE,{"disambiguationData":[OSD([sQuery(id+"F2.wireOp",EDGE,"E3.6.22.16")])],"isStart":false});
            var Q1997;
            Q1997=makeQuery(id+"F3.opExtrude","CAP_EDGE",EDGE,{"disambiguationData":[OSD([sQuery(id+"F2.wireOp",EDGE,"E2.9.16.2")])],"isStart":false});
            var Q1998;
            Q1998=makeQuery(id+"F3.opExtrude","CAP_EDGE",EDGE,{"disambiguationData":[OSD([sQuery(id+"F2.wireOp",EDGE,"E3.6.25.16")])],"isStart":false});
            var Q1999;
            Q1999=makeQuery(id+"F3.opExtrude","CAP_EDGE",EDGE,{"disambiguationData":[OSD([sQuery(id+"F2.wireOp",EDGE,"E2.6.16.2")])],"isStart":false});
            var Q2000;
            Q2000=makeQuery(id+"F3.opExtrude","CAP_EDGE",EDGE,{"disambiguationData":[OSD([sQuery(id+"F2.wireOp",EDGE,"E2.19.16.2")])],"isStart":false});
            var Q2001;
            Q2001=makeQuery(id+"F3.opExtrude","CAP_EDGE",EDGE,{"disambiguationData":[OSD([sQuery(id+"F2.wireOp",EDGE,"E3.6.26.16")])],"isStart":false});
            var Q2002;
            Q2002=makeQuery(id+"F3.opExtrude","CAP_EDGE",EDGE,{"disambiguationData":[OSD([sQuery(id+"F2.wireOp",EDGE,"E2.13.16.2")])],"isStart":false});
            var Q2003;
            Q2003=makeQuery(id+"F3.opExtrude","CAP_EDGE",EDGE,{"disambiguationData":[OSD([sQuery(id+"F2.wireOp",EDGE,"E3.6.20.16")])],"isStart":false});
            var Q2004;
            Q2004=makeQuery(id+"F3.opExtrude","CAP_EDGE",EDGE,{"disambiguationData":[OSD([sQuery(id+"F2.wireOp",EDGE,"E2.7.16.2")])],"isStart":false});
            var Q2005;
            Q2005=makeQuery(id+"F3.opExtrude","CAP_EDGE",EDGE,{"disambiguationData":[OSD([sQuery(id+"F2.wireOp",EDGE,"E2.14.16.2")])],"isStart":false});
            var Q2006;
            Q2006=makeQuery(id+"F3.opExtrude","CAP_EDGE",EDGE,{"disambiguationData":[OSD([sQuery(id+"F2.wireOp",EDGE,"E2.1.16.2")])],"isStart":false});
            var Q2007;
            Q2007=makeQuery(id+"F3.opExtrude","CAP_EDGE",EDGE,{"disambiguationData":[OSD([sQuery(id+"F2.wireOp",EDGE,"E2.8.16.2")])],"isStart":false});
            var Q2008;
            Q2008=makeQuery(id+"F3.opExtrude","CAP_EDGE",EDGE,{"disambiguationData":[OSD([sQuery(id+"F2.wireOp",EDGE,"E3.6.27.16")])],"isStart":false});
            var Q2009;
            Q2009=makeQuery(id+"F3.opExtrude","CAP_EDGE",EDGE,{"disambiguationData":[OSD([sQuery(id+"F2.wireOp",EDGE,"E2.2.16.2")])],"isStart":false});
            var Q2010;
            Q2010=makeQuery(id+"F3.opExtrude","CAP_EDGE",EDGE,{"disambiguationData":[OSD([sQuery(id+"F2.wireOp",EDGE,"E3.6.21.16")])],"isStart":false});
            var Q2011;
            Q2011=makeQuery(id+"F3.opExtrude","CAP_EDGE",EDGE,{"disambiguationData":[OSD([sQuery(id+"F2.wireOp",EDGE,"E2.16.16.1")])],"isStart":false});
            var Q2012;
            Q2012=makeQuery(id+"F3.opExtrude","CAP_EDGE",EDGE,{"disambiguationData":[OSD([sQuery(id+"F2.wireOp",EDGE,"E3.3.28.16")])],"isStart":false});
            var Q2013;
            Q2013=makeQuery(id+"F3.opExtrude","CAP_EDGE",EDGE,{"disambiguationData":[OSD([sQuery(id+"F2.wireOp",EDGE,"E2.9.16.1")])],"isStart":false});
            var Q2014;
            Q2014=makeQuery(id+"F3.opExtrude","CAP_EDGE",EDGE,{"disambiguationData":[OSD([sQuery(id+"F2.wireOp",EDGE,"E2.15.16.1")])],"isStart":false});
            var Q2015;
            Q2015=makeQuery(id+"F3.opExtrude","CAP_EDGE",EDGE,{"disambiguationData":[OSD([sQuery(id+"F2.wireOp",EDGE,"E2.3.16.1")])],"isStart":false});
            var Q2016;
            Q2016=makeQuery(id+"F3.opExtrude","CAP_EDGE",EDGE,{"disambiguationData":[OSD([sQuery(id+"F2.wireOp",EDGE,"E3.3.22.16")])],"isStart":false});
            var Q2017;
            Q2017=makeQuery(id+"F3.opExtrude","CAP_EDGE",EDGE,{"disambiguationData":[OSD([sQuery(id+"F2.wireOp",EDGE,"E2.10.16.1")])],"isStart":false});
            var Q2018;
            Q2018=makeQuery(id+"F3.opExtrude","CAP_EDGE",EDGE,{"disambiguationData":[OSD([sQuery(id+"F2.wireOp",EDGE,"E3.3.29.16")])],"isStart":false});
            var Q2019;
            Q2019=makeQuery(id+"F3.opExtrude","CAP_EDGE",EDGE,{"disambiguationData":[OSD([sQuery(id+"F2.wireOp",EDGE,"E2.4.16.1")])],"isStart":false});
            var Q2020;
            Q2020=makeQuery(id+"F3.opExtrude","CAP_EDGE",EDGE,{"disambiguationData":[OSD([sQuery(id+"F2.wireOp",EDGE,"E3.3.23.16")])],"isStart":false});
            var Q2021;
            Q2021=makeQuery(id+"F3.opExtrude","CAP_EDGE",EDGE,{"disambiguationData":[OSD([sQuery(id+"F2.wireOp",EDGE,"E3.3.20.16")])],"isStart":false});
            var Q2022;
            Q2022=makeQuery(id+"F3.opExtrude","CAP_EDGE",EDGE,{"disambiguationData":[OSD([sQuery(id+"F2.wireOp",EDGE,"E2.7.16.1")])],"isStart":false});
            var Q2023;
            Q2023=makeQuery(id+"F3.opExtrude","CAP_EDGE",EDGE,{"disambiguationData":[OSD([sQuery(id+"F2.wireOp",EDGE,"E2.14.16.1")])],"isStart":false});
            var Q2024;
            Q2024=makeQuery(id+"F3.opExtrude","CAP_EDGE",EDGE,{"disambiguationData":[OSD([sQuery(id+"F2.wireOp",EDGE,"E2.1.16.1")])],"isStart":false});
            var Q2025;
            Q2025=makeQuery(id+"F3.opExtrude","CAP_EDGE",EDGE,{"disambiguationData":[OSD([sQuery(id+"F2.wireOp",EDGE,"E2.8.16.1")])],"isStart":false});
            var Q2026;
            Q2026=makeQuery(id+"F3.opExtrude","CAP_EDGE",EDGE,{"disambiguationData":[OSD([sQuery(id+"F2.wireOp",EDGE,"E3.3.27.16")])],"isStart":false});
            var Q2027;
            Q2027=makeQuery(id+"F3.opExtrude","CAP_EDGE",EDGE,{"disambiguationData":[OSD([sQuery(id+"F2.wireOp",EDGE,"E2.2.16.1")])],"isStart":false});
            var Q2028;
            Q2028=makeQuery(id+"F3.opExtrude","CAP_EDGE",EDGE,{"disambiguationData":[OSD([sQuery(id+"F2.wireOp",EDGE,"E3.3.21.16")])],"isStart":false});
            var Q2029;
            Q2029=makeQuery(id+"F3.opExtrude","CAP_EDGE",EDGE,{"disambiguationData":[OSD([sQuery(id+"F2.wireOp",EDGE,"E2.17.16.1")])],"isStart":false});
            var Q2030;
            Q2030=makeQuery(id+"F3.opExtrude","CAP_EDGE",EDGE,{"disambiguationData":[OSD([sQuery(id+"F2.wireOp",EDGE,"E3.3.24.16")])],"isStart":false});
            var Q2031;
            Q2031=makeQuery(id+"F3.opExtrude","CAP_EDGE",EDGE,{"disambiguationData":[OSD([sQuery(id+"F2.wireOp",EDGE,"E2.11.16.1")])],"isStart":false});
            var Q2032;
            Q2032=makeQuery(id+"F3.opExtrude","CAP_EDGE",EDGE,{"disambiguationData":[OSD([sQuery(id+"F2.wireOp",EDGE,"E2.18.16.1")])],"isStart":false});
            var Q2033;
            Q2033=makeQuery(id+"F3.opExtrude","CAP_EDGE",EDGE,{"disambiguationData":[OSD([sQuery(id+"F2.wireOp",EDGE,"E2.5.16.1")])],"isStart":false});
            var Q2034;
            Q2034=makeQuery(id+"F3.opExtrude","CAP_EDGE",EDGE,{"disambiguationData":[OSD([sQuery(id+"F2.wireOp",EDGE,"E3.3.25.16")])],"isStart":false});
            var Q2035;
            Q2035=makeQuery(id+"F3.opExtrude","CAP_EDGE",EDGE,{"disambiguationData":[OSD([sQuery(id+"F2.wireOp",EDGE,"E2.12.16.1")])],"isStart":false});
            var Q2036;
            Q2036=makeQuery(id+"F3.opExtrude","CAP_EDGE",EDGE,{"disambiguationData":[OSD([sQuery(id+"F2.wireOp",EDGE,"E2.6.16.1")])],"isStart":false});
            var Q2037;
            Q2037=makeQuery(id+"F3.opExtrude","CAP_EDGE",EDGE,{"disambiguationData":[OSD([sQuery(id+"F2.wireOp",EDGE,"E2.19.16.1")])],"isStart":false});
            var Q2038;
            Q2038=makeQuery(id+"F3.opExtrude","CAP_EDGE",EDGE,{"disambiguationData":[OSD([sQuery(id+"F2.wireOp",EDGE,"E3.3.26.16")])],"isStart":false});
            var Q2039;
            Q2039=makeQuery(id+"F3.opExtrude","CAP_EDGE",EDGE,{"disambiguationData":[OSD([sQuery(id+"F2.wireOp",EDGE,"E2.13.16.1")])],"isStart":false});
            var Q2040;
            Q2040=makeQuery(id+"F3.opExtrude","CAP_EDGE",EDGE,{"disambiguationData":[OSD([sQuery(id+"F2.wireOp",EDGE,"E2.0.17.0")])],"isStart":false});
            var Q2041;
            Q2041=makeQuery(id+"F3.opExtrude","CAP_EDGE",EDGE,{"disambiguationData":[OSD([sQuery(id+"F2.wireOp",EDGE,"E2.0.17.2")])],"isStart":false});
            var Q2042;
            Q2042=makeQuery(id+"F3.opExtrude","CAP_EDGE",EDGE,{"disambiguationData":[OSD([sQuery(id+"F2.wireOp",EDGE,"E2.16.17.0")])],"isStart":false});
            var Q2043;
            Q2043=makeQuery(id+"F3.opExtrude","CAP_EDGE",EDGE,{"disambiguationData":[OSD([sQuery(id+"F2.wireOp",EDGE,"E3.0.28.17")])],"isStart":false});
            var Q2044;
            Q2044=makeQuery(id+"F3.opExtrude","CAP_EDGE",EDGE,{"disambiguationData":[OSD([sQuery(id+"F2.wireOp",EDGE,"E2.15.17.0")])],"isStart":false});
            var Q2045;
            Q2045=makeQuery(id+"F3.opExtrude","CAP_EDGE",EDGE,{"disambiguationData":[OSD([sQuery(id+"F2.wireOp",EDGE,"E3.0.22.17")])],"isStart":false});
            var Q2046;
            Q2046=makeQuery(id+"F3.opExtrude","CAP_EDGE",EDGE,{"disambiguationData":[OSD([sQuery(id+"F2.wireOp",EDGE,"E2.9.17.0")])],"isStart":false});
            var Q2047;
            Q2047=makeQuery(id+"F3.opExtrude","CAP_EDGE",EDGE,{"disambiguationData":[OSD([sQuery(id+"F2.wireOp",EDGE,"E2.3.17.0")])],"isStart":false});
            var Q2048;
            Q2048=makeQuery(id+"F3.opExtrude","CAP_EDGE",EDGE,{"disambiguationData":[OSD([sQuery(id+"F2.wireOp",EDGE,"E2.10.17.0")])],"isStart":false});
            var Q2049;
            Q2049=makeQuery(id+"F3.opExtrude","CAP_EDGE",EDGE,{"disambiguationData":[OSD([sQuery(id+"F2.wireOp",EDGE,"E3.0.29.17")])],"isStart":false});
            var Q2050;
            Q2050=makeQuery(id+"F3.opExtrude","CAP_EDGE",EDGE,{"disambiguationData":[OSD([sQuery(id+"F2.wireOp",EDGE,"E2.13.17.0")])],"isStart":false});
            var Q2051;
            Q2051=makeQuery(id+"F3.opExtrude","CAP_EDGE",EDGE,{"disambiguationData":[OSD([sQuery(id+"F2.wireOp",EDGE,"E2.7.17.0")])],"isStart":false});
            var Q2052;
            Q2052=makeQuery(id+"F3.opExtrude","CAP_EDGE",EDGE,{"disambiguationData":[OSD([sQuery(id+"F2.wireOp",EDGE,"E3.0.26.17")])],"isStart":false});
            var Q2053;
            Q2053=makeQuery(id+"F3.opExtrude","CAP_EDGE",EDGE,{"disambiguationData":[OSD([sQuery(id+"F2.wireOp",EDGE,"E2.1.17.0")])],"isStart":false});
            var Q2054;
            Q2054=makeQuery(id+"F3.opExtrude","CAP_EDGE",EDGE,{"disambiguationData":[OSD([sQuery(id+"F2.wireOp",EDGE,"E3.0.20.17")])],"isStart":false});
            var Q2055;
            Q2055=makeQuery(id+"F3.opExtrude","CAP_EDGE",EDGE,{"disambiguationData":[OSD([sQuery(id+"F2.wireOp",EDGE,"E3.0.27.17")])],"isStart":false});
            var Q2056;
            Q2056=makeQuery(id+"F3.opExtrude","CAP_EDGE",EDGE,{"disambiguationData":[OSD([sQuery(id+"F2.wireOp",EDGE,"E2.8.17.0")])],"isStart":false});
            var Q2057;
            Q2057=makeQuery(id+"F3.opExtrude","CAP_EDGE",EDGE,{"disambiguationData":[OSD([sQuery(id+"F2.wireOp",EDGE,"E2.14.17.0")])],"isStart":false});
            var Q2058;
            Q2058=makeQuery(id+"F3.opExtrude","CAP_EDGE",EDGE,{"disambiguationData":[OSD([sQuery(id+"F2.wireOp",EDGE,"E2.2.17.0")])],"isStart":false});
            var Q2059;
            Q2059=makeQuery(id+"F3.opExtrude","CAP_EDGE",EDGE,{"disambiguationData":[OSD([sQuery(id+"F2.wireOp",EDGE,"E3.0.21.17")])],"isStart":false});
            var Q2060;
            Q2060=makeQuery(id+"F3.opExtrude","CAP_EDGE",EDGE,{"disambiguationData":[OSD([sQuery(id+"F2.wireOp",EDGE,"E2.4.17.0")])],"isStart":false});
            var Q2061;
            Q2061=makeQuery(id+"F3.opExtrude","CAP_EDGE",EDGE,{"disambiguationData":[OSD([sQuery(id+"F2.wireOp",EDGE,"E3.0.23.17")])],"isStart":false});
            var Q2062;
            Q2062=makeQuery(id+"F3.opExtrude","CAP_EDGE",EDGE,{"disambiguationData":[OSD([sQuery(id+"F2.wireOp",EDGE,"E2.17.17.0")])],"isStart":false});
            var Q2063;
            Q2063=makeQuery(id+"F3.opExtrude","CAP_EDGE",EDGE,{"disambiguationData":[OSD([sQuery(id+"F2.wireOp",EDGE,"E3.0.24.17")])],"isStart":false});
            var Q2064;
            Q2064=makeQuery(id+"F3.opExtrude","CAP_EDGE",EDGE,{"disambiguationData":[OSD([sQuery(id+"F2.wireOp",EDGE,"E2.11.17.0")])],"isStart":false});
            var Q2065;
            Q2065=makeQuery(id+"F3.opExtrude","CAP_EDGE",EDGE,{"disambiguationData":[OSD([sQuery(id+"F2.wireOp",EDGE,"E2.18.17.0")])],"isStart":false});
            var Q2066;
            Q2066=makeQuery(id+"F3.opExtrude","CAP_EDGE",EDGE,{"disambiguationData":[OSD([sQuery(id+"F2.wireOp",EDGE,"E2.5.17.0")])],"isStart":false});
            var Q2067;
            Q2067=makeQuery(id+"F3.opExtrude","CAP_EDGE",EDGE,{"disambiguationData":[OSD([sQuery(id+"F2.wireOp",EDGE,"E2.12.17.0")])],"isStart":false});
            var Q2068;
            Q2068=makeQuery(id+"F3.opExtrude","CAP_EDGE",EDGE,{"disambiguationData":[OSD([sQuery(id+"F2.wireOp",EDGE,"E3.0.25.17")])],"isStart":false});
            var Q2069;
            Q2069=makeQuery(id+"F3.opExtrude","CAP_EDGE",EDGE,{"disambiguationData":[OSD([sQuery(id+"F2.wireOp",EDGE,"E2.19.17.0")])],"isStart":false});
            var Q2070;
            Q2070=makeQuery(id+"F3.opExtrude","CAP_EDGE",EDGE,{"disambiguationData":[OSD([sQuery(id+"F2.wireOp",EDGE,"E2.6.17.0")])],"isStart":false});
            var Q2071;
            Q2071=makeQuery(id+"F3.opExtrude","CAP_EDGE",EDGE,{"disambiguationData":[OSD([sQuery(id+"F2.wireOp",EDGE,"E2.16.17.2")])],"isStart":false});
            var Q2072;
            Q2072=makeQuery(id+"F3.opExtrude","CAP_EDGE",EDGE,{"disambiguationData":[OSD([sQuery(id+"F2.wireOp",EDGE,"E2.18.17.2")])],"isStart":false});
            var Q2073;
            Q2073=makeQuery(id+"F3.opExtrude","CAP_EDGE",EDGE,{"disambiguationData":[OSD([sQuery(id+"F2.wireOp",EDGE,"E2.5.17.2")])],"isStart":false});
            var Q2074;
            Q2074=makeQuery(id+"F3.opExtrude","CAP_EDGE",EDGE,{"disambiguationData":[OSD([sQuery(id+"F2.wireOp",EDGE,"E2.12.17.2")])],"isStart":false});
            var Q2075;
            Q2075=makeQuery(id+"F3.opExtrude","CAP_EDGE",EDGE,{"disambiguationData":[OSD([sQuery(id+"F2.wireOp",EDGE,"E3.6.25.17")])],"isStart":false});
            var Q2076;
            Q2076=makeQuery(id+"F3.opExtrude","CAP_EDGE",EDGE,{"disambiguationData":[OSD([sQuery(id+"F2.wireOp",EDGE,"E2.19.17.2")])],"isStart":false});
            var Q2077;
            Q2077=makeQuery(id+"F3.opExtrude","CAP_EDGE",EDGE,{"disambiguationData":[OSD([sQuery(id+"F2.wireOp",EDGE,"E2.6.17.2")])],"isStart":false});
            var Q2078;
            Q2078=makeQuery(id+"F3.opExtrude","CAP_EDGE",EDGE,{"disambiguationData":[OSD([sQuery(id+"F2.wireOp",EDGE,"E2.13.17.2")])],"isStart":false});
            var Q2079;
            Q2079=makeQuery(id+"F3.opExtrude","CAP_EDGE",EDGE,{"disambiguationData":[OSD([sQuery(id+"F2.wireOp",EDGE,"E2.7.17.2")])],"isStart":false});
            var Q2080;
            Q2080=makeQuery(id+"F3.opExtrude","CAP_EDGE",EDGE,{"disambiguationData":[OSD([sQuery(id+"F2.wireOp",EDGE,"E3.6.26.17")])],"isStart":false});
            var Q2081;
            Q2081=makeQuery(id+"F3.opExtrude","CAP_EDGE",EDGE,{"disambiguationData":[OSD([sQuery(id+"F2.wireOp",EDGE,"E2.1.17.2")])],"isStart":false});
            var Q2082;
            Q2082=makeQuery(id+"F3.opExtrude","CAP_EDGE",EDGE,{"disambiguationData":[OSD([sQuery(id+"F2.wireOp",EDGE,"E3.6.20.17")])],"isStart":false});
            var Q2083;
            Q2083=makeQuery(id+"F3.opExtrude","CAP_EDGE",EDGE,{"disambiguationData":[OSD([sQuery(id+"F2.wireOp",EDGE,"E3.6.28.17")])],"isStart":false});
            var Q2084;
            Q2084=makeQuery(id+"F3.opExtrude","CAP_EDGE",EDGE,{"disambiguationData":[OSD([sQuery(id+"F2.wireOp",EDGE,"E2.15.17.2")])],"isStart":false});
            var Q2085;
            Q2085=makeQuery(id+"F3.opExtrude","CAP_EDGE",EDGE,{"disambiguationData":[OSD([sQuery(id+"F2.wireOp",EDGE,"E3.6.22.17")])],"isStart":false});
            var Q2086;
            Q2086=makeQuery(id+"F3.opExtrude","CAP_EDGE",EDGE,{"disambiguationData":[OSD([sQuery(id+"F2.wireOp",EDGE,"E2.9.17.2")])],"isStart":false});
            var Q2087;
            Q2087=makeQuery(id+"F3.opExtrude","CAP_EDGE",EDGE,{"disambiguationData":[OSD([sQuery(id+"F2.wireOp",EDGE,"E2.3.17.2")])],"isStart":false});
            var Q2088;
            Q2088=makeQuery(id+"F3.opExtrude","CAP_EDGE",EDGE,{"disambiguationData":[OSD([sQuery(id+"F2.wireOp",EDGE,"E2.10.17.2")])],"isStart":false});
            var Q2089;
            Q2089=makeQuery(id+"F3.opExtrude","CAP_EDGE",EDGE,{"disambiguationData":[OSD([sQuery(id+"F2.wireOp",EDGE,"E2.0.17.1")])],"isStart":false});
            var Q2090;
            Q2090=makeQuery(id+"F3.opExtrude","CAP_EDGE",EDGE,{"disambiguationData":[OSD([sQuery(id+"F2.wireOp",EDGE,"E3.6.29.17")])],"isStart":false});
            var Q2091;
            Q2091=makeQuery(id+"F3.opExtrude","CAP_EDGE",EDGE,{"disambiguationData":[OSD([sQuery(id+"F2.wireOp",EDGE,"E2.4.17.2")])],"isStart":false});
            var Q2092;
            Q2092=makeQuery(id+"F3.opExtrude","CAP_EDGE",EDGE,{"disambiguationData":[OSD([sQuery(id+"F2.wireOp",EDGE,"E3.6.23.17")])],"isStart":false});
            var Q2093;
            Q2093=makeQuery(id+"F3.opExtrude","CAP_EDGE",EDGE,{"disambiguationData":[OSD([sQuery(id+"F2.wireOp",EDGE,"E2.17.17.2")])],"isStart":false});
            var Q2094;
            Q2094=makeQuery(id+"F3.opExtrude","CAP_EDGE",EDGE,{"disambiguationData":[OSD([sQuery(id+"F2.wireOp",EDGE,"E3.6.24.17")])],"isStart":false});
            var Q2095;
            Q2095=makeQuery(id+"F3.opExtrude","CAP_EDGE",EDGE,{"disambiguationData":[OSD([sQuery(id+"F2.wireOp",EDGE,"E2.11.17.2")])],"isStart":false});
            var Q2096;
            Q2096=makeQuery(id+"F3.opExtrude","CAP_EDGE",EDGE,{"disambiguationData":[OSD([sQuery(id+"F2.wireOp",EDGE,"E3.6.27.17")])],"isStart":false});
            var Q2097;
            Q2097=makeQuery(id+"F3.opExtrude","CAP_EDGE",EDGE,{"disambiguationData":[OSD([sQuery(id+"F2.wireOp",EDGE,"E2.14.17.2")])],"isStart":false});
            var Q2098;
            Q2098=makeQuery(id+"F3.opExtrude","CAP_EDGE",EDGE,{"disambiguationData":[OSD([sQuery(id+"F2.wireOp",EDGE,"E3.6.21.17")])],"isStart":false});
            var Q2099;
            Q2099=makeQuery(id+"F3.opExtrude","CAP_EDGE",EDGE,{"disambiguationData":[OSD([sQuery(id+"F2.wireOp",EDGE,"E2.2.17.2")])],"isStart":false});
            var Q2100;
            Q2100=makeQuery(id+"F3.opExtrude","CAP_EDGE",EDGE,{"disambiguationData":[OSD([sQuery(id+"F2.wireOp",EDGE,"E2.8.17.2")])],"isStart":false});
            var Q2101;
            Q2101=makeQuery(id+"F3.opExtrude","CAP_EDGE",EDGE,{"disambiguationData":[OSD([sQuery(id+"F2.wireOp",EDGE,"E2.0.17.3")])],"isStart":false});
            var Q2102;
            Q2102=makeQuery(id+"F3.opExtrude","CAP_EDGE",EDGE,{"disambiguationData":[OSD([sQuery(id+"F2.wireOp",EDGE,"E3.3.22.17")])],"isStart":false});
            var Q2103;
            Q2103=makeQuery(id+"F3.opExtrude","CAP_EDGE",EDGE,{"disambiguationData":[OSD([sQuery(id+"F2.wireOp",EDGE,"E2.9.17.1")])],"isStart":false});
            var Q2104;
            Q2104=makeQuery(id+"F3.opExtrude","CAP_EDGE",EDGE,{"disambiguationData":[OSD([sQuery(id+"F2.wireOp",EDGE,"E2.3.17.1")])],"isStart":false});
            var Q2105;
            Q2105=makeQuery(id+"F3.opExtrude","CAP_EDGE",EDGE,{"disambiguationData":[OSD([sQuery(id+"F2.wireOp",EDGE,"E2.10.17.1")])],"isStart":false});
            var Q2106;
            Q2106=makeQuery(id+"F3.opExtrude","CAP_EDGE",EDGE,{"disambiguationData":[OSD([sQuery(id+"F2.wireOp",EDGE,"E3.3.29.17")])],"isStart":false});
            var Q2107;
            Q2107=makeQuery(id+"F3.opExtrude","CAP_EDGE",EDGE,{"disambiguationData":[OSD([sQuery(id+"F2.wireOp",EDGE,"E2.4.17.1")])],"isStart":false});
            var Q2108;
            Q2108=makeQuery(id+"F3.opExtrude","CAP_EDGE",EDGE,{"disambiguationData":[OSD([sQuery(id+"F2.wireOp",EDGE,"E3.3.23.17")])],"isStart":false});
            var Q2109;
            Q2109=makeQuery(id+"F3.opExtrude","CAP_EDGE",EDGE,{"disambiguationData":[OSD([sQuery(id+"F2.wireOp",EDGE,"E2.17.17.1")])],"isStart":false});
            var Q2110;
            Q2110=makeQuery(id+"F3.opExtrude","CAP_EDGE",EDGE,{"disambiguationData":[OSD([sQuery(id+"F2.wireOp",EDGE,"E3.3.24.17")])],"isStart":false});
            var Q2111;
            Q2111=makeQuery(id+"F3.opExtrude","CAP_EDGE",EDGE,{"disambiguationData":[OSD([sQuery(id+"F2.wireOp",EDGE,"E2.11.17.1")])],"isStart":false});
            var Q2112;
            Q2112=makeQuery(id+"F3.opExtrude","CAP_EDGE",EDGE,{"disambiguationData":[OSD([sQuery(id+"F2.wireOp",EDGE,"E2.18.17.1")])],"isStart":false});
            var Q2113;
            Q2113=makeQuery(id+"F3.opExtrude","CAP_EDGE",EDGE,{"disambiguationData":[OSD([sQuery(id+"F2.wireOp",EDGE,"E2.5.17.1")])],"isStart":false});
            var Q2114;
            Q2114=makeQuery(id+"F3.opExtrude","CAP_EDGE",EDGE,{"disambiguationData":[OSD([sQuery(id+"F2.wireOp",EDGE,"E2.16.17.1")])],"isStart":false});
            var Q2115;
            Q2115=makeQuery(id+"F3.opExtrude","CAP_EDGE",EDGE,{"disambiguationData":[OSD([sQuery(id+"F2.wireOp",EDGE,"E3.3.28.17")])],"isStart":false});
            var Q2116;
            Q2116=makeQuery(id+"F3.opExtrude","CAP_EDGE",EDGE,{"disambiguationData":[OSD([sQuery(id+"F2.wireOp",EDGE,"E2.15.17.1")])],"isStart":false});
            var Q2117;
            Q2117=makeQuery(id+"F3.opExtrude","CAP_EDGE",EDGE,{"disambiguationData":[OSD([sQuery(id+"F2.wireOp",EDGE,"E3.3.21.17")])],"isStart":false});
            var Q2118;
            Q2118=makeQuery(id+"F3.opExtrude","CAP_EDGE",EDGE,{"disambiguationData":[OSD([sQuery(id+"F2.wireOp",EDGE,"E2.2.17.1")])],"isStart":false});
            var Q2119;
            Q2119=makeQuery(id+"F3.opExtrude","CAP_EDGE",EDGE,{"disambiguationData":[OSD([sQuery(id+"F2.wireOp",EDGE,"E2.8.17.1")])],"isStart":false});
            var Q2120;
            Q2120=makeQuery(id+"F3.opExtrude","CAP_EDGE",EDGE,{"disambiguationData":[OSD([sQuery(id+"F2.wireOp",EDGE,"E2.12.17.1")])],"isStart":false});
            var Q2121;
            Q2121=makeQuery(id+"F3.opExtrude","CAP_EDGE",EDGE,{"disambiguationData":[OSD([sQuery(id+"F2.wireOp",EDGE,"E3.3.25.17")])],"isStart":false});
            var Q2122;
            Q2122=makeQuery(id+"F3.opExtrude","CAP_EDGE",EDGE,{"disambiguationData":[OSD([sQuery(id+"F2.wireOp",EDGE,"E2.19.17.1")])],"isStart":false});
            var Q2123;
            Q2123=makeQuery(id+"F3.opExtrude","CAP_EDGE",EDGE,{"disambiguationData":[OSD([sQuery(id+"F2.wireOp",EDGE,"E2.6.17.1")])],"isStart":false});
            var Q2124;
            Q2124=makeQuery(id+"F3.opExtrude","CAP_EDGE",EDGE,{"disambiguationData":[OSD([sQuery(id+"F2.wireOp",EDGE,"E2.13.17.1")])],"isStart":false});
            var Q2125;
            Q2125=makeQuery(id+"F3.opExtrude","CAP_EDGE",EDGE,{"disambiguationData":[OSD([sQuery(id+"F2.wireOp",EDGE,"E2.7.17.1")])],"isStart":false});
            var Q2126;
            Q2126=makeQuery(id+"F3.opExtrude","CAP_EDGE",EDGE,{"disambiguationData":[OSD([sQuery(id+"F2.wireOp",EDGE,"E3.3.26.17")])],"isStart":false});
            var Q2127;
            Q2127=makeQuery(id+"F3.opExtrude","CAP_EDGE",EDGE,{"disambiguationData":[OSD([sQuery(id+"F2.wireOp",EDGE,"E2.1.17.1")])],"isStart":false});
            var Q2128;
            Q2128=makeQuery(id+"F3.opExtrude","CAP_EDGE",EDGE,{"disambiguationData":[OSD([sQuery(id+"F2.wireOp",EDGE,"E3.3.20.17")])],"isStart":false});
            var Q2129;
            Q2129=makeQuery(id+"F3.opExtrude","CAP_EDGE",EDGE,{"disambiguationData":[OSD([sQuery(id+"F2.wireOp",EDGE,"E3.3.27.17")])],"isStart":false});
            var Q2130;
            Q2130=makeQuery(id+"F3.opExtrude","CAP_EDGE",EDGE,{"disambiguationData":[OSD([sQuery(id+"F2.wireOp",EDGE,"E2.14.17.1")])],"isStart":false});
            var Q2131;
            Q2131=makeQuery(id+"F3.opExtrude","CAP_EDGE",EDGE,{"disambiguationData":[OSD([sQuery(id+"F2.wireOp",EDGE,"E2.16.17.3")])],"isStart":false});
            var Q2132;
            Q2132=makeQuery(id+"F3.opExtrude","CAP_EDGE",EDGE,{"disambiguationData":[OSD([sQuery(id+"F2.wireOp",EDGE,"E3.9.28.17")])],"isStart":false});
            var Q2133;
            Q2133=makeQuery(id+"F3.opExtrude","CAP_EDGE",EDGE,{"disambiguationData":[OSD([sQuery(id+"F2.wireOp",EDGE,"E2.15.17.3")])],"isStart":false});
            var Q2134;
            Q2134=makeQuery(id+"F3.opExtrude","CAP_EDGE",EDGE,{"disambiguationData":[OSD([sQuery(id+"F2.wireOp",EDGE,"E3.9.22.17")])],"isStart":false});
            var Q2135;
            Q2135=makeQuery(id+"F3.opExtrude","CAP_EDGE",EDGE,{"disambiguationData":[OSD([sQuery(id+"F2.wireOp",EDGE,"E2.9.17.3")])],"isStart":false});
            var Q2136;
            Q2136=makeQuery(id+"F3.opExtrude","CAP_EDGE",EDGE,{"disambiguationData":[OSD([sQuery(id+"F2.wireOp",EDGE,"E2.3.17.3")])],"isStart":false});
            var Q2137;
            Q2137=makeQuery(id+"F3.opExtrude","CAP_EDGE",EDGE,{"disambiguationData":[OSD([sQuery(id+"F2.wireOp",EDGE,"E2.19.17.3")])],"isStart":false});
            var Q2138;
            Q2138=makeQuery(id+"F3.opExtrude","CAP_EDGE",EDGE,{"disambiguationData":[OSD([sQuery(id+"F2.wireOp",EDGE,"E2.6.17.3")])],"isStart":false});
            var Q2139;
            Q2139=makeQuery(id+"F3.opExtrude","CAP_EDGE",EDGE,{"disambiguationData":[OSD([sQuery(id+"F2.wireOp",EDGE,"E2.13.17.3")])],"isStart":false});
            var Q2140;
            Q2140=makeQuery(id+"F3.opExtrude","CAP_EDGE",EDGE,{"disambiguationData":[OSD([sQuery(id+"F2.wireOp",EDGE,"E2.7.17.3")])],"isStart":false});
            var Q2141;
            Q2141=makeQuery(id+"F3.opExtrude","CAP_EDGE",EDGE,{"disambiguationData":[OSD([sQuery(id+"F2.wireOp",EDGE,"E3.9.26.17")])],"isStart":false});
            var Q2142;
            Q2142=makeQuery(id+"F3.opExtrude","CAP_EDGE",EDGE,{"disambiguationData":[OSD([sQuery(id+"F2.wireOp",EDGE,"E2.1.17.3")])],"isStart":false});
            var Q2143;
            Q2143=makeQuery(id+"F3.opExtrude","CAP_EDGE",EDGE,{"disambiguationData":[OSD([sQuery(id+"F2.wireOp",EDGE,"E3.9.20.17")])],"isStart":false});
            var Q2144;
            Q2144=makeQuery(id+"F3.opExtrude","CAP_EDGE",EDGE,{"disambiguationData":[OSD([sQuery(id+"F2.wireOp",EDGE,"E3.9.27.17")])],"isStart":false});
            var Q2145;
            Q2145=makeQuery(id+"F3.opExtrude","CAP_EDGE",EDGE,{"disambiguationData":[OSD([sQuery(id+"F2.wireOp",EDGE,"E2.14.17.3")])],"isStart":false});
            var Q2146;
            Q2146=makeQuery(id+"F3.opExtrude","CAP_EDGE",EDGE,{"disambiguationData":[OSD([sQuery(id+"F2.wireOp",EDGE,"E3.9.21.17")])],"isStart":false});
            var Q2147;
            Q2147=makeQuery(id+"F3.opExtrude","CAP_EDGE",EDGE,{"disambiguationData":[OSD([sQuery(id+"F2.wireOp",EDGE,"E2.8.17.3")])],"isStart":false});
            var Q2148;
            Q2148=makeQuery(id+"F3.opExtrude","CAP_EDGE",EDGE,{"disambiguationData":[OSD([sQuery(id+"F2.wireOp",EDGE,"E2.2.17.3")])],"isStart":false});
            var Q2149;
            Q2149=makeQuery(id+"F3.opExtrude","CAP_EDGE",EDGE,{"disambiguationData":[OSD([sQuery(id+"F2.wireOp",EDGE,"E3.9.29.17")])],"isStart":false});
            var Q2150;
            Q2150=makeQuery(id+"F3.opExtrude","CAP_EDGE",EDGE,{"disambiguationData":[OSD([sQuery(id+"F2.wireOp",EDGE,"E2.10.17.3")])],"isStart":false});
            var Q2151;
            Q2151=makeQuery(id+"F3.opExtrude","CAP_EDGE",EDGE,{"disambiguationData":[OSD([sQuery(id+"F2.wireOp",EDGE,"E2.4.17.3")])],"isStart":false});
            var Q2152;
            Q2152=makeQuery(id+"F3.opExtrude","CAP_EDGE",EDGE,{"disambiguationData":[OSD([sQuery(id+"F2.wireOp",EDGE,"E3.9.23.17")])],"isStart":false});
            var Q2153;
            Q2153=makeQuery(id+"F3.opExtrude","CAP_EDGE",EDGE,{"disambiguationData":[OSD([sQuery(id+"F2.wireOp",EDGE,"E2.17.17.3")])],"isStart":false});
            var Q2154;
            Q2154=makeQuery(id+"F3.opExtrude","CAP_EDGE",EDGE,{"disambiguationData":[OSD([sQuery(id+"F2.wireOp",EDGE,"E3.9.24.17")])],"isStart":false});
            var Q2155;
            Q2155=makeQuery(id+"F3.opExtrude","CAP_EDGE",EDGE,{"disambiguationData":[OSD([sQuery(id+"F2.wireOp",EDGE,"E2.11.17.3")])],"isStart":false});
            var Q2156;
            Q2156=makeQuery(id+"F3.opExtrude","CAP_EDGE",EDGE,{"disambiguationData":[OSD([sQuery(id+"F2.wireOp",EDGE,"E2.18.17.3")])],"isStart":false});
            var Q2157;
            Q2157=makeQuery(id+"F3.opExtrude","CAP_EDGE",EDGE,{"disambiguationData":[OSD([sQuery(id+"F2.wireOp",EDGE,"E2.5.17.3")])],"isStart":false});
            var Q2158;
            Q2158=makeQuery(id+"F3.opExtrude","CAP_EDGE",EDGE,{"disambiguationData":[OSD([sQuery(id+"F2.wireOp",EDGE,"E2.12.17.3")])],"isStart":false});
            var Q2159;
            Q2159=makeQuery(id+"F3.opExtrude","CAP_EDGE",EDGE,{"disambiguationData":[OSD([sQuery(id+"F2.wireOp",EDGE,"E3.9.25.17")])],"isStart":false});
            var Q2160;
            Q2160=makeQuery(id+"F3.opExtrude","CAP_EDGE",EDGE,{"disambiguationData":[OSD([sQuery(id+"F2.wireOp",EDGE,"E2.0.18.3")])],"isStart":false});
            var Q2161;
            Q2161=makeQuery(id+"F3.opExtrude","CAP_EDGE",EDGE,{"disambiguationData":[OSD([sQuery(id+"F2.wireOp",EDGE,"E2.0.18.0")])],"isStart":false});
            var Q2162;
            Q2162=makeQuery(id+"F3.opExtrude","CAP_EDGE",EDGE,{"disambiguationData":[OSD([sQuery(id+"F2.wireOp",EDGE,"E2.0.18.2")])],"isStart":false});
            var Q2163;
            Q2163=makeQuery(id+"F3.opExtrude","CAP_EDGE",EDGE,{"disambiguationData":[OSD([sQuery(id+"F2.wireOp",EDGE,"E2.16.18.3")])],"isStart":false});
            var Q2164;
            Q2164=makeQuery(id+"F3.opExtrude","CAP_EDGE",EDGE,{"disambiguationData":[OSD([sQuery(id+"F2.wireOp",EDGE,"E3.9.28.18")])],"isStart":false});
            var Q2165;
            Q2165=makeQuery(id+"F3.opExtrude","CAP_EDGE",EDGE,{"disambiguationData":[OSD([sQuery(id+"F2.wireOp",EDGE,"E2.15.18.3")])],"isStart":false});
            var Q2166;
            Q2166=makeQuery(id+"F3.opExtrude","CAP_EDGE",EDGE,{"disambiguationData":[OSD([sQuery(id+"F2.wireOp",EDGE,"E2.12.18.3")])],"isStart":false});
            var Q2167;
            Q2167=makeQuery(id+"F3.opExtrude","CAP_EDGE",EDGE,{"disambiguationData":[OSD([sQuery(id+"F2.wireOp",EDGE,"E3.9.25.18")])],"isStart":false});
            var Q2168;
            Q2168=makeQuery(id+"F3.opExtrude","CAP_EDGE",EDGE,{"disambiguationData":[OSD([sQuery(id+"F2.wireOp",EDGE,"E2.19.18.3")])],"isStart":false});
            var Q2169;
            Q2169=makeQuery(id+"F3.opExtrude","CAP_EDGE",EDGE,{"disambiguationData":[OSD([sQuery(id+"F2.wireOp",EDGE,"E2.6.18.3")])],"isStart":false});
            var Q2170;
            Q2170=makeQuery(id+"F3.opExtrude","CAP_EDGE",EDGE,{"disambiguationData":[OSD([sQuery(id+"F2.wireOp",EDGE,"E2.13.18.3")])],"isStart":false});
            var Q2171;
            Q2171=makeQuery(id+"F3.opExtrude","CAP_EDGE",EDGE,{"disambiguationData":[OSD([sQuery(id+"F2.wireOp",EDGE,"E2.7.18.3")])],"isStart":false});
            var Q2172;
            Q2172=makeQuery(id+"F3.opExtrude","CAP_EDGE",EDGE,{"disambiguationData":[OSD([sQuery(id+"F2.wireOp",EDGE,"E3.9.26.18")])],"isStart":false});
            var Q2173;
            Q2173=makeQuery(id+"F3.opExtrude","CAP_EDGE",EDGE,{"disambiguationData":[OSD([sQuery(id+"F2.wireOp",EDGE,"E2.1.18.3")])],"isStart":false});
            var Q2174;
            Q2174=makeQuery(id+"F3.opExtrude","CAP_EDGE",EDGE,{"disambiguationData":[OSD([sQuery(id+"F2.wireOp",EDGE,"E3.9.20.18")])],"isStart":false});
            var Q2175;
            Q2175=makeQuery(id+"F3.opExtrude","CAP_EDGE",EDGE,{"disambiguationData":[OSD([sQuery(id+"F2.wireOp",EDGE,"E3.9.27.18")])],"isStart":false});
            var Q2176;
            Q2176=makeQuery(id+"F3.opExtrude","CAP_EDGE",EDGE,{"disambiguationData":[OSD([sQuery(id+"F2.wireOp",EDGE,"E2.14.18.3")])],"isStart":false});
            var Q2177;
            Q2177=makeQuery(id+"F3.opExtrude","CAP_EDGE",EDGE,{"disambiguationData":[OSD([sQuery(id+"F2.wireOp",EDGE,"E3.9.22.18")])],"isStart":false});
            var Q2178;
            Q2178=makeQuery(id+"F3.opExtrude","CAP_EDGE",EDGE,{"disambiguationData":[OSD([sQuery(id+"F2.wireOp",EDGE,"E2.9.18.3")])],"isStart":false});
            var Q2179;
            Q2179=makeQuery(id+"F3.opExtrude","CAP_EDGE",EDGE,{"disambiguationData":[OSD([sQuery(id+"F2.wireOp",EDGE,"E2.3.18.3")])],"isStart":false});
            var Q2180;
            Q2180=makeQuery(id+"F3.opExtrude","CAP_EDGE",EDGE,{"disambiguationData":[OSD([sQuery(id+"F2.wireOp",EDGE,"E3.9.29.18")])],"isStart":false});
            var Q2181;
            Q2181=makeQuery(id+"F3.opExtrude","CAP_EDGE",EDGE,{"disambiguationData":[OSD([sQuery(id+"F2.wireOp",EDGE,"E3.9.23.18")])],"isStart":false});
            var Q2182;
            Q2182=makeQuery(id+"F3.opExtrude","CAP_EDGE",EDGE,{"disambiguationData":[OSD([sQuery(id+"F2.wireOp",EDGE,"E2.10.18.3")])],"isStart":false});
            var Q2183;
            Q2183=makeQuery(id+"F3.opExtrude","CAP_EDGE",EDGE,{"disambiguationData":[OSD([sQuery(id+"F2.wireOp",EDGE,"E2.17.18.3")])],"isStart":false});
            var Q2184;
            Q2184=makeQuery(id+"F3.opExtrude","CAP_EDGE",EDGE,{"disambiguationData":[OSD([sQuery(id+"F2.wireOp",EDGE,"E2.4.18.3")])],"isStart":false});
            var Q2185;
            Q2185=makeQuery(id+"F3.opExtrude","CAP_EDGE",EDGE,{"disambiguationData":[OSD([sQuery(id+"F2.wireOp",EDGE,"E3.9.24.18")])],"isStart":false});
            var Q2186;
            Q2186=makeQuery(id+"F3.opExtrude","CAP_EDGE",EDGE,{"disambiguationData":[OSD([sQuery(id+"F2.wireOp",EDGE,"E2.11.18.3")])],"isStart":false});
            var Q2187;
            Q2187=makeQuery(id+"F3.opExtrude","CAP_EDGE",EDGE,{"disambiguationData":[OSD([sQuery(id+"F2.wireOp",EDGE,"E2.18.18.3")])],"isStart":false});
            var Q2188;
            Q2188=makeQuery(id+"F3.opExtrude","CAP_EDGE",EDGE,{"disambiguationData":[OSD([sQuery(id+"F2.wireOp",EDGE,"E2.5.18.3")])],"isStart":false});
            var Q2189;
            Q2189=makeQuery(id+"F3.opExtrude","CAP_EDGE",EDGE,{"disambiguationData":[OSD([sQuery(id+"F2.wireOp",EDGE,"E2.16.18.0")])],"isStart":false});
            var Q2190;
            Q2190=makeQuery(id+"F3.opExtrude","CAP_EDGE",EDGE,{"disambiguationData":[OSD([sQuery(id+"F2.wireOp",EDGE,"E3.0.28.18")])],"isStart":false});
            var Q2191;
            Q2191=makeQuery(id+"F3.opExtrude","CAP_EDGE",EDGE,{"disambiguationData":[OSD([sQuery(id+"F2.wireOp",EDGE,"E2.15.18.0")])],"isStart":false});
            var Q2192;
            Q2192=makeQuery(id+"F3.opExtrude","CAP_EDGE",EDGE,{"disambiguationData":[OSD([sQuery(id+"F2.wireOp",EDGE,"E3.0.22.18")])],"isStart":false});
            var Q2193;
            Q2193=makeQuery(id+"F3.opExtrude","CAP_EDGE",EDGE,{"disambiguationData":[OSD([sQuery(id+"F2.wireOp",EDGE,"E2.9.18.0")])],"isStart":false});
            var Q2194;
            Q2194=makeQuery(id+"F3.opExtrude","CAP_EDGE",EDGE,{"disambiguationData":[OSD([sQuery(id+"F2.wireOp",EDGE,"E3.9.21.18")])],"isStart":false});
            var Q2195;
            Q2195=makeQuery(id+"F3.opExtrude","CAP_EDGE",EDGE,{"disambiguationData":[OSD([sQuery(id+"F2.wireOp",EDGE,"E2.8.18.3")])],"isStart":false});
            var Q2196;
            Q2196=makeQuery(id+"F3.opExtrude","CAP_EDGE",EDGE,{"disambiguationData":[OSD([sQuery(id+"F2.wireOp",EDGE,"E2.2.18.3")])],"isStart":false});
            var Q2197;
            Q2197=makeQuery(id+"F3.opExtrude","CAP_EDGE",EDGE,{"disambiguationData":[OSD([sQuery(id+"F2.wireOp",EDGE,"E3.0.25.18")])],"isStart":false});
            var Q2198;
            Q2198=makeQuery(id+"F3.opExtrude","CAP_EDGE",EDGE,{"disambiguationData":[OSD([sQuery(id+"F2.wireOp",EDGE,"E2.19.18.0")])],"isStart":false});
            var Q2199;
            Q2199=makeQuery(id+"F3.opExtrude","CAP_EDGE",EDGE,{"disambiguationData":[OSD([sQuery(id+"F2.wireOp",EDGE,"E2.6.18.0")])],"isStart":false});
            var Q2200;
            Q2200=makeQuery(id+"F3.opExtrude","CAP_EDGE",EDGE,{"disambiguationData":[OSD([sQuery(id+"F2.wireOp",EDGE,"E2.13.18.0")])],"isStart":false});
            var Q2201;
            Q2201=makeQuery(id+"F3.opExtrude","CAP_EDGE",EDGE,{"disambiguationData":[OSD([sQuery(id+"F2.wireOp",EDGE,"E3.0.20.18")])],"isStart":false});
            var Q2202;
            Q2202=makeQuery(id+"F3.opExtrude","CAP_EDGE",EDGE,{"disambiguationData":[OSD([sQuery(id+"F2.wireOp",EDGE,"E3.0.26.18")])],"isStart":false});
            var Q2203;
            Q2203=makeQuery(id+"F3.opExtrude","CAP_EDGE",EDGE,{"disambiguationData":[OSD([sQuery(id+"F2.wireOp",EDGE,"E2.7.18.0")])],"isStart":false});
            var Q2204;
            Q2204=makeQuery(id+"F3.opExtrude","CAP_EDGE",EDGE,{"disambiguationData":[OSD([sQuery(id+"F2.wireOp",EDGE,"E2.14.18.0")])],"isStart":false});
            var Q2205;
            Q2205=makeQuery(id+"F3.opExtrude","CAP_EDGE",EDGE,{"disambiguationData":[OSD([sQuery(id+"F2.wireOp",EDGE,"E2.1.18.0")])],"isStart":false});
            var Q2206;
            Q2206=makeQuery(id+"F3.opExtrude","CAP_EDGE",EDGE,{"disambiguationData":[OSD([sQuery(id+"F2.wireOp",EDGE,"E2.8.18.0")])],"isStart":false});
            var Q2207;
            Q2207=makeQuery(id+"F3.opExtrude","CAP_EDGE",EDGE,{"disambiguationData":[OSD([sQuery(id+"F2.wireOp",EDGE,"E3.0.27.18")])],"isStart":false});
            var Q2208;
            Q2208=makeQuery(id+"F3.opExtrude","CAP_EDGE",EDGE,{"disambiguationData":[OSD([sQuery(id+"F2.wireOp",EDGE,"E2.2.18.0")])],"isStart":false});
            var Q2209;
            Q2209=makeQuery(id+"F3.opExtrude","CAP_EDGE",EDGE,{"disambiguationData":[OSD([sQuery(id+"F2.wireOp",EDGE,"E3.0.21.18")])],"isStart":false});
            var Q2210;
            Q2210=makeQuery(id+"F3.opExtrude","CAP_EDGE",EDGE,{"disambiguationData":[OSD([sQuery(id+"F2.wireOp",EDGE,"E2.3.18.0")])],"isStart":false});
            var Q2211;
            Q2211=makeQuery(id+"F3.opExtrude","CAP_EDGE",EDGE,{"disambiguationData":[OSD([sQuery(id+"F2.wireOp",EDGE,"E2.10.18.0")])],"isStart":false});
            var Q2212;
            Q2212=makeQuery(id+"F3.opExtrude","CAP_EDGE",EDGE,{"disambiguationData":[OSD([sQuery(id+"F2.wireOp",EDGE,"E3.0.29.18")])],"isStart":false});
            var Q2213;
            Q2213=makeQuery(id+"F3.opExtrude","CAP_EDGE",EDGE,{"disambiguationData":[OSD([sQuery(id+"F2.wireOp",EDGE,"E2.4.18.0")])],"isStart":false});
            var Q2214;
            Q2214=makeQuery(id+"F3.opExtrude","CAP_EDGE",EDGE,{"disambiguationData":[OSD([sQuery(id+"F2.wireOp",EDGE,"E3.0.23.18")])],"isStart":false});
            var Q2215;
            Q2215=makeQuery(id+"F3.opExtrude","CAP_EDGE",EDGE,{"disambiguationData":[OSD([sQuery(id+"F2.wireOp",EDGE,"E2.17.18.0")])],"isStart":false});
            var Q2216;
            Q2216=makeQuery(id+"F3.opExtrude","CAP_EDGE",EDGE,{"disambiguationData":[OSD([sQuery(id+"F2.wireOp",EDGE,"E3.0.24.18")])],"isStart":false});
            var Q2217;
            Q2217=makeQuery(id+"F3.opExtrude","CAP_EDGE",EDGE,{"disambiguationData":[OSD([sQuery(id+"F2.wireOp",EDGE,"E2.11.18.0")])],"isStart":false});
            var Q2218;
            Q2218=makeQuery(id+"F3.opExtrude","CAP_EDGE",EDGE,{"disambiguationData":[OSD([sQuery(id+"F2.wireOp",EDGE,"E2.18.18.0")])],"isStart":false});
            var Q2219;
            Q2219=makeQuery(id+"F3.opExtrude","CAP_EDGE",EDGE,{"disambiguationData":[OSD([sQuery(id+"F2.wireOp",EDGE,"E2.5.18.0")])],"isStart":false});
            var Q2220;
            Q2220=makeQuery(id+"F3.opExtrude","CAP_EDGE",EDGE,{"disambiguationData":[OSD([sQuery(id+"F2.wireOp",EDGE,"E2.12.18.0")])],"isStart":false});
            var Q2221;
            Q2221=makeQuery(id+"F3.opExtrude","CAP_EDGE",EDGE,{"disambiguationData":[OSD([sQuery(id+"F2.wireOp",EDGE,"E2.0.18.1")])],"isStart":false});
            var Q2222;
            Q2222=makeQuery(id+"F3.opExtrude","CAP_EDGE",EDGE,{"disambiguationData":[OSD([sQuery(id+"F2.wireOp",EDGE,"E2.3.18.2")])],"isStart":false});
            var Q2223;
            Q2223=makeQuery(id+"F3.opExtrude","CAP_EDGE",EDGE,{"disambiguationData":[OSD([sQuery(id+"F2.wireOp",EDGE,"E2.10.18.2")])],"isStart":false});
            var Q2224;
            Q2224=makeQuery(id+"F3.opExtrude","CAP_EDGE",EDGE,{"disambiguationData":[OSD([sQuery(id+"F2.wireOp",EDGE,"E3.6.29.18")])],"isStart":false});
            var Q2225;
            Q2225=makeQuery(id+"F3.opExtrude","CAP_EDGE",EDGE,{"disambiguationData":[OSD([sQuery(id+"F2.wireOp",EDGE,"E2.4.18.2")])],"isStart":false});
            var Q2226;
            Q2226=makeQuery(id+"F3.opExtrude","CAP_EDGE",EDGE,{"disambiguationData":[OSD([sQuery(id+"F2.wireOp",EDGE,"E3.6.23.18")])],"isStart":false});
            var Q2227;
            Q2227=makeQuery(id+"F3.opExtrude","CAP_EDGE",EDGE,{"disambiguationData":[OSD([sQuery(id+"F2.wireOp",EDGE,"E2.17.18.2")])],"isStart":false});
            var Q2228;
            Q2228=makeQuery(id+"F3.opExtrude","CAP_EDGE",EDGE,{"disambiguationData":[OSD([sQuery(id+"F2.wireOp",EDGE,"E3.6.24.18")])],"isStart":false});
            var Q2229;
            Q2229=makeQuery(id+"F3.opExtrude","CAP_EDGE",EDGE,{"disambiguationData":[OSD([sQuery(id+"F2.wireOp",EDGE,"E2.11.18.2")])],"isStart":false});
            var Q2230;
            Q2230=makeQuery(id+"F3.opExtrude","CAP_EDGE",EDGE,{"disambiguationData":[OSD([sQuery(id+"F2.wireOp",EDGE,"E2.18.18.2")])],"isStart":false});
            var Q2231;
            Q2231=makeQuery(id+"F3.opExtrude","CAP_EDGE",EDGE,{"disambiguationData":[OSD([sQuery(id+"F2.wireOp",EDGE,"E2.5.18.2")])],"isStart":false});
            var Q2232;
            Q2232=makeQuery(id+"F3.opExtrude","CAP_EDGE",EDGE,{"disambiguationData":[OSD([sQuery(id+"F2.wireOp",EDGE,"E2.12.18.2")])],"isStart":false});
            var Q2233;
            Q2233=makeQuery(id+"F3.opExtrude","CAP_EDGE",EDGE,{"disambiguationData":[OSD([sQuery(id+"F2.wireOp",EDGE,"E2.16.18.2")])],"isStart":false});
            var Q2234;
            Q2234=makeQuery(id+"F3.opExtrude","CAP_EDGE",EDGE,{"disambiguationData":[OSD([sQuery(id+"F2.wireOp",EDGE,"E3.6.28.18")])],"isStart":false});
            var Q2235;
            Q2235=makeQuery(id+"F3.opExtrude","CAP_EDGE",EDGE,{"disambiguationData":[OSD([sQuery(id+"F2.wireOp",EDGE,"E2.15.18.2")])],"isStart":false});
            var Q2236;
            Q2236=makeQuery(id+"F3.opExtrude","CAP_EDGE",EDGE,{"disambiguationData":[OSD([sQuery(id+"F2.wireOp",EDGE,"E3.6.22.18")])],"isStart":false});
            var Q2237;
            Q2237=makeQuery(id+"F3.opExtrude","CAP_EDGE",EDGE,{"disambiguationData":[OSD([sQuery(id+"F2.wireOp",EDGE,"E2.9.18.2")])],"isStart":false});
            var Q2238;
            Q2238=makeQuery(id+"F3.opExtrude","CAP_EDGE",EDGE,{"disambiguationData":[OSD([sQuery(id+"F2.wireOp",EDGE,"E2.2.18.2")])],"isStart":false});
            var Q2239;
            Q2239=makeQuery(id+"F3.opExtrude","CAP_EDGE",EDGE,{"disambiguationData":[OSD([sQuery(id+"F2.wireOp",EDGE,"E3.6.25.18")])],"isStart":false});
            var Q2240;
            Q2240=makeQuery(id+"F3.opExtrude","CAP_EDGE",EDGE,{"disambiguationData":[OSD([sQuery(id+"F2.wireOp",EDGE,"E2.19.18.2")])],"isStart":false});
            var Q2241;
            Q2241=makeQuery(id+"F3.opExtrude","CAP_EDGE",EDGE,{"disambiguationData":[OSD([sQuery(id+"F2.wireOp",EDGE,"E2.6.18.2")])],"isStart":false});
            var Q2242;
            Q2242=makeQuery(id+"F3.opExtrude","CAP_EDGE",EDGE,{"disambiguationData":[OSD([sQuery(id+"F2.wireOp",EDGE,"E2.13.18.2")])],"isStart":false});
            var Q2243;
            Q2243=makeQuery(id+"F3.opExtrude","CAP_EDGE",EDGE,{"disambiguationData":[OSD([sQuery(id+"F2.wireOp",EDGE,"E2.7.18.2")])],"isStart":false});
            var Q2244;
            Q2244=makeQuery(id+"F3.opExtrude","CAP_EDGE",EDGE,{"disambiguationData":[OSD([sQuery(id+"F2.wireOp",EDGE,"E3.6.26.18")])],"isStart":false});
            var Q2245;
            Q2245=makeQuery(id+"F3.opExtrude","CAP_EDGE",EDGE,{"disambiguationData":[OSD([sQuery(id+"F2.wireOp",EDGE,"E2.1.18.2")])],"isStart":false});
            var Q2246;
            Q2246=makeQuery(id+"F3.opExtrude","CAP_EDGE",EDGE,{"disambiguationData":[OSD([sQuery(id+"F2.wireOp",EDGE,"E3.6.20.18")])],"isStart":false});
            var Q2247;
            Q2247=makeQuery(id+"F3.opExtrude","CAP_EDGE",EDGE,{"disambiguationData":[OSD([sQuery(id+"F2.wireOp",EDGE,"E3.6.27.18")])],"isStart":false});
            var Q2248;
            Q2248=makeQuery(id+"F3.opExtrude","CAP_EDGE",EDGE,{"disambiguationData":[OSD([sQuery(id+"F2.wireOp",EDGE,"E2.14.18.2")])],"isStart":false});
            var Q2249;
            Q2249=makeQuery(id+"F3.opExtrude","CAP_EDGE",EDGE,{"disambiguationData":[OSD([sQuery(id+"F2.wireOp",EDGE,"E3.6.21.18")])],"isStart":false});
            var Q2250;
            Q2250=makeQuery(id+"F3.opExtrude","CAP_EDGE",EDGE,{"disambiguationData":[OSD([sQuery(id+"F2.wireOp",EDGE,"E2.8.18.2")])],"isStart":false});
            var Q2251;
            Q2251=makeQuery(id+"F3.opExtrude","CAP_EDGE",EDGE,{"disambiguationData":[OSD([sQuery(id+"F2.wireOp",EDGE,"E2.16.18.1")])],"isStart":false});
            var Q2252;
            Q2252=makeQuery(id+"F3.opExtrude","CAP_EDGE",EDGE,{"disambiguationData":[OSD([sQuery(id+"F2.wireOp",EDGE,"E3.3.28.18")])],"isStart":false});
            var Q2253;
            Q2253=makeQuery(id+"F3.opExtrude","CAP_EDGE",EDGE,{"disambiguationData":[OSD([sQuery(id+"F2.wireOp",EDGE,"E2.15.18.1")])],"isStart":false});
            var Q2254;
            Q2254=makeQuery(id+"F3.opExtrude","CAP_EDGE",EDGE,{"disambiguationData":[OSD([sQuery(id+"F2.wireOp",EDGE,"E3.3.22.18")])],"isStart":false});
            var Q2255;
            Q2255=makeQuery(id+"F3.opExtrude","CAP_EDGE",EDGE,{"disambiguationData":[OSD([sQuery(id+"F2.wireOp",EDGE,"E2.9.18.1")])],"isStart":false});
            var Q2256;
            Q2256=makeQuery(id+"F3.opExtrude","CAP_EDGE",EDGE,{"disambiguationData":[OSD([sQuery(id+"F2.wireOp",EDGE,"E2.3.18.1")])],"isStart":false});
            var Q2257;
            Q2257=makeQuery(id+"F3.opExtrude","CAP_EDGE",EDGE,{"disambiguationData":[OSD([sQuery(id+"F2.wireOp",EDGE,"E2.10.18.1")])],"isStart":false});
            var Q2258;
            Q2258=makeQuery(id+"F3.opExtrude","CAP_EDGE",EDGE,{"disambiguationData":[OSD([sQuery(id+"F2.wireOp",EDGE,"E3.3.29.18")])],"isStart":false});
            var Q2259;
            Q2259=makeQuery(id+"F3.opExtrude","CAP_EDGE",EDGE,{"disambiguationData":[OSD([sQuery(id+"F2.wireOp",EDGE,"E2.4.18.1")])],"isStart":false});
            var Q2260;
            Q2260=makeQuery(id+"F3.opExtrude","CAP_EDGE",EDGE,{"disambiguationData":[OSD([sQuery(id+"F2.wireOp",EDGE,"E3.3.23.18")])],"isStart":false});
            var Q2261;
            Q2261=makeQuery(id+"F3.opExtrude","CAP_EDGE",EDGE,{"disambiguationData":[OSD([sQuery(id+"F2.wireOp",EDGE,"E2.7.18.1")])],"isStart":false});
            var Q2262;
            Q2262=makeQuery(id+"F3.opExtrude","CAP_EDGE",EDGE,{"disambiguationData":[OSD([sQuery(id+"F2.wireOp",EDGE,"E3.3.26.18")])],"isStart":false});
            var Q2263;
            Q2263=makeQuery(id+"F3.opExtrude","CAP_EDGE",EDGE,{"disambiguationData":[OSD([sQuery(id+"F2.wireOp",EDGE,"E2.1.18.1")])],"isStart":false});
            var Q2264;
            Q2264=makeQuery(id+"F3.opExtrude","CAP_EDGE",EDGE,{"disambiguationData":[OSD([sQuery(id+"F2.wireOp",EDGE,"E3.3.20.18")])],"isStart":false});
            var Q2265;
            Q2265=makeQuery(id+"F3.opExtrude","CAP_EDGE",EDGE,{"disambiguationData":[OSD([sQuery(id+"F2.wireOp",EDGE,"E3.3.27.18")])],"isStart":false});
            var Q2266;
            Q2266=makeQuery(id+"F3.opExtrude","CAP_EDGE",EDGE,{"disambiguationData":[OSD([sQuery(id+"F2.wireOp",EDGE,"E2.8.18.1")])],"isStart":false});
            var Q2267;
            Q2267=makeQuery(id+"F3.opExtrude","CAP_EDGE",EDGE,{"disambiguationData":[OSD([sQuery(id+"F2.wireOp",EDGE,"E2.14.18.1")])],"isStart":false});
            var Q2268;
            Q2268=makeQuery(id+"F3.opExtrude","CAP_EDGE",EDGE,{"disambiguationData":[OSD([sQuery(id+"F2.wireOp",EDGE,"E2.2.18.1")])],"isStart":false});
            var Q2269;
            Q2269=makeQuery(id+"F3.opExtrude","CAP_EDGE",EDGE,{"disambiguationData":[OSD([sQuery(id+"F2.wireOp",EDGE,"E3.3.21.18")])],"isStart":false});
            var Q2270;
            Q2270=makeQuery(id+"F3.opExtrude","CAP_EDGE",EDGE,{"disambiguationData":[OSD([sQuery(id+"F2.wireOp",EDGE,"E2.17.18.1")])],"isStart":false});
            var Q2271;
            Q2271=makeQuery(id+"F3.opExtrude","CAP_EDGE",EDGE,{"disambiguationData":[OSD([sQuery(id+"F2.wireOp",EDGE,"E3.3.24.18")])],"isStart":false});
            var Q2272;
            Q2272=makeQuery(id+"F3.opExtrude","CAP_EDGE",EDGE,{"disambiguationData":[OSD([sQuery(id+"F2.wireOp",EDGE,"E2.11.18.1")])],"isStart":false});
            var Q2273;
            Q2273=makeQuery(id+"F3.opExtrude","CAP_EDGE",EDGE,{"disambiguationData":[OSD([sQuery(id+"F2.wireOp",EDGE,"E2.18.18.1")])],"isStart":false});
            var Q2274;
            Q2274=makeQuery(id+"F3.opExtrude","CAP_EDGE",EDGE,{"disambiguationData":[OSD([sQuery(id+"F2.wireOp",EDGE,"E2.5.18.1")])],"isStart":false});
            var Q2275;
            Q2275=makeQuery(id+"F3.opExtrude","CAP_EDGE",EDGE,{"disambiguationData":[OSD([sQuery(id+"F2.wireOp",EDGE,"E2.12.18.1")])],"isStart":false});
            var Q2276;
            Q2276=makeQuery(id+"F3.opExtrude","CAP_EDGE",EDGE,{"disambiguationData":[OSD([sQuery(id+"F2.wireOp",EDGE,"E3.3.25.18")])],"isStart":false});
            var Q2277;
            Q2277=makeQuery(id+"F3.opExtrude","CAP_EDGE",EDGE,{"disambiguationData":[OSD([sQuery(id+"F2.wireOp",EDGE,"E2.19.18.1")])],"isStart":false});
            var Q2278;
            Q2278=makeQuery(id+"F3.opExtrude","CAP_EDGE",EDGE,{"disambiguationData":[OSD([sQuery(id+"F2.wireOp",EDGE,"E2.6.18.1")])],"isStart":false});
            var Q2279;
            Q2279=makeQuery(id+"F3.opExtrude","CAP_EDGE",EDGE,{"disambiguationData":[OSD([sQuery(id+"F2.wireOp",EDGE,"E2.13.18.1")])],"isStart":false});
            var Q2280;
            Q2280=makeQuery(id+"F3.opExtrude","CAP_EDGE",EDGE,{"disambiguationData":[OSD([sQuery(id+"F2.wireOp",EDGE,"E2.0.19.0")])],"isStart":false});
            var Q2281;
            Q2281=makeQuery(id+"F3.opExtrude","CAP_EDGE",EDGE,{"disambiguationData":[OSD([sQuery(id+"F2.wireOp",EDGE,"E2.0.19.2")])],"isStart":false});
            var Q2282;
            Q2282=makeQuery(id+"F3.opExtrude","CAP_EDGE",EDGE,{"disambiguationData":[OSD([sQuery(id+"F2.wireOp",EDGE,"E2.15.19.0")])],"isStart":false});
            var Q2283;
            Q2283=makeQuery(id+"F3.opExtrude","CAP_EDGE",EDGE,{"disambiguationData":[OSD([sQuery(id+"F2.wireOp",EDGE,"E2.16.19.0")])],"isStart":false});
            var Q2284;
            Q2284=makeQuery(id+"F3.opExtrude","CAP_EDGE",EDGE,{"disambiguationData":[OSD([sQuery(id+"F2.wireOp",EDGE,"E3.0.22.19")])],"isStart":false});
            var Q2285;
            Q2285=makeQuery(id+"F3.opExtrude","CAP_EDGE",EDGE,{"disambiguationData":[OSD([sQuery(id+"F2.wireOp",EDGE,"E3.0.28.19")])],"isStart":false});
            var Q2286;
            Q2286=makeQuery(id+"F3.opExtrude","CAP_EDGE",EDGE,{"disambiguationData":[OSD([sQuery(id+"F2.wireOp",EDGE,"E2.9.19.0")])],"isStart":false});
            var Q2287;
            Q2287=makeQuery(id+"F3.opExtrude","CAP_EDGE",EDGE,{"disambiguationData":[OSD([sQuery(id+"F2.wireOp",EDGE,"E2.3.19.0")])],"isStart":false});
            var Q2288;
            Q2288=makeQuery(id+"F3.opExtrude","CAP_EDGE",EDGE,{"disambiguationData":[OSD([sQuery(id+"F2.wireOp",EDGE,"E3.0.29.19")])],"isStart":false});
            var Q2289;
            Q2289=makeQuery(id+"F3.opExtrude","CAP_EDGE",EDGE,{"disambiguationData":[OSD([sQuery(id+"F2.wireOp",EDGE,"E2.13.19.0")])],"isStart":false});
            var Q2290;
            Q2290=makeQuery(id+"F3.opExtrude","CAP_EDGE",EDGE,{"disambiguationData":[OSD([sQuery(id+"F2.wireOp",EDGE,"E2.7.19.0")])],"isStart":false});
            var Q2291;
            Q2291=makeQuery(id+"F3.opExtrude","CAP_EDGE",EDGE,{"disambiguationData":[OSD([sQuery(id+"F2.wireOp",EDGE,"E3.0.26.19")])],"isStart":false});
            var Q2292;
            Q2292=makeQuery(id+"F3.opExtrude","CAP_EDGE",EDGE,{"disambiguationData":[OSD([sQuery(id+"F2.wireOp",EDGE,"E2.1.19.0")])],"isStart":false});
            var Q2293;
            Q2293=makeQuery(id+"F3.opExtrude","CAP_EDGE",EDGE,{"disambiguationData":[OSD([sQuery(id+"F2.wireOp",EDGE,"E3.0.20.19")])],"isStart":false});
            var Q2294;
            Q2294=makeQuery(id+"F3.opExtrude","CAP_EDGE",EDGE,{"disambiguationData":[OSD([sQuery(id+"F2.wireOp",EDGE,"E3.0.27.19")])],"isStart":false});
            var Q2295;
            Q2295=makeQuery(id+"F3.opExtrude","CAP_EDGE",EDGE,{"disambiguationData":[OSD([sQuery(id+"F2.wireOp",EDGE,"E2.14.19.0")])],"isStart":false});
            var Q2296;
            Q2296=makeQuery(id+"F3.opExtrude","CAP_EDGE",EDGE,{"disambiguationData":[OSD([sQuery(id+"F2.wireOp",EDGE,"E3.0.21.19")])],"isStart":false});
            var Q2297;
            Q2297=makeQuery(id+"F3.opExtrude","CAP_EDGE",EDGE,{"disambiguationData":[OSD([sQuery(id+"F2.wireOp",EDGE,"E2.8.19.0")])],"isStart":false});
            var Q2298;
            Q2298=makeQuery(id+"F3.opExtrude","CAP_EDGE",EDGE,{"disambiguationData":[OSD([sQuery(id+"F2.wireOp",EDGE,"E2.2.19.0")])],"isStart":false});
            var Q2299;
            Q2299=makeQuery(id+"F3.opExtrude","CAP_EDGE",EDGE,{"disambiguationData":[OSD([sQuery(id+"F2.wireOp",EDGE,"E3.0.23.19")])],"isStart":false});
            var Q2300;
            Q2300=makeQuery(id+"F3.opExtrude","CAP_EDGE",EDGE,{"disambiguationData":[OSD([sQuery(id+"F2.wireOp",EDGE,"E2.10.19.0")])],"isStart":false});
            var Q2301;
            Q2301=makeQuery(id+"F3.opExtrude","CAP_EDGE",EDGE,{"disambiguationData":[OSD([sQuery(id+"F2.wireOp",EDGE,"E2.17.19.0")])],"isStart":false});
            var Q2302;
            Q2302=makeQuery(id+"F3.opExtrude","CAP_EDGE",EDGE,{"disambiguationData":[OSD([sQuery(id+"F2.wireOp",EDGE,"E2.4.19.0")])],"isStart":false});
            var Q2303;
            Q2303=makeQuery(id+"F3.opExtrude","CAP_EDGE",EDGE,{"disambiguationData":[OSD([sQuery(id+"F2.wireOp",EDGE,"E2.11.19.0")])],"isStart":false});
            var Q2304;
            Q2304=makeQuery(id+"F3.opExtrude","CAP_EDGE",EDGE,{"disambiguationData":[OSD([sQuery(id+"F2.wireOp",EDGE,"E2.18.19.0")])],"isStart":false});
            var Q2305;
            Q2305=makeQuery(id+"F3.opExtrude","CAP_EDGE",EDGE,{"disambiguationData":[OSD([sQuery(id+"F2.wireOp",EDGE,"E3.0.24.19")])],"isStart":false});
            var Q2306;
            Q2306=makeQuery(id+"F3.opExtrude","CAP_EDGE",EDGE,{"disambiguationData":[OSD([sQuery(id+"F2.wireOp",EDGE,"E2.5.19.0")])],"isStart":false});
            var Q2307;
            Q2307=makeQuery(id+"F3.opExtrude","CAP_EDGE",EDGE,{"disambiguationData":[OSD([sQuery(id+"F2.wireOp",EDGE,"E2.12.19.0")])],"isStart":false});
            var Q2308;
            Q2308=makeQuery(id+"F3.opExtrude","CAP_EDGE",EDGE,{"disambiguationData":[OSD([sQuery(id+"F2.wireOp",EDGE,"E3.0.25.19")])],"isStart":false});
            var Q2309;
            Q2309=makeQuery(id+"F3.opExtrude","CAP_EDGE",EDGE,{"disambiguationData":[OSD([sQuery(id+"F2.wireOp",EDGE,"E2.19.19.0")])],"isStart":false});
            var Q2310;
            Q2310=makeQuery(id+"F3.opExtrude","CAP_EDGE",EDGE,{"disambiguationData":[OSD([sQuery(id+"F2.wireOp",EDGE,"E2.6.19.0")])],"isStart":false});
            var Q2311;
            Q2311=makeQuery(id+"F3.opExtrude","CAP_EDGE",EDGE,{"disambiguationData":[OSD([sQuery(id+"F2.wireOp",EDGE,"E2.5.19.2")])],"isStart":false});
            var Q2312;
            Q2312=makeQuery(id+"F3.opExtrude","CAP_EDGE",EDGE,{"disambiguationData":[OSD([sQuery(id+"F2.wireOp",EDGE,"E3.6.24.19")])],"isStart":false});
            var Q2313;
            Q2313=makeQuery(id+"F3.opExtrude","CAP_EDGE",EDGE,{"disambiguationData":[OSD([sQuery(id+"F2.wireOp",EDGE,"E2.12.19.2")])],"isStart":false});
            var Q2314;
            Q2314=makeQuery(id+"F3.opExtrude","CAP_EDGE",EDGE,{"disambiguationData":[OSD([sQuery(id+"F2.wireOp",EDGE,"E2.18.19.2")])],"isStart":false});
            var Q2315;
            Q2315=makeQuery(id+"F3.opExtrude","CAP_EDGE",EDGE,{"disambiguationData":[OSD([sQuery(id+"F2.wireOp",EDGE,"E3.6.25.19")])],"isStart":false});
            var Q2316;
            Q2316=makeQuery(id+"F3.opExtrude","CAP_EDGE",EDGE,{"disambiguationData":[OSD([sQuery(id+"F2.wireOp",EDGE,"E2.19.19.2")])],"isStart":false});
            var Q2317;
            Q2317=makeQuery(id+"F3.opExtrude","CAP_EDGE",EDGE,{"disambiguationData":[OSD([sQuery(id+"F2.wireOp",EDGE,"E2.6.19.2")])],"isStart":false});
            var Q2318;
            Q2318=makeQuery(id+"F3.opExtrude","CAP_EDGE",EDGE,{"disambiguationData":[OSD([sQuery(id+"F2.wireOp",EDGE,"E2.13.19.2")])],"isStart":false});
            var Q2319;
            Q2319=makeQuery(id+"F3.opExtrude","CAP_EDGE",EDGE,{"disambiguationData":[OSD([sQuery(id+"F2.wireOp",EDGE,"E2.7.19.2")])],"isStart":false});
            var Q2320;
            Q2320=makeQuery(id+"F3.opExtrude","CAP_EDGE",EDGE,{"disambiguationData":[OSD([sQuery(id+"F2.wireOp",EDGE,"E3.6.26.19")])],"isStart":false});
            var Q2321;
            Q2321=makeQuery(id+"F3.opExtrude","CAP_EDGE",EDGE,{"disambiguationData":[OSD([sQuery(id+"F2.wireOp",EDGE,"E2.1.19.2")])],"isStart":false});
            var Q2322;
            Q2322=makeQuery(id+"F3.opExtrude","CAP_EDGE",EDGE,{"disambiguationData":[OSD([sQuery(id+"F2.wireOp",EDGE,"E3.6.20.19")])],"isStart":false});
            var Q2323;
            Q2323=makeQuery(id+"F3.opExtrude","CAP_EDGE",EDGE,{"disambiguationData":[OSD([sQuery(id+"F2.wireOp",EDGE,"E2.15.19.2")])],"isStart":false});
            var Q2324;
            Q2324=makeQuery(id+"F3.opExtrude","CAP_EDGE",EDGE,{"disambiguationData":[OSD([sQuery(id+"F2.wireOp",EDGE,"E2.16.19.2")])],"isStart":false});
            var Q2325;
            Q2325=makeQuery(id+"F3.opExtrude","CAP_EDGE",EDGE,{"disambiguationData":[OSD([sQuery(id+"F2.wireOp",EDGE,"E2.9.19.2")])],"isStart":false});
            var Q2326;
            Q2326=makeQuery(id+"F3.opExtrude","CAP_EDGE",EDGE,{"disambiguationData":[OSD([sQuery(id+"F2.wireOp",EDGE,"E3.6.28.19")])],"isStart":false});
            var Q2327;
            Q2327=makeQuery(id+"F3.opExtrude","CAP_EDGE",EDGE,{"disambiguationData":[OSD([sQuery(id+"F2.wireOp",EDGE,"E3.6.22.19")])],"isStart":false});
            var Q2328;
            Q2328=makeQuery(id+"F3.opExtrude","CAP_EDGE",EDGE,{"disambiguationData":[OSD([sQuery(id+"F2.wireOp",EDGE,"E2.3.19.2")])],"isStart":false});
            var Q2329;
            Q2329=makeQuery(id+"F3.opExtrude","CAP_EDGE",EDGE,{"disambiguationData":[OSD([sQuery(id+"F2.wireOp",EDGE,"E3.6.29.19")])],"isStart":false});
            var Q2330;
            Q2330=makeQuery(id+"F3.opExtrude","CAP_EDGE",EDGE,{"disambiguationData":[OSD([sQuery(id+"F2.wireOp",EDGE,"E2.0.19.1")])],"isStart":false});
            var Q2331;
            Q2331=makeQuery(id+"F3.opExtrude","CAP_EDGE",EDGE,{"disambiguationData":[OSD([sQuery(id+"F2.wireOp",EDGE,"E3.6.23.19")])],"isStart":false});
            var Q2332;
            Q2332=makeQuery(id+"F3.opExtrude","CAP_EDGE",EDGE,{"disambiguationData":[OSD([sQuery(id+"F2.wireOp",EDGE,"E2.10.19.2")])],"isStart":false});
            var Q2333;
            Q2333=makeQuery(id+"F3.opExtrude","CAP_EDGE",EDGE,{"disambiguationData":[OSD([sQuery(id+"F2.wireOp",EDGE,"E2.17.19.2")])],"isStart":false});
            var Q2334;
            Q2334=makeQuery(id+"F3.opExtrude","CAP_EDGE",EDGE,{"disambiguationData":[OSD([sQuery(id+"F2.wireOp",EDGE,"E2.4.19.2")])],"isStart":false});
            var Q2335;
            Q2335=makeQuery(id+"F3.opExtrude","CAP_EDGE",EDGE,{"disambiguationData":[OSD([sQuery(id+"F2.wireOp",EDGE,"E2.11.19.2")])],"isStart":false});
            var Q2336;
            Q2336=makeQuery(id+"F3.opExtrude","CAP_EDGE",EDGE,{"disambiguationData":[OSD([sQuery(id+"F2.wireOp",EDGE,"E3.6.27.19")])],"isStart":false});
            var Q2337;
            Q2337=makeQuery(id+"F3.opExtrude","CAP_EDGE",EDGE,{"disambiguationData":[OSD([sQuery(id+"F2.wireOp",EDGE,"E2.14.19.2")])],"isStart":false});
            var Q2338;
            Q2338=makeQuery(id+"F3.opExtrude","CAP_EDGE",EDGE,{"disambiguationData":[OSD([sQuery(id+"F2.wireOp",EDGE,"E3.6.21.19")])],"isStart":false});
            var Q2339;
            Q2339=makeQuery(id+"F3.opExtrude","CAP_EDGE",EDGE,{"disambiguationData":[OSD([sQuery(id+"F2.wireOp",EDGE,"E2.8.19.2")])],"isStart":false});
            var Q2340;
            Q2340=makeQuery(id+"F3.opExtrude","CAP_EDGE",EDGE,{"disambiguationData":[OSD([sQuery(id+"F2.wireOp",EDGE,"E2.2.19.2")])],"isStart":false});
            var Q2341;
            Q2341=makeQuery(id+"F3.opExtrude","CAP_EDGE",EDGE,{"disambiguationData":[OSD([sQuery(id+"F2.wireOp",EDGE,"E2.0.19.3")])],"isStart":false});
            var Q2342;
            Q2342=makeQuery(id+"F3.opExtrude","CAP_EDGE",EDGE,{"disambiguationData":[OSD([sQuery(id+"F2.wireOp",EDGE,"E2.9.19.1")])],"isStart":false});
            var Q2343;
            Q2343=makeQuery(id+"F3.opExtrude","CAP_EDGE",EDGE,{"disambiguationData":[OSD([sQuery(id+"F2.wireOp",EDGE,"E3.3.28.19")])],"isStart":false});
            var Q2344;
            Q2344=makeQuery(id+"F3.opExtrude","CAP_EDGE",EDGE,{"disambiguationData":[OSD([sQuery(id+"F2.wireOp",EDGE,"E3.3.22.19")])],"isStart":false});
            var Q2345;
            Q2345=makeQuery(id+"F3.opExtrude","CAP_EDGE",EDGE,{"disambiguationData":[OSD([sQuery(id+"F2.wireOp",EDGE,"E2.3.19.1")])],"isStart":false});
            var Q2346;
            Q2346=makeQuery(id+"F3.opExtrude","CAP_EDGE",EDGE,{"disambiguationData":[OSD([sQuery(id+"F2.wireOp",EDGE,"E3.3.29.19")])],"isStart":false});
            var Q2347;
            Q2347=makeQuery(id+"F3.opExtrude","CAP_EDGE",EDGE,{"disambiguationData":[OSD([sQuery(id+"F2.wireOp",EDGE,"E3.3.23.19")])],"isStart":false});
            var Q2348;
            Q2348=makeQuery(id+"F3.opExtrude","CAP_EDGE",EDGE,{"disambiguationData":[OSD([sQuery(id+"F2.wireOp",EDGE,"E2.10.19.1")])],"isStart":false});
            var Q2349;
            Q2349=makeQuery(id+"F3.opExtrude","CAP_EDGE",EDGE,{"disambiguationData":[OSD([sQuery(id+"F2.wireOp",EDGE,"E2.17.19.1")])],"isStart":false});
            var Q2350;
            Q2350=makeQuery(id+"F3.opExtrude","CAP_EDGE",EDGE,{"disambiguationData":[OSD([sQuery(id+"F2.wireOp",EDGE,"E2.4.19.1")])],"isStart":false});
            var Q2351;
            Q2351=makeQuery(id+"F3.opExtrude","CAP_EDGE",EDGE,{"disambiguationData":[OSD([sQuery(id+"F2.wireOp",EDGE,"E2.11.19.1")])],"isStart":false});
            var Q2352;
            Q2352=makeQuery(id+"F3.opExtrude","CAP_EDGE",EDGE,{"disambiguationData":[OSD([sQuery(id+"F2.wireOp",EDGE,"E2.5.19.1")])],"isStart":false});
            var Q2353;
            Q2353=makeQuery(id+"F3.opExtrude","CAP_EDGE",EDGE,{"disambiguationData":[OSD([sQuery(id+"F2.wireOp",EDGE,"E3.3.24.19")])],"isStart":false});
            var Q2354;
            Q2354=makeQuery(id+"F3.opExtrude","CAP_EDGE",EDGE,{"disambiguationData":[OSD([sQuery(id+"F2.wireOp",EDGE,"E2.15.19.1")])],"isStart":false});
            var Q2355;
            Q2355=makeQuery(id+"F3.opExtrude","CAP_EDGE",EDGE,{"disambiguationData":[OSD([sQuery(id+"F2.wireOp",EDGE,"E2.16.19.1")])],"isStart":false});
            var Q2356;
            Q2356=makeQuery(id+"F3.opExtrude","CAP_EDGE",EDGE,{"disambiguationData":[OSD([sQuery(id+"F2.wireOp",EDGE,"E3.3.21.19")])],"isStart":false});
            var Q2357;
            Q2357=makeQuery(id+"F3.opExtrude","CAP_EDGE",EDGE,{"disambiguationData":[OSD([sQuery(id+"F2.wireOp",EDGE,"E2.8.19.1")])],"isStart":false});
            var Q2358;
            Q2358=makeQuery(id+"F3.opExtrude","CAP_EDGE",EDGE,{"disambiguationData":[OSD([sQuery(id+"F2.wireOp",EDGE,"E2.2.19.1")])],"isStart":false});
            var Q2359;
            Q2359=makeQuery(id+"F3.opExtrude","CAP_EDGE",EDGE,{"disambiguationData":[OSD([sQuery(id+"F2.wireOp",EDGE,"E2.18.19.1")])],"isStart":false});
            var Q2360;
            Q2360=makeQuery(id+"F3.opExtrude","CAP_EDGE",EDGE,{"disambiguationData":[OSD([sQuery(id+"F2.wireOp",EDGE,"E3.3.25.19")])],"isStart":false});
            var Q2361;
            Q2361=makeQuery(id+"F3.opExtrude","CAP_EDGE",EDGE,{"disambiguationData":[OSD([sQuery(id+"F2.wireOp",EDGE,"E2.12.19.1")])],"isStart":false});
            var Q2362;
            Q2362=makeQuery(id+"F3.opExtrude","CAP_EDGE",EDGE,{"disambiguationData":[OSD([sQuery(id+"F2.wireOp",EDGE,"E2.19.19.1")])],"isStart":false});
            var Q2363;
            Q2363=makeQuery(id+"F3.opExtrude","CAP_EDGE",EDGE,{"disambiguationData":[OSD([sQuery(id+"F2.wireOp",EDGE,"E2.6.19.1")])],"isStart":false});
            var Q2364;
            Q2364=makeQuery(id+"F3.opExtrude","CAP_EDGE",EDGE,{"disambiguationData":[OSD([sQuery(id+"F2.wireOp",EDGE,"E2.13.19.1")])],"isStart":false});
            var Q2365;
            Q2365=makeQuery(id+"F3.opExtrude","CAP_EDGE",EDGE,{"disambiguationData":[OSD([sQuery(id+"F2.wireOp",EDGE,"E2.7.19.1")])],"isStart":false});
            var Q2366;
            Q2366=makeQuery(id+"F3.opExtrude","CAP_EDGE",EDGE,{"disambiguationData":[OSD([sQuery(id+"F2.wireOp",EDGE,"E3.3.26.19")])],"isStart":false});
            var Q2367;
            Q2367=makeQuery(id+"F3.opExtrude","CAP_EDGE",EDGE,{"disambiguationData":[OSD([sQuery(id+"F2.wireOp",EDGE,"E2.1.19.1")])],"isStart":false});
            var Q2368;
            Q2368=makeQuery(id+"F3.opExtrude","CAP_EDGE",EDGE,{"disambiguationData":[OSD([sQuery(id+"F2.wireOp",EDGE,"E3.3.20.19")])],"isStart":false});
            var Q2369;
            Q2369=makeQuery(id+"F3.opExtrude","CAP_EDGE",EDGE,{"disambiguationData":[OSD([sQuery(id+"F2.wireOp",EDGE,"E3.3.27.19")])],"isStart":false});
            var Q2370;
            Q2370=makeQuery(id+"F3.opExtrude","CAP_EDGE",EDGE,{"disambiguationData":[OSD([sQuery(id+"F2.wireOp",EDGE,"E2.14.19.1")])],"isStart":false});
            var Q2371;
            Q2371=makeQuery(id+"F3.opExtrude","CAP_EDGE",EDGE,{"disambiguationData":[OSD([sQuery(id+"F2.wireOp",EDGE,"E2.15.19.3")])],"isStart":false});
            var Q2372;
            Q2372=makeQuery(id+"F3.opExtrude","CAP_EDGE",EDGE,{"disambiguationData":[OSD([sQuery(id+"F2.wireOp",EDGE,"E2.16.19.3")])],"isStart":false});
            var Q2373;
            Q2373=makeQuery(id+"F3.opExtrude","CAP_EDGE",EDGE,{"disambiguationData":[OSD([sQuery(id+"F2.wireOp",EDGE,"E2.9.19.3")])],"isStart":false});
            var Q2374;
            Q2374=makeQuery(id+"F3.opExtrude","CAP_EDGE",EDGE,{"disambiguationData":[OSD([sQuery(id+"F2.wireOp",EDGE,"E3.9.28.19")])],"isStart":false});
            var Q2375;
            Q2375=makeQuery(id+"F3.opExtrude","CAP_EDGE",EDGE,{"disambiguationData":[OSD([sQuery(id+"F2.wireOp",EDGE,"E2.3.19.3")])],"isStart":false});
            var Q2376;
            Q2376=makeQuery(id+"F3.opExtrude","CAP_EDGE",EDGE,{"disambiguationData":[OSD([sQuery(id+"F2.wireOp",EDGE,"E3.9.22.19")])],"isStart":false});
            var Q2377;
            Q2377=makeQuery(id+"F3.opExtrude","CAP_EDGE",EDGE,{"disambiguationData":[OSD([sQuery(id+"F2.wireOp",EDGE,"E2.19.19.3")])],"isStart":false});
            var Q2378;
            Q2378=makeQuery(id+"F3.opExtrude","CAP_EDGE",EDGE,{"disambiguationData":[OSD([sQuery(id+"F2.wireOp",EDGE,"E2.6.19.3")])],"isStart":false});
            var Q2379;
            Q2379=makeQuery(id+"F3.opExtrude","CAP_EDGE",EDGE,{"disambiguationData":[OSD([sQuery(id+"F2.wireOp",EDGE,"E2.13.19.3")])],"isStart":false});
            var Q2380;
            Q2380=makeQuery(id+"F3.opExtrude","CAP_EDGE",EDGE,{"disambiguationData":[OSD([sQuery(id+"F2.wireOp",EDGE,"E2.7.19.3")])],"isStart":false});
            var Q2381;
            Q2381=makeQuery(id+"F3.opExtrude","CAP_EDGE",EDGE,{"disambiguationData":[OSD([sQuery(id+"F2.wireOp",EDGE,"E3.9.26.19")])],"isStart":false});
            var Q2382;
            Q2382=makeQuery(id+"F3.opExtrude","CAP_EDGE",EDGE,{"disambiguationData":[OSD([sQuery(id+"F2.wireOp",EDGE,"E2.1.19.3")])],"isStart":false});
            var Q2383;
            Q2383=makeQuery(id+"F3.opExtrude","CAP_EDGE",EDGE,{"disambiguationData":[OSD([sQuery(id+"F2.wireOp",EDGE,"E3.9.20.19")])],"isStart":false});
            var Q2384;
            Q2384=makeQuery(id+"F3.opExtrude","CAP_EDGE",EDGE,{"disambiguationData":[OSD([sQuery(id+"F2.wireOp",EDGE,"E3.9.27.19")])],"isStart":false});
            var Q2385;
            Q2385=makeQuery(id+"F3.opExtrude","CAP_EDGE",EDGE,{"disambiguationData":[OSD([sQuery(id+"F2.wireOp",EDGE,"E2.14.19.3")])],"isStart":false});
            var Q2386;
            Q2386=makeQuery(id+"F3.opExtrude","CAP_EDGE",EDGE,{"disambiguationData":[OSD([sQuery(id+"F2.wireOp",EDGE,"E3.9.21.19")])],"isStart":false});
            var Q2387;
            Q2387=makeQuery(id+"F3.opExtrude","CAP_EDGE",EDGE,{"disambiguationData":[OSD([sQuery(id+"F2.wireOp",EDGE,"E2.8.19.3")])],"isStart":false});
            var Q2388;
            Q2388=makeQuery(id+"F3.opExtrude","CAP_EDGE",EDGE,{"disambiguationData":[OSD([sQuery(id+"F2.wireOp",EDGE,"E2.2.19.3")])],"isStart":false});
            var Q2389;
            Q2389=makeQuery(id+"F3.opExtrude","CAP_EDGE",EDGE,{"disambiguationData":[OSD([sQuery(id+"F2.wireOp",EDGE,"E3.9.29.19")])],"isStart":false});
            var Q2390;
            Q2390=makeQuery(id+"F3.opExtrude","CAP_EDGE",EDGE,{"disambiguationData":[OSD([sQuery(id+"F2.wireOp",EDGE,"E3.9.23.19")])],"isStart":false});
            var Q2391;
            Q2391=makeQuery(id+"F3.opExtrude","CAP_EDGE",EDGE,{"disambiguationData":[OSD([sQuery(id+"F2.wireOp",EDGE,"E2.10.19.3")])],"isStart":false});
            var Q2392;
            Q2392=makeQuery(id+"F3.opExtrude","CAP_EDGE",EDGE,{"disambiguationData":[OSD([sQuery(id+"F2.wireOp",EDGE,"E2.17.19.3")])],"isStart":false});
            var Q2393;
            Q2393=makeQuery(id+"F3.opExtrude","CAP_EDGE",EDGE,{"disambiguationData":[OSD([sQuery(id+"F2.wireOp",EDGE,"E2.4.19.3")])],"isStart":false});
            var Q2394;
            Q2394=makeQuery(id+"F3.opExtrude","CAP_EDGE",EDGE,{"disambiguationData":[OSD([sQuery(id+"F2.wireOp",EDGE,"E2.11.19.3")])],"isStart":false});
            var Q2395;
            Q2395=makeQuery(id+"F3.opExtrude","CAP_EDGE",EDGE,{"disambiguationData":[OSD([sQuery(id+"F2.wireOp",EDGE,"E2.5.19.3")])],"isStart":false});
            var Q2396;
            Q2396=makeQuery(id+"F3.opExtrude","CAP_EDGE",EDGE,{"disambiguationData":[OSD([sQuery(id+"F2.wireOp",EDGE,"E3.9.24.19")])],"isStart":false});
            var Q2397;
            Q2397=makeQuery(id+"F3.opExtrude","CAP_EDGE",EDGE,{"disambiguationData":[OSD([sQuery(id+"F2.wireOp",EDGE,"E2.18.19.3")])],"isStart":false});
            var Q2398;
            Q2398=makeQuery(id+"F3.opExtrude","CAP_EDGE",EDGE,{"disambiguationData":[OSD([sQuery(id+"F2.wireOp",EDGE,"E3.9.25.19")])],"isStart":false});
            var Q2399;
            Q2399=makeQuery(id+"F3.opExtrude","CAP_EDGE",EDGE,{"disambiguationData":[OSD([sQuery(id+"F2.wireOp",EDGE,"E2.12.19.3")])],"isStart":false});
            fillet(context, id + "F4", {"entities" : qUnion([Q0, Q1, Q2, Q3, Q4, Q5, Q6, Q7, Q8, Q9, Q10, Q11, Q12, Q13, Q14, Q15, Q16, Q17, Q18, Q19, Q20, Q21, Q22, Q23, Q24, Q25, Q26, Q27, Q28, Q29, Q30, Q31, Q32, Q33, Q34, Q35, Q36, Q37, Q38, Q39, Q40, Q41, Q42, Q43, Q44, Q45, Q46, Q47, Q48, Q49, Q50, Q51, Q52, Q53, Q54, Q55, Q56, Q57, Q58, Q59, Q60, Q61, Q62, Q63, Q64, Q65, Q66, Q67, Q68, Q69, Q70, Q71, Q72, Q73, Q74, Q75, Q76, Q77, Q78, Q79, Q80, Q81, Q82, Q83, Q84, Q85, Q86, Q87, Q88, Q89, Q90, Q91, Q92, Q93, Q94, Q95, Q96, Q97, Q98, Q99, Q100, Q101, Q102, Q103, Q104, Q105, Q106, Q107, Q108, Q109, Q110, Q111, Q112, Q113, Q114, Q115, Q116, Q117, Q118, Q119, Q120, Q121, Q122, Q123, Q124, Q125, Q126, Q127, Q128, Q129, Q130, Q131, Q132, Q133, Q134, Q135, Q136, Q137, Q138, Q139, Q140, Q141, Q142, Q143, Q144, Q145, Q146, Q147, Q148, Q149, Q150, Q151, Q152, Q153, Q154, Q155, Q156, Q157, Q158, Q159, Q160, Q161, Q162, Q163, Q164, Q165, Q166, Q167, Q168, Q169, Q170, Q171, Q172, Q173, Q174, Q175, Q176, Q177, Q178, Q179, Q180, Q181, Q182, Q183, Q184, Q185, Q186, Q187, Q188, Q189, Q190, Q191, Q192, Q193, Q194, Q195, Q196, Q197, Q198, Q199, Q200, Q201, Q202, Q203, Q204, Q205, Q206, Q207, Q208, Q209, Q210, Q211, Q212, Q213, Q214, Q215, Q216, Q217, Q218, Q219, Q220, Q221, Q222, Q223, Q224, Q225, Q226, Q227, Q228, Q229, Q230, Q231, Q232, Q233, Q234, Q235, Q236, Q237, Q238, Q239, Q240, Q241, Q242, Q243, Q244, Q245, Q246, Q247, Q248, Q249, Q250, Q251, Q252, Q253, Q254, Q255, Q256, Q257, Q258, Q259, Q260, Q261, Q262, Q263, Q264, Q265, Q266, Q267, Q268, Q269, Q270, Q271, Q272, Q273, Q274, Q275, Q276, Q277, Q278, Q279, Q280, Q281, Q282, Q283, Q284, Q285, Q286, Q287, Q288, Q289, Q290, Q291, Q292, Q293, Q294, Q295, Q296, Q297, Q298, Q299, Q300, Q301, Q302, Q303, Q304, Q305, Q306, Q307, Q308, Q309, Q310, Q311, Q312, Q313, Q314, Q315, Q316, Q317, Q318, Q319, Q320, Q321, Q322, Q323, Q324, Q325, Q326, Q327, Q328, Q329, Q330, Q331, Q332, Q333, Q334, Q335, Q336, Q337, Q338, Q339, Q340, Q341, Q342, Q343, Q344, Q345, Q346, Q347, Q348, Q349, Q350, Q351, Q352, Q353, Q354, Q355, Q356, Q357, Q358, Q359, Q360, Q361, Q362, Q363, Q364, Q365, Q366, Q367, Q368, Q369, Q370, Q371, Q372, Q373, Q374, Q375, Q376, Q377, Q378, Q379, Q380, Q381, Q382, Q383, Q384, Q385, Q386, Q387, Q388, Q389, Q390, Q391, Q392, Q393, Q394, Q395, Q396, Q397, Q398, Q399, Q400, Q401, Q402, Q403, Q404, Q405, Q406, Q407, Q408, Q409, Q410, Q411, Q412, Q413, Q414, Q415, Q416, Q417, Q418, Q419, Q420, Q421, Q422, Q423, Q424, Q425, Q426, Q427, Q428, Q429, Q430, Q431, Q432, Q433, Q434, Q435, Q436, Q437, Q438, Q439, Q440, Q441, Q442, Q443, Q444, Q445, Q446, Q447, Q448, Q449, Q450, Q451, Q452, Q453, Q454, Q455, Q456, Q457, Q458, Q459, Q460, Q461, Q462, Q463, Q464, Q465, Q466, Q467, Q468, Q469, Q470, Q471, Q472, Q473, Q474, Q475, Q476, Q477, Q478, Q479, Q480, Q481, Q482, Q483, Q484, Q485, Q486, Q487, Q488, Q489, Q490, Q491, Q492, Q493, Q494, Q495, Q496, Q497, Q498, Q499, Q500, Q501, Q502, Q503, Q504, Q505, Q506, Q507, Q508, Q509, Q510, Q511, Q512, Q513, Q514, Q515, Q516, Q517, Q518, Q519, Q520, Q521, Q522, Q523, Q524, Q525, Q526, Q527, Q528, Q529, Q530, Q531, Q532, Q533, Q534, Q535, Q536, Q537, Q538, Q539, Q540, Q541, Q542, Q543, Q544, Q545, Q546, Q547, Q548, Q549, Q550, Q551, Q552, Q553, Q554, Q555, Q556, Q557, Q558, Q559, Q560, Q561, Q562, Q563, Q564, Q565, Q566, Q567, Q568, Q569, Q570, Q571, Q572, Q573, Q574, Q575, Q576, Q577, Q578, Q579, Q580, Q581, Q582, Q583, Q584, Q585, Q586, Q587, Q588, Q589, Q590, Q591, Q592, Q593, Q594, Q595, Q596, Q597, Q598, Q599, Q600, Q601, Q602, Q603, Q604, Q605, Q606, Q607, Q608, Q609, Q610, Q611, Q612, Q613, Q614, Q615, Q616, Q617, Q618, Q619, Q620, Q621, Q622, Q623, Q624, Q625, Q626, Q627, Q628, Q629, Q630, Q631, Q632, Q633, Q634, Q635, Q636, Q637, Q638, Q639, Q640, Q641, Q642, Q643, Q644, Q645, Q646, Q647, Q648, Q649, Q650, Q651, Q652, Q653, Q654, Q655, Q656, Q657, Q658, Q659, Q660, Q661, Q662, Q663, Q664, Q665, Q666, Q667, Q668, Q669, Q670, Q671, Q672, Q673, Q674, Q675, Q676, Q677, Q678, Q679, Q680, Q681, Q682, Q683, Q684, Q685, Q686, Q687, Q688, Q689, Q690, Q691, Q692, Q693, Q694, Q695, Q696, Q697, Q698, Q699, Q700, Q701, Q702, Q703, Q704, Q705, Q706, Q707, Q708, Q709, Q710, Q711, Q712, Q713, Q714, Q715, Q716, Q717, Q718, Q719, Q720, Q721, Q722, Q723, Q724, Q725, Q726, Q727, Q728, Q729, Q730, Q731, Q732, Q733, Q734, Q735, Q736, Q737, Q738, Q739, Q740, Q741, Q742, Q743, Q744, Q745, Q746, Q747, Q748, Q749, Q750, Q751, Q752, Q753, Q754, Q755, Q756, Q757, Q758, Q759, Q760, Q761, Q762, Q763, Q764, Q765, Q766, Q767, Q768, Q769, Q770, Q771, Q772, Q773, Q774, Q775, Q776, Q777, Q778, Q779, Q780, Q781, Q782, Q783, Q784, Q785, Q786, Q787, Q788, Q789, Q790, Q791, Q792, Q793, Q794, Q795, Q796, Q797, Q798, Q799, Q800, Q801, Q802, Q803, Q804, Q805, Q806, Q807, Q808, Q809, Q810, Q811, Q812, Q813, Q814, Q815, Q816, Q817, Q818, Q819, Q820, Q821, Q822, Q823, Q824, Q825, Q826, Q827, Q828, Q829, Q830, Q831, Q832, Q833, Q834, Q835, Q836, Q837, Q838, Q839, Q840, Q841, Q842, Q843, Q844, Q845, Q846, Q847, Q848, Q849, Q850, Q851, Q852, Q853, Q854, Q855, Q856, Q857, Q858, Q859, Q860, Q861, Q862, Q863, Q864, Q865, Q866, Q867, Q868, Q869, Q870, Q871, Q872, Q873, Q874, Q875, Q876, Q877, Q878, Q879, Q880, Q881, Q882, Q883, Q884, Q885, Q886, Q887, Q888, Q889, Q890, Q891, Q892, Q893, Q894, Q895, Q896, Q897, Q898, Q899, Q900, Q901, Q902, Q903, Q904, Q905, Q906, Q907, Q908, Q909, Q910, Q911, Q912, Q913, Q914, Q915, Q916, Q917, Q918, Q919, Q920, Q921, Q922, Q923, Q924, Q925, Q926, Q927, Q928, Q929, Q930, Q931, Q932, Q933, Q934, Q935, Q936, Q937, Q938, Q939, Q940, Q941, Q942, Q943, Q944, Q945, Q946, Q947, Q948, Q949, Q950, Q951, Q952, Q953, Q954, Q955, Q956, Q957, Q958, Q959, Q960, Q961, Q962, Q963, Q964, Q965, Q966, Q967, Q968, Q969, Q970, Q971, Q972, Q973, Q974, Q975, Q976, Q977, Q978, Q979, Q980, Q981, Q982, Q983, Q984, Q985, Q986, Q987, Q988, Q989, Q990, Q991, Q992, Q993, Q994, Q995, Q996, Q997, Q998, Q999, Q1000, Q1001, Q1002, Q1003, Q1004, Q1005, Q1006, Q1007, Q1008, Q1009, Q1010, Q1011, Q1012, Q1013, Q1014, Q1015, Q1016, Q1017, Q1018, Q1019, Q1020, Q1021, Q1022, Q1023, Q1024, Q1025, Q1026, Q1027, Q1028, Q1029, Q1030, Q1031, Q1032, Q1033, Q1034, Q1035, Q1036, Q1037, Q1038, Q1039, Q1040, Q1041, Q1042, Q1043, Q1044, Q1045, Q1046, Q1047, Q1048, Q1049, Q1050, Q1051, Q1052, Q1053, Q1054, Q1055, Q1056, Q1057, Q1058, Q1059, Q1060, Q1061, Q1062, Q1063, Q1064, Q1065, Q1066, Q1067, Q1068, Q1069, Q1070, Q1071, Q1072, Q1073, Q1074, Q1075, Q1076, Q1077, Q1078, Q1079, Q1080, Q1081, Q1082, Q1083, Q1084, Q1085, Q1086, Q1087, Q1088, Q1089, Q1090, Q1091, Q1092, Q1093, Q1094, Q1095, Q1096, Q1097, Q1098, Q1099, Q1100, Q1101, Q1102, Q1103, Q1104, Q1105, Q1106, Q1107, Q1108, Q1109, Q1110, Q1111, Q1112, Q1113, Q1114, Q1115, Q1116, Q1117, Q1118, Q1119, Q1120, Q1121, Q1122, Q1123, Q1124, Q1125, Q1126, Q1127, Q1128, Q1129, Q1130, Q1131, Q1132, Q1133, Q1134, Q1135, Q1136, Q1137, Q1138, Q1139, Q1140, Q1141, Q1142, Q1143, Q1144, Q1145, Q1146, Q1147, Q1148, Q1149, Q1150, Q1151, Q1152, Q1153, Q1154, Q1155, Q1156, Q1157, Q1158, Q1159, Q1160, Q1161, Q1162, Q1163, Q1164, Q1165, Q1166, Q1167, Q1168, Q1169, Q1170, Q1171, Q1172, Q1173, Q1174, Q1175, Q1176, Q1177, Q1178, Q1179, Q1180, Q1181, Q1182, Q1183, Q1184, Q1185, Q1186, Q1187, Q1188, Q1189, Q1190, Q1191, Q1192, Q1193, Q1194, Q1195, Q1196, Q1197, Q1198, Q1199, Q1200, Q1201, Q1202, Q1203, Q1204, Q1205, Q1206, Q1207, Q1208, Q1209, Q1210, Q1211, Q1212, Q1213, Q1214, Q1215, Q1216, Q1217, Q1218, Q1219, Q1220, Q1221, Q1222, Q1223, Q1224, Q1225, Q1226, Q1227, Q1228, Q1229, Q1230, Q1231, Q1232, Q1233, Q1234, Q1235, Q1236, Q1237, Q1238, Q1239, Q1240, Q1241, Q1242, Q1243, Q1244, Q1245, Q1246, Q1247, Q1248, Q1249, Q1250, Q1251, Q1252, Q1253, Q1254, Q1255, Q1256, Q1257, Q1258, Q1259, Q1260, Q1261, Q1262, Q1263, Q1264, Q1265, Q1266, Q1267, Q1268, Q1269, Q1270, Q1271, Q1272, Q1273, Q1274, Q1275, Q1276, Q1277, Q1278, Q1279, Q1280, Q1281, Q1282, Q1283, Q1284, Q1285, Q1286, Q1287, Q1288, Q1289, Q1290, Q1291, Q1292, Q1293, Q1294, Q1295, Q1296, Q1297, Q1298, Q1299, Q1300, Q1301, Q1302, Q1303, Q1304, Q1305, Q1306, Q1307, Q1308, Q1309, Q1310, Q1311, Q1312, Q1313, Q1314, Q1315, Q1316, Q1317, Q1318, Q1319, Q1320, Q1321, Q1322, Q1323, Q1324, Q1325, Q1326, Q1327, Q1328, Q1329, Q1330, Q1331, Q1332, Q1333, Q1334, Q1335, Q1336, Q1337, Q1338, Q1339, Q1340, Q1341, Q1342, Q1343, Q1344, Q1345, Q1346, Q1347, Q1348, Q1349, Q1350, Q1351, Q1352, Q1353, Q1354, Q1355, Q1356, Q1357, Q1358, Q1359, Q1360, Q1361, Q1362, Q1363, Q1364, Q1365, Q1366, Q1367, Q1368, Q1369, Q1370, Q1371, Q1372, Q1373, Q1374, Q1375, Q1376, Q1377, Q1378, Q1379, Q1380, Q1381, Q1382, Q1383, Q1384, Q1385, Q1386, Q1387, Q1388, Q1389, Q1390, Q1391, Q1392, Q1393, Q1394, Q1395, Q1396, Q1397, Q1398, Q1399, Q1400, Q1401, Q1402, Q1403, Q1404, Q1405, Q1406, Q1407, Q1408, Q1409, Q1410, Q1411, Q1412, Q1413, Q1414, Q1415, Q1416, Q1417, Q1418, Q1419, Q1420, Q1421, Q1422, Q1423, Q1424, Q1425, Q1426, Q1427, Q1428, Q1429, Q1430, Q1431, Q1432, Q1433, Q1434, Q1435, Q1436, Q1437, Q1438, Q1439, Q1440, Q1441, Q1442, Q1443, Q1444, Q1445, Q1446, Q1447, Q1448, Q1449, Q1450, Q1451, Q1452, Q1453, Q1454, Q1455, Q1456, Q1457, Q1458, Q1459, Q1460, Q1461, Q1462, Q1463, Q1464, Q1465, Q1466, Q1467, Q1468, Q1469, Q1470, Q1471, Q1472, Q1473, Q1474, Q1475, Q1476, Q1477, Q1478, Q1479, Q1480, Q1481, Q1482, Q1483, Q1484, Q1485, Q1486, Q1487, Q1488, Q1489, Q1490, Q1491, Q1492, Q1493, Q1494, Q1495, Q1496, Q1497, Q1498, Q1499, Q1500, Q1501, Q1502, Q1503, Q1504, Q1505, Q1506, Q1507, Q1508, Q1509, Q1510, Q1511, Q1512, Q1513, Q1514, Q1515, Q1516, Q1517, Q1518, Q1519, Q1520, Q1521, Q1522, Q1523, Q1524, Q1525, Q1526, Q1527, Q1528, Q1529, Q1530, Q1531, Q1532, Q1533, Q1534, Q1535, Q1536, Q1537, Q1538, Q1539, Q1540, Q1541, Q1542, Q1543, Q1544, Q1545, Q1546, Q1547, Q1548, Q1549, Q1550, Q1551, Q1552, Q1553, Q1554, Q1555, Q1556, Q1557, Q1558, Q1559, Q1560, Q1561, Q1562, Q1563, Q1564, Q1565, Q1566, Q1567, Q1568, Q1569, Q1570, Q1571, Q1572, Q1573, Q1574, Q1575, Q1576, Q1577, Q1578, Q1579, Q1580, Q1581, Q1582, Q1583, Q1584, Q1585, Q1586, Q1587, Q1588, Q1589, Q1590, Q1591, Q1592, Q1593, Q1594, Q1595, Q1596, Q1597, Q1598, Q1599, Q1600, Q1601, Q1602, Q1603, Q1604, Q1605, Q1606, Q1607, Q1608, Q1609, Q1610, Q1611, Q1612, Q1613, Q1614, Q1615, Q1616, Q1617, Q1618, Q1619, Q1620, Q1621, Q1622, Q1623, Q1624, Q1625, Q1626, Q1627, Q1628, Q1629, Q1630, Q1631, Q1632, Q1633, Q1634, Q1635, Q1636, Q1637, Q1638, Q1639, Q1640, Q1641, Q1642, Q1643, Q1644, Q1645, Q1646, Q1647, Q1648, Q1649, Q1650, Q1651, Q1652, Q1653, Q1654, Q1655, Q1656, Q1657, Q1658, Q1659, Q1660, Q1661, Q1662, Q1663, Q1664, Q1665, Q1666, Q1667, Q1668, Q1669, Q1670, Q1671, Q1672, Q1673, Q1674, Q1675, Q1676, Q1677, Q1678, Q1679, Q1680, Q1681, Q1682, Q1683, Q1684, Q1685, Q1686, Q1687, Q1688, Q1689, Q1690, Q1691, Q1692, Q1693, Q1694, Q1695, Q1696, Q1697, Q1698, Q1699, Q1700, Q1701, Q1702, Q1703, Q1704, Q1705, Q1706, Q1707, Q1708, Q1709, Q1710, Q1711, Q1712, Q1713, Q1714, Q1715, Q1716, Q1717, Q1718, Q1719, Q1720, Q1721, Q1722, Q1723, Q1724, Q1725, Q1726, Q1727, Q1728, Q1729, Q1730, Q1731, Q1732, Q1733, Q1734, Q1735, Q1736, Q1737, Q1738, Q1739, Q1740, Q1741, Q1742, Q1743, Q1744, Q1745, Q1746, Q1747, Q1748, Q1749, Q1750, Q1751, Q1752, Q1753, Q1754, Q1755, Q1756, Q1757, Q1758, Q1759, Q1760, Q1761, Q1762, Q1763, Q1764, Q1765, Q1766, Q1767, Q1768, Q1769, Q1770, Q1771, Q1772, Q1773, Q1774, Q1775, Q1776, Q1777, Q1778, Q1779, Q1780, Q1781, Q1782, Q1783, Q1784, Q1785, Q1786, Q1787, Q1788, Q1789, Q1790, Q1791, Q1792, Q1793, Q1794, Q1795, Q1796, Q1797, Q1798, Q1799, Q1800, Q1801, Q1802, Q1803, Q1804, Q1805, Q1806, Q1807, Q1808, Q1809, Q1810, Q1811, Q1812, Q1813, Q1814, Q1815, Q1816, Q1817, Q1818, Q1819, Q1820, Q1821, Q1822, Q1823, Q1824, Q1825, Q1826, Q1827, Q1828, Q1829, Q1830, Q1831, Q1832, Q1833, Q1834, Q1835, Q1836, Q1837, Q1838, Q1839, Q1840, Q1841, Q1842, Q1843, Q1844, Q1845, Q1846, Q1847, Q1848, Q1849, Q1850, Q1851, Q1852, Q1853, Q1854, Q1855, Q1856, Q1857, Q1858, Q1859, Q1860, Q1861, Q1862, Q1863, Q1864, Q1865, Q1866, Q1867, Q1868, Q1869, Q1870, Q1871, Q1872, Q1873, Q1874, Q1875, Q1876, Q1877, Q1878, Q1879, Q1880, Q1881, Q1882, Q1883, Q1884, Q1885, Q1886, Q1887, Q1888, Q1889, Q1890, Q1891, Q1892, Q1893, Q1894, Q1895, Q1896, Q1897, Q1898, Q1899, Q1900, Q1901, Q1902, Q1903, Q1904, Q1905, Q1906, Q1907, Q1908, Q1909, Q1910, Q1911, Q1912, Q1913, Q1914, Q1915, Q1916, Q1917, Q1918, Q1919, Q1920, Q1921, Q1922, Q1923, Q1924, Q1925, Q1926, Q1927, Q1928, Q1929, Q1930, Q1931, Q1932, Q1933, Q1934, Q1935, Q1936, Q1937, Q1938, Q1939, Q1940, Q1941, Q1942, Q1943, Q1944, Q1945, Q1946, Q1947, Q1948, Q1949, Q1950, Q1951, Q1952, Q1953, Q1954, Q1955, Q1956, Q1957, Q1958, Q1959, Q1960, Q1961, Q1962, Q1963, Q1964, Q1965, Q1966, Q1967, Q1968, Q1969, Q1970, Q1971, Q1972, Q1973, Q1974, Q1975, Q1976, Q1977, Q1978, Q1979, Q1980, Q1981, Q1982, Q1983, Q1984, Q1985, Q1986, Q1987, Q1988, Q1989, Q1990, Q1991, Q1992, Q1993, Q1994, Q1995, Q1996, Q1997, Q1998, Q1999, Q2000, Q2001, Q2002, Q2003, Q2004, Q2005, Q2006, Q2007, Q2008, Q2009, Q2010, Q2011, Q2012, Q2013, Q2014, Q2015, Q2016, Q2017, Q2018, Q2019, Q2020, Q2021, Q2022, Q2023, Q2024, Q2025, Q2026, Q2027, Q2028, Q2029, Q2030, Q2031, Q2032, Q2033, Q2034, Q2035, Q2036, Q2037, Q2038, Q2039, Q2040, Q2041, Q2042, Q2043, Q2044, Q2045, Q2046, Q2047, Q2048, Q2049, Q2050, Q2051, Q2052, Q2053, Q2054, Q2055, Q2056, Q2057, Q2058, Q2059, Q2060, Q2061, Q2062, Q2063, Q2064, Q2065, Q2066, Q2067, Q2068, Q2069, Q2070, Q2071, Q2072, Q2073, Q2074, Q2075, Q2076, Q2077, Q2078, Q2079, Q2080, Q2081, Q2082, Q2083, Q2084, Q2085, Q2086, Q2087, Q2088, Q2089, Q2090, Q2091, Q2092, Q2093, Q2094, Q2095, Q2096, Q2097, Q2098, Q2099, Q2100, Q2101, Q2102, Q2103, Q2104, Q2105, Q2106, Q2107, Q2108, Q2109, Q2110, Q2111, Q2112, Q2113, Q2114, Q2115, Q2116, Q2117, Q2118, Q2119, Q2120, Q2121, Q2122, Q2123, Q2124, Q2125, Q2126, Q2127, Q2128, Q2129, Q2130, Q2131, Q2132, Q2133, Q2134, Q2135, Q2136, Q2137, Q2138, Q2139, Q2140, Q2141, Q2142, Q2143, Q2144, Q2145, Q2146, Q2147, Q2148, Q2149, Q2150, Q2151, Q2152, Q2153, Q2154, Q2155, Q2156, Q2157, Q2158, Q2159, Q2160, Q2161, Q2162, Q2163, Q2164, Q2165, Q2166, Q2167, Q2168, Q2169, Q2170, Q2171, Q2172, Q2173, Q2174, Q2175, Q2176, Q2177, Q2178, Q2179, Q2180, Q2181, Q2182, Q2183, Q2184, Q2185, Q2186, Q2187, Q2188, Q2189, Q2190, Q2191, Q2192, Q2193, Q2194, Q2195, Q2196, Q2197, Q2198, Q2199, Q2200, Q2201, Q2202, Q2203, Q2204, Q2205, Q2206, Q2207, Q2208, Q2209, Q2210, Q2211, Q2212, Q2213, Q2214, Q2215, Q2216, Q2217, Q2218, Q2219, Q2220, Q2221, Q2222, Q2223, Q2224, Q2225, Q2226, Q2227, Q2228, Q2229, Q2230, Q2231, Q2232, Q2233, Q2234, Q2235, Q2236, Q2237, Q2238, Q2239, Q2240, Q2241, Q2242, Q2243, Q2244, Q2245, Q2246, Q2247, Q2248, Q2249, Q2250, Q2251, Q2252, Q2253, Q2254, Q2255, Q2256, Q2257, Q2258, Q2259, Q2260, Q2261, Q2262, Q2263, Q2264, Q2265, Q2266, Q2267, Q2268, Q2269, Q2270, Q2271, Q2272, Q2273, Q2274, Q2275, Q2276, Q2277, Q2278, Q2279, Q2280, Q2281, Q2282, Q2283, Q2284, Q2285, Q2286, Q2287, Q2288, Q2289, Q2290, Q2291, Q2292, Q2293, Q2294, Q2295, Q2296, Q2297, Q2298, Q2299, Q2300, Q2301, Q2302, Q2303, Q2304, Q2305, Q2306, Q2307, Q2308, Q2309, Q2310, Q2311, Q2312, Q2313, Q2314, Q2315, Q2316, Q2317, Q2318, Q2319, Q2320, Q2321, Q2322, Q2323, Q2324, Q2325, Q2326, Q2327, Q2328, Q2329, Q2330, Q2331, Q2332, Q2333, Q2334, Q2335, Q2336, Q2337, Q2338, Q2339, Q2340, Q2341, Q2342, Q2343, Q2344, Q2345, Q2346, Q2347, Q2348, Q2349, Q2350, Q2351, Q2352, Q2353, Q2354, Q2355, Q2356, Q2357, Q2358, Q2359, Q2360, Q2361, Q2362, Q2363, Q2364, Q2365, Q2366, Q2367, Q2368, Q2369, Q2370, Q2371, Q2372, Q2373, Q2374, Q2375, Q2376, Q2377, Q2378, Q2379, Q2380, Q2381, Q2382, Q2383, Q2384, Q2385, Q2386, Q2387, Q2388, Q2389, Q2390, Q2391, Q2392, Q2393, Q2394, Q2395, Q2396, Q2397, Q2398, Q2399]), "radius" : 5.08 * mm, "tangentPropagation" : true, "allowEdgeOverflow" : false});
        }
        {
            var Q0;
            Q0=makeQuery(id+"F3.opExtrude","CAP_FACE",FACE,{"disambiguationData":[OSD([sQuery(id+"F2.wireOp",EDGE,"E2.13.0.0"),sQuery(id+"F2.wireOp",EDGE,"E2.13.0.1"),sQuery(id+"F2.wireOp",EDGE,"E2.13.0.2"),sQuery(id+"F2.wireOp",EDGE,"E2.13.0.3")])],"isStart":false});
            shell(context, id + "F5", {"entities" : qUnion([Q0]), "thickness" : 2.54 * mm});
        }
    });
